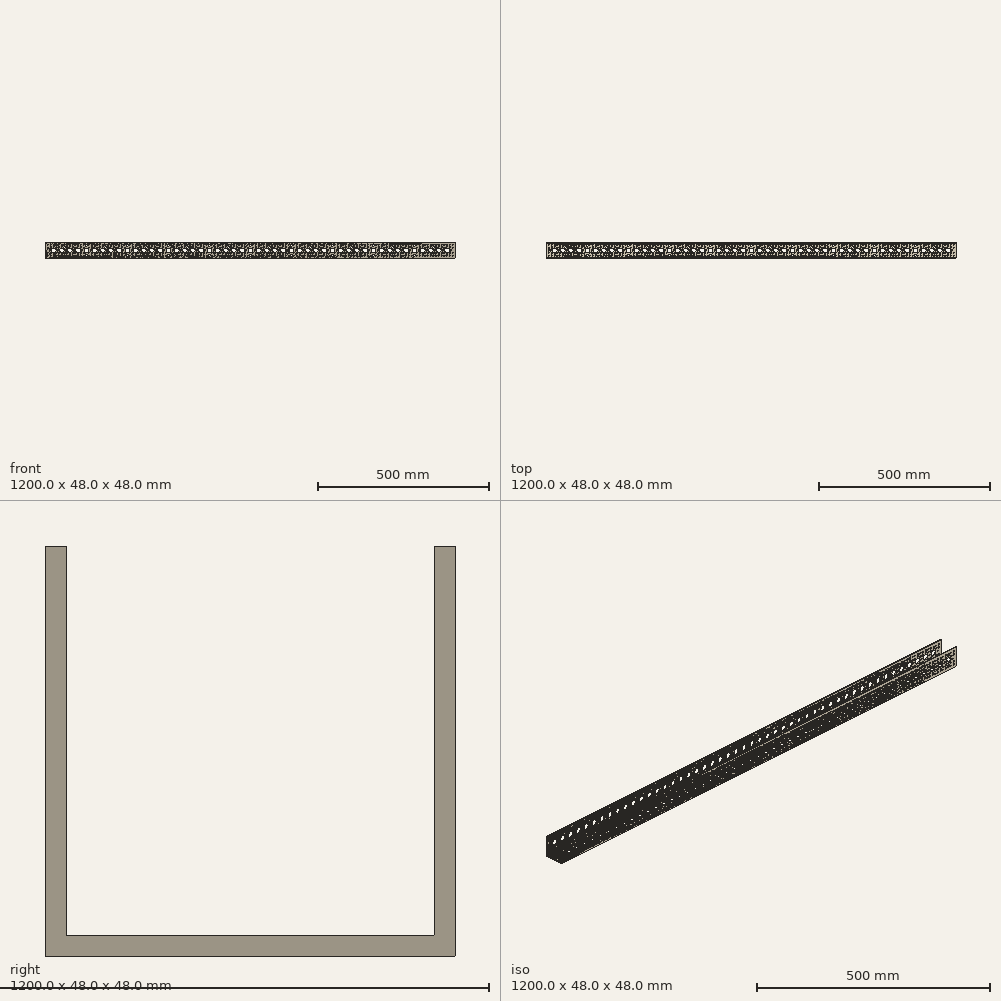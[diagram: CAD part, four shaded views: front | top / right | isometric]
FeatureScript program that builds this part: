
annotation { "Feature Type Name" : "Feature", "Feature Type Description" : "" }
export const myFeature = defineFeature(function(context is Context, id is Id, definition is map)
    precondition{}
    {
        {
            var Q0;
            Q0=qCreatedBy(makeId("Right.planeOp"),FACE);
            var sketch = newSketch(context, id + "F0", { "sketchPlane" : qUnion([Q0])});
            skLineSegment(sketch, "E0.bottom", {"start": v(24, 24) * mm, "end": v(21.5, 24) * mm});
            skLineSegment(sketch, "E0.top", {"start": v(24, -24) * mm, "end": v(-24, -24) * mm});
            skLineSegment(sketch, "E0.left", {"start": v(24, 24) * mm, "end": v(24, -24) * mm});
            skLineSegment(sketch, "E0.right", {"start": v(-24, 24) * mm, "end": v(-24, -24) * mm});
            skPoint(sketch, "E0.middle", {"position": v(0, 0) * mm});
            skLineSegment(sketch, "E1.top", {"start": v(-21.5, -21.5) * mm, "end": v(21.5, -21.5) * mm});
            skLineSegment(sketch, "E1.left", {"start": v(-21.5, 24) * mm, "end": v(-21.5, -21.5) * mm});
            skLineSegment(sketch, "E1.right", {"start": v(21.5, 24) * mm, "end": v(21.5, -21.5) * mm});
            skLineSegment(sketch, "E2.trimOffspring", {"start": v(-21.5, 24) * mm, "end": v(-24, 24) * mm});
            skSolve(sketch);
        }
        {
            var Q0;
            Q0=qSketchRegion(id+"F0",true);
            extrude(context, id + "F1", {"entities" : qUnion([Q0]), "depth" : 48 * mm, "offsetDistance" : 25 * mm});
        }
        {
            var Q0;
            Q0=qSketchRegion(id+"F0",true);
            extrude(context, id + "F2", {"entities" : qUnion([Q0]), "depth" : 72 * mm, "offsetDistance" : 25 * mm});
        }
        {
            var Q0;
            Q0=qSketchRegion(id+"F0",true);
            extrude(context, id + "F3", {"entities" : qUnion([Q0]), "depth" : 96 * mm, "offsetDistance" : 25 * mm});
        }
        {
            var Q0;
            Q0=qSketchRegion(id+"F0",true);
            extrude(context, id + "F4", {"entities" : qUnion([Q0]), "depth" : 120 * mm, "offsetDistance" : 25 * mm});
        }
        {
            var Q0;
            Q0=qSketchRegion(id+"F0",true);
            extrude(context, id + "F5", {"entities" : qUnion([Q0]), "depth" : 144 * mm, "offsetDistance" : 25 * mm});
        }
        {
            var Q0;
            Q0=qSketchRegion(id+"F0",true);
            extrude(context, id + "F6", {"entities" : qUnion([Q0]), "depth" : 192 * mm, "offsetDistance" : 25 * mm});
        }
        {
            var Q0;
            Q0=qSketchRegion(id+"F0",true);
            extrude(context, id + "F7", {"entities" : qUnion([Q0]), "depth" : 240 * mm, "offsetDistance" : 25 * mm});
        }
        {
            var Q0;
            Q0=qSketchRegion(id+"F0",true);
            extrude(context, id + "F8", {"entities" : qUnion([Q0]), "depth" : 288 * mm, "offsetDistance" : 25 * mm});
        }
        {
            var Q0;
            Q0=qSketchRegion(id+"F0",true);
            extrude(context, id + "F9", {"entities" : qUnion([Q0]), "depth" : 336 * mm, "offsetDistance" : 25 * mm});
        }
        {
            var Q0;
            Q0=qSketchRegion(id+"F0",true);
            extrude(context, id + "F10", {"entities" : qUnion([Q0]), "depth" : 384 * mm, "offsetDistance" : 25 * mm});
        }
        {
            var Q0;
            Q0=qSketchRegion(id+"F0",true);
            extrude(context, id + "F11", {"entities" : qUnion([Q0]), "depth" : 432 * mm, "offsetDistance" : 25 * mm});
        }
        {
            var Q0;
            Q0=qSketchRegion(id+"F0",true);
            extrude(context, id + "F12", {"entities" : qUnion([Q0]), "depth" : 528 * mm, "offsetDistance" : 25 * mm});
        }
        {
            var Q0;
            Q0=qSketchRegion(id+"F0",true);
            extrude(context, id + "F13", {"entities" : qUnion([Q0]), "depth" : 624 * mm, "offsetDistance" : 25 * mm});
        }
        {
            var Q0;
            Q0=qSketchRegion(id+"F0",true);
            extrude(context, id + "F14", {"entities" : qUnion([Q0]), "depth" : 720 * mm, "offsetDistance" : 25 * mm});
        }
        {
            var Q0;
            Q0=qSketchRegion(id+"F0",true);
            extrude(context, id + "F15", {"entities" : qUnion([Q0]), "depth" : 816 * mm, "offsetDistance" : 25 * mm});
        }
        {
            var Q0;
            Q0=qSketchRegion(id+"F0",true);
            extrude(context, id + "F16", {"entities" : qUnion([Q0]), "depth" : 912 * mm, "offsetDistance" : 25 * mm});
        }
        {
            var Q0;
            Q0=qSketchRegion(id+"F0",true);
            extrude(context, id + "F17", {"entities" : qUnion([Q0]), "depth" : 1008 * mm, "offsetDistance" : 25 * mm});
        }
        {
            var Q0;
            Q0=qSketchRegion(id+"F0",true);
            extrude(context, id + "F18", {"entities" : qUnion([Q0]), "depth" : 1104 * mm, "offsetDistance" : 25 * mm});
        }
        {
            var Q0;
            Q0=qSketchRegion(id+"F0",true);
            extrude(context, id + "F19", {"entities" : qUnion([Q0]), "depth" : 1200 * mm, "offsetDistance" : 25 * mm});
        }
        {
            var Q0;
            Q0=qCreatedBy(makeId("Front.planeOp"),FACE);
            var sketch = newSketch(context, id + "F20", { "sketchPlane" : qUnion([Q0])});
            skCircle(sketch, "E3", {"center": v(24, 0) * mm, "radius": 7 * mm});
            skLineSegment(sketch, "E4.0", {"start": v(48, 24) * mm, "end": v(0, 24) * mm, "construction": true});
            skLineSegment(sketch, "E5.0", {"start": v(48, -24) * mm, "end": v(0, -24) * mm, "construction": true});
            skLineSegment(sketch, "E6", {"start": v(24, 0) * mm, "end": v(24, 24) * mm, "construction": true});
            skLineSegment(sketch, "E7", {"start": v(24, 24) * mm, "end": v(24, -24) * mm, "construction": true});
            skArc(sketch, "E8", {"start": v(26, 16) * mm, "mid": v(24, 18) * mm, "end": v(22, 16) * mm});
            skArc(sketch, "E9", {"start": v(22, 12) * mm, "mid": v(24, 10) * mm, "end": v(26, 12) * mm});
            skLineSegment(sketch, "E10", {"start": v(22, 16) * mm, "end": v(22, 12) * mm});
            skLineSegment(sketch, "E11", {"start": v(26, 16) * mm, "end": v(26, 12) * mm});
            skArc(sketch, "E12", {"start": v(26, -12) * mm, "mid": v(24, -10) * mm, "end": v(22, -12) * mm});
            skArc(sketch, "E13", {"start": v(22, -16) * mm, "mid": v(24, -18) * mm, "end": v(26, -16) * mm});
            skLineSegment(sketch, "E14", {"start": v(22, -12) * mm, "end": v(22, -16) * mm});
            skLineSegment(sketch, "E15", {"start": v(26, -16) * mm, "end": v(26, -12) * mm});
            skLineSegment(sketch, "E16", {"start": v(0, -24) * mm, "end": v(24, 0) * mm, "construction": true});
            skLineSegment(sketch, "E17", {"start": v(0, 24) * mm, "end": v(24, 0) * mm, "construction": true});
            skArc(sketch, "E18", {"start": v(14.1, -7.07) * mm, "mid": v(14.1, -9.9) * mm, "end": v(16.93, -9.9) * mm});
            skArc(sketch, "E19", {"start": v(17.41, -9.41) * mm, "mid": v(17.41, -6.59) * mm, "end": v(14.59, -6.59) * mm});
            skArc(sketch, "E20", {"start": v(14.59, 6.59) * mm, "mid": v(17.41, 6.59) * mm, "end": v(17.41, 9.41) * mm});
            skArc(sketch, "E21", {"start": v(16.93, 9.9) * mm, "mid": v(14.1, 9.9) * mm, "end": v(14.1, 7.07) * mm});
            skLineSegment(sketch, "E22", {"start": v(15.51, 8.49) * mm, "end": v(16.93, 9.9) * mm, "construction": true});
            skLineSegment(sketch, "E23", {"start": v(15.51, 8.49) * mm, "end": v(14.1, 7.07) * mm, "construction": true});
            skLineSegment(sketch, "E24", {"start": v(17.41, 9.41) * mm, "end": v(14.59, 6.59) * mm, "construction": true});
            skLineSegment(sketch, "E25", {"start": v(16.93, 9.9) * mm, "end": v(17.41, 9.41) * mm});
            skLineSegment(sketch, "E26", {"start": v(14.1, 7.07) * mm, "end": v(14.59, 6.59) * mm});
            skLineSegment(sketch, "E27", {"start": v(14.1, -7.07) * mm, "end": v(16.93, -9.9) * mm, "construction": true});
            skLineSegment(sketch, "E28", {"start": v(14.59, -6.59) * mm, "end": v(17.41, -9.41) * mm, "construction": true});
            skLineSegment(sketch, "E29", {"start": v(14.1, -7.07) * mm, "end": v(14.59, -6.59) * mm});
            skLineSegment(sketch, "E30", {"start": v(16.93, -9.9) * mm, "end": v(17.41, -9.41) * mm});
            skCircle(sketch, "E31", {"center": v(8, 16) * mm, "radius": 2 * mm});
            skCircle(sketch, "E32", {"center": v(8, -16) * mm, "radius": 2 * mm});
            skCircle(sketch, "E33", {"center": v(12, 0) * mm, "radius": 2 * mm});
            skLineSegment(sketch, "E34", {"start": v(8, 16) * mm, "end": v(24, 16) * mm, "construction": true});
            skLineSegment(sketch, "E35", {"start": v(8, -16) * mm, "end": v(24, -16) * mm, "construction": true});
            skCircle(sketch, "E36", {"center": v(16, 16) * mm, "radius": 2 * mm});
            skCircle(sketch, "E37", {"center": v(16, -16) * mm, "radius": 2 * mm});
            skLineSegment(sketch, "E38", {"start": v(0, 0) * mm, "end": v(24, -24) * mm, "construction": true});
            skLineSegment(sketch, "E39", {"start": v(24, 24) * mm, "end": v(0, 0) * mm, "construction": true});
            skArc(sketch, "E40", {"start": v(6.59, 9.41) * mm, "mid": v(6.59, 6.59) * mm, "end": v(9.41, 6.59) * mm});
            skArc(sketch, "E41", {"start": v(9.9, 7.07) * mm, "mid": v(9.9, 9.9) * mm, "end": v(7.07, 9.9) * mm});
            skArc(sketch, "E42", {"start": v(7.07, -9.9) * mm, "mid": v(9.9, -9.9) * mm, "end": v(9.9, -7.07) * mm});
            skArc(sketch, "E43", {"start": v(9.41, -6.59) * mm, "mid": v(6.59, -6.59) * mm, "end": v(6.59, -9.41) * mm});
            skLineSegment(sketch, "E44", {"start": v(7.07, 9.9) * mm, "end": v(9.9, 7.07) * mm, "construction": true});
            skLineSegment(sketch, "E45", {"start": v(6.59, 9.41) * mm, "end": v(9.41, 6.59) * mm, "construction": true});
            skLineSegment(sketch, "E46", {"start": v(9.41, -6.59) * mm, "end": v(6.59, -9.41) * mm, "construction": true});
            skLineSegment(sketch, "E47", {"start": v(9.9, -7.07) * mm, "end": v(7.07, -9.9) * mm, "construction": true});
            skLineSegment(sketch, "E48", {"start": v(9.41, -6.59) * mm, "end": v(9.9, -7.07) * mm});
            skLineSegment(sketch, "E49", {"start": v(6.59, -9.41) * mm, "end": v(7.07, -9.9) * mm});
            skLineSegment(sketch, "E50", {"start": v(7.07, 9.9) * mm, "end": v(6.59, 9.41) * mm});
            skLineSegment(sketch, "E51", {"start": v(9.9, 7.07) * mm, "end": v(9.41, 6.59) * mm});
            skArc(sketch, "E52.1.0.0", {"start": v(50, 16) * mm, "mid": v(48, 18) * mm, "end": v(46, 16) * mm});
            skLineSegment(sketch, "E52.1.0.1", {"start": v(50, 16) * mm, "end": v(50, 12) * mm});
            skLineSegment(sketch, "E52.1.0.2", {"start": v(46, 16) * mm, "end": v(46, 12) * mm});
            skArc(sketch, "E52.1.0.3", {"start": v(46, 12) * mm, "mid": v(48, 10) * mm, "end": v(50, 12) * mm});
            skCircle(sketch, "E52.1.0.4", {"center": v(40, 16) * mm, "radius": 2 * mm});
            skCircle(sketch, "E52.1.0.5", {"center": v(32, 16) * mm, "radius": 2 * mm});
            skArc(sketch, "E52.1.0.6", {"start": v(33.9, 7.07) * mm, "mid": v(33.9, 9.9) * mm, "end": v(31.07, 9.9) * mm});
            skArc(sketch, "E52.1.0.7", {"start": v(30.59, 9.41) * mm, "mid": v(30.59, 6.59) * mm, "end": v(33.41, 6.59) * mm});
            skLineSegment(sketch, "E52.1.0.8", {"start": v(31.07, 9.9) * mm, "end": v(30.59, 9.41) * mm});
            skLineSegment(sketch, "E52.1.0.9", {"start": v(33.9, 7.07) * mm, "end": v(33.41, 6.59) * mm});
            skArc(sketch, "E52.1.0.10", {"start": v(40.93, 9.9) * mm, "mid": v(38.1, 9.9) * mm, "end": v(38.1, 7.07) * mm});
            skLineSegment(sketch, "E52.1.0.11", {"start": v(40.93, 9.9) * mm, "end": v(41.41, 9.41) * mm});
            skArc(sketch, "E52.1.0.12", {"start": v(38.59, 6.59) * mm, "mid": v(41.41, 6.59) * mm, "end": v(41.41, 9.41) * mm});
            skLineSegment(sketch, "E52.1.0.13", {"start": v(38.1, 7.07) * mm, "end": v(38.59, 6.59) * mm});
            skCircle(sketch, "E52.1.0.14", {"center": v(48, 0) * mm, "radius": 7 * mm});
            skArc(sketch, "E52.1.0.15", {"start": v(31.07, -9.9) * mm, "mid": v(33.9, -9.9) * mm, "end": v(33.9, -7.07) * mm});
            skArc(sketch, "E52.1.0.16", {"start": v(33.41, -6.59) * mm, "mid": v(30.59, -6.59) * mm, "end": v(30.59, -9.41) * mm});
            skLineSegment(sketch, "E52.1.0.17", {"start": v(33.41, -6.59) * mm, "end": v(33.9, -7.07) * mm});
            skLineSegment(sketch, "E52.1.0.18", {"start": v(30.59, -9.41) * mm, "end": v(31.07, -9.9) * mm});
            skArc(sketch, "E52.1.0.19", {"start": v(38.1, -7.07) * mm, "mid": v(38.1, -9.9) * mm, "end": v(40.93, -9.9) * mm});
            skLineSegment(sketch, "E52.1.0.20", {"start": v(40.93, -9.9) * mm, "end": v(41.41, -9.41) * mm});
            skArc(sketch, "E52.1.0.21", {"start": v(41.41, -9.41) * mm, "mid": v(41.41, -6.59) * mm, "end": v(38.59, -6.59) * mm});
            skCircle(sketch, "E52.1.0.22", {"center": v(40, -16) * mm, "radius": 2 * mm});
            skCircle(sketch, "E52.1.0.23", {"center": v(32, -16) * mm, "radius": 2 * mm});
            skLineSegment(sketch, "E52.1.0.24", {"start": v(38.1, -7.07) * mm, "end": v(38.59, -6.59) * mm});
            skCircle(sketch, "E52.1.0.25", {"center": v(36, 0) * mm, "radius": 2 * mm});
            skArc(sketch, "E52.1.0.26", {"start": v(50, -12) * mm, "mid": v(48, -10) * mm, "end": v(46, -12) * mm});
            skArc(sketch, "E52.1.0.27", {"start": v(46, -16) * mm, "mid": v(48, -18) * mm, "end": v(50, -16) * mm});
            skLineSegment(sketch, "E52.1.0.28", {"start": v(46, -12) * mm, "end": v(46, -16) * mm});
            skLineSegment(sketch, "E52.1.0.29", {"start": v(50, -16) * mm, "end": v(50, -12) * mm});
            skArc(sketch, "E52.2.0.0", {"start": v(74, 16) * mm, "mid": v(72, 18) * mm, "end": v(70, 16) * mm});
            skLineSegment(sketch, "E52.2.0.1", {"start": v(74, 16) * mm, "end": v(74, 12) * mm});
            skLineSegment(sketch, "E52.2.0.2", {"start": v(70, 16) * mm, "end": v(70, 12) * mm});
            skArc(sketch, "E52.2.0.3", {"start": v(70, 12) * mm, "mid": v(72, 10) * mm, "end": v(74, 12) * mm});
            skCircle(sketch, "E52.2.0.4", {"center": v(64, 16) * mm, "radius": 2 * mm});
            skCircle(sketch, "E52.2.0.5", {"center": v(56, 16) * mm, "radius": 2 * mm});
            skArc(sketch, "E52.2.0.6", {"start": v(57.9, 7.07) * mm, "mid": v(57.9, 9.9) * mm, "end": v(55.07, 9.9) * mm});
            skArc(sketch, "E52.2.0.7", {"start": v(54.59, 9.41) * mm, "mid": v(54.59, 6.59) * mm, "end": v(57.41, 6.59) * mm});
            skLineSegment(sketch, "E52.2.0.8", {"start": v(55.07, 9.9) * mm, "end": v(54.59, 9.41) * mm});
            skLineSegment(sketch, "E52.2.0.9", {"start": v(57.9, 7.07) * mm, "end": v(57.41, 6.59) * mm});
            skArc(sketch, "E52.2.0.10", {"start": v(64.93, 9.9) * mm, "mid": v(62.1, 9.9) * mm, "end": v(62.1, 7.07) * mm});
            skLineSegment(sketch, "E52.2.0.11", {"start": v(64.93, 9.9) * mm, "end": v(65.41, 9.41) * mm});
            skArc(sketch, "E52.2.0.12", {"start": v(62.59, 6.59) * mm, "mid": v(65.41, 6.59) * mm, "end": v(65.41, 9.41) * mm});
            skLineSegment(sketch, "E52.2.0.13", {"start": v(62.1, 7.07) * mm, "end": v(62.59, 6.59) * mm});
            skCircle(sketch, "E52.2.0.14", {"center": v(72, 0) * mm, "radius": 7 * mm});
            skArc(sketch, "E52.2.0.15", {"start": v(55.07, -9.9) * mm, "mid": v(57.9, -9.9) * mm, "end": v(57.9, -7.07) * mm});
            skArc(sketch, "E52.2.0.16", {"start": v(57.41, -6.59) * mm, "mid": v(54.59, -6.59) * mm, "end": v(54.59, -9.41) * mm});
            skLineSegment(sketch, "E52.2.0.17", {"start": v(57.41, -6.59) * mm, "end": v(57.9, -7.07) * mm});
            skLineSegment(sketch, "E52.2.0.18", {"start": v(54.59, -9.41) * mm, "end": v(55.07, -9.9) * mm});
            skArc(sketch, "E52.2.0.19", {"start": v(62.1, -7.07) * mm, "mid": v(62.1, -9.9) * mm, "end": v(64.93, -9.9) * mm});
            skLineSegment(sketch, "E52.2.0.20", {"start": v(64.93, -9.9) * mm, "end": v(65.41, -9.41) * mm});
            skArc(sketch, "E52.2.0.21", {"start": v(65.41, -9.41) * mm, "mid": v(65.41, -6.59) * mm, "end": v(62.59, -6.59) * mm});
            skCircle(sketch, "E52.2.0.22", {"center": v(64, -16) * mm, "radius": 2 * mm});
            skCircle(sketch, "E52.2.0.23", {"center": v(56, -16) * mm, "radius": 2 * mm});
            skLineSegment(sketch, "E52.2.0.24", {"start": v(62.1, -7.07) * mm, "end": v(62.59, -6.59) * mm});
            skCircle(sketch, "E52.2.0.25", {"center": v(60, 0) * mm, "radius": 2 * mm});
            skArc(sketch, "E52.2.0.26", {"start": v(74, -12) * mm, "mid": v(72, -10) * mm, "end": v(70, -12) * mm});
            skArc(sketch, "E52.2.0.27", {"start": v(70, -16) * mm, "mid": v(72, -18) * mm, "end": v(74, -16) * mm});
            skLineSegment(sketch, "E52.2.0.28", {"start": v(70, -12) * mm, "end": v(70, -16) * mm});
            skLineSegment(sketch, "E52.2.0.29", {"start": v(74, -16) * mm, "end": v(74, -12) * mm});
            skArc(sketch, "E52.3.0.0", {"start": v(98, 16) * mm, "mid": v(96, 18) * mm, "end": v(94, 16) * mm});
            skLineSegment(sketch, "E52.3.0.1", {"start": v(98, 16) * mm, "end": v(98, 12) * mm});
            skLineSegment(sketch, "E52.3.0.2", {"start": v(94, 16) * mm, "end": v(94, 12) * mm});
            skArc(sketch, "E52.3.0.3", {"start": v(94, 12) * mm, "mid": v(96, 10) * mm, "end": v(98, 12) * mm});
            skCircle(sketch, "E52.3.0.4", {"center": v(88, 16) * mm, "radius": 2 * mm});
            skCircle(sketch, "E52.3.0.5", {"center": v(80, 16) * mm, "radius": 2 * mm});
            skArc(sketch, "E52.3.0.6", {"start": v(81.9, 7.07) * mm, "mid": v(81.9, 9.9) * mm, "end": v(79.07, 9.9) * mm});
            skArc(sketch, "E52.3.0.7", {"start": v(78.59, 9.41) * mm, "mid": v(78.59, 6.59) * mm, "end": v(81.41, 6.59) * mm});
            skLineSegment(sketch, "E52.3.0.8", {"start": v(79.07, 9.9) * mm, "end": v(78.59, 9.41) * mm});
            skLineSegment(sketch, "E52.3.0.9", {"start": v(81.9, 7.07) * mm, "end": v(81.41, 6.59) * mm});
            skArc(sketch, "E52.3.0.10", {"start": v(88.93, 9.9) * mm, "mid": v(86.1, 9.9) * mm, "end": v(86.1, 7.07) * mm});
            skLineSegment(sketch, "E52.3.0.11", {"start": v(88.93, 9.9) * mm, "end": v(89.41, 9.41) * mm});
            skArc(sketch, "E52.3.0.12", {"start": v(86.59, 6.59) * mm, "mid": v(89.41, 6.59) * mm, "end": v(89.41, 9.41) * mm});
            skLineSegment(sketch, "E52.3.0.13", {"start": v(86.1, 7.07) * mm, "end": v(86.59, 6.59) * mm});
            skCircle(sketch, "E52.3.0.14", {"center": v(96, 0) * mm, "radius": 7 * mm});
            skArc(sketch, "E52.3.0.15", {"start": v(79.07, -9.9) * mm, "mid": v(81.9, -9.9) * mm, "end": v(81.9, -7.07) * mm});
            skArc(sketch, "E52.3.0.16", {"start": v(81.41, -6.59) * mm, "mid": v(78.59, -6.59) * mm, "end": v(78.59, -9.41) * mm});
            skLineSegment(sketch, "E52.3.0.17", {"start": v(81.41, -6.59) * mm, "end": v(81.9, -7.07) * mm});
            skLineSegment(sketch, "E52.3.0.18", {"start": v(78.59, -9.41) * mm, "end": v(79.07, -9.9) * mm});
            skArc(sketch, "E52.3.0.19", {"start": v(86.1, -7.07) * mm, "mid": v(86.1, -9.9) * mm, "end": v(88.93, -9.9) * mm});
            skLineSegment(sketch, "E52.3.0.20", {"start": v(88.93, -9.9) * mm, "end": v(89.41, -9.41) * mm});
            skArc(sketch, "E52.3.0.21", {"start": v(89.41, -9.41) * mm, "mid": v(89.41, -6.59) * mm, "end": v(86.59, -6.59) * mm});
            skCircle(sketch, "E52.3.0.22", {"center": v(88, -16) * mm, "radius": 2 * mm});
            skCircle(sketch, "E52.3.0.23", {"center": v(80, -16) * mm, "radius": 2 * mm});
            skLineSegment(sketch, "E52.3.0.24", {"start": v(86.1, -7.07) * mm, "end": v(86.59, -6.59) * mm});
            skCircle(sketch, "E52.3.0.25", {"center": v(84, 0) * mm, "radius": 2 * mm});
            skArc(sketch, "E52.3.0.26", {"start": v(98, -12) * mm, "mid": v(96, -10) * mm, "end": v(94, -12) * mm});
            skArc(sketch, "E52.3.0.27", {"start": v(94, -16) * mm, "mid": v(96, -18) * mm, "end": v(98, -16) * mm});
            skLineSegment(sketch, "E52.3.0.28", {"start": v(94, -12) * mm, "end": v(94, -16) * mm});
            skLineSegment(sketch, "E52.3.0.29", {"start": v(98, -16) * mm, "end": v(98, -12) * mm});
            skArc(sketch, "E52.4.0.0", {"start": v(122, 16) * mm, "mid": v(120, 18) * mm, "end": v(118, 16) * mm});
            skLineSegment(sketch, "E52.4.0.1", {"start": v(122, 16) * mm, "end": v(122, 12) * mm});
            skLineSegment(sketch, "E52.4.0.2", {"start": v(118, 16) * mm, "end": v(118, 12) * mm});
            skArc(sketch, "E52.4.0.3", {"start": v(118, 12) * mm, "mid": v(120, 10) * mm, "end": v(122, 12) * mm});
            skCircle(sketch, "E52.4.0.4", {"center": v(112, 16) * mm, "radius": 2 * mm});
            skCircle(sketch, "E52.4.0.5", {"center": v(104, 16) * mm, "radius": 2 * mm});
            skArc(sketch, "E52.4.0.6", {"start": v(105.9, 7.07) * mm, "mid": v(105.9, 9.9) * mm, "end": v(103.07, 9.9) * mm});
            skArc(sketch, "E52.4.0.7", {"start": v(102.59, 9.41) * mm, "mid": v(102.59, 6.59) * mm, "end": v(105.41, 6.59) * mm});
            skLineSegment(sketch, "E52.4.0.8", {"start": v(103.07, 9.9) * mm, "end": v(102.59, 9.41) * mm});
            skLineSegment(sketch, "E52.4.0.9", {"start": v(105.9, 7.07) * mm, "end": v(105.41, 6.59) * mm});
            skArc(sketch, "E52.4.0.10", {"start": v(112.93, 9.9) * mm, "mid": v(110.1, 9.9) * mm, "end": v(110.1, 7.07) * mm});
            skLineSegment(sketch, "E52.4.0.11", {"start": v(112.93, 9.9) * mm, "end": v(113.41, 9.41) * mm});
            skArc(sketch, "E52.4.0.12", {"start": v(110.59, 6.59) * mm, "mid": v(113.41, 6.59) * mm, "end": v(113.41, 9.41) * mm});
            skLineSegment(sketch, "E52.4.0.13", {"start": v(110.1, 7.07) * mm, "end": v(110.59, 6.59) * mm});
            skCircle(sketch, "E52.4.0.14", {"center": v(120, 0) * mm, "radius": 7 * mm});
            skArc(sketch, "E52.4.0.15", {"start": v(103.07, -9.9) * mm, "mid": v(105.9, -9.9) * mm, "end": v(105.9, -7.07) * mm});
            skArc(sketch, "E52.4.0.16", {"start": v(105.41, -6.59) * mm, "mid": v(102.59, -6.59) * mm, "end": v(102.59, -9.41) * mm});
            skLineSegment(sketch, "E52.4.0.17", {"start": v(105.41, -6.59) * mm, "end": v(105.9, -7.07) * mm});
            skLineSegment(sketch, "E52.4.0.18", {"start": v(102.59, -9.41) * mm, "end": v(103.07, -9.9) * mm});
            skArc(sketch, "E52.4.0.19", {"start": v(110.1, -7.07) * mm, "mid": v(110.1, -9.9) * mm, "end": v(112.93, -9.9) * mm});
            skLineSegment(sketch, "E52.4.0.20", {"start": v(112.93, -9.9) * mm, "end": v(113.41, -9.41) * mm});
            skArc(sketch, "E52.4.0.21", {"start": v(113.41, -9.41) * mm, "mid": v(113.41, -6.59) * mm, "end": v(110.59, -6.59) * mm});
            skCircle(sketch, "E52.4.0.22", {"center": v(112, -16) * mm, "radius": 2 * mm});
            skCircle(sketch, "E52.4.0.23", {"center": v(104, -16) * mm, "radius": 2 * mm});
            skLineSegment(sketch, "E52.4.0.24", {"start": v(110.1, -7.07) * mm, "end": v(110.59, -6.59) * mm});
            skCircle(sketch, "E52.4.0.25", {"center": v(108, 0) * mm, "radius": 2 * mm});
            skArc(sketch, "E52.4.0.26", {"start": v(122, -12) * mm, "mid": v(120, -10) * mm, "end": v(118, -12) * mm});
            skArc(sketch, "E52.4.0.27", {"start": v(118, -16) * mm, "mid": v(120, -18) * mm, "end": v(122, -16) * mm});
            skLineSegment(sketch, "E52.4.0.28", {"start": v(118, -12) * mm, "end": v(118, -16) * mm});
            skLineSegment(sketch, "E52.4.0.29", {"start": v(122, -16) * mm, "end": v(122, -12) * mm});
            skArc(sketch, "E52.5.0.0", {"start": v(146, 16) * mm, "mid": v(144, 18) * mm, "end": v(142, 16) * mm});
            skLineSegment(sketch, "E52.5.0.1", {"start": v(146, 16) * mm, "end": v(146, 12) * mm});
            skLineSegment(sketch, "E52.5.0.2", {"start": v(142, 16) * mm, "end": v(142, 12) * mm});
            skArc(sketch, "E52.5.0.3", {"start": v(142, 12) * mm, "mid": v(144, 10) * mm, "end": v(146, 12) * mm});
            skCircle(sketch, "E52.5.0.4", {"center": v(136, 16) * mm, "radius": 2 * mm});
            skCircle(sketch, "E52.5.0.5", {"center": v(128, 16) * mm, "radius": 2 * mm});
            skArc(sketch, "E52.5.0.6", {"start": v(129.9, 7.07) * mm, "mid": v(129.9, 9.9) * mm, "end": v(127.07, 9.9) * mm});
            skArc(sketch, "E52.5.0.7", {"start": v(126.59, 9.41) * mm, "mid": v(126.59, 6.59) * mm, "end": v(129.41, 6.59) * mm});
            skLineSegment(sketch, "E52.5.0.8", {"start": v(127.07, 9.9) * mm, "end": v(126.59, 9.41) * mm});
            skLineSegment(sketch, "E52.5.0.9", {"start": v(129.9, 7.07) * mm, "end": v(129.41, 6.59) * mm});
            skArc(sketch, "E52.5.0.10", {"start": v(136.93, 9.9) * mm, "mid": v(134.1, 9.9) * mm, "end": v(134.1, 7.07) * mm});
            skLineSegment(sketch, "E52.5.0.11", {"start": v(136.93, 9.9) * mm, "end": v(137.41, 9.41) * mm});
            skArc(sketch, "E52.5.0.12", {"start": v(134.59, 6.59) * mm, "mid": v(137.41, 6.59) * mm, "end": v(137.41, 9.41) * mm});
            skLineSegment(sketch, "E52.5.0.13", {"start": v(134.1, 7.07) * mm, "end": v(134.59, 6.59) * mm});
            skCircle(sketch, "E52.5.0.14", {"center": v(144, 0) * mm, "radius": 7 * mm});
            skArc(sketch, "E52.5.0.15", {"start": v(127.07, -9.9) * mm, "mid": v(129.9, -9.9) * mm, "end": v(129.9, -7.07) * mm});
            skArc(sketch, "E52.5.0.16", {"start": v(129.41, -6.59) * mm, "mid": v(126.59, -6.59) * mm, "end": v(126.59, -9.41) * mm});
            skLineSegment(sketch, "E52.5.0.17", {"start": v(129.41, -6.59) * mm, "end": v(129.9, -7.07) * mm});
            skLineSegment(sketch, "E52.5.0.18", {"start": v(126.59, -9.41) * mm, "end": v(127.07, -9.9) * mm});
            skArc(sketch, "E52.5.0.19", {"start": v(134.1, -7.07) * mm, "mid": v(134.1, -9.9) * mm, "end": v(136.93, -9.9) * mm});
            skLineSegment(sketch, "E52.5.0.20", {"start": v(136.93, -9.9) * mm, "end": v(137.41, -9.41) * mm});
            skArc(sketch, "E52.5.0.21", {"start": v(137.41, -9.41) * mm, "mid": v(137.41, -6.59) * mm, "end": v(134.59, -6.59) * mm});
            skCircle(sketch, "E52.5.0.22", {"center": v(136, -16) * mm, "radius": 2 * mm});
            skCircle(sketch, "E52.5.0.23", {"center": v(128, -16) * mm, "radius": 2 * mm});
            skLineSegment(sketch, "E52.5.0.24", {"start": v(134.1, -7.07) * mm, "end": v(134.59, -6.59) * mm});
            skCircle(sketch, "E52.5.0.25", {"center": v(132, 0) * mm, "radius": 2 * mm});
            skArc(sketch, "E52.5.0.26", {"start": v(146, -12) * mm, "mid": v(144, -10) * mm, "end": v(142, -12) * mm});
            skArc(sketch, "E52.5.0.27", {"start": v(142, -16) * mm, "mid": v(144, -18) * mm, "end": v(146, -16) * mm});
            skLineSegment(sketch, "E52.5.0.28", {"start": v(142, -12) * mm, "end": v(142, -16) * mm});
            skLineSegment(sketch, "E52.5.0.29", {"start": v(146, -16) * mm, "end": v(146, -12) * mm});
            skArc(sketch, "E52.6.0.0", {"start": v(170, 16) * mm, "mid": v(168, 18) * mm, "end": v(166, 16) * mm});
            skLineSegment(sketch, "E52.6.0.1", {"start": v(170, 16) * mm, "end": v(170, 12) * mm});
            skLineSegment(sketch, "E52.6.0.2", {"start": v(166, 16) * mm, "end": v(166, 12) * mm});
            skArc(sketch, "E52.6.0.3", {"start": v(166, 12) * mm, "mid": v(168, 10) * mm, "end": v(170, 12) * mm});
            skCircle(sketch, "E52.6.0.4", {"center": v(160, 16) * mm, "radius": 2 * mm});
            skCircle(sketch, "E52.6.0.5", {"center": v(152, 16) * mm, "radius": 2 * mm});
            skArc(sketch, "E52.6.0.6", {"start": v(153.9, 7.07) * mm, "mid": v(153.9, 9.9) * mm, "end": v(151.07, 9.9) * mm});
            skArc(sketch, "E52.6.0.7", {"start": v(150.59, 9.41) * mm, "mid": v(150.59, 6.59) * mm, "end": v(153.41, 6.59) * mm});
            skLineSegment(sketch, "E52.6.0.8", {"start": v(151.07, 9.9) * mm, "end": v(150.59, 9.41) * mm});
            skLineSegment(sketch, "E52.6.0.9", {"start": v(153.9, 7.07) * mm, "end": v(153.41, 6.59) * mm});
            skArc(sketch, "E52.6.0.10", {"start": v(160.93, 9.9) * mm, "mid": v(158.1, 9.9) * mm, "end": v(158.1, 7.07) * mm});
            skLineSegment(sketch, "E52.6.0.11", {"start": v(160.93, 9.9) * mm, "end": v(161.41, 9.41) * mm});
            skArc(sketch, "E52.6.0.12", {"start": v(158.59, 6.59) * mm, "mid": v(161.41, 6.59) * mm, "end": v(161.41, 9.41) * mm});
            skLineSegment(sketch, "E52.6.0.13", {"start": v(158.1, 7.07) * mm, "end": v(158.59, 6.59) * mm});
            skCircle(sketch, "E52.6.0.14", {"center": v(168, 0) * mm, "radius": 7 * mm});
            skArc(sketch, "E52.6.0.15", {"start": v(151.07, -9.9) * mm, "mid": v(153.9, -9.9) * mm, "end": v(153.9, -7.07) * mm});
            skArc(sketch, "E52.6.0.16", {"start": v(153.41, -6.59) * mm, "mid": v(150.59, -6.59) * mm, "end": v(150.59, -9.41) * mm});
            skLineSegment(sketch, "E52.6.0.17", {"start": v(153.41, -6.59) * mm, "end": v(153.9, -7.07) * mm});
            skLineSegment(sketch, "E52.6.0.18", {"start": v(150.59, -9.41) * mm, "end": v(151.07, -9.9) * mm});
            skArc(sketch, "E52.6.0.19", {"start": v(158.1, -7.07) * mm, "mid": v(158.1, -9.9) * mm, "end": v(160.93, -9.9) * mm});
            skLineSegment(sketch, "E52.6.0.20", {"start": v(160.93, -9.9) * mm, "end": v(161.41, -9.41) * mm});
            skArc(sketch, "E52.6.0.21", {"start": v(161.41, -9.41) * mm, "mid": v(161.41, -6.59) * mm, "end": v(158.59, -6.59) * mm});
            skCircle(sketch, "E52.6.0.22", {"center": v(160, -16) * mm, "radius": 2 * mm});
            skCircle(sketch, "E52.6.0.23", {"center": v(152, -16) * mm, "radius": 2 * mm});
            skLineSegment(sketch, "E52.6.0.24", {"start": v(158.1, -7.07) * mm, "end": v(158.59, -6.59) * mm});
            skCircle(sketch, "E52.6.0.25", {"center": v(156, 0) * mm, "radius": 2 * mm});
            skArc(sketch, "E52.6.0.26", {"start": v(170, -12) * mm, "mid": v(168, -10) * mm, "end": v(166, -12) * mm});
            skArc(sketch, "E52.6.0.27", {"start": v(166, -16) * mm, "mid": v(168, -18) * mm, "end": v(170, -16) * mm});
            skLineSegment(sketch, "E52.6.0.28", {"start": v(166, -12) * mm, "end": v(166, -16) * mm});
            skLineSegment(sketch, "E52.6.0.29", {"start": v(170, -16) * mm, "end": v(170, -12) * mm});
            skArc(sketch, "E52.7.0.0", {"start": v(194, 16) * mm, "mid": v(192, 18) * mm, "end": v(190, 16) * mm});
            skLineSegment(sketch, "E52.7.0.1", {"start": v(194, 16) * mm, "end": v(194, 12) * mm});
            skLineSegment(sketch, "E52.7.0.2", {"start": v(190, 16) * mm, "end": v(190, 12) * mm});
            skArc(sketch, "E52.7.0.3", {"start": v(190, 12) * mm, "mid": v(192, 10) * mm, "end": v(194, 12) * mm});
            skCircle(sketch, "E52.7.0.4", {"center": v(184, 16) * mm, "radius": 2 * mm});
            skCircle(sketch, "E52.7.0.5", {"center": v(176, 16) * mm, "radius": 2 * mm});
            skArc(sketch, "E52.7.0.6", {"start": v(177.9, 7.07) * mm, "mid": v(177.9, 9.9) * mm, "end": v(175.07, 9.9) * mm});
            skArc(sketch, "E52.7.0.7", {"start": v(174.59, 9.41) * mm, "mid": v(174.59, 6.59) * mm, "end": v(177.41, 6.59) * mm});
            skLineSegment(sketch, "E52.7.0.8", {"start": v(175.07, 9.9) * mm, "end": v(174.59, 9.41) * mm});
            skLineSegment(sketch, "E52.7.0.9", {"start": v(177.9, 7.07) * mm, "end": v(177.41, 6.59) * mm});
            skArc(sketch, "E52.7.0.10", {"start": v(184.93, 9.9) * mm, "mid": v(182.1, 9.9) * mm, "end": v(182.1, 7.07) * mm});
            skLineSegment(sketch, "E52.7.0.11", {"start": v(184.93, 9.9) * mm, "end": v(185.41, 9.41) * mm});
            skArc(sketch, "E52.7.0.12", {"start": v(182.59, 6.59) * mm, "mid": v(185.41, 6.59) * mm, "end": v(185.41, 9.41) * mm});
            skLineSegment(sketch, "E52.7.0.13", {"start": v(182.1, 7.07) * mm, "end": v(182.59, 6.59) * mm});
            skCircle(sketch, "E52.7.0.14", {"center": v(192, 0) * mm, "radius": 7 * mm});
            skArc(sketch, "E52.7.0.15", {"start": v(175.07, -9.9) * mm, "mid": v(177.9, -9.9) * mm, "end": v(177.9, -7.07) * mm});
            skArc(sketch, "E52.7.0.16", {"start": v(177.41, -6.59) * mm, "mid": v(174.59, -6.59) * mm, "end": v(174.59, -9.41) * mm});
            skLineSegment(sketch, "E52.7.0.17", {"start": v(177.41, -6.59) * mm, "end": v(177.9, -7.07) * mm});
            skLineSegment(sketch, "E52.7.0.18", {"start": v(174.59, -9.41) * mm, "end": v(175.07, -9.9) * mm});
            skArc(sketch, "E52.7.0.19", {"start": v(182.1, -7.07) * mm, "mid": v(182.1, -9.9) * mm, "end": v(184.93, -9.9) * mm});
            skLineSegment(sketch, "E52.7.0.20", {"start": v(184.93, -9.9) * mm, "end": v(185.41, -9.41) * mm});
            skArc(sketch, "E52.7.0.21", {"start": v(185.41, -9.41) * mm, "mid": v(185.41, -6.59) * mm, "end": v(182.59, -6.59) * mm});
            skCircle(sketch, "E52.7.0.22", {"center": v(184, -16) * mm, "radius": 2 * mm});
            skCircle(sketch, "E52.7.0.23", {"center": v(176, -16) * mm, "radius": 2 * mm});
            skLineSegment(sketch, "E52.7.0.24", {"start": v(182.1, -7.07) * mm, "end": v(182.59, -6.59) * mm});
            skCircle(sketch, "E52.7.0.25", {"center": v(180, 0) * mm, "radius": 2 * mm});
            skArc(sketch, "E52.7.0.26", {"start": v(194, -12) * mm, "mid": v(192, -10) * mm, "end": v(190, -12) * mm});
            skArc(sketch, "E52.7.0.27", {"start": v(190, -16) * mm, "mid": v(192, -18) * mm, "end": v(194, -16) * mm});
            skLineSegment(sketch, "E52.7.0.28", {"start": v(190, -12) * mm, "end": v(190, -16) * mm});
            skLineSegment(sketch, "E52.7.0.29", {"start": v(194, -16) * mm, "end": v(194, -12) * mm});
            skArc(sketch, "E52.8.0.0", {"start": v(218, 16) * mm, "mid": v(216, 18) * mm, "end": v(214, 16) * mm});
            skLineSegment(sketch, "E52.8.0.1", {"start": v(218, 16) * mm, "end": v(218, 12) * mm});
            skLineSegment(sketch, "E52.8.0.2", {"start": v(214, 16) * mm, "end": v(214, 12) * mm});
            skArc(sketch, "E52.8.0.3", {"start": v(214, 12) * mm, "mid": v(216, 10) * mm, "end": v(218, 12) * mm});
            skCircle(sketch, "E52.8.0.4", {"center": v(208, 16) * mm, "radius": 2 * mm});
            skCircle(sketch, "E52.8.0.5", {"center": v(200, 16) * mm, "radius": 2 * mm});
            skArc(sketch, "E52.8.0.6", {"start": v(201.9, 7.07) * mm, "mid": v(201.9, 9.9) * mm, "end": v(199.07, 9.9) * mm});
            skArc(sketch, "E52.8.0.7", {"start": v(198.59, 9.41) * mm, "mid": v(198.59, 6.59) * mm, "end": v(201.41, 6.59) * mm});
            skLineSegment(sketch, "E52.8.0.8", {"start": v(199.07, 9.9) * mm, "end": v(198.59, 9.41) * mm});
            skLineSegment(sketch, "E52.8.0.9", {"start": v(201.9, 7.07) * mm, "end": v(201.41, 6.59) * mm});
            skArc(sketch, "E52.8.0.10", {"start": v(208.93, 9.9) * mm, "mid": v(206.1, 9.9) * mm, "end": v(206.1, 7.07) * mm});
            skLineSegment(sketch, "E52.8.0.11", {"start": v(208.93, 9.9) * mm, "end": v(209.41, 9.41) * mm});
            skArc(sketch, "E52.8.0.12", {"start": v(206.59, 6.59) * mm, "mid": v(209.41, 6.59) * mm, "end": v(209.41, 9.41) * mm});
            skLineSegment(sketch, "E52.8.0.13", {"start": v(206.1, 7.07) * mm, "end": v(206.59, 6.59) * mm});
            skCircle(sketch, "E52.8.0.14", {"center": v(216, 0) * mm, "radius": 7 * mm});
            skArc(sketch, "E52.8.0.15", {"start": v(199.07, -9.9) * mm, "mid": v(201.9, -9.9) * mm, "end": v(201.9, -7.07) * mm});
            skArc(sketch, "E52.8.0.16", {"start": v(201.41, -6.59) * mm, "mid": v(198.59, -6.59) * mm, "end": v(198.59, -9.41) * mm});
            skLineSegment(sketch, "E52.8.0.17", {"start": v(201.41, -6.59) * mm, "end": v(201.9, -7.07) * mm});
            skLineSegment(sketch, "E52.8.0.18", {"start": v(198.59, -9.41) * mm, "end": v(199.07, -9.9) * mm});
            skArc(sketch, "E52.8.0.19", {"start": v(206.1, -7.07) * mm, "mid": v(206.1, -9.9) * mm, "end": v(208.93, -9.9) * mm});
            skLineSegment(sketch, "E52.8.0.20", {"start": v(208.93, -9.9) * mm, "end": v(209.41, -9.41) * mm});
            skArc(sketch, "E52.8.0.21", {"start": v(209.41, -9.41) * mm, "mid": v(209.41, -6.59) * mm, "end": v(206.59, -6.59) * mm});
            skCircle(sketch, "E52.8.0.22", {"center": v(208, -16) * mm, "radius": 2 * mm});
            skCircle(sketch, "E52.8.0.23", {"center": v(200, -16) * mm, "radius": 2 * mm});
            skLineSegment(sketch, "E52.8.0.24", {"start": v(206.1, -7.07) * mm, "end": v(206.59, -6.59) * mm});
            skCircle(sketch, "E52.8.0.25", {"center": v(204, 0) * mm, "radius": 2 * mm});
            skArc(sketch, "E52.8.0.26", {"start": v(218, -12) * mm, "mid": v(216, -10) * mm, "end": v(214, -12) * mm});
            skArc(sketch, "E52.8.0.27", {"start": v(214, -16) * mm, "mid": v(216, -18) * mm, "end": v(218, -16) * mm});
            skLineSegment(sketch, "E52.8.0.28", {"start": v(214, -12) * mm, "end": v(214, -16) * mm});
            skLineSegment(sketch, "E52.8.0.29", {"start": v(218, -16) * mm, "end": v(218, -12) * mm});
            skArc(sketch, "E52.9.0.0", {"start": v(242, 16) * mm, "mid": v(240, 18) * mm, "end": v(238, 16) * mm});
            skLineSegment(sketch, "E52.9.0.1", {"start": v(242, 16) * mm, "end": v(242, 12) * mm});
            skLineSegment(sketch, "E52.9.0.2", {"start": v(238, 16) * mm, "end": v(238, 12) * mm});
            skArc(sketch, "E52.9.0.3", {"start": v(238, 12) * mm, "mid": v(240, 10) * mm, "end": v(242, 12) * mm});
            skCircle(sketch, "E52.9.0.4", {"center": v(232, 16) * mm, "radius": 2 * mm});
            skCircle(sketch, "E52.9.0.5", {"center": v(224, 16) * mm, "radius": 2 * mm});
            skArc(sketch, "E52.9.0.6", {"start": v(225.9, 7.07) * mm, "mid": v(225.9, 9.9) * mm, "end": v(223.07, 9.9) * mm});
            skArc(sketch, "E52.9.0.7", {"start": v(222.59, 9.41) * mm, "mid": v(222.59, 6.59) * mm, "end": v(225.41, 6.59) * mm});
            skLineSegment(sketch, "E52.9.0.8", {"start": v(223.07, 9.9) * mm, "end": v(222.59, 9.41) * mm});
            skLineSegment(sketch, "E52.9.0.9", {"start": v(225.9, 7.07) * mm, "end": v(225.41, 6.59) * mm});
            skArc(sketch, "E52.9.0.10", {"start": v(232.93, 9.9) * mm, "mid": v(230.1, 9.9) * mm, "end": v(230.1, 7.07) * mm});
            skLineSegment(sketch, "E52.9.0.11", {"start": v(232.93, 9.9) * mm, "end": v(233.41, 9.41) * mm});
            skArc(sketch, "E52.9.0.12", {"start": v(230.59, 6.59) * mm, "mid": v(233.41, 6.59) * mm, "end": v(233.41, 9.41) * mm});
            skLineSegment(sketch, "E52.9.0.13", {"start": v(230.1, 7.07) * mm, "end": v(230.59, 6.59) * mm});
            skCircle(sketch, "E52.9.0.14", {"center": v(240, 0) * mm, "radius": 7 * mm});
            skArc(sketch, "E52.9.0.15", {"start": v(223.07, -9.9) * mm, "mid": v(225.9, -9.9) * mm, "end": v(225.9, -7.07) * mm});
            skArc(sketch, "E52.9.0.16", {"start": v(225.41, -6.59) * mm, "mid": v(222.59, -6.59) * mm, "end": v(222.59, -9.41) * mm});
            skLineSegment(sketch, "E52.9.0.17", {"start": v(225.41, -6.59) * mm, "end": v(225.9, -7.07) * mm});
            skLineSegment(sketch, "E52.9.0.18", {"start": v(222.59, -9.41) * mm, "end": v(223.07, -9.9) * mm});
            skArc(sketch, "E52.9.0.19", {"start": v(230.1, -7.07) * mm, "mid": v(230.1, -9.9) * mm, "end": v(232.93, -9.9) * mm});
            skLineSegment(sketch, "E52.9.0.20", {"start": v(232.93, -9.9) * mm, "end": v(233.41, -9.41) * mm});
            skArc(sketch, "E52.9.0.21", {"start": v(233.41, -9.41) * mm, "mid": v(233.41, -6.59) * mm, "end": v(230.59, -6.59) * mm});
            skCircle(sketch, "E52.9.0.22", {"center": v(232, -16) * mm, "radius": 2 * mm});
            skCircle(sketch, "E52.9.0.23", {"center": v(224, -16) * mm, "radius": 2 * mm});
            skLineSegment(sketch, "E52.9.0.24", {"start": v(230.1, -7.07) * mm, "end": v(230.59, -6.59) * mm});
            skCircle(sketch, "E52.9.0.25", {"center": v(228, 0) * mm, "radius": 2 * mm});
            skArc(sketch, "E52.9.0.26", {"start": v(242, -12) * mm, "mid": v(240, -10) * mm, "end": v(238, -12) * mm});
            skArc(sketch, "E52.9.0.27", {"start": v(238, -16) * mm, "mid": v(240, -18) * mm, "end": v(242, -16) * mm});
            skLineSegment(sketch, "E52.9.0.28", {"start": v(238, -12) * mm, "end": v(238, -16) * mm});
            skLineSegment(sketch, "E52.9.0.29", {"start": v(242, -16) * mm, "end": v(242, -12) * mm});
            skArc(sketch, "E52.10.0.0", {"start": v(266, 16) * mm, "mid": v(264, 18) * mm, "end": v(262, 16) * mm});
            skLineSegment(sketch, "E52.10.0.1", {"start": v(266, 16) * mm, "end": v(266, 12) * mm});
            skLineSegment(sketch, "E52.10.0.2", {"start": v(262, 16) * mm, "end": v(262, 12) * mm});
            skArc(sketch, "E52.10.0.3", {"start": v(262, 12) * mm, "mid": v(264, 10) * mm, "end": v(266, 12) * mm});
            skCircle(sketch, "E52.10.0.4", {"center": v(256, 16) * mm, "radius": 2 * mm});
            skCircle(sketch, "E52.10.0.5", {"center": v(248, 16) * mm, "radius": 2 * mm});
            skArc(sketch, "E52.10.0.6", {"start": v(249.9, 7.07) * mm, "mid": v(249.9, 9.9) * mm, "end": v(247.07, 9.9) * mm});
            skArc(sketch, "E52.10.0.7", {"start": v(246.59, 9.41) * mm, "mid": v(246.59, 6.59) * mm, "end": v(249.41, 6.59) * mm});
            skLineSegment(sketch, "E52.10.0.8", {"start": v(247.07, 9.9) * mm, "end": v(246.59, 9.41) * mm});
            skLineSegment(sketch, "E52.10.0.9", {"start": v(249.9, 7.07) * mm, "end": v(249.41, 6.59) * mm});
            skArc(sketch, "E52.10.0.10", {"start": v(256.93, 9.9) * mm, "mid": v(254.1, 9.9) * mm, "end": v(254.1, 7.07) * mm});
            skLineSegment(sketch, "E52.10.0.11", {"start": v(256.93, 9.9) * mm, "end": v(257.41, 9.41) * mm});
            skArc(sketch, "E52.10.0.12", {"start": v(254.59, 6.59) * mm, "mid": v(257.41, 6.59) * mm, "end": v(257.41, 9.41) * mm});
            skLineSegment(sketch, "E52.10.0.13", {"start": v(254.1, 7.07) * mm, "end": v(254.59, 6.59) * mm});
            skCircle(sketch, "E52.10.0.14", {"center": v(264, 0) * mm, "radius": 7 * mm});
            skArc(sketch, "E52.10.0.15", {"start": v(247.07, -9.9) * mm, "mid": v(249.9, -9.9) * mm, "end": v(249.9, -7.07) * mm});
            skArc(sketch, "E52.10.0.16", {"start": v(249.41, -6.59) * mm, "mid": v(246.59, -6.59) * mm, "end": v(246.59, -9.41) * mm});
            skLineSegment(sketch, "E52.10.0.17", {"start": v(249.41, -6.59) * mm, "end": v(249.9, -7.07) * mm});
            skLineSegment(sketch, "E52.10.0.18", {"start": v(246.59, -9.41) * mm, "end": v(247.07, -9.9) * mm});
            skArc(sketch, "E52.10.0.19", {"start": v(254.1, -7.07) * mm, "mid": v(254.1, -9.9) * mm, "end": v(256.93, -9.9) * mm});
            skLineSegment(sketch, "E52.10.0.20", {"start": v(256.93, -9.9) * mm, "end": v(257.41, -9.41) * mm});
            skArc(sketch, "E52.10.0.21", {"start": v(257.41, -9.41) * mm, "mid": v(257.41, -6.59) * mm, "end": v(254.59, -6.59) * mm});
            skCircle(sketch, "E52.10.0.22", {"center": v(256, -16) * mm, "radius": 2 * mm});
            skCircle(sketch, "E52.10.0.23", {"center": v(248, -16) * mm, "radius": 2 * mm});
            skLineSegment(sketch, "E52.10.0.24", {"start": v(254.1, -7.07) * mm, "end": v(254.59, -6.59) * mm});
            skCircle(sketch, "E52.10.0.25", {"center": v(252, 0) * mm, "radius": 2 * mm});
            skArc(sketch, "E52.10.0.26", {"start": v(266, -12) * mm, "mid": v(264, -10) * mm, "end": v(262, -12) * mm});
            skArc(sketch, "E52.10.0.27", {"start": v(262, -16) * mm, "mid": v(264, -18) * mm, "end": v(266, -16) * mm});
            skLineSegment(sketch, "E52.10.0.28", {"start": v(262, -12) * mm, "end": v(262, -16) * mm});
            skLineSegment(sketch, "E52.10.0.29", {"start": v(266, -16) * mm, "end": v(266, -12) * mm});
            skArc(sketch, "E52.11.0.0", {"start": v(290, 16) * mm, "mid": v(288, 18) * mm, "end": v(286, 16) * mm});
            skLineSegment(sketch, "E52.11.0.1", {"start": v(290, 16) * mm, "end": v(290, 12) * mm});
            skLineSegment(sketch, "E52.11.0.2", {"start": v(286, 16) * mm, "end": v(286, 12) * mm});
            skArc(sketch, "E52.11.0.3", {"start": v(286, 12) * mm, "mid": v(288, 10) * mm, "end": v(290, 12) * mm});
            skCircle(sketch, "E52.11.0.4", {"center": v(280, 16) * mm, "radius": 2 * mm});
            skCircle(sketch, "E52.11.0.5", {"center": v(272, 16) * mm, "radius": 2 * mm});
            skArc(sketch, "E52.11.0.6", {"start": v(273.9, 7.07) * mm, "mid": v(273.9, 9.9) * mm, "end": v(271.07, 9.9) * mm});
            skArc(sketch, "E52.11.0.7", {"start": v(270.59, 9.41) * mm, "mid": v(270.59, 6.59) * mm, "end": v(273.41, 6.59) * mm});
            skLineSegment(sketch, "E52.11.0.8", {"start": v(271.07, 9.9) * mm, "end": v(270.59, 9.41) * mm});
            skLineSegment(sketch, "E52.11.0.9", {"start": v(273.9, 7.07) * mm, "end": v(273.41, 6.59) * mm});
            skArc(sketch, "E52.11.0.10", {"start": v(280.93, 9.9) * mm, "mid": v(278.1, 9.9) * mm, "end": v(278.1, 7.07) * mm});
            skLineSegment(sketch, "E52.11.0.11", {"start": v(280.93, 9.9) * mm, "end": v(281.41, 9.41) * mm});
            skArc(sketch, "E52.11.0.12", {"start": v(278.59, 6.59) * mm, "mid": v(281.41, 6.59) * mm, "end": v(281.41, 9.41) * mm});
            skLineSegment(sketch, "E52.11.0.13", {"start": v(278.1, 7.07) * mm, "end": v(278.59, 6.59) * mm});
            skCircle(sketch, "E52.11.0.14", {"center": v(288, 0) * mm, "radius": 7 * mm});
            skArc(sketch, "E52.11.0.15", {"start": v(271.07, -9.9) * mm, "mid": v(273.9, -9.9) * mm, "end": v(273.9, -7.07) * mm});
            skArc(sketch, "E52.11.0.16", {"start": v(273.41, -6.59) * mm, "mid": v(270.59, -6.59) * mm, "end": v(270.59, -9.41) * mm});
            skLineSegment(sketch, "E52.11.0.17", {"start": v(273.41, -6.59) * mm, "end": v(273.9, -7.07) * mm});
            skLineSegment(sketch, "E52.11.0.18", {"start": v(270.59, -9.41) * mm, "end": v(271.07, -9.9) * mm});
            skArc(sketch, "E52.11.0.19", {"start": v(278.1, -7.07) * mm, "mid": v(278.1, -9.9) * mm, "end": v(280.93, -9.9) * mm});
            skLineSegment(sketch, "E52.11.0.20", {"start": v(280.93, -9.9) * mm, "end": v(281.41, -9.41) * mm});
            skArc(sketch, "E52.11.0.21", {"start": v(281.41, -9.41) * mm, "mid": v(281.41, -6.59) * mm, "end": v(278.59, -6.59) * mm});
            skCircle(sketch, "E52.11.0.22", {"center": v(280, -16) * mm, "radius": 2 * mm});
            skCircle(sketch, "E52.11.0.23", {"center": v(272, -16) * mm, "radius": 2 * mm});
            skLineSegment(sketch, "E52.11.0.24", {"start": v(278.1, -7.07) * mm, "end": v(278.59, -6.59) * mm});
            skCircle(sketch, "E52.11.0.25", {"center": v(276, 0) * mm, "radius": 2 * mm});
            skArc(sketch, "E52.11.0.26", {"start": v(290, -12) * mm, "mid": v(288, -10) * mm, "end": v(286, -12) * mm});
            skArc(sketch, "E52.11.0.27", {"start": v(286, -16) * mm, "mid": v(288, -18) * mm, "end": v(290, -16) * mm});
            skLineSegment(sketch, "E52.11.0.28", {"start": v(286, -12) * mm, "end": v(286, -16) * mm});
            skLineSegment(sketch, "E52.11.0.29", {"start": v(290, -16) * mm, "end": v(290, -12) * mm});
            skArc(sketch, "E52.12.0.0", {"start": v(314, 16) * mm, "mid": v(312, 18) * mm, "end": v(310, 16) * mm});
            skLineSegment(sketch, "E52.12.0.1", {"start": v(314, 16) * mm, "end": v(314, 12) * mm});
            skLineSegment(sketch, "E52.12.0.2", {"start": v(310, 16) * mm, "end": v(310, 12) * mm});
            skArc(sketch, "E52.12.0.3", {"start": v(310, 12) * mm, "mid": v(312, 10) * mm, "end": v(314, 12) * mm});
            skCircle(sketch, "E52.12.0.4", {"center": v(304, 16) * mm, "radius": 2 * mm});
            skCircle(sketch, "E52.12.0.5", {"center": v(296, 16) * mm, "radius": 2 * mm});
            skArc(sketch, "E52.12.0.6", {"start": v(297.9, 7.07) * mm, "mid": v(297.9, 9.9) * mm, "end": v(295.07, 9.9) * mm});
            skArc(sketch, "E52.12.0.7", {"start": v(294.59, 9.41) * mm, "mid": v(294.59, 6.59) * mm, "end": v(297.41, 6.59) * mm});
            skLineSegment(sketch, "E52.12.0.8", {"start": v(295.07, 9.9) * mm, "end": v(294.59, 9.41) * mm});
            skLineSegment(sketch, "E52.12.0.9", {"start": v(297.9, 7.07) * mm, "end": v(297.41, 6.59) * mm});
            skArc(sketch, "E52.12.0.10", {"start": v(304.93, 9.9) * mm, "mid": v(302.1, 9.9) * mm, "end": v(302.1, 7.07) * mm});
            skLineSegment(sketch, "E52.12.0.11", {"start": v(304.93, 9.9) * mm, "end": v(305.41, 9.41) * mm});
            skArc(sketch, "E52.12.0.12", {"start": v(302.59, 6.59) * mm, "mid": v(305.41, 6.59) * mm, "end": v(305.41, 9.41) * mm});
            skLineSegment(sketch, "E52.12.0.13", {"start": v(302.1, 7.07) * mm, "end": v(302.59, 6.59) * mm});
            skCircle(sketch, "E52.12.0.14", {"center": v(312, 0) * mm, "radius": 7 * mm});
            skArc(sketch, "E52.12.0.15", {"start": v(295.07, -9.9) * mm, "mid": v(297.9, -9.9) * mm, "end": v(297.9, -7.07) * mm});
            skArc(sketch, "E52.12.0.16", {"start": v(297.41, -6.59) * mm, "mid": v(294.59, -6.59) * mm, "end": v(294.59, -9.41) * mm});
            skLineSegment(sketch, "E52.12.0.17", {"start": v(297.41, -6.59) * mm, "end": v(297.9, -7.07) * mm});
            skLineSegment(sketch, "E52.12.0.18", {"start": v(294.59, -9.41) * mm, "end": v(295.07, -9.9) * mm});
            skArc(sketch, "E52.12.0.19", {"start": v(302.1, -7.07) * mm, "mid": v(302.1, -9.9) * mm, "end": v(304.93, -9.9) * mm});
            skLineSegment(sketch, "E52.12.0.20", {"start": v(304.93, -9.9) * mm, "end": v(305.41, -9.41) * mm});
            skArc(sketch, "E52.12.0.21", {"start": v(305.41, -9.41) * mm, "mid": v(305.41, -6.59) * mm, "end": v(302.59, -6.59) * mm});
            skCircle(sketch, "E52.12.0.22", {"center": v(304, -16) * mm, "radius": 2 * mm});
            skCircle(sketch, "E52.12.0.23", {"center": v(296, -16) * mm, "radius": 2 * mm});
            skLineSegment(sketch, "E52.12.0.24", {"start": v(302.1, -7.07) * mm, "end": v(302.59, -6.59) * mm});
            skCircle(sketch, "E52.12.0.25", {"center": v(300, 0) * mm, "radius": 2 * mm});
            skArc(sketch, "E52.12.0.26", {"start": v(314, -12) * mm, "mid": v(312, -10) * mm, "end": v(310, -12) * mm});
            skArc(sketch, "E52.12.0.27", {"start": v(310, -16) * mm, "mid": v(312, -18) * mm, "end": v(314, -16) * mm});
            skLineSegment(sketch, "E52.12.0.28", {"start": v(310, -12) * mm, "end": v(310, -16) * mm});
            skLineSegment(sketch, "E52.12.0.29", {"start": v(314, -16) * mm, "end": v(314, -12) * mm});
            skArc(sketch, "E52.13.0.0", {"start": v(338, 16) * mm, "mid": v(336, 18) * mm, "end": v(334, 16) * mm});
            skLineSegment(sketch, "E52.13.0.1", {"start": v(338, 16) * mm, "end": v(338, 12) * mm});
            skLineSegment(sketch, "E52.13.0.2", {"start": v(334, 16) * mm, "end": v(334, 12) * mm});
            skArc(sketch, "E52.13.0.3", {"start": v(334, 12) * mm, "mid": v(336, 10) * mm, "end": v(338, 12) * mm});
            skCircle(sketch, "E52.13.0.4", {"center": v(328, 16) * mm, "radius": 2 * mm});
            skCircle(sketch, "E52.13.0.5", {"center": v(320, 16) * mm, "radius": 2 * mm});
            skArc(sketch, "E52.13.0.6", {"start": v(321.9, 7.07) * mm, "mid": v(321.9, 9.9) * mm, "end": v(319.07, 9.9) * mm});
            skArc(sketch, "E52.13.0.7", {"start": v(318.59, 9.41) * mm, "mid": v(318.59, 6.59) * mm, "end": v(321.41, 6.59) * mm});
            skLineSegment(sketch, "E52.13.0.8", {"start": v(319.07, 9.9) * mm, "end": v(318.59, 9.41) * mm});
            skLineSegment(sketch, "E52.13.0.9", {"start": v(321.9, 7.07) * mm, "end": v(321.41, 6.59) * mm});
            skArc(sketch, "E52.13.0.10", {"start": v(328.93, 9.9) * mm, "mid": v(326.1, 9.9) * mm, "end": v(326.1, 7.07) * mm});
            skLineSegment(sketch, "E52.13.0.11", {"start": v(328.93, 9.9) * mm, "end": v(329.41, 9.41) * mm});
            skArc(sketch, "E52.13.0.12", {"start": v(326.59, 6.59) * mm, "mid": v(329.41, 6.59) * mm, "end": v(329.41, 9.41) * mm});
            skLineSegment(sketch, "E52.13.0.13", {"start": v(326.1, 7.07) * mm, "end": v(326.59, 6.59) * mm});
            skCircle(sketch, "E52.13.0.14", {"center": v(336, 0) * mm, "radius": 7 * mm});
            skArc(sketch, "E52.13.0.15", {"start": v(319.07, -9.9) * mm, "mid": v(321.9, -9.9) * mm, "end": v(321.9, -7.07) * mm});
            skArc(sketch, "E52.13.0.16", {"start": v(321.41, -6.59) * mm, "mid": v(318.59, -6.59) * mm, "end": v(318.59, -9.41) * mm});
            skLineSegment(sketch, "E52.13.0.17", {"start": v(321.41, -6.59) * mm, "end": v(321.9, -7.07) * mm});
            skLineSegment(sketch, "E52.13.0.18", {"start": v(318.59, -9.41) * mm, "end": v(319.07, -9.9) * mm});
            skArc(sketch, "E52.13.0.19", {"start": v(326.1, -7.07) * mm, "mid": v(326.1, -9.9) * mm, "end": v(328.93, -9.9) * mm});
            skLineSegment(sketch, "E52.13.0.20", {"start": v(328.93, -9.9) * mm, "end": v(329.41, -9.41) * mm});
            skArc(sketch, "E52.13.0.21", {"start": v(329.41, -9.41) * mm, "mid": v(329.41, -6.59) * mm, "end": v(326.59, -6.59) * mm});
            skCircle(sketch, "E52.13.0.22", {"center": v(328, -16) * mm, "radius": 2 * mm});
            skCircle(sketch, "E52.13.0.23", {"center": v(320, -16) * mm, "radius": 2 * mm});
            skLineSegment(sketch, "E52.13.0.24", {"start": v(326.1, -7.07) * mm, "end": v(326.59, -6.59) * mm});
            skCircle(sketch, "E52.13.0.25", {"center": v(324, 0) * mm, "radius": 2 * mm});
            skArc(sketch, "E52.13.0.26", {"start": v(338, -12) * mm, "mid": v(336, -10) * mm, "end": v(334, -12) * mm});
            skArc(sketch, "E52.13.0.27", {"start": v(334, -16) * mm, "mid": v(336, -18) * mm, "end": v(338, -16) * mm});
            skLineSegment(sketch, "E52.13.0.28", {"start": v(334, -12) * mm, "end": v(334, -16) * mm});
            skLineSegment(sketch, "E52.13.0.29", {"start": v(338, -16) * mm, "end": v(338, -12) * mm});
            skArc(sketch, "E52.14.0.0", {"start": v(362, 16) * mm, "mid": v(360, 18) * mm, "end": v(358, 16) * mm});
            skLineSegment(sketch, "E52.14.0.1", {"start": v(362, 16) * mm, "end": v(362, 12) * mm});
            skLineSegment(sketch, "E52.14.0.2", {"start": v(358, 16) * mm, "end": v(358, 12) * mm});
            skArc(sketch, "E52.14.0.3", {"start": v(358, 12) * mm, "mid": v(360, 10) * mm, "end": v(362, 12) * mm});
            skCircle(sketch, "E52.14.0.4", {"center": v(352, 16) * mm, "radius": 2 * mm});
            skCircle(sketch, "E52.14.0.5", {"center": v(344, 16) * mm, "radius": 2 * mm});
            skArc(sketch, "E52.14.0.6", {"start": v(345.9, 7.07) * mm, "mid": v(345.9, 9.9) * mm, "end": v(343.07, 9.9) * mm});
            skArc(sketch, "E52.14.0.7", {"start": v(342.59, 9.41) * mm, "mid": v(342.59, 6.59) * mm, "end": v(345.41, 6.59) * mm});
            skLineSegment(sketch, "E52.14.0.8", {"start": v(343.07, 9.9) * mm, "end": v(342.59, 9.41) * mm});
            skLineSegment(sketch, "E52.14.0.9", {"start": v(345.9, 7.07) * mm, "end": v(345.41, 6.59) * mm});
            skArc(sketch, "E52.14.0.10", {"start": v(352.93, 9.9) * mm, "mid": v(350.1, 9.9) * mm, "end": v(350.1, 7.07) * mm});
            skLineSegment(sketch, "E52.14.0.11", {"start": v(352.93, 9.9) * mm, "end": v(353.41, 9.41) * mm});
            skArc(sketch, "E52.14.0.12", {"start": v(350.59, 6.59) * mm, "mid": v(353.41, 6.59) * mm, "end": v(353.41, 9.41) * mm});
            skLineSegment(sketch, "E52.14.0.13", {"start": v(350.1, 7.07) * mm, "end": v(350.59, 6.59) * mm});
            skCircle(sketch, "E52.14.0.14", {"center": v(360, 0) * mm, "radius": 7 * mm});
            skArc(sketch, "E52.14.0.15", {"start": v(343.07, -9.9) * mm, "mid": v(345.9, -9.9) * mm, "end": v(345.9, -7.07) * mm});
            skArc(sketch, "E52.14.0.16", {"start": v(345.41, -6.59) * mm, "mid": v(342.59, -6.59) * mm, "end": v(342.59, -9.41) * mm});
            skLineSegment(sketch, "E52.14.0.17", {"start": v(345.41, -6.59) * mm, "end": v(345.9, -7.07) * mm});
            skLineSegment(sketch, "E52.14.0.18", {"start": v(342.59, -9.41) * mm, "end": v(343.07, -9.9) * mm});
            skArc(sketch, "E52.14.0.19", {"start": v(350.1, -7.07) * mm, "mid": v(350.1, -9.9) * mm, "end": v(352.93, -9.9) * mm});
            skLineSegment(sketch, "E52.14.0.20", {"start": v(352.93, -9.9) * mm, "end": v(353.41, -9.41) * mm});
            skArc(sketch, "E52.14.0.21", {"start": v(353.41, -9.41) * mm, "mid": v(353.41, -6.59) * mm, "end": v(350.59, -6.59) * mm});
            skCircle(sketch, "E52.14.0.22", {"center": v(352, -16) * mm, "radius": 2 * mm});
            skCircle(sketch, "E52.14.0.23", {"center": v(344, -16) * mm, "radius": 2 * mm});
            skLineSegment(sketch, "E52.14.0.24", {"start": v(350.1, -7.07) * mm, "end": v(350.59, -6.59) * mm});
            skCircle(sketch, "E52.14.0.25", {"center": v(348, 0) * mm, "radius": 2 * mm});
            skArc(sketch, "E52.14.0.26", {"start": v(362, -12) * mm, "mid": v(360, -10) * mm, "end": v(358, -12) * mm});
            skArc(sketch, "E52.14.0.27", {"start": v(358, -16) * mm, "mid": v(360, -18) * mm, "end": v(362, -16) * mm});
            skLineSegment(sketch, "E52.14.0.28", {"start": v(358, -12) * mm, "end": v(358, -16) * mm});
            skLineSegment(sketch, "E52.14.0.29", {"start": v(362, -16) * mm, "end": v(362, -12) * mm});
            skArc(sketch, "E52.15.0.0", {"start": v(386, 16) * mm, "mid": v(384, 18) * mm, "end": v(382, 16) * mm});
            skLineSegment(sketch, "E52.15.0.1", {"start": v(386, 16) * mm, "end": v(386, 12) * mm});
            skLineSegment(sketch, "E52.15.0.2", {"start": v(382, 16) * mm, "end": v(382, 12) * mm});
            skArc(sketch, "E52.15.0.3", {"start": v(382, 12) * mm, "mid": v(384, 10) * mm, "end": v(386, 12) * mm});
            skCircle(sketch, "E52.15.0.4", {"center": v(376, 16) * mm, "radius": 2 * mm});
            skCircle(sketch, "E52.15.0.5", {"center": v(368, 16) * mm, "radius": 2 * mm});
            skArc(sketch, "E52.15.0.6", {"start": v(369.9, 7.07) * mm, "mid": v(369.9, 9.9) * mm, "end": v(367.07, 9.9) * mm});
            skArc(sketch, "E52.15.0.7", {"start": v(366.59, 9.41) * mm, "mid": v(366.59, 6.59) * mm, "end": v(369.41, 6.59) * mm});
            skLineSegment(sketch, "E52.15.0.8", {"start": v(367.07, 9.9) * mm, "end": v(366.59, 9.41) * mm});
            skLineSegment(sketch, "E52.15.0.9", {"start": v(369.9, 7.07) * mm, "end": v(369.41, 6.59) * mm});
            skArc(sketch, "E52.15.0.10", {"start": v(376.93, 9.9) * mm, "mid": v(374.1, 9.9) * mm, "end": v(374.1, 7.07) * mm});
            skLineSegment(sketch, "E52.15.0.11", {"start": v(376.93, 9.9) * mm, "end": v(377.41, 9.41) * mm});
            skArc(sketch, "E52.15.0.12", {"start": v(374.59, 6.59) * mm, "mid": v(377.41, 6.59) * mm, "end": v(377.41, 9.41) * mm});
            skLineSegment(sketch, "E52.15.0.13", {"start": v(374.1, 7.07) * mm, "end": v(374.59, 6.59) * mm});
            skCircle(sketch, "E52.15.0.14", {"center": v(384, 0) * mm, "radius": 7 * mm});
            skArc(sketch, "E52.15.0.15", {"start": v(367.07, -9.9) * mm, "mid": v(369.9, -9.9) * mm, "end": v(369.9, -7.07) * mm});
            skArc(sketch, "E52.15.0.16", {"start": v(369.41, -6.59) * mm, "mid": v(366.59, -6.59) * mm, "end": v(366.59, -9.41) * mm});
            skLineSegment(sketch, "E52.15.0.17", {"start": v(369.41, -6.59) * mm, "end": v(369.9, -7.07) * mm});
            skLineSegment(sketch, "E52.15.0.18", {"start": v(366.59, -9.41) * mm, "end": v(367.07, -9.9) * mm});
            skArc(sketch, "E52.15.0.19", {"start": v(374.1, -7.07) * mm, "mid": v(374.1, -9.9) * mm, "end": v(376.93, -9.9) * mm});
            skLineSegment(sketch, "E52.15.0.20", {"start": v(376.93, -9.9) * mm, "end": v(377.41, -9.41) * mm});
            skArc(sketch, "E52.15.0.21", {"start": v(377.41, -9.41) * mm, "mid": v(377.41, -6.59) * mm, "end": v(374.59, -6.59) * mm});
            skCircle(sketch, "E52.15.0.22", {"center": v(376, -16) * mm, "radius": 2 * mm});
            skCircle(sketch, "E52.15.0.23", {"center": v(368, -16) * mm, "radius": 2 * mm});
            skLineSegment(sketch, "E52.15.0.24", {"start": v(374.1, -7.07) * mm, "end": v(374.59, -6.59) * mm});
            skCircle(sketch, "E52.15.0.25", {"center": v(372, 0) * mm, "radius": 2 * mm});
            skArc(sketch, "E52.15.0.26", {"start": v(386, -12) * mm, "mid": v(384, -10) * mm, "end": v(382, -12) * mm});
            skArc(sketch, "E52.15.0.27", {"start": v(382, -16) * mm, "mid": v(384, -18) * mm, "end": v(386, -16) * mm});
            skLineSegment(sketch, "E52.15.0.28", {"start": v(382, -12) * mm, "end": v(382, -16) * mm});
            skLineSegment(sketch, "E52.15.0.29", {"start": v(386, -16) * mm, "end": v(386, -12) * mm});
            skArc(sketch, "E52.16.0.0", {"start": v(410, 16) * mm, "mid": v(408, 18) * mm, "end": v(406, 16) * mm});
            skLineSegment(sketch, "E52.16.0.1", {"start": v(410, 16) * mm, "end": v(410, 12) * mm});
            skLineSegment(sketch, "E52.16.0.2", {"start": v(406, 16) * mm, "end": v(406, 12) * mm});
            skArc(sketch, "E52.16.0.3", {"start": v(406, 12) * mm, "mid": v(408, 10) * mm, "end": v(410, 12) * mm});
            skCircle(sketch, "E52.16.0.4", {"center": v(400, 16) * mm, "radius": 2 * mm});
            skCircle(sketch, "E52.16.0.5", {"center": v(392, 16) * mm, "radius": 2 * mm});
            skArc(sketch, "E52.16.0.6", {"start": v(393.9, 7.07) * mm, "mid": v(393.9, 9.9) * mm, "end": v(391.07, 9.9) * mm});
            skArc(sketch, "E52.16.0.7", {"start": v(390.59, 9.41) * mm, "mid": v(390.59, 6.59) * mm, "end": v(393.41, 6.59) * mm});
            skLineSegment(sketch, "E52.16.0.8", {"start": v(391.07, 9.9) * mm, "end": v(390.59, 9.41) * mm});
            skLineSegment(sketch, "E52.16.0.9", {"start": v(393.9, 7.07) * mm, "end": v(393.41, 6.59) * mm});
            skArc(sketch, "E52.16.0.10", {"start": v(400.93, 9.9) * mm, "mid": v(398.1, 9.9) * mm, "end": v(398.1, 7.07) * mm});
            skLineSegment(sketch, "E52.16.0.11", {"start": v(400.93, 9.9) * mm, "end": v(401.41, 9.41) * mm});
            skArc(sketch, "E52.16.0.12", {"start": v(398.59, 6.59) * mm, "mid": v(401.41, 6.59) * mm, "end": v(401.41, 9.41) * mm});
            skLineSegment(sketch, "E52.16.0.13", {"start": v(398.1, 7.07) * mm, "end": v(398.59, 6.59) * mm});
            skCircle(sketch, "E52.16.0.14", {"center": v(408, 0) * mm, "radius": 7 * mm});
            skArc(sketch, "E52.16.0.15", {"start": v(391.07, -9.9) * mm, "mid": v(393.9, -9.9) * mm, "end": v(393.9, -7.07) * mm});
            skArc(sketch, "E52.16.0.16", {"start": v(393.41, -6.59) * mm, "mid": v(390.59, -6.59) * mm, "end": v(390.59, -9.41) * mm});
            skLineSegment(sketch, "E52.16.0.17", {"start": v(393.41, -6.59) * mm, "end": v(393.9, -7.07) * mm});
            skLineSegment(sketch, "E52.16.0.18", {"start": v(390.59, -9.41) * mm, "end": v(391.07, -9.9) * mm});
            skArc(sketch, "E52.16.0.19", {"start": v(398.1, -7.07) * mm, "mid": v(398.1, -9.9) * mm, "end": v(400.93, -9.9) * mm});
            skLineSegment(sketch, "E52.16.0.20", {"start": v(400.93, -9.9) * mm, "end": v(401.41, -9.41) * mm});
            skArc(sketch, "E52.16.0.21", {"start": v(401.41, -9.41) * mm, "mid": v(401.41, -6.59) * mm, "end": v(398.59, -6.59) * mm});
            skCircle(sketch, "E52.16.0.22", {"center": v(400, -16) * mm, "radius": 2 * mm});
            skCircle(sketch, "E52.16.0.23", {"center": v(392, -16) * mm, "radius": 2 * mm});
            skLineSegment(sketch, "E52.16.0.24", {"start": v(398.1, -7.07) * mm, "end": v(398.59, -6.59) * mm});
            skCircle(sketch, "E52.16.0.25", {"center": v(396, 0) * mm, "radius": 2 * mm});
            skArc(sketch, "E52.16.0.26", {"start": v(410, -12) * mm, "mid": v(408, -10) * mm, "end": v(406, -12) * mm});
            skArc(sketch, "E52.16.0.27", {"start": v(406, -16) * mm, "mid": v(408, -18) * mm, "end": v(410, -16) * mm});
            skLineSegment(sketch, "E52.16.0.28", {"start": v(406, -12) * mm, "end": v(406, -16) * mm});
            skLineSegment(sketch, "E52.16.0.29", {"start": v(410, -16) * mm, "end": v(410, -12) * mm});
            skArc(sketch, "E52.17.0.0", {"start": v(434, 16) * mm, "mid": v(432, 18) * mm, "end": v(430, 16) * mm});
            skLineSegment(sketch, "E52.17.0.1", {"start": v(434, 16) * mm, "end": v(434, 12) * mm});
            skLineSegment(sketch, "E52.17.0.2", {"start": v(430, 16) * mm, "end": v(430, 12) * mm});
            skArc(sketch, "E52.17.0.3", {"start": v(430, 12) * mm, "mid": v(432, 10) * mm, "end": v(434, 12) * mm});
            skCircle(sketch, "E52.17.0.4", {"center": v(424, 16) * mm, "radius": 2 * mm});
            skCircle(sketch, "E52.17.0.5", {"center": v(416, 16) * mm, "radius": 2 * mm});
            skArc(sketch, "E52.17.0.6", {"start": v(417.9, 7.07) * mm, "mid": v(417.9, 9.9) * mm, "end": v(415.07, 9.9) * mm});
            skArc(sketch, "E52.17.0.7", {"start": v(414.59, 9.41) * mm, "mid": v(414.59, 6.59) * mm, "end": v(417.41, 6.59) * mm});
            skLineSegment(sketch, "E52.17.0.8", {"start": v(415.07, 9.9) * mm, "end": v(414.59, 9.41) * mm});
            skLineSegment(sketch, "E52.17.0.9", {"start": v(417.9, 7.07) * mm, "end": v(417.41, 6.59) * mm});
            skArc(sketch, "E52.17.0.10", {"start": v(424.93, 9.9) * mm, "mid": v(422.1, 9.9) * mm, "end": v(422.1, 7.07) * mm});
            skLineSegment(sketch, "E52.17.0.11", {"start": v(424.93, 9.9) * mm, "end": v(425.41, 9.41) * mm});
            skArc(sketch, "E52.17.0.12", {"start": v(422.59, 6.59) * mm, "mid": v(425.41, 6.59) * mm, "end": v(425.41, 9.41) * mm});
            skLineSegment(sketch, "E52.17.0.13", {"start": v(422.1, 7.07) * mm, "end": v(422.59, 6.59) * mm});
            skCircle(sketch, "E52.17.0.14", {"center": v(432, 0) * mm, "radius": 7 * mm});
            skArc(sketch, "E52.17.0.15", {"start": v(415.07, -9.9) * mm, "mid": v(417.9, -9.9) * mm, "end": v(417.9, -7.07) * mm});
            skArc(sketch, "E52.17.0.16", {"start": v(417.41, -6.59) * mm, "mid": v(414.59, -6.59) * mm, "end": v(414.59, -9.41) * mm});
            skLineSegment(sketch, "E52.17.0.17", {"start": v(417.41, -6.59) * mm, "end": v(417.9, -7.07) * mm});
            skLineSegment(sketch, "E52.17.0.18", {"start": v(414.59, -9.41) * mm, "end": v(415.07, -9.9) * mm});
            skArc(sketch, "E52.17.0.19", {"start": v(422.1, -7.07) * mm, "mid": v(422.1, -9.9) * mm, "end": v(424.93, -9.9) * mm});
            skLineSegment(sketch, "E52.17.0.20", {"start": v(424.93, -9.9) * mm, "end": v(425.41, -9.41) * mm});
            skArc(sketch, "E52.17.0.21", {"start": v(425.41, -9.41) * mm, "mid": v(425.41, -6.59) * mm, "end": v(422.59, -6.59) * mm});
            skCircle(sketch, "E52.17.0.22", {"center": v(424, -16) * mm, "radius": 2 * mm});
            skCircle(sketch, "E52.17.0.23", {"center": v(416, -16) * mm, "radius": 2 * mm});
            skLineSegment(sketch, "E52.17.0.24", {"start": v(422.1, -7.07) * mm, "end": v(422.59, -6.59) * mm});
            skCircle(sketch, "E52.17.0.25", {"center": v(420, 0) * mm, "radius": 2 * mm});
            skArc(sketch, "E52.17.0.26", {"start": v(434, -12) * mm, "mid": v(432, -10) * mm, "end": v(430, -12) * mm});
            skArc(sketch, "E52.17.0.27", {"start": v(430, -16) * mm, "mid": v(432, -18) * mm, "end": v(434, -16) * mm});
            skLineSegment(sketch, "E52.17.0.28", {"start": v(430, -12) * mm, "end": v(430, -16) * mm});
            skLineSegment(sketch, "E52.17.0.29", {"start": v(434, -16) * mm, "end": v(434, -12) * mm});
            skArc(sketch, "E52.18.0.0", {"start": v(458, 16) * mm, "mid": v(456, 18) * mm, "end": v(454, 16) * mm});
            skLineSegment(sketch, "E52.18.0.1", {"start": v(458, 16) * mm, "end": v(458, 12) * mm});
            skLineSegment(sketch, "E52.18.0.2", {"start": v(454, 16) * mm, "end": v(454, 12) * mm});
            skArc(sketch, "E52.18.0.3", {"start": v(454, 12) * mm, "mid": v(456, 10) * mm, "end": v(458, 12) * mm});
            skCircle(sketch, "E52.18.0.4", {"center": v(448, 16) * mm, "radius": 2 * mm});
            skCircle(sketch, "E52.18.0.5", {"center": v(440, 16) * mm, "radius": 2 * mm});
            skArc(sketch, "E52.18.0.6", {"start": v(441.9, 7.07) * mm, "mid": v(441.9, 9.9) * mm, "end": v(439.07, 9.9) * mm});
            skArc(sketch, "E52.18.0.7", {"start": v(438.59, 9.41) * mm, "mid": v(438.59, 6.59) * mm, "end": v(441.41, 6.59) * mm});
            skLineSegment(sketch, "E52.18.0.8", {"start": v(439.07, 9.9) * mm, "end": v(438.59, 9.41) * mm});
            skLineSegment(sketch, "E52.18.0.9", {"start": v(441.9, 7.07) * mm, "end": v(441.41, 6.59) * mm});
            skArc(sketch, "E52.18.0.10", {"start": v(448.93, 9.9) * mm, "mid": v(446.1, 9.9) * mm, "end": v(446.1, 7.07) * mm});
            skLineSegment(sketch, "E52.18.0.11", {"start": v(448.93, 9.9) * mm, "end": v(449.41, 9.41) * mm});
            skArc(sketch, "E52.18.0.12", {"start": v(446.59, 6.59) * mm, "mid": v(449.41, 6.59) * mm, "end": v(449.41, 9.41) * mm});
            skLineSegment(sketch, "E52.18.0.13", {"start": v(446.1, 7.07) * mm, "end": v(446.59, 6.59) * mm});
            skCircle(sketch, "E52.18.0.14", {"center": v(456, 0) * mm, "radius": 7 * mm});
            skArc(sketch, "E52.18.0.15", {"start": v(439.07, -9.9) * mm, "mid": v(441.9, -9.9) * mm, "end": v(441.9, -7.07) * mm});
            skArc(sketch, "E52.18.0.16", {"start": v(441.41, -6.59) * mm, "mid": v(438.59, -6.59) * mm, "end": v(438.59, -9.41) * mm});
            skLineSegment(sketch, "E52.18.0.17", {"start": v(441.41, -6.59) * mm, "end": v(441.9, -7.07) * mm});
            skLineSegment(sketch, "E52.18.0.18", {"start": v(438.59, -9.41) * mm, "end": v(439.07, -9.9) * mm});
            skArc(sketch, "E52.18.0.19", {"start": v(446.1, -7.07) * mm, "mid": v(446.1, -9.9) * mm, "end": v(448.93, -9.9) * mm});
            skLineSegment(sketch, "E52.18.0.20", {"start": v(448.93, -9.9) * mm, "end": v(449.41, -9.41) * mm});
            skArc(sketch, "E52.18.0.21", {"start": v(449.41, -9.41) * mm, "mid": v(449.41, -6.59) * mm, "end": v(446.59, -6.59) * mm});
            skCircle(sketch, "E52.18.0.22", {"center": v(448, -16) * mm, "radius": 2 * mm});
            skCircle(sketch, "E52.18.0.23", {"center": v(440, -16) * mm, "radius": 2 * mm});
            skLineSegment(sketch, "E52.18.0.24", {"start": v(446.1, -7.07) * mm, "end": v(446.59, -6.59) * mm});
            skCircle(sketch, "E52.18.0.25", {"center": v(444, 0) * mm, "radius": 2 * mm});
            skArc(sketch, "E52.18.0.26", {"start": v(458, -12) * mm, "mid": v(456, -10) * mm, "end": v(454, -12) * mm});
            skArc(sketch, "E52.18.0.27", {"start": v(454, -16) * mm, "mid": v(456, -18) * mm, "end": v(458, -16) * mm});
            skLineSegment(sketch, "E52.18.0.28", {"start": v(454, -12) * mm, "end": v(454, -16) * mm});
            skLineSegment(sketch, "E52.18.0.29", {"start": v(458, -16) * mm, "end": v(458, -12) * mm});
            skArc(sketch, "E52.19.0.0", {"start": v(482, 16) * mm, "mid": v(480, 18) * mm, "end": v(478, 16) * mm});
            skLineSegment(sketch, "E52.19.0.1", {"start": v(482, 16) * mm, "end": v(482, 12) * mm});
            skLineSegment(sketch, "E52.19.0.2", {"start": v(478, 16) * mm, "end": v(478, 12) * mm});
            skArc(sketch, "E52.19.0.3", {"start": v(478, 12) * mm, "mid": v(480, 10) * mm, "end": v(482, 12) * mm});
            skCircle(sketch, "E52.19.0.4", {"center": v(472, 16) * mm, "radius": 2 * mm});
            skCircle(sketch, "E52.19.0.5", {"center": v(464, 16) * mm, "radius": 2 * mm});
            skArc(sketch, "E52.19.0.6", {"start": v(465.9, 7.07) * mm, "mid": v(465.9, 9.9) * mm, "end": v(463.07, 9.9) * mm});
            skArc(sketch, "E52.19.0.7", {"start": v(462.59, 9.41) * mm, "mid": v(462.59, 6.59) * mm, "end": v(465.41, 6.59) * mm});
            skLineSegment(sketch, "E52.19.0.8", {"start": v(463.07, 9.9) * mm, "end": v(462.59, 9.41) * mm});
            skLineSegment(sketch, "E52.19.0.9", {"start": v(465.9, 7.07) * mm, "end": v(465.41, 6.59) * mm});
            skArc(sketch, "E52.19.0.10", {"start": v(472.93, 9.9) * mm, "mid": v(470.1, 9.9) * mm, "end": v(470.1, 7.07) * mm});
            skLineSegment(sketch, "E52.19.0.11", {"start": v(472.93, 9.9) * mm, "end": v(473.41, 9.41) * mm});
            skArc(sketch, "E52.19.0.12", {"start": v(470.59, 6.59) * mm, "mid": v(473.41, 6.59) * mm, "end": v(473.41, 9.41) * mm});
            skLineSegment(sketch, "E52.19.0.13", {"start": v(470.1, 7.07) * mm, "end": v(470.59, 6.59) * mm});
            skCircle(sketch, "E52.19.0.14", {"center": v(480, 0) * mm, "radius": 7 * mm});
            skArc(sketch, "E52.19.0.15", {"start": v(463.07, -9.9) * mm, "mid": v(465.9, -9.9) * mm, "end": v(465.9, -7.07) * mm});
            skArc(sketch, "E52.19.0.16", {"start": v(465.41, -6.59) * mm, "mid": v(462.59, -6.59) * mm, "end": v(462.59, -9.41) * mm});
            skLineSegment(sketch, "E52.19.0.17", {"start": v(465.41, -6.59) * mm, "end": v(465.9, -7.07) * mm});
            skLineSegment(sketch, "E52.19.0.18", {"start": v(462.59, -9.41) * mm, "end": v(463.07, -9.9) * mm});
            skArc(sketch, "E52.19.0.19", {"start": v(470.1, -7.07) * mm, "mid": v(470.1, -9.9) * mm, "end": v(472.93, -9.9) * mm});
            skLineSegment(sketch, "E52.19.0.20", {"start": v(472.93, -9.9) * mm, "end": v(473.41, -9.41) * mm});
            skArc(sketch, "E52.19.0.21", {"start": v(473.41, -9.41) * mm, "mid": v(473.41, -6.59) * mm, "end": v(470.59, -6.59) * mm});
            skCircle(sketch, "E52.19.0.22", {"center": v(472, -16) * mm, "radius": 2 * mm});
            skCircle(sketch, "E52.19.0.23", {"center": v(464, -16) * mm, "radius": 2 * mm});
            skLineSegment(sketch, "E52.19.0.24", {"start": v(470.1, -7.07) * mm, "end": v(470.59, -6.59) * mm});
            skCircle(sketch, "E52.19.0.25", {"center": v(468, 0) * mm, "radius": 2 * mm});
            skArc(sketch, "E52.19.0.26", {"start": v(482, -12) * mm, "mid": v(480, -10) * mm, "end": v(478, -12) * mm});
            skArc(sketch, "E52.19.0.27", {"start": v(478, -16) * mm, "mid": v(480, -18) * mm, "end": v(482, -16) * mm});
            skLineSegment(sketch, "E52.19.0.28", {"start": v(478, -12) * mm, "end": v(478, -16) * mm});
            skLineSegment(sketch, "E52.19.0.29", {"start": v(482, -16) * mm, "end": v(482, -12) * mm});
            skArc(sketch, "E52.20.0.0", {"start": v(506, 16) * mm, "mid": v(504, 18) * mm, "end": v(502, 16) * mm});
            skLineSegment(sketch, "E52.20.0.1", {"start": v(506, 16) * mm, "end": v(506, 12) * mm});
            skLineSegment(sketch, "E52.20.0.2", {"start": v(502, 16) * mm, "end": v(502, 12) * mm});
            skArc(sketch, "E52.20.0.3", {"start": v(502, 12) * mm, "mid": v(504, 10) * mm, "end": v(506, 12) * mm});
            skCircle(sketch, "E52.20.0.4", {"center": v(496, 16) * mm, "radius": 2 * mm});
            skCircle(sketch, "E52.20.0.5", {"center": v(488, 16) * mm, "radius": 2 * mm});
            skArc(sketch, "E52.20.0.6", {"start": v(489.9, 7.07) * mm, "mid": v(489.9, 9.9) * mm, "end": v(487.07, 9.9) * mm});
            skArc(sketch, "E52.20.0.7", {"start": v(486.59, 9.41) * mm, "mid": v(486.59, 6.59) * mm, "end": v(489.41, 6.59) * mm});
            skLineSegment(sketch, "E52.20.0.8", {"start": v(487.07, 9.9) * mm, "end": v(486.59, 9.41) * mm});
            skLineSegment(sketch, "E52.20.0.9", {"start": v(489.9, 7.07) * mm, "end": v(489.41, 6.59) * mm});
            skArc(sketch, "E52.20.0.10", {"start": v(496.93, 9.9) * mm, "mid": v(494.1, 9.9) * mm, "end": v(494.1, 7.07) * mm});
            skLineSegment(sketch, "E52.20.0.11", {"start": v(496.93, 9.9) * mm, "end": v(497.41, 9.41) * mm});
            skArc(sketch, "E52.20.0.12", {"start": v(494.59, 6.59) * mm, "mid": v(497.41, 6.59) * mm, "end": v(497.41, 9.41) * mm});
            skLineSegment(sketch, "E52.20.0.13", {"start": v(494.1, 7.07) * mm, "end": v(494.59, 6.59) * mm});
            skCircle(sketch, "E52.20.0.14", {"center": v(504, 0) * mm, "radius": 7 * mm});
            skArc(sketch, "E52.20.0.15", {"start": v(487.07, -9.9) * mm, "mid": v(489.9, -9.9) * mm, "end": v(489.9, -7.07) * mm});
            skArc(sketch, "E52.20.0.16", {"start": v(489.41, -6.59) * mm, "mid": v(486.59, -6.59) * mm, "end": v(486.59, -9.41) * mm});
            skLineSegment(sketch, "E52.20.0.17", {"start": v(489.41, -6.59) * mm, "end": v(489.9, -7.07) * mm});
            skLineSegment(sketch, "E52.20.0.18", {"start": v(486.59, -9.41) * mm, "end": v(487.07, -9.9) * mm});
            skArc(sketch, "E52.20.0.19", {"start": v(494.1, -7.07) * mm, "mid": v(494.1, -9.9) * mm, "end": v(496.93, -9.9) * mm});
            skLineSegment(sketch, "E52.20.0.20", {"start": v(496.93, -9.9) * mm, "end": v(497.41, -9.41) * mm});
            skArc(sketch, "E52.20.0.21", {"start": v(497.41, -9.41) * mm, "mid": v(497.41, -6.59) * mm, "end": v(494.59, -6.59) * mm});
            skCircle(sketch, "E52.20.0.22", {"center": v(496, -16) * mm, "radius": 2 * mm});
            skCircle(sketch, "E52.20.0.23", {"center": v(488, -16) * mm, "radius": 2 * mm});
            skLineSegment(sketch, "E52.20.0.24", {"start": v(494.1, -7.07) * mm, "end": v(494.59, -6.59) * mm});
            skCircle(sketch, "E52.20.0.25", {"center": v(492, 0) * mm, "radius": 2 * mm});
            skArc(sketch, "E52.20.0.26", {"start": v(506, -12) * mm, "mid": v(504, -10) * mm, "end": v(502, -12) * mm});
            skArc(sketch, "E52.20.0.27", {"start": v(502, -16) * mm, "mid": v(504, -18) * mm, "end": v(506, -16) * mm});
            skLineSegment(sketch, "E52.20.0.28", {"start": v(502, -12) * mm, "end": v(502, -16) * mm});
            skLineSegment(sketch, "E52.20.0.29", {"start": v(506, -16) * mm, "end": v(506, -12) * mm});
            skArc(sketch, "E52.21.0.0", {"start": v(530, 16) * mm, "mid": v(528, 18) * mm, "end": v(526, 16) * mm});
            skLineSegment(sketch, "E52.21.0.1", {"start": v(530, 16) * mm, "end": v(530, 12) * mm});
            skLineSegment(sketch, "E52.21.0.2", {"start": v(526, 16) * mm, "end": v(526, 12) * mm});
            skArc(sketch, "E52.21.0.3", {"start": v(526, 12) * mm, "mid": v(528, 10) * mm, "end": v(530, 12) * mm});
            skCircle(sketch, "E52.21.0.4", {"center": v(520, 16) * mm, "radius": 2 * mm});
            skCircle(sketch, "E52.21.0.5", {"center": v(512, 16) * mm, "radius": 2 * mm});
            skArc(sketch, "E52.21.0.6", {"start": v(513.9, 7.07) * mm, "mid": v(513.9, 9.9) * mm, "end": v(511.07, 9.9) * mm});
            skArc(sketch, "E52.21.0.7", {"start": v(510.59, 9.41) * mm, "mid": v(510.59, 6.59) * mm, "end": v(513.41, 6.59) * mm});
            skLineSegment(sketch, "E52.21.0.8", {"start": v(511.07, 9.9) * mm, "end": v(510.59, 9.41) * mm});
            skLineSegment(sketch, "E52.21.0.9", {"start": v(513.9, 7.07) * mm, "end": v(513.41, 6.59) * mm});
            skArc(sketch, "E52.21.0.10", {"start": v(520.93, 9.9) * mm, "mid": v(518.1, 9.9) * mm, "end": v(518.1, 7.07) * mm});
            skLineSegment(sketch, "E52.21.0.11", {"start": v(520.93, 9.9) * mm, "end": v(521.41, 9.41) * mm});
            skArc(sketch, "E52.21.0.12", {"start": v(518.59, 6.59) * mm, "mid": v(521.41, 6.59) * mm, "end": v(521.41, 9.41) * mm});
            skLineSegment(sketch, "E52.21.0.13", {"start": v(518.1, 7.07) * mm, "end": v(518.59, 6.59) * mm});
            skCircle(sketch, "E52.21.0.14", {"center": v(528, 0) * mm, "radius": 7 * mm});
            skArc(sketch, "E52.21.0.15", {"start": v(511.07, -9.9) * mm, "mid": v(513.9, -9.9) * mm, "end": v(513.9, -7.07) * mm});
            skArc(sketch, "E52.21.0.16", {"start": v(513.41, -6.59) * mm, "mid": v(510.59, -6.59) * mm, "end": v(510.59, -9.41) * mm});
            skLineSegment(sketch, "E52.21.0.17", {"start": v(513.41, -6.59) * mm, "end": v(513.9, -7.07) * mm});
            skLineSegment(sketch, "E52.21.0.18", {"start": v(510.59, -9.41) * mm, "end": v(511.07, -9.9) * mm});
            skArc(sketch, "E52.21.0.19", {"start": v(518.1, -7.07) * mm, "mid": v(518.1, -9.9) * mm, "end": v(520.93, -9.9) * mm});
            skLineSegment(sketch, "E52.21.0.20", {"start": v(520.93, -9.9) * mm, "end": v(521.41, -9.41) * mm});
            skArc(sketch, "E52.21.0.21", {"start": v(521.41, -9.41) * mm, "mid": v(521.41, -6.59) * mm, "end": v(518.59, -6.59) * mm});
            skCircle(sketch, "E52.21.0.22", {"center": v(520, -16) * mm, "radius": 2 * mm});
            skCircle(sketch, "E52.21.0.23", {"center": v(512, -16) * mm, "radius": 2 * mm});
            skLineSegment(sketch, "E52.21.0.24", {"start": v(518.1, -7.07) * mm, "end": v(518.59, -6.59) * mm});
            skCircle(sketch, "E52.21.0.25", {"center": v(516, 0) * mm, "radius": 2 * mm});
            skArc(sketch, "E52.21.0.26", {"start": v(530, -12) * mm, "mid": v(528, -10) * mm, "end": v(526, -12) * mm});
            skArc(sketch, "E52.21.0.27", {"start": v(526, -16) * mm, "mid": v(528, -18) * mm, "end": v(530, -16) * mm});
            skLineSegment(sketch, "E52.21.0.28", {"start": v(526, -12) * mm, "end": v(526, -16) * mm});
            skLineSegment(sketch, "E52.21.0.29", {"start": v(530, -16) * mm, "end": v(530, -12) * mm});
            skArc(sketch, "E52.22.0.0", {"start": v(554, 16) * mm, "mid": v(552, 18) * mm, "end": v(550, 16) * mm});
            skLineSegment(sketch, "E52.22.0.1", {"start": v(554, 16) * mm, "end": v(554, 12) * mm});
            skLineSegment(sketch, "E52.22.0.2", {"start": v(550, 16) * mm, "end": v(550, 12) * mm});
            skArc(sketch, "E52.22.0.3", {"start": v(550, 12) * mm, "mid": v(552, 10) * mm, "end": v(554, 12) * mm});
            skCircle(sketch, "E52.22.0.4", {"center": v(544, 16) * mm, "radius": 2 * mm});
            skCircle(sketch, "E52.22.0.5", {"center": v(536, 16) * mm, "radius": 2 * mm});
            skArc(sketch, "E52.22.0.6", {"start": v(537.9, 7.07) * mm, "mid": v(537.9, 9.9) * mm, "end": v(535.07, 9.9) * mm});
            skArc(sketch, "E52.22.0.7", {"start": v(534.59, 9.41) * mm, "mid": v(534.59, 6.59) * mm, "end": v(537.41, 6.59) * mm});
            skLineSegment(sketch, "E52.22.0.8", {"start": v(535.07, 9.9) * mm, "end": v(534.59, 9.41) * mm});
            skLineSegment(sketch, "E52.22.0.9", {"start": v(537.9, 7.07) * mm, "end": v(537.41, 6.59) * mm});
            skArc(sketch, "E52.22.0.10", {"start": v(544.93, 9.9) * mm, "mid": v(542.1, 9.9) * mm, "end": v(542.1, 7.07) * mm});
            skLineSegment(sketch, "E52.22.0.11", {"start": v(544.93, 9.9) * mm, "end": v(545.41, 9.41) * mm});
            skArc(sketch, "E52.22.0.12", {"start": v(542.59, 6.59) * mm, "mid": v(545.41, 6.59) * mm, "end": v(545.41, 9.41) * mm});
            skLineSegment(sketch, "E52.22.0.13", {"start": v(542.1, 7.07) * mm, "end": v(542.59, 6.59) * mm});
            skCircle(sketch, "E52.22.0.14", {"center": v(552, 0) * mm, "radius": 7 * mm});
            skArc(sketch, "E52.22.0.15", {"start": v(535.07, -9.9) * mm, "mid": v(537.9, -9.9) * mm, "end": v(537.9, -7.07) * mm});
            skArc(sketch, "E52.22.0.16", {"start": v(537.41, -6.59) * mm, "mid": v(534.59, -6.59) * mm, "end": v(534.59, -9.41) * mm});
            skLineSegment(sketch, "E52.22.0.17", {"start": v(537.41, -6.59) * mm, "end": v(537.9, -7.07) * mm});
            skLineSegment(sketch, "E52.22.0.18", {"start": v(534.59, -9.41) * mm, "end": v(535.07, -9.9) * mm});
            skArc(sketch, "E52.22.0.19", {"start": v(542.1, -7.07) * mm, "mid": v(542.1, -9.9) * mm, "end": v(544.93, -9.9) * mm});
            skLineSegment(sketch, "E52.22.0.20", {"start": v(544.93, -9.9) * mm, "end": v(545.41, -9.41) * mm});
            skArc(sketch, "E52.22.0.21", {"start": v(545.41, -9.41) * mm, "mid": v(545.41, -6.59) * mm, "end": v(542.59, -6.59) * mm});
            skCircle(sketch, "E52.22.0.22", {"center": v(544, -16) * mm, "radius": 2 * mm});
            skCircle(sketch, "E52.22.0.23", {"center": v(536, -16) * mm, "radius": 2 * mm});
            skLineSegment(sketch, "E52.22.0.24", {"start": v(542.1, -7.07) * mm, "end": v(542.59, -6.59) * mm});
            skCircle(sketch, "E52.22.0.25", {"center": v(540, 0) * mm, "radius": 2 * mm});
            skArc(sketch, "E52.22.0.26", {"start": v(554, -12) * mm, "mid": v(552, -10) * mm, "end": v(550, -12) * mm});
            skArc(sketch, "E52.22.0.27", {"start": v(550, -16) * mm, "mid": v(552, -18) * mm, "end": v(554, -16) * mm});
            skLineSegment(sketch, "E52.22.0.28", {"start": v(550, -12) * mm, "end": v(550, -16) * mm});
            skLineSegment(sketch, "E52.22.0.29", {"start": v(554, -16) * mm, "end": v(554, -12) * mm});
            skArc(sketch, "E52.23.0.0", {"start": v(578, 16) * mm, "mid": v(576, 18) * mm, "end": v(574, 16) * mm});
            skLineSegment(sketch, "E52.23.0.1", {"start": v(578, 16) * mm, "end": v(578, 12) * mm});
            skLineSegment(sketch, "E52.23.0.2", {"start": v(574, 16) * mm, "end": v(574, 12) * mm});
            skArc(sketch, "E52.23.0.3", {"start": v(574, 12) * mm, "mid": v(576, 10) * mm, "end": v(578, 12) * mm});
            skCircle(sketch, "E52.23.0.4", {"center": v(568, 16) * mm, "radius": 2 * mm});
            skCircle(sketch, "E52.23.0.5", {"center": v(560, 16) * mm, "radius": 2 * mm});
            skArc(sketch, "E52.23.0.6", {"start": v(561.9, 7.07) * mm, "mid": v(561.9, 9.9) * mm, "end": v(559.07, 9.9) * mm});
            skArc(sketch, "E52.23.0.7", {"start": v(558.59, 9.41) * mm, "mid": v(558.59, 6.59) * mm, "end": v(561.41, 6.59) * mm});
            skLineSegment(sketch, "E52.23.0.8", {"start": v(559.07, 9.9) * mm, "end": v(558.59, 9.41) * mm});
            skLineSegment(sketch, "E52.23.0.9", {"start": v(561.9, 7.07) * mm, "end": v(561.41, 6.59) * mm});
            skArc(sketch, "E52.23.0.10", {"start": v(568.93, 9.9) * mm, "mid": v(566.1, 9.9) * mm, "end": v(566.1, 7.07) * mm});
            skLineSegment(sketch, "E52.23.0.11", {"start": v(568.93, 9.9) * mm, "end": v(569.41, 9.41) * mm});
            skArc(sketch, "E52.23.0.12", {"start": v(566.59, 6.59) * mm, "mid": v(569.41, 6.59) * mm, "end": v(569.41, 9.41) * mm});
            skLineSegment(sketch, "E52.23.0.13", {"start": v(566.1, 7.07) * mm, "end": v(566.59, 6.59) * mm});
            skCircle(sketch, "E52.23.0.14", {"center": v(576, 0) * mm, "radius": 7 * mm});
            skArc(sketch, "E52.23.0.15", {"start": v(559.07, -9.9) * mm, "mid": v(561.9, -9.9) * mm, "end": v(561.9, -7.07) * mm});
            skArc(sketch, "E52.23.0.16", {"start": v(561.41, -6.59) * mm, "mid": v(558.59, -6.59) * mm, "end": v(558.59, -9.41) * mm});
            skLineSegment(sketch, "E52.23.0.17", {"start": v(561.41, -6.59) * mm, "end": v(561.9, -7.07) * mm});
            skLineSegment(sketch, "E52.23.0.18", {"start": v(558.59, -9.41) * mm, "end": v(559.07, -9.9) * mm});
            skArc(sketch, "E52.23.0.19", {"start": v(566.1, -7.07) * mm, "mid": v(566.1, -9.9) * mm, "end": v(568.93, -9.9) * mm});
            skLineSegment(sketch, "E52.23.0.20", {"start": v(568.93, -9.9) * mm, "end": v(569.41, -9.41) * mm});
            skArc(sketch, "E52.23.0.21", {"start": v(569.41, -9.41) * mm, "mid": v(569.41, -6.59) * mm, "end": v(566.59, -6.59) * mm});
            skCircle(sketch, "E52.23.0.22", {"center": v(568, -16) * mm, "radius": 2 * mm});
            skCircle(sketch, "E52.23.0.23", {"center": v(560, -16) * mm, "radius": 2 * mm});
            skLineSegment(sketch, "E52.23.0.24", {"start": v(566.1, -7.07) * mm, "end": v(566.59, -6.59) * mm});
            skCircle(sketch, "E52.23.0.25", {"center": v(564, 0) * mm, "radius": 2 * mm});
            skArc(sketch, "E52.23.0.26", {"start": v(578, -12) * mm, "mid": v(576, -10) * mm, "end": v(574, -12) * mm});
            skArc(sketch, "E52.23.0.27", {"start": v(574, -16) * mm, "mid": v(576, -18) * mm, "end": v(578, -16) * mm});
            skLineSegment(sketch, "E52.23.0.28", {"start": v(574, -12) * mm, "end": v(574, -16) * mm});
            skLineSegment(sketch, "E52.23.0.29", {"start": v(578, -16) * mm, "end": v(578, -12) * mm});
            skArc(sketch, "E52.24.0.0", {"start": v(602, 16) * mm, "mid": v(600, 18) * mm, "end": v(598, 16) * mm});
            skLineSegment(sketch, "E52.24.0.1", {"start": v(602, 16) * mm, "end": v(602, 12) * mm});
            skLineSegment(sketch, "E52.24.0.2", {"start": v(598, 16) * mm, "end": v(598, 12) * mm});
            skArc(sketch, "E52.24.0.3", {"start": v(598, 12) * mm, "mid": v(600, 10) * mm, "end": v(602, 12) * mm});
            skCircle(sketch, "E52.24.0.4", {"center": v(592, 16) * mm, "radius": 2 * mm});
            skCircle(sketch, "E52.24.0.5", {"center": v(584, 16) * mm, "radius": 2 * mm});
            skArc(sketch, "E52.24.0.6", {"start": v(585.9, 7.07) * mm, "mid": v(585.9, 9.9) * mm, "end": v(583.07, 9.9) * mm});
            skArc(sketch, "E52.24.0.7", {"start": v(582.59, 9.41) * mm, "mid": v(582.59, 6.59) * mm, "end": v(585.41, 6.59) * mm});
            skLineSegment(sketch, "E52.24.0.8", {"start": v(583.07, 9.9) * mm, "end": v(582.59, 9.41) * mm});
            skLineSegment(sketch, "E52.24.0.9", {"start": v(585.9, 7.07) * mm, "end": v(585.41, 6.59) * mm});
            skArc(sketch, "E52.24.0.10", {"start": v(592.93, 9.9) * mm, "mid": v(590.1, 9.9) * mm, "end": v(590.1, 7.07) * mm});
            skLineSegment(sketch, "E52.24.0.11", {"start": v(592.93, 9.9) * mm, "end": v(593.41, 9.41) * mm});
            skArc(sketch, "E52.24.0.12", {"start": v(590.59, 6.59) * mm, "mid": v(593.41, 6.59) * mm, "end": v(593.41, 9.41) * mm});
            skLineSegment(sketch, "E52.24.0.13", {"start": v(590.1, 7.07) * mm, "end": v(590.59, 6.59) * mm});
            skCircle(sketch, "E52.24.0.14", {"center": v(600, 0) * mm, "radius": 7 * mm});
            skArc(sketch, "E52.24.0.15", {"start": v(583.07, -9.9) * mm, "mid": v(585.9, -9.9) * mm, "end": v(585.9, -7.07) * mm});
            skArc(sketch, "E52.24.0.16", {"start": v(585.41, -6.59) * mm, "mid": v(582.59, -6.59) * mm, "end": v(582.59, -9.41) * mm});
            skLineSegment(sketch, "E52.24.0.17", {"start": v(585.41, -6.59) * mm, "end": v(585.9, -7.07) * mm});
            skLineSegment(sketch, "E52.24.0.18", {"start": v(582.59, -9.41) * mm, "end": v(583.07, -9.9) * mm});
            skArc(sketch, "E52.24.0.19", {"start": v(590.1, -7.07) * mm, "mid": v(590.1, -9.9) * mm, "end": v(592.93, -9.9) * mm});
            skLineSegment(sketch, "E52.24.0.20", {"start": v(592.93, -9.9) * mm, "end": v(593.41, -9.41) * mm});
            skArc(sketch, "E52.24.0.21", {"start": v(593.41, -9.41) * mm, "mid": v(593.41, -6.59) * mm, "end": v(590.59, -6.59) * mm});
            skCircle(sketch, "E52.24.0.22", {"center": v(592, -16) * mm, "radius": 2 * mm});
            skCircle(sketch, "E52.24.0.23", {"center": v(584, -16) * mm, "radius": 2 * mm});
            skLineSegment(sketch, "E52.24.0.24", {"start": v(590.1, -7.07) * mm, "end": v(590.59, -6.59) * mm});
            skCircle(sketch, "E52.24.0.25", {"center": v(588, 0) * mm, "radius": 2 * mm});
            skArc(sketch, "E52.24.0.26", {"start": v(602, -12) * mm, "mid": v(600, -10) * mm, "end": v(598, -12) * mm});
            skArc(sketch, "E52.24.0.27", {"start": v(598, -16) * mm, "mid": v(600, -18) * mm, "end": v(602, -16) * mm});
            skLineSegment(sketch, "E52.24.0.28", {"start": v(598, -12) * mm, "end": v(598, -16) * mm});
            skLineSegment(sketch, "E52.24.0.29", {"start": v(602, -16) * mm, "end": v(602, -12) * mm});
            skArc(sketch, "E52.25.0.0", {"start": v(626, 16) * mm, "mid": v(624, 18) * mm, "end": v(622, 16) * mm});
            skLineSegment(sketch, "E52.25.0.1", {"start": v(626, 16) * mm, "end": v(626, 12) * mm});
            skLineSegment(sketch, "E52.25.0.2", {"start": v(622, 16) * mm, "end": v(622, 12) * mm});
            skArc(sketch, "E52.25.0.3", {"start": v(622, 12) * mm, "mid": v(624, 10) * mm, "end": v(626, 12) * mm});
            skCircle(sketch, "E52.25.0.4", {"center": v(616, 16) * mm, "radius": 2 * mm});
            skCircle(sketch, "E52.25.0.5", {"center": v(608, 16) * mm, "radius": 2 * mm});
            skArc(sketch, "E52.25.0.6", {"start": v(609.9, 7.07) * mm, "mid": v(609.9, 9.9) * mm, "end": v(607.07, 9.9) * mm});
            skArc(sketch, "E52.25.0.7", {"start": v(606.59, 9.41) * mm, "mid": v(606.59, 6.59) * mm, "end": v(609.41, 6.59) * mm});
            skLineSegment(sketch, "E52.25.0.8", {"start": v(607.07, 9.9) * mm, "end": v(606.59, 9.41) * mm});
            skLineSegment(sketch, "E52.25.0.9", {"start": v(609.9, 7.07) * mm, "end": v(609.41, 6.59) * mm});
            skArc(sketch, "E52.25.0.10", {"start": v(616.93, 9.9) * mm, "mid": v(614.1, 9.9) * mm, "end": v(614.1, 7.07) * mm});
            skLineSegment(sketch, "E52.25.0.11", {"start": v(616.93, 9.9) * mm, "end": v(617.41, 9.41) * mm});
            skArc(sketch, "E52.25.0.12", {"start": v(614.59, 6.59) * mm, "mid": v(617.41, 6.59) * mm, "end": v(617.41, 9.41) * mm});
            skLineSegment(sketch, "E52.25.0.13", {"start": v(614.1, 7.07) * mm, "end": v(614.59, 6.59) * mm});
            skCircle(sketch, "E52.25.0.14", {"center": v(624, 0) * mm, "radius": 7 * mm});
            skArc(sketch, "E52.25.0.15", {"start": v(607.07, -9.9) * mm, "mid": v(609.9, -9.9) * mm, "end": v(609.9, -7.07) * mm});
            skArc(sketch, "E52.25.0.16", {"start": v(609.41, -6.59) * mm, "mid": v(606.59, -6.59) * mm, "end": v(606.59, -9.41) * mm});
            skLineSegment(sketch, "E52.25.0.17", {"start": v(609.41, -6.59) * mm, "end": v(609.9, -7.07) * mm});
            skLineSegment(sketch, "E52.25.0.18", {"start": v(606.59, -9.41) * mm, "end": v(607.07, -9.9) * mm});
            skArc(sketch, "E52.25.0.19", {"start": v(614.1, -7.07) * mm, "mid": v(614.1, -9.9) * mm, "end": v(616.93, -9.9) * mm});
            skLineSegment(sketch, "E52.25.0.20", {"start": v(616.93, -9.9) * mm, "end": v(617.41, -9.41) * mm});
            skArc(sketch, "E52.25.0.21", {"start": v(617.41, -9.41) * mm, "mid": v(617.41, -6.59) * mm, "end": v(614.59, -6.59) * mm});
            skCircle(sketch, "E52.25.0.22", {"center": v(616, -16) * mm, "radius": 2 * mm});
            skCircle(sketch, "E52.25.0.23", {"center": v(608, -16) * mm, "radius": 2 * mm});
            skLineSegment(sketch, "E52.25.0.24", {"start": v(614.1, -7.07) * mm, "end": v(614.59, -6.59) * mm});
            skCircle(sketch, "E52.25.0.25", {"center": v(612, 0) * mm, "radius": 2 * mm});
            skArc(sketch, "E52.25.0.26", {"start": v(626, -12) * mm, "mid": v(624, -10) * mm, "end": v(622, -12) * mm});
            skArc(sketch, "E52.25.0.27", {"start": v(622, -16) * mm, "mid": v(624, -18) * mm, "end": v(626, -16) * mm});
            skLineSegment(sketch, "E52.25.0.28", {"start": v(622, -12) * mm, "end": v(622, -16) * mm});
            skLineSegment(sketch, "E52.25.0.29", {"start": v(626, -16) * mm, "end": v(626, -12) * mm});
            skArc(sketch, "E52.26.0.0", {"start": v(650, 16) * mm, "mid": v(648, 18) * mm, "end": v(646, 16) * mm});
            skLineSegment(sketch, "E52.26.0.1", {"start": v(650, 16) * mm, "end": v(650, 12) * mm});
            skLineSegment(sketch, "E52.26.0.2", {"start": v(646, 16) * mm, "end": v(646, 12) * mm});
            skArc(sketch, "E52.26.0.3", {"start": v(646, 12) * mm, "mid": v(648, 10) * mm, "end": v(650, 12) * mm});
            skCircle(sketch, "E52.26.0.4", {"center": v(640, 16) * mm, "radius": 2 * mm});
            skCircle(sketch, "E52.26.0.5", {"center": v(632, 16) * mm, "radius": 2 * mm});
            skArc(sketch, "E52.26.0.6", {"start": v(633.9, 7.07) * mm, "mid": v(633.9, 9.9) * mm, "end": v(631.07, 9.9) * mm});
            skArc(sketch, "E52.26.0.7", {"start": v(630.59, 9.41) * mm, "mid": v(630.59, 6.59) * mm, "end": v(633.41, 6.59) * mm});
            skLineSegment(sketch, "E52.26.0.8", {"start": v(631.07, 9.9) * mm, "end": v(630.59, 9.41) * mm});
            skLineSegment(sketch, "E52.26.0.9", {"start": v(633.9, 7.07) * mm, "end": v(633.41, 6.59) * mm});
            skArc(sketch, "E52.26.0.10", {"start": v(640.93, 9.9) * mm, "mid": v(638.1, 9.9) * mm, "end": v(638.1, 7.07) * mm});
            skLineSegment(sketch, "E52.26.0.11", {"start": v(640.93, 9.9) * mm, "end": v(641.41, 9.41) * mm});
            skArc(sketch, "E52.26.0.12", {"start": v(638.59, 6.59) * mm, "mid": v(641.41, 6.59) * mm, "end": v(641.41, 9.41) * mm});
            skLineSegment(sketch, "E52.26.0.13", {"start": v(638.1, 7.07) * mm, "end": v(638.59, 6.59) * mm});
            skCircle(sketch, "E52.26.0.14", {"center": v(648, 0) * mm, "radius": 7 * mm});
            skArc(sketch, "E52.26.0.15", {"start": v(631.07, -9.9) * mm, "mid": v(633.9, -9.9) * mm, "end": v(633.9, -7.07) * mm});
            skArc(sketch, "E52.26.0.16", {"start": v(633.41, -6.59) * mm, "mid": v(630.59, -6.59) * mm, "end": v(630.59, -9.41) * mm});
            skLineSegment(sketch, "E52.26.0.17", {"start": v(633.41, -6.59) * mm, "end": v(633.9, -7.07) * mm});
            skLineSegment(sketch, "E52.26.0.18", {"start": v(630.59, -9.41) * mm, "end": v(631.07, -9.9) * mm});
            skArc(sketch, "E52.26.0.19", {"start": v(638.1, -7.07) * mm, "mid": v(638.1, -9.9) * mm, "end": v(640.93, -9.9) * mm});
            skLineSegment(sketch, "E52.26.0.20", {"start": v(640.93, -9.9) * mm, "end": v(641.41, -9.41) * mm});
            skArc(sketch, "E52.26.0.21", {"start": v(641.41, -9.41) * mm, "mid": v(641.41, -6.59) * mm, "end": v(638.59, -6.59) * mm});
            skCircle(sketch, "E52.26.0.22", {"center": v(640, -16) * mm, "radius": 2 * mm});
            skCircle(sketch, "E52.26.0.23", {"center": v(632, -16) * mm, "radius": 2 * mm});
            skLineSegment(sketch, "E52.26.0.24", {"start": v(638.1, -7.07) * mm, "end": v(638.59, -6.59) * mm});
            skCircle(sketch, "E52.26.0.25", {"center": v(636, 0) * mm, "radius": 2 * mm});
            skArc(sketch, "E52.26.0.26", {"start": v(650, -12) * mm, "mid": v(648, -10) * mm, "end": v(646, -12) * mm});
            skArc(sketch, "E52.26.0.27", {"start": v(646, -16) * mm, "mid": v(648, -18) * mm, "end": v(650, -16) * mm});
            skLineSegment(sketch, "E52.26.0.28", {"start": v(646, -12) * mm, "end": v(646, -16) * mm});
            skLineSegment(sketch, "E52.26.0.29", {"start": v(650, -16) * mm, "end": v(650, -12) * mm});
            skArc(sketch, "E52.27.0.0", {"start": v(674, 16) * mm, "mid": v(672, 18) * mm, "end": v(670, 16) * mm});
            skLineSegment(sketch, "E52.27.0.1", {"start": v(674, 16) * mm, "end": v(674, 12) * mm});
            skLineSegment(sketch, "E52.27.0.2", {"start": v(670, 16) * mm, "end": v(670, 12) * mm});
            skArc(sketch, "E52.27.0.3", {"start": v(670, 12) * mm, "mid": v(672, 10) * mm, "end": v(674, 12) * mm});
            skCircle(sketch, "E52.27.0.4", {"center": v(664, 16) * mm, "radius": 2 * mm});
            skCircle(sketch, "E52.27.0.5", {"center": v(656, 16) * mm, "radius": 2 * mm});
            skArc(sketch, "E52.27.0.6", {"start": v(657.9, 7.07) * mm, "mid": v(657.9, 9.9) * mm, "end": v(655.07, 9.9) * mm});
            skArc(sketch, "E52.27.0.7", {"start": v(654.59, 9.41) * mm, "mid": v(654.59, 6.59) * mm, "end": v(657.41, 6.59) * mm});
            skLineSegment(sketch, "E52.27.0.8", {"start": v(655.07, 9.9) * mm, "end": v(654.59, 9.41) * mm});
            skLineSegment(sketch, "E52.27.0.9", {"start": v(657.9, 7.07) * mm, "end": v(657.41, 6.59) * mm});
            skArc(sketch, "E52.27.0.10", {"start": v(664.93, 9.9) * mm, "mid": v(662.1, 9.9) * mm, "end": v(662.1, 7.07) * mm});
            skLineSegment(sketch, "E52.27.0.11", {"start": v(664.93, 9.9) * mm, "end": v(665.41, 9.41) * mm});
            skArc(sketch, "E52.27.0.12", {"start": v(662.59, 6.59) * mm, "mid": v(665.41, 6.59) * mm, "end": v(665.41, 9.41) * mm});
            skLineSegment(sketch, "E52.27.0.13", {"start": v(662.1, 7.07) * mm, "end": v(662.59, 6.59) * mm});
            skCircle(sketch, "E52.27.0.14", {"center": v(672, 0) * mm, "radius": 7 * mm});
            skArc(sketch, "E52.27.0.15", {"start": v(655.07, -9.9) * mm, "mid": v(657.9, -9.9) * mm, "end": v(657.9, -7.07) * mm});
            skArc(sketch, "E52.27.0.16", {"start": v(657.41, -6.59) * mm, "mid": v(654.59, -6.59) * mm, "end": v(654.59, -9.41) * mm});
            skLineSegment(sketch, "E52.27.0.17", {"start": v(657.41, -6.59) * mm, "end": v(657.9, -7.07) * mm});
            skLineSegment(sketch, "E52.27.0.18", {"start": v(654.59, -9.41) * mm, "end": v(655.07, -9.9) * mm});
            skArc(sketch, "E52.27.0.19", {"start": v(662.1, -7.07) * mm, "mid": v(662.1, -9.9) * mm, "end": v(664.93, -9.9) * mm});
            skLineSegment(sketch, "E52.27.0.20", {"start": v(664.93, -9.9) * mm, "end": v(665.41, -9.41) * mm});
            skArc(sketch, "E52.27.0.21", {"start": v(665.41, -9.41) * mm, "mid": v(665.41, -6.59) * mm, "end": v(662.59, -6.59) * mm});
            skCircle(sketch, "E52.27.0.22", {"center": v(664, -16) * mm, "radius": 2 * mm});
            skCircle(sketch, "E52.27.0.23", {"center": v(656, -16) * mm, "radius": 2 * mm});
            skLineSegment(sketch, "E52.27.0.24", {"start": v(662.1, -7.07) * mm, "end": v(662.59, -6.59) * mm});
            skCircle(sketch, "E52.27.0.25", {"center": v(660, 0) * mm, "radius": 2 * mm});
            skArc(sketch, "E52.27.0.26", {"start": v(674, -12) * mm, "mid": v(672, -10) * mm, "end": v(670, -12) * mm});
            skArc(sketch, "E52.27.0.27", {"start": v(670, -16) * mm, "mid": v(672, -18) * mm, "end": v(674, -16) * mm});
            skLineSegment(sketch, "E52.27.0.28", {"start": v(670, -12) * mm, "end": v(670, -16) * mm});
            skLineSegment(sketch, "E52.27.0.29", {"start": v(674, -16) * mm, "end": v(674, -12) * mm});
            skArc(sketch, "E52.28.0.0", {"start": v(698, 16) * mm, "mid": v(696, 18) * mm, "end": v(694, 16) * mm});
            skLineSegment(sketch, "E52.28.0.1", {"start": v(698, 16) * mm, "end": v(698, 12) * mm});
            skLineSegment(sketch, "E52.28.0.2", {"start": v(694, 16) * mm, "end": v(694, 12) * mm});
            skArc(sketch, "E52.28.0.3", {"start": v(694, 12) * mm, "mid": v(696, 10) * mm, "end": v(698, 12) * mm});
            skCircle(sketch, "E52.28.0.4", {"center": v(688, 16) * mm, "radius": 2 * mm});
            skCircle(sketch, "E52.28.0.5", {"center": v(680, 16) * mm, "radius": 2 * mm});
            skArc(sketch, "E52.28.0.6", {"start": v(681.9, 7.07) * mm, "mid": v(681.9, 9.9) * mm, "end": v(679.07, 9.9) * mm});
            skArc(sketch, "E52.28.0.7", {"start": v(678.59, 9.41) * mm, "mid": v(678.59, 6.59) * mm, "end": v(681.41, 6.59) * mm});
            skLineSegment(sketch, "E52.28.0.8", {"start": v(679.07, 9.9) * mm, "end": v(678.59, 9.41) * mm});
            skLineSegment(sketch, "E52.28.0.9", {"start": v(681.9, 7.07) * mm, "end": v(681.41, 6.59) * mm});
            skArc(sketch, "E52.28.0.10", {"start": v(688.93, 9.9) * mm, "mid": v(686.1, 9.9) * mm, "end": v(686.1, 7.07) * mm});
            skLineSegment(sketch, "E52.28.0.11", {"start": v(688.93, 9.9) * mm, "end": v(689.41, 9.41) * mm});
            skArc(sketch, "E52.28.0.12", {"start": v(686.59, 6.59) * mm, "mid": v(689.41, 6.59) * mm, "end": v(689.41, 9.41) * mm});
            skLineSegment(sketch, "E52.28.0.13", {"start": v(686.1, 7.07) * mm, "end": v(686.59, 6.59) * mm});
            skCircle(sketch, "E52.28.0.14", {"center": v(696, 0) * mm, "radius": 7 * mm});
            skArc(sketch, "E52.28.0.15", {"start": v(679.07, -9.9) * mm, "mid": v(681.9, -9.9) * mm, "end": v(681.9, -7.07) * mm});
            skArc(sketch, "E52.28.0.16", {"start": v(681.41, -6.59) * mm, "mid": v(678.59, -6.59) * mm, "end": v(678.59, -9.41) * mm});
            skLineSegment(sketch, "E52.28.0.17", {"start": v(681.41, -6.59) * mm, "end": v(681.9, -7.07) * mm});
            skLineSegment(sketch, "E52.28.0.18", {"start": v(678.59, -9.41) * mm, "end": v(679.07, -9.9) * mm});
            skArc(sketch, "E52.28.0.19", {"start": v(686.1, -7.07) * mm, "mid": v(686.1, -9.9) * mm, "end": v(688.93, -9.9) * mm});
            skLineSegment(sketch, "E52.28.0.20", {"start": v(688.93, -9.9) * mm, "end": v(689.41, -9.41) * mm});
            skArc(sketch, "E52.28.0.21", {"start": v(689.41, -9.41) * mm, "mid": v(689.41, -6.59) * mm, "end": v(686.59, -6.59) * mm});
            skCircle(sketch, "E52.28.0.22", {"center": v(688, -16) * mm, "radius": 2 * mm});
            skCircle(sketch, "E52.28.0.23", {"center": v(680, -16) * mm, "radius": 2 * mm});
            skLineSegment(sketch, "E52.28.0.24", {"start": v(686.1, -7.07) * mm, "end": v(686.59, -6.59) * mm});
            skCircle(sketch, "E52.28.0.25", {"center": v(684, 0) * mm, "radius": 2 * mm});
            skArc(sketch, "E52.28.0.26", {"start": v(698, -12) * mm, "mid": v(696, -10) * mm, "end": v(694, -12) * mm});
            skArc(sketch, "E52.28.0.27", {"start": v(694, -16) * mm, "mid": v(696, -18) * mm, "end": v(698, -16) * mm});
            skLineSegment(sketch, "E52.28.0.28", {"start": v(694, -12) * mm, "end": v(694, -16) * mm});
            skLineSegment(sketch, "E52.28.0.29", {"start": v(698, -16) * mm, "end": v(698, -12) * mm});
            skArc(sketch, "E52.29.0.0", {"start": v(722, 16) * mm, "mid": v(720, 18) * mm, "end": v(718, 16) * mm});
            skLineSegment(sketch, "E52.29.0.1", {"start": v(722, 16) * mm, "end": v(722, 12) * mm});
            skLineSegment(sketch, "E52.29.0.2", {"start": v(718, 16) * mm, "end": v(718, 12) * mm});
            skArc(sketch, "E52.29.0.3", {"start": v(718, 12) * mm, "mid": v(720, 10) * mm, "end": v(722, 12) * mm});
            skCircle(sketch, "E52.29.0.4", {"center": v(712, 16) * mm, "radius": 2 * mm});
            skCircle(sketch, "E52.29.0.5", {"center": v(704, 16) * mm, "radius": 2 * mm});
            skArc(sketch, "E52.29.0.6", {"start": v(705.9, 7.07) * mm, "mid": v(705.9, 9.9) * mm, "end": v(703.07, 9.9) * mm});
            skArc(sketch, "E52.29.0.7", {"start": v(702.59, 9.41) * mm, "mid": v(702.59, 6.59) * mm, "end": v(705.41, 6.59) * mm});
            skLineSegment(sketch, "E52.29.0.8", {"start": v(703.07, 9.9) * mm, "end": v(702.59, 9.41) * mm});
            skLineSegment(sketch, "E52.29.0.9", {"start": v(705.9, 7.07) * mm, "end": v(705.41, 6.59) * mm});
            skArc(sketch, "E52.29.0.10", {"start": v(712.93, 9.9) * mm, "mid": v(710.1, 9.9) * mm, "end": v(710.1, 7.07) * mm});
            skLineSegment(sketch, "E52.29.0.11", {"start": v(712.93, 9.9) * mm, "end": v(713.41, 9.41) * mm});
            skArc(sketch, "E52.29.0.12", {"start": v(710.59, 6.59) * mm, "mid": v(713.41, 6.59) * mm, "end": v(713.41, 9.41) * mm});
            skLineSegment(sketch, "E52.29.0.13", {"start": v(710.1, 7.07) * mm, "end": v(710.59, 6.59) * mm});
            skCircle(sketch, "E52.29.0.14", {"center": v(720, 0) * mm, "radius": 7 * mm});
            skArc(sketch, "E52.29.0.15", {"start": v(703.07, -9.9) * mm, "mid": v(705.9, -9.9) * mm, "end": v(705.9, -7.07) * mm});
            skArc(sketch, "E52.29.0.16", {"start": v(705.41, -6.59) * mm, "mid": v(702.59, -6.59) * mm, "end": v(702.59, -9.41) * mm});
            skLineSegment(sketch, "E52.29.0.17", {"start": v(705.41, -6.59) * mm, "end": v(705.9, -7.07) * mm});
            skLineSegment(sketch, "E52.29.0.18", {"start": v(702.59, -9.41) * mm, "end": v(703.07, -9.9) * mm});
            skArc(sketch, "E52.29.0.19", {"start": v(710.1, -7.07) * mm, "mid": v(710.1, -9.9) * mm, "end": v(712.93, -9.9) * mm});
            skLineSegment(sketch, "E52.29.0.20", {"start": v(712.93, -9.9) * mm, "end": v(713.41, -9.41) * mm});
            skArc(sketch, "E52.29.0.21", {"start": v(713.41, -9.41) * mm, "mid": v(713.41, -6.59) * mm, "end": v(710.59, -6.59) * mm});
            skCircle(sketch, "E52.29.0.22", {"center": v(712, -16) * mm, "radius": 2 * mm});
            skCircle(sketch, "E52.29.0.23", {"center": v(704, -16) * mm, "radius": 2 * mm});
            skLineSegment(sketch, "E52.29.0.24", {"start": v(710.1, -7.07) * mm, "end": v(710.59, -6.59) * mm});
            skCircle(sketch, "E52.29.0.25", {"center": v(708, 0) * mm, "radius": 2 * mm});
            skArc(sketch, "E52.29.0.26", {"start": v(722, -12) * mm, "mid": v(720, -10) * mm, "end": v(718, -12) * mm});
            skArc(sketch, "E52.29.0.27", {"start": v(718, -16) * mm, "mid": v(720, -18) * mm, "end": v(722, -16) * mm});
            skLineSegment(sketch, "E52.29.0.28", {"start": v(718, -12) * mm, "end": v(718, -16) * mm});
            skLineSegment(sketch, "E52.29.0.29", {"start": v(722, -16) * mm, "end": v(722, -12) * mm});
            skArc(sketch, "E52.30.0.0", {"start": v(746, 16) * mm, "mid": v(744, 18) * mm, "end": v(742, 16) * mm});
            skLineSegment(sketch, "E52.30.0.1", {"start": v(746, 16) * mm, "end": v(746, 12) * mm});
            skLineSegment(sketch, "E52.30.0.2", {"start": v(742, 16) * mm, "end": v(742, 12) * mm});
            skArc(sketch, "E52.30.0.3", {"start": v(742, 12) * mm, "mid": v(744, 10) * mm, "end": v(746, 12) * mm});
            skCircle(sketch, "E52.30.0.4", {"center": v(736, 16) * mm, "radius": 2 * mm});
            skCircle(sketch, "E52.30.0.5", {"center": v(728, 16) * mm, "radius": 2 * mm});
            skArc(sketch, "E52.30.0.6", {"start": v(729.9, 7.07) * mm, "mid": v(729.9, 9.9) * mm, "end": v(727.07, 9.9) * mm});
            skArc(sketch, "E52.30.0.7", {"start": v(726.59, 9.41) * mm, "mid": v(726.59, 6.59) * mm, "end": v(729.41, 6.59) * mm});
            skLineSegment(sketch, "E52.30.0.8", {"start": v(727.07, 9.9) * mm, "end": v(726.59, 9.41) * mm});
            skLineSegment(sketch, "E52.30.0.9", {"start": v(729.9, 7.07) * mm, "end": v(729.41, 6.59) * mm});
            skArc(sketch, "E52.30.0.10", {"start": v(736.93, 9.9) * mm, "mid": v(734.1, 9.9) * mm, "end": v(734.1, 7.07) * mm});
            skLineSegment(sketch, "E52.30.0.11", {"start": v(736.93, 9.9) * mm, "end": v(737.41, 9.41) * mm});
            skArc(sketch, "E52.30.0.12", {"start": v(734.59, 6.59) * mm, "mid": v(737.41, 6.59) * mm, "end": v(737.41, 9.41) * mm});
            skLineSegment(sketch, "E52.30.0.13", {"start": v(734.1, 7.07) * mm, "end": v(734.59, 6.59) * mm});
            skCircle(sketch, "E52.30.0.14", {"center": v(744, 0) * mm, "radius": 7 * mm});
            skArc(sketch, "E52.30.0.15", {"start": v(727.07, -9.9) * mm, "mid": v(729.9, -9.9) * mm, "end": v(729.9, -7.07) * mm});
            skArc(sketch, "E52.30.0.16", {"start": v(729.41, -6.59) * mm, "mid": v(726.59, -6.59) * mm, "end": v(726.59, -9.41) * mm});
            skLineSegment(sketch, "E52.30.0.17", {"start": v(729.41, -6.59) * mm, "end": v(729.9, -7.07) * mm});
            skLineSegment(sketch, "E52.30.0.18", {"start": v(726.59, -9.41) * mm, "end": v(727.07, -9.9) * mm});
            skArc(sketch, "E52.30.0.19", {"start": v(734.1, -7.07) * mm, "mid": v(734.1, -9.9) * mm, "end": v(736.93, -9.9) * mm});
            skLineSegment(sketch, "E52.30.0.20", {"start": v(736.93, -9.9) * mm, "end": v(737.41, -9.41) * mm});
            skArc(sketch, "E52.30.0.21", {"start": v(737.41, -9.41) * mm, "mid": v(737.41, -6.59) * mm, "end": v(734.59, -6.59) * mm});
            skCircle(sketch, "E52.30.0.22", {"center": v(736, -16) * mm, "radius": 2 * mm});
            skCircle(sketch, "E52.30.0.23", {"center": v(728, -16) * mm, "radius": 2 * mm});
            skLineSegment(sketch, "E52.30.0.24", {"start": v(734.1, -7.07) * mm, "end": v(734.59, -6.59) * mm});
            skCircle(sketch, "E52.30.0.25", {"center": v(732, 0) * mm, "radius": 2 * mm});
            skArc(sketch, "E52.30.0.26", {"start": v(746, -12) * mm, "mid": v(744, -10) * mm, "end": v(742, -12) * mm});
            skArc(sketch, "E52.30.0.27", {"start": v(742, -16) * mm, "mid": v(744, -18) * mm, "end": v(746, -16) * mm});
            skLineSegment(sketch, "E52.30.0.28", {"start": v(742, -12) * mm, "end": v(742, -16) * mm});
            skLineSegment(sketch, "E52.30.0.29", {"start": v(746, -16) * mm, "end": v(746, -12) * mm});
            skArc(sketch, "E52.31.0.0", {"start": v(770, 16) * mm, "mid": v(768, 18) * mm, "end": v(766, 16) * mm});
            skLineSegment(sketch, "E52.31.0.1", {"start": v(770, 16) * mm, "end": v(770, 12) * mm});
            skLineSegment(sketch, "E52.31.0.2", {"start": v(766, 16) * mm, "end": v(766, 12) * mm});
            skArc(sketch, "E52.31.0.3", {"start": v(766, 12) * mm, "mid": v(768, 10) * mm, "end": v(770, 12) * mm});
            skCircle(sketch, "E52.31.0.4", {"center": v(760, 16) * mm, "radius": 2 * mm});
            skCircle(sketch, "E52.31.0.5", {"center": v(752, 16) * mm, "radius": 2 * mm});
            skArc(sketch, "E52.31.0.6", {"start": v(753.9, 7.07) * mm, "mid": v(753.9, 9.9) * mm, "end": v(751.07, 9.9) * mm});
            skArc(sketch, "E52.31.0.7", {"start": v(750.59, 9.41) * mm, "mid": v(750.59, 6.59) * mm, "end": v(753.41, 6.59) * mm});
            skLineSegment(sketch, "E52.31.0.8", {"start": v(751.07, 9.9) * mm, "end": v(750.59, 9.41) * mm});
            skLineSegment(sketch, "E52.31.0.9", {"start": v(753.9, 7.07) * mm, "end": v(753.41, 6.59) * mm});
            skArc(sketch, "E52.31.0.10", {"start": v(760.93, 9.9) * mm, "mid": v(758.1, 9.9) * mm, "end": v(758.1, 7.07) * mm});
            skLineSegment(sketch, "E52.31.0.11", {"start": v(760.93, 9.9) * mm, "end": v(761.41, 9.41) * mm});
            skArc(sketch, "E52.31.0.12", {"start": v(758.59, 6.59) * mm, "mid": v(761.41, 6.59) * mm, "end": v(761.41, 9.41) * mm});
            skLineSegment(sketch, "E52.31.0.13", {"start": v(758.1, 7.07) * mm, "end": v(758.59, 6.59) * mm});
            skCircle(sketch, "E52.31.0.14", {"center": v(768, 0) * mm, "radius": 7 * mm});
            skArc(sketch, "E52.31.0.15", {"start": v(751.07, -9.9) * mm, "mid": v(753.9, -9.9) * mm, "end": v(753.9, -7.07) * mm});
            skArc(sketch, "E52.31.0.16", {"start": v(753.41, -6.59) * mm, "mid": v(750.59, -6.59) * mm, "end": v(750.59, -9.41) * mm});
            skLineSegment(sketch, "E52.31.0.17", {"start": v(753.41, -6.59) * mm, "end": v(753.9, -7.07) * mm});
            skLineSegment(sketch, "E52.31.0.18", {"start": v(750.59, -9.41) * mm, "end": v(751.07, -9.9) * mm});
            skArc(sketch, "E52.31.0.19", {"start": v(758.1, -7.07) * mm, "mid": v(758.1, -9.9) * mm, "end": v(760.93, -9.9) * mm});
            skLineSegment(sketch, "E52.31.0.20", {"start": v(760.93, -9.9) * mm, "end": v(761.41, -9.41) * mm});
            skArc(sketch, "E52.31.0.21", {"start": v(761.41, -9.41) * mm, "mid": v(761.41, -6.59) * mm, "end": v(758.59, -6.59) * mm});
            skCircle(sketch, "E52.31.0.22", {"center": v(760, -16) * mm, "radius": 2 * mm});
            skCircle(sketch, "E52.31.0.23", {"center": v(752, -16) * mm, "radius": 2 * mm});
            skLineSegment(sketch, "E52.31.0.24", {"start": v(758.1, -7.07) * mm, "end": v(758.59, -6.59) * mm});
            skCircle(sketch, "E52.31.0.25", {"center": v(756, 0) * mm, "radius": 2 * mm});
            skArc(sketch, "E52.31.0.26", {"start": v(770, -12) * mm, "mid": v(768, -10) * mm, "end": v(766, -12) * mm});
            skArc(sketch, "E52.31.0.27", {"start": v(766, -16) * mm, "mid": v(768, -18) * mm, "end": v(770, -16) * mm});
            skLineSegment(sketch, "E52.31.0.28", {"start": v(766, -12) * mm, "end": v(766, -16) * mm});
            skLineSegment(sketch, "E52.31.0.29", {"start": v(770, -16) * mm, "end": v(770, -12) * mm});
            skArc(sketch, "E52.32.0.0", {"start": v(794, 16) * mm, "mid": v(792, 18) * mm, "end": v(790, 16) * mm});
            skLineSegment(sketch, "E52.32.0.1", {"start": v(794, 16) * mm, "end": v(794, 12) * mm});
            skLineSegment(sketch, "E52.32.0.2", {"start": v(790, 16) * mm, "end": v(790, 12) * mm});
            skArc(sketch, "E52.32.0.3", {"start": v(790, 12) * mm, "mid": v(792, 10) * mm, "end": v(794, 12) * mm});
            skCircle(sketch, "E52.32.0.4", {"center": v(784, 16) * mm, "radius": 2 * mm});
            skCircle(sketch, "E52.32.0.5", {"center": v(776, 16) * mm, "radius": 2 * mm});
            skArc(sketch, "E52.32.0.6", {"start": v(777.9, 7.07) * mm, "mid": v(777.9, 9.9) * mm, "end": v(775.07, 9.9) * mm});
            skArc(sketch, "E52.32.0.7", {"start": v(774.59, 9.41) * mm, "mid": v(774.59, 6.59) * mm, "end": v(777.41, 6.59) * mm});
            skLineSegment(sketch, "E52.32.0.8", {"start": v(775.07, 9.9) * mm, "end": v(774.59, 9.41) * mm});
            skLineSegment(sketch, "E52.32.0.9", {"start": v(777.9, 7.07) * mm, "end": v(777.41, 6.59) * mm});
            skArc(sketch, "E52.32.0.10", {"start": v(784.93, 9.9) * mm, "mid": v(782.1, 9.9) * mm, "end": v(782.1, 7.07) * mm});
            skLineSegment(sketch, "E52.32.0.11", {"start": v(784.93, 9.9) * mm, "end": v(785.41, 9.41) * mm});
            skArc(sketch, "E52.32.0.12", {"start": v(782.59, 6.59) * mm, "mid": v(785.41, 6.59) * mm, "end": v(785.41, 9.41) * mm});
            skLineSegment(sketch, "E52.32.0.13", {"start": v(782.1, 7.07) * mm, "end": v(782.59, 6.59) * mm});
            skCircle(sketch, "E52.32.0.14", {"center": v(792, 0) * mm, "radius": 7 * mm});
            skArc(sketch, "E52.32.0.15", {"start": v(775.07, -9.9) * mm, "mid": v(777.9, -9.9) * mm, "end": v(777.9, -7.07) * mm});
            skArc(sketch, "E52.32.0.16", {"start": v(777.41, -6.59) * mm, "mid": v(774.59, -6.59) * mm, "end": v(774.59, -9.41) * mm});
            skLineSegment(sketch, "E52.32.0.17", {"start": v(777.41, -6.59) * mm, "end": v(777.9, -7.07) * mm});
            skLineSegment(sketch, "E52.32.0.18", {"start": v(774.59, -9.41) * mm, "end": v(775.07, -9.9) * mm});
            skArc(sketch, "E52.32.0.19", {"start": v(782.1, -7.07) * mm, "mid": v(782.1, -9.9) * mm, "end": v(784.93, -9.9) * mm});
            skLineSegment(sketch, "E52.32.0.20", {"start": v(784.93, -9.9) * mm, "end": v(785.41, -9.41) * mm});
            skArc(sketch, "E52.32.0.21", {"start": v(785.41, -9.41) * mm, "mid": v(785.41, -6.59) * mm, "end": v(782.59, -6.59) * mm});
            skCircle(sketch, "E52.32.0.22", {"center": v(784, -16) * mm, "radius": 2 * mm});
            skCircle(sketch, "E52.32.0.23", {"center": v(776, -16) * mm, "radius": 2 * mm});
            skLineSegment(sketch, "E52.32.0.24", {"start": v(782.1, -7.07) * mm, "end": v(782.59, -6.59) * mm});
            skCircle(sketch, "E52.32.0.25", {"center": v(780, 0) * mm, "radius": 2 * mm});
            skArc(sketch, "E52.32.0.26", {"start": v(794, -12) * mm, "mid": v(792, -10) * mm, "end": v(790, -12) * mm});
            skArc(sketch, "E52.32.0.27", {"start": v(790, -16) * mm, "mid": v(792, -18) * mm, "end": v(794, -16) * mm});
            skLineSegment(sketch, "E52.32.0.28", {"start": v(790, -12) * mm, "end": v(790, -16) * mm});
            skLineSegment(sketch, "E52.32.0.29", {"start": v(794, -16) * mm, "end": v(794, -12) * mm});
            skArc(sketch, "E52.33.0.0", {"start": v(818, 16) * mm, "mid": v(816, 18) * mm, "end": v(814, 16) * mm});
            skLineSegment(sketch, "E52.33.0.1", {"start": v(818, 16) * mm, "end": v(818, 12) * mm});
            skLineSegment(sketch, "E52.33.0.2", {"start": v(814, 16) * mm, "end": v(814, 12) * mm});
            skArc(sketch, "E52.33.0.3", {"start": v(814, 12) * mm, "mid": v(816, 10) * mm, "end": v(818, 12) * mm});
            skCircle(sketch, "E52.33.0.4", {"center": v(808, 16) * mm, "radius": 2 * mm});
            skCircle(sketch, "E52.33.0.5", {"center": v(800, 16) * mm, "radius": 2 * mm});
            skArc(sketch, "E52.33.0.6", {"start": v(801.9, 7.07) * mm, "mid": v(801.9, 9.9) * mm, "end": v(799.07, 9.9) * mm});
            skArc(sketch, "E52.33.0.7", {"start": v(798.59, 9.41) * mm, "mid": v(798.59, 6.59) * mm, "end": v(801.41, 6.59) * mm});
            skLineSegment(sketch, "E52.33.0.8", {"start": v(799.07, 9.9) * mm, "end": v(798.59, 9.41) * mm});
            skLineSegment(sketch, "E52.33.0.9", {"start": v(801.9, 7.07) * mm, "end": v(801.41, 6.59) * mm});
            skArc(sketch, "E52.33.0.10", {"start": v(808.93, 9.9) * mm, "mid": v(806.1, 9.9) * mm, "end": v(806.1, 7.07) * mm});
            skLineSegment(sketch, "E52.33.0.11", {"start": v(808.93, 9.9) * mm, "end": v(809.41, 9.41) * mm});
            skArc(sketch, "E52.33.0.12", {"start": v(806.59, 6.59) * mm, "mid": v(809.41, 6.59) * mm, "end": v(809.41, 9.41) * mm});
            skLineSegment(sketch, "E52.33.0.13", {"start": v(806.1, 7.07) * mm, "end": v(806.59, 6.59) * mm});
            skCircle(sketch, "E52.33.0.14", {"center": v(816, 0) * mm, "radius": 7 * mm});
            skArc(sketch, "E52.33.0.15", {"start": v(799.07, -9.9) * mm, "mid": v(801.9, -9.9) * mm, "end": v(801.9, -7.07) * mm});
            skArc(sketch, "E52.33.0.16", {"start": v(801.41, -6.59) * mm, "mid": v(798.59, -6.59) * mm, "end": v(798.59, -9.41) * mm});
            skLineSegment(sketch, "E52.33.0.17", {"start": v(801.41, -6.59) * mm, "end": v(801.9, -7.07) * mm});
            skLineSegment(sketch, "E52.33.0.18", {"start": v(798.59, -9.41) * mm, "end": v(799.07, -9.9) * mm});
            skArc(sketch, "E52.33.0.19", {"start": v(806.1, -7.07) * mm, "mid": v(806.1, -9.9) * mm, "end": v(808.93, -9.9) * mm});
            skLineSegment(sketch, "E52.33.0.20", {"start": v(808.93, -9.9) * mm, "end": v(809.41, -9.41) * mm});
            skArc(sketch, "E52.33.0.21", {"start": v(809.41, -9.41) * mm, "mid": v(809.41, -6.59) * mm, "end": v(806.59, -6.59) * mm});
            skCircle(sketch, "E52.33.0.22", {"center": v(808, -16) * mm, "radius": 2 * mm});
            skCircle(sketch, "E52.33.0.23", {"center": v(800, -16) * mm, "radius": 2 * mm});
            skLineSegment(sketch, "E52.33.0.24", {"start": v(806.1, -7.07) * mm, "end": v(806.59, -6.59) * mm});
            skCircle(sketch, "E52.33.0.25", {"center": v(804, 0) * mm, "radius": 2 * mm});
            skArc(sketch, "E52.33.0.26", {"start": v(818, -12) * mm, "mid": v(816, -10) * mm, "end": v(814, -12) * mm});
            skArc(sketch, "E52.33.0.27", {"start": v(814, -16) * mm, "mid": v(816, -18) * mm, "end": v(818, -16) * mm});
            skLineSegment(sketch, "E52.33.0.28", {"start": v(814, -12) * mm, "end": v(814, -16) * mm});
            skLineSegment(sketch, "E52.33.0.29", {"start": v(818, -16) * mm, "end": v(818, -12) * mm});
            skArc(sketch, "E52.34.0.0", {"start": v(842, 16) * mm, "mid": v(840, 18) * mm, "end": v(838, 16) * mm});
            skLineSegment(sketch, "E52.34.0.1", {"start": v(842, 16) * mm, "end": v(842, 12) * mm});
            skLineSegment(sketch, "E52.34.0.2", {"start": v(838, 16) * mm, "end": v(838, 12) * mm});
            skArc(sketch, "E52.34.0.3", {"start": v(838, 12) * mm, "mid": v(840, 10) * mm, "end": v(842, 12) * mm});
            skCircle(sketch, "E52.34.0.4", {"center": v(832, 16) * mm, "radius": 2 * mm});
            skCircle(sketch, "E52.34.0.5", {"center": v(824, 16) * mm, "radius": 2 * mm});
            skArc(sketch, "E52.34.0.6", {"start": v(825.9, 7.07) * mm, "mid": v(825.9, 9.9) * mm, "end": v(823.07, 9.9) * mm});
            skArc(sketch, "E52.34.0.7", {"start": v(822.59, 9.41) * mm, "mid": v(822.59, 6.59) * mm, "end": v(825.41, 6.59) * mm});
            skLineSegment(sketch, "E52.34.0.8", {"start": v(823.07, 9.9) * mm, "end": v(822.59, 9.41) * mm});
            skLineSegment(sketch, "E52.34.0.9", {"start": v(825.9, 7.07) * mm, "end": v(825.41, 6.59) * mm});
            skArc(sketch, "E52.34.0.10", {"start": v(832.93, 9.9) * mm, "mid": v(830.1, 9.9) * mm, "end": v(830.1, 7.07) * mm});
            skLineSegment(sketch, "E52.34.0.11", {"start": v(832.93, 9.9) * mm, "end": v(833.41, 9.41) * mm});
            skArc(sketch, "E52.34.0.12", {"start": v(830.59, 6.59) * mm, "mid": v(833.41, 6.59) * mm, "end": v(833.41, 9.41) * mm});
            skLineSegment(sketch, "E52.34.0.13", {"start": v(830.1, 7.07) * mm, "end": v(830.59, 6.59) * mm});
            skCircle(sketch, "E52.34.0.14", {"center": v(840, 0) * mm, "radius": 7 * mm});
            skArc(sketch, "E52.34.0.15", {"start": v(823.07, -9.9) * mm, "mid": v(825.9, -9.9) * mm, "end": v(825.9, -7.07) * mm});
            skArc(sketch, "E52.34.0.16", {"start": v(825.41, -6.59) * mm, "mid": v(822.59, -6.59) * mm, "end": v(822.59, -9.41) * mm});
            skLineSegment(sketch, "E52.34.0.17", {"start": v(825.41, -6.59) * mm, "end": v(825.9, -7.07) * mm});
            skLineSegment(sketch, "E52.34.0.18", {"start": v(822.59, -9.41) * mm, "end": v(823.07, -9.9) * mm});
            skArc(sketch, "E52.34.0.19", {"start": v(830.1, -7.07) * mm, "mid": v(830.1, -9.9) * mm, "end": v(832.93, -9.9) * mm});
            skLineSegment(sketch, "E52.34.0.20", {"start": v(832.93, -9.9) * mm, "end": v(833.41, -9.41) * mm});
            skArc(sketch, "E52.34.0.21", {"start": v(833.41, -9.41) * mm, "mid": v(833.41, -6.59) * mm, "end": v(830.59, -6.59) * mm});
            skCircle(sketch, "E52.34.0.22", {"center": v(832, -16) * mm, "radius": 2 * mm});
            skCircle(sketch, "E52.34.0.23", {"center": v(824, -16) * mm, "radius": 2 * mm});
            skLineSegment(sketch, "E52.34.0.24", {"start": v(830.1, -7.07) * mm, "end": v(830.59, -6.59) * mm});
            skCircle(sketch, "E52.34.0.25", {"center": v(828, 0) * mm, "radius": 2 * mm});
            skArc(sketch, "E52.34.0.26", {"start": v(842, -12) * mm, "mid": v(840, -10) * mm, "end": v(838, -12) * mm});
            skArc(sketch, "E52.34.0.27", {"start": v(838, -16) * mm, "mid": v(840, -18) * mm, "end": v(842, -16) * mm});
            skLineSegment(sketch, "E52.34.0.28", {"start": v(838, -12) * mm, "end": v(838, -16) * mm});
            skLineSegment(sketch, "E52.34.0.29", {"start": v(842, -16) * mm, "end": v(842, -12) * mm});
            skArc(sketch, "E52.35.0.0", {"start": v(866, 16) * mm, "mid": v(864, 18) * mm, "end": v(862, 16) * mm});
            skLineSegment(sketch, "E52.35.0.1", {"start": v(866, 16) * mm, "end": v(866, 12) * mm});
            skLineSegment(sketch, "E52.35.0.2", {"start": v(862, 16) * mm, "end": v(862, 12) * mm});
            skArc(sketch, "E52.35.0.3", {"start": v(862, 12) * mm, "mid": v(864, 10) * mm, "end": v(866, 12) * mm});
            skCircle(sketch, "E52.35.0.4", {"center": v(856, 16) * mm, "radius": 2 * mm});
            skCircle(sketch, "E52.35.0.5", {"center": v(848, 16) * mm, "radius": 2 * mm});
            skArc(sketch, "E52.35.0.6", {"start": v(849.9, 7.07) * mm, "mid": v(849.9, 9.9) * mm, "end": v(847.07, 9.9) * mm});
            skArc(sketch, "E52.35.0.7", {"start": v(846.59, 9.41) * mm, "mid": v(846.59, 6.59) * mm, "end": v(849.41, 6.59) * mm});
            skLineSegment(sketch, "E52.35.0.8", {"start": v(847.07, 9.9) * mm, "end": v(846.59, 9.41) * mm});
            skLineSegment(sketch, "E52.35.0.9", {"start": v(849.9, 7.07) * mm, "end": v(849.41, 6.59) * mm});
            skArc(sketch, "E52.35.0.10", {"start": v(856.93, 9.9) * mm, "mid": v(854.1, 9.9) * mm, "end": v(854.1, 7.07) * mm});
            skLineSegment(sketch, "E52.35.0.11", {"start": v(856.93, 9.9) * mm, "end": v(857.41, 9.41) * mm});
            skArc(sketch, "E52.35.0.12", {"start": v(854.59, 6.59) * mm, "mid": v(857.41, 6.59) * mm, "end": v(857.41, 9.41) * mm});
            skLineSegment(sketch, "E52.35.0.13", {"start": v(854.1, 7.07) * mm, "end": v(854.59, 6.59) * mm});
            skCircle(sketch, "E52.35.0.14", {"center": v(864, 0) * mm, "radius": 7 * mm});
            skArc(sketch, "E52.35.0.15", {"start": v(847.07, -9.9) * mm, "mid": v(849.9, -9.9) * mm, "end": v(849.9, -7.07) * mm});
            skArc(sketch, "E52.35.0.16", {"start": v(849.41, -6.59) * mm, "mid": v(846.59, -6.59) * mm, "end": v(846.59, -9.41) * mm});
            skLineSegment(sketch, "E52.35.0.17", {"start": v(849.41, -6.59) * mm, "end": v(849.9, -7.07) * mm});
            skLineSegment(sketch, "E52.35.0.18", {"start": v(846.59, -9.41) * mm, "end": v(847.07, -9.9) * mm});
            skArc(sketch, "E52.35.0.19", {"start": v(854.1, -7.07) * mm, "mid": v(854.1, -9.9) * mm, "end": v(856.93, -9.9) * mm});
            skLineSegment(sketch, "E52.35.0.20", {"start": v(856.93, -9.9) * mm, "end": v(857.41, -9.41) * mm});
            skArc(sketch, "E52.35.0.21", {"start": v(857.41, -9.41) * mm, "mid": v(857.41, -6.59) * mm, "end": v(854.59, -6.59) * mm});
            skCircle(sketch, "E52.35.0.22", {"center": v(856, -16) * mm, "radius": 2 * mm});
            skCircle(sketch, "E52.35.0.23", {"center": v(848, -16) * mm, "radius": 2 * mm});
            skLineSegment(sketch, "E52.35.0.24", {"start": v(854.1, -7.07) * mm, "end": v(854.59, -6.59) * mm});
            skCircle(sketch, "E52.35.0.25", {"center": v(852, 0) * mm, "radius": 2 * mm});
            skArc(sketch, "E52.35.0.26", {"start": v(866, -12) * mm, "mid": v(864, -10) * mm, "end": v(862, -12) * mm});
            skArc(sketch, "E52.35.0.27", {"start": v(862, -16) * mm, "mid": v(864, -18) * mm, "end": v(866, -16) * mm});
            skLineSegment(sketch, "E52.35.0.28", {"start": v(862, -12) * mm, "end": v(862, -16) * mm});
            skLineSegment(sketch, "E52.35.0.29", {"start": v(866, -16) * mm, "end": v(866, -12) * mm});
            skArc(sketch, "E52.36.0.0", {"start": v(890, 16) * mm, "mid": v(888, 18) * mm, "end": v(886, 16) * mm});
            skLineSegment(sketch, "E52.36.0.1", {"start": v(890, 16) * mm, "end": v(890, 12) * mm});
            skLineSegment(sketch, "E52.36.0.2", {"start": v(886, 16) * mm, "end": v(886, 12) * mm});
            skArc(sketch, "E52.36.0.3", {"start": v(886, 12) * mm, "mid": v(888, 10) * mm, "end": v(890, 12) * mm});
            skCircle(sketch, "E52.36.0.4", {"center": v(880, 16) * mm, "radius": 2 * mm});
            skCircle(sketch, "E52.36.0.5", {"center": v(872, 16) * mm, "radius": 2 * mm});
            skArc(sketch, "E52.36.0.6", {"start": v(873.9, 7.07) * mm, "mid": v(873.9, 9.9) * mm, "end": v(871.07, 9.9) * mm});
            skArc(sketch, "E52.36.0.7", {"start": v(870.59, 9.41) * mm, "mid": v(870.59, 6.59) * mm, "end": v(873.41, 6.59) * mm});
            skLineSegment(sketch, "E52.36.0.8", {"start": v(871.07, 9.9) * mm, "end": v(870.59, 9.41) * mm});
            skLineSegment(sketch, "E52.36.0.9", {"start": v(873.9, 7.07) * mm, "end": v(873.41, 6.59) * mm});
            skArc(sketch, "E52.36.0.10", {"start": v(880.93, 9.9) * mm, "mid": v(878.1, 9.9) * mm, "end": v(878.1, 7.07) * mm});
            skLineSegment(sketch, "E52.36.0.11", {"start": v(880.93, 9.9) * mm, "end": v(881.41, 9.41) * mm});
            skArc(sketch, "E52.36.0.12", {"start": v(878.59, 6.59) * mm, "mid": v(881.41, 6.59) * mm, "end": v(881.41, 9.41) * mm});
            skLineSegment(sketch, "E52.36.0.13", {"start": v(878.1, 7.07) * mm, "end": v(878.59, 6.59) * mm});
            skCircle(sketch, "E52.36.0.14", {"center": v(888, 0) * mm, "radius": 7 * mm});
            skArc(sketch, "E52.36.0.15", {"start": v(871.07, -9.9) * mm, "mid": v(873.9, -9.9) * mm, "end": v(873.9, -7.07) * mm});
            skArc(sketch, "E52.36.0.16", {"start": v(873.41, -6.59) * mm, "mid": v(870.59, -6.59) * mm, "end": v(870.59, -9.41) * mm});
            skLineSegment(sketch, "E52.36.0.17", {"start": v(873.41, -6.59) * mm, "end": v(873.9, -7.07) * mm});
            skLineSegment(sketch, "E52.36.0.18", {"start": v(870.59, -9.41) * mm, "end": v(871.07, -9.9) * mm});
            skArc(sketch, "E52.36.0.19", {"start": v(878.1, -7.07) * mm, "mid": v(878.1, -9.9) * mm, "end": v(880.93, -9.9) * mm});
            skLineSegment(sketch, "E52.36.0.20", {"start": v(880.93, -9.9) * mm, "end": v(881.41, -9.41) * mm});
            skArc(sketch, "E52.36.0.21", {"start": v(881.41, -9.41) * mm, "mid": v(881.41, -6.59) * mm, "end": v(878.59, -6.59) * mm});
            skCircle(sketch, "E52.36.0.22", {"center": v(880, -16) * mm, "radius": 2 * mm});
            skCircle(sketch, "E52.36.0.23", {"center": v(872, -16) * mm, "radius": 2 * mm});
            skLineSegment(sketch, "E52.36.0.24", {"start": v(878.1, -7.07) * mm, "end": v(878.59, -6.59) * mm});
            skCircle(sketch, "E52.36.0.25", {"center": v(876, 0) * mm, "radius": 2 * mm});
            skArc(sketch, "E52.36.0.26", {"start": v(890, -12) * mm, "mid": v(888, -10) * mm, "end": v(886, -12) * mm});
            skArc(sketch, "E52.36.0.27", {"start": v(886, -16) * mm, "mid": v(888, -18) * mm, "end": v(890, -16) * mm});
            skLineSegment(sketch, "E52.36.0.28", {"start": v(886, -12) * mm, "end": v(886, -16) * mm});
            skLineSegment(sketch, "E52.36.0.29", {"start": v(890, -16) * mm, "end": v(890, -12) * mm});
            skArc(sketch, "E52.37.0.0", {"start": v(914, 16) * mm, "mid": v(912, 18) * mm, "end": v(910, 16) * mm});
            skLineSegment(sketch, "E52.37.0.1", {"start": v(914, 16) * mm, "end": v(914, 12) * mm});
            skLineSegment(sketch, "E52.37.0.2", {"start": v(910, 16) * mm, "end": v(910, 12) * mm});
            skArc(sketch, "E52.37.0.3", {"start": v(910, 12) * mm, "mid": v(912, 10) * mm, "end": v(914, 12) * mm});
            skCircle(sketch, "E52.37.0.4", {"center": v(904, 16) * mm, "radius": 2 * mm});
            skCircle(sketch, "E52.37.0.5", {"center": v(896, 16) * mm, "radius": 2 * mm});
            skArc(sketch, "E52.37.0.6", {"start": v(897.9, 7.07) * mm, "mid": v(897.9, 9.9) * mm, "end": v(895.07, 9.9) * mm});
            skArc(sketch, "E52.37.0.7", {"start": v(894.59, 9.41) * mm, "mid": v(894.59, 6.59) * mm, "end": v(897.41, 6.59) * mm});
            skLineSegment(sketch, "E52.37.0.8", {"start": v(895.07, 9.9) * mm, "end": v(894.59, 9.41) * mm});
            skLineSegment(sketch, "E52.37.0.9", {"start": v(897.9, 7.07) * mm, "end": v(897.41, 6.59) * mm});
            skArc(sketch, "E52.37.0.10", {"start": v(904.93, 9.9) * mm, "mid": v(902.1, 9.9) * mm, "end": v(902.1, 7.07) * mm});
            skLineSegment(sketch, "E52.37.0.11", {"start": v(904.93, 9.9) * mm, "end": v(905.41, 9.41) * mm});
            skArc(sketch, "E52.37.0.12", {"start": v(902.59, 6.59) * mm, "mid": v(905.41, 6.59) * mm, "end": v(905.41, 9.41) * mm});
            skLineSegment(sketch, "E52.37.0.13", {"start": v(902.1, 7.07) * mm, "end": v(902.59, 6.59) * mm});
            skCircle(sketch, "E52.37.0.14", {"center": v(912, 0) * mm, "radius": 7 * mm});
            skArc(sketch, "E52.37.0.15", {"start": v(895.07, -9.9) * mm, "mid": v(897.9, -9.9) * mm, "end": v(897.9, -7.07) * mm});
            skArc(sketch, "E52.37.0.16", {"start": v(897.41, -6.59) * mm, "mid": v(894.59, -6.59) * mm, "end": v(894.59, -9.41) * mm});
            skLineSegment(sketch, "E52.37.0.17", {"start": v(897.41, -6.59) * mm, "end": v(897.9, -7.07) * mm});
            skLineSegment(sketch, "E52.37.0.18", {"start": v(894.59, -9.41) * mm, "end": v(895.07, -9.9) * mm});
            skArc(sketch, "E52.37.0.19", {"start": v(902.1, -7.07) * mm, "mid": v(902.1, -9.9) * mm, "end": v(904.93, -9.9) * mm});
            skLineSegment(sketch, "E52.37.0.20", {"start": v(904.93, -9.9) * mm, "end": v(905.41, -9.41) * mm});
            skArc(sketch, "E52.37.0.21", {"start": v(905.41, -9.41) * mm, "mid": v(905.41, -6.59) * mm, "end": v(902.59, -6.59) * mm});
            skCircle(sketch, "E52.37.0.22", {"center": v(904, -16) * mm, "radius": 2 * mm});
            skCircle(sketch, "E52.37.0.23", {"center": v(896, -16) * mm, "radius": 2 * mm});
            skLineSegment(sketch, "E52.37.0.24", {"start": v(902.1, -7.07) * mm, "end": v(902.59, -6.59) * mm});
            skCircle(sketch, "E52.37.0.25", {"center": v(900, 0) * mm, "radius": 2 * mm});
            skArc(sketch, "E52.37.0.26", {"start": v(914, -12) * mm, "mid": v(912, -10) * mm, "end": v(910, -12) * mm});
            skArc(sketch, "E52.37.0.27", {"start": v(910, -16) * mm, "mid": v(912, -18) * mm, "end": v(914, -16) * mm});
            skLineSegment(sketch, "E52.37.0.28", {"start": v(910, -12) * mm, "end": v(910, -16) * mm});
            skLineSegment(sketch, "E52.37.0.29", {"start": v(914, -16) * mm, "end": v(914, -12) * mm});
            skArc(sketch, "E52.38.0.0", {"start": v(938, 16) * mm, "mid": v(936, 18) * mm, "end": v(934, 16) * mm});
            skLineSegment(sketch, "E52.38.0.1", {"start": v(938, 16) * mm, "end": v(938, 12) * mm});
            skLineSegment(sketch, "E52.38.0.2", {"start": v(934, 16) * mm, "end": v(934, 12) * mm});
            skArc(sketch, "E52.38.0.3", {"start": v(934, 12) * mm, "mid": v(936, 10) * mm, "end": v(938, 12) * mm});
            skCircle(sketch, "E52.38.0.4", {"center": v(928, 16) * mm, "radius": 2 * mm});
            skCircle(sketch, "E52.38.0.5", {"center": v(920, 16) * mm, "radius": 2 * mm});
            skArc(sketch, "E52.38.0.6", {"start": v(921.9, 7.07) * mm, "mid": v(921.9, 9.9) * mm, "end": v(919.07, 9.9) * mm});
            skArc(sketch, "E52.38.0.7", {"start": v(918.59, 9.41) * mm, "mid": v(918.59, 6.59) * mm, "end": v(921.41, 6.59) * mm});
            skLineSegment(sketch, "E52.38.0.8", {"start": v(919.07, 9.9) * mm, "end": v(918.59, 9.41) * mm});
            skLineSegment(sketch, "E52.38.0.9", {"start": v(921.9, 7.07) * mm, "end": v(921.41, 6.59) * mm});
            skArc(sketch, "E52.38.0.10", {"start": v(928.93, 9.9) * mm, "mid": v(926.1, 9.9) * mm, "end": v(926.1, 7.07) * mm});
            skLineSegment(sketch, "E52.38.0.11", {"start": v(928.93, 9.9) * mm, "end": v(929.41, 9.41) * mm});
            skArc(sketch, "E52.38.0.12", {"start": v(926.59, 6.59) * mm, "mid": v(929.41, 6.59) * mm, "end": v(929.41, 9.41) * mm});
            skLineSegment(sketch, "E52.38.0.13", {"start": v(926.1, 7.07) * mm, "end": v(926.59, 6.59) * mm});
            skCircle(sketch, "E52.38.0.14", {"center": v(936, 0) * mm, "radius": 7 * mm});
            skArc(sketch, "E52.38.0.15", {"start": v(919.07, -9.9) * mm, "mid": v(921.9, -9.9) * mm, "end": v(921.9, -7.07) * mm});
            skArc(sketch, "E52.38.0.16", {"start": v(921.41, -6.59) * mm, "mid": v(918.59, -6.59) * mm, "end": v(918.59, -9.41) * mm});
            skLineSegment(sketch, "E52.38.0.17", {"start": v(921.41, -6.59) * mm, "end": v(921.9, -7.07) * mm});
            skLineSegment(sketch, "E52.38.0.18", {"start": v(918.59, -9.41) * mm, "end": v(919.07, -9.9) * mm});
            skArc(sketch, "E52.38.0.19", {"start": v(926.1, -7.07) * mm, "mid": v(926.1, -9.9) * mm, "end": v(928.93, -9.9) * mm});
            skLineSegment(sketch, "E52.38.0.20", {"start": v(928.93, -9.9) * mm, "end": v(929.41, -9.41) * mm});
            skArc(sketch, "E52.38.0.21", {"start": v(929.41, -9.41) * mm, "mid": v(929.41, -6.59) * mm, "end": v(926.59, -6.59) * mm});
            skCircle(sketch, "E52.38.0.22", {"center": v(928, -16) * mm, "radius": 2 * mm});
            skCircle(sketch, "E52.38.0.23", {"center": v(920, -16) * mm, "radius": 2 * mm});
            skLineSegment(sketch, "E52.38.0.24", {"start": v(926.1, -7.07) * mm, "end": v(926.59, -6.59) * mm});
            skCircle(sketch, "E52.38.0.25", {"center": v(924, 0) * mm, "radius": 2 * mm});
            skArc(sketch, "E52.38.0.26", {"start": v(938, -12) * mm, "mid": v(936, -10) * mm, "end": v(934, -12) * mm});
            skArc(sketch, "E52.38.0.27", {"start": v(934, -16) * mm, "mid": v(936, -18) * mm, "end": v(938, -16) * mm});
            skLineSegment(sketch, "E52.38.0.28", {"start": v(934, -12) * mm, "end": v(934, -16) * mm});
            skLineSegment(sketch, "E52.38.0.29", {"start": v(938, -16) * mm, "end": v(938, -12) * mm});
            skArc(sketch, "E52.39.0.0", {"start": v(962, 16) * mm, "mid": v(960, 18) * mm, "end": v(958, 16) * mm});
            skLineSegment(sketch, "E52.39.0.1", {"start": v(962, 16) * mm, "end": v(962, 12) * mm});
            skLineSegment(sketch, "E52.39.0.2", {"start": v(958, 16) * mm, "end": v(958, 12) * mm});
            skArc(sketch, "E52.39.0.3", {"start": v(958, 12) * mm, "mid": v(960, 10) * mm, "end": v(962, 12) * mm});
            skCircle(sketch, "E52.39.0.4", {"center": v(952, 16) * mm, "radius": 2 * mm});
            skCircle(sketch, "E52.39.0.5", {"center": v(944, 16) * mm, "radius": 2 * mm});
            skArc(sketch, "E52.39.0.6", {"start": v(945.9, 7.07) * mm, "mid": v(945.9, 9.9) * mm, "end": v(943.07, 9.9) * mm});
            skArc(sketch, "E52.39.0.7", {"start": v(942.59, 9.41) * mm, "mid": v(942.59, 6.59) * mm, "end": v(945.41, 6.59) * mm});
            skLineSegment(sketch, "E52.39.0.8", {"start": v(943.07, 9.9) * mm, "end": v(942.59, 9.41) * mm});
            skLineSegment(sketch, "E52.39.0.9", {"start": v(945.9, 7.07) * mm, "end": v(945.41, 6.59) * mm});
            skArc(sketch, "E52.39.0.10", {"start": v(952.93, 9.9) * mm, "mid": v(950.1, 9.9) * mm, "end": v(950.1, 7.07) * mm});
            skLineSegment(sketch, "E52.39.0.11", {"start": v(952.93, 9.9) * mm, "end": v(953.41, 9.41) * mm});
            skArc(sketch, "E52.39.0.12", {"start": v(950.59, 6.59) * mm, "mid": v(953.41, 6.59) * mm, "end": v(953.41, 9.41) * mm});
            skLineSegment(sketch, "E52.39.0.13", {"start": v(950.1, 7.07) * mm, "end": v(950.59, 6.59) * mm});
            skCircle(sketch, "E52.39.0.14", {"center": v(960, 0) * mm, "radius": 7 * mm});
            skArc(sketch, "E52.39.0.15", {"start": v(943.07, -9.9) * mm, "mid": v(945.9, -9.9) * mm, "end": v(945.9, -7.07) * mm});
            skArc(sketch, "E52.39.0.16", {"start": v(945.41, -6.59) * mm, "mid": v(942.59, -6.59) * mm, "end": v(942.59, -9.41) * mm});
            skLineSegment(sketch, "E52.39.0.17", {"start": v(945.41, -6.59) * mm, "end": v(945.9, -7.07) * mm});
            skLineSegment(sketch, "E52.39.0.18", {"start": v(942.59, -9.41) * mm, "end": v(943.07, -9.9) * mm});
            skArc(sketch, "E52.39.0.19", {"start": v(950.1, -7.07) * mm, "mid": v(950.1, -9.9) * mm, "end": v(952.93, -9.9) * mm});
            skLineSegment(sketch, "E52.39.0.20", {"start": v(952.93, -9.9) * mm, "end": v(953.41, -9.41) * mm});
            skArc(sketch, "E52.39.0.21", {"start": v(953.41, -9.41) * mm, "mid": v(953.41, -6.59) * mm, "end": v(950.59, -6.59) * mm});
            skCircle(sketch, "E52.39.0.22", {"center": v(952, -16) * mm, "radius": 2 * mm});
            skCircle(sketch, "E52.39.0.23", {"center": v(944, -16) * mm, "radius": 2 * mm});
            skLineSegment(sketch, "E52.39.0.24", {"start": v(950.1, -7.07) * mm, "end": v(950.59, -6.59) * mm});
            skCircle(sketch, "E52.39.0.25", {"center": v(948, 0) * mm, "radius": 2 * mm});
            skArc(sketch, "E52.39.0.26", {"start": v(962, -12) * mm, "mid": v(960, -10) * mm, "end": v(958, -12) * mm});
            skArc(sketch, "E52.39.0.27", {"start": v(958, -16) * mm, "mid": v(960, -18) * mm, "end": v(962, -16) * mm});
            skLineSegment(sketch, "E52.39.0.28", {"start": v(958, -12) * mm, "end": v(958, -16) * mm});
            skLineSegment(sketch, "E52.39.0.29", {"start": v(962, -16) * mm, "end": v(962, -12) * mm});
            skArc(sketch, "E52.40.0.0", {"start": v(986, 16) * mm, "mid": v(984, 18) * mm, "end": v(982, 16) * mm});
            skLineSegment(sketch, "E52.40.0.1", {"start": v(986, 16) * mm, "end": v(986, 12) * mm});
            skLineSegment(sketch, "E52.40.0.2", {"start": v(982, 16) * mm, "end": v(982, 12) * mm});
            skArc(sketch, "E52.40.0.3", {"start": v(982, 12) * mm, "mid": v(984, 10) * mm, "end": v(986, 12) * mm});
            skCircle(sketch, "E52.40.0.4", {"center": v(976, 16) * mm, "radius": 2 * mm});
            skCircle(sketch, "E52.40.0.5", {"center": v(968, 16) * mm, "radius": 2 * mm});
            skArc(sketch, "E52.40.0.6", {"start": v(969.9, 7.07) * mm, "mid": v(969.9, 9.9) * mm, "end": v(967.07, 9.9) * mm});
            skArc(sketch, "E52.40.0.7", {"start": v(966.59, 9.41) * mm, "mid": v(966.59, 6.59) * mm, "end": v(969.41, 6.59) * mm});
            skLineSegment(sketch, "E52.40.0.8", {"start": v(967.07, 9.9) * mm, "end": v(966.59, 9.41) * mm});
            skLineSegment(sketch, "E52.40.0.9", {"start": v(969.9, 7.07) * mm, "end": v(969.41, 6.59) * mm});
            skArc(sketch, "E52.40.0.10", {"start": v(976.93, 9.9) * mm, "mid": v(974.1, 9.9) * mm, "end": v(974.1, 7.07) * mm});
            skLineSegment(sketch, "E52.40.0.11", {"start": v(976.93, 9.9) * mm, "end": v(977.41, 9.41) * mm});
            skArc(sketch, "E52.40.0.12", {"start": v(974.59, 6.59) * mm, "mid": v(977.41, 6.59) * mm, "end": v(977.41, 9.41) * mm});
            skLineSegment(sketch, "E52.40.0.13", {"start": v(974.1, 7.07) * mm, "end": v(974.59, 6.59) * mm});
            skCircle(sketch, "E52.40.0.14", {"center": v(984, 0) * mm, "radius": 7 * mm});
            skArc(sketch, "E52.40.0.15", {"start": v(967.07, -9.9) * mm, "mid": v(969.9, -9.9) * mm, "end": v(969.9, -7.07) * mm});
            skArc(sketch, "E52.40.0.16", {"start": v(969.41, -6.59) * mm, "mid": v(966.59, -6.59) * mm, "end": v(966.59, -9.41) * mm});
            skLineSegment(sketch, "E52.40.0.17", {"start": v(969.41, -6.59) * mm, "end": v(969.9, -7.07) * mm});
            skLineSegment(sketch, "E52.40.0.18", {"start": v(966.59, -9.41) * mm, "end": v(967.07, -9.9) * mm});
            skArc(sketch, "E52.40.0.19", {"start": v(974.1, -7.07) * mm, "mid": v(974.1, -9.9) * mm, "end": v(976.93, -9.9) * mm});
            skLineSegment(sketch, "E52.40.0.20", {"start": v(976.93, -9.9) * mm, "end": v(977.41, -9.41) * mm});
            skArc(sketch, "E52.40.0.21", {"start": v(977.41, -9.41) * mm, "mid": v(977.41, -6.59) * mm, "end": v(974.59, -6.59) * mm});
            skCircle(sketch, "E52.40.0.22", {"center": v(976, -16) * mm, "radius": 2 * mm});
            skCircle(sketch, "E52.40.0.23", {"center": v(968, -16) * mm, "radius": 2 * mm});
            skLineSegment(sketch, "E52.40.0.24", {"start": v(974.1, -7.07) * mm, "end": v(974.59, -6.59) * mm});
            skCircle(sketch, "E52.40.0.25", {"center": v(972, 0) * mm, "radius": 2 * mm});
            skArc(sketch, "E52.40.0.26", {"start": v(986, -12) * mm, "mid": v(984, -10) * mm, "end": v(982, -12) * mm});
            skArc(sketch, "E52.40.0.27", {"start": v(982, -16) * mm, "mid": v(984, -18) * mm, "end": v(986, -16) * mm});
            skLineSegment(sketch, "E52.40.0.28", {"start": v(982, -12) * mm, "end": v(982, -16) * mm});
            skLineSegment(sketch, "E52.40.0.29", {"start": v(986, -16) * mm, "end": v(986, -12) * mm});
            skArc(sketch, "E52.41.0.0", {"start": v(1010, 16) * mm, "mid": v(1008, 18) * mm, "end": v(1006, 16) * mm});
            skLineSegment(sketch, "E52.41.0.1", {"start": v(1010, 16) * mm, "end": v(1010, 12) * mm});
            skLineSegment(sketch, "E52.41.0.2", {"start": v(1006, 16) * mm, "end": v(1006, 12) * mm});
            skArc(sketch, "E52.41.0.3", {"start": v(1006, 12) * mm, "mid": v(1008, 10) * mm, "end": v(1010, 12) * mm});
            skCircle(sketch, "E52.41.0.4", {"center": v(1000, 16) * mm, "radius": 2 * mm});
            skCircle(sketch, "E52.41.0.5", {"center": v(992, 16) * mm, "radius": 2 * mm});
            skArc(sketch, "E52.41.0.6", {"start": v(993.9, 7.07) * mm, "mid": v(993.9, 9.9) * mm, "end": v(991.07, 9.9) * mm});
            skArc(sketch, "E52.41.0.7", {"start": v(990.59, 9.41) * mm, "mid": v(990.59, 6.59) * mm, "end": v(993.41, 6.59) * mm});
            skLineSegment(sketch, "E52.41.0.8", {"start": v(991.07, 9.9) * mm, "end": v(990.59, 9.41) * mm});
            skLineSegment(sketch, "E52.41.0.9", {"start": v(993.9, 7.07) * mm, "end": v(993.41, 6.59) * mm});
            skArc(sketch, "E52.41.0.10", {"start": v(1000.93, 9.9) * mm, "mid": v(998.1, 9.9) * mm, "end": v(998.1, 7.07) * mm});
            skLineSegment(sketch, "E52.41.0.11", {"start": v(1000.93, 9.9) * mm, "end": v(1001.41, 9.41) * mm});
            skArc(sketch, "E52.41.0.12", {"start": v(998.59, 6.59) * mm, "mid": v(1001.41, 6.59) * mm, "end": v(1001.41, 9.41) * mm});
            skLineSegment(sketch, "E52.41.0.13", {"start": v(998.1, 7.07) * mm, "end": v(998.59, 6.59) * mm});
            skCircle(sketch, "E52.41.0.14", {"center": v(1008, 0) * mm, "radius": 7 * mm});
            skArc(sketch, "E52.41.0.15", {"start": v(991.07, -9.9) * mm, "mid": v(993.9, -9.9) * mm, "end": v(993.9, -7.07) * mm});
            skArc(sketch, "E52.41.0.16", {"start": v(993.41, -6.59) * mm, "mid": v(990.59, -6.59) * mm, "end": v(990.59, -9.41) * mm});
            skLineSegment(sketch, "E52.41.0.17", {"start": v(993.41, -6.59) * mm, "end": v(993.9, -7.07) * mm});
            skLineSegment(sketch, "E52.41.0.18", {"start": v(990.59, -9.41) * mm, "end": v(991.07, -9.9) * mm});
            skArc(sketch, "E52.41.0.19", {"start": v(998.1, -7.07) * mm, "mid": v(998.1, -9.9) * mm, "end": v(1000.93, -9.9) * mm});
            skLineSegment(sketch, "E52.41.0.20", {"start": v(1000.93, -9.9) * mm, "end": v(1001.41, -9.41) * mm});
            skArc(sketch, "E52.41.0.21", {"start": v(1001.41, -9.41) * mm, "mid": v(1001.41, -6.59) * mm, "end": v(998.59, -6.59) * mm});
            skCircle(sketch, "E52.41.0.22", {"center": v(1000, -16) * mm, "radius": 2 * mm});
            skCircle(sketch, "E52.41.0.23", {"center": v(992, -16) * mm, "radius": 2 * mm});
            skLineSegment(sketch, "E52.41.0.24", {"start": v(998.1, -7.07) * mm, "end": v(998.59, -6.59) * mm});
            skCircle(sketch, "E52.41.0.25", {"center": v(996, 0) * mm, "radius": 2 * mm});
            skArc(sketch, "E52.41.0.26", {"start": v(1010, -12) * mm, "mid": v(1008, -10) * mm, "end": v(1006, -12) * mm});
            skArc(sketch, "E52.41.0.27", {"start": v(1006, -16) * mm, "mid": v(1008, -18) * mm, "end": v(1010, -16) * mm});
            skLineSegment(sketch, "E52.41.0.28", {"start": v(1006, -12) * mm, "end": v(1006, -16) * mm});
            skLineSegment(sketch, "E52.41.0.29", {"start": v(1010, -16) * mm, "end": v(1010, -12) * mm});
            skArc(sketch, "E52.42.0.0", {"start": v(1034, 16) * mm, "mid": v(1032, 18) * mm, "end": v(1030, 16) * mm});
            skLineSegment(sketch, "E52.42.0.1", {"start": v(1034, 16) * mm, "end": v(1034, 12) * mm});
            skLineSegment(sketch, "E52.42.0.2", {"start": v(1030, 16) * mm, "end": v(1030, 12) * mm});
            skArc(sketch, "E52.42.0.3", {"start": v(1030, 12) * mm, "mid": v(1032, 10) * mm, "end": v(1034, 12) * mm});
            skCircle(sketch, "E52.42.0.4", {"center": v(1024, 16) * mm, "radius": 2 * mm});
            skCircle(sketch, "E52.42.0.5", {"center": v(1016, 16) * mm, "radius": 2 * mm});
            skArc(sketch, "E52.42.0.6", {"start": v(1017.9, 7.07) * mm, "mid": v(1017.9, 9.9) * mm, "end": v(1015.07, 9.9) * mm});
            skArc(sketch, "E52.42.0.7", {"start": v(1014.59, 9.41) * mm, "mid": v(1014.59, 6.59) * mm, "end": v(1017.41, 6.59) * mm});
            skLineSegment(sketch, "E52.42.0.8", {"start": v(1015.07, 9.9) * mm, "end": v(1014.59, 9.41) * mm});
            skLineSegment(sketch, "E52.42.0.9", {"start": v(1017.9, 7.07) * mm, "end": v(1017.41, 6.59) * mm});
            skArc(sketch, "E52.42.0.10", {"start": v(1024.93, 9.9) * mm, "mid": v(1022.1, 9.9) * mm, "end": v(1022.1, 7.07) * mm});
            skLineSegment(sketch, "E52.42.0.11", {"start": v(1024.93, 9.9) * mm, "end": v(1025.41, 9.41) * mm});
            skArc(sketch, "E52.42.0.12", {"start": v(1022.59, 6.59) * mm, "mid": v(1025.41, 6.59) * mm, "end": v(1025.41, 9.41) * mm});
            skLineSegment(sketch, "E52.42.0.13", {"start": v(1022.1, 7.07) * mm, "end": v(1022.59, 6.59) * mm});
            skCircle(sketch, "E52.42.0.14", {"center": v(1032, 0) * mm, "radius": 7 * mm});
            skArc(sketch, "E52.42.0.15", {"start": v(1015.07, -9.9) * mm, "mid": v(1017.9, -9.9) * mm, "end": v(1017.9, -7.07) * mm});
            skArc(sketch, "E52.42.0.16", {"start": v(1017.41, -6.59) * mm, "mid": v(1014.59, -6.59) * mm, "end": v(1014.59, -9.41) * mm});
            skLineSegment(sketch, "E52.42.0.17", {"start": v(1017.41, -6.59) * mm, "end": v(1017.9, -7.07) * mm});
            skLineSegment(sketch, "E52.42.0.18", {"start": v(1014.59, -9.41) * mm, "end": v(1015.07, -9.9) * mm});
            skArc(sketch, "E52.42.0.19", {"start": v(1022.1, -7.07) * mm, "mid": v(1022.1, -9.9) * mm, "end": v(1024.93, -9.9) * mm});
            skLineSegment(sketch, "E52.42.0.20", {"start": v(1024.93, -9.9) * mm, "end": v(1025.41, -9.41) * mm});
            skArc(sketch, "E52.42.0.21", {"start": v(1025.41, -9.41) * mm, "mid": v(1025.41, -6.59) * mm, "end": v(1022.59, -6.59) * mm});
            skCircle(sketch, "E52.42.0.22", {"center": v(1024, -16) * mm, "radius": 2 * mm});
            skCircle(sketch, "E52.42.0.23", {"center": v(1016, -16) * mm, "radius": 2 * mm});
            skLineSegment(sketch, "E52.42.0.24", {"start": v(1022.1, -7.07) * mm, "end": v(1022.59, -6.59) * mm});
            skCircle(sketch, "E52.42.0.25", {"center": v(1020, 0) * mm, "radius": 2 * mm});
            skArc(sketch, "E52.42.0.26", {"start": v(1034, -12) * mm, "mid": v(1032, -10) * mm, "end": v(1030, -12) * mm});
            skArc(sketch, "E52.42.0.27", {"start": v(1030, -16) * mm, "mid": v(1032, -18) * mm, "end": v(1034, -16) * mm});
            skLineSegment(sketch, "E52.42.0.28", {"start": v(1030, -12) * mm, "end": v(1030, -16) * mm});
            skLineSegment(sketch, "E52.42.0.29", {"start": v(1034, -16) * mm, "end": v(1034, -12) * mm});
            skArc(sketch, "E52.43.0.0", {"start": v(1058, 16) * mm, "mid": v(1056, 18) * mm, "end": v(1054, 16) * mm});
            skLineSegment(sketch, "E52.43.0.1", {"start": v(1058, 16) * mm, "end": v(1058, 12) * mm});
            skLineSegment(sketch, "E52.43.0.2", {"start": v(1054, 16) * mm, "end": v(1054, 12) * mm});
            skArc(sketch, "E52.43.0.3", {"start": v(1054, 12) * mm, "mid": v(1056, 10) * mm, "end": v(1058, 12) * mm});
            skCircle(sketch, "E52.43.0.4", {"center": v(1048, 16) * mm, "radius": 2 * mm});
            skCircle(sketch, "E52.43.0.5", {"center": v(1040, 16) * mm, "radius": 2 * mm});
            skArc(sketch, "E52.43.0.6", {"start": v(1041.9, 7.07) * mm, "mid": v(1041.9, 9.9) * mm, "end": v(1039.07, 9.9) * mm});
            skArc(sketch, "E52.43.0.7", {"start": v(1038.59, 9.41) * mm, "mid": v(1038.59, 6.59) * mm, "end": v(1041.41, 6.59) * mm});
            skLineSegment(sketch, "E52.43.0.8", {"start": v(1039.07, 9.9) * mm, "end": v(1038.59, 9.41) * mm});
            skLineSegment(sketch, "E52.43.0.9", {"start": v(1041.9, 7.07) * mm, "end": v(1041.41, 6.59) * mm});
            skArc(sketch, "E52.43.0.10", {"start": v(1048.93, 9.9) * mm, "mid": v(1046.1, 9.9) * mm, "end": v(1046.1, 7.07) * mm});
            skLineSegment(sketch, "E52.43.0.11", {"start": v(1048.93, 9.9) * mm, "end": v(1049.41, 9.41) * mm});
            skArc(sketch, "E52.43.0.12", {"start": v(1046.59, 6.59) * mm, "mid": v(1049.41, 6.59) * mm, "end": v(1049.41, 9.41) * mm});
            skLineSegment(sketch, "E52.43.0.13", {"start": v(1046.1, 7.07) * mm, "end": v(1046.59, 6.59) * mm});
            skCircle(sketch, "E52.43.0.14", {"center": v(1056, 0) * mm, "radius": 7 * mm});
            skArc(sketch, "E52.43.0.15", {"start": v(1039.07, -9.9) * mm, "mid": v(1041.9, -9.9) * mm, "end": v(1041.9, -7.07) * mm});
            skArc(sketch, "E52.43.0.16", {"start": v(1041.41, -6.59) * mm, "mid": v(1038.59, -6.59) * mm, "end": v(1038.59, -9.41) * mm});
            skLineSegment(sketch, "E52.43.0.17", {"start": v(1041.41, -6.59) * mm, "end": v(1041.9, -7.07) * mm});
            skLineSegment(sketch, "E52.43.0.18", {"start": v(1038.59, -9.41) * mm, "end": v(1039.07, -9.9) * mm});
            skArc(sketch, "E52.43.0.19", {"start": v(1046.1, -7.07) * mm, "mid": v(1046.1, -9.9) * mm, "end": v(1048.93, -9.9) * mm});
            skLineSegment(sketch, "E52.43.0.20", {"start": v(1048.93, -9.9) * mm, "end": v(1049.41, -9.41) * mm});
            skArc(sketch, "E52.43.0.21", {"start": v(1049.41, -9.41) * mm, "mid": v(1049.41, -6.59) * mm, "end": v(1046.59, -6.59) * mm});
            skCircle(sketch, "E52.43.0.22", {"center": v(1048, -16) * mm, "radius": 2 * mm});
            skCircle(sketch, "E52.43.0.23", {"center": v(1040, -16) * mm, "radius": 2 * mm});
            skLineSegment(sketch, "E52.43.0.24", {"start": v(1046.1, -7.07) * mm, "end": v(1046.59, -6.59) * mm});
            skCircle(sketch, "E52.43.0.25", {"center": v(1044, 0) * mm, "radius": 2 * mm});
            skArc(sketch, "E52.43.0.26", {"start": v(1058, -12) * mm, "mid": v(1056, -10) * mm, "end": v(1054, -12) * mm});
            skArc(sketch, "E52.43.0.27", {"start": v(1054, -16) * mm, "mid": v(1056, -18) * mm, "end": v(1058, -16) * mm});
            skLineSegment(sketch, "E52.43.0.28", {"start": v(1054, -12) * mm, "end": v(1054, -16) * mm});
            skLineSegment(sketch, "E52.43.0.29", {"start": v(1058, -16) * mm, "end": v(1058, -12) * mm});
            skArc(sketch, "E52.44.0.0", {"start": v(1082, 16) * mm, "mid": v(1080, 18) * mm, "end": v(1078, 16) * mm});
            skLineSegment(sketch, "E52.44.0.1", {"start": v(1082, 16) * mm, "end": v(1082, 12) * mm});
            skLineSegment(sketch, "E52.44.0.2", {"start": v(1078, 16) * mm, "end": v(1078, 12) * mm});
            skArc(sketch, "E52.44.0.3", {"start": v(1078, 12) * mm, "mid": v(1080, 10) * mm, "end": v(1082, 12) * mm});
            skCircle(sketch, "E52.44.0.4", {"center": v(1072, 16) * mm, "radius": 2 * mm});
            skCircle(sketch, "E52.44.0.5", {"center": v(1064, 16) * mm, "radius": 2 * mm});
            skArc(sketch, "E52.44.0.6", {"start": v(1065.9, 7.07) * mm, "mid": v(1065.9, 9.9) * mm, "end": v(1063.07, 9.9) * mm});
            skArc(sketch, "E52.44.0.7", {"start": v(1062.59, 9.41) * mm, "mid": v(1062.59, 6.59) * mm, "end": v(1065.41, 6.59) * mm});
            skLineSegment(sketch, "E52.44.0.8", {"start": v(1063.07, 9.9) * mm, "end": v(1062.59, 9.41) * mm});
            skLineSegment(sketch, "E52.44.0.9", {"start": v(1065.9, 7.07) * mm, "end": v(1065.41, 6.59) * mm});
            skArc(sketch, "E52.44.0.10", {"start": v(1072.93, 9.9) * mm, "mid": v(1070.1, 9.9) * mm, "end": v(1070.1, 7.07) * mm});
            skLineSegment(sketch, "E52.44.0.11", {"start": v(1072.93, 9.9) * mm, "end": v(1073.41, 9.41) * mm});
            skArc(sketch, "E52.44.0.12", {"start": v(1070.59, 6.59) * mm, "mid": v(1073.41, 6.59) * mm, "end": v(1073.41, 9.41) * mm});
            skLineSegment(sketch, "E52.44.0.13", {"start": v(1070.1, 7.07) * mm, "end": v(1070.59, 6.59) * mm});
            skCircle(sketch, "E52.44.0.14", {"center": v(1080, 0) * mm, "radius": 7 * mm});
            skArc(sketch, "E52.44.0.15", {"start": v(1063.07, -9.9) * mm, "mid": v(1065.9, -9.9) * mm, "end": v(1065.9, -7.07) * mm});
            skArc(sketch, "E52.44.0.16", {"start": v(1065.41, -6.59) * mm, "mid": v(1062.59, -6.59) * mm, "end": v(1062.59, -9.41) * mm});
            skLineSegment(sketch, "E52.44.0.17", {"start": v(1065.41, -6.59) * mm, "end": v(1065.9, -7.07) * mm});
            skLineSegment(sketch, "E52.44.0.18", {"start": v(1062.59, -9.41) * mm, "end": v(1063.07, -9.9) * mm});
            skArc(sketch, "E52.44.0.19", {"start": v(1070.1, -7.07) * mm, "mid": v(1070.1, -9.9) * mm, "end": v(1072.93, -9.9) * mm});
            skLineSegment(sketch, "E52.44.0.20", {"start": v(1072.93, -9.9) * mm, "end": v(1073.41, -9.41) * mm});
            skArc(sketch, "E52.44.0.21", {"start": v(1073.41, -9.41) * mm, "mid": v(1073.41, -6.59) * mm, "end": v(1070.59, -6.59) * mm});
            skCircle(sketch, "E52.44.0.22", {"center": v(1072, -16) * mm, "radius": 2 * mm});
            skCircle(sketch, "E52.44.0.23", {"center": v(1064, -16) * mm, "radius": 2 * mm});
            skLineSegment(sketch, "E52.44.0.24", {"start": v(1070.1, -7.07) * mm, "end": v(1070.59, -6.59) * mm});
            skCircle(sketch, "E52.44.0.25", {"center": v(1068, 0) * mm, "radius": 2 * mm});
            skArc(sketch, "E52.44.0.26", {"start": v(1082, -12) * mm, "mid": v(1080, -10) * mm, "end": v(1078, -12) * mm});
            skArc(sketch, "E52.44.0.27", {"start": v(1078, -16) * mm, "mid": v(1080, -18) * mm, "end": v(1082, -16) * mm});
            skLineSegment(sketch, "E52.44.0.28", {"start": v(1078, -12) * mm, "end": v(1078, -16) * mm});
            skLineSegment(sketch, "E52.44.0.29", {"start": v(1082, -16) * mm, "end": v(1082, -12) * mm});
            skArc(sketch, "E52.45.0.0", {"start": v(1106, 16) * mm, "mid": v(1104, 18) * mm, "end": v(1102, 16) * mm});
            skLineSegment(sketch, "E52.45.0.1", {"start": v(1106, 16) * mm, "end": v(1106, 12) * mm});
            skLineSegment(sketch, "E52.45.0.2", {"start": v(1102, 16) * mm, "end": v(1102, 12) * mm});
            skArc(sketch, "E52.45.0.3", {"start": v(1102, 12) * mm, "mid": v(1104, 10) * mm, "end": v(1106, 12) * mm});
            skCircle(sketch, "E52.45.0.4", {"center": v(1096, 16) * mm, "radius": 2 * mm});
            skCircle(sketch, "E52.45.0.5", {"center": v(1088, 16) * mm, "radius": 2 * mm});
            skArc(sketch, "E52.45.0.6", {"start": v(1089.9, 7.07) * mm, "mid": v(1089.9, 9.9) * mm, "end": v(1087.07, 9.9) * mm});
            skArc(sketch, "E52.45.0.7", {"start": v(1086.59, 9.41) * mm, "mid": v(1086.59, 6.59) * mm, "end": v(1089.41, 6.59) * mm});
            skLineSegment(sketch, "E52.45.0.8", {"start": v(1087.07, 9.9) * mm, "end": v(1086.59, 9.41) * mm});
            skLineSegment(sketch, "E52.45.0.9", {"start": v(1089.9, 7.07) * mm, "end": v(1089.41, 6.59) * mm});
            skArc(sketch, "E52.45.0.10", {"start": v(1096.93, 9.9) * mm, "mid": v(1094.1, 9.9) * mm, "end": v(1094.1, 7.07) * mm});
            skLineSegment(sketch, "E52.45.0.11", {"start": v(1096.93, 9.9) * mm, "end": v(1097.41, 9.41) * mm});
            skArc(sketch, "E52.45.0.12", {"start": v(1094.59, 6.59) * mm, "mid": v(1097.41, 6.59) * mm, "end": v(1097.41, 9.41) * mm});
            skLineSegment(sketch, "E52.45.0.13", {"start": v(1094.1, 7.07) * mm, "end": v(1094.59, 6.59) * mm});
            skCircle(sketch, "E52.45.0.14", {"center": v(1104, 0) * mm, "radius": 7 * mm});
            skArc(sketch, "E52.45.0.15", {"start": v(1087.07, -9.9) * mm, "mid": v(1089.9, -9.9) * mm, "end": v(1089.9, -7.07) * mm});
            skArc(sketch, "E52.45.0.16", {"start": v(1089.41, -6.59) * mm, "mid": v(1086.59, -6.59) * mm, "end": v(1086.59, -9.41) * mm});
            skLineSegment(sketch, "E52.45.0.17", {"start": v(1089.41, -6.59) * mm, "end": v(1089.9, -7.07) * mm});
            skLineSegment(sketch, "E52.45.0.18", {"start": v(1086.59, -9.41) * mm, "end": v(1087.07, -9.9) * mm});
            skArc(sketch, "E52.45.0.19", {"start": v(1094.1, -7.07) * mm, "mid": v(1094.1, -9.9) * mm, "end": v(1096.93, -9.9) * mm});
            skLineSegment(sketch, "E52.45.0.20", {"start": v(1096.93, -9.9) * mm, "end": v(1097.41, -9.41) * mm});
            skArc(sketch, "E52.45.0.21", {"start": v(1097.41, -9.41) * mm, "mid": v(1097.41, -6.59) * mm, "end": v(1094.59, -6.59) * mm});
            skCircle(sketch, "E52.45.0.22", {"center": v(1096, -16) * mm, "radius": 2 * mm});
            skCircle(sketch, "E52.45.0.23", {"center": v(1088, -16) * mm, "radius": 2 * mm});
            skLineSegment(sketch, "E52.45.0.24", {"start": v(1094.1, -7.07) * mm, "end": v(1094.59, -6.59) * mm});
            skCircle(sketch, "E52.45.0.25", {"center": v(1092, 0) * mm, "radius": 2 * mm});
            skArc(sketch, "E52.45.0.26", {"start": v(1106, -12) * mm, "mid": v(1104, -10) * mm, "end": v(1102, -12) * mm});
            skArc(sketch, "E52.45.0.27", {"start": v(1102, -16) * mm, "mid": v(1104, -18) * mm, "end": v(1106, -16) * mm});
            skLineSegment(sketch, "E52.45.0.28", {"start": v(1102, -12) * mm, "end": v(1102, -16) * mm});
            skLineSegment(sketch, "E52.45.0.29", {"start": v(1106, -16) * mm, "end": v(1106, -12) * mm});
            skArc(sketch, "E52.46.0.0", {"start": v(1130, 16) * mm, "mid": v(1128, 18) * mm, "end": v(1126, 16) * mm});
            skLineSegment(sketch, "E52.46.0.1", {"start": v(1130, 16) * mm, "end": v(1130, 12) * mm});
            skLineSegment(sketch, "E52.46.0.2", {"start": v(1126, 16) * mm, "end": v(1126, 12) * mm});
            skArc(sketch, "E52.46.0.3", {"start": v(1126, 12) * mm, "mid": v(1128, 10) * mm, "end": v(1130, 12) * mm});
            skCircle(sketch, "E52.46.0.4", {"center": v(1120, 16) * mm, "radius": 2 * mm});
            skCircle(sketch, "E52.46.0.5", {"center": v(1112, 16) * mm, "radius": 2 * mm});
            skArc(sketch, "E52.46.0.6", {"start": v(1113.9, 7.07) * mm, "mid": v(1113.9, 9.9) * mm, "end": v(1111.07, 9.9) * mm});
            skArc(sketch, "E52.46.0.7", {"start": v(1110.59, 9.41) * mm, "mid": v(1110.59, 6.59) * mm, "end": v(1113.41, 6.59) * mm});
            skLineSegment(sketch, "E52.46.0.8", {"start": v(1111.07, 9.9) * mm, "end": v(1110.59, 9.41) * mm});
            skLineSegment(sketch, "E52.46.0.9", {"start": v(1113.9, 7.07) * mm, "end": v(1113.41, 6.59) * mm});
            skArc(sketch, "E52.46.0.10", {"start": v(1120.93, 9.9) * mm, "mid": v(1118.1, 9.9) * mm, "end": v(1118.1, 7.07) * mm});
            skLineSegment(sketch, "E52.46.0.11", {"start": v(1120.93, 9.9) * mm, "end": v(1121.41, 9.41) * mm});
            skArc(sketch, "E52.46.0.12", {"start": v(1118.59, 6.59) * mm, "mid": v(1121.41, 6.59) * mm, "end": v(1121.41, 9.41) * mm});
            skLineSegment(sketch, "E52.46.0.13", {"start": v(1118.1, 7.07) * mm, "end": v(1118.59, 6.59) * mm});
            skCircle(sketch, "E52.46.0.14", {"center": v(1128, 0) * mm, "radius": 7 * mm});
            skArc(sketch, "E52.46.0.15", {"start": v(1111.07, -9.9) * mm, "mid": v(1113.9, -9.9) * mm, "end": v(1113.9, -7.07) * mm});
            skArc(sketch, "E52.46.0.16", {"start": v(1113.41, -6.59) * mm, "mid": v(1110.59, -6.59) * mm, "end": v(1110.59, -9.41) * mm});
            skLineSegment(sketch, "E52.46.0.17", {"start": v(1113.41, -6.59) * mm, "end": v(1113.9, -7.07) * mm});
            skLineSegment(sketch, "E52.46.0.18", {"start": v(1110.59, -9.41) * mm, "end": v(1111.07, -9.9) * mm});
            skArc(sketch, "E52.46.0.19", {"start": v(1118.1, -7.07) * mm, "mid": v(1118.1, -9.9) * mm, "end": v(1120.93, -9.9) * mm});
            skLineSegment(sketch, "E52.46.0.20", {"start": v(1120.93, -9.9) * mm, "end": v(1121.41, -9.41) * mm});
            skArc(sketch, "E52.46.0.21", {"start": v(1121.41, -9.41) * mm, "mid": v(1121.41, -6.59) * mm, "end": v(1118.59, -6.59) * mm});
            skCircle(sketch, "E52.46.0.22", {"center": v(1120, -16) * mm, "radius": 2 * mm});
            skCircle(sketch, "E52.46.0.23", {"center": v(1112, -16) * mm, "radius": 2 * mm});
            skLineSegment(sketch, "E52.46.0.24", {"start": v(1118.1, -7.07) * mm, "end": v(1118.59, -6.59) * mm});
            skCircle(sketch, "E52.46.0.25", {"center": v(1116, 0) * mm, "radius": 2 * mm});
            skArc(sketch, "E52.46.0.26", {"start": v(1130, -12) * mm, "mid": v(1128, -10) * mm, "end": v(1126, -12) * mm});
            skArc(sketch, "E52.46.0.27", {"start": v(1126, -16) * mm, "mid": v(1128, -18) * mm, "end": v(1130, -16) * mm});
            skLineSegment(sketch, "E52.46.0.28", {"start": v(1126, -12) * mm, "end": v(1126, -16) * mm});
            skLineSegment(sketch, "E52.46.0.29", {"start": v(1130, -16) * mm, "end": v(1130, -12) * mm});
            skArc(sketch, "E52.47.0.0", {"start": v(1154, 16) * mm, "mid": v(1152, 18) * mm, "end": v(1150, 16) * mm});
            skLineSegment(sketch, "E52.47.0.1", {"start": v(1154, 16) * mm, "end": v(1154, 12) * mm});
            skLineSegment(sketch, "E52.47.0.2", {"start": v(1150, 16) * mm, "end": v(1150, 12) * mm});
            skArc(sketch, "E52.47.0.3", {"start": v(1150, 12) * mm, "mid": v(1152, 10) * mm, "end": v(1154, 12) * mm});
            skCircle(sketch, "E52.47.0.4", {"center": v(1144, 16) * mm, "radius": 2 * mm});
            skCircle(sketch, "E52.47.0.5", {"center": v(1136, 16) * mm, "radius": 2 * mm});
            skArc(sketch, "E52.47.0.6", {"start": v(1137.9, 7.07) * mm, "mid": v(1137.9, 9.9) * mm, "end": v(1135.07, 9.9) * mm});
            skArc(sketch, "E52.47.0.7", {"start": v(1134.59, 9.41) * mm, "mid": v(1134.59, 6.59) * mm, "end": v(1137.41, 6.59) * mm});
            skLineSegment(sketch, "E52.47.0.8", {"start": v(1135.07, 9.9) * mm, "end": v(1134.59, 9.41) * mm});
            skLineSegment(sketch, "E52.47.0.9", {"start": v(1137.9, 7.07) * mm, "end": v(1137.41, 6.59) * mm});
            skArc(sketch, "E52.47.0.10", {"start": v(1144.93, 9.9) * mm, "mid": v(1142.1, 9.9) * mm, "end": v(1142.1, 7.07) * mm});
            skLineSegment(sketch, "E52.47.0.11", {"start": v(1144.93, 9.9) * mm, "end": v(1145.41, 9.41) * mm});
            skArc(sketch, "E52.47.0.12", {"start": v(1142.59, 6.59) * mm, "mid": v(1145.41, 6.59) * mm, "end": v(1145.41, 9.41) * mm});
            skLineSegment(sketch, "E52.47.0.13", {"start": v(1142.1, 7.07) * mm, "end": v(1142.59, 6.59) * mm});
            skCircle(sketch, "E52.47.0.14", {"center": v(1152, 0) * mm, "radius": 7 * mm});
            skArc(sketch, "E52.47.0.15", {"start": v(1135.07, -9.9) * mm, "mid": v(1137.9, -9.9) * mm, "end": v(1137.9, -7.07) * mm});
            skArc(sketch, "E52.47.0.16", {"start": v(1137.41, -6.59) * mm, "mid": v(1134.59, -6.59) * mm, "end": v(1134.59, -9.41) * mm});
            skLineSegment(sketch, "E52.47.0.17", {"start": v(1137.41, -6.59) * mm, "end": v(1137.9, -7.07) * mm});
            skLineSegment(sketch, "E52.47.0.18", {"start": v(1134.59, -9.41) * mm, "end": v(1135.07, -9.9) * mm});
            skArc(sketch, "E52.47.0.19", {"start": v(1142.1, -7.07) * mm, "mid": v(1142.1, -9.9) * mm, "end": v(1144.93, -9.9) * mm});
            skLineSegment(sketch, "E52.47.0.20", {"start": v(1144.93, -9.9) * mm, "end": v(1145.41, -9.41) * mm});
            skArc(sketch, "E52.47.0.21", {"start": v(1145.41, -9.41) * mm, "mid": v(1145.41, -6.59) * mm, "end": v(1142.59, -6.59) * mm});
            skCircle(sketch, "E52.47.0.22", {"center": v(1144, -16) * mm, "radius": 2 * mm});
            skCircle(sketch, "E52.47.0.23", {"center": v(1136, -16) * mm, "radius": 2 * mm});
            skLineSegment(sketch, "E52.47.0.24", {"start": v(1142.1, -7.07) * mm, "end": v(1142.59, -6.59) * mm});
            skCircle(sketch, "E52.47.0.25", {"center": v(1140, 0) * mm, "radius": 2 * mm});
            skArc(sketch, "E52.47.0.26", {"start": v(1154, -12) * mm, "mid": v(1152, -10) * mm, "end": v(1150, -12) * mm});
            skArc(sketch, "E52.47.0.27", {"start": v(1150, -16) * mm, "mid": v(1152, -18) * mm, "end": v(1154, -16) * mm});
            skLineSegment(sketch, "E52.47.0.28", {"start": v(1150, -12) * mm, "end": v(1150, -16) * mm});
            skLineSegment(sketch, "E52.47.0.29", {"start": v(1154, -16) * mm, "end": v(1154, -12) * mm});
            skArc(sketch, "E52.48.0.0", {"start": v(1178, 16) * mm, "mid": v(1176, 18) * mm, "end": v(1174, 16) * mm});
            skLineSegment(sketch, "E52.48.0.1", {"start": v(1178, 16) * mm, "end": v(1178, 12) * mm});
            skLineSegment(sketch, "E52.48.0.2", {"start": v(1174, 16) * mm, "end": v(1174, 12) * mm});
            skArc(sketch, "E52.48.0.3", {"start": v(1174, 12) * mm, "mid": v(1176, 10) * mm, "end": v(1178, 12) * mm});
            skCircle(sketch, "E52.48.0.4", {"center": v(1168, 16) * mm, "radius": 2 * mm});
            skCircle(sketch, "E52.48.0.5", {"center": v(1160, 16) * mm, "radius": 2 * mm});
            skArc(sketch, "E52.48.0.6", {"start": v(1161.9, 7.07) * mm, "mid": v(1161.9, 9.9) * mm, "end": v(1159.07, 9.9) * mm});
            skArc(sketch, "E52.48.0.7", {"start": v(1158.59, 9.41) * mm, "mid": v(1158.59, 6.59) * mm, "end": v(1161.41, 6.59) * mm});
            skLineSegment(sketch, "E52.48.0.8", {"start": v(1159.07, 9.9) * mm, "end": v(1158.59, 9.41) * mm});
            skLineSegment(sketch, "E52.48.0.9", {"start": v(1161.9, 7.07) * mm, "end": v(1161.41, 6.59) * mm});
            skArc(sketch, "E52.48.0.10", {"start": v(1168.93, 9.9) * mm, "mid": v(1166.1, 9.9) * mm, "end": v(1166.1, 7.07) * mm});
            skLineSegment(sketch, "E52.48.0.11", {"start": v(1168.93, 9.9) * mm, "end": v(1169.41, 9.41) * mm});
            skArc(sketch, "E52.48.0.12", {"start": v(1166.59, 6.59) * mm, "mid": v(1169.41, 6.59) * mm, "end": v(1169.41, 9.41) * mm});
            skLineSegment(sketch, "E52.48.0.13", {"start": v(1166.1, 7.07) * mm, "end": v(1166.59, 6.59) * mm});
            skCircle(sketch, "E52.48.0.14", {"center": v(1176, 0) * mm, "radius": 7 * mm});
            skArc(sketch, "E52.48.0.15", {"start": v(1159.07, -9.9) * mm, "mid": v(1161.9, -9.9) * mm, "end": v(1161.9, -7.07) * mm});
            skArc(sketch, "E52.48.0.16", {"start": v(1161.41, -6.59) * mm, "mid": v(1158.59, -6.59) * mm, "end": v(1158.59, -9.41) * mm});
            skLineSegment(sketch, "E52.48.0.17", {"start": v(1161.41, -6.59) * mm, "end": v(1161.9, -7.07) * mm});
            skLineSegment(sketch, "E52.48.0.18", {"start": v(1158.59, -9.41) * mm, "end": v(1159.07, -9.9) * mm});
            skArc(sketch, "E52.48.0.19", {"start": v(1166.1, -7.07) * mm, "mid": v(1166.1, -9.9) * mm, "end": v(1168.93, -9.9) * mm});
            skLineSegment(sketch, "E52.48.0.20", {"start": v(1168.93, -9.9) * mm, "end": v(1169.41, -9.41) * mm});
            skArc(sketch, "E52.48.0.21", {"start": v(1169.41, -9.41) * mm, "mid": v(1169.41, -6.59) * mm, "end": v(1166.59, -6.59) * mm});
            skCircle(sketch, "E52.48.0.22", {"center": v(1168, -16) * mm, "radius": 2 * mm});
            skCircle(sketch, "E52.48.0.23", {"center": v(1160, -16) * mm, "radius": 2 * mm});
            skLineSegment(sketch, "E52.48.0.24", {"start": v(1166.1, -7.07) * mm, "end": v(1166.59, -6.59) * mm});
            skCircle(sketch, "E52.48.0.25", {"center": v(1164, 0) * mm, "radius": 2 * mm});
            skArc(sketch, "E52.48.0.26", {"start": v(1178, -12) * mm, "mid": v(1176, -10) * mm, "end": v(1174, -12) * mm});
            skArc(sketch, "E52.48.0.27", {"start": v(1174, -16) * mm, "mid": v(1176, -18) * mm, "end": v(1178, -16) * mm});
            skLineSegment(sketch, "E52.48.0.28", {"start": v(1174, -12) * mm, "end": v(1174, -16) * mm});
            skLineSegment(sketch, "E52.48.0.29", {"start": v(1178, -16) * mm, "end": v(1178, -12) * mm});
            skArc(sketch, "E52.49.0.0", {"start": v(1202, 16) * mm, "mid": v(1200, 18) * mm, "end": v(1198, 16) * mm});
            skLineSegment(sketch, "E52.49.0.1", {"start": v(1202, 16) * mm, "end": v(1202, 12) * mm});
            skLineSegment(sketch, "E52.49.0.2", {"start": v(1198, 16) * mm, "end": v(1198, 12) * mm});
            skArc(sketch, "E52.49.0.3", {"start": v(1198, 12) * mm, "mid": v(1200, 10) * mm, "end": v(1202, 12) * mm});
            skCircle(sketch, "E52.49.0.4", {"center": v(1192, 16) * mm, "radius": 2 * mm});
            skCircle(sketch, "E52.49.0.5", {"center": v(1184, 16) * mm, "radius": 2 * mm});
            skArc(sketch, "E52.49.0.6", {"start": v(1185.9, 7.07) * mm, "mid": v(1185.9, 9.9) * mm, "end": v(1183.07, 9.9) * mm});
            skArc(sketch, "E52.49.0.7", {"start": v(1182.59, 9.41) * mm, "mid": v(1182.59, 6.59) * mm, "end": v(1185.41, 6.59) * mm});
            skLineSegment(sketch, "E52.49.0.8", {"start": v(1183.07, 9.9) * mm, "end": v(1182.59, 9.41) * mm});
            skLineSegment(sketch, "E52.49.0.9", {"start": v(1185.9, 7.07) * mm, "end": v(1185.41, 6.59) * mm});
            skArc(sketch, "E52.49.0.10", {"start": v(1192.93, 9.9) * mm, "mid": v(1190.1, 9.9) * mm, "end": v(1190.1, 7.07) * mm});
            skLineSegment(sketch, "E52.49.0.11", {"start": v(1192.93, 9.9) * mm, "end": v(1193.41, 9.41) * mm});
            skArc(sketch, "E52.49.0.12", {"start": v(1190.59, 6.59) * mm, "mid": v(1193.41, 6.59) * mm, "end": v(1193.41, 9.41) * mm});
            skLineSegment(sketch, "E52.49.0.13", {"start": v(1190.1, 7.07) * mm, "end": v(1190.59, 6.59) * mm});
            skCircle(sketch, "E52.49.0.14", {"center": v(1200, 0) * mm, "radius": 7 * mm});
            skArc(sketch, "E52.49.0.15", {"start": v(1183.07, -9.9) * mm, "mid": v(1185.9, -9.9) * mm, "end": v(1185.9, -7.07) * mm});
            skArc(sketch, "E52.49.0.16", {"start": v(1185.41, -6.59) * mm, "mid": v(1182.59, -6.59) * mm, "end": v(1182.59, -9.41) * mm});
            skLineSegment(sketch, "E52.49.0.17", {"start": v(1185.41, -6.59) * mm, "end": v(1185.9, -7.07) * mm});
            skLineSegment(sketch, "E52.49.0.18", {"start": v(1182.59, -9.41) * mm, "end": v(1183.07, -9.9) * mm});
            skArc(sketch, "E52.49.0.19", {"start": v(1190.1, -7.07) * mm, "mid": v(1190.1, -9.9) * mm, "end": v(1192.93, -9.9) * mm});
            skLineSegment(sketch, "E52.49.0.20", {"start": v(1192.93, -9.9) * mm, "end": v(1193.41, -9.41) * mm});
            skArc(sketch, "E52.49.0.21", {"start": v(1193.41, -9.41) * mm, "mid": v(1193.41, -6.59) * mm, "end": v(1190.59, -6.59) * mm});
            skCircle(sketch, "E52.49.0.22", {"center": v(1192, -16) * mm, "radius": 2 * mm});
            skCircle(sketch, "E52.49.0.23", {"center": v(1184, -16) * mm, "radius": 2 * mm});
            skLineSegment(sketch, "E52.49.0.24", {"start": v(1190.1, -7.07) * mm, "end": v(1190.59, -6.59) * mm});
            skCircle(sketch, "E52.49.0.25", {"center": v(1188, 0) * mm, "radius": 2 * mm});
            skArc(sketch, "E52.49.0.26", {"start": v(1202, -12) * mm, "mid": v(1200, -10) * mm, "end": v(1198, -12) * mm});
            skArc(sketch, "E52.49.0.27", {"start": v(1198, -16) * mm, "mid": v(1200, -18) * mm, "end": v(1202, -16) * mm});
            skLineSegment(sketch, "E52.49.0.28", {"start": v(1198, -12) * mm, "end": v(1198, -16) * mm});
            skLineSegment(sketch, "E52.49.0.29", {"start": v(1202, -16) * mm, "end": v(1202, -12) * mm});
            skLineSegment(sketch, "E52.direction1", {"start": v(8, -16) * mm, "end": v(32, -16) * mm, "construction": true});
            skSolve(sketch);
        }
        {
            var Q0;
            Q0=makeQuery(id+"F20.imprint","IMPRINT",FACE,{"disambiguationData":[TD([[makeQuery(id+"F20.imprint","IMPRINT",EDGE,{"derivedFrom":sQuery(id+"F20.wireOp",EDGE,"E52.1.0.4")}),1.0]])]});
            var Q1;
            Q1=makeQuery(id+"F20.imprint","IMPRINT",FACE,{"disambiguationData":[TD([[makeQuery(id+"F20.imprint","IMPRINT",EDGE,{"derivedFrom":sQuery(id+"F20.wireOp",EDGE,"E52.1.0.10")}),1.0]])]});
            var Q2;
            Q2=makeQuery(id+"F20.imprint","IMPRINT",FACE,{"disambiguationData":[TD([[makeQuery(id+"F20.imprint","IMPRINT",EDGE,{"derivedFrom":sQuery(id+"F20.wireOp",EDGE,"E52.1.0.25")}),1.0]])]});
            var Q3;
            Q3=makeQuery(id+"F20.imprint","IMPRINT",FACE,{"disambiguationData":[TD([[makeQuery(id+"F20.imprint","IMPRINT",EDGE,{"derivedFrom":sQuery(id+"F20.wireOp",EDGE,"E52.1.0.15")}),1.0]])]});
            var Q4;
            Q4=makeQuery(id+"F20.imprint","IMPRINT",FACE,{"disambiguationData":[TD([[makeQuery(id+"F20.imprint","IMPRINT",EDGE,{"derivedFrom":sQuery(id+"F20.wireOp",EDGE,"E52.1.0.23")}),1.0]])]});
            var Q5;
            Q5=makeQuery(id+"F20.imprint","IMPRINT",FACE,{"disambiguationData":[TD([[makeQuery(id+"F20.imprint","IMPRINT",EDGE,{"derivedFrom":sQuery(id+"F20.wireOp",EDGE,"E12")}),1.0]])]});
            var Q6;
            Q6=makeQuery(id+"F20.imprint","IMPRINT",FACE,{"disambiguationData":[TD([[makeQuery(id+"F20.imprint","IMPRINT",EDGE,{"derivedFrom":sQuery(id+"F20.wireOp",EDGE,"E3")}),1.0]])]});
            var Q7;
            Q7=makeQuery(id+"F20.imprint","IMPRINT",FACE,{"disambiguationData":[TD([[makeQuery(id+"F20.imprint","IMPRINT",EDGE,{"derivedFrom":sQuery(id+"F20.wireOp",EDGE,"E8")}),1.0]])]});
            var Q8;
            Q8=makeQuery(id+"F20.imprint","IMPRINT",FACE,{"disambiguationData":[TD([[makeQuery(id+"F20.imprint","IMPRINT",EDGE,{"derivedFrom":sQuery(id+"F20.wireOp",EDGE,"E36")}),1.0]])]});
            var Q9;
            Q9=makeQuery(id+"F20.imprint","IMPRINT",FACE,{"disambiguationData":[TD([[makeQuery(id+"F20.imprint","IMPRINT",EDGE,{"derivedFrom":sQuery(id+"F20.wireOp",EDGE,"E52.1.0.19")}),1.0]])]});
            var Q10;
            Q10=makeQuery(id+"F20.imprint","IMPRINT",FACE,{"disambiguationData":[TD([[makeQuery(id+"F20.imprint","IMPRINT",EDGE,{"derivedFrom":sQuery(id+"F20.wireOp",EDGE,"E52.1.0.6")}),1.0]])]});
            var Q11;
            Q11=makeQuery(id+"F20.imprint","IMPRINT",FACE,{"disambiguationData":[TD([[makeQuery(id+"F20.imprint","IMPRINT",EDGE,{"derivedFrom":sQuery(id+"F20.wireOp",EDGE,"E31")}),1.0]])]});
            var Q12;
            Q12=makeQuery(id+"F20.imprint","IMPRINT",FACE,{"disambiguationData":[TD([[makeQuery(id+"F20.imprint","IMPRINT",EDGE,{"derivedFrom":sQuery(id+"F20.wireOp",EDGE,"E40")}),1.0]])]});
            var Q13;
            Q13=makeQuery(id+"F20.imprint","IMPRINT",FACE,{"disambiguationData":[TD([[makeQuery(id+"F20.imprint","IMPRINT",EDGE,{"derivedFrom":sQuery(id+"F20.wireOp",EDGE,"E42")}),1.0]])]});
            var Q14;
            Q14=makeQuery(id+"F20.imprint","IMPRINT",FACE,{"disambiguationData":[TD([[makeQuery(id+"F20.imprint","IMPRINT",EDGE,{"derivedFrom":sQuery(id+"F20.wireOp",EDGE,"E32")}),1.0]])]});
            var Q15;
            Q15=makeQuery(id+"F20.imprint","IMPRINT",FACE,{"disambiguationData":[TD([[makeQuery(id+"F20.imprint","IMPRINT",EDGE,{"derivedFrom":sQuery(id+"F20.wireOp",EDGE,"E37")}),1.0]])]});
            var Q16;
            Q16=makeQuery(id+"F20.imprint","IMPRINT",FACE,{"disambiguationData":[TD([[makeQuery(id+"F20.imprint","IMPRINT",EDGE,{"derivedFrom":sQuery(id+"F20.wireOp",EDGE,"E18")}),1.0]])]});
            var Q17;
            Q17=makeQuery(id+"F20.imprint","IMPRINT",FACE,{"disambiguationData":[TD([[makeQuery(id+"F20.imprint","IMPRINT",EDGE,{"derivedFrom":sQuery(id+"F20.wireOp",EDGE,"E33")}),1.0]])]});
            var Q18;
            Q18=makeQuery(id+"F20.imprint","IMPRINT",FACE,{"disambiguationData":[TD([[makeQuery(id+"F20.imprint","IMPRINT",EDGE,{"derivedFrom":sQuery(id+"F20.wireOp",EDGE,"E20")}),1.0]])]});
            var Q19;
            Q19=makeQuery(id+"F20.imprint","IMPRINT",FACE,{"disambiguationData":[TD([[makeQuery(id+"F20.imprint","IMPRINT",EDGE,{"derivedFrom":sQuery(id+"F20.wireOp",EDGE,"E52.1.0.5")}),1.0]])]});
            var Q20;
            Q20=makeQuery(id+"F20.imprint","IMPRINT",FACE,{"disambiguationData":[TD([[makeQuery(id+"F20.imprint","IMPRINT",EDGE,{"derivedFrom":sQuery(id+"F20.wireOp",EDGE,"E52.1.0.22")}),1.0]])]});
            extrude(context, id + "F21", {"entities" : qUnion([Q0, Q1, Q2, Q3, Q4, Q5, Q6, Q7, Q8, Q9, Q10, Q11, Q12, Q13, Q14, Q15, Q16, Q17, Q18, Q19, Q20]), "operationType" : NewBodyOperationType.REMOVE, "oppositeDirection" : true, "depth" : 50 * mm, "offsetDistance" : 25 * mm, "symmetric" : true});
        }
        {
            var Q0;
            Q0=makeQuery(id+"F20.imprint","IMPRINT",FACE,{"disambiguationData":[TD([[makeQuery(id+"F20.imprint","IMPRINT",EDGE,{"derivedFrom":sQuery(id+"F20.wireOp",EDGE,"E52.1.0.0")}),1.0]])]});
            var Q1;
            Q1=makeQuery(id+"F20.imprint","IMPRINT",FACE,{"disambiguationData":[TD([[makeQuery(id+"F20.imprint","IMPRINT",EDGE,{"derivedFrom":sQuery(id+"F20.wireOp",EDGE,"E52.2.0.6")}),1.0]])]});
            var Q2;
            Q2=makeQuery(id+"F20.imprint","IMPRINT",FACE,{"disambiguationData":[TD([[makeQuery(id+"F20.imprint","IMPRINT",EDGE,{"derivedFrom":sQuery(id+"F20.wireOp",EDGE,"E52.2.0.5")}),1.0]])]});
            var Q3;
            Q3=makeQuery(id+"F20.imprint","IMPRINT",FACE,{"disambiguationData":[TD([[makeQuery(id+"F20.imprint","IMPRINT",EDGE,{"derivedFrom":sQuery(id+"F20.wireOp",EDGE,"E52.1.0.14")}),1.0]])]});
            var Q4;
            Q4=makeQuery(id+"F20.imprint","IMPRINT",FACE,{"disambiguationData":[TD([[makeQuery(id+"F20.imprint","IMPRINT",EDGE,{"derivedFrom":sQuery(id+"F20.wireOp",EDGE,"E52.1.0.26")}),1.0]])]});
            var Q5;
            Q5=makeQuery(id+"F20.imprint","IMPRINT",FACE,{"disambiguationData":[TD([[makeQuery(id+"F20.imprint","IMPRINT",EDGE,{"derivedFrom":sQuery(id+"F20.wireOp",EDGE,"E52.2.0.23")}),1.0]])]});
            var Q6;
            Q6=makeQuery(id+"F20.imprint","IMPRINT",FACE,{"disambiguationData":[TD([[makeQuery(id+"F20.imprint","IMPRINT",EDGE,{"derivedFrom":sQuery(id+"F20.wireOp",EDGE,"E52.2.0.22")}),1.0]])]});
            var Q7;
            Q7=makeQuery(id+"F20.imprint","IMPRINT",FACE,{"disambiguationData":[TD([[makeQuery(id+"F20.imprint","IMPRINT",EDGE,{"derivedFrom":sQuery(id+"F20.wireOp",EDGE,"E52.2.0.19")}),1.0]])]});
            var Q8;
            Q8=makeQuery(id+"F20.imprint","IMPRINT",FACE,{"disambiguationData":[TD([[makeQuery(id+"F20.imprint","IMPRINT",EDGE,{"derivedFrom":sQuery(id+"F20.wireOp",EDGE,"E52.2.0.15")}),1.0]])]});
            var Q9;
            Q9=makeQuery(id+"F20.imprint","IMPRINT",FACE,{"disambiguationData":[TD([[makeQuery(id+"F20.imprint","IMPRINT",EDGE,{"derivedFrom":sQuery(id+"F20.wireOp",EDGE,"E52.2.0.25")}),1.0]])]});
            var Q10;
            Q10=makeQuery(id+"F20.imprint","IMPRINT",FACE,{"disambiguationData":[TD([[makeQuery(id+"F20.imprint","IMPRINT",EDGE,{"derivedFrom":sQuery(id+"F20.wireOp",EDGE,"E52.2.0.10")}),1.0]])]});
            var Q11;
            Q11=makeQuery(id+"F20.imprint","IMPRINT",FACE,{"disambiguationData":[TD([[makeQuery(id+"F20.imprint","IMPRINT",EDGE,{"derivedFrom":sQuery(id+"F20.wireOp",EDGE,"E52.2.0.4")}),1.0]])]});
            extrude(context, id + "F22", {"entities" : qUnion([Q0, Q1, Q2, Q3, Q4, Q5, Q6, Q7, Q8, Q9, Q10, Q11]), "operationType" : NewBodyOperationType.REMOVE, "oppositeDirection" : true, "depth" : 50 * mm, "offsetDistance" : 25 * mm, "symmetric" : true});
        }
        {
            var Q0;
            Q0=makeQuery(id+"F20.imprint","IMPRINT",FACE,{"disambiguationData":[TD([[makeQuery(id+"F20.imprint","IMPRINT",EDGE,{"derivedFrom":sQuery(id+"F20.wireOp",EDGE,"E52.2.0.26")}),1.0]])]});
            var Q1;
            Q1=makeQuery(id+"F20.imprint","IMPRINT",FACE,{"disambiguationData":[TD([[makeQuery(id+"F20.imprint","IMPRINT",EDGE,{"derivedFrom":sQuery(id+"F20.wireOp",EDGE,"E52.3.0.23")}),1.0]])]});
            var Q2;
            Q2=makeQuery(id+"F20.imprint","IMPRINT",FACE,{"disambiguationData":[TD([[makeQuery(id+"F20.imprint","IMPRINT",EDGE,{"derivedFrom":sQuery(id+"F20.wireOp",EDGE,"E52.3.0.22")}),1.0]])]});
            var Q3;
            Q3=makeQuery(id+"F20.imprint","IMPRINT",FACE,{"disambiguationData":[TD([[makeQuery(id+"F20.imprint","IMPRINT",EDGE,{"derivedFrom":sQuery(id+"F20.wireOp",EDGE,"E52.3.0.19")}),1.0]])]});
            var Q4;
            Q4=makeQuery(id+"F20.imprint","IMPRINT",FACE,{"disambiguationData":[TD([[makeQuery(id+"F20.imprint","IMPRINT",EDGE,{"derivedFrom":sQuery(id+"F20.wireOp",EDGE,"E52.3.0.15")}),1.0]])]});
            var Q5;
            Q5=makeQuery(id+"F20.imprint","IMPRINT",FACE,{"disambiguationData":[TD([[makeQuery(id+"F20.imprint","IMPRINT",EDGE,{"derivedFrom":sQuery(id+"F20.wireOp",EDGE,"E52.2.0.14")}),1.0]])]});
            var Q6;
            Q6=makeQuery(id+"F20.imprint","IMPRINT",FACE,{"disambiguationData":[TD([[makeQuery(id+"F20.imprint","IMPRINT",EDGE,{"derivedFrom":sQuery(id+"F20.wireOp",EDGE,"E52.3.0.25")}),1.0]])]});
            var Q7;
            Q7=makeQuery(id+"F20.imprint","IMPRINT",FACE,{"disambiguationData":[TD([[makeQuery(id+"F20.imprint","IMPRINT",EDGE,{"derivedFrom":sQuery(id+"F20.wireOp",EDGE,"E52.2.0.0")}),1.0]])]});
            var Q8;
            Q8=makeQuery(id+"F20.imprint","IMPRINT",FACE,{"disambiguationData":[TD([[makeQuery(id+"F20.imprint","IMPRINT",EDGE,{"derivedFrom":sQuery(id+"F20.wireOp",EDGE,"E52.3.0.6")}),1.0]])]});
            var Q9;
            Q9=makeQuery(id+"F20.imprint","IMPRINT",FACE,{"disambiguationData":[TD([[makeQuery(id+"F20.imprint","IMPRINT",EDGE,{"derivedFrom":sQuery(id+"F20.wireOp",EDGE,"E52.3.0.5")}),1.0]])]});
            var Q10;
            Q10=makeQuery(id+"F20.imprint","IMPRINT",FACE,{"disambiguationData":[TD([[makeQuery(id+"F20.imprint","IMPRINT",EDGE,{"derivedFrom":sQuery(id+"F20.wireOp",EDGE,"E52.3.0.10")}),1.0]])]});
            var Q11;
            Q11=makeQuery(id+"F20.imprint","IMPRINT",FACE,{"disambiguationData":[TD([[makeQuery(id+"F20.imprint","IMPRINT",EDGE,{"derivedFrom":sQuery(id+"F20.wireOp",EDGE,"E52.3.0.4")}),1.0]])]});
            extrude(context, id + "F23", {"entities" : qUnion([Q0, Q1, Q2, Q3, Q4, Q5, Q6, Q7, Q8, Q9, Q10, Q11]), "operationType" : NewBodyOperationType.REMOVE, "oppositeDirection" : true, "depth" : 50 * mm, "offsetDistance" : 25 * mm, "symmetric" : true});
        }
        {
            var Q0;
            Q0=makeQuery(id+"F20.imprint","IMPRINT",FACE,{"disambiguationData":[TD([[makeQuery(id+"F20.imprint","IMPRINT",EDGE,{"derivedFrom":sQuery(id+"F20.wireOp",EDGE,"E52.3.0.26")}),1.0]])]});
            var Q1;
            Q1=makeQuery(id+"F20.imprint","IMPRINT",FACE,{"disambiguationData":[TD([[makeQuery(id+"F20.imprint","IMPRINT",EDGE,{"derivedFrom":sQuery(id+"F20.wireOp",EDGE,"E52.4.0.23")}),1.0]])]});
            var Q2;
            Q2=makeQuery(id+"F20.imprint","IMPRINT",FACE,{"disambiguationData":[TD([[makeQuery(id+"F20.imprint","IMPRINT",EDGE,{"derivedFrom":sQuery(id+"F20.wireOp",EDGE,"E52.4.0.22")}),1.0]])]});
            var Q3;
            Q3=makeQuery(id+"F20.imprint","IMPRINT",FACE,{"disambiguationData":[TD([[makeQuery(id+"F20.imprint","IMPRINT",EDGE,{"derivedFrom":sQuery(id+"F20.wireOp",EDGE,"E52.4.0.19")}),1.0]])]});
            var Q4;
            Q4=makeQuery(id+"F20.imprint","IMPRINT",FACE,{"disambiguationData":[TD([[makeQuery(id+"F20.imprint","IMPRINT",EDGE,{"derivedFrom":sQuery(id+"F20.wireOp",EDGE,"E52.4.0.15")}),1.0]])]});
            var Q5;
            Q5=makeQuery(id+"F20.imprint","IMPRINT",FACE,{"disambiguationData":[TD([[makeQuery(id+"F20.imprint","IMPRINT",EDGE,{"derivedFrom":sQuery(id+"F20.wireOp",EDGE,"E52.3.0.14")}),1.0]])]});
            var Q6;
            Q6=makeQuery(id+"F20.imprint","IMPRINT",FACE,{"disambiguationData":[TD([[makeQuery(id+"F20.imprint","IMPRINT",EDGE,{"derivedFrom":sQuery(id+"F20.wireOp",EDGE,"E52.3.0.0")}),1.0]])]});
            var Q7;
            Q7=makeQuery(id+"F20.imprint","IMPRINT",FACE,{"disambiguationData":[TD([[makeQuery(id+"F20.imprint","IMPRINT",EDGE,{"derivedFrom":sQuery(id+"F20.wireOp",EDGE,"E52.4.0.5")}),1.0]])]});
            var Q8;
            Q8=makeQuery(id+"F20.imprint","IMPRINT",FACE,{"disambiguationData":[TD([[makeQuery(id+"F20.imprint","IMPRINT",EDGE,{"derivedFrom":sQuery(id+"F20.wireOp",EDGE,"E52.4.0.6")}),1.0]])]});
            var Q9;
            Q9=makeQuery(id+"F20.imprint","IMPRINT",FACE,{"disambiguationData":[TD([[makeQuery(id+"F20.imprint","IMPRINT",EDGE,{"derivedFrom":sQuery(id+"F20.wireOp",EDGE,"E52.4.0.10")}),1.0]])]});
            var Q10;
            Q10=makeQuery(id+"F20.imprint","IMPRINT",FACE,{"disambiguationData":[TD([[makeQuery(id+"F20.imprint","IMPRINT",EDGE,{"derivedFrom":sQuery(id+"F20.wireOp",EDGE,"E52.4.0.4")}),1.0]])]});
            var Q11;
            Q11=makeQuery(id+"F20.imprint","IMPRINT",FACE,{"disambiguationData":[TD([[makeQuery(id+"F20.imprint","IMPRINT",EDGE,{"derivedFrom":sQuery(id+"F20.wireOp",EDGE,"E52.4.0.25")}),1.0]])]});
            extrude(context, id + "F24", {"entities" : qUnion([Q0, Q1, Q2, Q3, Q4, Q5, Q6, Q7, Q8, Q9, Q10, Q11]), "operationType" : NewBodyOperationType.REMOVE, "oppositeDirection" : true, "depth" : 50 * mm, "offsetDistance" : 25 * mm, "symmetric" : true});
        }
        {
            var Q0;
            Q0=makeQuery(id+"F20.imprint","IMPRINT",FACE,{"disambiguationData":[TD([[makeQuery(id+"F20.imprint","IMPRINT",EDGE,{"derivedFrom":sQuery(id+"F20.wireOp",EDGE,"E52.4.0.26")}),1.0]])]});
            var Q1;
            Q1=makeQuery(id+"F20.imprint","IMPRINT",FACE,{"disambiguationData":[TD([[makeQuery(id+"F20.imprint","IMPRINT",EDGE,{"derivedFrom":sQuery(id+"F20.wireOp",EDGE,"E52.5.0.23")}),1.0]])]});
            var Q2;
            Q2=makeQuery(id+"F20.imprint","IMPRINT",FACE,{"disambiguationData":[TD([[makeQuery(id+"F20.imprint","IMPRINT",EDGE,{"derivedFrom":sQuery(id+"F20.wireOp",EDGE,"E52.5.0.22")}),1.0]])]});
            var Q3;
            Q3=makeQuery(id+"F20.imprint","IMPRINT",FACE,{"disambiguationData":[TD([[makeQuery(id+"F20.imprint","IMPRINT",EDGE,{"derivedFrom":sQuery(id+"F20.wireOp",EDGE,"E52.5.0.19")}),1.0]])]});
            var Q4;
            Q4=makeQuery(id+"F20.imprint","IMPRINT",FACE,{"disambiguationData":[TD([[makeQuery(id+"F20.imprint","IMPRINT",EDGE,{"derivedFrom":sQuery(id+"F20.wireOp",EDGE,"E52.5.0.15")}),1.0]])]});
            var Q5;
            Q5=makeQuery(id+"F20.imprint","IMPRINT",FACE,{"disambiguationData":[TD([[makeQuery(id+"F20.imprint","IMPRINT",EDGE,{"derivedFrom":sQuery(id+"F20.wireOp",EDGE,"E52.4.0.14")}),1.0]])]});
            var Q6;
            Q6=makeQuery(id+"F20.imprint","IMPRINT",FACE,{"disambiguationData":[TD([[makeQuery(id+"F20.imprint","IMPRINT",EDGE,{"derivedFrom":sQuery(id+"F20.wireOp",EDGE,"E52.5.0.25")}),1.0]])]});
            var Q7;
            Q7=makeQuery(id+"F20.imprint","IMPRINT",FACE,{"disambiguationData":[TD([[makeQuery(id+"F20.imprint","IMPRINT",EDGE,{"derivedFrom":sQuery(id+"F20.wireOp",EDGE,"E52.5.0.6")}),1.0]])]});
            var Q8;
            Q8=makeQuery(id+"F20.imprint","IMPRINT",FACE,{"disambiguationData":[TD([[makeQuery(id+"F20.imprint","IMPRINT",EDGE,{"derivedFrom":sQuery(id+"F20.wireOp",EDGE,"E52.4.0.0")}),1.0]])]});
            var Q9;
            Q9=makeQuery(id+"F20.imprint","IMPRINT",FACE,{"disambiguationData":[TD([[makeQuery(id+"F20.imprint","IMPRINT",EDGE,{"derivedFrom":sQuery(id+"F20.wireOp",EDGE,"E52.5.0.5")}),1.0]])]});
            var Q10;
            Q10=makeQuery(id+"F20.imprint","IMPRINT",FACE,{"disambiguationData":[TD([[makeQuery(id+"F20.imprint","IMPRINT",EDGE,{"derivedFrom":sQuery(id+"F20.wireOp",EDGE,"E52.5.0.4")}),1.0]])]});
            var Q11;
            Q11=makeQuery(id+"F20.imprint","IMPRINT",FACE,{"disambiguationData":[TD([[makeQuery(id+"F20.imprint","IMPRINT",EDGE,{"derivedFrom":sQuery(id+"F20.wireOp",EDGE,"E52.5.0.10")}),1.0]])]});
            extrude(context, id + "F25", {"entities" : qUnion([Q0, Q1, Q2, Q3, Q4, Q5, Q6, Q7, Q8, Q9, Q10, Q11]), "operationType" : NewBodyOperationType.REMOVE, "oppositeDirection" : true, "depth" : 50 * mm, "offsetDistance" : 25 * mm, "symmetric" : true});
        }
        {
            var Q0;
            Q0=makeQuery(id+"F20.imprint","IMPRINT",FACE,{"disambiguationData":[TD([[makeQuery(id+"F20.imprint","IMPRINT",EDGE,{"derivedFrom":sQuery(id+"F20.wireOp",EDGE,"E52.7.0.22")}),1.0]])]});
            var Q1;
            Q1=makeQuery(id+"F20.imprint","IMPRINT",FACE,{"disambiguationData":[TD([[makeQuery(id+"F20.imprint","IMPRINT",EDGE,{"derivedFrom":sQuery(id+"F20.wireOp",EDGE,"E52.7.0.23")}),1.0]])]});
            var Q2;
            Q2=makeQuery(id+"F20.imprint","IMPRINT",FACE,{"disambiguationData":[TD([[makeQuery(id+"F20.imprint","IMPRINT",EDGE,{"derivedFrom":sQuery(id+"F20.wireOp",EDGE,"E52.6.0.26")}),1.0]])]});
            var Q3;
            Q3=makeQuery(id+"F20.imprint","IMPRINT",FACE,{"disambiguationData":[TD([[makeQuery(id+"F20.imprint","IMPRINT",EDGE,{"derivedFrom":sQuery(id+"F20.wireOp",EDGE,"E52.6.0.22")}),1.0]])]});
            var Q4;
            Q4=makeQuery(id+"F20.imprint","IMPRINT",FACE,{"disambiguationData":[TD([[makeQuery(id+"F20.imprint","IMPRINT",EDGE,{"derivedFrom":sQuery(id+"F20.wireOp",EDGE,"E52.6.0.23")}),1.0]])]});
            var Q5;
            Q5=makeQuery(id+"F20.imprint","IMPRINT",FACE,{"disambiguationData":[TD([[makeQuery(id+"F20.imprint","IMPRINT",EDGE,{"derivedFrom":sQuery(id+"F20.wireOp",EDGE,"E52.5.0.26")}),1.0]])]});
            var Q6;
            Q6=makeQuery(id+"F20.imprint","IMPRINT",FACE,{"disambiguationData":[TD([[makeQuery(id+"F20.imprint","IMPRINT",EDGE,{"derivedFrom":sQuery(id+"F20.wireOp",EDGE,"E52.6.0.15")}),1.0]])]});
            var Q7;
            Q7=makeQuery(id+"F20.imprint","IMPRINT",FACE,{"disambiguationData":[TD([[makeQuery(id+"F20.imprint","IMPRINT",EDGE,{"derivedFrom":sQuery(id+"F20.wireOp",EDGE,"E52.6.0.19")}),1.0]])]});
            var Q8;
            Q8=makeQuery(id+"F20.imprint","IMPRINT",FACE,{"disambiguationData":[TD([[makeQuery(id+"F20.imprint","IMPRINT",EDGE,{"derivedFrom":sQuery(id+"F20.wireOp",EDGE,"E52.7.0.15")}),1.0]])]});
            var Q9;
            Q9=makeQuery(id+"F20.imprint","IMPRINT",FACE,{"disambiguationData":[TD([[makeQuery(id+"F20.imprint","IMPRINT",EDGE,{"derivedFrom":sQuery(id+"F20.wireOp",EDGE,"E52.7.0.19")}),1.0]])]});
            var Q10;
            Q10=makeQuery(id+"F20.imprint","IMPRINT",FACE,{"disambiguationData":[TD([[makeQuery(id+"F20.imprint","IMPRINT",EDGE,{"derivedFrom":sQuery(id+"F20.wireOp",EDGE,"E52.7.0.25")}),1.0]])]});
            var Q11;
            Q11=makeQuery(id+"F20.imprint","IMPRINT",FACE,{"disambiguationData":[TD([[makeQuery(id+"F20.imprint","IMPRINT",EDGE,{"derivedFrom":sQuery(id+"F20.wireOp",EDGE,"E52.6.0.14")}),1.0]])]});
            var Q12;
            Q12=makeQuery(id+"F20.imprint","IMPRINT",FACE,{"disambiguationData":[TD([[makeQuery(id+"F20.imprint","IMPRINT",EDGE,{"derivedFrom":sQuery(id+"F20.wireOp",EDGE,"E52.6.0.25")}),1.0]])]});
            var Q13;
            Q13=makeQuery(id+"F20.imprint","IMPRINT",FACE,{"disambiguationData":[TD([[makeQuery(id+"F20.imprint","IMPRINT",EDGE,{"derivedFrom":sQuery(id+"F20.wireOp",EDGE,"E52.5.0.14")}),1.0]])]});
            var Q14;
            Q14=makeQuery(id+"F20.imprint","IMPRINT",FACE,{"disambiguationData":[TD([[makeQuery(id+"F20.imprint","IMPRINT",EDGE,{"derivedFrom":sQuery(id+"F20.wireOp",EDGE,"E52.5.0.0")}),1.0]])]});
            var Q15;
            Q15=makeQuery(id+"F20.imprint","IMPRINT",FACE,{"disambiguationData":[TD([[makeQuery(id+"F20.imprint","IMPRINT",EDGE,{"derivedFrom":sQuery(id+"F20.wireOp",EDGE,"E52.6.0.6")}),1.0]])]});
            var Q16;
            Q16=makeQuery(id+"F20.imprint","IMPRINT",FACE,{"disambiguationData":[TD([[makeQuery(id+"F20.imprint","IMPRINT",EDGE,{"derivedFrom":sQuery(id+"F20.wireOp",EDGE,"E52.6.0.5")}),1.0]])]});
            var Q17;
            Q17=makeQuery(id+"F20.imprint","IMPRINT",FACE,{"disambiguationData":[TD([[makeQuery(id+"F20.imprint","IMPRINT",EDGE,{"derivedFrom":sQuery(id+"F20.wireOp",EDGE,"E52.6.0.10")}),1.0]])]});
            var Q18;
            Q18=makeQuery(id+"F20.imprint","IMPRINT",FACE,{"disambiguationData":[TD([[makeQuery(id+"F20.imprint","IMPRINT",EDGE,{"derivedFrom":sQuery(id+"F20.wireOp",EDGE,"E52.6.0.4")}),1.0]])]});
            var Q19;
            Q19=makeQuery(id+"F20.imprint","IMPRINT",FACE,{"disambiguationData":[TD([[makeQuery(id+"F20.imprint","IMPRINT",EDGE,{"derivedFrom":sQuery(id+"F20.wireOp",EDGE,"E52.6.0.0")}),1.0]])]});
            var Q20;
            Q20=makeQuery(id+"F20.imprint","IMPRINT",FACE,{"disambiguationData":[TD([[makeQuery(id+"F20.imprint","IMPRINT",EDGE,{"derivedFrom":sQuery(id+"F20.wireOp",EDGE,"E52.7.0.5")}),1.0]])]});
            var Q21;
            Q21=makeQuery(id+"F20.imprint","IMPRINT",FACE,{"disambiguationData":[TD([[makeQuery(id+"F20.imprint","IMPRINT",EDGE,{"derivedFrom":sQuery(id+"F20.wireOp",EDGE,"E52.7.0.6")}),1.0]])]});
            var Q22;
            Q22=makeQuery(id+"F20.imprint","IMPRINT",FACE,{"disambiguationData":[TD([[makeQuery(id+"F20.imprint","IMPRINT",EDGE,{"derivedFrom":sQuery(id+"F20.wireOp",EDGE,"E52.7.0.10")}),1.0]])]});
            var Q23;
            Q23=makeQuery(id+"F20.imprint","IMPRINT",FACE,{"disambiguationData":[TD([[makeQuery(id+"F20.imprint","IMPRINT",EDGE,{"derivedFrom":sQuery(id+"F20.wireOp",EDGE,"E52.7.0.4")}),1.0]])]});
            extrude(context, id + "F26", {"entities" : qUnion([Q0, Q1, Q2, Q3, Q4, Q5, Q6, Q7, Q8, Q9, Q10, Q11, Q12, Q13, Q14, Q15, Q16, Q17, Q18, Q19, Q20, Q21, Q22, Q23]), "operationType" : NewBodyOperationType.REMOVE, "depth" : 50 * mm, "offsetDistance" : 25 * mm, "symmetric" : true});
        }
        {
            var Q0;
            Q0=makeQuery(id+"F20.imprint","IMPRINT",FACE,{"disambiguationData":[TD([[makeQuery(id+"F20.imprint","IMPRINT",EDGE,{"derivedFrom":sQuery(id+"F20.wireOp",EDGE,"E52.7.0.26")}),1.0]])]});
            var Q1;
            Q1=makeQuery(id+"F20.imprint","IMPRINT",FACE,{"disambiguationData":[TD([[makeQuery(id+"F20.imprint","IMPRINT",EDGE,{"derivedFrom":sQuery(id+"F20.wireOp",EDGE,"E52.8.0.23")}),1.0]])]});
            var Q2;
            Q2=makeQuery(id+"F20.imprint","IMPRINT",FACE,{"disambiguationData":[TD([[makeQuery(id+"F20.imprint","IMPRINT",EDGE,{"derivedFrom":sQuery(id+"F20.wireOp",EDGE,"E52.8.0.22")}),1.0]])]});
            var Q3;
            Q3=makeQuery(id+"F20.imprint","IMPRINT",FACE,{"disambiguationData":[TD([[makeQuery(id+"F20.imprint","IMPRINT",EDGE,{"derivedFrom":sQuery(id+"F20.wireOp",EDGE,"E52.8.0.26")}),1.0]])]});
            var Q4;
            Q4=makeQuery(id+"F20.imprint","IMPRINT",FACE,{"disambiguationData":[TD([[makeQuery(id+"F20.imprint","IMPRINT",EDGE,{"derivedFrom":sQuery(id+"F20.wireOp",EDGE,"E52.9.0.23")}),1.0]])]});
            var Q5;
            Q5=makeQuery(id+"F20.imprint","IMPRINT",FACE,{"disambiguationData":[TD([[makeQuery(id+"F20.imprint","IMPRINT",EDGE,{"derivedFrom":sQuery(id+"F20.wireOp",EDGE,"E52.9.0.22")}),1.0]])]});
            var Q6;
            Q6=makeQuery(id+"F20.imprint","IMPRINT",FACE,{"disambiguationData":[TD([[makeQuery(id+"F20.imprint","IMPRINT",EDGE,{"derivedFrom":sQuery(id+"F20.wireOp",EDGE,"E52.9.0.19")}),1.0]])]});
            var Q7;
            Q7=makeQuery(id+"F20.imprint","IMPRINT",FACE,{"disambiguationData":[TD([[makeQuery(id+"F20.imprint","IMPRINT",EDGE,{"derivedFrom":sQuery(id+"F20.wireOp",EDGE,"E52.9.0.15")}),1.0]])]});
            var Q8;
            Q8=makeQuery(id+"F20.imprint","IMPRINT",FACE,{"disambiguationData":[TD([[makeQuery(id+"F20.imprint","IMPRINT",EDGE,{"derivedFrom":sQuery(id+"F20.wireOp",EDGE,"E52.8.0.19")}),1.0]])]});
            var Q9;
            Q9=makeQuery(id+"F20.imprint","IMPRINT",FACE,{"disambiguationData":[TD([[makeQuery(id+"F20.imprint","IMPRINT",EDGE,{"derivedFrom":sQuery(id+"F20.wireOp",EDGE,"E52.8.0.15")}),1.0]])]});
            var Q10;
            Q10=makeQuery(id+"F20.imprint","IMPRINT",FACE,{"disambiguationData":[TD([[makeQuery(id+"F20.imprint","IMPRINT",EDGE,{"derivedFrom":sQuery(id+"F20.wireOp",EDGE,"E52.7.0.14")}),1.0]])]});
            var Q11;
            Q11=makeQuery(id+"F20.imprint","IMPRINT",FACE,{"disambiguationData":[TD([[makeQuery(id+"F20.imprint","IMPRINT",EDGE,{"derivedFrom":sQuery(id+"F20.wireOp",EDGE,"E52.8.0.25")}),1.0]])]});
            var Q12;
            Q12=makeQuery(id+"F20.imprint","IMPRINT",FACE,{"disambiguationData":[TD([[makeQuery(id+"F20.imprint","IMPRINT",EDGE,{"derivedFrom":sQuery(id+"F20.wireOp",EDGE,"E52.8.0.14")}),1.0]])]});
            var Q13;
            Q13=makeQuery(id+"F20.imprint","IMPRINT",FACE,{"disambiguationData":[TD([[makeQuery(id+"F20.imprint","IMPRINT",EDGE,{"derivedFrom":sQuery(id+"F20.wireOp",EDGE,"E52.9.0.25")}),1.0]])]});
            var Q14;
            Q14=makeQuery(id+"F20.imprint","IMPRINT",FACE,{"disambiguationData":[TD([[makeQuery(id+"F20.imprint","IMPRINT",EDGE,{"derivedFrom":sQuery(id+"F20.wireOp",EDGE,"E52.9.0.10")}),1.0]])]});
            var Q15;
            Q15=makeQuery(id+"F20.imprint","IMPRINT",FACE,{"disambiguationData":[TD([[makeQuery(id+"F20.imprint","IMPRINT",EDGE,{"derivedFrom":sQuery(id+"F20.wireOp",EDGE,"E52.9.0.4")}),1.0]])]});
            var Q16;
            Q16=makeQuery(id+"F20.imprint","IMPRINT",FACE,{"disambiguationData":[TD([[makeQuery(id+"F20.imprint","IMPRINT",EDGE,{"derivedFrom":sQuery(id+"F20.wireOp",EDGE,"E52.9.0.6")}),1.0]])]});
            var Q17;
            Q17=makeQuery(id+"F20.imprint","IMPRINT",FACE,{"disambiguationData":[TD([[makeQuery(id+"F20.imprint","IMPRINT",EDGE,{"derivedFrom":sQuery(id+"F20.wireOp",EDGE,"E52.9.0.5")}),1.0]])]});
            var Q18;
            Q18=makeQuery(id+"F20.imprint","IMPRINT",FACE,{"disambiguationData":[TD([[makeQuery(id+"F20.imprint","IMPRINT",EDGE,{"derivedFrom":sQuery(id+"F20.wireOp",EDGE,"E52.8.0.0")}),1.0]])]});
            var Q19;
            Q19=makeQuery(id+"F20.imprint","IMPRINT",FACE,{"disambiguationData":[TD([[makeQuery(id+"F20.imprint","IMPRINT",EDGE,{"derivedFrom":sQuery(id+"F20.wireOp",EDGE,"E52.8.0.10")}),1.0]])]});
            var Q20;
            Q20=makeQuery(id+"F20.imprint","IMPRINT",FACE,{"disambiguationData":[TD([[makeQuery(id+"F20.imprint","IMPRINT",EDGE,{"derivedFrom":sQuery(id+"F20.wireOp",EDGE,"E52.8.0.4")}),1.0]])]});
            var Q21;
            Q21=makeQuery(id+"F20.imprint","IMPRINT",FACE,{"disambiguationData":[TD([[makeQuery(id+"F20.imprint","IMPRINT",EDGE,{"derivedFrom":sQuery(id+"F20.wireOp",EDGE,"E52.8.0.6")}),1.0]])]});
            var Q22;
            Q22=makeQuery(id+"F20.imprint","IMPRINT",FACE,{"disambiguationData":[TD([[makeQuery(id+"F20.imprint","IMPRINT",EDGE,{"derivedFrom":sQuery(id+"F20.wireOp",EDGE,"E52.8.0.5")}),1.0]])]});
            var Q23;
            Q23=makeQuery(id+"F20.imprint","IMPRINT",FACE,{"disambiguationData":[TD([[makeQuery(id+"F20.imprint","IMPRINT",EDGE,{"derivedFrom":sQuery(id+"F20.wireOp",EDGE,"E52.7.0.0")}),1.0]])]});
            extrude(context, id + "F27", {"entities" : qUnion([Q0, Q1, Q2, Q3, Q4, Q5, Q6, Q7, Q8, Q9, Q10, Q11, Q12, Q13, Q14, Q15, Q16, Q17, Q18, Q19, Q20, Q21, Q22, Q23]), "operationType" : NewBodyOperationType.REMOVE, "oppositeDirection" : true, "depth" : 56 * mm, "offsetDistance" : 25 * mm, "symmetric" : true});
        }
        {
            var Q0;
            Q0=makeQuery(id+"F20.imprint","IMPRINT",FACE,{"disambiguationData":[TD([[makeQuery(id+"F20.imprint","IMPRINT",EDGE,{"derivedFrom":sQuery(id+"F20.wireOp",EDGE,"E52.9.0.26")}),1.0]])]});
            var Q1;
            Q1=makeQuery(id+"F20.imprint","IMPRINT",FACE,{"disambiguationData":[TD([[makeQuery(id+"F20.imprint","IMPRINT",EDGE,{"derivedFrom":sQuery(id+"F20.wireOp",EDGE,"E52.10.0.23")}),1.0]])]});
            var Q2;
            Q2=makeQuery(id+"F20.imprint","IMPRINT",FACE,{"disambiguationData":[TD([[makeQuery(id+"F20.imprint","IMPRINT",EDGE,{"derivedFrom":sQuery(id+"F20.wireOp",EDGE,"E52.10.0.22")}),1.0]])]});
            var Q3;
            Q3=makeQuery(id+"F20.imprint","IMPRINT",FACE,{"disambiguationData":[TD([[makeQuery(id+"F20.imprint","IMPRINT",EDGE,{"derivedFrom":sQuery(id+"F20.wireOp",EDGE,"E52.10.0.26")}),1.0]])]});
            var Q4;
            Q4=makeQuery(id+"F20.imprint","IMPRINT",FACE,{"disambiguationData":[TD([[makeQuery(id+"F20.imprint","IMPRINT",EDGE,{"derivedFrom":sQuery(id+"F20.wireOp",EDGE,"E52.11.0.23")}),1.0]])]});
            var Q5;
            Q5=makeQuery(id+"F20.imprint","IMPRINT",FACE,{"disambiguationData":[TD([[makeQuery(id+"F20.imprint","IMPRINT",EDGE,{"derivedFrom":sQuery(id+"F20.wireOp",EDGE,"E52.11.0.22")}),1.0]])]});
            var Q6;
            Q6=makeQuery(id+"F20.imprint","IMPRINT",FACE,{"disambiguationData":[TD([[makeQuery(id+"F20.imprint","IMPRINT",EDGE,{"derivedFrom":sQuery(id+"F20.wireOp",EDGE,"E52.11.0.19")}),1.0]])]});
            var Q7;
            Q7=makeQuery(id+"F20.imprint","IMPRINT",FACE,{"disambiguationData":[TD([[makeQuery(id+"F20.imprint","IMPRINT",EDGE,{"derivedFrom":sQuery(id+"F20.wireOp",EDGE,"E52.11.0.15")}),1.0]])]});
            var Q8;
            Q8=makeQuery(id+"F20.imprint","IMPRINT",FACE,{"disambiguationData":[TD([[makeQuery(id+"F20.imprint","IMPRINT",EDGE,{"derivedFrom":sQuery(id+"F20.wireOp",EDGE,"E52.11.0.25")}),1.0]])]});
            var Q9;
            Q9=makeQuery(id+"F20.imprint","IMPRINT",FACE,{"disambiguationData":[TD([[makeQuery(id+"F20.imprint","IMPRINT",EDGE,{"derivedFrom":sQuery(id+"F20.wireOp",EDGE,"E52.11.0.10")}),1.0]])]});
            var Q10;
            Q10=makeQuery(id+"F20.imprint","IMPRINT",FACE,{"disambiguationData":[TD([[makeQuery(id+"F20.imprint","IMPRINT",EDGE,{"derivedFrom":sQuery(id+"F20.wireOp",EDGE,"E52.11.0.4")}),1.0]])]});
            var Q11;
            Q11=makeQuery(id+"F20.imprint","IMPRINT",FACE,{"disambiguationData":[TD([[makeQuery(id+"F20.imprint","IMPRINT",EDGE,{"derivedFrom":sQuery(id+"F20.wireOp",EDGE,"E52.11.0.6")}),1.0]])]});
            var Q12;
            Q12=makeQuery(id+"F20.imprint","IMPRINT",FACE,{"disambiguationData":[TD([[makeQuery(id+"F20.imprint","IMPRINT",EDGE,{"derivedFrom":sQuery(id+"F20.wireOp",EDGE,"E52.11.0.5")}),1.0]])]});
            var Q13;
            Q13=makeQuery(id+"F20.imprint","IMPRINT",FACE,{"disambiguationData":[TD([[makeQuery(id+"F20.imprint","IMPRINT",EDGE,{"derivedFrom":sQuery(id+"F20.wireOp",EDGE,"E52.10.0.14")}),1.0]])]});
            var Q14;
            Q14=makeQuery(id+"F20.imprint","IMPRINT",FACE,{"disambiguationData":[TD([[makeQuery(id+"F20.imprint","IMPRINT",EDGE,{"derivedFrom":sQuery(id+"F20.wireOp",EDGE,"E52.10.0.0")}),1.0]])]});
            var Q15;
            Q15=makeQuery(id+"F20.imprint","IMPRINT",FACE,{"disambiguationData":[TD([[makeQuery(id+"F20.imprint","IMPRINT",EDGE,{"derivedFrom":sQuery(id+"F20.wireOp",EDGE,"E52.10.0.10")}),1.0]])]});
            var Q16;
            Q16=makeQuery(id+"F20.imprint","IMPRINT",FACE,{"disambiguationData":[TD([[makeQuery(id+"F20.imprint","IMPRINT",EDGE,{"derivedFrom":sQuery(id+"F20.wireOp",EDGE,"E52.10.0.4")}),1.0]])]});
            var Q17;
            Q17=makeQuery(id+"F20.imprint","IMPRINT",FACE,{"disambiguationData":[TD([[makeQuery(id+"F20.imprint","IMPRINT",EDGE,{"derivedFrom":sQuery(id+"F20.wireOp",EDGE,"E52.10.0.25")}),1.0]])]});
            var Q18;
            Q18=makeQuery(id+"F20.imprint","IMPRINT",FACE,{"disambiguationData":[TD([[makeQuery(id+"F20.imprint","IMPRINT",EDGE,{"derivedFrom":sQuery(id+"F20.wireOp",EDGE,"E52.10.0.19")}),1.0]])]});
            var Q19;
            Q19=makeQuery(id+"F20.imprint","IMPRINT",FACE,{"disambiguationData":[TD([[makeQuery(id+"F20.imprint","IMPRINT",EDGE,{"derivedFrom":sQuery(id+"F20.wireOp",EDGE,"E52.10.0.15")}),1.0]])]});
            var Q20;
            Q20=makeQuery(id+"F20.imprint","IMPRINT",FACE,{"disambiguationData":[TD([[makeQuery(id+"F20.imprint","IMPRINT",EDGE,{"derivedFrom":sQuery(id+"F20.wireOp",EDGE,"E52.10.0.6")}),1.0]])]});
            var Q21;
            Q21=makeQuery(id+"F20.imprint","IMPRINT",FACE,{"disambiguationData":[TD([[makeQuery(id+"F20.imprint","IMPRINT",EDGE,{"derivedFrom":sQuery(id+"F20.wireOp",EDGE,"E52.10.0.5")}),1.0]])]});
            var Q22;
            Q22=makeQuery(id+"F20.imprint","IMPRINT",FACE,{"disambiguationData":[TD([[makeQuery(id+"F20.imprint","IMPRINT",EDGE,{"derivedFrom":sQuery(id+"F20.wireOp",EDGE,"E52.9.0.14")}),1.0]])]});
            var Q23;
            Q23=makeQuery(id+"F20.imprint","IMPRINT",FACE,{"disambiguationData":[TD([[makeQuery(id+"F20.imprint","IMPRINT",EDGE,{"derivedFrom":sQuery(id+"F20.wireOp",EDGE,"E52.9.0.0")}),1.0]])]});
            extrude(context, id + "F28", {"entities" : qUnion([Q0, Q1, Q2, Q3, Q4, Q5, Q6, Q7, Q8, Q9, Q10, Q11, Q12, Q13, Q14, Q15, Q16, Q17, Q18, Q19, Q20, Q21, Q22, Q23]), "operationType" : NewBodyOperationType.REMOVE, "oppositeDirection" : true, "depth" : 50 * mm, "offsetDistance" : 25 * mm, "symmetric" : true});
        }
        {
            var Q0;
            Q0=makeQuery(id+"F20.imprint","IMPRINT",FACE,{"disambiguationData":[TD([[makeQuery(id+"F20.imprint","IMPRINT",EDGE,{"derivedFrom":sQuery(id+"F20.wireOp",EDGE,"E52.13.0.22")}),1.0]])]});
            var Q1;
            Q1=makeQuery(id+"F20.imprint","IMPRINT",FACE,{"disambiguationData":[TD([[makeQuery(id+"F20.imprint","IMPRINT",EDGE,{"derivedFrom":sQuery(id+"F20.wireOp",EDGE,"E52.13.0.23")}),1.0]])]});
            var Q2;
            Q2=makeQuery(id+"F20.imprint","IMPRINT",FACE,{"disambiguationData":[TD([[makeQuery(id+"F20.imprint","IMPRINT",EDGE,{"derivedFrom":sQuery(id+"F20.wireOp",EDGE,"E52.12.0.26")}),1.0]])]});
            var Q3;
            Q3=makeQuery(id+"F20.imprint","IMPRINT",FACE,{"disambiguationData":[TD([[makeQuery(id+"F20.imprint","IMPRINT",EDGE,{"derivedFrom":sQuery(id+"F20.wireOp",EDGE,"E52.12.0.22")}),1.0]])]});
            var Q4;
            Q4=makeQuery(id+"F20.imprint","IMPRINT",FACE,{"disambiguationData":[TD([[makeQuery(id+"F20.imprint","IMPRINT",EDGE,{"derivedFrom":sQuery(id+"F20.wireOp",EDGE,"E52.12.0.23")}),1.0]])]});
            var Q5;
            Q5=makeQuery(id+"F20.imprint","IMPRINT",FACE,{"disambiguationData":[TD([[makeQuery(id+"F20.imprint","IMPRINT",EDGE,{"derivedFrom":sQuery(id+"F20.wireOp",EDGE,"E52.11.0.26")}),1.0]])]});
            var Q6;
            Q6=makeQuery(id+"F20.imprint","IMPRINT",FACE,{"disambiguationData":[TD([[makeQuery(id+"F20.imprint","IMPRINT",EDGE,{"derivedFrom":sQuery(id+"F20.wireOp",EDGE,"E52.11.0.14")}),1.0]])]});
            var Q7;
            Q7=makeQuery(id+"F20.imprint","IMPRINT",FACE,{"disambiguationData":[TD([[makeQuery(id+"F20.imprint","IMPRINT",EDGE,{"derivedFrom":sQuery(id+"F20.wireOp",EDGE,"E52.12.0.15")}),1.0]])]});
            var Q8;
            Q8=makeQuery(id+"F20.imprint","IMPRINT",FACE,{"disambiguationData":[TD([[makeQuery(id+"F20.imprint","IMPRINT",EDGE,{"derivedFrom":sQuery(id+"F20.wireOp",EDGE,"E52.12.0.25")}),1.0]])]});
            var Q9;
            Q9=makeQuery(id+"F20.imprint","IMPRINT",FACE,{"disambiguationData":[TD([[makeQuery(id+"F20.imprint","IMPRINT",EDGE,{"derivedFrom":sQuery(id+"F20.wireOp",EDGE,"E52.12.0.19")}),1.0]])]});
            var Q10;
            Q10=makeQuery(id+"F20.imprint","IMPRINT",FACE,{"disambiguationData":[TD([[makeQuery(id+"F20.imprint","IMPRINT",EDGE,{"derivedFrom":sQuery(id+"F20.wireOp",EDGE,"E52.12.0.14")}),1.0]])]});
            var Q11;
            Q11=makeQuery(id+"F20.imprint","IMPRINT",FACE,{"disambiguationData":[TD([[makeQuery(id+"F20.imprint","IMPRINT",EDGE,{"derivedFrom":sQuery(id+"F20.wireOp",EDGE,"E52.13.0.15")}),1.0]])]});
            var Q12;
            Q12=makeQuery(id+"F20.imprint","IMPRINT",FACE,{"disambiguationData":[TD([[makeQuery(id+"F20.imprint","IMPRINT",EDGE,{"derivedFrom":sQuery(id+"F20.wireOp",EDGE,"E52.13.0.25")}),1.0]])]});
            var Q13;
            Q13=makeQuery(id+"F20.imprint","IMPRINT",FACE,{"disambiguationData":[TD([[makeQuery(id+"F20.imprint","IMPRINT",EDGE,{"derivedFrom":sQuery(id+"F20.wireOp",EDGE,"E52.13.0.19")}),1.0]])]});
            var Q14;
            Q14=makeQuery(id+"F20.imprint","IMPRINT",FACE,{"disambiguationData":[TD([[makeQuery(id+"F20.imprint","IMPRINT",EDGE,{"derivedFrom":sQuery(id+"F20.wireOp",EDGE,"E52.13.0.10")}),1.0]])]});
            var Q15;
            Q15=makeQuery(id+"F20.imprint","IMPRINT",FACE,{"disambiguationData":[TD([[makeQuery(id+"F20.imprint","IMPRINT",EDGE,{"derivedFrom":sQuery(id+"F20.wireOp",EDGE,"E52.13.0.4")}),1.0]])]});
            var Q16;
            Q16=makeQuery(id+"F20.imprint","IMPRINT",FACE,{"disambiguationData":[TD([[makeQuery(id+"F20.imprint","IMPRINT",EDGE,{"derivedFrom":sQuery(id+"F20.wireOp",EDGE,"E52.13.0.5")}),1.0]])]});
            var Q17;
            Q17=makeQuery(id+"F20.imprint","IMPRINT",FACE,{"disambiguationData":[TD([[makeQuery(id+"F20.imprint","IMPRINT",EDGE,{"derivedFrom":sQuery(id+"F20.wireOp",EDGE,"E52.13.0.6")}),1.0]])]});
            var Q18;
            Q18=makeQuery(id+"F20.imprint","IMPRINT",FACE,{"disambiguationData":[TD([[makeQuery(id+"F20.imprint","IMPRINT",EDGE,{"derivedFrom":sQuery(id+"F20.wireOp",EDGE,"E52.12.0.0")}),1.0]])]});
            var Q19;
            Q19=makeQuery(id+"F20.imprint","IMPRINT",FACE,{"disambiguationData":[TD([[makeQuery(id+"F20.imprint","IMPRINT",EDGE,{"derivedFrom":sQuery(id+"F20.wireOp",EDGE,"E52.12.0.4")}),1.0]])]});
            var Q20;
            Q20=makeQuery(id+"F20.imprint","IMPRINT",FACE,{"disambiguationData":[TD([[makeQuery(id+"F20.imprint","IMPRINT",EDGE,{"derivedFrom":sQuery(id+"F20.wireOp",EDGE,"E52.12.0.10")}),1.0]])]});
            var Q21;
            Q21=makeQuery(id+"F20.imprint","IMPRINT",FACE,{"disambiguationData":[TD([[makeQuery(id+"F20.imprint","IMPRINT",EDGE,{"derivedFrom":sQuery(id+"F20.wireOp",EDGE,"E52.12.0.6")}),1.0]])]});
            var Q22;
            Q22=makeQuery(id+"F20.imprint","IMPRINT",FACE,{"disambiguationData":[TD([[makeQuery(id+"F20.imprint","IMPRINT",EDGE,{"derivedFrom":sQuery(id+"F20.wireOp",EDGE,"E52.12.0.5")}),1.0]])]});
            var Q23;
            Q23=makeQuery(id+"F20.imprint","IMPRINT",FACE,{"disambiguationData":[TD([[makeQuery(id+"F20.imprint","IMPRINT",EDGE,{"derivedFrom":sQuery(id+"F20.wireOp",EDGE,"E52.11.0.0")}),1.0]])]});
            extrude(context, id + "F29", {"entities" : qUnion([Q0, Q1, Q2, Q3, Q4, Q5, Q6, Q7, Q8, Q9, Q10, Q11, Q12, Q13, Q14, Q15, Q16, Q17, Q18, Q19, Q20, Q21, Q22, Q23]), "operationType" : NewBodyOperationType.REMOVE, "oppositeDirection" : true, "depth" : 50 * mm, "offsetDistance" : 25 * mm, "symmetric" : true});
        }
        {
            var Q0;
            Q0=makeQuery(id+"F20.imprint","IMPRINT",FACE,{"disambiguationData":[TD([[makeQuery(id+"F20.imprint","IMPRINT",EDGE,{"derivedFrom":sQuery(id+"F20.wireOp",EDGE,"E52.15.0.22")}),1.0]])]});
            var Q1;
            Q1=makeQuery(id+"F20.imprint","IMPRINT",FACE,{"disambiguationData":[TD([[makeQuery(id+"F20.imprint","IMPRINT",EDGE,{"derivedFrom":sQuery(id+"F20.wireOp",EDGE,"E52.15.0.23")}),1.0]])]});
            var Q2;
            Q2=makeQuery(id+"F20.imprint","IMPRINT",FACE,{"disambiguationData":[TD([[makeQuery(id+"F20.imprint","IMPRINT",EDGE,{"derivedFrom":sQuery(id+"F20.wireOp",EDGE,"E52.14.0.26")}),1.0]])]});
            var Q3;
            Q3=makeQuery(id+"F20.imprint","IMPRINT",FACE,{"disambiguationData":[TD([[makeQuery(id+"F20.imprint","IMPRINT",EDGE,{"derivedFrom":sQuery(id+"F20.wireOp",EDGE,"E52.14.0.22")}),1.0]])]});
            var Q4;
            Q4=makeQuery(id+"F20.imprint","IMPRINT",FACE,{"disambiguationData":[TD([[makeQuery(id+"F20.imprint","IMPRINT",EDGE,{"derivedFrom":sQuery(id+"F20.wireOp",EDGE,"E52.14.0.23")}),1.0]])]});
            var Q5;
            Q5=makeQuery(id+"F20.imprint","IMPRINT",FACE,{"disambiguationData":[TD([[makeQuery(id+"F20.imprint","IMPRINT",EDGE,{"derivedFrom":sQuery(id+"F20.wireOp",EDGE,"E52.13.0.26")}),1.0]])]});
            var Q6;
            Q6=makeQuery(id+"F20.imprint","IMPRINT",FACE,{"disambiguationData":[TD([[makeQuery(id+"F20.imprint","IMPRINT",EDGE,{"derivedFrom":sQuery(id+"F20.wireOp",EDGE,"E52.13.0.14")}),1.0]])]});
            var Q7;
            Q7=makeQuery(id+"F20.imprint","IMPRINT",FACE,{"disambiguationData":[TD([[makeQuery(id+"F20.imprint","IMPRINT",EDGE,{"derivedFrom":sQuery(id+"F20.wireOp",EDGE,"E52.14.0.15")}),1.0]])]});
            var Q8;
            Q8=makeQuery(id+"F20.imprint","IMPRINT",FACE,{"disambiguationData":[TD([[makeQuery(id+"F20.imprint","IMPRINT",EDGE,{"derivedFrom":sQuery(id+"F20.wireOp",EDGE,"E52.14.0.25")}),1.0]])]});
            var Q9;
            Q9=makeQuery(id+"F20.imprint","IMPRINT",FACE,{"disambiguationData":[TD([[makeQuery(id+"F20.imprint","IMPRINT",EDGE,{"derivedFrom":sQuery(id+"F20.wireOp",EDGE,"E52.14.0.19")}),1.0]])]});
            var Q10;
            Q10=makeQuery(id+"F20.imprint","IMPRINT",FACE,{"disambiguationData":[TD([[makeQuery(id+"F20.imprint","IMPRINT",EDGE,{"derivedFrom":sQuery(id+"F20.wireOp",EDGE,"E52.14.0.14")}),1.0]])]});
            var Q11;
            Q11=makeQuery(id+"F20.imprint","IMPRINT",FACE,{"disambiguationData":[TD([[makeQuery(id+"F20.imprint","IMPRINT",EDGE,{"derivedFrom":sQuery(id+"F20.wireOp",EDGE,"E52.15.0.15")}),1.0]])]});
            var Q12;
            Q12=makeQuery(id+"F20.imprint","IMPRINT",FACE,{"disambiguationData":[TD([[makeQuery(id+"F20.imprint","IMPRINT",EDGE,{"derivedFrom":sQuery(id+"F20.wireOp",EDGE,"E52.15.0.25")}),1.0]])]});
            var Q13;
            Q13=makeQuery(id+"F20.imprint","IMPRINT",FACE,{"disambiguationData":[TD([[makeQuery(id+"F20.imprint","IMPRINT",EDGE,{"derivedFrom":sQuery(id+"F20.wireOp",EDGE,"E52.15.0.19")}),1.0]])]});
            var Q14;
            Q14=makeQuery(id+"F20.imprint","IMPRINT",FACE,{"disambiguationData":[TD([[makeQuery(id+"F20.imprint","IMPRINT",EDGE,{"derivedFrom":sQuery(id+"F20.wireOp",EDGE,"E52.15.0.10")}),1.0]])]});
            var Q15;
            Q15=makeQuery(id+"F20.imprint","IMPRINT",FACE,{"disambiguationData":[TD([[makeQuery(id+"F20.imprint","IMPRINT",EDGE,{"derivedFrom":sQuery(id+"F20.wireOp",EDGE,"E52.15.0.4")}),1.0]])]});
            var Q16;
            Q16=makeQuery(id+"F20.imprint","IMPRINT",FACE,{"disambiguationData":[TD([[makeQuery(id+"F20.imprint","IMPRINT",EDGE,{"derivedFrom":sQuery(id+"F20.wireOp",EDGE,"E52.15.0.5")}),1.0]])]});
            var Q17;
            Q17=makeQuery(id+"F20.imprint","IMPRINT",FACE,{"disambiguationData":[TD([[makeQuery(id+"F20.imprint","IMPRINT",EDGE,{"derivedFrom":sQuery(id+"F20.wireOp",EDGE,"E52.15.0.6")}),1.0]])]});
            var Q18;
            Q18=makeQuery(id+"F20.imprint","IMPRINT",FACE,{"disambiguationData":[TD([[makeQuery(id+"F20.imprint","IMPRINT",EDGE,{"derivedFrom":sQuery(id+"F20.wireOp",EDGE,"E52.14.0.0")}),1.0]])]});
            var Q19;
            Q19=makeQuery(id+"F20.imprint","IMPRINT",FACE,{"disambiguationData":[TD([[makeQuery(id+"F20.imprint","IMPRINT",EDGE,{"derivedFrom":sQuery(id+"F20.wireOp",EDGE,"E52.14.0.4")}),1.0]])]});
            var Q20;
            Q20=makeQuery(id+"F20.imprint","IMPRINT",FACE,{"disambiguationData":[TD([[makeQuery(id+"F20.imprint","IMPRINT",EDGE,{"derivedFrom":sQuery(id+"F20.wireOp",EDGE,"E52.14.0.10")}),1.0]])]});
            var Q21;
            Q21=makeQuery(id+"F20.imprint","IMPRINT",FACE,{"disambiguationData":[TD([[makeQuery(id+"F20.imprint","IMPRINT",EDGE,{"derivedFrom":sQuery(id+"F20.wireOp",EDGE,"E52.14.0.6")}),1.0]])]});
            var Q22;
            Q22=makeQuery(id+"F20.imprint","IMPRINT",FACE,{"disambiguationData":[TD([[makeQuery(id+"F20.imprint","IMPRINT",EDGE,{"derivedFrom":sQuery(id+"F20.wireOp",EDGE,"E52.14.0.5")}),1.0]])]});
            var Q23;
            Q23=makeQuery(id+"F20.imprint","IMPRINT",FACE,{"disambiguationData":[TD([[makeQuery(id+"F20.imprint","IMPRINT",EDGE,{"derivedFrom":sQuery(id+"F20.wireOp",EDGE,"E52.13.0.0")}),1.0]])]});
            extrude(context, id + "F30", {"entities" : qUnion([Q0, Q1, Q2, Q3, Q4, Q5, Q6, Q7, Q8, Q9, Q10, Q11, Q12, Q13, Q14, Q15, Q16, Q17, Q18, Q19, Q20, Q21, Q22, Q23]), "operationType" : NewBodyOperationType.REMOVE, "oppositeDirection" : true, "depth" : 50 * mm, "offsetDistance" : 25 * mm, "symmetric" : true});
        }
        {
            var Q0;
            Q0=makeQuery(id+"F20.imprint","IMPRINT",FACE,{"disambiguationData":[TD([[makeQuery(id+"F20.imprint","IMPRINT",EDGE,{"derivedFrom":sQuery(id+"F20.wireOp",EDGE,"E52.15.0.26")}),1.0]])]});
            var Q1;
            Q1=makeQuery(id+"F20.imprint","IMPRINT",FACE,{"disambiguationData":[TD([[makeQuery(id+"F20.imprint","IMPRINT",EDGE,{"derivedFrom":sQuery(id+"F20.wireOp",EDGE,"E52.16.0.23")}),1.0]])]});
            var Q2;
            Q2=makeQuery(id+"F20.imprint","IMPRINT",FACE,{"disambiguationData":[TD([[makeQuery(id+"F20.imprint","IMPRINT",EDGE,{"derivedFrom":sQuery(id+"F20.wireOp",EDGE,"E52.16.0.22")}),1.0]])]});
            var Q3;
            Q3=makeQuery(id+"F20.imprint","IMPRINT",FACE,{"disambiguationData":[TD([[makeQuery(id+"F20.imprint","IMPRINT",EDGE,{"derivedFrom":sQuery(id+"F20.wireOp",EDGE,"E52.16.0.26")}),1.0]])]});
            var Q4;
            Q4=makeQuery(id+"F20.imprint","IMPRINT",FACE,{"disambiguationData":[TD([[makeQuery(id+"F20.imprint","IMPRINT",EDGE,{"derivedFrom":sQuery(id+"F20.wireOp",EDGE,"E52.17.0.23")}),1.0]])]});
            var Q5;
            Q5=makeQuery(id+"F20.imprint","IMPRINT",FACE,{"disambiguationData":[TD([[makeQuery(id+"F20.imprint","IMPRINT",EDGE,{"derivedFrom":sQuery(id+"F20.wireOp",EDGE,"E52.17.0.22")}),1.0]])]});
            var Q6;
            Q6=makeQuery(id+"F20.imprint","IMPRINT",FACE,{"disambiguationData":[TD([[makeQuery(id+"F20.imprint","IMPRINT",EDGE,{"derivedFrom":sQuery(id+"F20.wireOp",EDGE,"E52.17.0.19")}),1.0]])]});
            var Q7;
            Q7=makeQuery(id+"F20.imprint","IMPRINT",FACE,{"disambiguationData":[TD([[makeQuery(id+"F20.imprint","IMPRINT",EDGE,{"derivedFrom":sQuery(id+"F20.wireOp",EDGE,"E52.17.0.15")}),1.0]])]});
            var Q8;
            Q8=makeQuery(id+"F20.imprint","IMPRINT",FACE,{"disambiguationData":[TD([[makeQuery(id+"F20.imprint","IMPRINT",EDGE,{"derivedFrom":sQuery(id+"F20.wireOp",EDGE,"E52.17.0.25")}),1.0]])]});
            var Q9;
            Q9=makeQuery(id+"F20.imprint","IMPRINT",FACE,{"disambiguationData":[TD([[makeQuery(id+"F20.imprint","IMPRINT",EDGE,{"derivedFrom":sQuery(id+"F20.wireOp",EDGE,"E52.16.0.14")}),1.0]])]});
            var Q10;
            Q10=makeQuery(id+"F20.imprint","IMPRINT",FACE,{"disambiguationData":[TD([[makeQuery(id+"F20.imprint","IMPRINT",EDGE,{"derivedFrom":sQuery(id+"F20.wireOp",EDGE,"E52.16.0.19")}),1.0]])]});
            var Q11;
            Q11=makeQuery(id+"F20.imprint","IMPRINT",FACE,{"disambiguationData":[TD([[makeQuery(id+"F20.imprint","IMPRINT",EDGE,{"derivedFrom":sQuery(id+"F20.wireOp",EDGE,"E52.16.0.25")}),1.0]])]});
            var Q12;
            Q12=makeQuery(id+"F20.imprint","IMPRINT",FACE,{"disambiguationData":[TD([[makeQuery(id+"F20.imprint","IMPRINT",EDGE,{"derivedFrom":sQuery(id+"F20.wireOp",EDGE,"E52.16.0.15")}),1.0]])]});
            var Q13;
            Q13=makeQuery(id+"F20.imprint","IMPRINT",FACE,{"disambiguationData":[TD([[makeQuery(id+"F20.imprint","IMPRINT",EDGE,{"derivedFrom":sQuery(id+"F20.wireOp",EDGE,"E52.15.0.14")}),1.0]])]});
            var Q14;
            Q14=makeQuery(id+"F20.imprint","IMPRINT",FACE,{"disambiguationData":[TD([[makeQuery(id+"F20.imprint","IMPRINT",EDGE,{"derivedFrom":sQuery(id+"F20.wireOp",EDGE,"E52.15.0.0")}),1.0]])]});
            var Q15;
            Q15=makeQuery(id+"F20.imprint","IMPRINT",FACE,{"disambiguationData":[TD([[makeQuery(id+"F20.imprint","IMPRINT",EDGE,{"derivedFrom":sQuery(id+"F20.wireOp",EDGE,"E52.16.0.5")}),1.0]])]});
            var Q16;
            Q16=makeQuery(id+"F20.imprint","IMPRINT",FACE,{"disambiguationData":[TD([[makeQuery(id+"F20.imprint","IMPRINT",EDGE,{"derivedFrom":sQuery(id+"F20.wireOp",EDGE,"E52.16.0.6")}),1.0]])]});
            var Q17;
            Q17=makeQuery(id+"F20.imprint","IMPRINT",FACE,{"disambiguationData":[TD([[makeQuery(id+"F20.imprint","IMPRINT",EDGE,{"derivedFrom":sQuery(id+"F20.wireOp",EDGE,"E52.16.0.10")}),1.0]])]});
            var Q18;
            Q18=makeQuery(id+"F20.imprint","IMPRINT",FACE,{"disambiguationData":[TD([[makeQuery(id+"F20.imprint","IMPRINT",EDGE,{"derivedFrom":sQuery(id+"F20.wireOp",EDGE,"E52.16.0.4")}),1.0]])]});
            var Q19;
            Q19=makeQuery(id+"F20.imprint","IMPRINT",FACE,{"disambiguationData":[TD([[makeQuery(id+"F20.imprint","IMPRINT",EDGE,{"derivedFrom":sQuery(id+"F20.wireOp",EDGE,"E52.16.0.0")}),1.0]])]});
            var Q20;
            Q20=makeQuery(id+"F20.imprint","IMPRINT",FACE,{"disambiguationData":[TD([[makeQuery(id+"F20.imprint","IMPRINT",EDGE,{"derivedFrom":sQuery(id+"F20.wireOp",EDGE,"E52.17.0.5")}),1.0]])]});
            var Q21;
            Q21=makeQuery(id+"F20.imprint","IMPRINT",FACE,{"disambiguationData":[TD([[makeQuery(id+"F20.imprint","IMPRINT",EDGE,{"derivedFrom":sQuery(id+"F20.wireOp",EDGE,"E52.17.0.6")}),1.0]])]});
            var Q22;
            Q22=makeQuery(id+"F20.imprint","IMPRINT",FACE,{"disambiguationData":[TD([[makeQuery(id+"F20.imprint","IMPRINT",EDGE,{"derivedFrom":sQuery(id+"F20.wireOp",EDGE,"E52.17.0.10")}),1.0]])]});
            var Q23;
            Q23=makeQuery(id+"F20.imprint","IMPRINT",FACE,{"disambiguationData":[TD([[makeQuery(id+"F20.imprint","IMPRINT",EDGE,{"derivedFrom":sQuery(id+"F20.wireOp",EDGE,"E52.17.0.4")}),1.0]])]});
            extrude(context, id + "F31", {"entities" : qUnion([Q0, Q1, Q2, Q3, Q4, Q5, Q6, Q7, Q8, Q9, Q10, Q11, Q12, Q13, Q14, Q15, Q16, Q17, Q18, Q19, Q20, Q21, Q22, Q23]), "operationType" : NewBodyOperationType.REMOVE, "oppositeDirection" : true, "depth" : 50 * mm, "offsetDistance" : 25 * mm, "symmetric" : true});
        }
        {
            var Q0;
            Q0=makeQuery(id+"F20.imprint","IMPRINT",FACE,{"disambiguationData":[TD([[makeQuery(id+"F20.imprint","IMPRINT",EDGE,{"derivedFrom":sQuery(id+"F20.wireOp",EDGE,"E52.18.0.19")}),1.0]])]});
            var Q1;
            Q1=makeQuery(id+"F20.imprint","IMPRINT",FACE,{"disambiguationData":[TD([[makeQuery(id+"F20.imprint","IMPRINT",EDGE,{"derivedFrom":sQuery(id+"F20.wireOp",EDGE,"E52.21.0.6")}),1.0]])]});
            var Q2;
            Q2=makeQuery(id+"F20.imprint","IMPRINT",FACE,{"disambiguationData":[TD([[makeQuery(id+"F20.imprint","IMPRINT",EDGE,{"derivedFrom":sQuery(id+"F20.wireOp",EDGE,"E52.19.0.26")}),1.0]])]});
            var Q3;
            Q3=makeQuery(id+"F20.imprint","IMPRINT",FACE,{"disambiguationData":[TD([[makeQuery(id+"F20.imprint","IMPRINT",EDGE,{"derivedFrom":sQuery(id+"F20.wireOp",EDGE,"E52.18.0.14")}),1.0]])]});
            var Q4;
            Q4=makeQuery(id+"F20.imprint","IMPRINT",FACE,{"disambiguationData":[TD([[makeQuery(id+"F20.imprint","IMPRINT",EDGE,{"derivedFrom":sQuery(id+"F20.wireOp",EDGE,"E52.21.0.4")}),1.0]])]});
            var Q5;
            Q5=makeQuery(id+"F20.imprint","IMPRINT",FACE,{"disambiguationData":[TD([[makeQuery(id+"F20.imprint","IMPRINT",EDGE,{"derivedFrom":sQuery(id+"F20.wireOp",EDGE,"E52.19.0.23")}),1.0]])]});
            var Q6;
            Q6=makeQuery(id+"F20.imprint","IMPRINT",FACE,{"disambiguationData":[TD([[makeQuery(id+"F20.imprint","IMPRINT",EDGE,{"derivedFrom":sQuery(id+"F20.wireOp",EDGE,"E52.18.0.15")}),1.0]])]});
            var Q7;
            Q7=makeQuery(id+"F20.imprint","IMPRINT",FACE,{"disambiguationData":[TD([[makeQuery(id+"F20.imprint","IMPRINT",EDGE,{"derivedFrom":sQuery(id+"F20.wireOp",EDGE,"E52.21.0.5")}),1.0]])]});
            var Q8;
            Q8=makeQuery(id+"F20.imprint","IMPRINT",FACE,{"disambiguationData":[TD([[makeQuery(id+"F20.imprint","IMPRINT",EDGE,{"derivedFrom":sQuery(id+"F20.wireOp",EDGE,"E52.19.0.25")}),1.0]])]});
            var Q9;
            Q9=makeQuery(id+"F20.imprint","IMPRINT",FACE,{"disambiguationData":[TD([[makeQuery(id+"F20.imprint","IMPRINT",EDGE,{"derivedFrom":sQuery(id+"F20.wireOp",EDGE,"E52.18.0.22")}),1.0]])]});
            var Q10;
            Q10=makeQuery(id+"F20.imprint","IMPRINT",FACE,{"disambiguationData":[TD([[makeQuery(id+"F20.imprint","IMPRINT",EDGE,{"derivedFrom":sQuery(id+"F20.wireOp",EDGE,"E52.21.0.10")}),1.0]])]});
            var Q11;
            Q11=makeQuery(id+"F20.imprint","IMPRINT",FACE,{"disambiguationData":[TD([[makeQuery(id+"F20.imprint","IMPRINT",EDGE,{"derivedFrom":sQuery(id+"F20.wireOp",EDGE,"E52.20.0.0")}),1.0]])]});
            var Q12;
            Q12=makeQuery(id+"F20.imprint","IMPRINT",FACE,{"disambiguationData":[TD([[makeQuery(id+"F20.imprint","IMPRINT",EDGE,{"derivedFrom":sQuery(id+"F20.wireOp",EDGE,"E52.18.0.23")}),1.0]])]});
            var Q13;
            Q13=makeQuery(id+"F20.imprint","IMPRINT",FACE,{"disambiguationData":[TD([[makeQuery(id+"F20.imprint","IMPRINT",EDGE,{"derivedFrom":sQuery(id+"F20.wireOp",EDGE,"E52.17.0.14")}),1.0]])]});
            var Q14;
            Q14=makeQuery(id+"F20.imprint","IMPRINT",FACE,{"disambiguationData":[TD([[makeQuery(id+"F20.imprint","IMPRINT",EDGE,{"derivedFrom":sQuery(id+"F20.wireOp",EDGE,"E52.20.0.4")}),1.0]])]});
            var Q15;
            Q15=makeQuery(id+"F20.imprint","IMPRINT",FACE,{"disambiguationData":[TD([[makeQuery(id+"F20.imprint","IMPRINT",EDGE,{"derivedFrom":sQuery(id+"F20.wireOp",EDGE,"E52.18.0.25")}),1.0]])]});
            var Q16;
            Q16=makeQuery(id+"F20.imprint","IMPRINT",FACE,{"disambiguationData":[TD([[makeQuery(id+"F20.imprint","IMPRINT",EDGE,{"derivedFrom":sQuery(id+"F20.wireOp",EDGE,"E52.21.0.15")}),1.0]])]});
            var Q17;
            Q17=makeQuery(id+"F20.imprint","IMPRINT",FACE,{"disambiguationData":[TD([[makeQuery(id+"F20.imprint","IMPRINT",EDGE,{"derivedFrom":sQuery(id+"F20.wireOp",EDGE,"E52.20.0.5")}),1.0]])]});
            var Q18;
            Q18=makeQuery(id+"F20.imprint","IMPRINT",FACE,{"disambiguationData":[TD([[makeQuery(id+"F20.imprint","IMPRINT",EDGE,{"derivedFrom":sQuery(id+"F20.wireOp",EDGE,"E52.18.0.26")}),1.0]])]});
            var Q19;
            Q19=makeQuery(id+"F20.imprint","IMPRINT",FACE,{"disambiguationData":[TD([[makeQuery(id+"F20.imprint","IMPRINT",EDGE,{"derivedFrom":sQuery(id+"F20.wireOp",EDGE,"E52.21.0.19")}),1.0]])]});
            var Q20;
            Q20=makeQuery(id+"F20.imprint","IMPRINT",FACE,{"disambiguationData":[TD([[makeQuery(id+"F20.imprint","IMPRINT",EDGE,{"derivedFrom":sQuery(id+"F20.wireOp",EDGE,"E52.20.0.6")}),1.0]])]});
            var Q21;
            Q21=makeQuery(id+"F20.imprint","IMPRINT",FACE,{"disambiguationData":[TD([[makeQuery(id+"F20.imprint","IMPRINT",EDGE,{"derivedFrom":sQuery(id+"F20.wireOp",EDGE,"E52.19.0.0")}),1.0]])]});
            var Q22;
            Q22=makeQuery(id+"F20.imprint","IMPRINT",FACE,{"disambiguationData":[TD([[makeQuery(id+"F20.imprint","IMPRINT",EDGE,{"derivedFrom":sQuery(id+"F20.wireOp",EDGE,"E52.21.0.22")}),1.0]])]});
            var Q23;
            Q23=makeQuery(id+"F20.imprint","IMPRINT",FACE,{"disambiguationData":[TD([[makeQuery(id+"F20.imprint","IMPRINT",EDGE,{"derivedFrom":sQuery(id+"F20.wireOp",EDGE,"E52.20.0.10")}),1.0]])]});
            var Q24;
            Q24=makeQuery(id+"F20.imprint","IMPRINT",FACE,{"disambiguationData":[TD([[makeQuery(id+"F20.imprint","IMPRINT",EDGE,{"derivedFrom":sQuery(id+"F20.wireOp",EDGE,"E52.19.0.4")}),1.0]])]});
            var Q25;
            Q25=makeQuery(id+"F20.imprint","IMPRINT",FACE,{"disambiguationData":[TD([[makeQuery(id+"F20.imprint","IMPRINT",EDGE,{"derivedFrom":sQuery(id+"F20.wireOp",EDGE,"E52.21.0.23")}),1.0]])]});
            var Q26;
            Q26=makeQuery(id+"F20.imprint","IMPRINT",FACE,{"disambiguationData":[TD([[makeQuery(id+"F20.imprint","IMPRINT",EDGE,{"derivedFrom":sQuery(id+"F20.wireOp",EDGE,"E52.20.0.14")}),1.0]])]});
            var Q27;
            Q27=makeQuery(id+"F20.imprint","IMPRINT",FACE,{"disambiguationData":[TD([[makeQuery(id+"F20.imprint","IMPRINT",EDGE,{"derivedFrom":sQuery(id+"F20.wireOp",EDGE,"E52.21.0.25")}),1.0]])]});
            var Q28;
            Q28=makeQuery(id+"F20.imprint","IMPRINT",FACE,{"disambiguationData":[TD([[makeQuery(id+"F20.imprint","IMPRINT",EDGE,{"derivedFrom":sQuery(id+"F20.wireOp",EDGE,"E52.20.0.15")}),1.0]])]});
            var Q29;
            Q29=makeQuery(id+"F20.imprint","IMPRINT",FACE,{"disambiguationData":[TD([[makeQuery(id+"F20.imprint","IMPRINT",EDGE,{"derivedFrom":sQuery(id+"F20.wireOp",EDGE,"E52.19.0.5")}),1.0]])]});
            var Q30;
            Q30=makeQuery(id+"F20.imprint","IMPRINT",FACE,{"disambiguationData":[TD([[makeQuery(id+"F20.imprint","IMPRINT",EDGE,{"derivedFrom":sQuery(id+"F20.wireOp",EDGE,"E52.20.0.19")}),1.0]])]});
            var Q31;
            Q31=makeQuery(id+"F20.imprint","IMPRINT",FACE,{"disambiguationData":[TD([[makeQuery(id+"F20.imprint","IMPRINT",EDGE,{"derivedFrom":sQuery(id+"F20.wireOp",EDGE,"E52.19.0.6")}),1.0]])]});
            var Q32;
            Q32=makeQuery(id+"F20.imprint","IMPRINT",FACE,{"disambiguationData":[TD([[makeQuery(id+"F20.imprint","IMPRINT",EDGE,{"derivedFrom":sQuery(id+"F20.wireOp",EDGE,"E52.17.0.26")}),1.0]])]});
            var Q33;
            Q33=makeQuery(id+"F20.imprint","IMPRINT",FACE,{"disambiguationData":[TD([[makeQuery(id+"F20.imprint","IMPRINT",EDGE,{"derivedFrom":sQuery(id+"F20.wireOp",EDGE,"E52.20.0.22")}),1.0]])]});
            var Q34;
            Q34=makeQuery(id+"F20.imprint","IMPRINT",FACE,{"disambiguationData":[TD([[makeQuery(id+"F20.imprint","IMPRINT",EDGE,{"derivedFrom":sQuery(id+"F20.wireOp",EDGE,"E52.19.0.10")}),1.0]])]});
            var Q35;
            Q35=makeQuery(id+"F20.imprint","IMPRINT",FACE,{"disambiguationData":[TD([[makeQuery(id+"F20.imprint","IMPRINT",EDGE,{"derivedFrom":sQuery(id+"F20.wireOp",EDGE,"E52.18.0.0")}),1.0]])]});
            var Q36;
            Q36=makeQuery(id+"F20.imprint","IMPRINT",FACE,{"disambiguationData":[TD([[makeQuery(id+"F20.imprint","IMPRINT",EDGE,{"derivedFrom":sQuery(id+"F20.wireOp",EDGE,"E52.20.0.23")}),1.0]])]});
            var Q37;
            Q37=makeQuery(id+"F20.imprint","IMPRINT",FACE,{"disambiguationData":[TD([[makeQuery(id+"F20.imprint","IMPRINT",EDGE,{"derivedFrom":sQuery(id+"F20.wireOp",EDGE,"E52.19.0.14")}),1.0]])]});
            var Q38;
            Q38=makeQuery(id+"F20.imprint","IMPRINT",FACE,{"disambiguationData":[TD([[makeQuery(id+"F20.imprint","IMPRINT",EDGE,{"derivedFrom":sQuery(id+"F20.wireOp",EDGE,"E52.18.0.4")}),1.0]])]});
            var Q39;
            Q39=makeQuery(id+"F20.imprint","IMPRINT",FACE,{"disambiguationData":[TD([[makeQuery(id+"F20.imprint","IMPRINT",EDGE,{"derivedFrom":sQuery(id+"F20.wireOp",EDGE,"E52.20.0.25")}),1.0]])]});
            var Q40;
            Q40=makeQuery(id+"F20.imprint","IMPRINT",FACE,{"disambiguationData":[TD([[makeQuery(id+"F20.imprint","IMPRINT",EDGE,{"derivedFrom":sQuery(id+"F20.wireOp",EDGE,"E52.19.0.15")}),1.0]])]});
            var Q41;
            Q41=makeQuery(id+"F20.imprint","IMPRINT",FACE,{"disambiguationData":[TD([[makeQuery(id+"F20.imprint","IMPRINT",EDGE,{"derivedFrom":sQuery(id+"F20.wireOp",EDGE,"E52.18.0.5")}),1.0]])]});
            var Q42;
            Q42=makeQuery(id+"F20.imprint","IMPRINT",FACE,{"disambiguationData":[TD([[makeQuery(id+"F20.imprint","IMPRINT",EDGE,{"derivedFrom":sQuery(id+"F20.wireOp",EDGE,"E52.20.0.26")}),1.0]])]});
            var Q43;
            Q43=makeQuery(id+"F20.imprint","IMPRINT",FACE,{"disambiguationData":[TD([[makeQuery(id+"F20.imprint","IMPRINT",EDGE,{"derivedFrom":sQuery(id+"F20.wireOp",EDGE,"E52.19.0.19")}),1.0]])]});
            var Q44;
            Q44=makeQuery(id+"F20.imprint","IMPRINT",FACE,{"disambiguationData":[TD([[makeQuery(id+"F20.imprint","IMPRINT",EDGE,{"derivedFrom":sQuery(id+"F20.wireOp",EDGE,"E52.18.0.6")}),1.0]])]});
            var Q45;
            Q45=makeQuery(id+"F20.imprint","IMPRINT",FACE,{"disambiguationData":[TD([[makeQuery(id+"F20.imprint","IMPRINT",EDGE,{"derivedFrom":sQuery(id+"F20.wireOp",EDGE,"E52.17.0.0")}),1.0]])]});
            var Q46;
            Q46=makeQuery(id+"F20.imprint","IMPRINT",FACE,{"disambiguationData":[TD([[makeQuery(id+"F20.imprint","IMPRINT",EDGE,{"derivedFrom":sQuery(id+"F20.wireOp",EDGE,"E52.19.0.22")}),1.0]])]});
            var Q47;
            Q47=makeQuery(id+"F20.imprint","IMPRINT",FACE,{"disambiguationData":[TD([[makeQuery(id+"F20.imprint","IMPRINT",EDGE,{"derivedFrom":sQuery(id+"F20.wireOp",EDGE,"E52.18.0.10")}),1.0]])]});
            extrude(context, id + "F32", {"entities" : qUnion([Q0, Q1, Q2, Q3, Q4, Q5, Q6, Q7, Q8, Q9, Q10, Q11, Q12, Q13, Q14, Q15, Q16, Q17, Q18, Q19, Q20, Q21, Q22, Q23, Q24, Q25, Q26, Q27, Q28, Q29, Q30, Q31, Q32, Q33, Q34, Q35, Q36, Q37, Q38, Q39, Q40, Q41, Q42, Q43, Q44, Q45, Q46, Q47]), "operationType" : NewBodyOperationType.REMOVE, "oppositeDirection" : true, "depth" : 56 * mm, "offsetDistance" : 25 * mm, "symmetric" : true});
        }
        {
            var Q0;
            Q0=makeQuery(id+"F20.imprint","IMPRINT",FACE,{"disambiguationData":[TD([[makeQuery(id+"F20.imprint","IMPRINT",EDGE,{"derivedFrom":sQuery(id+"F20.wireOp",EDGE,"E52.21.0.26")}),1.0]])]});
            var Q1;
            Q1=makeQuery(id+"F20.imprint","IMPRINT",FACE,{"disambiguationData":[TD([[makeQuery(id+"F20.imprint","IMPRINT",EDGE,{"derivedFrom":sQuery(id+"F20.wireOp",EDGE,"E52.21.0.14")}),1.0]])]});
            var Q2;
            Q2=makeQuery(id+"F20.imprint","IMPRINT",FACE,{"disambiguationData":[TD([[makeQuery(id+"F20.imprint","IMPRINT",EDGE,{"derivedFrom":sQuery(id+"F20.wireOp",EDGE,"E52.21.0.0")}),1.0]])]});
            var Q3;
            Q3=makeQuery(id+"F20.imprint","IMPRINT",FACE,{"disambiguationData":[TD([[makeQuery(id+"F20.imprint","IMPRINT",EDGE,{"derivedFrom":sQuery(id+"F20.wireOp",EDGE,"E52.22.0.5")}),1.0]])]});
            var Q4;
            Q4=makeQuery(id+"F20.imprint","IMPRINT",FACE,{"disambiguationData":[TD([[makeQuery(id+"F20.imprint","IMPRINT",EDGE,{"derivedFrom":sQuery(id+"F20.wireOp",EDGE,"E52.22.0.6")}),1.0]])]});
            var Q5;
            Q5=makeQuery(id+"F20.imprint","IMPRINT",FACE,{"disambiguationData":[TD([[makeQuery(id+"F20.imprint","IMPRINT",EDGE,{"derivedFrom":sQuery(id+"F20.wireOp",EDGE,"E52.22.0.15")}),1.0]])]});
            var Q6;
            Q6=makeQuery(id+"F20.imprint","IMPRINT",FACE,{"disambiguationData":[TD([[makeQuery(id+"F20.imprint","IMPRINT",EDGE,{"derivedFrom":sQuery(id+"F20.wireOp",EDGE,"E52.22.0.23")}),1.0]])]});
            var Q7;
            Q7=makeQuery(id+"F20.imprint","IMPRINT",FACE,{"disambiguationData":[TD([[makeQuery(id+"F20.imprint","IMPRINT",EDGE,{"derivedFrom":sQuery(id+"F20.wireOp",EDGE,"E52.22.0.22")}),1.0]])]});
            var Q8;
            Q8=makeQuery(id+"F20.imprint","IMPRINT",FACE,{"disambiguationData":[TD([[makeQuery(id+"F20.imprint","IMPRINT",EDGE,{"derivedFrom":sQuery(id+"F20.wireOp",EDGE,"E52.22.0.19")}),1.0]])]});
            var Q9;
            Q9=makeQuery(id+"F20.imprint","IMPRINT",FACE,{"disambiguationData":[TD([[makeQuery(id+"F20.imprint","IMPRINT",EDGE,{"derivedFrom":sQuery(id+"F20.wireOp",EDGE,"E52.22.0.25")}),1.0]])]});
            var Q10;
            Q10=makeQuery(id+"F20.imprint","IMPRINT",FACE,{"disambiguationData":[TD([[makeQuery(id+"F20.imprint","IMPRINT",EDGE,{"derivedFrom":sQuery(id+"F20.wireOp",EDGE,"E52.22.0.10")}),1.0]])]});
            var Q11;
            Q11=makeQuery(id+"F20.imprint","IMPRINT",FACE,{"disambiguationData":[TD([[makeQuery(id+"F20.imprint","IMPRINT",EDGE,{"derivedFrom":sQuery(id+"F20.wireOp",EDGE,"E52.22.0.4")}),1.0]])]});
            var Q12;
            Q12=makeQuery(id+"F20.imprint","IMPRINT",FACE,{"disambiguationData":[TD([[makeQuery(id+"F20.imprint","IMPRINT",EDGE,{"derivedFrom":sQuery(id+"F20.wireOp",EDGE,"E52.22.0.14")}),1.0]])]});
            var Q13;
            Q13=makeQuery(id+"F20.imprint","IMPRINT",FACE,{"disambiguationData":[TD([[makeQuery(id+"F20.imprint","IMPRINT",EDGE,{"derivedFrom":sQuery(id+"F20.wireOp",EDGE,"E52.22.0.0")}),1.0]])]});
            var Q14;
            Q14=makeQuery(id+"F20.imprint","IMPRINT",FACE,{"disambiguationData":[TD([[makeQuery(id+"F20.imprint","IMPRINT",EDGE,{"derivedFrom":sQuery(id+"F20.wireOp",EDGE,"E52.22.0.26")}),1.0]])]});
            var Q15;
            Q15=makeQuery(id+"F20.imprint","IMPRINT",FACE,{"disambiguationData":[TD([[makeQuery(id+"F20.imprint","IMPRINT",EDGE,{"derivedFrom":sQuery(id+"F20.wireOp",EDGE,"E52.23.0.23")}),1.0]])]});
            var Q16;
            Q16=makeQuery(id+"F20.imprint","IMPRINT",FACE,{"disambiguationData":[TD([[makeQuery(id+"F20.imprint","IMPRINT",EDGE,{"derivedFrom":sQuery(id+"F20.wireOp",EDGE,"E52.23.0.15")}),1.0]])]});
            var Q17;
            Q17=makeQuery(id+"F20.imprint","IMPRINT",FACE,{"disambiguationData":[TD([[makeQuery(id+"F20.imprint","IMPRINT",EDGE,{"derivedFrom":sQuery(id+"F20.wireOp",EDGE,"E52.23.0.6")}),1.0]])]});
            var Q18;
            Q18=makeQuery(id+"F20.imprint","IMPRINT",FACE,{"disambiguationData":[TD([[makeQuery(id+"F20.imprint","IMPRINT",EDGE,{"derivedFrom":sQuery(id+"F20.wireOp",EDGE,"E52.23.0.5")}),1.0]])]});
            var Q19;
            Q19=makeQuery(id+"F20.imprint","IMPRINT",FACE,{"disambiguationData":[TD([[makeQuery(id+"F20.imprint","IMPRINT",EDGE,{"derivedFrom":sQuery(id+"F20.wireOp",EDGE,"E52.23.0.25")}),1.0]])]});
            var Q20;
            Q20=makeQuery(id+"F20.imprint","IMPRINT",FACE,{"disambiguationData":[TD([[makeQuery(id+"F20.imprint","IMPRINT",EDGE,{"derivedFrom":sQuery(id+"F20.wireOp",EDGE,"E52.23.0.10")}),1.0]])]});
            var Q21;
            Q21=makeQuery(id+"F20.imprint","IMPRINT",FACE,{"disambiguationData":[TD([[makeQuery(id+"F20.imprint","IMPRINT",EDGE,{"derivedFrom":sQuery(id+"F20.wireOp",EDGE,"E52.23.0.4")}),1.0]])]});
            var Q22;
            Q22=makeQuery(id+"F20.imprint","IMPRINT",FACE,{"disambiguationData":[TD([[makeQuery(id+"F20.imprint","IMPRINT",EDGE,{"derivedFrom":sQuery(id+"F20.wireOp",EDGE,"E52.23.0.19")}),1.0]])]});
            var Q23;
            Q23=makeQuery(id+"F20.imprint","IMPRINT",FACE,{"disambiguationData":[TD([[makeQuery(id+"F20.imprint","IMPRINT",EDGE,{"derivedFrom":sQuery(id+"F20.wireOp",EDGE,"E52.23.0.22")}),1.0]])]});
            var Q24;
            Q24=makeQuery(id+"F20.imprint","IMPRINT",FACE,{"disambiguationData":[TD([[makeQuery(id+"F20.imprint","IMPRINT",EDGE,{"derivedFrom":sQuery(id+"F20.wireOp",EDGE,"E52.23.0.14")}),1.0]])]});
            var Q25;
            Q25=makeQuery(id+"F20.imprint","IMPRINT",FACE,{"disambiguationData":[TD([[makeQuery(id+"F20.imprint","IMPRINT",EDGE,{"derivedFrom":sQuery(id+"F20.wireOp",EDGE,"E52.23.0.0")}),1.0]])]});
            var Q26;
            Q26=makeQuery(id+"F20.imprint","IMPRINT",FACE,{"disambiguationData":[TD([[makeQuery(id+"F20.imprint","IMPRINT",EDGE,{"derivedFrom":sQuery(id+"F20.wireOp",EDGE,"E52.23.0.26")}),1.0]])]});
            var Q27;
            Q27=makeQuery(id+"F20.imprint","IMPRINT",FACE,{"disambiguationData":[TD([[makeQuery(id+"F20.imprint","IMPRINT",EDGE,{"derivedFrom":sQuery(id+"F20.wireOp",EDGE,"E52.24.0.23")}),1.0]])]});
            var Q28;
            Q28=makeQuery(id+"F20.imprint","IMPRINT",FACE,{"disambiguationData":[TD([[makeQuery(id+"F20.imprint","IMPRINT",EDGE,{"derivedFrom":sQuery(id+"F20.wireOp",EDGE,"E52.24.0.15")}),1.0]])]});
            var Q29;
            Q29=makeQuery(id+"F20.imprint","IMPRINT",FACE,{"disambiguationData":[TD([[makeQuery(id+"F20.imprint","IMPRINT",EDGE,{"derivedFrom":sQuery(id+"F20.wireOp",EDGE,"E52.24.0.6")}),1.0]])]});
            var Q30;
            Q30=makeQuery(id+"F20.imprint","IMPRINT",FACE,{"disambiguationData":[TD([[makeQuery(id+"F20.imprint","IMPRINT",EDGE,{"derivedFrom":sQuery(id+"F20.wireOp",EDGE,"E52.24.0.5")}),1.0]])]});
            var Q31;
            Q31=makeQuery(id+"F20.imprint","IMPRINT",FACE,{"disambiguationData":[TD([[makeQuery(id+"F20.imprint","IMPRINT",EDGE,{"derivedFrom":sQuery(id+"F20.wireOp",EDGE,"E52.24.0.25")}),1.0]])]});
            var Q32;
            Q32=makeQuery(id+"F20.imprint","IMPRINT",FACE,{"disambiguationData":[TD([[makeQuery(id+"F20.imprint","IMPRINT",EDGE,{"derivedFrom":sQuery(id+"F20.wireOp",EDGE,"E52.24.0.19")}),1.0]])]});
            var Q33;
            Q33=makeQuery(id+"F20.imprint","IMPRINT",FACE,{"disambiguationData":[TD([[makeQuery(id+"F20.imprint","IMPRINT",EDGE,{"derivedFrom":sQuery(id+"F20.wireOp",EDGE,"E52.24.0.22")}),1.0]])]});
            var Q34;
            Q34=makeQuery(id+"F20.imprint","IMPRINT",FACE,{"disambiguationData":[TD([[makeQuery(id+"F20.imprint","IMPRINT",EDGE,{"derivedFrom":sQuery(id+"F20.wireOp",EDGE,"E52.24.0.10")}),1.0]])]});
            var Q35;
            Q35=makeQuery(id+"F20.imprint","IMPRINT",FACE,{"disambiguationData":[TD([[makeQuery(id+"F20.imprint","IMPRINT",EDGE,{"derivedFrom":sQuery(id+"F20.wireOp",EDGE,"E52.24.0.4")}),1.0]])]});
            var Q36;
            Q36=makeQuery(id+"F20.imprint","IMPRINT",FACE,{"disambiguationData":[TD([[makeQuery(id+"F20.imprint","IMPRINT",EDGE,{"derivedFrom":sQuery(id+"F20.wireOp",EDGE,"E52.24.0.14")}),1.0]])]});
            var Q37;
            Q37=makeQuery(id+"F20.imprint","IMPRINT",FACE,{"disambiguationData":[TD([[makeQuery(id+"F20.imprint","IMPRINT",EDGE,{"derivedFrom":sQuery(id+"F20.wireOp",EDGE,"E52.24.0.0")}),1.0]])]});
            var Q38;
            Q38=makeQuery(id+"F20.imprint","IMPRINT",FACE,{"disambiguationData":[TD([[makeQuery(id+"F20.imprint","IMPRINT",EDGE,{"derivedFrom":sQuery(id+"F20.wireOp",EDGE,"E52.24.0.26")}),1.0]])]});
            var Q39;
            Q39=makeQuery(id+"F20.imprint","IMPRINT",FACE,{"disambiguationData":[TD([[makeQuery(id+"F20.imprint","IMPRINT",EDGE,{"derivedFrom":sQuery(id+"F20.wireOp",EDGE,"E52.25.0.23")}),1.0]])]});
            var Q40;
            Q40=makeQuery(id+"F20.imprint","IMPRINT",FACE,{"disambiguationData":[TD([[makeQuery(id+"F20.imprint","IMPRINT",EDGE,{"derivedFrom":sQuery(id+"F20.wireOp",EDGE,"E52.25.0.15")}),1.0]])]});
            var Q41;
            Q41=makeQuery(id+"F20.imprint","IMPRINT",FACE,{"disambiguationData":[TD([[makeQuery(id+"F20.imprint","IMPRINT",EDGE,{"derivedFrom":sQuery(id+"F20.wireOp",EDGE,"E52.25.0.6")}),1.0]])]});
            var Q42;
            Q42=makeQuery(id+"F20.imprint","IMPRINT",FACE,{"disambiguationData":[TD([[makeQuery(id+"F20.imprint","IMPRINT",EDGE,{"derivedFrom":sQuery(id+"F20.wireOp",EDGE,"E52.25.0.5")}),1.0]])]});
            var Q43;
            Q43=makeQuery(id+"F20.imprint","IMPRINT",FACE,{"disambiguationData":[TD([[makeQuery(id+"F20.imprint","IMPRINT",EDGE,{"derivedFrom":sQuery(id+"F20.wireOp",EDGE,"E52.25.0.25")}),1.0]])]});
            var Q44;
            Q44=makeQuery(id+"F20.imprint","IMPRINT",FACE,{"disambiguationData":[TD([[makeQuery(id+"F20.imprint","IMPRINT",EDGE,{"derivedFrom":sQuery(id+"F20.wireOp",EDGE,"E52.25.0.10")}),1.0]])]});
            var Q45;
            Q45=makeQuery(id+"F20.imprint","IMPRINT",FACE,{"disambiguationData":[TD([[makeQuery(id+"F20.imprint","IMPRINT",EDGE,{"derivedFrom":sQuery(id+"F20.wireOp",EDGE,"E52.25.0.4")}),1.0]])]});
            var Q46;
            Q46=makeQuery(id+"F20.imprint","IMPRINT",FACE,{"disambiguationData":[TD([[makeQuery(id+"F20.imprint","IMPRINT",EDGE,{"derivedFrom":sQuery(id+"F20.wireOp",EDGE,"E52.25.0.22")}),1.0]])]});
            var Q47;
            Q47=makeQuery(id+"F20.imprint","IMPRINT",FACE,{"disambiguationData":[TD([[makeQuery(id+"F20.imprint","IMPRINT",EDGE,{"derivedFrom":sQuery(id+"F20.wireOp",EDGE,"E52.25.0.19")}),1.0]])]});
            extrude(context, id + "F33", {"entities" : qUnion([Q0, Q1, Q2, Q3, Q4, Q5, Q6, Q7, Q8, Q9, Q10, Q11, Q12, Q13, Q14, Q15, Q16, Q17, Q18, Q19, Q20, Q21, Q22, Q23, Q24, Q25, Q26, Q27, Q28, Q29, Q30, Q31, Q32, Q33, Q34, Q35, Q36, Q37, Q38, Q39, Q40, Q41, Q42, Q43, Q44, Q45, Q46, Q47]), "operationType" : NewBodyOperationType.REMOVE, "depth" : 56 * mm, "offsetDistance" : 25 * mm, "symmetric" : true});
        }
        {
            var Q0;
            Q0=makeQuery(id+"F20.imprint","IMPRINT",FACE,{"disambiguationData":[TD([[makeQuery(id+"F20.imprint","IMPRINT",EDGE,{"derivedFrom":sQuery(id+"F20.wireOp",EDGE,"E52.29.0.4")}),1.0]])]});
            var Q1;
            Q1=makeQuery(id+"F20.imprint","IMPRINT",FACE,{"disambiguationData":[TD([[makeQuery(id+"F20.imprint","IMPRINT",EDGE,{"derivedFrom":sQuery(id+"F20.wireOp",EDGE,"E52.26.0.14")}),1.0]])]});
            var Q2;
            Q2=makeQuery(id+"F20.imprint","IMPRINT",FACE,{"disambiguationData":[TD([[makeQuery(id+"F20.imprint","IMPRINT",EDGE,{"derivedFrom":sQuery(id+"F20.wireOp",EDGE,"E52.29.0.5")}),1.0]])]});
            var Q3;
            Q3=makeQuery(id+"F20.imprint","IMPRINT",FACE,{"disambiguationData":[TD([[makeQuery(id+"F20.imprint","IMPRINT",EDGE,{"derivedFrom":sQuery(id+"F20.wireOp",EDGE,"E52.27.0.25")}),1.0]])]});
            var Q4;
            Q4=makeQuery(id+"F20.imprint","IMPRINT",FACE,{"disambiguationData":[TD([[makeQuery(id+"F20.imprint","IMPRINT",EDGE,{"derivedFrom":sQuery(id+"F20.wireOp",EDGE,"E52.26.0.23")}),1.0]])]});
            var Q5;
            Q5=makeQuery(id+"F20.imprint","IMPRINT",FACE,{"disambiguationData":[TD([[makeQuery(id+"F20.imprint","IMPRINT",EDGE,{"derivedFrom":sQuery(id+"F20.wireOp",EDGE,"E52.25.0.14")}),1.0]])]});
            var Q6;
            Q6=makeQuery(id+"F20.imprint","IMPRINT",FACE,{"disambiguationData":[TD([[makeQuery(id+"F20.imprint","IMPRINT",EDGE,{"derivedFrom":sQuery(id+"F20.wireOp",EDGE,"E52.28.0.5")}),1.0]])]});
            var Q7;
            Q7=makeQuery(id+"F20.imprint","IMPRINT",FACE,{"disambiguationData":[TD([[makeQuery(id+"F20.imprint","IMPRINT",EDGE,{"derivedFrom":sQuery(id+"F20.wireOp",EDGE,"E52.26.0.25")}),1.0]])]});
            var Q8;
            Q8=makeQuery(id+"F20.imprint","IMPRINT",FACE,{"disambiguationData":[TD([[makeQuery(id+"F20.imprint","IMPRINT",EDGE,{"derivedFrom":sQuery(id+"F20.wireOp",EDGE,"E52.29.0.23")}),1.0]])]});
            var Q9;
            Q9=makeQuery(id+"F20.imprint","IMPRINT",FACE,{"disambiguationData":[TD([[makeQuery(id+"F20.imprint","IMPRINT",EDGE,{"derivedFrom":sQuery(id+"F20.wireOp",EDGE,"E52.28.0.14")}),1.0]])]});
            var Q10;
            Q10=makeQuery(id+"F20.imprint","IMPRINT",FACE,{"disambiguationData":[TD([[makeQuery(id+"F20.imprint","IMPRINT",EDGE,{"derivedFrom":sQuery(id+"F20.wireOp",EDGE,"E52.27.0.4")}),1.0]])]});
            var Q11;
            Q11=makeQuery(id+"F20.imprint","IMPRINT",FACE,{"disambiguationData":[TD([[makeQuery(id+"F20.imprint","IMPRINT",EDGE,{"derivedFrom":sQuery(id+"F20.wireOp",EDGE,"E52.27.0.5")}),1.0]])]});
            var Q12;
            Q12=makeQuery(id+"F20.imprint","IMPRINT",FACE,{"disambiguationData":[TD([[makeQuery(id+"F20.imprint","IMPRINT",EDGE,{"derivedFrom":sQuery(id+"F20.wireOp",EDGE,"E52.29.0.25")}),1.0]])]});
            var Q13;
            Q13=makeQuery(id+"F20.imprint","IMPRINT",FACE,{"disambiguationData":[TD([[makeQuery(id+"F20.imprint","IMPRINT",EDGE,{"derivedFrom":sQuery(id+"F20.wireOp",EDGE,"E52.28.0.22")}),1.0]])]});
            var Q14;
            Q14=makeQuery(id+"F20.imprint","IMPRINT",FACE,{"disambiguationData":[TD([[makeQuery(id+"F20.imprint","IMPRINT",EDGE,{"derivedFrom":sQuery(id+"F20.wireOp",EDGE,"E52.28.0.23")}),1.0]])]});
            var Q15;
            Q15=makeQuery(id+"F20.imprint","IMPRINT",FACE,{"disambiguationData":[TD([[makeQuery(id+"F20.imprint","IMPRINT",EDGE,{"derivedFrom":sQuery(id+"F20.wireOp",EDGE,"E52.27.0.14")}),1.0]])]});
            var Q16;
            Q16=makeQuery(id+"F20.imprint","IMPRINT",FACE,{"disambiguationData":[TD([[makeQuery(id+"F20.imprint","IMPRINT",EDGE,{"derivedFrom":sQuery(id+"F20.wireOp",EDGE,"E52.26.0.4")}),1.0]])]});
            var Q17;
            Q17=makeQuery(id+"F20.imprint","IMPRINT",FACE,{"disambiguationData":[TD([[makeQuery(id+"F20.imprint","IMPRINT",EDGE,{"derivedFrom":sQuery(id+"F20.wireOp",EDGE,"E52.26.0.5")}),1.0]])]});
            var Q18;
            Q18=makeQuery(id+"F20.imprint","IMPRINT",FACE,{"disambiguationData":[TD([[makeQuery(id+"F20.imprint","IMPRINT",EDGE,{"derivedFrom":sQuery(id+"F20.wireOp",EDGE,"E52.28.0.25")}),1.0]])]});
            var Q19;
            Q19=makeQuery(id+"F20.imprint","IMPRINT",FACE,{"disambiguationData":[TD([[makeQuery(id+"F20.imprint","IMPRINT",EDGE,{"derivedFrom":sQuery(id+"F20.wireOp",EDGE,"E52.27.0.22")}),1.0]])]});
            var Q20;
            Q20=makeQuery(id+"F20.imprint","IMPRINT",FACE,{"disambiguationData":[TD([[makeQuery(id+"F20.imprint","IMPRINT",EDGE,{"derivedFrom":sQuery(id+"F20.wireOp",EDGE,"E52.29.0.6")}),1.0]])]});
            var Q21;
            Q21=makeQuery(id+"F20.imprint","IMPRINT",FACE,{"disambiguationData":[TD([[makeQuery(id+"F20.imprint","IMPRINT",EDGE,{"derivedFrom":sQuery(id+"F20.wireOp",EDGE,"E52.27.0.26")}),1.0]])]});
            var Q22;
            Q22=makeQuery(id+"F20.imprint","IMPRINT",FACE,{"disambiguationData":[TD([[makeQuery(id+"F20.imprint","IMPRINT",EDGE,{"derivedFrom":sQuery(id+"F20.wireOp",EDGE,"E52.26.0.19")}),1.0]])]});
            var Q23;
            Q23=makeQuery(id+"F20.imprint","IMPRINT",FACE,{"disambiguationData":[TD([[makeQuery(id+"F20.imprint","IMPRINT",EDGE,{"derivedFrom":sQuery(id+"F20.wireOp",EDGE,"E52.27.0.23")}),1.0]])]});
            var Q24;
            Q24=makeQuery(id+"F20.imprint","IMPRINT",FACE,{"disambiguationData":[TD([[makeQuery(id+"F20.imprint","IMPRINT",EDGE,{"derivedFrom":sQuery(id+"F20.wireOp",EDGE,"E52.26.0.15")}),1.0]])]});
            var Q25;
            Q25=makeQuery(id+"F20.imprint","IMPRINT",FACE,{"disambiguationData":[TD([[makeQuery(id+"F20.imprint","IMPRINT",EDGE,{"derivedFrom":sQuery(id+"F20.wireOp",EDGE,"E52.29.0.10")}),1.0]])]});
            var Q26;
            Q26=makeQuery(id+"F20.imprint","IMPRINT",FACE,{"disambiguationData":[TD([[makeQuery(id+"F20.imprint","IMPRINT",EDGE,{"derivedFrom":sQuery(id+"F20.wireOp",EDGE,"E52.28.0.0")}),1.0]])]});
            var Q27;
            Q27=makeQuery(id+"F20.imprint","IMPRINT",FACE,{"disambiguationData":[TD([[makeQuery(id+"F20.imprint","IMPRINT",EDGE,{"derivedFrom":sQuery(id+"F20.wireOp",EDGE,"E52.26.0.22")}),1.0]])]});
            var Q28;
            Q28=makeQuery(id+"F20.imprint","IMPRINT",FACE,{"disambiguationData":[TD([[makeQuery(id+"F20.imprint","IMPRINT",EDGE,{"derivedFrom":sQuery(id+"F20.wireOp",EDGE,"E52.28.0.4")}),1.0]])]});
            var Q29;
            Q29=makeQuery(id+"F20.imprint","IMPRINT",FACE,{"disambiguationData":[TD([[makeQuery(id+"F20.imprint","IMPRINT",EDGE,{"derivedFrom":sQuery(id+"F20.wireOp",EDGE,"E52.29.0.15")}),1.0]])]});
            var Q30;
            Q30=makeQuery(id+"F20.imprint","IMPRINT",FACE,{"disambiguationData":[TD([[makeQuery(id+"F20.imprint","IMPRINT",EDGE,{"derivedFrom":sQuery(id+"F20.wireOp",EDGE,"E52.29.0.19")}),1.0]])]});
            var Q31;
            Q31=makeQuery(id+"F20.imprint","IMPRINT",FACE,{"disambiguationData":[TD([[makeQuery(id+"F20.imprint","IMPRINT",EDGE,{"derivedFrom":sQuery(id+"F20.wireOp",EDGE,"E52.28.0.6")}),1.0]])]});
            var Q32;
            Q32=makeQuery(id+"F20.imprint","IMPRINT",FACE,{"disambiguationData":[TD([[makeQuery(id+"F20.imprint","IMPRINT",EDGE,{"derivedFrom":sQuery(id+"F20.wireOp",EDGE,"E52.26.0.26")}),1.0]])]});
            var Q33;
            Q33=makeQuery(id+"F20.imprint","IMPRINT",FACE,{"disambiguationData":[TD([[makeQuery(id+"F20.imprint","IMPRINT",EDGE,{"derivedFrom":sQuery(id+"F20.wireOp",EDGE,"E52.29.0.22")}),1.0]])]});
            var Q34;
            Q34=makeQuery(id+"F20.imprint","IMPRINT",FACE,{"disambiguationData":[TD([[makeQuery(id+"F20.imprint","IMPRINT",EDGE,{"derivedFrom":sQuery(id+"F20.wireOp",EDGE,"E52.28.0.10")}),1.0]])]});
            var Q35;
            Q35=makeQuery(id+"F20.imprint","IMPRINT",FACE,{"disambiguationData":[TD([[makeQuery(id+"F20.imprint","IMPRINT",EDGE,{"derivedFrom":sQuery(id+"F20.wireOp",EDGE,"E52.27.0.0")}),1.0]])]});
            var Q36;
            Q36=makeQuery(id+"F20.imprint","IMPRINT",FACE,{"disambiguationData":[TD([[makeQuery(id+"F20.imprint","IMPRINT",EDGE,{"derivedFrom":sQuery(id+"F20.wireOp",EDGE,"E52.28.0.15")}),1.0]])]});
            var Q37;
            Q37=makeQuery(id+"F20.imprint","IMPRINT",FACE,{"disambiguationData":[TD([[makeQuery(id+"F20.imprint","IMPRINT",EDGE,{"derivedFrom":sQuery(id+"F20.wireOp",EDGE,"E52.27.0.6")}),1.0]])]});
            var Q38;
            Q38=makeQuery(id+"F20.imprint","IMPRINT",FACE,{"disambiguationData":[TD([[makeQuery(id+"F20.imprint","IMPRINT",EDGE,{"derivedFrom":sQuery(id+"F20.wireOp",EDGE,"E52.28.0.19")}),1.0]])]});
            var Q39;
            Q39=makeQuery(id+"F20.imprint","IMPRINT",FACE,{"disambiguationData":[TD([[makeQuery(id+"F20.imprint","IMPRINT",EDGE,{"derivedFrom":sQuery(id+"F20.wireOp",EDGE,"E52.27.0.10")}),1.0]])]});
            var Q40;
            Q40=makeQuery(id+"F20.imprint","IMPRINT",FACE,{"disambiguationData":[TD([[makeQuery(id+"F20.imprint","IMPRINT",EDGE,{"derivedFrom":sQuery(id+"F20.wireOp",EDGE,"E52.26.0.0")}),1.0]])]});
            var Q41;
            Q41=makeQuery(id+"F20.imprint","IMPRINT",FACE,{"disambiguationData":[TD([[makeQuery(id+"F20.imprint","IMPRINT",EDGE,{"derivedFrom":sQuery(id+"F20.wireOp",EDGE,"E52.27.0.15")}),1.0]])]});
            var Q42;
            Q42=makeQuery(id+"F20.imprint","IMPRINT",FACE,{"disambiguationData":[TD([[makeQuery(id+"F20.imprint","IMPRINT",EDGE,{"derivedFrom":sQuery(id+"F20.wireOp",EDGE,"E52.27.0.19")}),1.0]])]});
            var Q43;
            Q43=makeQuery(id+"F20.imprint","IMPRINT",FACE,{"disambiguationData":[TD([[makeQuery(id+"F20.imprint","IMPRINT",EDGE,{"derivedFrom":sQuery(id+"F20.wireOp",EDGE,"E52.26.0.6")}),1.0]])]});
            var Q44;
            Q44=makeQuery(id+"F20.imprint","IMPRINT",FACE,{"disambiguationData":[TD([[makeQuery(id+"F20.imprint","IMPRINT",EDGE,{"derivedFrom":sQuery(id+"F20.wireOp",EDGE,"E52.28.0.26")}),1.0]])]});
            var Q45;
            Q45=makeQuery(id+"F20.imprint","IMPRINT",FACE,{"disambiguationData":[TD([[makeQuery(id+"F20.imprint","IMPRINT",EDGE,{"derivedFrom":sQuery(id+"F20.wireOp",EDGE,"E52.26.0.10")}),1.0]])]});
            var Q46;
            Q46=makeQuery(id+"F20.imprint","IMPRINT",FACE,{"disambiguationData":[TD([[makeQuery(id+"F20.imprint","IMPRINT",EDGE,{"derivedFrom":sQuery(id+"F20.wireOp",EDGE,"E52.25.0.26")}),1.0]])]});
            var Q47;
            Q47=makeQuery(id+"F20.imprint","IMPRINT",FACE,{"disambiguationData":[TD([[makeQuery(id+"F20.imprint","IMPRINT",EDGE,{"derivedFrom":sQuery(id+"F20.wireOp",EDGE,"E52.25.0.0")}),1.0]])]});
            extrude(context, id + "F34", {"entities" : qUnion([Q0, Q1, Q2, Q3, Q4, Q5, Q6, Q7, Q8, Q9, Q10, Q11, Q12, Q13, Q14, Q15, Q16, Q17, Q18, Q19, Q20, Q21, Q22, Q23, Q24, Q25, Q26, Q27, Q28, Q29, Q30, Q31, Q32, Q33, Q34, Q35, Q36, Q37, Q38, Q39, Q40, Q41, Q42, Q43, Q44, Q45, Q46, Q47]), "operationType" : NewBodyOperationType.REMOVE, "oppositeDirection" : true, "depth" : 56 * mm, "offsetDistance" : 25 * mm, "symmetric" : true});
        }
        {
            var Q0;
            Q0=makeQuery(id+"F20.imprint","IMPRINT",FACE,{"disambiguationData":[TD([[makeQuery(id+"F20.imprint","IMPRINT",EDGE,{"derivedFrom":sQuery(id+"F20.wireOp",EDGE,"E52.30.0.14")}),1.0]])]});
            var Q1;
            Q1=makeQuery(id+"F20.imprint","IMPRINT",FACE,{"disambiguationData":[TD([[makeQuery(id+"F20.imprint","IMPRINT",EDGE,{"derivedFrom":sQuery(id+"F20.wireOp",EDGE,"E52.29.0.14")}),1.0]])]});
            var Q2;
            Q2=makeQuery(id+"F20.imprint","IMPRINT",FACE,{"disambiguationData":[TD([[makeQuery(id+"F20.imprint","IMPRINT",EDGE,{"derivedFrom":sQuery(id+"F20.wireOp",EDGE,"E52.32.0.14")}),1.0]])]});
            var Q3;
            Q3=makeQuery(id+"F20.imprint","IMPRINT",FACE,{"disambiguationData":[TD([[makeQuery(id+"F20.imprint","IMPRINT",EDGE,{"derivedFrom":sQuery(id+"F20.wireOp",EDGE,"E52.31.0.14")}),1.0]])]});
            var Q4;
            Q4=makeQuery(id+"F20.imprint","IMPRINT",FACE,{"disambiguationData":[TD([[makeQuery(id+"F20.imprint","IMPRINT",EDGE,{"derivedFrom":sQuery(id+"F20.wireOp",EDGE,"E52.33.0.6")}),1.0]])]});
            var Q5;
            Q5=makeQuery(id+"F20.imprint","IMPRINT",FACE,{"disambiguationData":[TD([[makeQuery(id+"F20.imprint","IMPRINT",EDGE,{"derivedFrom":sQuery(id+"F20.wireOp",EDGE,"E52.31.0.26")}),1.0]])]});
            var Q6;
            Q6=makeQuery(id+"F20.imprint","IMPRINT",FACE,{"disambiguationData":[TD([[makeQuery(id+"F20.imprint","IMPRINT",EDGE,{"derivedFrom":sQuery(id+"F20.wireOp",EDGE,"E52.33.0.4")}),1.0]])]});
            var Q7;
            Q7=makeQuery(id+"F20.imprint","IMPRINT",FACE,{"disambiguationData":[TD([[makeQuery(id+"F20.imprint","IMPRINT",EDGE,{"derivedFrom":sQuery(id+"F20.wireOp",EDGE,"E52.31.0.23")}),1.0]])]});
            var Q8;
            Q8=makeQuery(id+"F20.imprint","IMPRINT",FACE,{"disambiguationData":[TD([[makeQuery(id+"F20.imprint","IMPRINT",EDGE,{"derivedFrom":sQuery(id+"F20.wireOp",EDGE,"E52.33.0.5")}),1.0]])]});
            var Q9;
            Q9=makeQuery(id+"F20.imprint","IMPRINT",FACE,{"disambiguationData":[TD([[makeQuery(id+"F20.imprint","IMPRINT",EDGE,{"derivedFrom":sQuery(id+"F20.wireOp",EDGE,"E52.31.0.25")}),1.0]])]});
            var Q10;
            Q10=makeQuery(id+"F20.imprint","IMPRINT",FACE,{"disambiguationData":[TD([[makeQuery(id+"F20.imprint","IMPRINT",EDGE,{"derivedFrom":sQuery(id+"F20.wireOp",EDGE,"E52.30.0.22")}),1.0]])]});
            var Q11;
            Q11=makeQuery(id+"F20.imprint","IMPRINT",FACE,{"disambiguationData":[TD([[makeQuery(id+"F20.imprint","IMPRINT",EDGE,{"derivedFrom":sQuery(id+"F20.wireOp",EDGE,"E52.32.0.4")}),1.0]])]});
            var Q12;
            Q12=makeQuery(id+"F20.imprint","IMPRINT",FACE,{"disambiguationData":[TD([[makeQuery(id+"F20.imprint","IMPRINT",EDGE,{"derivedFrom":sQuery(id+"F20.wireOp",EDGE,"E52.30.0.23")}),1.0]])]});
            var Q13;
            Q13=makeQuery(id+"F20.imprint","IMPRINT",FACE,{"disambiguationData":[TD([[makeQuery(id+"F20.imprint","IMPRINT",EDGE,{"derivedFrom":sQuery(id+"F20.wireOp",EDGE,"E52.33.0.15")}),1.0]])]});
            var Q14;
            Q14=makeQuery(id+"F20.imprint","IMPRINT",FACE,{"disambiguationData":[TD([[makeQuery(id+"F20.imprint","IMPRINT",EDGE,{"derivedFrom":sQuery(id+"F20.wireOp",EDGE,"E52.32.0.5")}),1.0]])]});
            var Q15;
            Q15=makeQuery(id+"F20.imprint","IMPRINT",FACE,{"disambiguationData":[TD([[makeQuery(id+"F20.imprint","IMPRINT",EDGE,{"derivedFrom":sQuery(id+"F20.wireOp",EDGE,"E52.30.0.25")}),1.0]])]});
            var Q16;
            Q16=makeQuery(id+"F20.imprint","IMPRINT",FACE,{"disambiguationData":[TD([[makeQuery(id+"F20.imprint","IMPRINT",EDGE,{"derivedFrom":sQuery(id+"F20.wireOp",EDGE,"E52.33.0.22")}),1.0]])]});
            var Q17;
            Q17=makeQuery(id+"F20.imprint","IMPRINT",FACE,{"disambiguationData":[TD([[makeQuery(id+"F20.imprint","IMPRINT",EDGE,{"derivedFrom":sQuery(id+"F20.wireOp",EDGE,"E52.32.0.10")}),1.0]])]});
            var Q18;
            Q18=makeQuery(id+"F20.imprint","IMPRINT",FACE,{"disambiguationData":[TD([[makeQuery(id+"F20.imprint","IMPRINT",EDGE,{"derivedFrom":sQuery(id+"F20.wireOp",EDGE,"E52.31.0.0")}),1.0]])]});
            var Q19;
            Q19=makeQuery(id+"F20.imprint","IMPRINT",FACE,{"disambiguationData":[TD([[makeQuery(id+"F20.imprint","IMPRINT",EDGE,{"derivedFrom":sQuery(id+"F20.wireOp",EDGE,"E52.33.0.23")}),1.0]])]});
            var Q20;
            Q20=makeQuery(id+"F20.imprint","IMPRINT",FACE,{"disambiguationData":[TD([[makeQuery(id+"F20.imprint","IMPRINT",EDGE,{"derivedFrom":sQuery(id+"F20.wireOp",EDGE,"E52.31.0.4")}),1.0]])]});
            var Q21;
            Q21=makeQuery(id+"F20.imprint","IMPRINT",FACE,{"disambiguationData":[TD([[makeQuery(id+"F20.imprint","IMPRINT",EDGE,{"derivedFrom":sQuery(id+"F20.wireOp",EDGE,"E52.31.0.5")}),1.0]])]});
            var Q22;
            Q22=makeQuery(id+"F20.imprint","IMPRINT",FACE,{"disambiguationData":[TD([[makeQuery(id+"F20.imprint","IMPRINT",EDGE,{"derivedFrom":sQuery(id+"F20.wireOp",EDGE,"E52.33.0.25")}),1.0]])]});
            var Q23;
            Q23=makeQuery(id+"F20.imprint","IMPRINT",FACE,{"disambiguationData":[TD([[makeQuery(id+"F20.imprint","IMPRINT",EDGE,{"derivedFrom":sQuery(id+"F20.wireOp",EDGE,"E52.32.0.19")}),1.0]])]});
            var Q24;
            Q24=makeQuery(id+"F20.imprint","IMPRINT",FACE,{"disambiguationData":[TD([[makeQuery(id+"F20.imprint","IMPRINT",EDGE,{"derivedFrom":sQuery(id+"F20.wireOp",EDGE,"E52.31.0.6")}),1.0]])]});
            var Q25;
            Q25=makeQuery(id+"F20.imprint","IMPRINT",FACE,{"disambiguationData":[TD([[makeQuery(id+"F20.imprint","IMPRINT",EDGE,{"derivedFrom":sQuery(id+"F20.wireOp",EDGE,"E52.32.0.22")}),1.0]])]});
            var Q26;
            Q26=makeQuery(id+"F20.imprint","IMPRINT",FACE,{"disambiguationData":[TD([[makeQuery(id+"F20.imprint","IMPRINT",EDGE,{"derivedFrom":sQuery(id+"F20.wireOp",EDGE,"E52.32.0.23")}),1.0]])]});
            var Q27;
            Q27=makeQuery(id+"F20.imprint","IMPRINT",FACE,{"disambiguationData":[TD([[makeQuery(id+"F20.imprint","IMPRINT",EDGE,{"derivedFrom":sQuery(id+"F20.wireOp",EDGE,"E52.30.0.4")}),1.0]])]});
            var Q28;
            Q28=makeQuery(id+"F20.imprint","IMPRINT",FACE,{"disambiguationData":[TD([[makeQuery(id+"F20.imprint","IMPRINT",EDGE,{"derivedFrom":sQuery(id+"F20.wireOp",EDGE,"E52.32.0.25")}),1.0]])]});
            var Q29;
            Q29=makeQuery(id+"F20.imprint","IMPRINT",FACE,{"disambiguationData":[TD([[makeQuery(id+"F20.imprint","IMPRINT",EDGE,{"derivedFrom":sQuery(id+"F20.wireOp",EDGE,"E52.31.0.15")}),1.0]])]});
            var Q30;
            Q30=makeQuery(id+"F20.imprint","IMPRINT",FACE,{"disambiguationData":[TD([[makeQuery(id+"F20.imprint","IMPRINT",EDGE,{"derivedFrom":sQuery(id+"F20.wireOp",EDGE,"E52.30.0.5")}),1.0]])]});
            var Q31;
            Q31=makeQuery(id+"F20.imprint","IMPRINT",FACE,{"disambiguationData":[TD([[makeQuery(id+"F20.imprint","IMPRINT",EDGE,{"derivedFrom":sQuery(id+"F20.wireOp",EDGE,"E52.31.0.22")}),1.0]])]});
            var Q32;
            Q32=makeQuery(id+"F20.imprint","IMPRINT",FACE,{"disambiguationData":[TD([[makeQuery(id+"F20.imprint","IMPRINT",EDGE,{"derivedFrom":sQuery(id+"F20.wireOp",EDGE,"E52.30.0.19")}),1.0]])]});
            var Q33;
            Q33=makeQuery(id+"F20.imprint","IMPRINT",FACE,{"disambiguationData":[TD([[makeQuery(id+"F20.imprint","IMPRINT",EDGE,{"derivedFrom":sQuery(id+"F20.wireOp",EDGE,"E52.30.0.15")}),1.0]])]});
            var Q34;
            Q34=makeQuery(id+"F20.imprint","IMPRINT",FACE,{"disambiguationData":[TD([[makeQuery(id+"F20.imprint","IMPRINT",EDGE,{"derivedFrom":sQuery(id+"F20.wireOp",EDGE,"E52.33.0.10")}),1.0]])]});
            var Q35;
            Q35=makeQuery(id+"F20.imprint","IMPRINT",FACE,{"disambiguationData":[TD([[makeQuery(id+"F20.imprint","IMPRINT",EDGE,{"derivedFrom":sQuery(id+"F20.wireOp",EDGE,"E52.32.0.0")}),1.0]])]});
            var Q36;
            Q36=makeQuery(id+"F20.imprint","IMPRINT",FACE,{"disambiguationData":[TD([[makeQuery(id+"F20.imprint","IMPRINT",EDGE,{"derivedFrom":sQuery(id+"F20.wireOp",EDGE,"E52.33.0.19")}),1.0]])]});
            var Q37;
            Q37=makeQuery(id+"F20.imprint","IMPRINT",FACE,{"disambiguationData":[TD([[makeQuery(id+"F20.imprint","IMPRINT",EDGE,{"derivedFrom":sQuery(id+"F20.wireOp",EDGE,"E52.32.0.6")}),1.0]])]});
            var Q38;
            Q38=makeQuery(id+"F20.imprint","IMPRINT",FACE,{"disambiguationData":[TD([[makeQuery(id+"F20.imprint","IMPRINT",EDGE,{"derivedFrom":sQuery(id+"F20.wireOp",EDGE,"E52.30.0.26")}),1.0]])]});
            var Q39;
            Q39=makeQuery(id+"F20.imprint","IMPRINT",FACE,{"disambiguationData":[TD([[makeQuery(id+"F20.imprint","IMPRINT",EDGE,{"derivedFrom":sQuery(id+"F20.wireOp",EDGE,"E52.32.0.15")}),1.0]])]});
            var Q40;
            Q40=makeQuery(id+"F20.imprint","IMPRINT",FACE,{"disambiguationData":[TD([[makeQuery(id+"F20.imprint","IMPRINT",EDGE,{"derivedFrom":sQuery(id+"F20.wireOp",EDGE,"E52.31.0.10")}),1.0]])]});
            var Q41;
            Q41=makeQuery(id+"F20.imprint","IMPRINT",FACE,{"disambiguationData":[TD([[makeQuery(id+"F20.imprint","IMPRINT",EDGE,{"derivedFrom":sQuery(id+"F20.wireOp",EDGE,"E52.30.0.0")}),1.0]])]});
            var Q42;
            Q42=makeQuery(id+"F20.imprint","IMPRINT",FACE,{"disambiguationData":[TD([[makeQuery(id+"F20.imprint","IMPRINT",EDGE,{"derivedFrom":sQuery(id+"F20.wireOp",EDGE,"E52.32.0.26")}),1.0]])]});
            var Q43;
            Q43=makeQuery(id+"F20.imprint","IMPRINT",FACE,{"disambiguationData":[TD([[makeQuery(id+"F20.imprint","IMPRINT",EDGE,{"derivedFrom":sQuery(id+"F20.wireOp",EDGE,"E52.31.0.19")}),1.0]])]});
            var Q44;
            Q44=makeQuery(id+"F20.imprint","IMPRINT",FACE,{"disambiguationData":[TD([[makeQuery(id+"F20.imprint","IMPRINT",EDGE,{"derivedFrom":sQuery(id+"F20.wireOp",EDGE,"E52.30.0.6")}),1.0]])]});
            var Q45;
            Q45=makeQuery(id+"F20.imprint","IMPRINT",FACE,{"disambiguationData":[TD([[makeQuery(id+"F20.imprint","IMPRINT",EDGE,{"derivedFrom":sQuery(id+"F20.wireOp",EDGE,"E52.30.0.10")}),1.0]])]});
            var Q46;
            Q46=makeQuery(id+"F20.imprint","IMPRINT",FACE,{"disambiguationData":[TD([[makeQuery(id+"F20.imprint","IMPRINT",EDGE,{"derivedFrom":sQuery(id+"F20.wireOp",EDGE,"E52.29.0.26")}),1.0]])]});
            var Q47;
            Q47=makeQuery(id+"F20.imprint","IMPRINT",FACE,{"disambiguationData":[TD([[makeQuery(id+"F20.imprint","IMPRINT",EDGE,{"derivedFrom":sQuery(id+"F20.wireOp",EDGE,"E52.29.0.0")}),1.0]])]});
            extrude(context, id + "F35", {"entities" : qUnion([Q0, Q1, Q2, Q3, Q4, Q5, Q6, Q7, Q8, Q9, Q10, Q11, Q12, Q13, Q14, Q15, Q16, Q17, Q18, Q19, Q20, Q21, Q22, Q23, Q24, Q25, Q26, Q27, Q28, Q29, Q30, Q31, Q32, Q33, Q34, Q35, Q36, Q37, Q38, Q39, Q40, Q41, Q42, Q43, Q44, Q45, Q46, Q47]), "operationType" : NewBodyOperationType.REMOVE, "oppositeDirection" : true, "depth" : 50 * mm, "offsetDistance" : 25 * mm, "symmetric" : true});
        }
        {
            var Q0;
            Q0=makeQuery(id+"F20.imprint","IMPRINT",FACE,{"disambiguationData":[TD([[makeQuery(id+"F20.imprint","IMPRINT",EDGE,{"derivedFrom":sQuery(id+"F20.wireOp",EDGE,"E52.34.0.14")}),1.0]])]});
            var Q1;
            Q1=makeQuery(id+"F20.imprint","IMPRINT",FACE,{"disambiguationData":[TD([[makeQuery(id+"F20.imprint","IMPRINT",EDGE,{"derivedFrom":sQuery(id+"F20.wireOp",EDGE,"E52.33.0.14")}),1.0]])]});
            var Q2;
            Q2=makeQuery(id+"F20.imprint","IMPRINT",FACE,{"disambiguationData":[TD([[makeQuery(id+"F20.imprint","IMPRINT",EDGE,{"derivedFrom":sQuery(id+"F20.wireOp",EDGE,"E52.36.0.14")}),1.0]])]});
            var Q3;
            Q3=makeQuery(id+"F20.imprint","IMPRINT",FACE,{"disambiguationData":[TD([[makeQuery(id+"F20.imprint","IMPRINT",EDGE,{"derivedFrom":sQuery(id+"F20.wireOp",EDGE,"E52.35.0.14")}),1.0]])]});
            var Q4;
            Q4=makeQuery(id+"F20.imprint","IMPRINT",FACE,{"disambiguationData":[TD([[makeQuery(id+"F20.imprint","IMPRINT",EDGE,{"derivedFrom":sQuery(id+"F20.wireOp",EDGE,"E52.37.0.4")}),1.0]])]});
            var Q5;
            Q5=makeQuery(id+"F20.imprint","IMPRINT",FACE,{"disambiguationData":[TD([[makeQuery(id+"F20.imprint","IMPRINT",EDGE,{"derivedFrom":sQuery(id+"F20.wireOp",EDGE,"E52.35.0.23")}),1.0]])]});
            var Q6;
            Q6=makeQuery(id+"F20.imprint","IMPRINT",FACE,{"disambiguationData":[TD([[makeQuery(id+"F20.imprint","IMPRINT",EDGE,{"derivedFrom":sQuery(id+"F20.wireOp",EDGE,"E52.37.0.5")}),1.0]])]});
            var Q7;
            Q7=makeQuery(id+"F20.imprint","IMPRINT",FACE,{"disambiguationData":[TD([[makeQuery(id+"F20.imprint","IMPRINT",EDGE,{"derivedFrom":sQuery(id+"F20.wireOp",EDGE,"E52.35.0.25")}),1.0]])]});
            var Q8;
            Q8=makeQuery(id+"F20.imprint","IMPRINT",FACE,{"disambiguationData":[TD([[makeQuery(id+"F20.imprint","IMPRINT",EDGE,{"derivedFrom":sQuery(id+"F20.wireOp",EDGE,"E52.37.0.10")}),1.0]])]});
            var Q9;
            Q9=makeQuery(id+"F20.imprint","IMPRINT",FACE,{"disambiguationData":[TD([[makeQuery(id+"F20.imprint","IMPRINT",EDGE,{"derivedFrom":sQuery(id+"F20.wireOp",EDGE,"E52.36.0.0")}),1.0]])]});
            var Q10;
            Q10=makeQuery(id+"F20.imprint","IMPRINT",FACE,{"disambiguationData":[TD([[makeQuery(id+"F20.imprint","IMPRINT",EDGE,{"derivedFrom":sQuery(id+"F20.wireOp",EDGE,"E52.34.0.22")}),1.0]])]});
            var Q11;
            Q11=makeQuery(id+"F20.imprint","IMPRINT",FACE,{"disambiguationData":[TD([[makeQuery(id+"F20.imprint","IMPRINT",EDGE,{"derivedFrom":sQuery(id+"F20.wireOp",EDGE,"E52.36.0.4")}),1.0]])]});
            var Q12;
            Q12=makeQuery(id+"F20.imprint","IMPRINT",FACE,{"disambiguationData":[TD([[makeQuery(id+"F20.imprint","IMPRINT",EDGE,{"derivedFrom":sQuery(id+"F20.wireOp",EDGE,"E52.34.0.23")}),1.0]])]});
            var Q13;
            Q13=makeQuery(id+"F20.imprint","IMPRINT",FACE,{"disambiguationData":[TD([[makeQuery(id+"F20.imprint","IMPRINT",EDGE,{"derivedFrom":sQuery(id+"F20.wireOp",EDGE,"E52.37.0.15")}),1.0]])]});
            var Q14;
            Q14=makeQuery(id+"F20.imprint","IMPRINT",FACE,{"disambiguationData":[TD([[makeQuery(id+"F20.imprint","IMPRINT",EDGE,{"derivedFrom":sQuery(id+"F20.wireOp",EDGE,"E52.36.0.5")}),1.0]])]});
            var Q15;
            Q15=makeQuery(id+"F20.imprint","IMPRINT",FACE,{"disambiguationData":[TD([[makeQuery(id+"F20.imprint","IMPRINT",EDGE,{"derivedFrom":sQuery(id+"F20.wireOp",EDGE,"E52.34.0.25")}),1.0]])]});
            var Q16;
            Q16=makeQuery(id+"F20.imprint","IMPRINT",FACE,{"disambiguationData":[TD([[makeQuery(id+"F20.imprint","IMPRINT",EDGE,{"derivedFrom":sQuery(id+"F20.wireOp",EDGE,"E52.36.0.6")}),1.0]])]});
            var Q17;
            Q17=makeQuery(id+"F20.imprint","IMPRINT",FACE,{"disambiguationData":[TD([[makeQuery(id+"F20.imprint","IMPRINT",EDGE,{"derivedFrom":sQuery(id+"F20.wireOp",EDGE,"E52.34.0.26")}),1.0]])]});
            var Q18;
            Q18=makeQuery(id+"F20.imprint","IMPRINT",FACE,{"disambiguationData":[TD([[makeQuery(id+"F20.imprint","IMPRINT",EDGE,{"derivedFrom":sQuery(id+"F20.wireOp",EDGE,"E52.37.0.22")}),1.0]])]});
            var Q19;
            Q19=makeQuery(id+"F20.imprint","IMPRINT",FACE,{"disambiguationData":[TD([[makeQuery(id+"F20.imprint","IMPRINT",EDGE,{"derivedFrom":sQuery(id+"F20.wireOp",EDGE,"E52.37.0.23")}),1.0]])]});
            var Q20;
            Q20=makeQuery(id+"F20.imprint","IMPRINT",FACE,{"disambiguationData":[TD([[makeQuery(id+"F20.imprint","IMPRINT",EDGE,{"derivedFrom":sQuery(id+"F20.wireOp",EDGE,"E52.35.0.4")}),1.0]])]});
            var Q21;
            Q21=makeQuery(id+"F20.imprint","IMPRINT",FACE,{"disambiguationData":[TD([[makeQuery(id+"F20.imprint","IMPRINT",EDGE,{"derivedFrom":sQuery(id+"F20.wireOp",EDGE,"E52.35.0.5")}),1.0]])]});
            var Q22;
            Q22=makeQuery(id+"F20.imprint","IMPRINT",FACE,{"disambiguationData":[TD([[makeQuery(id+"F20.imprint","IMPRINT",EDGE,{"derivedFrom":sQuery(id+"F20.wireOp",EDGE,"E52.37.0.25")}),1.0]])]});
            var Q23;
            Q23=makeQuery(id+"F20.imprint","IMPRINT",FACE,{"disambiguationData":[TD([[makeQuery(id+"F20.imprint","IMPRINT",EDGE,{"derivedFrom":sQuery(id+"F20.wireOp",EDGE,"E52.36.0.15")}),1.0]])]});
            var Q24;
            Q24=makeQuery(id+"F20.imprint","IMPRINT",FACE,{"disambiguationData":[TD([[makeQuery(id+"F20.imprint","IMPRINT",EDGE,{"derivedFrom":sQuery(id+"F20.wireOp",EDGE,"E52.34.0.0")}),1.0]])]});
            var Q25;
            Q25=makeQuery(id+"F20.imprint","IMPRINT",FACE,{"disambiguationData":[TD([[makeQuery(id+"F20.imprint","IMPRINT",EDGE,{"derivedFrom":sQuery(id+"F20.wireOp",EDGE,"E52.35.0.10")}),1.0]])]});
            var Q26;
            Q26=makeQuery(id+"F20.imprint","IMPRINT",FACE,{"disambiguationData":[TD([[makeQuery(id+"F20.imprint","IMPRINT",EDGE,{"derivedFrom":sQuery(id+"F20.wireOp",EDGE,"E52.36.0.22")}),1.0]])]});
            var Q27;
            Q27=makeQuery(id+"F20.imprint","IMPRINT",FACE,{"disambiguationData":[TD([[makeQuery(id+"F20.imprint","IMPRINT",EDGE,{"derivedFrom":sQuery(id+"F20.wireOp",EDGE,"E52.34.0.4")}),1.0]])]});
            var Q28;
            Q28=makeQuery(id+"F20.imprint","IMPRINT",FACE,{"disambiguationData":[TD([[makeQuery(id+"F20.imprint","IMPRINT",EDGE,{"derivedFrom":sQuery(id+"F20.wireOp",EDGE,"E52.36.0.23")}),1.0]])]});
            var Q29;
            Q29=makeQuery(id+"F20.imprint","IMPRINT",FACE,{"disambiguationData":[TD([[makeQuery(id+"F20.imprint","IMPRINT",EDGE,{"derivedFrom":sQuery(id+"F20.wireOp",EDGE,"E52.34.0.5")}),1.0]])]});
            var Q30;
            Q30=makeQuery(id+"F20.imprint","IMPRINT",FACE,{"disambiguationData":[TD([[makeQuery(id+"F20.imprint","IMPRINT",EDGE,{"derivedFrom":sQuery(id+"F20.wireOp",EDGE,"E52.36.0.25")}),1.0]])]});
            var Q31;
            Q31=makeQuery(id+"F20.imprint","IMPRINT",FACE,{"disambiguationData":[TD([[makeQuery(id+"F20.imprint","IMPRINT",EDGE,{"derivedFrom":sQuery(id+"F20.wireOp",EDGE,"E52.35.0.19")}),1.0]])]});
            var Q32;
            Q32=makeQuery(id+"F20.imprint","IMPRINT",FACE,{"disambiguationData":[TD([[makeQuery(id+"F20.imprint","IMPRINT",EDGE,{"derivedFrom":sQuery(id+"F20.wireOp",EDGE,"E52.36.0.26")}),1.0]])]});
            var Q33;
            Q33=makeQuery(id+"F20.imprint","IMPRINT",FACE,{"disambiguationData":[TD([[makeQuery(id+"F20.imprint","IMPRINT",EDGE,{"derivedFrom":sQuery(id+"F20.wireOp",EDGE,"E52.34.0.6")}),1.0]])]});
            var Q34;
            Q34=makeQuery(id+"F20.imprint","IMPRINT",FACE,{"disambiguationData":[TD([[makeQuery(id+"F20.imprint","IMPRINT",EDGE,{"derivedFrom":sQuery(id+"F20.wireOp",EDGE,"E52.35.0.22")}),1.0]])]});
            var Q35;
            Q35=makeQuery(id+"F20.imprint","IMPRINT",FACE,{"disambiguationData":[TD([[makeQuery(id+"F20.imprint","IMPRINT",EDGE,{"derivedFrom":sQuery(id+"F20.wireOp",EDGE,"E52.34.0.19")}),1.0]])]});
            var Q36;
            Q36=makeQuery(id+"F20.imprint","IMPRINT",FACE,{"disambiguationData":[TD([[makeQuery(id+"F20.imprint","IMPRINT",EDGE,{"derivedFrom":sQuery(id+"F20.wireOp",EDGE,"E52.37.0.6")}),1.0]])]});
            var Q37;
            Q37=makeQuery(id+"F20.imprint","IMPRINT",FACE,{"disambiguationData":[TD([[makeQuery(id+"F20.imprint","IMPRINT",EDGE,{"derivedFrom":sQuery(id+"F20.wireOp",EDGE,"E52.35.0.26")}),1.0]])]});
            var Q38;
            Q38=makeQuery(id+"F20.imprint","IMPRINT",FACE,{"disambiguationData":[TD([[makeQuery(id+"F20.imprint","IMPRINT",EDGE,{"derivedFrom":sQuery(id+"F20.wireOp",EDGE,"E52.34.0.15")}),1.0]])]});
            var Q39;
            Q39=makeQuery(id+"F20.imprint","IMPRINT",FACE,{"disambiguationData":[TD([[makeQuery(id+"F20.imprint","IMPRINT",EDGE,{"derivedFrom":sQuery(id+"F20.wireOp",EDGE,"E52.37.0.19")}),1.0]])]});
            var Q40;
            Q40=makeQuery(id+"F20.imprint","IMPRINT",FACE,{"disambiguationData":[TD([[makeQuery(id+"F20.imprint","IMPRINT",EDGE,{"derivedFrom":sQuery(id+"F20.wireOp",EDGE,"E52.36.0.10")}),1.0]])]});
            var Q41;
            Q41=makeQuery(id+"F20.imprint","IMPRINT",FACE,{"disambiguationData":[TD([[makeQuery(id+"F20.imprint","IMPRINT",EDGE,{"derivedFrom":sQuery(id+"F20.wireOp",EDGE,"E52.35.0.0")}),1.0]])]});
            var Q42;
            Q42=makeQuery(id+"F20.imprint","IMPRINT",FACE,{"disambiguationData":[TD([[makeQuery(id+"F20.imprint","IMPRINT",EDGE,{"derivedFrom":sQuery(id+"F20.wireOp",EDGE,"E52.35.0.6")}),1.0]])]});
            var Q43;
            Q43=makeQuery(id+"F20.imprint","IMPRINT",FACE,{"disambiguationData":[TD([[makeQuery(id+"F20.imprint","IMPRINT",EDGE,{"derivedFrom":sQuery(id+"F20.wireOp",EDGE,"E52.36.0.19")}),1.0]])]});
            var Q44;
            Q44=makeQuery(id+"F20.imprint","IMPRINT",FACE,{"disambiguationData":[TD([[makeQuery(id+"F20.imprint","IMPRINT",EDGE,{"derivedFrom":sQuery(id+"F20.wireOp",EDGE,"E52.35.0.15")}),1.0]])]});
            var Q45;
            Q45=makeQuery(id+"F20.imprint","IMPRINT",FACE,{"disambiguationData":[TD([[makeQuery(id+"F20.imprint","IMPRINT",EDGE,{"derivedFrom":sQuery(id+"F20.wireOp",EDGE,"E52.34.0.10")}),1.0]])]});
            var Q46;
            Q46=makeQuery(id+"F20.imprint","IMPRINT",FACE,{"disambiguationData":[TD([[makeQuery(id+"F20.imprint","IMPRINT",EDGE,{"derivedFrom":sQuery(id+"F20.wireOp",EDGE,"E52.33.0.26")}),1.0]])]});
            var Q47;
            Q47=makeQuery(id+"F20.imprint","IMPRINT",FACE,{"disambiguationData":[TD([[makeQuery(id+"F20.imprint","IMPRINT",EDGE,{"derivedFrom":sQuery(id+"F20.wireOp",EDGE,"E52.33.0.0")}),1.0]])]});
            extrude(context, id + "F36", {"entities" : qUnion([Q0, Q1, Q2, Q3, Q4, Q5, Q6, Q7, Q8, Q9, Q10, Q11, Q12, Q13, Q14, Q15, Q16, Q17, Q18, Q19, Q20, Q21, Q22, Q23, Q24, Q25, Q26, Q27, Q28, Q29, Q30, Q31, Q32, Q33, Q34, Q35, Q36, Q37, Q38, Q39, Q40, Q41, Q42, Q43, Q44, Q45, Q46, Q47]), "operationType" : NewBodyOperationType.REMOVE, "oppositeDirection" : true, "depth" : 50 * mm, "offsetDistance" : 25 * mm, "symmetric" : true});
        }
        {
            var Q0;
            Q0=makeQuery(id+"F20.imprint","IMPRINT",FACE,{"disambiguationData":[TD([[makeQuery(id+"F20.imprint","IMPRINT",EDGE,{"derivedFrom":sQuery(id+"F20.wireOp",EDGE,"E52.38.0.14")}),1.0]])]});
            var Q1;
            Q1=makeQuery(id+"F20.imprint","IMPRINT",FACE,{"disambiguationData":[TD([[makeQuery(id+"F20.imprint","IMPRINT",EDGE,{"derivedFrom":sQuery(id+"F20.wireOp",EDGE,"E52.37.0.14")}),1.0]])]});
            var Q2;
            Q2=makeQuery(id+"F20.imprint","IMPRINT",FACE,{"disambiguationData":[TD([[makeQuery(id+"F20.imprint","IMPRINT",EDGE,{"derivedFrom":sQuery(id+"F20.wireOp",EDGE,"E52.38.0.23")}),1.0]])]});
            var Q3;
            Q3=makeQuery(id+"F20.imprint","IMPRINT",FACE,{"disambiguationData":[TD([[makeQuery(id+"F20.imprint","IMPRINT",EDGE,{"derivedFrom":sQuery(id+"F20.wireOp",EDGE,"E52.40.0.14")}),1.0]])]});
            var Q4;
            Q4=makeQuery(id+"F20.imprint","IMPRINT",FACE,{"disambiguationData":[TD([[makeQuery(id+"F20.imprint","IMPRINT",EDGE,{"derivedFrom":sQuery(id+"F20.wireOp",EDGE,"E52.39.0.14")}),1.0]])]});
            var Q5;
            Q5=makeQuery(id+"F20.imprint","IMPRINT",FACE,{"disambiguationData":[TD([[makeQuery(id+"F20.imprint","IMPRINT",EDGE,{"derivedFrom":sQuery(id+"F20.wireOp",EDGE,"E52.39.0.26")}),1.0]])]});
            var Q6;
            Q6=makeQuery(id+"F20.imprint","IMPRINT",FACE,{"disambiguationData":[TD([[makeQuery(id+"F20.imprint","IMPRINT",EDGE,{"derivedFrom":sQuery(id+"F20.wireOp",EDGE,"E52.38.0.19")}),1.0]])]});
            var Q7;
            Q7=makeQuery(id+"F20.imprint","IMPRINT",FACE,{"disambiguationData":[TD([[makeQuery(id+"F20.imprint","IMPRINT",EDGE,{"derivedFrom":sQuery(id+"F20.wireOp",EDGE,"E52.41.0.4")}),1.0]])]});
            var Q8;
            Q8=makeQuery(id+"F20.imprint","IMPRINT",FACE,{"disambiguationData":[TD([[makeQuery(id+"F20.imprint","IMPRINT",EDGE,{"derivedFrom":sQuery(id+"F20.wireOp",EDGE,"E52.39.0.23")}),1.0]])]});
            var Q9;
            Q9=makeQuery(id+"F20.imprint","IMPRINT",FACE,{"disambiguationData":[TD([[makeQuery(id+"F20.imprint","IMPRINT",EDGE,{"derivedFrom":sQuery(id+"F20.wireOp",EDGE,"E52.41.0.5")}),1.0]])]});
            var Q10;
            Q10=makeQuery(id+"F20.imprint","IMPRINT",FACE,{"disambiguationData":[TD([[makeQuery(id+"F20.imprint","IMPRINT",EDGE,{"derivedFrom":sQuery(id+"F20.wireOp",EDGE,"E52.39.0.25")}),1.0]])]});
            var Q11;
            Q11=makeQuery(id+"F20.imprint","IMPRINT",FACE,{"disambiguationData":[TD([[makeQuery(id+"F20.imprint","IMPRINT",EDGE,{"derivedFrom":sQuery(id+"F20.wireOp",EDGE,"E52.38.0.15")}),1.0]])]});
            var Q12;
            Q12=makeQuery(id+"F20.imprint","IMPRINT",FACE,{"disambiguationData":[TD([[makeQuery(id+"F20.imprint","IMPRINT",EDGE,{"derivedFrom":sQuery(id+"F20.wireOp",EDGE,"E52.40.0.0")}),1.0]])]});
            var Q13;
            Q13=makeQuery(id+"F20.imprint","IMPRINT",FACE,{"disambiguationData":[TD([[makeQuery(id+"F20.imprint","IMPRINT",EDGE,{"derivedFrom":sQuery(id+"F20.wireOp",EDGE,"E52.38.0.22")}),1.0]])]});
            var Q14;
            Q14=makeQuery(id+"F20.imprint","IMPRINT",FACE,{"disambiguationData":[TD([[makeQuery(id+"F20.imprint","IMPRINT",EDGE,{"derivedFrom":sQuery(id+"F20.wireOp",EDGE,"E52.40.0.4")}),1.0]])]});
            var Q15;
            Q15=makeQuery(id+"F20.imprint","IMPRINT",FACE,{"disambiguationData":[TD([[makeQuery(id+"F20.imprint","IMPRINT",EDGE,{"derivedFrom":sQuery(id+"F20.wireOp",EDGE,"E52.41.0.15")}),1.0]])]});
            var Q16;
            Q16=makeQuery(id+"F20.imprint","IMPRINT",FACE,{"disambiguationData":[TD([[makeQuery(id+"F20.imprint","IMPRINT",EDGE,{"derivedFrom":sQuery(id+"F20.wireOp",EDGE,"E52.40.0.5")}),1.0]])]});
            var Q17;
            Q17=makeQuery(id+"F20.imprint","IMPRINT",FACE,{"disambiguationData":[TD([[makeQuery(id+"F20.imprint","IMPRINT",EDGE,{"derivedFrom":sQuery(id+"F20.wireOp",EDGE,"E52.38.0.25")}),1.0]])]});
            var Q18;
            Q18=makeQuery(id+"F20.imprint","IMPRINT",FACE,{"disambiguationData":[TD([[makeQuery(id+"F20.imprint","IMPRINT",EDGE,{"derivedFrom":sQuery(id+"F20.wireOp",EDGE,"E52.41.0.19")}),1.0]])]});
            var Q19;
            Q19=makeQuery(id+"F20.imprint","IMPRINT",FACE,{"disambiguationData":[TD([[makeQuery(id+"F20.imprint","IMPRINT",EDGE,{"derivedFrom":sQuery(id+"F20.wireOp",EDGE,"E52.40.0.6")}),1.0]])]});
            var Q20;
            Q20=makeQuery(id+"F20.imprint","IMPRINT",FACE,{"disambiguationData":[TD([[makeQuery(id+"F20.imprint","IMPRINT",EDGE,{"derivedFrom":sQuery(id+"F20.wireOp",EDGE,"E52.38.0.26")}),1.0]])]});
            var Q21;
            Q21=makeQuery(id+"F20.imprint","IMPRINT",FACE,{"disambiguationData":[TD([[makeQuery(id+"F20.imprint","IMPRINT",EDGE,{"derivedFrom":sQuery(id+"F20.wireOp",EDGE,"E52.41.0.22")}),1.0]])]});
            var Q22;
            Q22=makeQuery(id+"F20.imprint","IMPRINT",FACE,{"disambiguationData":[TD([[makeQuery(id+"F20.imprint","IMPRINT",EDGE,{"derivedFrom":sQuery(id+"F20.wireOp",EDGE,"E52.40.0.10")}),1.0]])]});
            var Q23;
            Q23=makeQuery(id+"F20.imprint","IMPRINT",FACE,{"disambiguationData":[TD([[makeQuery(id+"F20.imprint","IMPRINT",EDGE,{"derivedFrom":sQuery(id+"F20.wireOp",EDGE,"E52.39.0.0")}),1.0]])]});
            var Q24;
            Q24=makeQuery(id+"F20.imprint","IMPRINT",FACE,{"disambiguationData":[TD([[makeQuery(id+"F20.imprint","IMPRINT",EDGE,{"derivedFrom":sQuery(id+"F20.wireOp",EDGE,"E52.41.0.23")}),1.0]])]});
            var Q25;
            Q25=makeQuery(id+"F20.imprint","IMPRINT",FACE,{"disambiguationData":[TD([[makeQuery(id+"F20.imprint","IMPRINT",EDGE,{"derivedFrom":sQuery(id+"F20.wireOp",EDGE,"E52.39.0.4")}),1.0]])]});
            var Q26;
            Q26=makeQuery(id+"F20.imprint","IMPRINT",FACE,{"disambiguationData":[TD([[makeQuery(id+"F20.imprint","IMPRINT",EDGE,{"derivedFrom":sQuery(id+"F20.wireOp",EDGE,"E52.40.0.15")}),1.0]])]});
            var Q27;
            Q27=makeQuery(id+"F20.imprint","IMPRINT",FACE,{"disambiguationData":[TD([[makeQuery(id+"F20.imprint","IMPRINT",EDGE,{"derivedFrom":sQuery(id+"F20.wireOp",EDGE,"E52.39.0.5")}),1.0]])]});
            var Q28;
            Q28=makeQuery(id+"F20.imprint","IMPRINT",FACE,{"disambiguationData":[TD([[makeQuery(id+"F20.imprint","IMPRINT",EDGE,{"derivedFrom":sQuery(id+"F20.wireOp",EDGE,"E52.41.0.25")}),1.0]])]});
            var Q29;
            Q29=makeQuery(id+"F20.imprint","IMPRINT",FACE,{"disambiguationData":[TD([[makeQuery(id+"F20.imprint","IMPRINT",EDGE,{"derivedFrom":sQuery(id+"F20.wireOp",EDGE,"E52.40.0.19")}),1.0]])]});
            var Q30;
            Q30=makeQuery(id+"F20.imprint","IMPRINT",FACE,{"disambiguationData":[TD([[makeQuery(id+"F20.imprint","IMPRINT",EDGE,{"derivedFrom":sQuery(id+"F20.wireOp",EDGE,"E52.39.0.6")}),1.0]])]});
            var Q31;
            Q31=makeQuery(id+"F20.imprint","IMPRINT",FACE,{"disambiguationData":[TD([[makeQuery(id+"F20.imprint","IMPRINT",EDGE,{"derivedFrom":sQuery(id+"F20.wireOp",EDGE,"E52.40.0.22")}),1.0]])]});
            var Q32;
            Q32=makeQuery(id+"F20.imprint","IMPRINT",FACE,{"disambiguationData":[TD([[makeQuery(id+"F20.imprint","IMPRINT",EDGE,{"derivedFrom":sQuery(id+"F20.wireOp",EDGE,"E52.39.0.10")}),1.0]])]});
            var Q33;
            Q33=makeQuery(id+"F20.imprint","IMPRINT",FACE,{"disambiguationData":[TD([[makeQuery(id+"F20.imprint","IMPRINT",EDGE,{"derivedFrom":sQuery(id+"F20.wireOp",EDGE,"E52.38.0.0")}),1.0]])]});
            var Q34;
            Q34=makeQuery(id+"F20.imprint","IMPRINT",FACE,{"disambiguationData":[TD([[makeQuery(id+"F20.imprint","IMPRINT",EDGE,{"derivedFrom":sQuery(id+"F20.wireOp",EDGE,"E52.40.0.23")}),1.0]])]});
            var Q35;
            Q35=makeQuery(id+"F20.imprint","IMPRINT",FACE,{"disambiguationData":[TD([[makeQuery(id+"F20.imprint","IMPRINT",EDGE,{"derivedFrom":sQuery(id+"F20.wireOp",EDGE,"E52.38.0.4")}),1.0]])]});
            var Q36;
            Q36=makeQuery(id+"F20.imprint","IMPRINT",FACE,{"disambiguationData":[TD([[makeQuery(id+"F20.imprint","IMPRINT",EDGE,{"derivedFrom":sQuery(id+"F20.wireOp",EDGE,"E52.40.0.25")}),1.0]])]});
            var Q37;
            Q37=makeQuery(id+"F20.imprint","IMPRINT",FACE,{"disambiguationData":[TD([[makeQuery(id+"F20.imprint","IMPRINT",EDGE,{"derivedFrom":sQuery(id+"F20.wireOp",EDGE,"E52.39.0.15")}),1.0]])]});
            var Q38;
            Q38=makeQuery(id+"F20.imprint","IMPRINT",FACE,{"disambiguationData":[TD([[makeQuery(id+"F20.imprint","IMPRINT",EDGE,{"derivedFrom":sQuery(id+"F20.wireOp",EDGE,"E52.38.0.5")}),1.0]])]});
            var Q39;
            Q39=makeQuery(id+"F20.imprint","IMPRINT",FACE,{"disambiguationData":[TD([[makeQuery(id+"F20.imprint","IMPRINT",EDGE,{"derivedFrom":sQuery(id+"F20.wireOp",EDGE,"E52.40.0.26")}),1.0]])]});
            var Q40;
            Q40=makeQuery(id+"F20.imprint","IMPRINT",FACE,{"disambiguationData":[TD([[makeQuery(id+"F20.imprint","IMPRINT",EDGE,{"derivedFrom":sQuery(id+"F20.wireOp",EDGE,"E52.39.0.19")}),1.0]])]});
            var Q41;
            Q41=makeQuery(id+"F20.imprint","IMPRINT",FACE,{"disambiguationData":[TD([[makeQuery(id+"F20.imprint","IMPRINT",EDGE,{"derivedFrom":sQuery(id+"F20.wireOp",EDGE,"E52.38.0.6")}),1.0]])]});
            var Q42;
            Q42=makeQuery(id+"F20.imprint","IMPRINT",FACE,{"disambiguationData":[TD([[makeQuery(id+"F20.imprint","IMPRINT",EDGE,{"derivedFrom":sQuery(id+"F20.wireOp",EDGE,"E52.39.0.22")}),1.0]])]});
            var Q43;
            Q43=makeQuery(id+"F20.imprint","IMPRINT",FACE,{"disambiguationData":[TD([[makeQuery(id+"F20.imprint","IMPRINT",EDGE,{"derivedFrom":sQuery(id+"F20.wireOp",EDGE,"E52.38.0.10")}),1.0]])]});
            var Q44;
            Q44=makeQuery(id+"F20.imprint","IMPRINT",FACE,{"disambiguationData":[TD([[makeQuery(id+"F20.imprint","IMPRINT",EDGE,{"derivedFrom":sQuery(id+"F20.wireOp",EDGE,"E52.41.0.6")}),1.0]])]});
            var Q45;
            Q45=makeQuery(id+"F20.imprint","IMPRINT",FACE,{"disambiguationData":[TD([[makeQuery(id+"F20.imprint","IMPRINT",EDGE,{"derivedFrom":sQuery(id+"F20.wireOp",EDGE,"E52.41.0.10")}),1.0]])]});
            var Q46;
            Q46=makeQuery(id+"F20.imprint","IMPRINT",FACE,{"disambiguationData":[TD([[makeQuery(id+"F20.imprint","IMPRINT",EDGE,{"derivedFrom":sQuery(id+"F20.wireOp",EDGE,"E52.37.0.26")}),1.0]])]});
            var Q47;
            Q47=makeQuery(id+"F20.imprint","IMPRINT",FACE,{"disambiguationData":[TD([[makeQuery(id+"F20.imprint","IMPRINT",EDGE,{"derivedFrom":sQuery(id+"F20.wireOp",EDGE,"E52.37.0.0")}),1.0]])]});
            extrude(context, id + "F37", {"entities" : qUnion([Q0, Q1, Q2, Q3, Q4, Q5, Q6, Q7, Q8, Q9, Q10, Q11, Q12, Q13, Q14, Q15, Q16, Q17, Q18, Q19, Q20, Q21, Q22, Q23, Q24, Q25, Q26, Q27, Q28, Q29, Q30, Q31, Q32, Q33, Q34, Q35, Q36, Q37, Q38, Q39, Q40, Q41, Q42, Q43, Q44, Q45, Q46, Q47]), "operationType" : NewBodyOperationType.REMOVE, "depth" : 50 * mm, "offsetDistance" : 25 * mm, "symmetric" : true});
        }
        {
            var Q0;
            Q0=makeQuery(id+"F20.imprint","IMPRINT",FACE,{"disambiguationData":[TD([[makeQuery(id+"F20.imprint","IMPRINT",EDGE,{"derivedFrom":sQuery(id+"F20.wireOp",EDGE,"E52.42.0.14")}),1.0]])]});
            var Q1;
            Q1=makeQuery(id+"F20.imprint","IMPRINT",FACE,{"disambiguationData":[TD([[makeQuery(id+"F20.imprint","IMPRINT",EDGE,{"derivedFrom":sQuery(id+"F20.wireOp",EDGE,"E52.41.0.14")}),1.0]])]});
            var Q2;
            Q2=makeQuery(id+"F20.imprint","IMPRINT",FACE,{"disambiguationData":[TD([[makeQuery(id+"F20.imprint","IMPRINT",EDGE,{"derivedFrom":sQuery(id+"F20.wireOp",EDGE,"E52.44.0.10")}),1.0]])]});
            var Q3;
            Q3=makeQuery(id+"F20.imprint","IMPRINT",FACE,{"disambiguationData":[TD([[makeQuery(id+"F20.imprint","IMPRINT",EDGE,{"derivedFrom":sQuery(id+"F20.wireOp",EDGE,"E52.44.0.14")}),1.0]])]});
            var Q4;
            Q4=makeQuery(id+"F20.imprint","IMPRINT",FACE,{"disambiguationData":[TD([[makeQuery(id+"F20.imprint","IMPRINT",EDGE,{"derivedFrom":sQuery(id+"F20.wireOp",EDGE,"E52.44.0.23")}),1.0]])]});
            var Q5;
            Q5=makeQuery(id+"F20.imprint","IMPRINT",FACE,{"disambiguationData":[TD([[makeQuery(id+"F20.imprint","IMPRINT",EDGE,{"derivedFrom":sQuery(id+"F20.wireOp",EDGE,"E52.43.0.14")}),1.0]])]});
            var Q6;
            Q6=makeQuery(id+"F20.imprint","IMPRINT",FACE,{"disambiguationData":[TD([[makeQuery(id+"F20.imprint","IMPRINT",EDGE,{"derivedFrom":sQuery(id+"F20.wireOp",EDGE,"E52.45.0.6")}),1.0]])]});
            var Q7;
            Q7=makeQuery(id+"F20.imprint","IMPRINT",FACE,{"disambiguationData":[TD([[makeQuery(id+"F20.imprint","IMPRINT",EDGE,{"derivedFrom":sQuery(id+"F20.wireOp",EDGE,"E52.43.0.26")}),1.0]])]});
            var Q8;
            Q8=makeQuery(id+"F20.imprint","IMPRINT",FACE,{"disambiguationData":[TD([[makeQuery(id+"F20.imprint","IMPRINT",EDGE,{"derivedFrom":sQuery(id+"F20.wireOp",EDGE,"E52.45.0.4")}),1.0]])]});
            var Q9;
            Q9=makeQuery(id+"F20.imprint","IMPRINT",FACE,{"disambiguationData":[TD([[makeQuery(id+"F20.imprint","IMPRINT",EDGE,{"derivedFrom":sQuery(id+"F20.wireOp",EDGE,"E52.43.0.23")}),1.0]])]});
            var Q10;
            Q10=makeQuery(id+"F20.imprint","IMPRINT",FACE,{"disambiguationData":[TD([[makeQuery(id+"F20.imprint","IMPRINT",EDGE,{"derivedFrom":sQuery(id+"F20.wireOp",EDGE,"E52.42.0.15")}),1.0]])]});
            var Q11;
            Q11=makeQuery(id+"F20.imprint","IMPRINT",FACE,{"disambiguationData":[TD([[makeQuery(id+"F20.imprint","IMPRINT",EDGE,{"derivedFrom":sQuery(id+"F20.wireOp",EDGE,"E52.45.0.5")}),1.0]])]});
            var Q12;
            Q12=makeQuery(id+"F20.imprint","IMPRINT",FACE,{"disambiguationData":[TD([[makeQuery(id+"F20.imprint","IMPRINT",EDGE,{"derivedFrom":sQuery(id+"F20.wireOp",EDGE,"E52.43.0.25")}),1.0]])]});
            var Q13;
            Q13=makeQuery(id+"F20.imprint","IMPRINT",FACE,{"disambiguationData":[TD([[makeQuery(id+"F20.imprint","IMPRINT",EDGE,{"derivedFrom":sQuery(id+"F20.wireOp",EDGE,"E52.42.0.22")}),1.0]])]});
            var Q14;
            Q14=makeQuery(id+"F20.imprint","IMPRINT",FACE,{"disambiguationData":[TD([[makeQuery(id+"F20.imprint","IMPRINT",EDGE,{"derivedFrom":sQuery(id+"F20.wireOp",EDGE,"E52.45.0.10")}),1.0]])]});
            var Q15;
            Q15=makeQuery(id+"F20.imprint","IMPRINT",FACE,{"disambiguationData":[TD([[makeQuery(id+"F20.imprint","IMPRINT",EDGE,{"derivedFrom":sQuery(id+"F20.wireOp",EDGE,"E52.44.0.0")}),1.0]])]});
            var Q16;
            Q16=makeQuery(id+"F20.imprint","IMPRINT",FACE,{"disambiguationData":[TD([[makeQuery(id+"F20.imprint","IMPRINT",EDGE,{"derivedFrom":sQuery(id+"F20.wireOp",EDGE,"E52.42.0.23")}),1.0]])]});
            var Q17;
            Q17=makeQuery(id+"F20.imprint","IMPRINT",FACE,{"disambiguationData":[TD([[makeQuery(id+"F20.imprint","IMPRINT",EDGE,{"derivedFrom":sQuery(id+"F20.wireOp",EDGE,"E52.44.0.4")}),1.0]])]});
            var Q18;
            Q18=makeQuery(id+"F20.imprint","IMPRINT",FACE,{"disambiguationData":[TD([[makeQuery(id+"F20.imprint","IMPRINT",EDGE,{"derivedFrom":sQuery(id+"F20.wireOp",EDGE,"E52.42.0.25")}),1.0]])]});
            var Q19;
            Q19=makeQuery(id+"F20.imprint","IMPRINT",FACE,{"disambiguationData":[TD([[makeQuery(id+"F20.imprint","IMPRINT",EDGE,{"derivedFrom":sQuery(id+"F20.wireOp",EDGE,"E52.45.0.15")}),1.0]])]});
            var Q20;
            Q20=makeQuery(id+"F20.imprint","IMPRINT",FACE,{"disambiguationData":[TD([[makeQuery(id+"F20.imprint","IMPRINT",EDGE,{"derivedFrom":sQuery(id+"F20.wireOp",EDGE,"E52.44.0.5")}),1.0]])]});
            var Q21;
            Q21=makeQuery(id+"F20.imprint","IMPRINT",FACE,{"disambiguationData":[TD([[makeQuery(id+"F20.imprint","IMPRINT",EDGE,{"derivedFrom":sQuery(id+"F20.wireOp",EDGE,"E52.42.0.26")}),1.0]])]});
            var Q22;
            Q22=makeQuery(id+"F20.imprint","IMPRINT",FACE,{"disambiguationData":[TD([[makeQuery(id+"F20.imprint","IMPRINT",EDGE,{"derivedFrom":sQuery(id+"F20.wireOp",EDGE,"E52.45.0.19")}),1.0]])]});
            var Q23;
            Q23=makeQuery(id+"F20.imprint","IMPRINT",FACE,{"disambiguationData":[TD([[makeQuery(id+"F20.imprint","IMPRINT",EDGE,{"derivedFrom":sQuery(id+"F20.wireOp",EDGE,"E52.44.0.6")}),1.0]])]});
            var Q24;
            Q24=makeQuery(id+"F20.imprint","IMPRINT",FACE,{"disambiguationData":[TD([[makeQuery(id+"F20.imprint","IMPRINT",EDGE,{"derivedFrom":sQuery(id+"F20.wireOp",EDGE,"E52.43.0.0")}),1.0]])]});
            var Q25;
            Q25=makeQuery(id+"F20.imprint","IMPRINT",FACE,{"disambiguationData":[TD([[makeQuery(id+"F20.imprint","IMPRINT",EDGE,{"derivedFrom":sQuery(id+"F20.wireOp",EDGE,"E52.45.0.22")}),1.0]])]});
            var Q26;
            Q26=makeQuery(id+"F20.imprint","IMPRINT",FACE,{"disambiguationData":[TD([[makeQuery(id+"F20.imprint","IMPRINT",EDGE,{"derivedFrom":sQuery(id+"F20.wireOp",EDGE,"E52.43.0.4")}),1.0]])]});
            var Q27;
            Q27=makeQuery(id+"F20.imprint","IMPRINT",FACE,{"disambiguationData":[TD([[makeQuery(id+"F20.imprint","IMPRINT",EDGE,{"derivedFrom":sQuery(id+"F20.wireOp",EDGE,"E52.45.0.23")}),1.0]])]});
            var Q28;
            Q28=makeQuery(id+"F20.imprint","IMPRINT",FACE,{"disambiguationData":[TD([[makeQuery(id+"F20.imprint","IMPRINT",EDGE,{"derivedFrom":sQuery(id+"F20.wireOp",EDGE,"E52.45.0.25")}),1.0]])]});
            var Q29;
            Q29=makeQuery(id+"F20.imprint","IMPRINT",FACE,{"disambiguationData":[TD([[makeQuery(id+"F20.imprint","IMPRINT",EDGE,{"derivedFrom":sQuery(id+"F20.wireOp",EDGE,"E52.44.0.15")}),1.0]])]});
            var Q30;
            Q30=makeQuery(id+"F20.imprint","IMPRINT",FACE,{"disambiguationData":[TD([[makeQuery(id+"F20.imprint","IMPRINT",EDGE,{"derivedFrom":sQuery(id+"F20.wireOp",EDGE,"E52.43.0.5")}),1.0]])]});
            var Q31;
            Q31=makeQuery(id+"F20.imprint","IMPRINT",FACE,{"disambiguationData":[TD([[makeQuery(id+"F20.imprint","IMPRINT",EDGE,{"derivedFrom":sQuery(id+"F20.wireOp",EDGE,"E52.44.0.19")}),1.0]])]});
            var Q32;
            Q32=makeQuery(id+"F20.imprint","IMPRINT",FACE,{"disambiguationData":[TD([[makeQuery(id+"F20.imprint","IMPRINT",EDGE,{"derivedFrom":sQuery(id+"F20.wireOp",EDGE,"E52.43.0.6")}),1.0]])]});
            var Q33;
            Q33=makeQuery(id+"F20.imprint","IMPRINT",FACE,{"disambiguationData":[TD([[makeQuery(id+"F20.imprint","IMPRINT",EDGE,{"derivedFrom":sQuery(id+"F20.wireOp",EDGE,"E52.44.0.22")}),1.0]])]});
            var Q34;
            Q34=makeQuery(id+"F20.imprint","IMPRINT",FACE,{"disambiguationData":[TD([[makeQuery(id+"F20.imprint","IMPRINT",EDGE,{"derivedFrom":sQuery(id+"F20.wireOp",EDGE,"E52.43.0.10")}),1.0]])]});
            var Q35;
            Q35=makeQuery(id+"F20.imprint","IMPRINT",FACE,{"disambiguationData":[TD([[makeQuery(id+"F20.imprint","IMPRINT",EDGE,{"derivedFrom":sQuery(id+"F20.wireOp",EDGE,"E52.42.0.0")}),1.0]])]});
            var Q36;
            Q36=makeQuery(id+"F20.imprint","IMPRINT",FACE,{"disambiguationData":[TD([[makeQuery(id+"F20.imprint","IMPRINT",EDGE,{"derivedFrom":sQuery(id+"F20.wireOp",EDGE,"E52.42.0.4")}),1.0]])]});
            var Q37;
            Q37=makeQuery(id+"F20.imprint","IMPRINT",FACE,{"disambiguationData":[TD([[makeQuery(id+"F20.imprint","IMPRINT",EDGE,{"derivedFrom":sQuery(id+"F20.wireOp",EDGE,"E52.44.0.25")}),1.0]])]});
            var Q38;
            Q38=makeQuery(id+"F20.imprint","IMPRINT",FACE,{"disambiguationData":[TD([[makeQuery(id+"F20.imprint","IMPRINT",EDGE,{"derivedFrom":sQuery(id+"F20.wireOp",EDGE,"E52.43.0.15")}),1.0]])]});
            var Q39;
            Q39=makeQuery(id+"F20.imprint","IMPRINT",FACE,{"disambiguationData":[TD([[makeQuery(id+"F20.imprint","IMPRINT",EDGE,{"derivedFrom":sQuery(id+"F20.wireOp",EDGE,"E52.42.0.5")}),1.0]])]});
            var Q40;
            Q40=makeQuery(id+"F20.imprint","IMPRINT",FACE,{"disambiguationData":[TD([[makeQuery(id+"F20.imprint","IMPRINT",EDGE,{"derivedFrom":sQuery(id+"F20.wireOp",EDGE,"E52.44.0.26")}),1.0]])]});
            var Q41;
            Q41=makeQuery(id+"F20.imprint","IMPRINT",FACE,{"disambiguationData":[TD([[makeQuery(id+"F20.imprint","IMPRINT",EDGE,{"derivedFrom":sQuery(id+"F20.wireOp",EDGE,"E52.43.0.19")}),1.0]])]});
            var Q42;
            Q42=makeQuery(id+"F20.imprint","IMPRINT",FACE,{"disambiguationData":[TD([[makeQuery(id+"F20.imprint","IMPRINT",EDGE,{"derivedFrom":sQuery(id+"F20.wireOp",EDGE,"E52.42.0.6")}),1.0]])]});
            var Q43;
            Q43=makeQuery(id+"F20.imprint","IMPRINT",FACE,{"disambiguationData":[TD([[makeQuery(id+"F20.imprint","IMPRINT",EDGE,{"derivedFrom":sQuery(id+"F20.wireOp",EDGE,"E52.43.0.22")}),1.0]])]});
            var Q44;
            Q44=makeQuery(id+"F20.imprint","IMPRINT",FACE,{"disambiguationData":[TD([[makeQuery(id+"F20.imprint","IMPRINT",EDGE,{"derivedFrom":sQuery(id+"F20.wireOp",EDGE,"E52.42.0.10")}),1.0]])]});
            var Q45;
            Q45=makeQuery(id+"F20.imprint","IMPRINT",FACE,{"disambiguationData":[TD([[makeQuery(id+"F20.imprint","IMPRINT",EDGE,{"derivedFrom":sQuery(id+"F20.wireOp",EDGE,"E52.42.0.19")}),1.0]])]});
            var Q46;
            Q46=makeQuery(id+"F20.imprint","IMPRINT",FACE,{"disambiguationData":[TD([[makeQuery(id+"F20.imprint","IMPRINT",EDGE,{"derivedFrom":sQuery(id+"F20.wireOp",EDGE,"E52.41.0.26")}),1.0]])]});
            var Q47;
            Q47=makeQuery(id+"F20.imprint","IMPRINT",FACE,{"disambiguationData":[TD([[makeQuery(id+"F20.imprint","IMPRINT",EDGE,{"derivedFrom":sQuery(id+"F20.wireOp",EDGE,"E52.41.0.0")}),1.0]])]});
            extrude(context, id + "F38", {"entities" : qUnion([Q0, Q1, Q2, Q3, Q4, Q5, Q6, Q7, Q8, Q9, Q10, Q11, Q12, Q13, Q14, Q15, Q16, Q17, Q18, Q19, Q20, Q21, Q22, Q23, Q24, Q25, Q26, Q27, Q28, Q29, Q30, Q31, Q32, Q33, Q34, Q35, Q36, Q37, Q38, Q39, Q40, Q41, Q42, Q43, Q44, Q45, Q46, Q47]), "operationType" : NewBodyOperationType.REMOVE, "depth" : 50 * mm, "offsetDistance" : 25 * mm, "symmetric" : true});
        }
        {
            var Q0;
            Q0=makeQuery(id+"F20.imprint","IMPRINT",FACE,{"disambiguationData":[TD([[makeQuery(id+"F20.imprint","IMPRINT",EDGE,{"derivedFrom":sQuery(id+"F20.wireOp",EDGE,"E52.47.0.26")}),1.0]])]});
            var Q1;
            Q1=makeQuery(id+"F20.imprint","IMPRINT",FACE,{"disambiguationData":[TD([[makeQuery(id+"F20.imprint","IMPRINT",EDGE,{"derivedFrom":sQuery(id+"F20.wireOp",EDGE,"E52.46.0.19")}),1.0]])]});
            var Q2;
            Q2=makeQuery(id+"F20.imprint","IMPRINT",FACE,{"disambiguationData":[TD([[makeQuery(id+"F20.imprint","IMPRINT",EDGE,{"derivedFrom":sQuery(id+"F20.wireOp",EDGE,"E52.47.0.23")}),1.0]])]});
            var Q3;
            Q3=makeQuery(id+"F20.imprint","IMPRINT",FACE,{"disambiguationData":[TD([[makeQuery(id+"F20.imprint","IMPRINT",EDGE,{"derivedFrom":sQuery(id+"F20.wireOp",EDGE,"E52.46.0.14")}),1.0]])]});
            var Q4;
            Q4=makeQuery(id+"F20.imprint","IMPRINT",FACE,{"disambiguationData":[TD([[makeQuery(id+"F20.imprint","IMPRINT",EDGE,{"derivedFrom":sQuery(id+"F20.wireOp",EDGE,"E52.47.0.25")}),1.0]])]});
            var Q5;
            Q5=makeQuery(id+"F20.imprint","IMPRINT",FACE,{"disambiguationData":[TD([[makeQuery(id+"F20.imprint","IMPRINT",EDGE,{"derivedFrom":sQuery(id+"F20.wireOp",EDGE,"E52.49.0.5")}),1.0]])]});
            var Q6;
            Q6=makeQuery(id+"F20.imprint","IMPRINT",FACE,{"disambiguationData":[TD([[makeQuery(id+"F20.imprint","IMPRINT",EDGE,{"derivedFrom":sQuery(id+"F20.wireOp",EDGE,"E52.48.0.0")}),1.0]])]});
            var Q7;
            Q7=makeQuery(id+"F20.imprint","IMPRINT",FACE,{"disambiguationData":[TD([[makeQuery(id+"F20.imprint","IMPRINT",EDGE,{"derivedFrom":sQuery(id+"F20.wireOp",EDGE,"E52.46.0.22")}),1.0]])]});
            var Q8;
            Q8=makeQuery(id+"F20.imprint","IMPRINT",FACE,{"disambiguationData":[TD([[makeQuery(id+"F20.imprint","IMPRINT",EDGE,{"derivedFrom":sQuery(id+"F20.wireOp",EDGE,"E52.48.0.4")}),1.0]])]});
            var Q9;
            Q9=makeQuery(id+"F20.imprint","IMPRINT",FACE,{"disambiguationData":[TD([[makeQuery(id+"F20.imprint","IMPRINT",EDGE,{"derivedFrom":sQuery(id+"F20.wireOp",EDGE,"E52.45.0.14")}),1.0]])]});
            var Q10;
            Q10=makeQuery(id+"F20.imprint","IMPRINT",FACE,{"disambiguationData":[TD([[makeQuery(id+"F20.imprint","IMPRINT",EDGE,{"derivedFrom":sQuery(id+"F20.wireOp",EDGE,"E52.48.0.5")}),1.0]])]});
            var Q11;
            Q11=makeQuery(id+"F20.imprint","IMPRINT",FACE,{"disambiguationData":[TD([[makeQuery(id+"F20.imprint","IMPRINT",EDGE,{"derivedFrom":sQuery(id+"F20.wireOp",EDGE,"E52.46.0.25")}),1.0]])]});
            var Q12;
            Q12=makeQuery(id+"F20.imprint","IMPRINT",FACE,{"disambiguationData":[TD([[makeQuery(id+"F20.imprint","IMPRINT",EDGE,{"derivedFrom":sQuery(id+"F20.wireOp",EDGE,"E52.46.0.26")}),1.0]])]});
            var Q13;
            Q13=makeQuery(id+"F20.imprint","IMPRINT",FACE,{"disambiguationData":[TD([[makeQuery(id+"F20.imprint","IMPRINT",EDGE,{"derivedFrom":sQuery(id+"F20.wireOp",EDGE,"E52.47.0.0")}),1.0]])]});
            var Q14;
            Q14=makeQuery(id+"F20.imprint","IMPRINT",FACE,{"disambiguationData":[TD([[makeQuery(id+"F20.imprint","IMPRINT",EDGE,{"derivedFrom":sQuery(id+"F20.wireOp",EDGE,"E52.48.0.14")}),1.0]])]});
            var Q15;
            Q15=makeQuery(id+"F20.imprint","IMPRINT",FACE,{"disambiguationData":[TD([[makeQuery(id+"F20.imprint","IMPRINT",EDGE,{"derivedFrom":sQuery(id+"F20.wireOp",EDGE,"E52.47.0.4")}),1.0]])]});
            var Q16;
            Q16=makeQuery(id+"F20.imprint","IMPRINT",FACE,{"disambiguationData":[TD([[makeQuery(id+"F20.imprint","IMPRINT",EDGE,{"derivedFrom":sQuery(id+"F20.wireOp",EDGE,"E52.49.0.23")}),1.0]])]});
            var Q17;
            Q17=makeQuery(id+"F20.imprint","IMPRINT",FACE,{"disambiguationData":[TD([[makeQuery(id+"F20.imprint","IMPRINT",EDGE,{"derivedFrom":sQuery(id+"F20.wireOp",EDGE,"E52.49.0.25")}),1.0]])]});
            var Q18;
            Q18=makeQuery(id+"F20.imprint","IMPRINT",FACE,{"disambiguationData":[TD([[makeQuery(id+"F20.imprint","IMPRINT",EDGE,{"derivedFrom":sQuery(id+"F20.wireOp",EDGE,"E52.48.0.15")}),1.0]])]});
            var Q19;
            Q19=makeQuery(id+"F20.imprint","IMPRINT",FACE,{"disambiguationData":[TD([[makeQuery(id+"F20.imprint","IMPRINT",EDGE,{"derivedFrom":sQuery(id+"F20.wireOp",EDGE,"E52.47.0.5")}),1.0]])]});
            var Q20;
            Q20=makeQuery(id+"F20.imprint","IMPRINT",FACE,{"disambiguationData":[TD([[makeQuery(id+"F20.imprint","IMPRINT",EDGE,{"derivedFrom":sQuery(id+"F20.wireOp",EDGE,"E52.46.0.0")}),1.0]])]});
            var Q21;
            Q21=makeQuery(id+"F20.imprint","IMPRINT",FACE,{"disambiguationData":[TD([[makeQuery(id+"F20.imprint","IMPRINT",EDGE,{"derivedFrom":sQuery(id+"F20.wireOp",EDGE,"E52.46.0.4")}),1.0]])]});
            var Q22;
            Q22=makeQuery(id+"F20.imprint","IMPRINT",FACE,{"disambiguationData":[TD([[makeQuery(id+"F20.imprint","IMPRINT",EDGE,{"derivedFrom":sQuery(id+"F20.wireOp",EDGE,"E52.48.0.23")}),1.0]])]});
            var Q23;
            Q23=makeQuery(id+"F20.imprint","IMPRINT",FACE,{"disambiguationData":[TD([[makeQuery(id+"F20.imprint","IMPRINT",EDGE,{"derivedFrom":sQuery(id+"F20.wireOp",EDGE,"E52.47.0.14")}),1.0]])]});
            var Q24;
            Q24=makeQuery(id+"F20.imprint","IMPRINT",FACE,{"disambiguationData":[TD([[makeQuery(id+"F20.imprint","IMPRINT",EDGE,{"derivedFrom":sQuery(id+"F20.wireOp",EDGE,"E52.46.0.5")}),1.0]])]});
            var Q25;
            Q25=makeQuery(id+"F20.imprint","IMPRINT",FACE,{"disambiguationData":[TD([[makeQuery(id+"F20.imprint","IMPRINT",EDGE,{"derivedFrom":sQuery(id+"F20.wireOp",EDGE,"E52.48.0.25")}),1.0]])]});
            var Q26;
            Q26=makeQuery(id+"F20.imprint","IMPRINT",FACE,{"disambiguationData":[TD([[makeQuery(id+"F20.imprint","IMPRINT",EDGE,{"derivedFrom":sQuery(id+"F20.wireOp",EDGE,"E52.48.0.26")}),1.0]])]});
            var Q27;
            Q27=makeQuery(id+"F20.imprint","IMPRINT",FACE,{"disambiguationData":[TD([[makeQuery(id+"F20.imprint","IMPRINT",EDGE,{"derivedFrom":sQuery(id+"F20.wireOp",EDGE,"E52.47.0.22")}),1.0]])]});
            var Q28;
            Q28=makeQuery(id+"F20.imprint","IMPRINT",FACE,{"disambiguationData":[TD([[makeQuery(id+"F20.imprint","IMPRINT",EDGE,{"derivedFrom":sQuery(id+"F20.wireOp",EDGE,"E52.49.0.6")}),1.0]])]});
            var Q29;
            Q29=makeQuery(id+"F20.imprint","IMPRINT",FACE,{"disambiguationData":[TD([[makeQuery(id+"F20.imprint","IMPRINT",EDGE,{"derivedFrom":sQuery(id+"F20.wireOp",EDGE,"E52.49.0.4")}),1.0]])]});
            var Q30;
            Q30=makeQuery(id+"F20.imprint","IMPRINT",FACE,{"disambiguationData":[TD([[makeQuery(id+"F20.imprint","IMPRINT",EDGE,{"derivedFrom":sQuery(id+"F20.wireOp",EDGE,"E52.46.0.15")}),1.0]])]});
            var Q31;
            Q31=makeQuery(id+"F20.imprint","IMPRINT",FACE,{"disambiguationData":[TD([[makeQuery(id+"F20.imprint","IMPRINT",EDGE,{"derivedFrom":sQuery(id+"F20.wireOp",EDGE,"E52.49.0.10")}),1.0]])]});
            var Q32;
            Q32=makeQuery(id+"F20.imprint","IMPRINT",FACE,{"disambiguationData":[TD([[makeQuery(id+"F20.imprint","IMPRINT",EDGE,{"derivedFrom":sQuery(id+"F20.wireOp",EDGE,"E52.46.0.23")}),1.0]])]});
            var Q33;
            Q33=makeQuery(id+"F20.imprint","IMPRINT",FACE,{"disambiguationData":[TD([[makeQuery(id+"F20.imprint","IMPRINT",EDGE,{"derivedFrom":sQuery(id+"F20.wireOp",EDGE,"E52.49.0.15")}),1.0]])]});
            var Q34;
            Q34=makeQuery(id+"F20.imprint","IMPRINT",FACE,{"disambiguationData":[TD([[makeQuery(id+"F20.imprint","IMPRINT",EDGE,{"derivedFrom":sQuery(id+"F20.wireOp",EDGE,"E52.48.0.6")}),1.0]])]});
            var Q35;
            Q35=makeQuery(id+"F20.imprint","IMPRINT",FACE,{"disambiguationData":[TD([[makeQuery(id+"F20.imprint","IMPRINT",EDGE,{"derivedFrom":sQuery(id+"F20.wireOp",EDGE,"E52.49.0.19")}),1.0]])]});
            var Q36;
            Q36=makeQuery(id+"F20.imprint","IMPRINT",FACE,{"disambiguationData":[TD([[makeQuery(id+"F20.imprint","IMPRINT",EDGE,{"derivedFrom":sQuery(id+"F20.wireOp",EDGE,"E52.48.0.10")}),1.0]])]});
            var Q37;
            Q37=makeQuery(id+"F20.imprint","IMPRINT",FACE,{"disambiguationData":[TD([[makeQuery(id+"F20.imprint","IMPRINT",EDGE,{"derivedFrom":sQuery(id+"F20.wireOp",EDGE,"E52.49.0.22")}),1.0]])]});
            var Q38;
            Q38=makeQuery(id+"F20.imprint","IMPRINT",FACE,{"disambiguationData":[TD([[makeQuery(id+"F20.imprint","IMPRINT",EDGE,{"derivedFrom":sQuery(id+"F20.wireOp",EDGE,"E52.45.0.26")}),1.0]])]});
            var Q39;
            Q39=makeQuery(id+"F20.imprint","IMPRINT",FACE,{"disambiguationData":[TD([[makeQuery(id+"F20.imprint","IMPRINT",EDGE,{"derivedFrom":sQuery(id+"F20.wireOp",EDGE,"E52.48.0.19")}),1.0]])]});
            var Q40;
            Q40=makeQuery(id+"F20.imprint","IMPRINT",FACE,{"disambiguationData":[TD([[makeQuery(id+"F20.imprint","IMPRINT",EDGE,{"derivedFrom":sQuery(id+"F20.wireOp",EDGE,"E52.47.0.6")}),1.0]])]});
            var Q41;
            Q41=makeQuery(id+"F20.imprint","IMPRINT",FACE,{"disambiguationData":[TD([[makeQuery(id+"F20.imprint","IMPRINT",EDGE,{"derivedFrom":sQuery(id+"F20.wireOp",EDGE,"E52.48.0.22")}),1.0]])]});
            var Q42;
            Q42=makeQuery(id+"F20.imprint","IMPRINT",FACE,{"disambiguationData":[TD([[makeQuery(id+"F20.imprint","IMPRINT",EDGE,{"derivedFrom":sQuery(id+"F20.wireOp",EDGE,"E52.47.0.10")}),1.0]])]});
            var Q43;
            Q43=makeQuery(id+"F20.imprint","IMPRINT",FACE,{"disambiguationData":[TD([[makeQuery(id+"F20.imprint","IMPRINT",EDGE,{"derivedFrom":sQuery(id+"F20.wireOp",EDGE,"E52.47.0.15")}),1.0]])]});
            var Q44;
            Q44=makeQuery(id+"F20.imprint","IMPRINT",FACE,{"disambiguationData":[TD([[makeQuery(id+"F20.imprint","IMPRINT",EDGE,{"derivedFrom":sQuery(id+"F20.wireOp",EDGE,"E52.46.0.6")}),1.0]])]});
            var Q45;
            Q45=makeQuery(id+"F20.imprint","IMPRINT",FACE,{"disambiguationData":[TD([[makeQuery(id+"F20.imprint","IMPRINT",EDGE,{"derivedFrom":sQuery(id+"F20.wireOp",EDGE,"E52.47.0.19")}),1.0]])]});
            var Q46;
            Q46=makeQuery(id+"F20.imprint","IMPRINT",FACE,{"disambiguationData":[TD([[makeQuery(id+"F20.imprint","IMPRINT",EDGE,{"derivedFrom":sQuery(id+"F20.wireOp",EDGE,"E52.46.0.10")}),1.0]])]});
            var Q47;
            Q47=makeQuery(id+"F20.imprint","IMPRINT",FACE,{"disambiguationData":[TD([[makeQuery(id+"F20.imprint","IMPRINT",EDGE,{"derivedFrom":sQuery(id+"F20.wireOp",EDGE,"E52.45.0.0")}),1.0]])]});
            extrude(context, id + "F39", {"entities" : qUnion([Q0, Q1, Q2, Q3, Q4, Q5, Q6, Q7, Q8, Q9, Q10, Q11, Q12, Q13, Q14, Q15, Q16, Q17, Q18, Q19, Q20, Q21, Q22, Q23, Q24, Q25, Q26, Q27, Q28, Q29, Q30, Q31, Q32, Q33, Q34, Q35, Q36, Q37, Q38, Q39, Q40, Q41, Q42, Q43, Q44, Q45, Q46, Q47]), "operationType" : NewBodyOperationType.REMOVE, "depth" : 50 * mm, "offsetDistance" : 25 * mm, "symmetric" : true});
        }
        {
            var Q0;
            Q0=qCreatedBy(makeId("Top.planeOp"),FACE);
            var sketch = newSketch(context, id + "F40", { "sketchPlane" : qUnion([Q0])});
            skPoint(sketch, "E53.0", {"position": v(0, 24) * mm});
            skPoint(sketch, "E54.0", {"position": v(0, -24) * mm});
            skLineSegment(sketch, "E55", {"start": v(0, 24) * mm, "end": v(24, 0) * mm, "construction": true});
            skLineSegment(sketch, "E56", {"start": v(24, 0) * mm, "end": v(0, -24) * mm, "construction": true});
            skCircle(sketch, "E57", {"center": v(8, 16) * mm, "radius": 2 * mm});
            skArc(sketch, "E58", {"start": v(16.93, 9.9) * mm, "mid": v(14.1, 9.9) * mm, "end": v(14.1, 7.07) * mm});
            skArc(sketch, "E59", {"start": v(14.59, 6.59) * mm, "mid": v(17.41, 6.59) * mm, "end": v(17.41, 9.41) * mm});
            skCircle(sketch, "E60", {"center": v(8, -16) * mm, "radius": 2 * mm});
            skArc(sketch, "E61", {"start": v(17.41, -9.41) * mm, "mid": v(17.41, -6.59) * mm, "end": v(14.59, -6.59) * mm});
            skArc(sketch, "E62", {"start": v(14.1, -7.07) * mm, "mid": v(14.1, -9.9) * mm, "end": v(16.93, -9.9) * mm});
            skLineSegment(sketch, "E63", {"start": v(14.1, -7.07) * mm, "end": v(16.93, -9.9) * mm, "construction": true});
            skLineSegment(sketch, "E64", {"start": v(14.59, -6.59) * mm, "end": v(17.41, -9.41) * mm, "construction": true});
            skLineSegment(sketch, "E65", {"start": v(14.1, -7.07) * mm, "end": v(14.59, -6.59) * mm});
            skLineSegment(sketch, "E66", {"start": v(16.93, -9.9) * mm, "end": v(17.41, -9.41) * mm});
            skLineSegment(sketch, "E67", {"start": v(16.93, 9.9) * mm, "end": v(14.1, 7.07) * mm, "construction": true});
            skLineSegment(sketch, "E68", {"start": v(14.59, 6.59) * mm, "end": v(17.41, 9.41) * mm, "construction": true});
            skLineSegment(sketch, "E69", {"start": v(14.1, 7.07) * mm, "end": v(14.59, 6.59) * mm});
            skLineSegment(sketch, "E70", {"start": v(16.93, 9.9) * mm, "end": v(17.41, 9.41) * mm});
            skLineSegment(sketch, "E71", {"start": v(8, 16) * mm, "end": v(16, 16) * mm, "construction": true});
            skLineSegment(sketch, "E72", {"start": v(8, -16) * mm, "end": v(16, -16) * mm, "construction": true});
            skCircle(sketch, "E73", {"center": v(16, -16) * mm, "radius": 2 * mm});
            skCircle(sketch, "E74", {"center": v(12, 0) * mm, "radius": 2 * mm});
            skCircle(sketch, "E75", {"center": v(16, 16) * mm, "radius": 2 * mm});
            skLineSegment(sketch, "E76.bottom", {"start": v(0, 24) * mm, "end": v(24, 24) * mm, "construction": true});
            skLineSegment(sketch, "E76.top", {"start": v(0, 0) * mm, "end": v(24, 0) * mm, "construction": true});
            skLineSegment(sketch, "E76.left", {"start": v(0, 24) * mm, "end": v(0, 0) * mm, "construction": true});
            skLineSegment(sketch, "E76.right", {"start": v(24, 24) * mm, "end": v(24, 0) * mm, "construction": true});
            skLineSegment(sketch, "E77.bottom", {"start": v(24, 0) * mm, "end": v(0, 0) * mm, "construction": true});
            skLineSegment(sketch, "E77.top", {"start": v(24, -24) * mm, "end": v(0, -24) * mm, "construction": true});
            skLineSegment(sketch, "E77.left", {"start": v(24, 0) * mm, "end": v(24, -24) * mm, "construction": true});
            skLineSegment(sketch, "E77.right", {"start": v(0, 0) * mm, "end": v(0, -24) * mm, "construction": true});
            skLineSegment(sketch, "E78", {"start": v(24, 24) * mm, "end": v(0, 0) * mm, "construction": true});
            skLineSegment(sketch, "E79", {"start": v(24, -24) * mm, "end": v(0, 0) * mm, "construction": true});
            skArc(sketch, "E80", {"start": v(7.07, -9.9) * mm, "mid": v(9.9, -9.9) * mm, "end": v(9.9, -7.07) * mm});
            skArc(sketch, "E81", {"start": v(9.9, 7.07) * mm, "mid": v(9.9, 9.9) * mm, "end": v(7.07, 9.9) * mm});
            skArc(sketch, "E82", {"start": v(6.59, 9.41) * mm, "mid": v(6.59, 6.59) * mm, "end": v(9.41, 6.59) * mm});
            skLineSegment(sketch, "E83", {"start": v(7.07, 9.9) * mm, "end": v(9.9, 7.07) * mm, "construction": true});
            skLineSegment(sketch, "E84", {"start": v(6.59, 9.41) * mm, "end": v(9.41, 6.59) * mm, "construction": true});
            skLineSegment(sketch, "E85", {"start": v(7.07, -9.9) * mm, "end": v(9.9, -7.07) * mm, "construction": true});
            skLineSegment(sketch, "E86", {"start": v(9.41, -6.59) * mm, "end": v(6.59, -9.41) * mm, "construction": true});
            skLineSegment(sketch, "E87", {"start": v(9.41, -6.59) * mm, "end": v(9.9, -7.07) * mm});
            skLineSegment(sketch, "E88", {"start": v(6.59, -9.41) * mm, "end": v(7.07, -9.9) * mm});
            skLineSegment(sketch, "E89", {"start": v(6.59, 9.41) * mm, "end": v(7.07, 9.9) * mm});
            skLineSegment(sketch, "E90", {"start": v(9.41, 6.59) * mm, "end": v(9.9, 7.07) * mm});
            skArc(sketch, "E91.trimOffspring", {"start": v(9.41, -6.59) * mm, "mid": v(6.59, -6.59) * mm, "end": v(6.59, -9.41) * mm});
            skArc(sketch, "E92.1.0.0", {"start": v(30.59, 9.41) * mm, "mid": v(30.59, 6.59) * mm, "end": v(33.41, 6.59) * mm});
            skArc(sketch, "E92.1.0.1", {"start": v(33.41, -6.59) * mm, "mid": v(30.59, -6.59) * mm, "end": v(30.59, -9.41) * mm});
            skLineSegment(sketch, "E92.1.0.2", {"start": v(24, 24) * mm, "end": v(48, 24) * mm, "construction": true});
            skLineSegment(sketch, "E92.1.0.3", {"start": v(32, 16) * mm, "end": v(40, 16) * mm, "construction": true});
            skArc(sketch, "E92.1.0.4", {"start": v(31.07, -9.9) * mm, "mid": v(33.9, -9.9) * mm, "end": v(33.9, -7.07) * mm});
            skLineSegment(sketch, "E92.1.0.5", {"start": v(48, 0) * mm, "end": v(24, -24) * mm, "construction": true});
            skCircle(sketch, "E92.1.0.6", {"center": v(40, -16) * mm, "radius": 2 * mm});
            skLineSegment(sketch, "E92.1.0.7", {"start": v(48, -24) * mm, "end": v(24, -24) * mm, "construction": true});
            skCircle(sketch, "E92.1.0.8", {"center": v(32, 16) * mm, "radius": 2 * mm});
            skCircle(sketch, "E92.1.0.9", {"center": v(40, 16) * mm, "radius": 2 * mm});
            skLineSegment(sketch, "E92.1.0.10", {"start": v(48, -24) * mm, "end": v(24, 0) * mm, "construction": true});
            skLineSegment(sketch, "E92.1.0.11", {"start": v(24, 24) * mm, "end": v(48, 0) * mm, "construction": true});
            skLineSegment(sketch, "E92.1.0.12", {"start": v(48, 24) * mm, "end": v(24, 0) * mm, "construction": true});
            skArc(sketch, "E92.1.0.13", {"start": v(40.93, 9.9) * mm, "mid": v(38.1, 9.9) * mm, "end": v(38.1, 7.07) * mm});
            skArc(sketch, "E92.1.0.14", {"start": v(33.9, 7.07) * mm, "mid": v(33.9, 9.9) * mm, "end": v(31.07, 9.9) * mm});
            skArc(sketch, "E92.1.0.15", {"start": v(38.1, -7.07) * mm, "mid": v(38.1, -9.9) * mm, "end": v(40.93, -9.9) * mm});
            skArc(sketch, "E92.1.0.16", {"start": v(38.59, 6.59) * mm, "mid": v(41.41, 6.59) * mm, "end": v(41.41, 9.41) * mm});
            skLineSegment(sketch, "E92.1.0.17", {"start": v(32, -16) * mm, "end": v(40, -16) * mm, "construction": true});
            skLineSegment(sketch, "E92.1.0.18", {"start": v(24, 0) * mm, "end": v(48, 0) * mm, "construction": true});
            skArc(sketch, "E92.1.0.19", {"start": v(41.41, -9.41) * mm, "mid": v(41.41, -6.59) * mm, "end": v(38.59, -6.59) * mm});
            skCircle(sketch, "E92.1.0.20", {"center": v(32, -16) * mm, "radius": 2 * mm});
            skCircle(sketch, "E92.1.0.21", {"center": v(36, 0) * mm, "radius": 2 * mm});
            skPoint(sketch, "E92.1.0.22", {"position": v(32, -8) * mm});
            skLineSegment(sketch, "E92.1.0.23", {"start": v(48, 0) * mm, "end": v(24, 0) * mm, "construction": true});
            skLineSegment(sketch, "E92.1.0.24", {"start": v(38.59, 6.59) * mm, "end": v(41.41, 9.41) * mm, "construction": true});
            skLineSegment(sketch, "E92.1.0.25", {"start": v(38.1, -7.07) * mm, "end": v(40.93, -9.9) * mm, "construction": true});
            skLineSegment(sketch, "E92.1.0.26", {"start": v(30.59, 9.41) * mm, "end": v(33.41, 6.59) * mm, "construction": true});
            skLineSegment(sketch, "E92.1.0.27", {"start": v(31.07, 9.9) * mm, "end": v(33.9, 7.07) * mm, "construction": true});
            skLineSegment(sketch, "E92.1.0.28", {"start": v(40.93, 9.9) * mm, "end": v(38.1, 7.07) * mm, "construction": true});
            skLineSegment(sketch, "E92.1.0.29", {"start": v(38.59, -6.59) * mm, "end": v(41.41, -9.41) * mm, "construction": true});
            skLineSegment(sketch, "E92.1.0.30", {"start": v(31.07, -9.9) * mm, "end": v(33.9, -7.07) * mm, "construction": true});
            skLineSegment(sketch, "E92.1.0.31", {"start": v(33.41, -6.59) * mm, "end": v(30.59, -9.41) * mm, "construction": true});
            skLineSegment(sketch, "E92.1.0.32", {"start": v(38.1, -7.07) * mm, "end": v(38.59, -6.59) * mm});
            skLineSegment(sketch, "E92.1.0.33", {"start": v(30.59, 9.41) * mm, "end": v(31.07, 9.9) * mm});
            skLineSegment(sketch, "E92.1.0.34", {"start": v(30.59, -9.41) * mm, "end": v(31.07, -9.9) * mm});
            skLineSegment(sketch, "E92.1.0.35", {"start": v(40.93, -9.9) * mm, "end": v(41.41, -9.41) * mm});
            skLineSegment(sketch, "E92.1.0.36", {"start": v(33.41, 6.59) * mm, "end": v(33.9, 7.07) * mm});
            skLineSegment(sketch, "E92.1.0.37", {"start": v(40.93, 9.9) * mm, "end": v(41.41, 9.41) * mm});
            skLineSegment(sketch, "E92.1.0.38", {"start": v(38.1, 7.07) * mm, "end": v(38.59, 6.59) * mm});
            skLineSegment(sketch, "E92.1.0.39", {"start": v(33.41, -6.59) * mm, "end": v(33.9, -7.07) * mm});
            skArc(sketch, "E92.2.0.0", {"start": v(54.59, 9.41) * mm, "mid": v(54.59, 6.59) * mm, "end": v(57.41, 6.59) * mm});
            skArc(sketch, "E92.2.0.1", {"start": v(57.41, -6.59) * mm, "mid": v(54.59, -6.59) * mm, "end": v(54.59, -9.41) * mm});
            skLineSegment(sketch, "E92.2.0.2", {"start": v(48, 24) * mm, "end": v(72, 24) * mm, "construction": true});
            skLineSegment(sketch, "E92.2.0.3", {"start": v(56, 16) * mm, "end": v(64, 16) * mm, "construction": true});
            skArc(sketch, "E92.2.0.4", {"start": v(55.07, -9.9) * mm, "mid": v(57.9, -9.9) * mm, "end": v(57.9, -7.07) * mm});
            skLineSegment(sketch, "E92.2.0.5", {"start": v(72, 0) * mm, "end": v(48, -24) * mm, "construction": true});
            skCircle(sketch, "E92.2.0.6", {"center": v(64, -16) * mm, "radius": 2 * mm});
            skLineSegment(sketch, "E92.2.0.7", {"start": v(72, -24) * mm, "end": v(48, -24) * mm, "construction": true});
            skCircle(sketch, "E92.2.0.8", {"center": v(56, 16) * mm, "radius": 2 * mm});
            skCircle(sketch, "E92.2.0.9", {"center": v(64, 16) * mm, "radius": 2 * mm});
            skLineSegment(sketch, "E92.2.0.10", {"start": v(72, -24) * mm, "end": v(48, 0) * mm, "construction": true});
            skLineSegment(sketch, "E92.2.0.11", {"start": v(48, 24) * mm, "end": v(72, 0) * mm, "construction": true});
            skLineSegment(sketch, "E92.2.0.12", {"start": v(72, 24) * mm, "end": v(48, 0) * mm, "construction": true});
            skArc(sketch, "E92.2.0.13", {"start": v(64.93, 9.9) * mm, "mid": v(62.1, 9.9) * mm, "end": v(62.1, 7.07) * mm});
            skArc(sketch, "E92.2.0.14", {"start": v(57.9, 7.07) * mm, "mid": v(57.9, 9.9) * mm, "end": v(55.07, 9.9) * mm});
            skArc(sketch, "E92.2.0.15", {"start": v(62.1, -7.07) * mm, "mid": v(62.1, -9.9) * mm, "end": v(64.93, -9.9) * mm});
            skArc(sketch, "E92.2.0.16", {"start": v(62.59, 6.59) * mm, "mid": v(65.41, 6.59) * mm, "end": v(65.41, 9.41) * mm});
            skLineSegment(sketch, "E92.2.0.17", {"start": v(56, -16) * mm, "end": v(64, -16) * mm, "construction": true});
            skLineSegment(sketch, "E92.2.0.18", {"start": v(48, 0) * mm, "end": v(72, 0) * mm, "construction": true});
            skArc(sketch, "E92.2.0.19", {"start": v(65.41, -9.41) * mm, "mid": v(65.41, -6.59) * mm, "end": v(62.59, -6.59) * mm});
            skCircle(sketch, "E92.2.0.20", {"center": v(56, -16) * mm, "radius": 2 * mm});
            skCircle(sketch, "E92.2.0.21", {"center": v(60, 0) * mm, "radius": 2 * mm});
            skPoint(sketch, "E92.2.0.22", {"position": v(56, -8) * mm});
            skLineSegment(sketch, "E92.2.0.23", {"start": v(72, 0) * mm, "end": v(48, 0) * mm, "construction": true});
            skLineSegment(sketch, "E92.2.0.24", {"start": v(62.59, 6.59) * mm, "end": v(65.41, 9.41) * mm, "construction": true});
            skLineSegment(sketch, "E92.2.0.25", {"start": v(62.1, -7.07) * mm, "end": v(64.93, -9.9) * mm, "construction": true});
            skLineSegment(sketch, "E92.2.0.26", {"start": v(54.59, 9.41) * mm, "end": v(57.41, 6.59) * mm, "construction": true});
            skLineSegment(sketch, "E92.2.0.27", {"start": v(55.07, 9.9) * mm, "end": v(57.9, 7.07) * mm, "construction": true});
            skLineSegment(sketch, "E92.2.0.28", {"start": v(64.93, 9.9) * mm, "end": v(62.1, 7.07) * mm, "construction": true});
            skLineSegment(sketch, "E92.2.0.29", {"start": v(62.59, -6.59) * mm, "end": v(65.41, -9.41) * mm, "construction": true});
            skLineSegment(sketch, "E92.2.0.30", {"start": v(55.07, -9.9) * mm, "end": v(57.9, -7.07) * mm, "construction": true});
            skLineSegment(sketch, "E92.2.0.31", {"start": v(57.41, -6.59) * mm, "end": v(54.59, -9.41) * mm, "construction": true});
            skLineSegment(sketch, "E92.2.0.32", {"start": v(62.1, -7.07) * mm, "end": v(62.59, -6.59) * mm});
            skLineSegment(sketch, "E92.2.0.33", {"start": v(54.59, 9.41) * mm, "end": v(55.07, 9.9) * mm});
            skLineSegment(sketch, "E92.2.0.34", {"start": v(54.59, -9.41) * mm, "end": v(55.07, -9.9) * mm});
            skLineSegment(sketch, "E92.2.0.35", {"start": v(64.93, -9.9) * mm, "end": v(65.41, -9.41) * mm});
            skLineSegment(sketch, "E92.2.0.36", {"start": v(57.41, 6.59) * mm, "end": v(57.9, 7.07) * mm});
            skLineSegment(sketch, "E92.2.0.37", {"start": v(64.93, 9.9) * mm, "end": v(65.41, 9.41) * mm});
            skLineSegment(sketch, "E92.2.0.38", {"start": v(62.1, 7.07) * mm, "end": v(62.59, 6.59) * mm});
            skLineSegment(sketch, "E92.2.0.39", {"start": v(57.41, -6.59) * mm, "end": v(57.9, -7.07) * mm});
            skArc(sketch, "E92.3.0.0", {"start": v(78.59, 9.41) * mm, "mid": v(78.59, 6.59) * mm, "end": v(81.41, 6.59) * mm});
            skArc(sketch, "E92.3.0.1", {"start": v(81.41, -6.59) * mm, "mid": v(78.59, -6.59) * mm, "end": v(78.59, -9.41) * mm});
            skLineSegment(sketch, "E92.3.0.2", {"start": v(72, 24) * mm, "end": v(96, 24) * mm, "construction": true});
            skLineSegment(sketch, "E92.3.0.3", {"start": v(80, 16) * mm, "end": v(88, 16) * mm, "construction": true});
            skArc(sketch, "E92.3.0.4", {"start": v(79.07, -9.9) * mm, "mid": v(81.9, -9.9) * mm, "end": v(81.9, -7.07) * mm});
            skLineSegment(sketch, "E92.3.0.5", {"start": v(96, 0) * mm, "end": v(72, -24) * mm, "construction": true});
            skCircle(sketch, "E92.3.0.6", {"center": v(88, -16) * mm, "radius": 2 * mm});
            skLineSegment(sketch, "E92.3.0.7", {"start": v(96, -24) * mm, "end": v(72, -24) * mm, "construction": true});
            skCircle(sketch, "E92.3.0.8", {"center": v(80, 16) * mm, "radius": 2 * mm});
            skCircle(sketch, "E92.3.0.9", {"center": v(88, 16) * mm, "radius": 2 * mm});
            skLineSegment(sketch, "E92.3.0.10", {"start": v(96, -24) * mm, "end": v(72, 0) * mm, "construction": true});
            skLineSegment(sketch, "E92.3.0.11", {"start": v(72, 24) * mm, "end": v(96, 0) * mm, "construction": true});
            skLineSegment(sketch, "E92.3.0.12", {"start": v(96, 24) * mm, "end": v(72, 0) * mm, "construction": true});
            skArc(sketch, "E92.3.0.13", {"start": v(88.93, 9.9) * mm, "mid": v(86.1, 9.9) * mm, "end": v(86.1, 7.07) * mm});
            skArc(sketch, "E92.3.0.14", {"start": v(81.9, 7.07) * mm, "mid": v(81.9, 9.9) * mm, "end": v(79.07, 9.9) * mm});
            skArc(sketch, "E92.3.0.15", {"start": v(86.1, -7.07) * mm, "mid": v(86.1, -9.9) * mm, "end": v(88.93, -9.9) * mm});
            skArc(sketch, "E92.3.0.16", {"start": v(86.59, 6.59) * mm, "mid": v(89.41, 6.59) * mm, "end": v(89.41, 9.41) * mm});
            skLineSegment(sketch, "E92.3.0.17", {"start": v(80, -16) * mm, "end": v(88, -16) * mm, "construction": true});
            skLineSegment(sketch, "E92.3.0.18", {"start": v(72, 0) * mm, "end": v(96, 0) * mm, "construction": true});
            skArc(sketch, "E92.3.0.19", {"start": v(89.41, -9.41) * mm, "mid": v(89.41, -6.59) * mm, "end": v(86.59, -6.59) * mm});
            skCircle(sketch, "E92.3.0.20", {"center": v(80, -16) * mm, "radius": 2 * mm});
            skCircle(sketch, "E92.3.0.21", {"center": v(84, 0) * mm, "radius": 2 * mm});
            skPoint(sketch, "E92.3.0.22", {"position": v(80, -8) * mm});
            skLineSegment(sketch, "E92.3.0.23", {"start": v(96, 0) * mm, "end": v(72, 0) * mm, "construction": true});
            skLineSegment(sketch, "E92.3.0.24", {"start": v(86.59, 6.59) * mm, "end": v(89.41, 9.41) * mm, "construction": true});
            skLineSegment(sketch, "E92.3.0.25", {"start": v(86.1, -7.07) * mm, "end": v(88.93, -9.9) * mm, "construction": true});
            skLineSegment(sketch, "E92.3.0.26", {"start": v(78.59, 9.41) * mm, "end": v(81.41, 6.59) * mm, "construction": true});
            skLineSegment(sketch, "E92.3.0.27", {"start": v(79.07, 9.9) * mm, "end": v(81.9, 7.07) * mm, "construction": true});
            skLineSegment(sketch, "E92.3.0.28", {"start": v(88.93, 9.9) * mm, "end": v(86.1, 7.07) * mm, "construction": true});
            skLineSegment(sketch, "E92.3.0.29", {"start": v(86.59, -6.59) * mm, "end": v(89.41, -9.41) * mm, "construction": true});
            skLineSegment(sketch, "E92.3.0.30", {"start": v(79.07, -9.9) * mm, "end": v(81.9, -7.07) * mm, "construction": true});
            skLineSegment(sketch, "E92.3.0.31", {"start": v(81.41, -6.59) * mm, "end": v(78.59, -9.41) * mm, "construction": true});
            skLineSegment(sketch, "E92.3.0.32", {"start": v(86.1, -7.07) * mm, "end": v(86.59, -6.59) * mm});
            skLineSegment(sketch, "E92.3.0.33", {"start": v(78.59, 9.41) * mm, "end": v(79.07, 9.9) * mm});
            skLineSegment(sketch, "E92.3.0.34", {"start": v(78.59, -9.41) * mm, "end": v(79.07, -9.9) * mm});
            skLineSegment(sketch, "E92.3.0.35", {"start": v(88.93, -9.9) * mm, "end": v(89.41, -9.41) * mm});
            skLineSegment(sketch, "E92.3.0.36", {"start": v(81.41, 6.59) * mm, "end": v(81.9, 7.07) * mm});
            skLineSegment(sketch, "E92.3.0.37", {"start": v(88.93, 9.9) * mm, "end": v(89.41, 9.41) * mm});
            skLineSegment(sketch, "E92.3.0.38", {"start": v(86.1, 7.07) * mm, "end": v(86.59, 6.59) * mm});
            skLineSegment(sketch, "E92.3.0.39", {"start": v(81.41, -6.59) * mm, "end": v(81.9, -7.07) * mm});
            skArc(sketch, "E92.4.0.0", {"start": v(102.59, 9.41) * mm, "mid": v(102.59, 6.59) * mm, "end": v(105.41, 6.59) * mm});
            skArc(sketch, "E92.4.0.1", {"start": v(105.41, -6.59) * mm, "mid": v(102.59, -6.59) * mm, "end": v(102.59, -9.41) * mm});
            skLineSegment(sketch, "E92.4.0.2", {"start": v(96, 24) * mm, "end": v(120, 24) * mm, "construction": true});
            skLineSegment(sketch, "E92.4.0.3", {"start": v(104, 16) * mm, "end": v(112, 16) * mm, "construction": true});
            skArc(sketch, "E92.4.0.4", {"start": v(103.07, -9.9) * mm, "mid": v(105.9, -9.9) * mm, "end": v(105.9, -7.07) * mm});
            skLineSegment(sketch, "E92.4.0.5", {"start": v(120, 0) * mm, "end": v(96, -24) * mm, "construction": true});
            skCircle(sketch, "E92.4.0.6", {"center": v(112, -16) * mm, "radius": 2 * mm});
            skLineSegment(sketch, "E92.4.0.7", {"start": v(120, -24) * mm, "end": v(96, -24) * mm, "construction": true});
            skCircle(sketch, "E92.4.0.8", {"center": v(104, 16) * mm, "radius": 2 * mm});
            skCircle(sketch, "E92.4.0.9", {"center": v(112, 16) * mm, "radius": 2 * mm});
            skLineSegment(sketch, "E92.4.0.10", {"start": v(120, -24) * mm, "end": v(96, 0) * mm, "construction": true});
            skLineSegment(sketch, "E92.4.0.11", {"start": v(96, 24) * mm, "end": v(120, 0) * mm, "construction": true});
            skLineSegment(sketch, "E92.4.0.12", {"start": v(120, 24) * mm, "end": v(96, 0) * mm, "construction": true});
            skArc(sketch, "E92.4.0.13", {"start": v(112.93, 9.9) * mm, "mid": v(110.1, 9.9) * mm, "end": v(110.1, 7.07) * mm});
            skArc(sketch, "E92.4.0.14", {"start": v(105.9, 7.07) * mm, "mid": v(105.9, 9.9) * mm, "end": v(103.07, 9.9) * mm});
            skArc(sketch, "E92.4.0.15", {"start": v(110.1, -7.07) * mm, "mid": v(110.1, -9.9) * mm, "end": v(112.93, -9.9) * mm});
            skArc(sketch, "E92.4.0.16", {"start": v(110.59, 6.59) * mm, "mid": v(113.41, 6.59) * mm, "end": v(113.41, 9.41) * mm});
            skLineSegment(sketch, "E92.4.0.17", {"start": v(104, -16) * mm, "end": v(112, -16) * mm, "construction": true});
            skLineSegment(sketch, "E92.4.0.18", {"start": v(96, 0) * mm, "end": v(120, 0) * mm, "construction": true});
            skArc(sketch, "E92.4.0.19", {"start": v(113.41, -9.41) * mm, "mid": v(113.41, -6.59) * mm, "end": v(110.59, -6.59) * mm});
            skCircle(sketch, "E92.4.0.20", {"center": v(104, -16) * mm, "radius": 2 * mm});
            skCircle(sketch, "E92.4.0.21", {"center": v(108, 0) * mm, "radius": 2 * mm});
            skPoint(sketch, "E92.4.0.22", {"position": v(104, -8) * mm});
            skLineSegment(sketch, "E92.4.0.23", {"start": v(120, 0) * mm, "end": v(96, 0) * mm, "construction": true});
            skLineSegment(sketch, "E92.4.0.24", {"start": v(110.59, 6.59) * mm, "end": v(113.41, 9.41) * mm, "construction": true});
            skLineSegment(sketch, "E92.4.0.25", {"start": v(110.1, -7.07) * mm, "end": v(112.93, -9.9) * mm, "construction": true});
            skLineSegment(sketch, "E92.4.0.26", {"start": v(102.59, 9.41) * mm, "end": v(105.41, 6.59) * mm, "construction": true});
            skLineSegment(sketch, "E92.4.0.27", {"start": v(103.07, 9.9) * mm, "end": v(105.9, 7.07) * mm, "construction": true});
            skLineSegment(sketch, "E92.4.0.28", {"start": v(112.93, 9.9) * mm, "end": v(110.1, 7.07) * mm, "construction": true});
            skLineSegment(sketch, "E92.4.0.29", {"start": v(110.59, -6.59) * mm, "end": v(113.41, -9.41) * mm, "construction": true});
            skLineSegment(sketch, "E92.4.0.30", {"start": v(103.07, -9.9) * mm, "end": v(105.9, -7.07) * mm, "construction": true});
            skLineSegment(sketch, "E92.4.0.31", {"start": v(105.41, -6.59) * mm, "end": v(102.59, -9.41) * mm, "construction": true});
            skLineSegment(sketch, "E92.4.0.32", {"start": v(110.1, -7.07) * mm, "end": v(110.59, -6.59) * mm});
            skLineSegment(sketch, "E92.4.0.33", {"start": v(102.59, 9.41) * mm, "end": v(103.07, 9.9) * mm});
            skLineSegment(sketch, "E92.4.0.34", {"start": v(102.59, -9.41) * mm, "end": v(103.07, -9.9) * mm});
            skLineSegment(sketch, "E92.4.0.35", {"start": v(112.93, -9.9) * mm, "end": v(113.41, -9.41) * mm});
            skLineSegment(sketch, "E92.4.0.36", {"start": v(105.41, 6.59) * mm, "end": v(105.9, 7.07) * mm});
            skLineSegment(sketch, "E92.4.0.37", {"start": v(112.93, 9.9) * mm, "end": v(113.41, 9.41) * mm});
            skLineSegment(sketch, "E92.4.0.38", {"start": v(110.1, 7.07) * mm, "end": v(110.59, 6.59) * mm});
            skLineSegment(sketch, "E92.4.0.39", {"start": v(105.41, -6.59) * mm, "end": v(105.9, -7.07) * mm});
            skArc(sketch, "E92.5.0.0", {"start": v(126.59, 9.41) * mm, "mid": v(126.59, 6.59) * mm, "end": v(129.41, 6.59) * mm});
            skArc(sketch, "E92.5.0.1", {"start": v(129.41, -6.59) * mm, "mid": v(126.59, -6.59) * mm, "end": v(126.59, -9.41) * mm});
            skLineSegment(sketch, "E92.5.0.2", {"start": v(120, 24) * mm, "end": v(144, 24) * mm, "construction": true});
            skLineSegment(sketch, "E92.5.0.3", {"start": v(128, 16) * mm, "end": v(136, 16) * mm, "construction": true});
            skArc(sketch, "E92.5.0.4", {"start": v(127.07, -9.9) * mm, "mid": v(129.9, -9.9) * mm, "end": v(129.9, -7.07) * mm});
            skLineSegment(sketch, "E92.5.0.5", {"start": v(144, 0) * mm, "end": v(120, -24) * mm, "construction": true});
            skCircle(sketch, "E92.5.0.6", {"center": v(136, -16) * mm, "radius": 2 * mm});
            skLineSegment(sketch, "E92.5.0.7", {"start": v(144, -24) * mm, "end": v(120, -24) * mm, "construction": true});
            skCircle(sketch, "E92.5.0.8", {"center": v(128, 16) * mm, "radius": 2 * mm});
            skCircle(sketch, "E92.5.0.9", {"center": v(136, 16) * mm, "radius": 2 * mm});
            skLineSegment(sketch, "E92.5.0.10", {"start": v(144, -24) * mm, "end": v(120, 0) * mm, "construction": true});
            skLineSegment(sketch, "E92.5.0.11", {"start": v(120, 24) * mm, "end": v(144, 0) * mm, "construction": true});
            skLineSegment(sketch, "E92.5.0.12", {"start": v(144, 24) * mm, "end": v(120, 0) * mm, "construction": true});
            skArc(sketch, "E92.5.0.13", {"start": v(136.93, 9.9) * mm, "mid": v(134.1, 9.9) * mm, "end": v(134.1, 7.07) * mm});
            skArc(sketch, "E92.5.0.14", {"start": v(129.9, 7.07) * mm, "mid": v(129.9, 9.9) * mm, "end": v(127.07, 9.9) * mm});
            skArc(sketch, "E92.5.0.15", {"start": v(134.1, -7.07) * mm, "mid": v(134.1, -9.9) * mm, "end": v(136.93, -9.9) * mm});
            skArc(sketch, "E92.5.0.16", {"start": v(134.59, 6.59) * mm, "mid": v(137.41, 6.59) * mm, "end": v(137.41, 9.41) * mm});
            skLineSegment(sketch, "E92.5.0.17", {"start": v(128, -16) * mm, "end": v(136, -16) * mm, "construction": true});
            skLineSegment(sketch, "E92.5.0.18", {"start": v(120, 0) * mm, "end": v(144, 0) * mm, "construction": true});
            skArc(sketch, "E92.5.0.19", {"start": v(137.41, -9.41) * mm, "mid": v(137.41, -6.59) * mm, "end": v(134.59, -6.59) * mm});
            skCircle(sketch, "E92.5.0.20", {"center": v(128, -16) * mm, "radius": 2 * mm});
            skCircle(sketch, "E92.5.0.21", {"center": v(132, 0) * mm, "radius": 2 * mm});
            skPoint(sketch, "E92.5.0.22", {"position": v(128, -8) * mm});
            skLineSegment(sketch, "E92.5.0.23", {"start": v(144, 0) * mm, "end": v(120, 0) * mm, "construction": true});
            skLineSegment(sketch, "E92.5.0.24", {"start": v(134.59, 6.59) * mm, "end": v(137.41, 9.41) * mm, "construction": true});
            skLineSegment(sketch, "E92.5.0.25", {"start": v(134.1, -7.07) * mm, "end": v(136.93, -9.9) * mm, "construction": true});
            skLineSegment(sketch, "E92.5.0.26", {"start": v(126.59, 9.41) * mm, "end": v(129.41, 6.59) * mm, "construction": true});
            skLineSegment(sketch, "E92.5.0.27", {"start": v(127.07, 9.9) * mm, "end": v(129.9, 7.07) * mm, "construction": true});
            skLineSegment(sketch, "E92.5.0.28", {"start": v(136.93, 9.9) * mm, "end": v(134.1, 7.07) * mm, "construction": true});
            skLineSegment(sketch, "E92.5.0.29", {"start": v(134.59, -6.59) * mm, "end": v(137.41, -9.41) * mm, "construction": true});
            skLineSegment(sketch, "E92.5.0.30", {"start": v(127.07, -9.9) * mm, "end": v(129.9, -7.07) * mm, "construction": true});
            skLineSegment(sketch, "E92.5.0.31", {"start": v(129.41, -6.59) * mm, "end": v(126.59, -9.41) * mm, "construction": true});
            skLineSegment(sketch, "E92.5.0.32", {"start": v(134.1, -7.07) * mm, "end": v(134.59, -6.59) * mm});
            skLineSegment(sketch, "E92.5.0.33", {"start": v(126.59, 9.41) * mm, "end": v(127.07, 9.9) * mm});
            skLineSegment(sketch, "E92.5.0.34", {"start": v(126.59, -9.41) * mm, "end": v(127.07, -9.9) * mm});
            skLineSegment(sketch, "E92.5.0.35", {"start": v(136.93, -9.9) * mm, "end": v(137.41, -9.41) * mm});
            skLineSegment(sketch, "E92.5.0.36", {"start": v(129.41, 6.59) * mm, "end": v(129.9, 7.07) * mm});
            skLineSegment(sketch, "E92.5.0.37", {"start": v(136.93, 9.9) * mm, "end": v(137.41, 9.41) * mm});
            skLineSegment(sketch, "E92.5.0.38", {"start": v(134.1, 7.07) * mm, "end": v(134.59, 6.59) * mm});
            skLineSegment(sketch, "E92.5.0.39", {"start": v(129.41, -6.59) * mm, "end": v(129.9, -7.07) * mm});
            skArc(sketch, "E92.6.0.0", {"start": v(150.59, 9.41) * mm, "mid": v(150.59, 6.59) * mm, "end": v(153.41, 6.59) * mm});
            skArc(sketch, "E92.6.0.1", {"start": v(153.41, -6.59) * mm, "mid": v(150.59, -6.59) * mm, "end": v(150.59, -9.41) * mm});
            skLineSegment(sketch, "E92.6.0.2", {"start": v(144, 24) * mm, "end": v(168, 24) * mm, "construction": true});
            skLineSegment(sketch, "E92.6.0.3", {"start": v(152, 16) * mm, "end": v(160, 16) * mm, "construction": true});
            skArc(sketch, "E92.6.0.4", {"start": v(151.07, -9.9) * mm, "mid": v(153.9, -9.9) * mm, "end": v(153.9, -7.07) * mm});
            skLineSegment(sketch, "E92.6.0.5", {"start": v(168, 0) * mm, "end": v(144, -24) * mm, "construction": true});
            skCircle(sketch, "E92.6.0.6", {"center": v(160, -16) * mm, "radius": 2 * mm});
            skLineSegment(sketch, "E92.6.0.7", {"start": v(168, -24) * mm, "end": v(144, -24) * mm, "construction": true});
            skCircle(sketch, "E92.6.0.8", {"center": v(152, 16) * mm, "radius": 2 * mm});
            skCircle(sketch, "E92.6.0.9", {"center": v(160, 16) * mm, "radius": 2 * mm});
            skLineSegment(sketch, "E92.6.0.10", {"start": v(168, -24) * mm, "end": v(144, 0) * mm, "construction": true});
            skLineSegment(sketch, "E92.6.0.11", {"start": v(144, 24) * mm, "end": v(168, 0) * mm, "construction": true});
            skLineSegment(sketch, "E92.6.0.12", {"start": v(168, 24) * mm, "end": v(144, 0) * mm, "construction": true});
            skArc(sketch, "E92.6.0.13", {"start": v(160.93, 9.9) * mm, "mid": v(158.1, 9.9) * mm, "end": v(158.1, 7.07) * mm});
            skArc(sketch, "E92.6.0.14", {"start": v(153.9, 7.07) * mm, "mid": v(153.9, 9.9) * mm, "end": v(151.07, 9.9) * mm});
            skArc(sketch, "E92.6.0.15", {"start": v(158.1, -7.07) * mm, "mid": v(158.1, -9.9) * mm, "end": v(160.93, -9.9) * mm});
            skArc(sketch, "E92.6.0.16", {"start": v(158.59, 6.59) * mm, "mid": v(161.41, 6.59) * mm, "end": v(161.41, 9.41) * mm});
            skLineSegment(sketch, "E92.6.0.17", {"start": v(152, -16) * mm, "end": v(160, -16) * mm, "construction": true});
            skLineSegment(sketch, "E92.6.0.18", {"start": v(144, 0) * mm, "end": v(168, 0) * mm, "construction": true});
            skArc(sketch, "E92.6.0.19", {"start": v(161.41, -9.41) * mm, "mid": v(161.41, -6.59) * mm, "end": v(158.59, -6.59) * mm});
            skCircle(sketch, "E92.6.0.20", {"center": v(152, -16) * mm, "radius": 2 * mm});
            skCircle(sketch, "E92.6.0.21", {"center": v(156, 0) * mm, "radius": 2 * mm});
            skPoint(sketch, "E92.6.0.22", {"position": v(152, -8) * mm});
            skLineSegment(sketch, "E92.6.0.23", {"start": v(168, 0) * mm, "end": v(144, 0) * mm, "construction": true});
            skLineSegment(sketch, "E92.6.0.24", {"start": v(158.59, 6.59) * mm, "end": v(161.41, 9.41) * mm, "construction": true});
            skLineSegment(sketch, "E92.6.0.25", {"start": v(158.1, -7.07) * mm, "end": v(160.93, -9.9) * mm, "construction": true});
            skLineSegment(sketch, "E92.6.0.26", {"start": v(150.59, 9.41) * mm, "end": v(153.41, 6.59) * mm, "construction": true});
            skLineSegment(sketch, "E92.6.0.27", {"start": v(151.07, 9.9) * mm, "end": v(153.9, 7.07) * mm, "construction": true});
            skLineSegment(sketch, "E92.6.0.28", {"start": v(160.93, 9.9) * mm, "end": v(158.1, 7.07) * mm, "construction": true});
            skLineSegment(sketch, "E92.6.0.29", {"start": v(158.59, -6.59) * mm, "end": v(161.41, -9.41) * mm, "construction": true});
            skLineSegment(sketch, "E92.6.0.30", {"start": v(151.07, -9.9) * mm, "end": v(153.9, -7.07) * mm, "construction": true});
            skLineSegment(sketch, "E92.6.0.31", {"start": v(153.41, -6.59) * mm, "end": v(150.59, -9.41) * mm, "construction": true});
            skLineSegment(sketch, "E92.6.0.32", {"start": v(158.1, -7.07) * mm, "end": v(158.59, -6.59) * mm});
            skLineSegment(sketch, "E92.6.0.33", {"start": v(150.59, 9.41) * mm, "end": v(151.07, 9.9) * mm});
            skLineSegment(sketch, "E92.6.0.34", {"start": v(150.59, -9.41) * mm, "end": v(151.07, -9.9) * mm});
            skLineSegment(sketch, "E92.6.0.35", {"start": v(160.93, -9.9) * mm, "end": v(161.41, -9.41) * mm});
            skLineSegment(sketch, "E92.6.0.36", {"start": v(153.41, 6.59) * mm, "end": v(153.9, 7.07) * mm});
            skLineSegment(sketch, "E92.6.0.37", {"start": v(160.93, 9.9) * mm, "end": v(161.41, 9.41) * mm});
            skLineSegment(sketch, "E92.6.0.38", {"start": v(158.1, 7.07) * mm, "end": v(158.59, 6.59) * mm});
            skLineSegment(sketch, "E92.6.0.39", {"start": v(153.41, -6.59) * mm, "end": v(153.9, -7.07) * mm});
            skArc(sketch, "E92.7.0.0", {"start": v(174.59, 9.41) * mm, "mid": v(174.59, 6.59) * mm, "end": v(177.41, 6.59) * mm});
            skArc(sketch, "E92.7.0.1", {"start": v(177.41, -6.59) * mm, "mid": v(174.59, -6.59) * mm, "end": v(174.59, -9.41) * mm});
            skLineSegment(sketch, "E92.7.0.2", {"start": v(168, 24) * mm, "end": v(192, 24) * mm, "construction": true});
            skLineSegment(sketch, "E92.7.0.3", {"start": v(176, 16) * mm, "end": v(184, 16) * mm, "construction": true});
            skArc(sketch, "E92.7.0.4", {"start": v(175.07, -9.9) * mm, "mid": v(177.9, -9.9) * mm, "end": v(177.9, -7.07) * mm});
            skLineSegment(sketch, "E92.7.0.5", {"start": v(192, 0) * mm, "end": v(168, -24) * mm, "construction": true});
            skCircle(sketch, "E92.7.0.6", {"center": v(184, -16) * mm, "radius": 2 * mm});
            skLineSegment(sketch, "E92.7.0.7", {"start": v(192, -24) * mm, "end": v(168, -24) * mm, "construction": true});
            skCircle(sketch, "E92.7.0.8", {"center": v(176, 16) * mm, "radius": 2 * mm});
            skCircle(sketch, "E92.7.0.9", {"center": v(184, 16) * mm, "radius": 2 * mm});
            skLineSegment(sketch, "E92.7.0.10", {"start": v(192, -24) * mm, "end": v(168, 0) * mm, "construction": true});
            skLineSegment(sketch, "E92.7.0.11", {"start": v(168, 24) * mm, "end": v(192, 0) * mm, "construction": true});
            skLineSegment(sketch, "E92.7.0.12", {"start": v(192, 24) * mm, "end": v(168, 0) * mm, "construction": true});
            skArc(sketch, "E92.7.0.13", {"start": v(184.93, 9.9) * mm, "mid": v(182.1, 9.9) * mm, "end": v(182.1, 7.07) * mm});
            skArc(sketch, "E92.7.0.14", {"start": v(177.9, 7.07) * mm, "mid": v(177.9, 9.9) * mm, "end": v(175.07, 9.9) * mm});
            skArc(sketch, "E92.7.0.15", {"start": v(182.1, -7.07) * mm, "mid": v(182.1, -9.9) * mm, "end": v(184.93, -9.9) * mm});
            skArc(sketch, "E92.7.0.16", {"start": v(182.59, 6.59) * mm, "mid": v(185.41, 6.59) * mm, "end": v(185.41, 9.41) * mm});
            skLineSegment(sketch, "E92.7.0.17", {"start": v(176, -16) * mm, "end": v(184, -16) * mm, "construction": true});
            skLineSegment(sketch, "E92.7.0.18", {"start": v(168, 0) * mm, "end": v(192, 0) * mm, "construction": true});
            skArc(sketch, "E92.7.0.19", {"start": v(185.41, -9.41) * mm, "mid": v(185.41, -6.59) * mm, "end": v(182.59, -6.59) * mm});
            skCircle(sketch, "E92.7.0.20", {"center": v(176, -16) * mm, "radius": 2 * mm});
            skCircle(sketch, "E92.7.0.21", {"center": v(180, 0) * mm, "radius": 2 * mm});
            skPoint(sketch, "E92.7.0.22", {"position": v(176, -8) * mm});
            skLineSegment(sketch, "E92.7.0.23", {"start": v(192, 0) * mm, "end": v(168, 0) * mm, "construction": true});
            skLineSegment(sketch, "E92.7.0.24", {"start": v(182.59, 6.59) * mm, "end": v(185.41, 9.41) * mm, "construction": true});
            skLineSegment(sketch, "E92.7.0.25", {"start": v(182.1, -7.07) * mm, "end": v(184.93, -9.9) * mm, "construction": true});
            skLineSegment(sketch, "E92.7.0.26", {"start": v(174.59, 9.41) * mm, "end": v(177.41, 6.59) * mm, "construction": true});
            skLineSegment(sketch, "E92.7.0.27", {"start": v(175.07, 9.9) * mm, "end": v(177.9, 7.07) * mm, "construction": true});
            skLineSegment(sketch, "E92.7.0.28", {"start": v(184.93, 9.9) * mm, "end": v(182.1, 7.07) * mm, "construction": true});
            skLineSegment(sketch, "E92.7.0.29", {"start": v(182.59, -6.59) * mm, "end": v(185.41, -9.41) * mm, "construction": true});
            skLineSegment(sketch, "E92.7.0.30", {"start": v(175.07, -9.9) * mm, "end": v(177.9, -7.07) * mm, "construction": true});
            skLineSegment(sketch, "E92.7.0.31", {"start": v(177.41, -6.59) * mm, "end": v(174.59, -9.41) * mm, "construction": true});
            skLineSegment(sketch, "E92.7.0.32", {"start": v(182.1, -7.07) * mm, "end": v(182.59, -6.59) * mm});
            skLineSegment(sketch, "E92.7.0.33", {"start": v(174.59, 9.41) * mm, "end": v(175.07, 9.9) * mm});
            skLineSegment(sketch, "E92.7.0.34", {"start": v(174.59, -9.41) * mm, "end": v(175.07, -9.9) * mm});
            skLineSegment(sketch, "E92.7.0.35", {"start": v(184.93, -9.9) * mm, "end": v(185.41, -9.41) * mm});
            skLineSegment(sketch, "E92.7.0.36", {"start": v(177.41, 6.59) * mm, "end": v(177.9, 7.07) * mm});
            skLineSegment(sketch, "E92.7.0.37", {"start": v(184.93, 9.9) * mm, "end": v(185.41, 9.41) * mm});
            skLineSegment(sketch, "E92.7.0.38", {"start": v(182.1, 7.07) * mm, "end": v(182.59, 6.59) * mm});
            skLineSegment(sketch, "E92.7.0.39", {"start": v(177.41, -6.59) * mm, "end": v(177.9, -7.07) * mm});
            skArc(sketch, "E92.8.0.0", {"start": v(198.59, 9.41) * mm, "mid": v(198.59, 6.59) * mm, "end": v(201.41, 6.59) * mm});
            skArc(sketch, "E92.8.0.1", {"start": v(201.41, -6.59) * mm, "mid": v(198.59, -6.59) * mm, "end": v(198.59, -9.41) * mm});
            skLineSegment(sketch, "E92.8.0.2", {"start": v(192, 24) * mm, "end": v(216, 24) * mm, "construction": true});
            skLineSegment(sketch, "E92.8.0.3", {"start": v(200, 16) * mm, "end": v(208, 16) * mm, "construction": true});
            skArc(sketch, "E92.8.0.4", {"start": v(199.07, -9.9) * mm, "mid": v(201.9, -9.9) * mm, "end": v(201.9, -7.07) * mm});
            skLineSegment(sketch, "E92.8.0.5", {"start": v(216, 0) * mm, "end": v(192, -24) * mm, "construction": true});
            skCircle(sketch, "E92.8.0.6", {"center": v(208, -16) * mm, "radius": 2 * mm});
            skLineSegment(sketch, "E92.8.0.7", {"start": v(216, -24) * mm, "end": v(192, -24) * mm, "construction": true});
            skCircle(sketch, "E92.8.0.8", {"center": v(200, 16) * mm, "radius": 2 * mm});
            skCircle(sketch, "E92.8.0.9", {"center": v(208, 16) * mm, "radius": 2 * mm});
            skLineSegment(sketch, "E92.8.0.10", {"start": v(216, -24) * mm, "end": v(192, 0) * mm, "construction": true});
            skLineSegment(sketch, "E92.8.0.11", {"start": v(192, 24) * mm, "end": v(216, 0) * mm, "construction": true});
            skLineSegment(sketch, "E92.8.0.12", {"start": v(216, 24) * mm, "end": v(192, 0) * mm, "construction": true});
            skArc(sketch, "E92.8.0.13", {"start": v(208.93, 9.9) * mm, "mid": v(206.1, 9.9) * mm, "end": v(206.1, 7.07) * mm});
            skArc(sketch, "E92.8.0.14", {"start": v(201.9, 7.07) * mm, "mid": v(201.9, 9.9) * mm, "end": v(199.07, 9.9) * mm});
            skArc(sketch, "E92.8.0.15", {"start": v(206.1, -7.07) * mm, "mid": v(206.1, -9.9) * mm, "end": v(208.93, -9.9) * mm});
            skArc(sketch, "E92.8.0.16", {"start": v(206.59, 6.59) * mm, "mid": v(209.41, 6.59) * mm, "end": v(209.41, 9.41) * mm});
            skLineSegment(sketch, "E92.8.0.17", {"start": v(200, -16) * mm, "end": v(208, -16) * mm, "construction": true});
            skLineSegment(sketch, "E92.8.0.18", {"start": v(192, 0) * mm, "end": v(216, 0) * mm, "construction": true});
            skArc(sketch, "E92.8.0.19", {"start": v(209.41, -9.41) * mm, "mid": v(209.41, -6.59) * mm, "end": v(206.59, -6.59) * mm});
            skCircle(sketch, "E92.8.0.20", {"center": v(200, -16) * mm, "radius": 2 * mm});
            skCircle(sketch, "E92.8.0.21", {"center": v(204, 0) * mm, "radius": 2 * mm});
            skPoint(sketch, "E92.8.0.22", {"position": v(200, -8) * mm});
            skLineSegment(sketch, "E92.8.0.23", {"start": v(216, 0) * mm, "end": v(192, 0) * mm, "construction": true});
            skLineSegment(sketch, "E92.8.0.24", {"start": v(206.59, 6.59) * mm, "end": v(209.41, 9.41) * mm, "construction": true});
            skLineSegment(sketch, "E92.8.0.25", {"start": v(206.1, -7.07) * mm, "end": v(208.93, -9.9) * mm, "construction": true});
            skLineSegment(sketch, "E92.8.0.26", {"start": v(198.59, 9.41) * mm, "end": v(201.41, 6.59) * mm, "construction": true});
            skLineSegment(sketch, "E92.8.0.27", {"start": v(199.07, 9.9) * mm, "end": v(201.9, 7.07) * mm, "construction": true});
            skLineSegment(sketch, "E92.8.0.28", {"start": v(208.93, 9.9) * mm, "end": v(206.1, 7.07) * mm, "construction": true});
            skLineSegment(sketch, "E92.8.0.29", {"start": v(206.59, -6.59) * mm, "end": v(209.41, -9.41) * mm, "construction": true});
            skLineSegment(sketch, "E92.8.0.30", {"start": v(199.07, -9.9) * mm, "end": v(201.9, -7.07) * mm, "construction": true});
            skLineSegment(sketch, "E92.8.0.31", {"start": v(201.41, -6.59) * mm, "end": v(198.59, -9.41) * mm, "construction": true});
            skLineSegment(sketch, "E92.8.0.32", {"start": v(206.1, -7.07) * mm, "end": v(206.59, -6.59) * mm});
            skLineSegment(sketch, "E92.8.0.33", {"start": v(198.59, 9.41) * mm, "end": v(199.07, 9.9) * mm});
            skLineSegment(sketch, "E92.8.0.34", {"start": v(198.59, -9.41) * mm, "end": v(199.07, -9.9) * mm});
            skLineSegment(sketch, "E92.8.0.35", {"start": v(208.93, -9.9) * mm, "end": v(209.41, -9.41) * mm});
            skLineSegment(sketch, "E92.8.0.36", {"start": v(201.41, 6.59) * mm, "end": v(201.9, 7.07) * mm});
            skLineSegment(sketch, "E92.8.0.37", {"start": v(208.93, 9.9) * mm, "end": v(209.41, 9.41) * mm});
            skLineSegment(sketch, "E92.8.0.38", {"start": v(206.1, 7.07) * mm, "end": v(206.59, 6.59) * mm});
            skLineSegment(sketch, "E92.8.0.39", {"start": v(201.41, -6.59) * mm, "end": v(201.9, -7.07) * mm});
            skArc(sketch, "E92.9.0.0", {"start": v(222.59, 9.41) * mm, "mid": v(222.59, 6.59) * mm, "end": v(225.41, 6.59) * mm});
            skArc(sketch, "E92.9.0.1", {"start": v(225.41, -6.59) * mm, "mid": v(222.59, -6.59) * mm, "end": v(222.59, -9.41) * mm});
            skLineSegment(sketch, "E92.9.0.2", {"start": v(216, 24) * mm, "end": v(240, 24) * mm, "construction": true});
            skLineSegment(sketch, "E92.9.0.3", {"start": v(224, 16) * mm, "end": v(232, 16) * mm, "construction": true});
            skArc(sketch, "E92.9.0.4", {"start": v(223.07, -9.9) * mm, "mid": v(225.9, -9.9) * mm, "end": v(225.9, -7.07) * mm});
            skLineSegment(sketch, "E92.9.0.5", {"start": v(240, 0) * mm, "end": v(216, -24) * mm, "construction": true});
            skCircle(sketch, "E92.9.0.6", {"center": v(232, -16) * mm, "radius": 2 * mm});
            skLineSegment(sketch, "E92.9.0.7", {"start": v(240, -24) * mm, "end": v(216, -24) * mm, "construction": true});
            skCircle(sketch, "E92.9.0.8", {"center": v(224, 16) * mm, "radius": 2 * mm});
            skCircle(sketch, "E92.9.0.9", {"center": v(232, 16) * mm, "radius": 2 * mm});
            skLineSegment(sketch, "E92.9.0.10", {"start": v(240, -24) * mm, "end": v(216, 0) * mm, "construction": true});
            skLineSegment(sketch, "E92.9.0.11", {"start": v(216, 24) * mm, "end": v(240, 0) * mm, "construction": true});
            skLineSegment(sketch, "E92.9.0.12", {"start": v(240, 24) * mm, "end": v(216, 0) * mm, "construction": true});
            skArc(sketch, "E92.9.0.13", {"start": v(232.93, 9.9) * mm, "mid": v(230.1, 9.9) * mm, "end": v(230.1, 7.07) * mm});
            skArc(sketch, "E92.9.0.14", {"start": v(225.9, 7.07) * mm, "mid": v(225.9, 9.9) * mm, "end": v(223.07, 9.9) * mm});
            skArc(sketch, "E92.9.0.15", {"start": v(230.1, -7.07) * mm, "mid": v(230.1, -9.9) * mm, "end": v(232.93, -9.9) * mm});
            skArc(sketch, "E92.9.0.16", {"start": v(230.59, 6.59) * mm, "mid": v(233.41, 6.59) * mm, "end": v(233.41, 9.41) * mm});
            skLineSegment(sketch, "E92.9.0.17", {"start": v(224, -16) * mm, "end": v(232, -16) * mm, "construction": true});
            skLineSegment(sketch, "E92.9.0.18", {"start": v(216, 0) * mm, "end": v(240, 0) * mm, "construction": true});
            skArc(sketch, "E92.9.0.19", {"start": v(233.41, -9.41) * mm, "mid": v(233.41, -6.59) * mm, "end": v(230.59, -6.59) * mm});
            skCircle(sketch, "E92.9.0.20", {"center": v(224, -16) * mm, "radius": 2 * mm});
            skCircle(sketch, "E92.9.0.21", {"center": v(228, 0) * mm, "radius": 2 * mm});
            skPoint(sketch, "E92.9.0.22", {"position": v(224, -8) * mm});
            skLineSegment(sketch, "E92.9.0.23", {"start": v(240, 0) * mm, "end": v(216, 0) * mm, "construction": true});
            skLineSegment(sketch, "E92.9.0.24", {"start": v(230.59, 6.59) * mm, "end": v(233.41, 9.41) * mm, "construction": true});
            skLineSegment(sketch, "E92.9.0.25", {"start": v(230.1, -7.07) * mm, "end": v(232.93, -9.9) * mm, "construction": true});
            skLineSegment(sketch, "E92.9.0.26", {"start": v(222.59, 9.41) * mm, "end": v(225.41, 6.59) * mm, "construction": true});
            skLineSegment(sketch, "E92.9.0.27", {"start": v(223.07, 9.9) * mm, "end": v(225.9, 7.07) * mm, "construction": true});
            skLineSegment(sketch, "E92.9.0.28", {"start": v(232.93, 9.9) * mm, "end": v(230.1, 7.07) * mm, "construction": true});
            skLineSegment(sketch, "E92.9.0.29", {"start": v(230.59, -6.59) * mm, "end": v(233.41, -9.41) * mm, "construction": true});
            skLineSegment(sketch, "E92.9.0.30", {"start": v(223.07, -9.9) * mm, "end": v(225.9, -7.07) * mm, "construction": true});
            skLineSegment(sketch, "E92.9.0.31", {"start": v(225.41, -6.59) * mm, "end": v(222.59, -9.41) * mm, "construction": true});
            skLineSegment(sketch, "E92.9.0.32", {"start": v(230.1, -7.07) * mm, "end": v(230.59, -6.59) * mm});
            skLineSegment(sketch, "E92.9.0.33", {"start": v(222.59, 9.41) * mm, "end": v(223.07, 9.9) * mm});
            skLineSegment(sketch, "E92.9.0.34", {"start": v(222.59, -9.41) * mm, "end": v(223.07, -9.9) * mm});
            skLineSegment(sketch, "E92.9.0.35", {"start": v(232.93, -9.9) * mm, "end": v(233.41, -9.41) * mm});
            skLineSegment(sketch, "E92.9.0.36", {"start": v(225.41, 6.59) * mm, "end": v(225.9, 7.07) * mm});
            skLineSegment(sketch, "E92.9.0.37", {"start": v(232.93, 9.9) * mm, "end": v(233.41, 9.41) * mm});
            skLineSegment(sketch, "E92.9.0.38", {"start": v(230.1, 7.07) * mm, "end": v(230.59, 6.59) * mm});
            skLineSegment(sketch, "E92.9.0.39", {"start": v(225.41, -6.59) * mm, "end": v(225.9, -7.07) * mm});
            skArc(sketch, "E92.10.0.0", {"start": v(246.59, 9.41) * mm, "mid": v(246.59, 6.59) * mm, "end": v(249.41, 6.59) * mm});
            skArc(sketch, "E92.10.0.1", {"start": v(249.41, -6.59) * mm, "mid": v(246.59, -6.59) * mm, "end": v(246.59, -9.41) * mm});
            skLineSegment(sketch, "E92.10.0.2", {"start": v(240, 24) * mm, "end": v(264, 24) * mm, "construction": true});
            skLineSegment(sketch, "E92.10.0.3", {"start": v(248, 16) * mm, "end": v(256, 16) * mm, "construction": true});
            skArc(sketch, "E92.10.0.4", {"start": v(247.07, -9.9) * mm, "mid": v(249.9, -9.9) * mm, "end": v(249.9, -7.07) * mm});
            skLineSegment(sketch, "E92.10.0.5", {"start": v(264, 0) * mm, "end": v(240, -24) * mm, "construction": true});
            skCircle(sketch, "E92.10.0.6", {"center": v(256, -16) * mm, "radius": 2 * mm});
            skLineSegment(sketch, "E92.10.0.7", {"start": v(264, -24) * mm, "end": v(240, -24) * mm, "construction": true});
            skCircle(sketch, "E92.10.0.8", {"center": v(248, 16) * mm, "radius": 2 * mm});
            skCircle(sketch, "E92.10.0.9", {"center": v(256, 16) * mm, "radius": 2 * mm});
            skLineSegment(sketch, "E92.10.0.10", {"start": v(264, -24) * mm, "end": v(240, 0) * mm, "construction": true});
            skLineSegment(sketch, "E92.10.0.11", {"start": v(240, 24) * mm, "end": v(264, 0) * mm, "construction": true});
            skLineSegment(sketch, "E92.10.0.12", {"start": v(264, 24) * mm, "end": v(240, 0) * mm, "construction": true});
            skArc(sketch, "E92.10.0.13", {"start": v(256.93, 9.9) * mm, "mid": v(254.1, 9.9) * mm, "end": v(254.1, 7.07) * mm});
            skArc(sketch, "E92.10.0.14", {"start": v(249.9, 7.07) * mm, "mid": v(249.9, 9.9) * mm, "end": v(247.07, 9.9) * mm});
            skArc(sketch, "E92.10.0.15", {"start": v(254.1, -7.07) * mm, "mid": v(254.1, -9.9) * mm, "end": v(256.93, -9.9) * mm});
            skArc(sketch, "E92.10.0.16", {"start": v(254.59, 6.59) * mm, "mid": v(257.41, 6.59) * mm, "end": v(257.41, 9.41) * mm});
            skLineSegment(sketch, "E92.10.0.17", {"start": v(248, -16) * mm, "end": v(256, -16) * mm, "construction": true});
            skLineSegment(sketch, "E92.10.0.18", {"start": v(240, 0) * mm, "end": v(264, 0) * mm, "construction": true});
            skArc(sketch, "E92.10.0.19", {"start": v(257.41, -9.41) * mm, "mid": v(257.41, -6.59) * mm, "end": v(254.59, -6.59) * mm});
            skCircle(sketch, "E92.10.0.20", {"center": v(248, -16) * mm, "radius": 2 * mm});
            skCircle(sketch, "E92.10.0.21", {"center": v(252, 0) * mm, "radius": 2 * mm});
            skPoint(sketch, "E92.10.0.22", {"position": v(248, -8) * mm});
            skLineSegment(sketch, "E92.10.0.23", {"start": v(264, 0) * mm, "end": v(240, 0) * mm, "construction": true});
            skLineSegment(sketch, "E92.10.0.24", {"start": v(254.59, 6.59) * mm, "end": v(257.41, 9.41) * mm, "construction": true});
            skLineSegment(sketch, "E92.10.0.25", {"start": v(254.1, -7.07) * mm, "end": v(256.93, -9.9) * mm, "construction": true});
            skLineSegment(sketch, "E92.10.0.26", {"start": v(246.59, 9.41) * mm, "end": v(249.41, 6.59) * mm, "construction": true});
            skLineSegment(sketch, "E92.10.0.27", {"start": v(247.07, 9.9) * mm, "end": v(249.9, 7.07) * mm, "construction": true});
            skLineSegment(sketch, "E92.10.0.28", {"start": v(256.93, 9.9) * mm, "end": v(254.1, 7.07) * mm, "construction": true});
            skLineSegment(sketch, "E92.10.0.29", {"start": v(254.59, -6.59) * mm, "end": v(257.41, -9.41) * mm, "construction": true});
            skLineSegment(sketch, "E92.10.0.30", {"start": v(247.07, -9.9) * mm, "end": v(249.9, -7.07) * mm, "construction": true});
            skLineSegment(sketch, "E92.10.0.31", {"start": v(249.41, -6.59) * mm, "end": v(246.59, -9.41) * mm, "construction": true});
            skLineSegment(sketch, "E92.10.0.32", {"start": v(254.1, -7.07) * mm, "end": v(254.59, -6.59) * mm});
            skLineSegment(sketch, "E92.10.0.33", {"start": v(246.59, 9.41) * mm, "end": v(247.07, 9.9) * mm});
            skLineSegment(sketch, "E92.10.0.34", {"start": v(246.59, -9.41) * mm, "end": v(247.07, -9.9) * mm});
            skLineSegment(sketch, "E92.10.0.35", {"start": v(256.93, -9.9) * mm, "end": v(257.41, -9.41) * mm});
            skLineSegment(sketch, "E92.10.0.36", {"start": v(249.41, 6.59) * mm, "end": v(249.9, 7.07) * mm});
            skLineSegment(sketch, "E92.10.0.37", {"start": v(256.93, 9.9) * mm, "end": v(257.41, 9.41) * mm});
            skLineSegment(sketch, "E92.10.0.38", {"start": v(254.1, 7.07) * mm, "end": v(254.59, 6.59) * mm});
            skLineSegment(sketch, "E92.10.0.39", {"start": v(249.41, -6.59) * mm, "end": v(249.9, -7.07) * mm});
            skArc(sketch, "E92.11.0.0", {"start": v(270.59, 9.41) * mm, "mid": v(270.59, 6.59) * mm, "end": v(273.41, 6.59) * mm});
            skArc(sketch, "E92.11.0.1", {"start": v(273.41, -6.59) * mm, "mid": v(270.59, -6.59) * mm, "end": v(270.59, -9.41) * mm});
            skLineSegment(sketch, "E92.11.0.2", {"start": v(264, 24) * mm, "end": v(288, 24) * mm, "construction": true});
            skLineSegment(sketch, "E92.11.0.3", {"start": v(272, 16) * mm, "end": v(280, 16) * mm, "construction": true});
            skArc(sketch, "E92.11.0.4", {"start": v(271.07, -9.9) * mm, "mid": v(273.9, -9.9) * mm, "end": v(273.9, -7.07) * mm});
            skLineSegment(sketch, "E92.11.0.5", {"start": v(288, 0) * mm, "end": v(264, -24) * mm, "construction": true});
            skCircle(sketch, "E92.11.0.6", {"center": v(280, -16) * mm, "radius": 2 * mm});
            skLineSegment(sketch, "E92.11.0.7", {"start": v(288, -24) * mm, "end": v(264, -24) * mm, "construction": true});
            skCircle(sketch, "E92.11.0.8", {"center": v(272, 16) * mm, "radius": 2 * mm});
            skCircle(sketch, "E92.11.0.9", {"center": v(280, 16) * mm, "radius": 2 * mm});
            skLineSegment(sketch, "E92.11.0.10", {"start": v(288, -24) * mm, "end": v(264, 0) * mm, "construction": true});
            skLineSegment(sketch, "E92.11.0.11", {"start": v(264, 24) * mm, "end": v(288, 0) * mm, "construction": true});
            skLineSegment(sketch, "E92.11.0.12", {"start": v(288, 24) * mm, "end": v(264, 0) * mm, "construction": true});
            skArc(sketch, "E92.11.0.13", {"start": v(280.93, 9.9) * mm, "mid": v(278.1, 9.9) * mm, "end": v(278.1, 7.07) * mm});
            skArc(sketch, "E92.11.0.14", {"start": v(273.9, 7.07) * mm, "mid": v(273.9, 9.9) * mm, "end": v(271.07, 9.9) * mm});
            skArc(sketch, "E92.11.0.15", {"start": v(278.1, -7.07) * mm, "mid": v(278.1, -9.9) * mm, "end": v(280.93, -9.9) * mm});
            skArc(sketch, "E92.11.0.16", {"start": v(278.59, 6.59) * mm, "mid": v(281.41, 6.59) * mm, "end": v(281.41, 9.41) * mm});
            skLineSegment(sketch, "E92.11.0.17", {"start": v(272, -16) * mm, "end": v(280, -16) * mm, "construction": true});
            skLineSegment(sketch, "E92.11.0.18", {"start": v(264, 0) * mm, "end": v(288, 0) * mm, "construction": true});
            skArc(sketch, "E92.11.0.19", {"start": v(281.41, -9.41) * mm, "mid": v(281.41, -6.59) * mm, "end": v(278.59, -6.59) * mm});
            skCircle(sketch, "E92.11.0.20", {"center": v(272, -16) * mm, "radius": 2 * mm});
            skCircle(sketch, "E92.11.0.21", {"center": v(276, 0) * mm, "radius": 2 * mm});
            skPoint(sketch, "E92.11.0.22", {"position": v(272, -8) * mm});
            skLineSegment(sketch, "E92.11.0.23", {"start": v(288, 0) * mm, "end": v(264, 0) * mm, "construction": true});
            skLineSegment(sketch, "E92.11.0.24", {"start": v(278.59, 6.59) * mm, "end": v(281.41, 9.41) * mm, "construction": true});
            skLineSegment(sketch, "E92.11.0.25", {"start": v(278.1, -7.07) * mm, "end": v(280.93, -9.9) * mm, "construction": true});
            skLineSegment(sketch, "E92.11.0.26", {"start": v(270.59, 9.41) * mm, "end": v(273.41, 6.59) * mm, "construction": true});
            skLineSegment(sketch, "E92.11.0.27", {"start": v(271.07, 9.9) * mm, "end": v(273.9, 7.07) * mm, "construction": true});
            skLineSegment(sketch, "E92.11.0.28", {"start": v(280.93, 9.9) * mm, "end": v(278.1, 7.07) * mm, "construction": true});
            skLineSegment(sketch, "E92.11.0.29", {"start": v(278.59, -6.59) * mm, "end": v(281.41, -9.41) * mm, "construction": true});
            skLineSegment(sketch, "E92.11.0.30", {"start": v(271.07, -9.9) * mm, "end": v(273.9, -7.07) * mm, "construction": true});
            skLineSegment(sketch, "E92.11.0.31", {"start": v(273.41, -6.59) * mm, "end": v(270.59, -9.41) * mm, "construction": true});
            skLineSegment(sketch, "E92.11.0.32", {"start": v(278.1, -7.07) * mm, "end": v(278.59, -6.59) * mm});
            skLineSegment(sketch, "E92.11.0.33", {"start": v(270.59, 9.41) * mm, "end": v(271.07, 9.9) * mm});
            skLineSegment(sketch, "E92.11.0.34", {"start": v(270.59, -9.41) * mm, "end": v(271.07, -9.9) * mm});
            skLineSegment(sketch, "E92.11.0.35", {"start": v(280.93, -9.9) * mm, "end": v(281.41, -9.41) * mm});
            skLineSegment(sketch, "E92.11.0.36", {"start": v(273.41, 6.59) * mm, "end": v(273.9, 7.07) * mm});
            skLineSegment(sketch, "E92.11.0.37", {"start": v(280.93, 9.9) * mm, "end": v(281.41, 9.41) * mm});
            skLineSegment(sketch, "E92.11.0.38", {"start": v(278.1, 7.07) * mm, "end": v(278.59, 6.59) * mm});
            skLineSegment(sketch, "E92.11.0.39", {"start": v(273.41, -6.59) * mm, "end": v(273.9, -7.07) * mm});
            skArc(sketch, "E92.12.0.0", {"start": v(294.59, 9.41) * mm, "mid": v(294.59, 6.59) * mm, "end": v(297.41, 6.59) * mm});
            skArc(sketch, "E92.12.0.1", {"start": v(297.41, -6.59) * mm, "mid": v(294.59, -6.59) * mm, "end": v(294.59, -9.41) * mm});
            skLineSegment(sketch, "E92.12.0.2", {"start": v(288, 24) * mm, "end": v(312, 24) * mm, "construction": true});
            skLineSegment(sketch, "E92.12.0.3", {"start": v(296, 16) * mm, "end": v(304, 16) * mm, "construction": true});
            skArc(sketch, "E92.12.0.4", {"start": v(295.07, -9.9) * mm, "mid": v(297.9, -9.9) * mm, "end": v(297.9, -7.07) * mm});
            skLineSegment(sketch, "E92.12.0.5", {"start": v(312, 0) * mm, "end": v(288, -24) * mm, "construction": true});
            skCircle(sketch, "E92.12.0.6", {"center": v(304, -16) * mm, "radius": 2 * mm});
            skLineSegment(sketch, "E92.12.0.7", {"start": v(312, -24) * mm, "end": v(288, -24) * mm, "construction": true});
            skCircle(sketch, "E92.12.0.8", {"center": v(296, 16) * mm, "radius": 2 * mm});
            skCircle(sketch, "E92.12.0.9", {"center": v(304, 16) * mm, "radius": 2 * mm});
            skLineSegment(sketch, "E92.12.0.10", {"start": v(312, -24) * mm, "end": v(288, 0) * mm, "construction": true});
            skLineSegment(sketch, "E92.12.0.11", {"start": v(288, 24) * mm, "end": v(312, 0) * mm, "construction": true});
            skLineSegment(sketch, "E92.12.0.12", {"start": v(312, 24) * mm, "end": v(288, 0) * mm, "construction": true});
            skArc(sketch, "E92.12.0.13", {"start": v(304.93, 9.9) * mm, "mid": v(302.1, 9.9) * mm, "end": v(302.1, 7.07) * mm});
            skArc(sketch, "E92.12.0.14", {"start": v(297.9, 7.07) * mm, "mid": v(297.9, 9.9) * mm, "end": v(295.07, 9.9) * mm});
            skArc(sketch, "E92.12.0.15", {"start": v(302.1, -7.07) * mm, "mid": v(302.1, -9.9) * mm, "end": v(304.93, -9.9) * mm});
            skArc(sketch, "E92.12.0.16", {"start": v(302.59, 6.59) * mm, "mid": v(305.41, 6.59) * mm, "end": v(305.41, 9.41) * mm});
            skLineSegment(sketch, "E92.12.0.17", {"start": v(296, -16) * mm, "end": v(304, -16) * mm, "construction": true});
            skLineSegment(sketch, "E92.12.0.18", {"start": v(288, 0) * mm, "end": v(312, 0) * mm, "construction": true});
            skArc(sketch, "E92.12.0.19", {"start": v(305.41, -9.41) * mm, "mid": v(305.41, -6.59) * mm, "end": v(302.59, -6.59) * mm});
            skCircle(sketch, "E92.12.0.20", {"center": v(296, -16) * mm, "radius": 2 * mm});
            skCircle(sketch, "E92.12.0.21", {"center": v(300, 0) * mm, "radius": 2 * mm});
            skPoint(sketch, "E92.12.0.22", {"position": v(296, -8) * mm});
            skLineSegment(sketch, "E92.12.0.23", {"start": v(312, 0) * mm, "end": v(288, 0) * mm, "construction": true});
            skLineSegment(sketch, "E92.12.0.24", {"start": v(302.59, 6.59) * mm, "end": v(305.41, 9.41) * mm, "construction": true});
            skLineSegment(sketch, "E92.12.0.25", {"start": v(302.1, -7.07) * mm, "end": v(304.93, -9.9) * mm, "construction": true});
            skLineSegment(sketch, "E92.12.0.26", {"start": v(294.59, 9.41) * mm, "end": v(297.41, 6.59) * mm, "construction": true});
            skLineSegment(sketch, "E92.12.0.27", {"start": v(295.07, 9.9) * mm, "end": v(297.9, 7.07) * mm, "construction": true});
            skLineSegment(sketch, "E92.12.0.28", {"start": v(304.93, 9.9) * mm, "end": v(302.1, 7.07) * mm, "construction": true});
            skLineSegment(sketch, "E92.12.0.29", {"start": v(302.59, -6.59) * mm, "end": v(305.41, -9.41) * mm, "construction": true});
            skLineSegment(sketch, "E92.12.0.30", {"start": v(295.07, -9.9) * mm, "end": v(297.9, -7.07) * mm, "construction": true});
            skLineSegment(sketch, "E92.12.0.31", {"start": v(297.41, -6.59) * mm, "end": v(294.59, -9.41) * mm, "construction": true});
            skLineSegment(sketch, "E92.12.0.32", {"start": v(302.1, -7.07) * mm, "end": v(302.59, -6.59) * mm});
            skLineSegment(sketch, "E92.12.0.33", {"start": v(294.59, 9.41) * mm, "end": v(295.07, 9.9) * mm});
            skLineSegment(sketch, "E92.12.0.34", {"start": v(294.59, -9.41) * mm, "end": v(295.07, -9.9) * mm});
            skLineSegment(sketch, "E92.12.0.35", {"start": v(304.93, -9.9) * mm, "end": v(305.41, -9.41) * mm});
            skLineSegment(sketch, "E92.12.0.36", {"start": v(297.41, 6.59) * mm, "end": v(297.9, 7.07) * mm});
            skLineSegment(sketch, "E92.12.0.37", {"start": v(304.93, 9.9) * mm, "end": v(305.41, 9.41) * mm});
            skLineSegment(sketch, "E92.12.0.38", {"start": v(302.1, 7.07) * mm, "end": v(302.59, 6.59) * mm});
            skLineSegment(sketch, "E92.12.0.39", {"start": v(297.41, -6.59) * mm, "end": v(297.9, -7.07) * mm});
            skArc(sketch, "E92.13.0.0", {"start": v(318.59, 9.41) * mm, "mid": v(318.59, 6.59) * mm, "end": v(321.41, 6.59) * mm});
            skArc(sketch, "E92.13.0.1", {"start": v(321.41, -6.59) * mm, "mid": v(318.59, -6.59) * mm, "end": v(318.59, -9.41) * mm});
            skLineSegment(sketch, "E92.13.0.2", {"start": v(312, 24) * mm, "end": v(336, 24) * mm, "construction": true});
            skLineSegment(sketch, "E92.13.0.3", {"start": v(320, 16) * mm, "end": v(328, 16) * mm, "construction": true});
            skArc(sketch, "E92.13.0.4", {"start": v(319.07, -9.9) * mm, "mid": v(321.9, -9.9) * mm, "end": v(321.9, -7.07) * mm});
            skLineSegment(sketch, "E92.13.0.5", {"start": v(336, 0) * mm, "end": v(312, -24) * mm, "construction": true});
            skCircle(sketch, "E92.13.0.6", {"center": v(328, -16) * mm, "radius": 2 * mm});
            skLineSegment(sketch, "E92.13.0.7", {"start": v(336, -24) * mm, "end": v(312, -24) * mm, "construction": true});
            skCircle(sketch, "E92.13.0.8", {"center": v(320, 16) * mm, "radius": 2 * mm});
            skCircle(sketch, "E92.13.0.9", {"center": v(328, 16) * mm, "radius": 2 * mm});
            skLineSegment(sketch, "E92.13.0.10", {"start": v(336, -24) * mm, "end": v(312, 0) * mm, "construction": true});
            skLineSegment(sketch, "E92.13.0.11", {"start": v(312, 24) * mm, "end": v(336, 0) * mm, "construction": true});
            skLineSegment(sketch, "E92.13.0.12", {"start": v(336, 24) * mm, "end": v(312, 0) * mm, "construction": true});
            skArc(sketch, "E92.13.0.13", {"start": v(328.93, 9.9) * mm, "mid": v(326.1, 9.9) * mm, "end": v(326.1, 7.07) * mm});
            skArc(sketch, "E92.13.0.14", {"start": v(321.9, 7.07) * mm, "mid": v(321.9, 9.9) * mm, "end": v(319.07, 9.9) * mm});
            skArc(sketch, "E92.13.0.15", {"start": v(326.1, -7.07) * mm, "mid": v(326.1, -9.9) * mm, "end": v(328.93, -9.9) * mm});
            skArc(sketch, "E92.13.0.16", {"start": v(326.59, 6.59) * mm, "mid": v(329.41, 6.59) * mm, "end": v(329.41, 9.41) * mm});
            skLineSegment(sketch, "E92.13.0.17", {"start": v(320, -16) * mm, "end": v(328, -16) * mm, "construction": true});
            skLineSegment(sketch, "E92.13.0.18", {"start": v(312, 0) * mm, "end": v(336, 0) * mm, "construction": true});
            skArc(sketch, "E92.13.0.19", {"start": v(329.41, -9.41) * mm, "mid": v(329.41, -6.59) * mm, "end": v(326.59, -6.59) * mm});
            skCircle(sketch, "E92.13.0.20", {"center": v(320, -16) * mm, "radius": 2 * mm});
            skCircle(sketch, "E92.13.0.21", {"center": v(324, 0) * mm, "radius": 2 * mm});
            skPoint(sketch, "E92.13.0.22", {"position": v(320, -8) * mm});
            skLineSegment(sketch, "E92.13.0.23", {"start": v(336, 0) * mm, "end": v(312, 0) * mm, "construction": true});
            skLineSegment(sketch, "E92.13.0.24", {"start": v(326.59, 6.59) * mm, "end": v(329.41, 9.41) * mm, "construction": true});
            skLineSegment(sketch, "E92.13.0.25", {"start": v(326.1, -7.07) * mm, "end": v(328.93, -9.9) * mm, "construction": true});
            skLineSegment(sketch, "E92.13.0.26", {"start": v(318.59, 9.41) * mm, "end": v(321.41, 6.59) * mm, "construction": true});
            skLineSegment(sketch, "E92.13.0.27", {"start": v(319.07, 9.9) * mm, "end": v(321.9, 7.07) * mm, "construction": true});
            skLineSegment(sketch, "E92.13.0.28", {"start": v(328.93, 9.9) * mm, "end": v(326.1, 7.07) * mm, "construction": true});
            skLineSegment(sketch, "E92.13.0.29", {"start": v(326.59, -6.59) * mm, "end": v(329.41, -9.41) * mm, "construction": true});
            skLineSegment(sketch, "E92.13.0.30", {"start": v(319.07, -9.9) * mm, "end": v(321.9, -7.07) * mm, "construction": true});
            skLineSegment(sketch, "E92.13.0.31", {"start": v(321.41, -6.59) * mm, "end": v(318.59, -9.41) * mm, "construction": true});
            skLineSegment(sketch, "E92.13.0.32", {"start": v(326.1, -7.07) * mm, "end": v(326.59, -6.59) * mm});
            skLineSegment(sketch, "E92.13.0.33", {"start": v(318.59, 9.41) * mm, "end": v(319.07, 9.9) * mm});
            skLineSegment(sketch, "E92.13.0.34", {"start": v(318.59, -9.41) * mm, "end": v(319.07, -9.9) * mm});
            skLineSegment(sketch, "E92.13.0.35", {"start": v(328.93, -9.9) * mm, "end": v(329.41, -9.41) * mm});
            skLineSegment(sketch, "E92.13.0.36", {"start": v(321.41, 6.59) * mm, "end": v(321.9, 7.07) * mm});
            skLineSegment(sketch, "E92.13.0.37", {"start": v(328.93, 9.9) * mm, "end": v(329.41, 9.41) * mm});
            skLineSegment(sketch, "E92.13.0.38", {"start": v(326.1, 7.07) * mm, "end": v(326.59, 6.59) * mm});
            skLineSegment(sketch, "E92.13.0.39", {"start": v(321.41, -6.59) * mm, "end": v(321.9, -7.07) * mm});
            skArc(sketch, "E92.14.0.0", {"start": v(342.59, 9.41) * mm, "mid": v(342.59, 6.59) * mm, "end": v(345.41, 6.59) * mm});
            skArc(sketch, "E92.14.0.1", {"start": v(345.41, -6.59) * mm, "mid": v(342.59, -6.59) * mm, "end": v(342.59, -9.41) * mm});
            skLineSegment(sketch, "E92.14.0.2", {"start": v(336, 24) * mm, "end": v(360, 24) * mm, "construction": true});
            skLineSegment(sketch, "E92.14.0.3", {"start": v(344, 16) * mm, "end": v(352, 16) * mm, "construction": true});
            skArc(sketch, "E92.14.0.4", {"start": v(343.07, -9.9) * mm, "mid": v(345.9, -9.9) * mm, "end": v(345.9, -7.07) * mm});
            skLineSegment(sketch, "E92.14.0.5", {"start": v(360, 0) * mm, "end": v(336, -24) * mm, "construction": true});
            skCircle(sketch, "E92.14.0.6", {"center": v(352, -16) * mm, "radius": 2 * mm});
            skLineSegment(sketch, "E92.14.0.7", {"start": v(360, -24) * mm, "end": v(336, -24) * mm, "construction": true});
            skCircle(sketch, "E92.14.0.8", {"center": v(344, 16) * mm, "radius": 2 * mm});
            skCircle(sketch, "E92.14.0.9", {"center": v(352, 16) * mm, "radius": 2 * mm});
            skLineSegment(sketch, "E92.14.0.10", {"start": v(360, -24) * mm, "end": v(336, 0) * mm, "construction": true});
            skLineSegment(sketch, "E92.14.0.11", {"start": v(336, 24) * mm, "end": v(360, 0) * mm, "construction": true});
            skLineSegment(sketch, "E92.14.0.12", {"start": v(360, 24) * mm, "end": v(336, 0) * mm, "construction": true});
            skArc(sketch, "E92.14.0.13", {"start": v(352.93, 9.9) * mm, "mid": v(350.1, 9.9) * mm, "end": v(350.1, 7.07) * mm});
            skArc(sketch, "E92.14.0.14", {"start": v(345.9, 7.07) * mm, "mid": v(345.9, 9.9) * mm, "end": v(343.07, 9.9) * mm});
            skArc(sketch, "E92.14.0.15", {"start": v(350.1, -7.07) * mm, "mid": v(350.1, -9.9) * mm, "end": v(352.93, -9.9) * mm});
            skArc(sketch, "E92.14.0.16", {"start": v(350.59, 6.59) * mm, "mid": v(353.41, 6.59) * mm, "end": v(353.41, 9.41) * mm});
            skLineSegment(sketch, "E92.14.0.17", {"start": v(344, -16) * mm, "end": v(352, -16) * mm, "construction": true});
            skLineSegment(sketch, "E92.14.0.18", {"start": v(336, 0) * mm, "end": v(360, 0) * mm, "construction": true});
            skArc(sketch, "E92.14.0.19", {"start": v(353.41, -9.41) * mm, "mid": v(353.41, -6.59) * mm, "end": v(350.59, -6.59) * mm});
            skCircle(sketch, "E92.14.0.20", {"center": v(344, -16) * mm, "radius": 2 * mm});
            skCircle(sketch, "E92.14.0.21", {"center": v(348, 0) * mm, "radius": 2 * mm});
            skPoint(sketch, "E92.14.0.22", {"position": v(344, -8) * mm});
            skLineSegment(sketch, "E92.14.0.23", {"start": v(360, 0) * mm, "end": v(336, 0) * mm, "construction": true});
            skLineSegment(sketch, "E92.14.0.24", {"start": v(350.59, 6.59) * mm, "end": v(353.41, 9.41) * mm, "construction": true});
            skLineSegment(sketch, "E92.14.0.25", {"start": v(350.1, -7.07) * mm, "end": v(352.93, -9.9) * mm, "construction": true});
            skLineSegment(sketch, "E92.14.0.26", {"start": v(342.59, 9.41) * mm, "end": v(345.41, 6.59) * mm, "construction": true});
            skLineSegment(sketch, "E92.14.0.27", {"start": v(343.07, 9.9) * mm, "end": v(345.9, 7.07) * mm, "construction": true});
            skLineSegment(sketch, "E92.14.0.28", {"start": v(352.93, 9.9) * mm, "end": v(350.1, 7.07) * mm, "construction": true});
            skLineSegment(sketch, "E92.14.0.29", {"start": v(350.59, -6.59) * mm, "end": v(353.41, -9.41) * mm, "construction": true});
            skLineSegment(sketch, "E92.14.0.30", {"start": v(343.07, -9.9) * mm, "end": v(345.9, -7.07) * mm, "construction": true});
            skLineSegment(sketch, "E92.14.0.31", {"start": v(345.41, -6.59) * mm, "end": v(342.59, -9.41) * mm, "construction": true});
            skLineSegment(sketch, "E92.14.0.32", {"start": v(350.1, -7.07) * mm, "end": v(350.59, -6.59) * mm});
            skLineSegment(sketch, "E92.14.0.33", {"start": v(342.59, 9.41) * mm, "end": v(343.07, 9.9) * mm});
            skLineSegment(sketch, "E92.14.0.34", {"start": v(342.59, -9.41) * mm, "end": v(343.07, -9.9) * mm});
            skLineSegment(sketch, "E92.14.0.35", {"start": v(352.93, -9.9) * mm, "end": v(353.41, -9.41) * mm});
            skLineSegment(sketch, "E92.14.0.36", {"start": v(345.41, 6.59) * mm, "end": v(345.9, 7.07) * mm});
            skLineSegment(sketch, "E92.14.0.37", {"start": v(352.93, 9.9) * mm, "end": v(353.41, 9.41) * mm});
            skLineSegment(sketch, "E92.14.0.38", {"start": v(350.1, 7.07) * mm, "end": v(350.59, 6.59) * mm});
            skLineSegment(sketch, "E92.14.0.39", {"start": v(345.41, -6.59) * mm, "end": v(345.9, -7.07) * mm});
            skArc(sketch, "E92.15.0.0", {"start": v(366.59, 9.41) * mm, "mid": v(366.59, 6.59) * mm, "end": v(369.41, 6.59) * mm});
            skArc(sketch, "E92.15.0.1", {"start": v(369.41, -6.59) * mm, "mid": v(366.59, -6.59) * mm, "end": v(366.59, -9.41) * mm});
            skLineSegment(sketch, "E92.15.0.2", {"start": v(360, 24) * mm, "end": v(384, 24) * mm, "construction": true});
            skLineSegment(sketch, "E92.15.0.3", {"start": v(368, 16) * mm, "end": v(376, 16) * mm, "construction": true});
            skArc(sketch, "E92.15.0.4", {"start": v(367.07, -9.9) * mm, "mid": v(369.9, -9.9) * mm, "end": v(369.9, -7.07) * mm});
            skLineSegment(sketch, "E92.15.0.5", {"start": v(384, 0) * mm, "end": v(360, -24) * mm, "construction": true});
            skCircle(sketch, "E92.15.0.6", {"center": v(376, -16) * mm, "radius": 2 * mm});
            skLineSegment(sketch, "E92.15.0.7", {"start": v(384, -24) * mm, "end": v(360, -24) * mm, "construction": true});
            skCircle(sketch, "E92.15.0.8", {"center": v(368, 16) * mm, "radius": 2 * mm});
            skCircle(sketch, "E92.15.0.9", {"center": v(376, 16) * mm, "radius": 2 * mm});
            skLineSegment(sketch, "E92.15.0.10", {"start": v(384, -24) * mm, "end": v(360, 0) * mm, "construction": true});
            skLineSegment(sketch, "E92.15.0.11", {"start": v(360, 24) * mm, "end": v(384, 0) * mm, "construction": true});
            skLineSegment(sketch, "E92.15.0.12", {"start": v(384, 24) * mm, "end": v(360, 0) * mm, "construction": true});
            skArc(sketch, "E92.15.0.13", {"start": v(376.93, 9.9) * mm, "mid": v(374.1, 9.9) * mm, "end": v(374.1, 7.07) * mm});
            skArc(sketch, "E92.15.0.14", {"start": v(369.9, 7.07) * mm, "mid": v(369.9, 9.9) * mm, "end": v(367.07, 9.9) * mm});
            skArc(sketch, "E92.15.0.15", {"start": v(374.1, -7.07) * mm, "mid": v(374.1, -9.9) * mm, "end": v(376.93, -9.9) * mm});
            skArc(sketch, "E92.15.0.16", {"start": v(374.59, 6.59) * mm, "mid": v(377.41, 6.59) * mm, "end": v(377.41, 9.41) * mm});
            skLineSegment(sketch, "E92.15.0.17", {"start": v(368, -16) * mm, "end": v(376, -16) * mm, "construction": true});
            skLineSegment(sketch, "E92.15.0.18", {"start": v(360, 0) * mm, "end": v(384, 0) * mm, "construction": true});
            skArc(sketch, "E92.15.0.19", {"start": v(377.41, -9.41) * mm, "mid": v(377.41, -6.59) * mm, "end": v(374.59, -6.59) * mm});
            skCircle(sketch, "E92.15.0.20", {"center": v(368, -16) * mm, "radius": 2 * mm});
            skCircle(sketch, "E92.15.0.21", {"center": v(372, 0) * mm, "radius": 2 * mm});
            skPoint(sketch, "E92.15.0.22", {"position": v(368, -8) * mm});
            skLineSegment(sketch, "E92.15.0.23", {"start": v(384, 0) * mm, "end": v(360, 0) * mm, "construction": true});
            skLineSegment(sketch, "E92.15.0.24", {"start": v(374.59, 6.59) * mm, "end": v(377.41, 9.41) * mm, "construction": true});
            skLineSegment(sketch, "E92.15.0.25", {"start": v(374.1, -7.07) * mm, "end": v(376.93, -9.9) * mm, "construction": true});
            skLineSegment(sketch, "E92.15.0.26", {"start": v(366.59, 9.41) * mm, "end": v(369.41, 6.59) * mm, "construction": true});
            skLineSegment(sketch, "E92.15.0.27", {"start": v(367.07, 9.9) * mm, "end": v(369.9, 7.07) * mm, "construction": true});
            skLineSegment(sketch, "E92.15.0.28", {"start": v(376.93, 9.9) * mm, "end": v(374.1, 7.07) * mm, "construction": true});
            skLineSegment(sketch, "E92.15.0.29", {"start": v(374.59, -6.59) * mm, "end": v(377.41, -9.41) * mm, "construction": true});
            skLineSegment(sketch, "E92.15.0.30", {"start": v(367.07, -9.9) * mm, "end": v(369.9, -7.07) * mm, "construction": true});
            skLineSegment(sketch, "E92.15.0.31", {"start": v(369.41, -6.59) * mm, "end": v(366.59, -9.41) * mm, "construction": true});
            skLineSegment(sketch, "E92.15.0.32", {"start": v(374.1, -7.07) * mm, "end": v(374.59, -6.59) * mm});
            skLineSegment(sketch, "E92.15.0.33", {"start": v(366.59, 9.41) * mm, "end": v(367.07, 9.9) * mm});
            skLineSegment(sketch, "E92.15.0.34", {"start": v(366.59, -9.41) * mm, "end": v(367.07, -9.9) * mm});
            skLineSegment(sketch, "E92.15.0.35", {"start": v(376.93, -9.9) * mm, "end": v(377.41, -9.41) * mm});
            skLineSegment(sketch, "E92.15.0.36", {"start": v(369.41, 6.59) * mm, "end": v(369.9, 7.07) * mm});
            skLineSegment(sketch, "E92.15.0.37", {"start": v(376.93, 9.9) * mm, "end": v(377.41, 9.41) * mm});
            skLineSegment(sketch, "E92.15.0.38", {"start": v(374.1, 7.07) * mm, "end": v(374.59, 6.59) * mm});
            skLineSegment(sketch, "E92.15.0.39", {"start": v(369.41, -6.59) * mm, "end": v(369.9, -7.07) * mm});
            skArc(sketch, "E92.16.0.0", {"start": v(390.59, 9.41) * mm, "mid": v(390.59, 6.59) * mm, "end": v(393.41, 6.59) * mm});
            skArc(sketch, "E92.16.0.1", {"start": v(393.41, -6.59) * mm, "mid": v(390.59, -6.59) * mm, "end": v(390.59, -9.41) * mm});
            skLineSegment(sketch, "E92.16.0.2", {"start": v(384, 24) * mm, "end": v(408, 24) * mm, "construction": true});
            skLineSegment(sketch, "E92.16.0.3", {"start": v(392, 16) * mm, "end": v(400, 16) * mm, "construction": true});
            skArc(sketch, "E92.16.0.4", {"start": v(391.07, -9.9) * mm, "mid": v(393.9, -9.9) * mm, "end": v(393.9, -7.07) * mm});
            skLineSegment(sketch, "E92.16.0.5", {"start": v(408, 0) * mm, "end": v(384, -24) * mm, "construction": true});
            skCircle(sketch, "E92.16.0.6", {"center": v(400, -16) * mm, "radius": 2 * mm});
            skLineSegment(sketch, "E92.16.0.7", {"start": v(408, -24) * mm, "end": v(384, -24) * mm, "construction": true});
            skCircle(sketch, "E92.16.0.8", {"center": v(392, 16) * mm, "radius": 2 * mm});
            skCircle(sketch, "E92.16.0.9", {"center": v(400, 16) * mm, "radius": 2 * mm});
            skLineSegment(sketch, "E92.16.0.10", {"start": v(408, -24) * mm, "end": v(384, 0) * mm, "construction": true});
            skLineSegment(sketch, "E92.16.0.11", {"start": v(384, 24) * mm, "end": v(408, 0) * mm, "construction": true});
            skLineSegment(sketch, "E92.16.0.12", {"start": v(408, 24) * mm, "end": v(384, 0) * mm, "construction": true});
            skArc(sketch, "E92.16.0.13", {"start": v(400.93, 9.9) * mm, "mid": v(398.1, 9.9) * mm, "end": v(398.1, 7.07) * mm});
            skArc(sketch, "E92.16.0.14", {"start": v(393.9, 7.07) * mm, "mid": v(393.9, 9.9) * mm, "end": v(391.07, 9.9) * mm});
            skArc(sketch, "E92.16.0.15", {"start": v(398.1, -7.07) * mm, "mid": v(398.1, -9.9) * mm, "end": v(400.93, -9.9) * mm});
            skArc(sketch, "E92.16.0.16", {"start": v(398.59, 6.59) * mm, "mid": v(401.41, 6.59) * mm, "end": v(401.41, 9.41) * mm});
            skLineSegment(sketch, "E92.16.0.17", {"start": v(392, -16) * mm, "end": v(400, -16) * mm, "construction": true});
            skLineSegment(sketch, "E92.16.0.18", {"start": v(384, 0) * mm, "end": v(408, 0) * mm, "construction": true});
            skArc(sketch, "E92.16.0.19", {"start": v(401.41, -9.41) * mm, "mid": v(401.41, -6.59) * mm, "end": v(398.59, -6.59) * mm});
            skCircle(sketch, "E92.16.0.20", {"center": v(392, -16) * mm, "radius": 2 * mm});
            skCircle(sketch, "E92.16.0.21", {"center": v(396, 0) * mm, "radius": 2 * mm});
            skPoint(sketch, "E92.16.0.22", {"position": v(392, -8) * mm});
            skLineSegment(sketch, "E92.16.0.23", {"start": v(408, 0) * mm, "end": v(384, 0) * mm, "construction": true});
            skLineSegment(sketch, "E92.16.0.24", {"start": v(398.59, 6.59) * mm, "end": v(401.41, 9.41) * mm, "construction": true});
            skLineSegment(sketch, "E92.16.0.25", {"start": v(398.1, -7.07) * mm, "end": v(400.93, -9.9) * mm, "construction": true});
            skLineSegment(sketch, "E92.16.0.26", {"start": v(390.59, 9.41) * mm, "end": v(393.41, 6.59) * mm, "construction": true});
            skLineSegment(sketch, "E92.16.0.27", {"start": v(391.07, 9.9) * mm, "end": v(393.9, 7.07) * mm, "construction": true});
            skLineSegment(sketch, "E92.16.0.28", {"start": v(400.93, 9.9) * mm, "end": v(398.1, 7.07) * mm, "construction": true});
            skLineSegment(sketch, "E92.16.0.29", {"start": v(398.59, -6.59) * mm, "end": v(401.41, -9.41) * mm, "construction": true});
            skLineSegment(sketch, "E92.16.0.30", {"start": v(391.07, -9.9) * mm, "end": v(393.9, -7.07) * mm, "construction": true});
            skLineSegment(sketch, "E92.16.0.31", {"start": v(393.41, -6.59) * mm, "end": v(390.59, -9.41) * mm, "construction": true});
            skLineSegment(sketch, "E92.16.0.32", {"start": v(398.1, -7.07) * mm, "end": v(398.59, -6.59) * mm});
            skLineSegment(sketch, "E92.16.0.33", {"start": v(390.59, 9.41) * mm, "end": v(391.07, 9.9) * mm});
            skLineSegment(sketch, "E92.16.0.34", {"start": v(390.59, -9.41) * mm, "end": v(391.07, -9.9) * mm});
            skLineSegment(sketch, "E92.16.0.35", {"start": v(400.93, -9.9) * mm, "end": v(401.41, -9.41) * mm});
            skLineSegment(sketch, "E92.16.0.36", {"start": v(393.41, 6.59) * mm, "end": v(393.9, 7.07) * mm});
            skLineSegment(sketch, "E92.16.0.37", {"start": v(400.93, 9.9) * mm, "end": v(401.41, 9.41) * mm});
            skLineSegment(sketch, "E92.16.0.38", {"start": v(398.1, 7.07) * mm, "end": v(398.59, 6.59) * mm});
            skLineSegment(sketch, "E92.16.0.39", {"start": v(393.41, -6.59) * mm, "end": v(393.9, -7.07) * mm});
            skArc(sketch, "E92.17.0.0", {"start": v(414.59, 9.41) * mm, "mid": v(414.59, 6.59) * mm, "end": v(417.41, 6.59) * mm});
            skArc(sketch, "E92.17.0.1", {"start": v(417.41, -6.59) * mm, "mid": v(414.59, -6.59) * mm, "end": v(414.59, -9.41) * mm});
            skLineSegment(sketch, "E92.17.0.2", {"start": v(408, 24) * mm, "end": v(432, 24) * mm, "construction": true});
            skLineSegment(sketch, "E92.17.0.3", {"start": v(416, 16) * mm, "end": v(424, 16) * mm, "construction": true});
            skArc(sketch, "E92.17.0.4", {"start": v(415.07, -9.9) * mm, "mid": v(417.9, -9.9) * mm, "end": v(417.9, -7.07) * mm});
            skLineSegment(sketch, "E92.17.0.5", {"start": v(432, 0) * mm, "end": v(408, -24) * mm, "construction": true});
            skCircle(sketch, "E92.17.0.6", {"center": v(424, -16) * mm, "radius": 2 * mm});
            skLineSegment(sketch, "E92.17.0.7", {"start": v(432, -24) * mm, "end": v(408, -24) * mm, "construction": true});
            skCircle(sketch, "E92.17.0.8", {"center": v(416, 16) * mm, "radius": 2 * mm});
            skCircle(sketch, "E92.17.0.9", {"center": v(424, 16) * mm, "radius": 2 * mm});
            skLineSegment(sketch, "E92.17.0.10", {"start": v(432, -24) * mm, "end": v(408, 0) * mm, "construction": true});
            skLineSegment(sketch, "E92.17.0.11", {"start": v(408, 24) * mm, "end": v(432, 0) * mm, "construction": true});
            skLineSegment(sketch, "E92.17.0.12", {"start": v(432, 24) * mm, "end": v(408, 0) * mm, "construction": true});
            skArc(sketch, "E92.17.0.13", {"start": v(424.93, 9.9) * mm, "mid": v(422.1, 9.9) * mm, "end": v(422.1, 7.07) * mm});
            skArc(sketch, "E92.17.0.14", {"start": v(417.9, 7.07) * mm, "mid": v(417.9, 9.9) * mm, "end": v(415.07, 9.9) * mm});
            skArc(sketch, "E92.17.0.15", {"start": v(422.1, -7.07) * mm, "mid": v(422.1, -9.9) * mm, "end": v(424.93, -9.9) * mm});
            skArc(sketch, "E92.17.0.16", {"start": v(422.59, 6.59) * mm, "mid": v(425.41, 6.59) * mm, "end": v(425.41, 9.41) * mm});
            skLineSegment(sketch, "E92.17.0.17", {"start": v(416, -16) * mm, "end": v(424, -16) * mm, "construction": true});
            skLineSegment(sketch, "E92.17.0.18", {"start": v(408, 0) * mm, "end": v(432, 0) * mm, "construction": true});
            skArc(sketch, "E92.17.0.19", {"start": v(425.41, -9.41) * mm, "mid": v(425.41, -6.59) * mm, "end": v(422.59, -6.59) * mm});
            skCircle(sketch, "E92.17.0.20", {"center": v(416, -16) * mm, "radius": 2 * mm});
            skCircle(sketch, "E92.17.0.21", {"center": v(420, 0) * mm, "radius": 2 * mm});
            skPoint(sketch, "E92.17.0.22", {"position": v(416, -8) * mm});
            skLineSegment(sketch, "E92.17.0.23", {"start": v(432, 0) * mm, "end": v(408, 0) * mm, "construction": true});
            skLineSegment(sketch, "E92.17.0.24", {"start": v(422.59, 6.59) * mm, "end": v(425.41, 9.41) * mm, "construction": true});
            skLineSegment(sketch, "E92.17.0.25", {"start": v(422.1, -7.07) * mm, "end": v(424.93, -9.9) * mm, "construction": true});
            skLineSegment(sketch, "E92.17.0.26", {"start": v(414.59, 9.41) * mm, "end": v(417.41, 6.59) * mm, "construction": true});
            skLineSegment(sketch, "E92.17.0.27", {"start": v(415.07, 9.9) * mm, "end": v(417.9, 7.07) * mm, "construction": true});
            skLineSegment(sketch, "E92.17.0.28", {"start": v(424.93, 9.9) * mm, "end": v(422.1, 7.07) * mm, "construction": true});
            skLineSegment(sketch, "E92.17.0.29", {"start": v(422.59, -6.59) * mm, "end": v(425.41, -9.41) * mm, "construction": true});
            skLineSegment(sketch, "E92.17.0.30", {"start": v(415.07, -9.9) * mm, "end": v(417.9, -7.07) * mm, "construction": true});
            skLineSegment(sketch, "E92.17.0.31", {"start": v(417.41, -6.59) * mm, "end": v(414.59, -9.41) * mm, "construction": true});
            skLineSegment(sketch, "E92.17.0.32", {"start": v(422.1, -7.07) * mm, "end": v(422.59, -6.59) * mm});
            skLineSegment(sketch, "E92.17.0.33", {"start": v(414.59, 9.41) * mm, "end": v(415.07, 9.9) * mm});
            skLineSegment(sketch, "E92.17.0.34", {"start": v(414.59, -9.41) * mm, "end": v(415.07, -9.9) * mm});
            skLineSegment(sketch, "E92.17.0.35", {"start": v(424.93, -9.9) * mm, "end": v(425.41, -9.41) * mm});
            skLineSegment(sketch, "E92.17.0.36", {"start": v(417.41, 6.59) * mm, "end": v(417.9, 7.07) * mm});
            skLineSegment(sketch, "E92.17.0.37", {"start": v(424.93, 9.9) * mm, "end": v(425.41, 9.41) * mm});
            skLineSegment(sketch, "E92.17.0.38", {"start": v(422.1, 7.07) * mm, "end": v(422.59, 6.59) * mm});
            skLineSegment(sketch, "E92.17.0.39", {"start": v(417.41, -6.59) * mm, "end": v(417.9, -7.07) * mm});
            skArc(sketch, "E92.18.0.0", {"start": v(438.59, 9.41) * mm, "mid": v(438.59, 6.59) * mm, "end": v(441.41, 6.59) * mm});
            skArc(sketch, "E92.18.0.1", {"start": v(441.41, -6.59) * mm, "mid": v(438.59, -6.59) * mm, "end": v(438.59, -9.41) * mm});
            skLineSegment(sketch, "E92.18.0.2", {"start": v(432, 24) * mm, "end": v(456, 24) * mm, "construction": true});
            skLineSegment(sketch, "E92.18.0.3", {"start": v(440, 16) * mm, "end": v(448, 16) * mm, "construction": true});
            skArc(sketch, "E92.18.0.4", {"start": v(439.07, -9.9) * mm, "mid": v(441.9, -9.9) * mm, "end": v(441.9, -7.07) * mm});
            skLineSegment(sketch, "E92.18.0.5", {"start": v(456, 0) * mm, "end": v(432, -24) * mm, "construction": true});
            skCircle(sketch, "E92.18.0.6", {"center": v(448, -16) * mm, "radius": 2 * mm});
            skLineSegment(sketch, "E92.18.0.7", {"start": v(456, -24) * mm, "end": v(432, -24) * mm, "construction": true});
            skCircle(sketch, "E92.18.0.8", {"center": v(440, 16) * mm, "radius": 2 * mm});
            skCircle(sketch, "E92.18.0.9", {"center": v(448, 16) * mm, "radius": 2 * mm});
            skLineSegment(sketch, "E92.18.0.10", {"start": v(456, -24) * mm, "end": v(432, 0) * mm, "construction": true});
            skLineSegment(sketch, "E92.18.0.11", {"start": v(432, 24) * mm, "end": v(456, 0) * mm, "construction": true});
            skLineSegment(sketch, "E92.18.0.12", {"start": v(456, 24) * mm, "end": v(432, 0) * mm, "construction": true});
            skArc(sketch, "E92.18.0.13", {"start": v(448.93, 9.9) * mm, "mid": v(446.1, 9.9) * mm, "end": v(446.1, 7.07) * mm});
            skArc(sketch, "E92.18.0.14", {"start": v(441.9, 7.07) * mm, "mid": v(441.9, 9.9) * mm, "end": v(439.07, 9.9) * mm});
            skArc(sketch, "E92.18.0.15", {"start": v(446.1, -7.07) * mm, "mid": v(446.1, -9.9) * mm, "end": v(448.93, -9.9) * mm});
            skArc(sketch, "E92.18.0.16", {"start": v(446.59, 6.59) * mm, "mid": v(449.41, 6.59) * mm, "end": v(449.41, 9.41) * mm});
            skLineSegment(sketch, "E92.18.0.17", {"start": v(440, -16) * mm, "end": v(448, -16) * mm, "construction": true});
            skLineSegment(sketch, "E92.18.0.18", {"start": v(432, 0) * mm, "end": v(456, 0) * mm, "construction": true});
            skArc(sketch, "E92.18.0.19", {"start": v(449.41, -9.41) * mm, "mid": v(449.41, -6.59) * mm, "end": v(446.59, -6.59) * mm});
            skCircle(sketch, "E92.18.0.20", {"center": v(440, -16) * mm, "radius": 2 * mm});
            skCircle(sketch, "E92.18.0.21", {"center": v(444, 0) * mm, "radius": 2 * mm});
            skPoint(sketch, "E92.18.0.22", {"position": v(440, -8) * mm});
            skLineSegment(sketch, "E92.18.0.23", {"start": v(456, 0) * mm, "end": v(432, 0) * mm, "construction": true});
            skLineSegment(sketch, "E92.18.0.24", {"start": v(446.59, 6.59) * mm, "end": v(449.41, 9.41) * mm, "construction": true});
            skLineSegment(sketch, "E92.18.0.25", {"start": v(446.1, -7.07) * mm, "end": v(448.93, -9.9) * mm, "construction": true});
            skLineSegment(sketch, "E92.18.0.26", {"start": v(438.59, 9.41) * mm, "end": v(441.41, 6.59) * mm, "construction": true});
            skLineSegment(sketch, "E92.18.0.27", {"start": v(439.07, 9.9) * mm, "end": v(441.9, 7.07) * mm, "construction": true});
            skLineSegment(sketch, "E92.18.0.28", {"start": v(448.93, 9.9) * mm, "end": v(446.1, 7.07) * mm, "construction": true});
            skLineSegment(sketch, "E92.18.0.29", {"start": v(446.59, -6.59) * mm, "end": v(449.41, -9.41) * mm, "construction": true});
            skLineSegment(sketch, "E92.18.0.30", {"start": v(439.07, -9.9) * mm, "end": v(441.9, -7.07) * mm, "construction": true});
            skLineSegment(sketch, "E92.18.0.31", {"start": v(441.41, -6.59) * mm, "end": v(438.59, -9.41) * mm, "construction": true});
            skLineSegment(sketch, "E92.18.0.32", {"start": v(446.1, -7.07) * mm, "end": v(446.59, -6.59) * mm});
            skLineSegment(sketch, "E92.18.0.33", {"start": v(438.59, 9.41) * mm, "end": v(439.07, 9.9) * mm});
            skLineSegment(sketch, "E92.18.0.34", {"start": v(438.59, -9.41) * mm, "end": v(439.07, -9.9) * mm});
            skLineSegment(sketch, "E92.18.0.35", {"start": v(448.93, -9.9) * mm, "end": v(449.41, -9.41) * mm});
            skLineSegment(sketch, "E92.18.0.36", {"start": v(441.41, 6.59) * mm, "end": v(441.9, 7.07) * mm});
            skLineSegment(sketch, "E92.18.0.37", {"start": v(448.93, 9.9) * mm, "end": v(449.41, 9.41) * mm});
            skLineSegment(sketch, "E92.18.0.38", {"start": v(446.1, 7.07) * mm, "end": v(446.59, 6.59) * mm});
            skLineSegment(sketch, "E92.18.0.39", {"start": v(441.41, -6.59) * mm, "end": v(441.9, -7.07) * mm});
            skArc(sketch, "E92.19.0.0", {"start": v(462.59, 9.41) * mm, "mid": v(462.59, 6.59) * mm, "end": v(465.41, 6.59) * mm});
            skArc(sketch, "E92.19.0.1", {"start": v(465.41, -6.59) * mm, "mid": v(462.59, -6.59) * mm, "end": v(462.59, -9.41) * mm});
            skLineSegment(sketch, "E92.19.0.2", {"start": v(456, 24) * mm, "end": v(480, 24) * mm, "construction": true});
            skLineSegment(sketch, "E92.19.0.3", {"start": v(464, 16) * mm, "end": v(472, 16) * mm, "construction": true});
            skArc(sketch, "E92.19.0.4", {"start": v(463.07, -9.9) * mm, "mid": v(465.9, -9.9) * mm, "end": v(465.9, -7.07) * mm});
            skLineSegment(sketch, "E92.19.0.5", {"start": v(480, 0) * mm, "end": v(456, -24) * mm, "construction": true});
            skCircle(sketch, "E92.19.0.6", {"center": v(472, -16) * mm, "radius": 2 * mm});
            skLineSegment(sketch, "E92.19.0.7", {"start": v(480, -24) * mm, "end": v(456, -24) * mm, "construction": true});
            skCircle(sketch, "E92.19.0.8", {"center": v(464, 16) * mm, "radius": 2 * mm});
            skCircle(sketch, "E92.19.0.9", {"center": v(472, 16) * mm, "radius": 2 * mm});
            skLineSegment(sketch, "E92.19.0.10", {"start": v(480, -24) * mm, "end": v(456, 0) * mm, "construction": true});
            skLineSegment(sketch, "E92.19.0.11", {"start": v(456, 24) * mm, "end": v(480, 0) * mm, "construction": true});
            skLineSegment(sketch, "E92.19.0.12", {"start": v(480, 24) * mm, "end": v(456, 0) * mm, "construction": true});
            skArc(sketch, "E92.19.0.13", {"start": v(472.93, 9.9) * mm, "mid": v(470.1, 9.9) * mm, "end": v(470.1, 7.07) * mm});
            skArc(sketch, "E92.19.0.14", {"start": v(465.9, 7.07) * mm, "mid": v(465.9, 9.9) * mm, "end": v(463.07, 9.9) * mm});
            skArc(sketch, "E92.19.0.15", {"start": v(470.1, -7.07) * mm, "mid": v(470.1, -9.9) * mm, "end": v(472.93, -9.9) * mm});
            skArc(sketch, "E92.19.0.16", {"start": v(470.59, 6.59) * mm, "mid": v(473.41, 6.59) * mm, "end": v(473.41, 9.41) * mm});
            skLineSegment(sketch, "E92.19.0.17", {"start": v(464, -16) * mm, "end": v(472, -16) * mm, "construction": true});
            skLineSegment(sketch, "E92.19.0.18", {"start": v(456, 0) * mm, "end": v(480, 0) * mm, "construction": true});
            skArc(sketch, "E92.19.0.19", {"start": v(473.41, -9.41) * mm, "mid": v(473.41, -6.59) * mm, "end": v(470.59, -6.59) * mm});
            skCircle(sketch, "E92.19.0.20", {"center": v(464, -16) * mm, "radius": 2 * mm});
            skCircle(sketch, "E92.19.0.21", {"center": v(468, 0) * mm, "radius": 2 * mm});
            skPoint(sketch, "E92.19.0.22", {"position": v(464, -8) * mm});
            skLineSegment(sketch, "E92.19.0.23", {"start": v(480, 0) * mm, "end": v(456, 0) * mm, "construction": true});
            skLineSegment(sketch, "E92.19.0.24", {"start": v(470.59, 6.59) * mm, "end": v(473.41, 9.41) * mm, "construction": true});
            skLineSegment(sketch, "E92.19.0.25", {"start": v(470.1, -7.07) * mm, "end": v(472.93, -9.9) * mm, "construction": true});
            skLineSegment(sketch, "E92.19.0.26", {"start": v(462.59, 9.41) * mm, "end": v(465.41, 6.59) * mm, "construction": true});
            skLineSegment(sketch, "E92.19.0.27", {"start": v(463.07, 9.9) * mm, "end": v(465.9, 7.07) * mm, "construction": true});
            skLineSegment(sketch, "E92.19.0.28", {"start": v(472.93, 9.9) * mm, "end": v(470.1, 7.07) * mm, "construction": true});
            skLineSegment(sketch, "E92.19.0.29", {"start": v(470.59, -6.59) * mm, "end": v(473.41, -9.41) * mm, "construction": true});
            skLineSegment(sketch, "E92.19.0.30", {"start": v(463.07, -9.9) * mm, "end": v(465.9, -7.07) * mm, "construction": true});
            skLineSegment(sketch, "E92.19.0.31", {"start": v(465.41, -6.59) * mm, "end": v(462.59, -9.41) * mm, "construction": true});
            skLineSegment(sketch, "E92.19.0.32", {"start": v(470.1, -7.07) * mm, "end": v(470.59, -6.59) * mm});
            skLineSegment(sketch, "E92.19.0.33", {"start": v(462.59, 9.41) * mm, "end": v(463.07, 9.9) * mm});
            skLineSegment(sketch, "E92.19.0.34", {"start": v(462.59, -9.41) * mm, "end": v(463.07, -9.9) * mm});
            skLineSegment(sketch, "E92.19.0.35", {"start": v(472.93, -9.9) * mm, "end": v(473.41, -9.41) * mm});
            skLineSegment(sketch, "E92.19.0.36", {"start": v(465.41, 6.59) * mm, "end": v(465.9, 7.07) * mm});
            skLineSegment(sketch, "E92.19.0.37", {"start": v(472.93, 9.9) * mm, "end": v(473.41, 9.41) * mm});
            skLineSegment(sketch, "E92.19.0.38", {"start": v(470.1, 7.07) * mm, "end": v(470.59, 6.59) * mm});
            skLineSegment(sketch, "E92.19.0.39", {"start": v(465.41, -6.59) * mm, "end": v(465.9, -7.07) * mm});
            skArc(sketch, "E92.20.0.0", {"start": v(486.59, 9.41) * mm, "mid": v(486.59, 6.59) * mm, "end": v(489.41, 6.59) * mm});
            skArc(sketch, "E92.20.0.1", {"start": v(489.41, -6.59) * mm, "mid": v(486.59, -6.59) * mm, "end": v(486.59, -9.41) * mm});
            skLineSegment(sketch, "E92.20.0.2", {"start": v(480, 24) * mm, "end": v(504, 24) * mm, "construction": true});
            skLineSegment(sketch, "E92.20.0.3", {"start": v(488, 16) * mm, "end": v(496, 16) * mm, "construction": true});
            skArc(sketch, "E92.20.0.4", {"start": v(487.07, -9.9) * mm, "mid": v(489.9, -9.9) * mm, "end": v(489.9, -7.07) * mm});
            skLineSegment(sketch, "E92.20.0.5", {"start": v(504, 0) * mm, "end": v(480, -24) * mm, "construction": true});
            skCircle(sketch, "E92.20.0.6", {"center": v(496, -16) * mm, "radius": 2 * mm});
            skLineSegment(sketch, "E92.20.0.7", {"start": v(504, -24) * mm, "end": v(480, -24) * mm, "construction": true});
            skCircle(sketch, "E92.20.0.8", {"center": v(488, 16) * mm, "radius": 2 * mm});
            skCircle(sketch, "E92.20.0.9", {"center": v(496, 16) * mm, "radius": 2 * mm});
            skLineSegment(sketch, "E92.20.0.10", {"start": v(504, -24) * mm, "end": v(480, 0) * mm, "construction": true});
            skLineSegment(sketch, "E92.20.0.11", {"start": v(480, 24) * mm, "end": v(504, 0) * mm, "construction": true});
            skLineSegment(sketch, "E92.20.0.12", {"start": v(504, 24) * mm, "end": v(480, 0) * mm, "construction": true});
            skArc(sketch, "E92.20.0.13", {"start": v(496.93, 9.9) * mm, "mid": v(494.1, 9.9) * mm, "end": v(494.1, 7.07) * mm});
            skArc(sketch, "E92.20.0.14", {"start": v(489.9, 7.07) * mm, "mid": v(489.9, 9.9) * mm, "end": v(487.07, 9.9) * mm});
            skArc(sketch, "E92.20.0.15", {"start": v(494.1, -7.07) * mm, "mid": v(494.1, -9.9) * mm, "end": v(496.93, -9.9) * mm});
            skArc(sketch, "E92.20.0.16", {"start": v(494.59, 6.59) * mm, "mid": v(497.41, 6.59) * mm, "end": v(497.41, 9.41) * mm});
            skLineSegment(sketch, "E92.20.0.17", {"start": v(488, -16) * mm, "end": v(496, -16) * mm, "construction": true});
            skLineSegment(sketch, "E92.20.0.18", {"start": v(480, 0) * mm, "end": v(504, 0) * mm, "construction": true});
            skArc(sketch, "E92.20.0.19", {"start": v(497.41, -9.41) * mm, "mid": v(497.41, -6.59) * mm, "end": v(494.59, -6.59) * mm});
            skCircle(sketch, "E92.20.0.20", {"center": v(488, -16) * mm, "radius": 2 * mm});
            skCircle(sketch, "E92.20.0.21", {"center": v(492, 0) * mm, "radius": 2 * mm});
            skPoint(sketch, "E92.20.0.22", {"position": v(488, -8) * mm});
            skLineSegment(sketch, "E92.20.0.23", {"start": v(504, 0) * mm, "end": v(480, 0) * mm, "construction": true});
            skLineSegment(sketch, "E92.20.0.24", {"start": v(494.59, 6.59) * mm, "end": v(497.41, 9.41) * mm, "construction": true});
            skLineSegment(sketch, "E92.20.0.25", {"start": v(494.1, -7.07) * mm, "end": v(496.93, -9.9) * mm, "construction": true});
            skLineSegment(sketch, "E92.20.0.26", {"start": v(486.59, 9.41) * mm, "end": v(489.41, 6.59) * mm, "construction": true});
            skLineSegment(sketch, "E92.20.0.27", {"start": v(487.07, 9.9) * mm, "end": v(489.9, 7.07) * mm, "construction": true});
            skLineSegment(sketch, "E92.20.0.28", {"start": v(496.93, 9.9) * mm, "end": v(494.1, 7.07) * mm, "construction": true});
            skLineSegment(sketch, "E92.20.0.29", {"start": v(494.59, -6.59) * mm, "end": v(497.41, -9.41) * mm, "construction": true});
            skLineSegment(sketch, "E92.20.0.30", {"start": v(487.07, -9.9) * mm, "end": v(489.9, -7.07) * mm, "construction": true});
            skLineSegment(sketch, "E92.20.0.31", {"start": v(489.41, -6.59) * mm, "end": v(486.59, -9.41) * mm, "construction": true});
            skLineSegment(sketch, "E92.20.0.32", {"start": v(494.1, -7.07) * mm, "end": v(494.59, -6.59) * mm});
            skLineSegment(sketch, "E92.20.0.33", {"start": v(486.59, 9.41) * mm, "end": v(487.07, 9.9) * mm});
            skLineSegment(sketch, "E92.20.0.34", {"start": v(486.59, -9.41) * mm, "end": v(487.07, -9.9) * mm});
            skLineSegment(sketch, "E92.20.0.35", {"start": v(496.93, -9.9) * mm, "end": v(497.41, -9.41) * mm});
            skLineSegment(sketch, "E92.20.0.36", {"start": v(489.41, 6.59) * mm, "end": v(489.9, 7.07) * mm});
            skLineSegment(sketch, "E92.20.0.37", {"start": v(496.93, 9.9) * mm, "end": v(497.41, 9.41) * mm});
            skLineSegment(sketch, "E92.20.0.38", {"start": v(494.1, 7.07) * mm, "end": v(494.59, 6.59) * mm});
            skLineSegment(sketch, "E92.20.0.39", {"start": v(489.41, -6.59) * mm, "end": v(489.9, -7.07) * mm});
            skArc(sketch, "E92.21.0.0", {"start": v(510.59, 9.41) * mm, "mid": v(510.59, 6.59) * mm, "end": v(513.41, 6.59) * mm});
            skArc(sketch, "E92.21.0.1", {"start": v(513.41, -6.59) * mm, "mid": v(510.59, -6.59) * mm, "end": v(510.59, -9.41) * mm});
            skLineSegment(sketch, "E92.21.0.2", {"start": v(504, 24) * mm, "end": v(528, 24) * mm, "construction": true});
            skLineSegment(sketch, "E92.21.0.3", {"start": v(512, 16) * mm, "end": v(520, 16) * mm, "construction": true});
            skArc(sketch, "E92.21.0.4", {"start": v(511.07, -9.9) * mm, "mid": v(513.9, -9.9) * mm, "end": v(513.9, -7.07) * mm});
            skLineSegment(sketch, "E92.21.0.5", {"start": v(528, 0) * mm, "end": v(504, -24) * mm, "construction": true});
            skCircle(sketch, "E92.21.0.6", {"center": v(520, -16) * mm, "radius": 2 * mm});
            skLineSegment(sketch, "E92.21.0.7", {"start": v(528, -24) * mm, "end": v(504, -24) * mm, "construction": true});
            skCircle(sketch, "E92.21.0.8", {"center": v(512, 16) * mm, "radius": 2 * mm});
            skCircle(sketch, "E92.21.0.9", {"center": v(520, 16) * mm, "radius": 2 * mm});
            skLineSegment(sketch, "E92.21.0.10", {"start": v(528, -24) * mm, "end": v(504, 0) * mm, "construction": true});
            skLineSegment(sketch, "E92.21.0.11", {"start": v(504, 24) * mm, "end": v(528, 0) * mm, "construction": true});
            skLineSegment(sketch, "E92.21.0.12", {"start": v(528, 24) * mm, "end": v(504, 0) * mm, "construction": true});
            skArc(sketch, "E92.21.0.13", {"start": v(520.93, 9.9) * mm, "mid": v(518.1, 9.9) * mm, "end": v(518.1, 7.07) * mm});
            skArc(sketch, "E92.21.0.14", {"start": v(513.9, 7.07) * mm, "mid": v(513.9, 9.9) * mm, "end": v(511.07, 9.9) * mm});
            skArc(sketch, "E92.21.0.15", {"start": v(518.1, -7.07) * mm, "mid": v(518.1, -9.9) * mm, "end": v(520.93, -9.9) * mm});
            skArc(sketch, "E92.21.0.16", {"start": v(518.59, 6.59) * mm, "mid": v(521.41, 6.59) * mm, "end": v(521.41, 9.41) * mm});
            skLineSegment(sketch, "E92.21.0.17", {"start": v(512, -16) * mm, "end": v(520, -16) * mm, "construction": true});
            skLineSegment(sketch, "E92.21.0.18", {"start": v(504, 0) * mm, "end": v(528, 0) * mm, "construction": true});
            skArc(sketch, "E92.21.0.19", {"start": v(521.41, -9.41) * mm, "mid": v(521.41, -6.59) * mm, "end": v(518.59, -6.59) * mm});
            skCircle(sketch, "E92.21.0.20", {"center": v(512, -16) * mm, "radius": 2 * mm});
            skCircle(sketch, "E92.21.0.21", {"center": v(516, 0) * mm, "radius": 2 * mm});
            skPoint(sketch, "E92.21.0.22", {"position": v(512, -8) * mm});
            skLineSegment(sketch, "E92.21.0.23", {"start": v(528, 0) * mm, "end": v(504, 0) * mm, "construction": true});
            skLineSegment(sketch, "E92.21.0.24", {"start": v(518.59, 6.59) * mm, "end": v(521.41, 9.41) * mm, "construction": true});
            skLineSegment(sketch, "E92.21.0.25", {"start": v(518.1, -7.07) * mm, "end": v(520.93, -9.9) * mm, "construction": true});
            skLineSegment(sketch, "E92.21.0.26", {"start": v(510.59, 9.41) * mm, "end": v(513.41, 6.59) * mm, "construction": true});
            skLineSegment(sketch, "E92.21.0.27", {"start": v(511.07, 9.9) * mm, "end": v(513.9, 7.07) * mm, "construction": true});
            skLineSegment(sketch, "E92.21.0.28", {"start": v(520.93, 9.9) * mm, "end": v(518.1, 7.07) * mm, "construction": true});
            skLineSegment(sketch, "E92.21.0.29", {"start": v(518.59, -6.59) * mm, "end": v(521.41, -9.41) * mm, "construction": true});
            skLineSegment(sketch, "E92.21.0.30", {"start": v(511.07, -9.9) * mm, "end": v(513.9, -7.07) * mm, "construction": true});
            skLineSegment(sketch, "E92.21.0.31", {"start": v(513.41, -6.59) * mm, "end": v(510.59, -9.41) * mm, "construction": true});
            skLineSegment(sketch, "E92.21.0.32", {"start": v(518.1, -7.07) * mm, "end": v(518.59, -6.59) * mm});
            skLineSegment(sketch, "E92.21.0.33", {"start": v(510.59, 9.41) * mm, "end": v(511.07, 9.9) * mm});
            skLineSegment(sketch, "E92.21.0.34", {"start": v(510.59, -9.41) * mm, "end": v(511.07, -9.9) * mm});
            skLineSegment(sketch, "E92.21.0.35", {"start": v(520.93, -9.9) * mm, "end": v(521.41, -9.41) * mm});
            skLineSegment(sketch, "E92.21.0.36", {"start": v(513.41, 6.59) * mm, "end": v(513.9, 7.07) * mm});
            skLineSegment(sketch, "E92.21.0.37", {"start": v(520.93, 9.9) * mm, "end": v(521.41, 9.41) * mm});
            skLineSegment(sketch, "E92.21.0.38", {"start": v(518.1, 7.07) * mm, "end": v(518.59, 6.59) * mm});
            skLineSegment(sketch, "E92.21.0.39", {"start": v(513.41, -6.59) * mm, "end": v(513.9, -7.07) * mm});
            skArc(sketch, "E92.22.0.0", {"start": v(534.59, 9.41) * mm, "mid": v(534.59, 6.59) * mm, "end": v(537.41, 6.59) * mm});
            skArc(sketch, "E92.22.0.1", {"start": v(537.41, -6.59) * mm, "mid": v(534.59, -6.59) * mm, "end": v(534.59, -9.41) * mm});
            skLineSegment(sketch, "E92.22.0.2", {"start": v(528, 24) * mm, "end": v(552, 24) * mm, "construction": true});
            skLineSegment(sketch, "E92.22.0.3", {"start": v(536, 16) * mm, "end": v(544, 16) * mm, "construction": true});
            skArc(sketch, "E92.22.0.4", {"start": v(535.07, -9.9) * mm, "mid": v(537.9, -9.9) * mm, "end": v(537.9, -7.07) * mm});
            skLineSegment(sketch, "E92.22.0.5", {"start": v(552, 0) * mm, "end": v(528, -24) * mm, "construction": true});
            skCircle(sketch, "E92.22.0.6", {"center": v(544, -16) * mm, "radius": 2 * mm});
            skLineSegment(sketch, "E92.22.0.7", {"start": v(552, -24) * mm, "end": v(528, -24) * mm, "construction": true});
            skCircle(sketch, "E92.22.0.8", {"center": v(536, 16) * mm, "radius": 2 * mm});
            skCircle(sketch, "E92.22.0.9", {"center": v(544, 16) * mm, "radius": 2 * mm});
            skLineSegment(sketch, "E92.22.0.10", {"start": v(552, -24) * mm, "end": v(528, 0) * mm, "construction": true});
            skLineSegment(sketch, "E92.22.0.11", {"start": v(528, 24) * mm, "end": v(552, 0) * mm, "construction": true});
            skLineSegment(sketch, "E92.22.0.12", {"start": v(552, 24) * mm, "end": v(528, 0) * mm, "construction": true});
            skArc(sketch, "E92.22.0.13", {"start": v(544.93, 9.9) * mm, "mid": v(542.1, 9.9) * mm, "end": v(542.1, 7.07) * mm});
            skArc(sketch, "E92.22.0.14", {"start": v(537.9, 7.07) * mm, "mid": v(537.9, 9.9) * mm, "end": v(535.07, 9.9) * mm});
            skArc(sketch, "E92.22.0.15", {"start": v(542.1, -7.07) * mm, "mid": v(542.1, -9.9) * mm, "end": v(544.93, -9.9) * mm});
            skArc(sketch, "E92.22.0.16", {"start": v(542.59, 6.59) * mm, "mid": v(545.41, 6.59) * mm, "end": v(545.41, 9.41) * mm});
            skLineSegment(sketch, "E92.22.0.17", {"start": v(536, -16) * mm, "end": v(544, -16) * mm, "construction": true});
            skLineSegment(sketch, "E92.22.0.18", {"start": v(528, 0) * mm, "end": v(552, 0) * mm, "construction": true});
            skArc(sketch, "E92.22.0.19", {"start": v(545.41, -9.41) * mm, "mid": v(545.41, -6.59) * mm, "end": v(542.59, -6.59) * mm});
            skCircle(sketch, "E92.22.0.20", {"center": v(536, -16) * mm, "radius": 2 * mm});
            skCircle(sketch, "E92.22.0.21", {"center": v(540, 0) * mm, "radius": 2 * mm});
            skPoint(sketch, "E92.22.0.22", {"position": v(536, -8) * mm});
            skLineSegment(sketch, "E92.22.0.23", {"start": v(552, 0) * mm, "end": v(528, 0) * mm, "construction": true});
            skLineSegment(sketch, "E92.22.0.24", {"start": v(542.59, 6.59) * mm, "end": v(545.41, 9.41) * mm, "construction": true});
            skLineSegment(sketch, "E92.22.0.25", {"start": v(542.1, -7.07) * mm, "end": v(544.93, -9.9) * mm, "construction": true});
            skLineSegment(sketch, "E92.22.0.26", {"start": v(534.59, 9.41) * mm, "end": v(537.41, 6.59) * mm, "construction": true});
            skLineSegment(sketch, "E92.22.0.27", {"start": v(535.07, 9.9) * mm, "end": v(537.9, 7.07) * mm, "construction": true});
            skLineSegment(sketch, "E92.22.0.28", {"start": v(544.93, 9.9) * mm, "end": v(542.1, 7.07) * mm, "construction": true});
            skLineSegment(sketch, "E92.22.0.29", {"start": v(542.59, -6.59) * mm, "end": v(545.41, -9.41) * mm, "construction": true});
            skLineSegment(sketch, "E92.22.0.30", {"start": v(535.07, -9.9) * mm, "end": v(537.9, -7.07) * mm, "construction": true});
            skLineSegment(sketch, "E92.22.0.31", {"start": v(537.41, -6.59) * mm, "end": v(534.59, -9.41) * mm, "construction": true});
            skLineSegment(sketch, "E92.22.0.32", {"start": v(542.1, -7.07) * mm, "end": v(542.59, -6.59) * mm});
            skLineSegment(sketch, "E92.22.0.33", {"start": v(534.59, 9.41) * mm, "end": v(535.07, 9.9) * mm});
            skLineSegment(sketch, "E92.22.0.34", {"start": v(534.59, -9.41) * mm, "end": v(535.07, -9.9) * mm});
            skLineSegment(sketch, "E92.22.0.35", {"start": v(544.93, -9.9) * mm, "end": v(545.41, -9.41) * mm});
            skLineSegment(sketch, "E92.22.0.36", {"start": v(537.41, 6.59) * mm, "end": v(537.9, 7.07) * mm});
            skLineSegment(sketch, "E92.22.0.37", {"start": v(544.93, 9.9) * mm, "end": v(545.41, 9.41) * mm});
            skLineSegment(sketch, "E92.22.0.38", {"start": v(542.1, 7.07) * mm, "end": v(542.59, 6.59) * mm});
            skLineSegment(sketch, "E92.22.0.39", {"start": v(537.41, -6.59) * mm, "end": v(537.9, -7.07) * mm});
            skArc(sketch, "E92.23.0.0", {"start": v(558.59, 9.41) * mm, "mid": v(558.59, 6.59) * mm, "end": v(561.41, 6.59) * mm});
            skArc(sketch, "E92.23.0.1", {"start": v(561.41, -6.59) * mm, "mid": v(558.59, -6.59) * mm, "end": v(558.59, -9.41) * mm});
            skLineSegment(sketch, "E92.23.0.2", {"start": v(552, 24) * mm, "end": v(576, 24) * mm, "construction": true});
            skLineSegment(sketch, "E92.23.0.3", {"start": v(560, 16) * mm, "end": v(568, 16) * mm, "construction": true});
            skArc(sketch, "E92.23.0.4", {"start": v(559.07, -9.9) * mm, "mid": v(561.9, -9.9) * mm, "end": v(561.9, -7.07) * mm});
            skLineSegment(sketch, "E92.23.0.5", {"start": v(576, 0) * mm, "end": v(552, -24) * mm, "construction": true});
            skCircle(sketch, "E92.23.0.6", {"center": v(568, -16) * mm, "radius": 2 * mm});
            skLineSegment(sketch, "E92.23.0.7", {"start": v(576, -24) * mm, "end": v(552, -24) * mm, "construction": true});
            skCircle(sketch, "E92.23.0.8", {"center": v(560, 16) * mm, "radius": 2 * mm});
            skCircle(sketch, "E92.23.0.9", {"center": v(568, 16) * mm, "radius": 2 * mm});
            skLineSegment(sketch, "E92.23.0.10", {"start": v(576, -24) * mm, "end": v(552, 0) * mm, "construction": true});
            skLineSegment(sketch, "E92.23.0.11", {"start": v(552, 24) * mm, "end": v(576, 0) * mm, "construction": true});
            skLineSegment(sketch, "E92.23.0.12", {"start": v(576, 24) * mm, "end": v(552, 0) * mm, "construction": true});
            skArc(sketch, "E92.23.0.13", {"start": v(568.93, 9.9) * mm, "mid": v(566.1, 9.9) * mm, "end": v(566.1, 7.07) * mm});
            skArc(sketch, "E92.23.0.14", {"start": v(561.9, 7.07) * mm, "mid": v(561.9, 9.9) * mm, "end": v(559.07, 9.9) * mm});
            skArc(sketch, "E92.23.0.15", {"start": v(566.1, -7.07) * mm, "mid": v(566.1, -9.9) * mm, "end": v(568.93, -9.9) * mm});
            skArc(sketch, "E92.23.0.16", {"start": v(566.59, 6.59) * mm, "mid": v(569.41, 6.59) * mm, "end": v(569.41, 9.41) * mm});
            skLineSegment(sketch, "E92.23.0.17", {"start": v(560, -16) * mm, "end": v(568, -16) * mm, "construction": true});
            skLineSegment(sketch, "E92.23.0.18", {"start": v(552, 0) * mm, "end": v(576, 0) * mm, "construction": true});
            skArc(sketch, "E92.23.0.19", {"start": v(569.41, -9.41) * mm, "mid": v(569.41, -6.59) * mm, "end": v(566.59, -6.59) * mm});
            skCircle(sketch, "E92.23.0.20", {"center": v(560, -16) * mm, "radius": 2 * mm});
            skCircle(sketch, "E92.23.0.21", {"center": v(564, 0) * mm, "radius": 2 * mm});
            skPoint(sketch, "E92.23.0.22", {"position": v(560, -8) * mm});
            skLineSegment(sketch, "E92.23.0.23", {"start": v(576, 0) * mm, "end": v(552, 0) * mm, "construction": true});
            skLineSegment(sketch, "E92.23.0.24", {"start": v(566.59, 6.59) * mm, "end": v(569.41, 9.41) * mm, "construction": true});
            skLineSegment(sketch, "E92.23.0.25", {"start": v(566.1, -7.07) * mm, "end": v(568.93, -9.9) * mm, "construction": true});
            skLineSegment(sketch, "E92.23.0.26", {"start": v(558.59, 9.41) * mm, "end": v(561.41, 6.59) * mm, "construction": true});
            skLineSegment(sketch, "E92.23.0.27", {"start": v(559.07, 9.9) * mm, "end": v(561.9, 7.07) * mm, "construction": true});
            skLineSegment(sketch, "E92.23.0.28", {"start": v(568.93, 9.9) * mm, "end": v(566.1, 7.07) * mm, "construction": true});
            skLineSegment(sketch, "E92.23.0.29", {"start": v(566.59, -6.59) * mm, "end": v(569.41, -9.41) * mm, "construction": true});
            skLineSegment(sketch, "E92.23.0.30", {"start": v(559.07, -9.9) * mm, "end": v(561.9, -7.07) * mm, "construction": true});
            skLineSegment(sketch, "E92.23.0.31", {"start": v(561.41, -6.59) * mm, "end": v(558.59, -9.41) * mm, "construction": true});
            skLineSegment(sketch, "E92.23.0.32", {"start": v(566.1, -7.07) * mm, "end": v(566.59, -6.59) * mm});
            skLineSegment(sketch, "E92.23.0.33", {"start": v(558.59, 9.41) * mm, "end": v(559.07, 9.9) * mm});
            skLineSegment(sketch, "E92.23.0.34", {"start": v(558.59, -9.41) * mm, "end": v(559.07, -9.9) * mm});
            skLineSegment(sketch, "E92.23.0.35", {"start": v(568.93, -9.9) * mm, "end": v(569.41, -9.41) * mm});
            skLineSegment(sketch, "E92.23.0.36", {"start": v(561.41, 6.59) * mm, "end": v(561.9, 7.07) * mm});
            skLineSegment(sketch, "E92.23.0.37", {"start": v(568.93, 9.9) * mm, "end": v(569.41, 9.41) * mm});
            skLineSegment(sketch, "E92.23.0.38", {"start": v(566.1, 7.07) * mm, "end": v(566.59, 6.59) * mm});
            skLineSegment(sketch, "E92.23.0.39", {"start": v(561.41, -6.59) * mm, "end": v(561.9, -7.07) * mm});
            skArc(sketch, "E92.24.0.0", {"start": v(582.59, 9.41) * mm, "mid": v(582.59, 6.59) * mm, "end": v(585.41, 6.59) * mm});
            skArc(sketch, "E92.24.0.1", {"start": v(585.41, -6.59) * mm, "mid": v(582.59, -6.59) * mm, "end": v(582.59, -9.41) * mm});
            skLineSegment(sketch, "E92.24.0.2", {"start": v(576, 24) * mm, "end": v(600, 24) * mm, "construction": true});
            skLineSegment(sketch, "E92.24.0.3", {"start": v(584, 16) * mm, "end": v(592, 16) * mm, "construction": true});
            skArc(sketch, "E92.24.0.4", {"start": v(583.07, -9.9) * mm, "mid": v(585.9, -9.9) * mm, "end": v(585.9, -7.07) * mm});
            skLineSegment(sketch, "E92.24.0.5", {"start": v(600, 0) * mm, "end": v(576, -24) * mm, "construction": true});
            skCircle(sketch, "E92.24.0.6", {"center": v(592, -16) * mm, "radius": 2 * mm});
            skLineSegment(sketch, "E92.24.0.7", {"start": v(600, -24) * mm, "end": v(576, -24) * mm, "construction": true});
            skCircle(sketch, "E92.24.0.8", {"center": v(584, 16) * mm, "radius": 2 * mm});
            skCircle(sketch, "E92.24.0.9", {"center": v(592, 16) * mm, "radius": 2 * mm});
            skLineSegment(sketch, "E92.24.0.10", {"start": v(600, -24) * mm, "end": v(576, 0) * mm, "construction": true});
            skLineSegment(sketch, "E92.24.0.11", {"start": v(576, 24) * mm, "end": v(600, 0) * mm, "construction": true});
            skLineSegment(sketch, "E92.24.0.12", {"start": v(600, 24) * mm, "end": v(576, 0) * mm, "construction": true});
            skArc(sketch, "E92.24.0.13", {"start": v(592.93, 9.9) * mm, "mid": v(590.1, 9.9) * mm, "end": v(590.1, 7.07) * mm});
            skArc(sketch, "E92.24.0.14", {"start": v(585.9, 7.07) * mm, "mid": v(585.9, 9.9) * mm, "end": v(583.07, 9.9) * mm});
            skArc(sketch, "E92.24.0.15", {"start": v(590.1, -7.07) * mm, "mid": v(590.1, -9.9) * mm, "end": v(592.93, -9.9) * mm});
            skArc(sketch, "E92.24.0.16", {"start": v(590.59, 6.59) * mm, "mid": v(593.41, 6.59) * mm, "end": v(593.41, 9.41) * mm});
            skLineSegment(sketch, "E92.24.0.17", {"start": v(584, -16) * mm, "end": v(592, -16) * mm, "construction": true});
            skLineSegment(sketch, "E92.24.0.18", {"start": v(576, 0) * mm, "end": v(600, 0) * mm, "construction": true});
            skArc(sketch, "E92.24.0.19", {"start": v(593.41, -9.41) * mm, "mid": v(593.41, -6.59) * mm, "end": v(590.59, -6.59) * mm});
            skCircle(sketch, "E92.24.0.20", {"center": v(584, -16) * mm, "radius": 2 * mm});
            skCircle(sketch, "E92.24.0.21", {"center": v(588, 0) * mm, "radius": 2 * mm});
            skPoint(sketch, "E92.24.0.22", {"position": v(584, -8) * mm});
            skLineSegment(sketch, "E92.24.0.23", {"start": v(600, 0) * mm, "end": v(576, 0) * mm, "construction": true});
            skLineSegment(sketch, "E92.24.0.24", {"start": v(590.59, 6.59) * mm, "end": v(593.41, 9.41) * mm, "construction": true});
            skLineSegment(sketch, "E92.24.0.25", {"start": v(590.1, -7.07) * mm, "end": v(592.93, -9.9) * mm, "construction": true});
            skLineSegment(sketch, "E92.24.0.26", {"start": v(582.59, 9.41) * mm, "end": v(585.41, 6.59) * mm, "construction": true});
            skLineSegment(sketch, "E92.24.0.27", {"start": v(583.07, 9.9) * mm, "end": v(585.9, 7.07) * mm, "construction": true});
            skLineSegment(sketch, "E92.24.0.28", {"start": v(592.93, 9.9) * mm, "end": v(590.1, 7.07) * mm, "construction": true});
            skLineSegment(sketch, "E92.24.0.29", {"start": v(590.59, -6.59) * mm, "end": v(593.41, -9.41) * mm, "construction": true});
            skLineSegment(sketch, "E92.24.0.30", {"start": v(583.07, -9.9) * mm, "end": v(585.9, -7.07) * mm, "construction": true});
            skLineSegment(sketch, "E92.24.0.31", {"start": v(585.41, -6.59) * mm, "end": v(582.59, -9.41) * mm, "construction": true});
            skLineSegment(sketch, "E92.24.0.32", {"start": v(590.1, -7.07) * mm, "end": v(590.59, -6.59) * mm});
            skLineSegment(sketch, "E92.24.0.33", {"start": v(582.59, 9.41) * mm, "end": v(583.07, 9.9) * mm});
            skLineSegment(sketch, "E92.24.0.34", {"start": v(582.59, -9.41) * mm, "end": v(583.07, -9.9) * mm});
            skLineSegment(sketch, "E92.24.0.35", {"start": v(592.93, -9.9) * mm, "end": v(593.41, -9.41) * mm});
            skLineSegment(sketch, "E92.24.0.36", {"start": v(585.41, 6.59) * mm, "end": v(585.9, 7.07) * mm});
            skLineSegment(sketch, "E92.24.0.37", {"start": v(592.93, 9.9) * mm, "end": v(593.41, 9.41) * mm});
            skLineSegment(sketch, "E92.24.0.38", {"start": v(590.1, 7.07) * mm, "end": v(590.59, 6.59) * mm});
            skLineSegment(sketch, "E92.24.0.39", {"start": v(585.41, -6.59) * mm, "end": v(585.9, -7.07) * mm});
            skArc(sketch, "E92.25.0.0", {"start": v(606.59, 9.41) * mm, "mid": v(606.59, 6.59) * mm, "end": v(609.41, 6.59) * mm});
            skArc(sketch, "E92.25.0.1", {"start": v(609.41, -6.59) * mm, "mid": v(606.59, -6.59) * mm, "end": v(606.59, -9.41) * mm});
            skLineSegment(sketch, "E92.25.0.2", {"start": v(600, 24) * mm, "end": v(624, 24) * mm, "construction": true});
            skLineSegment(sketch, "E92.25.0.3", {"start": v(608, 16) * mm, "end": v(616, 16) * mm, "construction": true});
            skArc(sketch, "E92.25.0.4", {"start": v(607.07, -9.9) * mm, "mid": v(609.9, -9.9) * mm, "end": v(609.9, -7.07) * mm});
            skLineSegment(sketch, "E92.25.0.5", {"start": v(624, 0) * mm, "end": v(600, -24) * mm, "construction": true});
            skCircle(sketch, "E92.25.0.6", {"center": v(616, -16) * mm, "radius": 2 * mm});
            skLineSegment(sketch, "E92.25.0.7", {"start": v(624, -24) * mm, "end": v(600, -24) * mm, "construction": true});
            skCircle(sketch, "E92.25.0.8", {"center": v(608, 16) * mm, "radius": 2 * mm});
            skCircle(sketch, "E92.25.0.9", {"center": v(616, 16) * mm, "radius": 2 * mm});
            skLineSegment(sketch, "E92.25.0.10", {"start": v(624, -24) * mm, "end": v(600, 0) * mm, "construction": true});
            skLineSegment(sketch, "E92.25.0.11", {"start": v(600, 24) * mm, "end": v(624, 0) * mm, "construction": true});
            skLineSegment(sketch, "E92.25.0.12", {"start": v(624, 24) * mm, "end": v(600, 0) * mm, "construction": true});
            skArc(sketch, "E92.25.0.13", {"start": v(616.93, 9.9) * mm, "mid": v(614.1, 9.9) * mm, "end": v(614.1, 7.07) * mm});
            skArc(sketch, "E92.25.0.14", {"start": v(609.9, 7.07) * mm, "mid": v(609.9, 9.9) * mm, "end": v(607.07, 9.9) * mm});
            skArc(sketch, "E92.25.0.15", {"start": v(614.1, -7.07) * mm, "mid": v(614.1, -9.9) * mm, "end": v(616.93, -9.9) * mm});
            skArc(sketch, "E92.25.0.16", {"start": v(614.59, 6.59) * mm, "mid": v(617.41, 6.59) * mm, "end": v(617.41, 9.41) * mm});
            skLineSegment(sketch, "E92.25.0.17", {"start": v(608, -16) * mm, "end": v(616, -16) * mm, "construction": true});
            skLineSegment(sketch, "E92.25.0.18", {"start": v(600, 0) * mm, "end": v(624, 0) * mm, "construction": true});
            skArc(sketch, "E92.25.0.19", {"start": v(617.41, -9.41) * mm, "mid": v(617.41, -6.59) * mm, "end": v(614.59, -6.59) * mm});
            skCircle(sketch, "E92.25.0.20", {"center": v(608, -16) * mm, "radius": 2 * mm});
            skCircle(sketch, "E92.25.0.21", {"center": v(612, 0) * mm, "radius": 2 * mm});
            skPoint(sketch, "E92.25.0.22", {"position": v(608, -8) * mm});
            skLineSegment(sketch, "E92.25.0.23", {"start": v(624, 0) * mm, "end": v(600, 0) * mm, "construction": true});
            skLineSegment(sketch, "E92.25.0.24", {"start": v(614.59, 6.59) * mm, "end": v(617.41, 9.41) * mm, "construction": true});
            skLineSegment(sketch, "E92.25.0.25", {"start": v(614.1, -7.07) * mm, "end": v(616.93, -9.9) * mm, "construction": true});
            skLineSegment(sketch, "E92.25.0.26", {"start": v(606.59, 9.41) * mm, "end": v(609.41, 6.59) * mm, "construction": true});
            skLineSegment(sketch, "E92.25.0.27", {"start": v(607.07, 9.9) * mm, "end": v(609.9, 7.07) * mm, "construction": true});
            skLineSegment(sketch, "E92.25.0.28", {"start": v(616.93, 9.9) * mm, "end": v(614.1, 7.07) * mm, "construction": true});
            skLineSegment(sketch, "E92.25.0.29", {"start": v(614.59, -6.59) * mm, "end": v(617.41, -9.41) * mm, "construction": true});
            skLineSegment(sketch, "E92.25.0.30", {"start": v(607.07, -9.9) * mm, "end": v(609.9, -7.07) * mm, "construction": true});
            skLineSegment(sketch, "E92.25.0.31", {"start": v(609.41, -6.59) * mm, "end": v(606.59, -9.41) * mm, "construction": true});
            skLineSegment(sketch, "E92.25.0.32", {"start": v(614.1, -7.07) * mm, "end": v(614.59, -6.59) * mm});
            skLineSegment(sketch, "E92.25.0.33", {"start": v(606.59, 9.41) * mm, "end": v(607.07, 9.9) * mm});
            skLineSegment(sketch, "E92.25.0.34", {"start": v(606.59, -9.41) * mm, "end": v(607.07, -9.9) * mm});
            skLineSegment(sketch, "E92.25.0.35", {"start": v(616.93, -9.9) * mm, "end": v(617.41, -9.41) * mm});
            skLineSegment(sketch, "E92.25.0.36", {"start": v(609.41, 6.59) * mm, "end": v(609.9, 7.07) * mm});
            skLineSegment(sketch, "E92.25.0.37", {"start": v(616.93, 9.9) * mm, "end": v(617.41, 9.41) * mm});
            skLineSegment(sketch, "E92.25.0.38", {"start": v(614.1, 7.07) * mm, "end": v(614.59, 6.59) * mm});
            skLineSegment(sketch, "E92.25.0.39", {"start": v(609.41, -6.59) * mm, "end": v(609.9, -7.07) * mm});
            skArc(sketch, "E92.26.0.0", {"start": v(630.59, 9.41) * mm, "mid": v(630.59, 6.59) * mm, "end": v(633.41, 6.59) * mm});
            skArc(sketch, "E92.26.0.1", {"start": v(633.41, -6.59) * mm, "mid": v(630.59, -6.59) * mm, "end": v(630.59, -9.41) * mm});
            skLineSegment(sketch, "E92.26.0.2", {"start": v(624, 24) * mm, "end": v(648, 24) * mm, "construction": true});
            skLineSegment(sketch, "E92.26.0.3", {"start": v(632, 16) * mm, "end": v(640, 16) * mm, "construction": true});
            skArc(sketch, "E92.26.0.4", {"start": v(631.07, -9.9) * mm, "mid": v(633.9, -9.9) * mm, "end": v(633.9, -7.07) * mm});
            skLineSegment(sketch, "E92.26.0.5", {"start": v(648, 0) * mm, "end": v(624, -24) * mm, "construction": true});
            skCircle(sketch, "E92.26.0.6", {"center": v(640, -16) * mm, "radius": 2 * mm});
            skLineSegment(sketch, "E92.26.0.7", {"start": v(648, -24) * mm, "end": v(624, -24) * mm, "construction": true});
            skCircle(sketch, "E92.26.0.8", {"center": v(632, 16) * mm, "radius": 2 * mm});
            skCircle(sketch, "E92.26.0.9", {"center": v(640, 16) * mm, "radius": 2 * mm});
            skLineSegment(sketch, "E92.26.0.10", {"start": v(648, -24) * mm, "end": v(624, 0) * mm, "construction": true});
            skLineSegment(sketch, "E92.26.0.11", {"start": v(624, 24) * mm, "end": v(648, 0) * mm, "construction": true});
            skLineSegment(sketch, "E92.26.0.12", {"start": v(648, 24) * mm, "end": v(624, 0) * mm, "construction": true});
            skArc(sketch, "E92.26.0.13", {"start": v(640.93, 9.9) * mm, "mid": v(638.1, 9.9) * mm, "end": v(638.1, 7.07) * mm});
            skArc(sketch, "E92.26.0.14", {"start": v(633.9, 7.07) * mm, "mid": v(633.9, 9.9) * mm, "end": v(631.07, 9.9) * mm});
            skArc(sketch, "E92.26.0.15", {"start": v(638.1, -7.07) * mm, "mid": v(638.1, -9.9) * mm, "end": v(640.93, -9.9) * mm});
            skArc(sketch, "E92.26.0.16", {"start": v(638.59, 6.59) * mm, "mid": v(641.41, 6.59) * mm, "end": v(641.41, 9.41) * mm});
            skLineSegment(sketch, "E92.26.0.17", {"start": v(632, -16) * mm, "end": v(640, -16) * mm, "construction": true});
            skLineSegment(sketch, "E92.26.0.18", {"start": v(624, 0) * mm, "end": v(648, 0) * mm, "construction": true});
            skArc(sketch, "E92.26.0.19", {"start": v(641.41, -9.41) * mm, "mid": v(641.41, -6.59) * mm, "end": v(638.59, -6.59) * mm});
            skCircle(sketch, "E92.26.0.20", {"center": v(632, -16) * mm, "radius": 2 * mm});
            skCircle(sketch, "E92.26.0.21", {"center": v(636, 0) * mm, "radius": 2 * mm});
            skPoint(sketch, "E92.26.0.22", {"position": v(632, -8) * mm});
            skLineSegment(sketch, "E92.26.0.23", {"start": v(648, 0) * mm, "end": v(624, 0) * mm, "construction": true});
            skLineSegment(sketch, "E92.26.0.24", {"start": v(638.59, 6.59) * mm, "end": v(641.41, 9.41) * mm, "construction": true});
            skLineSegment(sketch, "E92.26.0.25", {"start": v(638.1, -7.07) * mm, "end": v(640.93, -9.9) * mm, "construction": true});
            skLineSegment(sketch, "E92.26.0.26", {"start": v(630.59, 9.41) * mm, "end": v(633.41, 6.59) * mm, "construction": true});
            skLineSegment(sketch, "E92.26.0.27", {"start": v(631.07, 9.9) * mm, "end": v(633.9, 7.07) * mm, "construction": true});
            skLineSegment(sketch, "E92.26.0.28", {"start": v(640.93, 9.9) * mm, "end": v(638.1, 7.07) * mm, "construction": true});
            skLineSegment(sketch, "E92.26.0.29", {"start": v(638.59, -6.59) * mm, "end": v(641.41, -9.41) * mm, "construction": true});
            skLineSegment(sketch, "E92.26.0.30", {"start": v(631.07, -9.9) * mm, "end": v(633.9, -7.07) * mm, "construction": true});
            skLineSegment(sketch, "E92.26.0.31", {"start": v(633.41, -6.59) * mm, "end": v(630.59, -9.41) * mm, "construction": true});
            skLineSegment(sketch, "E92.26.0.32", {"start": v(638.1, -7.07) * mm, "end": v(638.59, -6.59) * mm});
            skLineSegment(sketch, "E92.26.0.33", {"start": v(630.59, 9.41) * mm, "end": v(631.07, 9.9) * mm});
            skLineSegment(sketch, "E92.26.0.34", {"start": v(630.59, -9.41) * mm, "end": v(631.07, -9.9) * mm});
            skLineSegment(sketch, "E92.26.0.35", {"start": v(640.93, -9.9) * mm, "end": v(641.41, -9.41) * mm});
            skLineSegment(sketch, "E92.26.0.36", {"start": v(633.41, 6.59) * mm, "end": v(633.9, 7.07) * mm});
            skLineSegment(sketch, "E92.26.0.37", {"start": v(640.93, 9.9) * mm, "end": v(641.41, 9.41) * mm});
            skLineSegment(sketch, "E92.26.0.38", {"start": v(638.1, 7.07) * mm, "end": v(638.59, 6.59) * mm});
            skLineSegment(sketch, "E92.26.0.39", {"start": v(633.41, -6.59) * mm, "end": v(633.9, -7.07) * mm});
            skArc(sketch, "E92.27.0.0", {"start": v(654.59, 9.41) * mm, "mid": v(654.59, 6.59) * mm, "end": v(657.41, 6.59) * mm});
            skArc(sketch, "E92.27.0.1", {"start": v(657.41, -6.59) * mm, "mid": v(654.59, -6.59) * mm, "end": v(654.59, -9.41) * mm});
            skLineSegment(sketch, "E92.27.0.2", {"start": v(648, 24) * mm, "end": v(672, 24) * mm, "construction": true});
            skLineSegment(sketch, "E92.27.0.3", {"start": v(656, 16) * mm, "end": v(664, 16) * mm, "construction": true});
            skArc(sketch, "E92.27.0.4", {"start": v(655.07, -9.9) * mm, "mid": v(657.9, -9.9) * mm, "end": v(657.9, -7.07) * mm});
            skLineSegment(sketch, "E92.27.0.5", {"start": v(672, 0) * mm, "end": v(648, -24) * mm, "construction": true});
            skCircle(sketch, "E92.27.0.6", {"center": v(664, -16) * mm, "radius": 2 * mm});
            skLineSegment(sketch, "E92.27.0.7", {"start": v(672, -24) * mm, "end": v(648, -24) * mm, "construction": true});
            skCircle(sketch, "E92.27.0.8", {"center": v(656, 16) * mm, "radius": 2 * mm});
            skCircle(sketch, "E92.27.0.9", {"center": v(664, 16) * mm, "radius": 2 * mm});
            skLineSegment(sketch, "E92.27.0.10", {"start": v(672, -24) * mm, "end": v(648, 0) * mm, "construction": true});
            skLineSegment(sketch, "E92.27.0.11", {"start": v(648, 24) * mm, "end": v(672, 0) * mm, "construction": true});
            skLineSegment(sketch, "E92.27.0.12", {"start": v(672, 24) * mm, "end": v(648, 0) * mm, "construction": true});
            skArc(sketch, "E92.27.0.13", {"start": v(664.93, 9.9) * mm, "mid": v(662.1, 9.9) * mm, "end": v(662.1, 7.07) * mm});
            skArc(sketch, "E92.27.0.14", {"start": v(657.9, 7.07) * mm, "mid": v(657.9, 9.9) * mm, "end": v(655.07, 9.9) * mm});
            skArc(sketch, "E92.27.0.15", {"start": v(662.1, -7.07) * mm, "mid": v(662.1, -9.9) * mm, "end": v(664.93, -9.9) * mm});
            skArc(sketch, "E92.27.0.16", {"start": v(662.59, 6.59) * mm, "mid": v(665.41, 6.59) * mm, "end": v(665.41, 9.41) * mm});
            skLineSegment(sketch, "E92.27.0.17", {"start": v(656, -16) * mm, "end": v(664, -16) * mm, "construction": true});
            skLineSegment(sketch, "E92.27.0.18", {"start": v(648, 0) * mm, "end": v(672, 0) * mm, "construction": true});
            skArc(sketch, "E92.27.0.19", {"start": v(665.41, -9.41) * mm, "mid": v(665.41, -6.59) * mm, "end": v(662.59, -6.59) * mm});
            skCircle(sketch, "E92.27.0.20", {"center": v(656, -16) * mm, "radius": 2 * mm});
            skCircle(sketch, "E92.27.0.21", {"center": v(660, 0) * mm, "radius": 2 * mm});
            skPoint(sketch, "E92.27.0.22", {"position": v(656, -8) * mm});
            skLineSegment(sketch, "E92.27.0.23", {"start": v(672, 0) * mm, "end": v(648, 0) * mm, "construction": true});
            skLineSegment(sketch, "E92.27.0.24", {"start": v(662.59, 6.59) * mm, "end": v(665.41, 9.41) * mm, "construction": true});
            skLineSegment(sketch, "E92.27.0.25", {"start": v(662.1, -7.07) * mm, "end": v(664.93, -9.9) * mm, "construction": true});
            skLineSegment(sketch, "E92.27.0.26", {"start": v(654.59, 9.41) * mm, "end": v(657.41, 6.59) * mm, "construction": true});
            skLineSegment(sketch, "E92.27.0.27", {"start": v(655.07, 9.9) * mm, "end": v(657.9, 7.07) * mm, "construction": true});
            skLineSegment(sketch, "E92.27.0.28", {"start": v(664.93, 9.9) * mm, "end": v(662.1, 7.07) * mm, "construction": true});
            skLineSegment(sketch, "E92.27.0.29", {"start": v(662.59, -6.59) * mm, "end": v(665.41, -9.41) * mm, "construction": true});
            skLineSegment(sketch, "E92.27.0.30", {"start": v(655.07, -9.9) * mm, "end": v(657.9, -7.07) * mm, "construction": true});
            skLineSegment(sketch, "E92.27.0.31", {"start": v(657.41, -6.59) * mm, "end": v(654.59, -9.41) * mm, "construction": true});
            skLineSegment(sketch, "E92.27.0.32", {"start": v(662.1, -7.07) * mm, "end": v(662.59, -6.59) * mm});
            skLineSegment(sketch, "E92.27.0.33", {"start": v(654.59, 9.41) * mm, "end": v(655.07, 9.9) * mm});
            skLineSegment(sketch, "E92.27.0.34", {"start": v(654.59, -9.41) * mm, "end": v(655.07, -9.9) * mm});
            skLineSegment(sketch, "E92.27.0.35", {"start": v(664.93, -9.9) * mm, "end": v(665.41, -9.41) * mm});
            skLineSegment(sketch, "E92.27.0.36", {"start": v(657.41, 6.59) * mm, "end": v(657.9, 7.07) * mm});
            skLineSegment(sketch, "E92.27.0.37", {"start": v(664.93, 9.9) * mm, "end": v(665.41, 9.41) * mm});
            skLineSegment(sketch, "E92.27.0.38", {"start": v(662.1, 7.07) * mm, "end": v(662.59, 6.59) * mm});
            skLineSegment(sketch, "E92.27.0.39", {"start": v(657.41, -6.59) * mm, "end": v(657.9, -7.07) * mm});
            skArc(sketch, "E92.28.0.0", {"start": v(678.59, 9.41) * mm, "mid": v(678.59, 6.59) * mm, "end": v(681.41, 6.59) * mm});
            skArc(sketch, "E92.28.0.1", {"start": v(681.41, -6.59) * mm, "mid": v(678.59, -6.59) * mm, "end": v(678.59, -9.41) * mm});
            skLineSegment(sketch, "E92.28.0.2", {"start": v(672, 24) * mm, "end": v(696, 24) * mm, "construction": true});
            skLineSegment(sketch, "E92.28.0.3", {"start": v(680, 16) * mm, "end": v(688, 16) * mm, "construction": true});
            skArc(sketch, "E92.28.0.4", {"start": v(679.07, -9.9) * mm, "mid": v(681.9, -9.9) * mm, "end": v(681.9, -7.07) * mm});
            skLineSegment(sketch, "E92.28.0.5", {"start": v(696, 0) * mm, "end": v(672, -24) * mm, "construction": true});
            skCircle(sketch, "E92.28.0.6", {"center": v(688, -16) * mm, "radius": 2 * mm});
            skLineSegment(sketch, "E92.28.0.7", {"start": v(696, -24) * mm, "end": v(672, -24) * mm, "construction": true});
            skCircle(sketch, "E92.28.0.8", {"center": v(680, 16) * mm, "radius": 2 * mm});
            skCircle(sketch, "E92.28.0.9", {"center": v(688, 16) * mm, "radius": 2 * mm});
            skLineSegment(sketch, "E92.28.0.10", {"start": v(696, -24) * mm, "end": v(672, 0) * mm, "construction": true});
            skLineSegment(sketch, "E92.28.0.11", {"start": v(672, 24) * mm, "end": v(696, 0) * mm, "construction": true});
            skLineSegment(sketch, "E92.28.0.12", {"start": v(696, 24) * mm, "end": v(672, 0) * mm, "construction": true});
            skArc(sketch, "E92.28.0.13", {"start": v(688.93, 9.9) * mm, "mid": v(686.1, 9.9) * mm, "end": v(686.1, 7.07) * mm});
            skArc(sketch, "E92.28.0.14", {"start": v(681.9, 7.07) * mm, "mid": v(681.9, 9.9) * mm, "end": v(679.07, 9.9) * mm});
            skArc(sketch, "E92.28.0.15", {"start": v(686.1, -7.07) * mm, "mid": v(686.1, -9.9) * mm, "end": v(688.93, -9.9) * mm});
            skArc(sketch, "E92.28.0.16", {"start": v(686.59, 6.59) * mm, "mid": v(689.41, 6.59) * mm, "end": v(689.41, 9.41) * mm});
            skLineSegment(sketch, "E92.28.0.17", {"start": v(680, -16) * mm, "end": v(688, -16) * mm, "construction": true});
            skLineSegment(sketch, "E92.28.0.18", {"start": v(672, 0) * mm, "end": v(696, 0) * mm, "construction": true});
            skArc(sketch, "E92.28.0.19", {"start": v(689.41, -9.41) * mm, "mid": v(689.41, -6.59) * mm, "end": v(686.59, -6.59) * mm});
            skCircle(sketch, "E92.28.0.20", {"center": v(680, -16) * mm, "radius": 2 * mm});
            skCircle(sketch, "E92.28.0.21", {"center": v(684, 0) * mm, "radius": 2 * mm});
            skPoint(sketch, "E92.28.0.22", {"position": v(680, -8) * mm});
            skLineSegment(sketch, "E92.28.0.23", {"start": v(696, 0) * mm, "end": v(672, 0) * mm, "construction": true});
            skLineSegment(sketch, "E92.28.0.24", {"start": v(686.59, 6.59) * mm, "end": v(689.41, 9.41) * mm, "construction": true});
            skLineSegment(sketch, "E92.28.0.25", {"start": v(686.1, -7.07) * mm, "end": v(688.93, -9.9) * mm, "construction": true});
            skLineSegment(sketch, "E92.28.0.26", {"start": v(678.59, 9.41) * mm, "end": v(681.41, 6.59) * mm, "construction": true});
            skLineSegment(sketch, "E92.28.0.27", {"start": v(679.07, 9.9) * mm, "end": v(681.9, 7.07) * mm, "construction": true});
            skLineSegment(sketch, "E92.28.0.28", {"start": v(688.93, 9.9) * mm, "end": v(686.1, 7.07) * mm, "construction": true});
            skLineSegment(sketch, "E92.28.0.29", {"start": v(686.59, -6.59) * mm, "end": v(689.41, -9.41) * mm, "construction": true});
            skLineSegment(sketch, "E92.28.0.30", {"start": v(679.07, -9.9) * mm, "end": v(681.9, -7.07) * mm, "construction": true});
            skLineSegment(sketch, "E92.28.0.31", {"start": v(681.41, -6.59) * mm, "end": v(678.59, -9.41) * mm, "construction": true});
            skLineSegment(sketch, "E92.28.0.32", {"start": v(686.1, -7.07) * mm, "end": v(686.59, -6.59) * mm});
            skLineSegment(sketch, "E92.28.0.33", {"start": v(678.59, 9.41) * mm, "end": v(679.07, 9.9) * mm});
            skLineSegment(sketch, "E92.28.0.34", {"start": v(678.59, -9.41) * mm, "end": v(679.07, -9.9) * mm});
            skLineSegment(sketch, "E92.28.0.35", {"start": v(688.93, -9.9) * mm, "end": v(689.41, -9.41) * mm});
            skLineSegment(sketch, "E92.28.0.36", {"start": v(681.41, 6.59) * mm, "end": v(681.9, 7.07) * mm});
            skLineSegment(sketch, "E92.28.0.37", {"start": v(688.93, 9.9) * mm, "end": v(689.41, 9.41) * mm});
            skLineSegment(sketch, "E92.28.0.38", {"start": v(686.1, 7.07) * mm, "end": v(686.59, 6.59) * mm});
            skLineSegment(sketch, "E92.28.0.39", {"start": v(681.41, -6.59) * mm, "end": v(681.9, -7.07) * mm});
            skArc(sketch, "E92.29.0.0", {"start": v(702.59, 9.41) * mm, "mid": v(702.59, 6.59) * mm, "end": v(705.41, 6.59) * mm});
            skArc(sketch, "E92.29.0.1", {"start": v(705.41, -6.59) * mm, "mid": v(702.59, -6.59) * mm, "end": v(702.59, -9.41) * mm});
            skLineSegment(sketch, "E92.29.0.2", {"start": v(696, 24) * mm, "end": v(720, 24) * mm, "construction": true});
            skLineSegment(sketch, "E92.29.0.3", {"start": v(704, 16) * mm, "end": v(712, 16) * mm, "construction": true});
            skArc(sketch, "E92.29.0.4", {"start": v(703.07, -9.9) * mm, "mid": v(705.9, -9.9) * mm, "end": v(705.9, -7.07) * mm});
            skLineSegment(sketch, "E92.29.0.5", {"start": v(720, 0) * mm, "end": v(696, -24) * mm, "construction": true});
            skCircle(sketch, "E92.29.0.6", {"center": v(712, -16) * mm, "radius": 2 * mm});
            skLineSegment(sketch, "E92.29.0.7", {"start": v(720, -24) * mm, "end": v(696, -24) * mm, "construction": true});
            skCircle(sketch, "E92.29.0.8", {"center": v(704, 16) * mm, "radius": 2 * mm});
            skCircle(sketch, "E92.29.0.9", {"center": v(712, 16) * mm, "radius": 2 * mm});
            skLineSegment(sketch, "E92.29.0.10", {"start": v(720, -24) * mm, "end": v(696, 0) * mm, "construction": true});
            skLineSegment(sketch, "E92.29.0.11", {"start": v(696, 24) * mm, "end": v(720, 0) * mm, "construction": true});
            skLineSegment(sketch, "E92.29.0.12", {"start": v(720, 24) * mm, "end": v(696, 0) * mm, "construction": true});
            skArc(sketch, "E92.29.0.13", {"start": v(712.93, 9.9) * mm, "mid": v(710.1, 9.9) * mm, "end": v(710.1, 7.07) * mm});
            skArc(sketch, "E92.29.0.14", {"start": v(705.9, 7.07) * mm, "mid": v(705.9, 9.9) * mm, "end": v(703.07, 9.9) * mm});
            skArc(sketch, "E92.29.0.15", {"start": v(710.1, -7.07) * mm, "mid": v(710.1, -9.9) * mm, "end": v(712.93, -9.9) * mm});
            skArc(sketch, "E92.29.0.16", {"start": v(710.59, 6.59) * mm, "mid": v(713.41, 6.59) * mm, "end": v(713.41, 9.41) * mm});
            skLineSegment(sketch, "E92.29.0.17", {"start": v(704, -16) * mm, "end": v(712, -16) * mm, "construction": true});
            skLineSegment(sketch, "E92.29.0.18", {"start": v(696, 0) * mm, "end": v(720, 0) * mm, "construction": true});
            skArc(sketch, "E92.29.0.19", {"start": v(713.41, -9.41) * mm, "mid": v(713.41, -6.59) * mm, "end": v(710.59, -6.59) * mm});
            skCircle(sketch, "E92.29.0.20", {"center": v(704, -16) * mm, "radius": 2 * mm});
            skCircle(sketch, "E92.29.0.21", {"center": v(708, 0) * mm, "radius": 2 * mm});
            skPoint(sketch, "E92.29.0.22", {"position": v(704, -8) * mm});
            skLineSegment(sketch, "E92.29.0.23", {"start": v(720, 0) * mm, "end": v(696, 0) * mm, "construction": true});
            skLineSegment(sketch, "E92.29.0.24", {"start": v(710.59, 6.59) * mm, "end": v(713.41, 9.41) * mm, "construction": true});
            skLineSegment(sketch, "E92.29.0.25", {"start": v(710.1, -7.07) * mm, "end": v(712.93, -9.9) * mm, "construction": true});
            skLineSegment(sketch, "E92.29.0.26", {"start": v(702.59, 9.41) * mm, "end": v(705.41, 6.59) * mm, "construction": true});
            skLineSegment(sketch, "E92.29.0.27", {"start": v(703.07, 9.9) * mm, "end": v(705.9, 7.07) * mm, "construction": true});
            skLineSegment(sketch, "E92.29.0.28", {"start": v(712.93, 9.9) * mm, "end": v(710.1, 7.07) * mm, "construction": true});
            skLineSegment(sketch, "E92.29.0.29", {"start": v(710.59, -6.59) * mm, "end": v(713.41, -9.41) * mm, "construction": true});
            skLineSegment(sketch, "E92.29.0.30", {"start": v(703.07, -9.9) * mm, "end": v(705.9, -7.07) * mm, "construction": true});
            skLineSegment(sketch, "E92.29.0.31", {"start": v(705.41, -6.59) * mm, "end": v(702.59, -9.41) * mm, "construction": true});
            skLineSegment(sketch, "E92.29.0.32", {"start": v(710.1, -7.07) * mm, "end": v(710.59, -6.59) * mm});
            skLineSegment(sketch, "E92.29.0.33", {"start": v(702.59, 9.41) * mm, "end": v(703.07, 9.9) * mm});
            skLineSegment(sketch, "E92.29.0.34", {"start": v(702.59, -9.41) * mm, "end": v(703.07, -9.9) * mm});
            skLineSegment(sketch, "E92.29.0.35", {"start": v(712.93, -9.9) * mm, "end": v(713.41, -9.41) * mm});
            skLineSegment(sketch, "E92.29.0.36", {"start": v(705.41, 6.59) * mm, "end": v(705.9, 7.07) * mm});
            skLineSegment(sketch, "E92.29.0.37", {"start": v(712.93, 9.9) * mm, "end": v(713.41, 9.41) * mm});
            skLineSegment(sketch, "E92.29.0.38", {"start": v(710.1, 7.07) * mm, "end": v(710.59, 6.59) * mm});
            skLineSegment(sketch, "E92.29.0.39", {"start": v(705.41, -6.59) * mm, "end": v(705.9, -7.07) * mm});
            skArc(sketch, "E92.30.0.0", {"start": v(726.59, 9.41) * mm, "mid": v(726.59, 6.59) * mm, "end": v(729.41, 6.59) * mm});
            skArc(sketch, "E92.30.0.1", {"start": v(729.41, -6.59) * mm, "mid": v(726.59, -6.59) * mm, "end": v(726.59, -9.41) * mm});
            skLineSegment(sketch, "E92.30.0.2", {"start": v(720, 24) * mm, "end": v(744, 24) * mm, "construction": true});
            skLineSegment(sketch, "E92.30.0.3", {"start": v(728, 16) * mm, "end": v(736, 16) * mm, "construction": true});
            skArc(sketch, "E92.30.0.4", {"start": v(727.07, -9.9) * mm, "mid": v(729.9, -9.9) * mm, "end": v(729.9, -7.07) * mm});
            skLineSegment(sketch, "E92.30.0.5", {"start": v(744, 0) * mm, "end": v(720, -24) * mm, "construction": true});
            skCircle(sketch, "E92.30.0.6", {"center": v(736, -16) * mm, "radius": 2 * mm});
            skLineSegment(sketch, "E92.30.0.7", {"start": v(744, -24) * mm, "end": v(720, -24) * mm, "construction": true});
            skCircle(sketch, "E92.30.0.8", {"center": v(728, 16) * mm, "radius": 2 * mm});
            skCircle(sketch, "E92.30.0.9", {"center": v(736, 16) * mm, "radius": 2 * mm});
            skLineSegment(sketch, "E92.30.0.10", {"start": v(744, -24) * mm, "end": v(720, 0) * mm, "construction": true});
            skLineSegment(sketch, "E92.30.0.11", {"start": v(720, 24) * mm, "end": v(744, 0) * mm, "construction": true});
            skLineSegment(sketch, "E92.30.0.12", {"start": v(744, 24) * mm, "end": v(720, 0) * mm, "construction": true});
            skArc(sketch, "E92.30.0.13", {"start": v(736.93, 9.9) * mm, "mid": v(734.1, 9.9) * mm, "end": v(734.1, 7.07) * mm});
            skArc(sketch, "E92.30.0.14", {"start": v(729.9, 7.07) * mm, "mid": v(729.9, 9.9) * mm, "end": v(727.07, 9.9) * mm});
            skArc(sketch, "E92.30.0.15", {"start": v(734.1, -7.07) * mm, "mid": v(734.1, -9.9) * mm, "end": v(736.93, -9.9) * mm});
            skArc(sketch, "E92.30.0.16", {"start": v(734.59, 6.59) * mm, "mid": v(737.41, 6.59) * mm, "end": v(737.41, 9.41) * mm});
            skLineSegment(sketch, "E92.30.0.17", {"start": v(728, -16) * mm, "end": v(736, -16) * mm, "construction": true});
            skLineSegment(sketch, "E92.30.0.18", {"start": v(720, 0) * mm, "end": v(744, 0) * mm, "construction": true});
            skArc(sketch, "E92.30.0.19", {"start": v(737.41, -9.41) * mm, "mid": v(737.41, -6.59) * mm, "end": v(734.59, -6.59) * mm});
            skCircle(sketch, "E92.30.0.20", {"center": v(728, -16) * mm, "radius": 2 * mm});
            skCircle(sketch, "E92.30.0.21", {"center": v(732, 0) * mm, "radius": 2 * mm});
            skPoint(sketch, "E92.30.0.22", {"position": v(728, -8) * mm});
            skLineSegment(sketch, "E92.30.0.23", {"start": v(744, 0) * mm, "end": v(720, 0) * mm, "construction": true});
            skLineSegment(sketch, "E92.30.0.24", {"start": v(734.59, 6.59) * mm, "end": v(737.41, 9.41) * mm, "construction": true});
            skLineSegment(sketch, "E92.30.0.25", {"start": v(734.1, -7.07) * mm, "end": v(736.93, -9.9) * mm, "construction": true});
            skLineSegment(sketch, "E92.30.0.26", {"start": v(726.59, 9.41) * mm, "end": v(729.41, 6.59) * mm, "construction": true});
            skLineSegment(sketch, "E92.30.0.27", {"start": v(727.07, 9.9) * mm, "end": v(729.9, 7.07) * mm, "construction": true});
            skLineSegment(sketch, "E92.30.0.28", {"start": v(736.93, 9.9) * mm, "end": v(734.1, 7.07) * mm, "construction": true});
            skLineSegment(sketch, "E92.30.0.29", {"start": v(734.59, -6.59) * mm, "end": v(737.41, -9.41) * mm, "construction": true});
            skLineSegment(sketch, "E92.30.0.30", {"start": v(727.07, -9.9) * mm, "end": v(729.9, -7.07) * mm, "construction": true});
            skLineSegment(sketch, "E92.30.0.31", {"start": v(729.41, -6.59) * mm, "end": v(726.59, -9.41) * mm, "construction": true});
            skLineSegment(sketch, "E92.30.0.32", {"start": v(734.1, -7.07) * mm, "end": v(734.59, -6.59) * mm});
            skLineSegment(sketch, "E92.30.0.33", {"start": v(726.59, 9.41) * mm, "end": v(727.07, 9.9) * mm});
            skLineSegment(sketch, "E92.30.0.34", {"start": v(726.59, -9.41) * mm, "end": v(727.07, -9.9) * mm});
            skLineSegment(sketch, "E92.30.0.35", {"start": v(736.93, -9.9) * mm, "end": v(737.41, -9.41) * mm});
            skLineSegment(sketch, "E92.30.0.36", {"start": v(729.41, 6.59) * mm, "end": v(729.9, 7.07) * mm});
            skLineSegment(sketch, "E92.30.0.37", {"start": v(736.93, 9.9) * mm, "end": v(737.41, 9.41) * mm});
            skLineSegment(sketch, "E92.30.0.38", {"start": v(734.1, 7.07) * mm, "end": v(734.59, 6.59) * mm});
            skLineSegment(sketch, "E92.30.0.39", {"start": v(729.41, -6.59) * mm, "end": v(729.9, -7.07) * mm});
            skArc(sketch, "E92.31.0.0", {"start": v(750.59, 9.41) * mm, "mid": v(750.59, 6.59) * mm, "end": v(753.41, 6.59) * mm});
            skArc(sketch, "E92.31.0.1", {"start": v(753.41, -6.59) * mm, "mid": v(750.59, -6.59) * mm, "end": v(750.59, -9.41) * mm});
            skLineSegment(sketch, "E92.31.0.2", {"start": v(744, 24) * mm, "end": v(768, 24) * mm, "construction": true});
            skLineSegment(sketch, "E92.31.0.3", {"start": v(752, 16) * mm, "end": v(760, 16) * mm, "construction": true});
            skArc(sketch, "E92.31.0.4", {"start": v(751.07, -9.9) * mm, "mid": v(753.9, -9.9) * mm, "end": v(753.9, -7.07) * mm});
            skLineSegment(sketch, "E92.31.0.5", {"start": v(768, 0) * mm, "end": v(744, -24) * mm, "construction": true});
            skCircle(sketch, "E92.31.0.6", {"center": v(760, -16) * mm, "radius": 2 * mm});
            skLineSegment(sketch, "E92.31.0.7", {"start": v(768, -24) * mm, "end": v(744, -24) * mm, "construction": true});
            skCircle(sketch, "E92.31.0.8", {"center": v(752, 16) * mm, "radius": 2 * mm});
            skCircle(sketch, "E92.31.0.9", {"center": v(760, 16) * mm, "radius": 2 * mm});
            skLineSegment(sketch, "E92.31.0.10", {"start": v(768, -24) * mm, "end": v(744, 0) * mm, "construction": true});
            skLineSegment(sketch, "E92.31.0.11", {"start": v(744, 24) * mm, "end": v(768, 0) * mm, "construction": true});
            skLineSegment(sketch, "E92.31.0.12", {"start": v(768, 24) * mm, "end": v(744, 0) * mm, "construction": true});
            skArc(sketch, "E92.31.0.13", {"start": v(760.93, 9.9) * mm, "mid": v(758.1, 9.9) * mm, "end": v(758.1, 7.07) * mm});
            skArc(sketch, "E92.31.0.14", {"start": v(753.9, 7.07) * mm, "mid": v(753.9, 9.9) * mm, "end": v(751.07, 9.9) * mm});
            skArc(sketch, "E92.31.0.15", {"start": v(758.1, -7.07) * mm, "mid": v(758.1, -9.9) * mm, "end": v(760.93, -9.9) * mm});
            skArc(sketch, "E92.31.0.16", {"start": v(758.59, 6.59) * mm, "mid": v(761.41, 6.59) * mm, "end": v(761.41, 9.41) * mm});
            skLineSegment(sketch, "E92.31.0.17", {"start": v(752, -16) * mm, "end": v(760, -16) * mm, "construction": true});
            skLineSegment(sketch, "E92.31.0.18", {"start": v(744, 0) * mm, "end": v(768, 0) * mm, "construction": true});
            skArc(sketch, "E92.31.0.19", {"start": v(761.41, -9.41) * mm, "mid": v(761.41, -6.59) * mm, "end": v(758.59, -6.59) * mm});
            skCircle(sketch, "E92.31.0.20", {"center": v(752, -16) * mm, "radius": 2 * mm});
            skCircle(sketch, "E92.31.0.21", {"center": v(756, 0) * mm, "radius": 2 * mm});
            skPoint(sketch, "E92.31.0.22", {"position": v(752, -8) * mm});
            skLineSegment(sketch, "E92.31.0.23", {"start": v(768, 0) * mm, "end": v(744, 0) * mm, "construction": true});
            skLineSegment(sketch, "E92.31.0.24", {"start": v(758.59, 6.59) * mm, "end": v(761.41, 9.41) * mm, "construction": true});
            skLineSegment(sketch, "E92.31.0.25", {"start": v(758.1, -7.07) * mm, "end": v(760.93, -9.9) * mm, "construction": true});
            skLineSegment(sketch, "E92.31.0.26", {"start": v(750.59, 9.41) * mm, "end": v(753.41, 6.59) * mm, "construction": true});
            skLineSegment(sketch, "E92.31.0.27", {"start": v(751.07, 9.9) * mm, "end": v(753.9, 7.07) * mm, "construction": true});
            skLineSegment(sketch, "E92.31.0.28", {"start": v(760.93, 9.9) * mm, "end": v(758.1, 7.07) * mm, "construction": true});
            skLineSegment(sketch, "E92.31.0.29", {"start": v(758.59, -6.59) * mm, "end": v(761.41, -9.41) * mm, "construction": true});
            skLineSegment(sketch, "E92.31.0.30", {"start": v(751.07, -9.9) * mm, "end": v(753.9, -7.07) * mm, "construction": true});
            skLineSegment(sketch, "E92.31.0.31", {"start": v(753.41, -6.59) * mm, "end": v(750.59, -9.41) * mm, "construction": true});
            skLineSegment(sketch, "E92.31.0.32", {"start": v(758.1, -7.07) * mm, "end": v(758.59, -6.59) * mm});
            skLineSegment(sketch, "E92.31.0.33", {"start": v(750.59, 9.41) * mm, "end": v(751.07, 9.9) * mm});
            skLineSegment(sketch, "E92.31.0.34", {"start": v(750.59, -9.41) * mm, "end": v(751.07, -9.9) * mm});
            skLineSegment(sketch, "E92.31.0.35", {"start": v(760.93, -9.9) * mm, "end": v(761.41, -9.41) * mm});
            skLineSegment(sketch, "E92.31.0.36", {"start": v(753.41, 6.59) * mm, "end": v(753.9, 7.07) * mm});
            skLineSegment(sketch, "E92.31.0.37", {"start": v(760.93, 9.9) * mm, "end": v(761.41, 9.41) * mm});
            skLineSegment(sketch, "E92.31.0.38", {"start": v(758.1, 7.07) * mm, "end": v(758.59, 6.59) * mm});
            skLineSegment(sketch, "E92.31.0.39", {"start": v(753.41, -6.59) * mm, "end": v(753.9, -7.07) * mm});
            skArc(sketch, "E92.32.0.0", {"start": v(774.59, 9.41) * mm, "mid": v(774.59, 6.59) * mm, "end": v(777.41, 6.59) * mm});
            skArc(sketch, "E92.32.0.1", {"start": v(777.41, -6.59) * mm, "mid": v(774.59, -6.59) * mm, "end": v(774.59, -9.41) * mm});
            skLineSegment(sketch, "E92.32.0.2", {"start": v(768, 24) * mm, "end": v(792, 24) * mm, "construction": true});
            skLineSegment(sketch, "E92.32.0.3", {"start": v(776, 16) * mm, "end": v(784, 16) * mm, "construction": true});
            skArc(sketch, "E92.32.0.4", {"start": v(775.07, -9.9) * mm, "mid": v(777.9, -9.9) * mm, "end": v(777.9, -7.07) * mm});
            skLineSegment(sketch, "E92.32.0.5", {"start": v(792, 0) * mm, "end": v(768, -24) * mm, "construction": true});
            skCircle(sketch, "E92.32.0.6", {"center": v(784, -16) * mm, "radius": 2 * mm});
            skLineSegment(sketch, "E92.32.0.7", {"start": v(792, -24) * mm, "end": v(768, -24) * mm, "construction": true});
            skCircle(sketch, "E92.32.0.8", {"center": v(776, 16) * mm, "radius": 2 * mm});
            skCircle(sketch, "E92.32.0.9", {"center": v(784, 16) * mm, "radius": 2 * mm});
            skLineSegment(sketch, "E92.32.0.10", {"start": v(792, -24) * mm, "end": v(768, 0) * mm, "construction": true});
            skLineSegment(sketch, "E92.32.0.11", {"start": v(768, 24) * mm, "end": v(792, 0) * mm, "construction": true});
            skLineSegment(sketch, "E92.32.0.12", {"start": v(792, 24) * mm, "end": v(768, 0) * mm, "construction": true});
            skArc(sketch, "E92.32.0.13", {"start": v(784.93, 9.9) * mm, "mid": v(782.1, 9.9) * mm, "end": v(782.1, 7.07) * mm});
            skArc(sketch, "E92.32.0.14", {"start": v(777.9, 7.07) * mm, "mid": v(777.9, 9.9) * mm, "end": v(775.07, 9.9) * mm});
            skArc(sketch, "E92.32.0.15", {"start": v(782.1, -7.07) * mm, "mid": v(782.1, -9.9) * mm, "end": v(784.93, -9.9) * mm});
            skArc(sketch, "E92.32.0.16", {"start": v(782.59, 6.59) * mm, "mid": v(785.41, 6.59) * mm, "end": v(785.41, 9.41) * mm});
            skLineSegment(sketch, "E92.32.0.17", {"start": v(776, -16) * mm, "end": v(784, -16) * mm, "construction": true});
            skLineSegment(sketch, "E92.32.0.18", {"start": v(768, 0) * mm, "end": v(792, 0) * mm, "construction": true});
            skArc(sketch, "E92.32.0.19", {"start": v(785.41, -9.41) * mm, "mid": v(785.41, -6.59) * mm, "end": v(782.59, -6.59) * mm});
            skCircle(sketch, "E92.32.0.20", {"center": v(776, -16) * mm, "radius": 2 * mm});
            skCircle(sketch, "E92.32.0.21", {"center": v(780, 0) * mm, "radius": 2 * mm});
            skPoint(sketch, "E92.32.0.22", {"position": v(776, -8) * mm});
            skLineSegment(sketch, "E92.32.0.23", {"start": v(792, 0) * mm, "end": v(768, 0) * mm, "construction": true});
            skLineSegment(sketch, "E92.32.0.24", {"start": v(782.59, 6.59) * mm, "end": v(785.41, 9.41) * mm, "construction": true});
            skLineSegment(sketch, "E92.32.0.25", {"start": v(782.1, -7.07) * mm, "end": v(784.93, -9.9) * mm, "construction": true});
            skLineSegment(sketch, "E92.32.0.26", {"start": v(774.59, 9.41) * mm, "end": v(777.41, 6.59) * mm, "construction": true});
            skLineSegment(sketch, "E92.32.0.27", {"start": v(775.07, 9.9) * mm, "end": v(777.9, 7.07) * mm, "construction": true});
            skLineSegment(sketch, "E92.32.0.28", {"start": v(784.93, 9.9) * mm, "end": v(782.1, 7.07) * mm, "construction": true});
            skLineSegment(sketch, "E92.32.0.29", {"start": v(782.59, -6.59) * mm, "end": v(785.41, -9.41) * mm, "construction": true});
            skLineSegment(sketch, "E92.32.0.30", {"start": v(775.07, -9.9) * mm, "end": v(777.9, -7.07) * mm, "construction": true});
            skLineSegment(sketch, "E92.32.0.31", {"start": v(777.41, -6.59) * mm, "end": v(774.59, -9.41) * mm, "construction": true});
            skLineSegment(sketch, "E92.32.0.32", {"start": v(782.1, -7.07) * mm, "end": v(782.59, -6.59) * mm});
            skLineSegment(sketch, "E92.32.0.33", {"start": v(774.59, 9.41) * mm, "end": v(775.07, 9.9) * mm});
            skLineSegment(sketch, "E92.32.0.34", {"start": v(774.59, -9.41) * mm, "end": v(775.07, -9.9) * mm});
            skLineSegment(sketch, "E92.32.0.35", {"start": v(784.93, -9.9) * mm, "end": v(785.41, -9.41) * mm});
            skLineSegment(sketch, "E92.32.0.36", {"start": v(777.41, 6.59) * mm, "end": v(777.9, 7.07) * mm});
            skLineSegment(sketch, "E92.32.0.37", {"start": v(784.93, 9.9) * mm, "end": v(785.41, 9.41) * mm});
            skLineSegment(sketch, "E92.32.0.38", {"start": v(782.1, 7.07) * mm, "end": v(782.59, 6.59) * mm});
            skLineSegment(sketch, "E92.32.0.39", {"start": v(777.41, -6.59) * mm, "end": v(777.9, -7.07) * mm});
            skArc(sketch, "E92.33.0.0", {"start": v(798.59, 9.41) * mm, "mid": v(798.59, 6.59) * mm, "end": v(801.41, 6.59) * mm});
            skArc(sketch, "E92.33.0.1", {"start": v(801.41, -6.59) * mm, "mid": v(798.59, -6.59) * mm, "end": v(798.59, -9.41) * mm});
            skLineSegment(sketch, "E92.33.0.2", {"start": v(792, 24) * mm, "end": v(816, 24) * mm, "construction": true});
            skLineSegment(sketch, "E92.33.0.3", {"start": v(800, 16) * mm, "end": v(808, 16) * mm, "construction": true});
            skArc(sketch, "E92.33.0.4", {"start": v(799.07, -9.9) * mm, "mid": v(801.9, -9.9) * mm, "end": v(801.9, -7.07) * mm});
            skLineSegment(sketch, "E92.33.0.5", {"start": v(816, 0) * mm, "end": v(792, -24) * mm, "construction": true});
            skCircle(sketch, "E92.33.0.6", {"center": v(808, -16) * mm, "radius": 2 * mm});
            skLineSegment(sketch, "E92.33.0.7", {"start": v(816, -24) * mm, "end": v(792, -24) * mm, "construction": true});
            skCircle(sketch, "E92.33.0.8", {"center": v(800, 16) * mm, "radius": 2 * mm});
            skCircle(sketch, "E92.33.0.9", {"center": v(808, 16) * mm, "radius": 2 * mm});
            skLineSegment(sketch, "E92.33.0.10", {"start": v(816, -24) * mm, "end": v(792, 0) * mm, "construction": true});
            skLineSegment(sketch, "E92.33.0.11", {"start": v(792, 24) * mm, "end": v(816, 0) * mm, "construction": true});
            skLineSegment(sketch, "E92.33.0.12", {"start": v(816, 24) * mm, "end": v(792, 0) * mm, "construction": true});
            skArc(sketch, "E92.33.0.13", {"start": v(808.93, 9.9) * mm, "mid": v(806.1, 9.9) * mm, "end": v(806.1, 7.07) * mm});
            skArc(sketch, "E92.33.0.14", {"start": v(801.9, 7.07) * mm, "mid": v(801.9, 9.9) * mm, "end": v(799.07, 9.9) * mm});
            skArc(sketch, "E92.33.0.15", {"start": v(806.1, -7.07) * mm, "mid": v(806.1, -9.9) * mm, "end": v(808.93, -9.9) * mm});
            skArc(sketch, "E92.33.0.16", {"start": v(806.59, 6.59) * mm, "mid": v(809.41, 6.59) * mm, "end": v(809.41, 9.41) * mm});
            skLineSegment(sketch, "E92.33.0.17", {"start": v(800, -16) * mm, "end": v(808, -16) * mm, "construction": true});
            skLineSegment(sketch, "E92.33.0.18", {"start": v(792, 0) * mm, "end": v(816, 0) * mm, "construction": true});
            skArc(sketch, "E92.33.0.19", {"start": v(809.41, -9.41) * mm, "mid": v(809.41, -6.59) * mm, "end": v(806.59, -6.59) * mm});
            skCircle(sketch, "E92.33.0.20", {"center": v(800, -16) * mm, "radius": 2 * mm});
            skCircle(sketch, "E92.33.0.21", {"center": v(804, 0) * mm, "radius": 2 * mm});
            skPoint(sketch, "E92.33.0.22", {"position": v(800, -8) * mm});
            skLineSegment(sketch, "E92.33.0.23", {"start": v(816, 0) * mm, "end": v(792, 0) * mm, "construction": true});
            skLineSegment(sketch, "E92.33.0.24", {"start": v(806.59, 6.59) * mm, "end": v(809.41, 9.41) * mm, "construction": true});
            skLineSegment(sketch, "E92.33.0.25", {"start": v(806.1, -7.07) * mm, "end": v(808.93, -9.9) * mm, "construction": true});
            skLineSegment(sketch, "E92.33.0.26", {"start": v(798.59, 9.41) * mm, "end": v(801.41, 6.59) * mm, "construction": true});
            skLineSegment(sketch, "E92.33.0.27", {"start": v(799.07, 9.9) * mm, "end": v(801.9, 7.07) * mm, "construction": true});
            skLineSegment(sketch, "E92.33.0.28", {"start": v(808.93, 9.9) * mm, "end": v(806.1, 7.07) * mm, "construction": true});
            skLineSegment(sketch, "E92.33.0.29", {"start": v(806.59, -6.59) * mm, "end": v(809.41, -9.41) * mm, "construction": true});
            skLineSegment(sketch, "E92.33.0.30", {"start": v(799.07, -9.9) * mm, "end": v(801.9, -7.07) * mm, "construction": true});
            skLineSegment(sketch, "E92.33.0.31", {"start": v(801.41, -6.59) * mm, "end": v(798.59, -9.41) * mm, "construction": true});
            skLineSegment(sketch, "E92.33.0.32", {"start": v(806.1, -7.07) * mm, "end": v(806.59, -6.59) * mm});
            skLineSegment(sketch, "E92.33.0.33", {"start": v(798.59, 9.41) * mm, "end": v(799.07, 9.9) * mm});
            skLineSegment(sketch, "E92.33.0.34", {"start": v(798.59, -9.41) * mm, "end": v(799.07, -9.9) * mm});
            skLineSegment(sketch, "E92.33.0.35", {"start": v(808.93, -9.9) * mm, "end": v(809.41, -9.41) * mm});
            skLineSegment(sketch, "E92.33.0.36", {"start": v(801.41, 6.59) * mm, "end": v(801.9, 7.07) * mm});
            skLineSegment(sketch, "E92.33.0.37", {"start": v(808.93, 9.9) * mm, "end": v(809.41, 9.41) * mm});
            skLineSegment(sketch, "E92.33.0.38", {"start": v(806.1, 7.07) * mm, "end": v(806.59, 6.59) * mm});
            skLineSegment(sketch, "E92.33.0.39", {"start": v(801.41, -6.59) * mm, "end": v(801.9, -7.07) * mm});
            skArc(sketch, "E92.34.0.0", {"start": v(822.59, 9.41) * mm, "mid": v(822.59, 6.59) * mm, "end": v(825.41, 6.59) * mm});
            skArc(sketch, "E92.34.0.1", {"start": v(825.41, -6.59) * mm, "mid": v(822.59, -6.59) * mm, "end": v(822.59, -9.41) * mm});
            skLineSegment(sketch, "E92.34.0.2", {"start": v(816, 24) * mm, "end": v(840, 24) * mm, "construction": true});
            skLineSegment(sketch, "E92.34.0.3", {"start": v(824, 16) * mm, "end": v(832, 16) * mm, "construction": true});
            skArc(sketch, "E92.34.0.4", {"start": v(823.07, -9.9) * mm, "mid": v(825.9, -9.9) * mm, "end": v(825.9, -7.07) * mm});
            skLineSegment(sketch, "E92.34.0.5", {"start": v(840, 0) * mm, "end": v(816, -24) * mm, "construction": true});
            skCircle(sketch, "E92.34.0.6", {"center": v(832, -16) * mm, "radius": 2 * mm});
            skLineSegment(sketch, "E92.34.0.7", {"start": v(840, -24) * mm, "end": v(816, -24) * mm, "construction": true});
            skCircle(sketch, "E92.34.0.8", {"center": v(824, 16) * mm, "radius": 2 * mm});
            skCircle(sketch, "E92.34.0.9", {"center": v(832, 16) * mm, "radius": 2 * mm});
            skLineSegment(sketch, "E92.34.0.10", {"start": v(840, -24) * mm, "end": v(816, 0) * mm, "construction": true});
            skLineSegment(sketch, "E92.34.0.11", {"start": v(816, 24) * mm, "end": v(840, 0) * mm, "construction": true});
            skLineSegment(sketch, "E92.34.0.12", {"start": v(840, 24) * mm, "end": v(816, 0) * mm, "construction": true});
            skArc(sketch, "E92.34.0.13", {"start": v(832.93, 9.9) * mm, "mid": v(830.1, 9.9) * mm, "end": v(830.1, 7.07) * mm});
            skArc(sketch, "E92.34.0.14", {"start": v(825.9, 7.07) * mm, "mid": v(825.9, 9.9) * mm, "end": v(823.07, 9.9) * mm});
            skArc(sketch, "E92.34.0.15", {"start": v(830.1, -7.07) * mm, "mid": v(830.1, -9.9) * mm, "end": v(832.93, -9.9) * mm});
            skArc(sketch, "E92.34.0.16", {"start": v(830.59, 6.59) * mm, "mid": v(833.41, 6.59) * mm, "end": v(833.41, 9.41) * mm});
            skLineSegment(sketch, "E92.34.0.17", {"start": v(824, -16) * mm, "end": v(832, -16) * mm, "construction": true});
            skLineSegment(sketch, "E92.34.0.18", {"start": v(816, 0) * mm, "end": v(840, 0) * mm, "construction": true});
            skArc(sketch, "E92.34.0.19", {"start": v(833.41, -9.41) * mm, "mid": v(833.41, -6.59) * mm, "end": v(830.59, -6.59) * mm});
            skCircle(sketch, "E92.34.0.20", {"center": v(824, -16) * mm, "radius": 2 * mm});
            skCircle(sketch, "E92.34.0.21", {"center": v(828, 0) * mm, "radius": 2 * mm});
            skPoint(sketch, "E92.34.0.22", {"position": v(824, -8) * mm});
            skLineSegment(sketch, "E92.34.0.23", {"start": v(840, 0) * mm, "end": v(816, 0) * mm, "construction": true});
            skLineSegment(sketch, "E92.34.0.24", {"start": v(830.59, 6.59) * mm, "end": v(833.41, 9.41) * mm, "construction": true});
            skLineSegment(sketch, "E92.34.0.25", {"start": v(830.1, -7.07) * mm, "end": v(832.93, -9.9) * mm, "construction": true});
            skLineSegment(sketch, "E92.34.0.26", {"start": v(822.59, 9.41) * mm, "end": v(825.41, 6.59) * mm, "construction": true});
            skLineSegment(sketch, "E92.34.0.27", {"start": v(823.07, 9.9) * mm, "end": v(825.9, 7.07) * mm, "construction": true});
            skLineSegment(sketch, "E92.34.0.28", {"start": v(832.93, 9.9) * mm, "end": v(830.1, 7.07) * mm, "construction": true});
            skLineSegment(sketch, "E92.34.0.29", {"start": v(830.59, -6.59) * mm, "end": v(833.41, -9.41) * mm, "construction": true});
            skLineSegment(sketch, "E92.34.0.30", {"start": v(823.07, -9.9) * mm, "end": v(825.9, -7.07) * mm, "construction": true});
            skLineSegment(sketch, "E92.34.0.31", {"start": v(825.41, -6.59) * mm, "end": v(822.59, -9.41) * mm, "construction": true});
            skLineSegment(sketch, "E92.34.0.32", {"start": v(830.1, -7.07) * mm, "end": v(830.59, -6.59) * mm});
            skLineSegment(sketch, "E92.34.0.33", {"start": v(822.59, 9.41) * mm, "end": v(823.07, 9.9) * mm});
            skLineSegment(sketch, "E92.34.0.34", {"start": v(822.59, -9.41) * mm, "end": v(823.07, -9.9) * mm});
            skLineSegment(sketch, "E92.34.0.35", {"start": v(832.93, -9.9) * mm, "end": v(833.41, -9.41) * mm});
            skLineSegment(sketch, "E92.34.0.36", {"start": v(825.41, 6.59) * mm, "end": v(825.9, 7.07) * mm});
            skLineSegment(sketch, "E92.34.0.37", {"start": v(832.93, 9.9) * mm, "end": v(833.41, 9.41) * mm});
            skLineSegment(sketch, "E92.34.0.38", {"start": v(830.1, 7.07) * mm, "end": v(830.59, 6.59) * mm});
            skLineSegment(sketch, "E92.34.0.39", {"start": v(825.41, -6.59) * mm, "end": v(825.9, -7.07) * mm});
            skArc(sketch, "E92.35.0.0", {"start": v(846.59, 9.41) * mm, "mid": v(846.59, 6.59) * mm, "end": v(849.41, 6.59) * mm});
            skArc(sketch, "E92.35.0.1", {"start": v(849.41, -6.59) * mm, "mid": v(846.59, -6.59) * mm, "end": v(846.59, -9.41) * mm});
            skLineSegment(sketch, "E92.35.0.2", {"start": v(840, 24) * mm, "end": v(864, 24) * mm, "construction": true});
            skLineSegment(sketch, "E92.35.0.3", {"start": v(848, 16) * mm, "end": v(856, 16) * mm, "construction": true});
            skArc(sketch, "E92.35.0.4", {"start": v(847.07, -9.9) * mm, "mid": v(849.9, -9.9) * mm, "end": v(849.9, -7.07) * mm});
            skLineSegment(sketch, "E92.35.0.5", {"start": v(864, 0) * mm, "end": v(840, -24) * mm, "construction": true});
            skCircle(sketch, "E92.35.0.6", {"center": v(856, -16) * mm, "radius": 2 * mm});
            skLineSegment(sketch, "E92.35.0.7", {"start": v(864, -24) * mm, "end": v(840, -24) * mm, "construction": true});
            skCircle(sketch, "E92.35.0.8", {"center": v(848, 16) * mm, "radius": 2 * mm});
            skCircle(sketch, "E92.35.0.9", {"center": v(856, 16) * mm, "radius": 2 * mm});
            skLineSegment(sketch, "E92.35.0.10", {"start": v(864, -24) * mm, "end": v(840, 0) * mm, "construction": true});
            skLineSegment(sketch, "E92.35.0.11", {"start": v(840, 24) * mm, "end": v(864, 0) * mm, "construction": true});
            skLineSegment(sketch, "E92.35.0.12", {"start": v(864, 24) * mm, "end": v(840, 0) * mm, "construction": true});
            skArc(sketch, "E92.35.0.13", {"start": v(856.93, 9.9) * mm, "mid": v(854.1, 9.9) * mm, "end": v(854.1, 7.07) * mm});
            skArc(sketch, "E92.35.0.14", {"start": v(849.9, 7.07) * mm, "mid": v(849.9, 9.9) * mm, "end": v(847.07, 9.9) * mm});
            skArc(sketch, "E92.35.0.15", {"start": v(854.1, -7.07) * mm, "mid": v(854.1, -9.9) * mm, "end": v(856.93, -9.9) * mm});
            skArc(sketch, "E92.35.0.16", {"start": v(854.59, 6.59) * mm, "mid": v(857.41, 6.59) * mm, "end": v(857.41, 9.41) * mm});
            skLineSegment(sketch, "E92.35.0.17", {"start": v(848, -16) * mm, "end": v(856, -16) * mm, "construction": true});
            skLineSegment(sketch, "E92.35.0.18", {"start": v(840, 0) * mm, "end": v(864, 0) * mm, "construction": true});
            skArc(sketch, "E92.35.0.19", {"start": v(857.41, -9.41) * mm, "mid": v(857.41, -6.59) * mm, "end": v(854.59, -6.59) * mm});
            skCircle(sketch, "E92.35.0.20", {"center": v(848, -16) * mm, "radius": 2 * mm});
            skCircle(sketch, "E92.35.0.21", {"center": v(852, 0) * mm, "radius": 2 * mm});
            skPoint(sketch, "E92.35.0.22", {"position": v(848, -8) * mm});
            skLineSegment(sketch, "E92.35.0.23", {"start": v(864, 0) * mm, "end": v(840, 0) * mm, "construction": true});
            skLineSegment(sketch, "E92.35.0.24", {"start": v(854.59, 6.59) * mm, "end": v(857.41, 9.41) * mm, "construction": true});
            skLineSegment(sketch, "E92.35.0.25", {"start": v(854.1, -7.07) * mm, "end": v(856.93, -9.9) * mm, "construction": true});
            skLineSegment(sketch, "E92.35.0.26", {"start": v(846.59, 9.41) * mm, "end": v(849.41, 6.59) * mm, "construction": true});
            skLineSegment(sketch, "E92.35.0.27", {"start": v(847.07, 9.9) * mm, "end": v(849.9, 7.07) * mm, "construction": true});
            skLineSegment(sketch, "E92.35.0.28", {"start": v(856.93, 9.9) * mm, "end": v(854.1, 7.07) * mm, "construction": true});
            skLineSegment(sketch, "E92.35.0.29", {"start": v(854.59, -6.59) * mm, "end": v(857.41, -9.41) * mm, "construction": true});
            skLineSegment(sketch, "E92.35.0.30", {"start": v(847.07, -9.9) * mm, "end": v(849.9, -7.07) * mm, "construction": true});
            skLineSegment(sketch, "E92.35.0.31", {"start": v(849.41, -6.59) * mm, "end": v(846.59, -9.41) * mm, "construction": true});
            skLineSegment(sketch, "E92.35.0.32", {"start": v(854.1, -7.07) * mm, "end": v(854.59, -6.59) * mm});
            skLineSegment(sketch, "E92.35.0.33", {"start": v(846.59, 9.41) * mm, "end": v(847.07, 9.9) * mm});
            skLineSegment(sketch, "E92.35.0.34", {"start": v(846.59, -9.41) * mm, "end": v(847.07, -9.9) * mm});
            skLineSegment(sketch, "E92.35.0.35", {"start": v(856.93, -9.9) * mm, "end": v(857.41, -9.41) * mm});
            skLineSegment(sketch, "E92.35.0.36", {"start": v(849.41, 6.59) * mm, "end": v(849.9, 7.07) * mm});
            skLineSegment(sketch, "E92.35.0.37", {"start": v(856.93, 9.9) * mm, "end": v(857.41, 9.41) * mm});
            skLineSegment(sketch, "E92.35.0.38", {"start": v(854.1, 7.07) * mm, "end": v(854.59, 6.59) * mm});
            skLineSegment(sketch, "E92.35.0.39", {"start": v(849.41, -6.59) * mm, "end": v(849.9, -7.07) * mm});
            skArc(sketch, "E92.36.0.0", {"start": v(870.59, 9.41) * mm, "mid": v(870.59, 6.59) * mm, "end": v(873.41, 6.59) * mm});
            skArc(sketch, "E92.36.0.1", {"start": v(873.41, -6.59) * mm, "mid": v(870.59, -6.59) * mm, "end": v(870.59, -9.41) * mm});
            skLineSegment(sketch, "E92.36.0.2", {"start": v(864, 24) * mm, "end": v(888, 24) * mm, "construction": true});
            skLineSegment(sketch, "E92.36.0.3", {"start": v(872, 16) * mm, "end": v(880, 16) * mm, "construction": true});
            skArc(sketch, "E92.36.0.4", {"start": v(871.07, -9.9) * mm, "mid": v(873.9, -9.9) * mm, "end": v(873.9, -7.07) * mm});
            skLineSegment(sketch, "E92.36.0.5", {"start": v(888, 0) * mm, "end": v(864, -24) * mm, "construction": true});
            skCircle(sketch, "E92.36.0.6", {"center": v(880, -16) * mm, "radius": 2 * mm});
            skLineSegment(sketch, "E92.36.0.7", {"start": v(888, -24) * mm, "end": v(864, -24) * mm, "construction": true});
            skCircle(sketch, "E92.36.0.8", {"center": v(872, 16) * mm, "radius": 2 * mm});
            skCircle(sketch, "E92.36.0.9", {"center": v(880, 16) * mm, "radius": 2 * mm});
            skLineSegment(sketch, "E92.36.0.10", {"start": v(888, -24) * mm, "end": v(864, 0) * mm, "construction": true});
            skLineSegment(sketch, "E92.36.0.11", {"start": v(864, 24) * mm, "end": v(888, 0) * mm, "construction": true});
            skLineSegment(sketch, "E92.36.0.12", {"start": v(888, 24) * mm, "end": v(864, 0) * mm, "construction": true});
            skArc(sketch, "E92.36.0.13", {"start": v(880.93, 9.9) * mm, "mid": v(878.1, 9.9) * mm, "end": v(878.1, 7.07) * mm});
            skArc(sketch, "E92.36.0.14", {"start": v(873.9, 7.07) * mm, "mid": v(873.9, 9.9) * mm, "end": v(871.07, 9.9) * mm});
            skArc(sketch, "E92.36.0.15", {"start": v(878.1, -7.07) * mm, "mid": v(878.1, -9.9) * mm, "end": v(880.93, -9.9) * mm});
            skArc(sketch, "E92.36.0.16", {"start": v(878.59, 6.59) * mm, "mid": v(881.41, 6.59) * mm, "end": v(881.41, 9.41) * mm});
            skLineSegment(sketch, "E92.36.0.17", {"start": v(872, -16) * mm, "end": v(880, -16) * mm, "construction": true});
            skLineSegment(sketch, "E92.36.0.18", {"start": v(864, 0) * mm, "end": v(888, 0) * mm, "construction": true});
            skArc(sketch, "E92.36.0.19", {"start": v(881.41, -9.41) * mm, "mid": v(881.41, -6.59) * mm, "end": v(878.59, -6.59) * mm});
            skCircle(sketch, "E92.36.0.20", {"center": v(872, -16) * mm, "radius": 2 * mm});
            skCircle(sketch, "E92.36.0.21", {"center": v(876, 0) * mm, "radius": 2 * mm});
            skPoint(sketch, "E92.36.0.22", {"position": v(872, -8) * mm});
            skLineSegment(sketch, "E92.36.0.23", {"start": v(888, 0) * mm, "end": v(864, 0) * mm, "construction": true});
            skLineSegment(sketch, "E92.36.0.24", {"start": v(878.59, 6.59) * mm, "end": v(881.41, 9.41) * mm, "construction": true});
            skLineSegment(sketch, "E92.36.0.25", {"start": v(878.1, -7.07) * mm, "end": v(880.93, -9.9) * mm, "construction": true});
            skLineSegment(sketch, "E92.36.0.26", {"start": v(870.59, 9.41) * mm, "end": v(873.41, 6.59) * mm, "construction": true});
            skLineSegment(sketch, "E92.36.0.27", {"start": v(871.07, 9.9) * mm, "end": v(873.9, 7.07) * mm, "construction": true});
            skLineSegment(sketch, "E92.36.0.28", {"start": v(880.93, 9.9) * mm, "end": v(878.1, 7.07) * mm, "construction": true});
            skLineSegment(sketch, "E92.36.0.29", {"start": v(878.59, -6.59) * mm, "end": v(881.41, -9.41) * mm, "construction": true});
            skLineSegment(sketch, "E92.36.0.30", {"start": v(871.07, -9.9) * mm, "end": v(873.9, -7.07) * mm, "construction": true});
            skLineSegment(sketch, "E92.36.0.31", {"start": v(873.41, -6.59) * mm, "end": v(870.59, -9.41) * mm, "construction": true});
            skLineSegment(sketch, "E92.36.0.32", {"start": v(878.1, -7.07) * mm, "end": v(878.59, -6.59) * mm});
            skLineSegment(sketch, "E92.36.0.33", {"start": v(870.59, 9.41) * mm, "end": v(871.07, 9.9) * mm});
            skLineSegment(sketch, "E92.36.0.34", {"start": v(870.59, -9.41) * mm, "end": v(871.07, -9.9) * mm});
            skLineSegment(sketch, "E92.36.0.35", {"start": v(880.93, -9.9) * mm, "end": v(881.41, -9.41) * mm});
            skLineSegment(sketch, "E92.36.0.36", {"start": v(873.41, 6.59) * mm, "end": v(873.9, 7.07) * mm});
            skLineSegment(sketch, "E92.36.0.37", {"start": v(880.93, 9.9) * mm, "end": v(881.41, 9.41) * mm});
            skLineSegment(sketch, "E92.36.0.38", {"start": v(878.1, 7.07) * mm, "end": v(878.59, 6.59) * mm});
            skLineSegment(sketch, "E92.36.0.39", {"start": v(873.41, -6.59) * mm, "end": v(873.9, -7.07) * mm});
            skArc(sketch, "E92.37.0.0", {"start": v(894.59, 9.41) * mm, "mid": v(894.59, 6.59) * mm, "end": v(897.41, 6.59) * mm});
            skArc(sketch, "E92.37.0.1", {"start": v(897.41, -6.59) * mm, "mid": v(894.59, -6.59) * mm, "end": v(894.59, -9.41) * mm});
            skLineSegment(sketch, "E92.37.0.2", {"start": v(888, 24) * mm, "end": v(912, 24) * mm, "construction": true});
            skLineSegment(sketch, "E92.37.0.3", {"start": v(896, 16) * mm, "end": v(904, 16) * mm, "construction": true});
            skArc(sketch, "E92.37.0.4", {"start": v(895.07, -9.9) * mm, "mid": v(897.9, -9.9) * mm, "end": v(897.9, -7.07) * mm});
            skLineSegment(sketch, "E92.37.0.5", {"start": v(912, 0) * mm, "end": v(888, -24) * mm, "construction": true});
            skCircle(sketch, "E92.37.0.6", {"center": v(904, -16) * mm, "radius": 2 * mm});
            skLineSegment(sketch, "E92.37.0.7", {"start": v(912, -24) * mm, "end": v(888, -24) * mm, "construction": true});
            skCircle(sketch, "E92.37.0.8", {"center": v(896, 16) * mm, "radius": 2 * mm});
            skCircle(sketch, "E92.37.0.9", {"center": v(904, 16) * mm, "radius": 2 * mm});
            skLineSegment(sketch, "E92.37.0.10", {"start": v(912, -24) * mm, "end": v(888, 0) * mm, "construction": true});
            skLineSegment(sketch, "E92.37.0.11", {"start": v(888, 24) * mm, "end": v(912, 0) * mm, "construction": true});
            skLineSegment(sketch, "E92.37.0.12", {"start": v(912, 24) * mm, "end": v(888, 0) * mm, "construction": true});
            skArc(sketch, "E92.37.0.13", {"start": v(904.93, 9.9) * mm, "mid": v(902.1, 9.9) * mm, "end": v(902.1, 7.07) * mm});
            skArc(sketch, "E92.37.0.14", {"start": v(897.9, 7.07) * mm, "mid": v(897.9, 9.9) * mm, "end": v(895.07, 9.9) * mm});
            skArc(sketch, "E92.37.0.15", {"start": v(902.1, -7.07) * mm, "mid": v(902.1, -9.9) * mm, "end": v(904.93, -9.9) * mm});
            skArc(sketch, "E92.37.0.16", {"start": v(902.59, 6.59) * mm, "mid": v(905.41, 6.59) * mm, "end": v(905.41, 9.41) * mm});
            skLineSegment(sketch, "E92.37.0.17", {"start": v(896, -16) * mm, "end": v(904, -16) * mm, "construction": true});
            skLineSegment(sketch, "E92.37.0.18", {"start": v(888, 0) * mm, "end": v(912, 0) * mm, "construction": true});
            skArc(sketch, "E92.37.0.19", {"start": v(905.41, -9.41) * mm, "mid": v(905.41, -6.59) * mm, "end": v(902.59, -6.59) * mm});
            skCircle(sketch, "E92.37.0.20", {"center": v(896, -16) * mm, "radius": 2 * mm});
            skCircle(sketch, "E92.37.0.21", {"center": v(900, 0) * mm, "radius": 2 * mm});
            skPoint(sketch, "E92.37.0.22", {"position": v(896, -8) * mm});
            skLineSegment(sketch, "E92.37.0.23", {"start": v(912, 0) * mm, "end": v(888, 0) * mm, "construction": true});
            skLineSegment(sketch, "E92.37.0.24", {"start": v(902.59, 6.59) * mm, "end": v(905.41, 9.41) * mm, "construction": true});
            skLineSegment(sketch, "E92.37.0.25", {"start": v(902.1, -7.07) * mm, "end": v(904.93, -9.9) * mm, "construction": true});
            skLineSegment(sketch, "E92.37.0.26", {"start": v(894.59, 9.41) * mm, "end": v(897.41, 6.59) * mm, "construction": true});
            skLineSegment(sketch, "E92.37.0.27", {"start": v(895.07, 9.9) * mm, "end": v(897.9, 7.07) * mm, "construction": true});
            skLineSegment(sketch, "E92.37.0.28", {"start": v(904.93, 9.9) * mm, "end": v(902.1, 7.07) * mm, "construction": true});
            skLineSegment(sketch, "E92.37.0.29", {"start": v(902.59, -6.59) * mm, "end": v(905.41, -9.41) * mm, "construction": true});
            skLineSegment(sketch, "E92.37.0.30", {"start": v(895.07, -9.9) * mm, "end": v(897.9, -7.07) * mm, "construction": true});
            skLineSegment(sketch, "E92.37.0.31", {"start": v(897.41, -6.59) * mm, "end": v(894.59, -9.41) * mm, "construction": true});
            skLineSegment(sketch, "E92.37.0.32", {"start": v(902.1, -7.07) * mm, "end": v(902.59, -6.59) * mm});
            skLineSegment(sketch, "E92.37.0.33", {"start": v(894.59, 9.41) * mm, "end": v(895.07, 9.9) * mm});
            skLineSegment(sketch, "E92.37.0.34", {"start": v(894.59, -9.41) * mm, "end": v(895.07, -9.9) * mm});
            skLineSegment(sketch, "E92.37.0.35", {"start": v(904.93, -9.9) * mm, "end": v(905.41, -9.41) * mm});
            skLineSegment(sketch, "E92.37.0.36", {"start": v(897.41, 6.59) * mm, "end": v(897.9, 7.07) * mm});
            skLineSegment(sketch, "E92.37.0.37", {"start": v(904.93, 9.9) * mm, "end": v(905.41, 9.41) * mm});
            skLineSegment(sketch, "E92.37.0.38", {"start": v(902.1, 7.07) * mm, "end": v(902.59, 6.59) * mm});
            skLineSegment(sketch, "E92.37.0.39", {"start": v(897.41, -6.59) * mm, "end": v(897.9, -7.07) * mm});
            skArc(sketch, "E92.38.0.0", {"start": v(918.59, 9.41) * mm, "mid": v(918.59, 6.59) * mm, "end": v(921.41, 6.59) * mm});
            skArc(sketch, "E92.38.0.1", {"start": v(921.41, -6.59) * mm, "mid": v(918.59, -6.59) * mm, "end": v(918.59, -9.41) * mm});
            skLineSegment(sketch, "E92.38.0.2", {"start": v(912, 24) * mm, "end": v(936, 24) * mm, "construction": true});
            skLineSegment(sketch, "E92.38.0.3", {"start": v(920, 16) * mm, "end": v(928, 16) * mm, "construction": true});
            skArc(sketch, "E92.38.0.4", {"start": v(919.07, -9.9) * mm, "mid": v(921.9, -9.9) * mm, "end": v(921.9, -7.07) * mm});
            skLineSegment(sketch, "E92.38.0.5", {"start": v(936, 0) * mm, "end": v(912, -24) * mm, "construction": true});
            skCircle(sketch, "E92.38.0.6", {"center": v(928, -16) * mm, "radius": 2 * mm});
            skLineSegment(sketch, "E92.38.0.7", {"start": v(936, -24) * mm, "end": v(912, -24) * mm, "construction": true});
            skCircle(sketch, "E92.38.0.8", {"center": v(920, 16) * mm, "radius": 2 * mm});
            skCircle(sketch, "E92.38.0.9", {"center": v(928, 16) * mm, "radius": 2 * mm});
            skLineSegment(sketch, "E92.38.0.10", {"start": v(936, -24) * mm, "end": v(912, 0) * mm, "construction": true});
            skLineSegment(sketch, "E92.38.0.11", {"start": v(912, 24) * mm, "end": v(936, 0) * mm, "construction": true});
            skLineSegment(sketch, "E92.38.0.12", {"start": v(936, 24) * mm, "end": v(912, 0) * mm, "construction": true});
            skArc(sketch, "E92.38.0.13", {"start": v(928.93, 9.9) * mm, "mid": v(926.1, 9.9) * mm, "end": v(926.1, 7.07) * mm});
            skArc(sketch, "E92.38.0.14", {"start": v(921.9, 7.07) * mm, "mid": v(921.9, 9.9) * mm, "end": v(919.07, 9.9) * mm});
            skArc(sketch, "E92.38.0.15", {"start": v(926.1, -7.07) * mm, "mid": v(926.1, -9.9) * mm, "end": v(928.93, -9.9) * mm});
            skArc(sketch, "E92.38.0.16", {"start": v(926.59, 6.59) * mm, "mid": v(929.41, 6.59) * mm, "end": v(929.41, 9.41) * mm});
            skLineSegment(sketch, "E92.38.0.17", {"start": v(920, -16) * mm, "end": v(928, -16) * mm, "construction": true});
            skLineSegment(sketch, "E92.38.0.18", {"start": v(912, 0) * mm, "end": v(936, 0) * mm, "construction": true});
            skArc(sketch, "E92.38.0.19", {"start": v(929.41, -9.41) * mm, "mid": v(929.41, -6.59) * mm, "end": v(926.59, -6.59) * mm});
            skCircle(sketch, "E92.38.0.20", {"center": v(920, -16) * mm, "radius": 2 * mm});
            skCircle(sketch, "E92.38.0.21", {"center": v(924, 0) * mm, "radius": 2 * mm});
            skPoint(sketch, "E92.38.0.22", {"position": v(920, -8) * mm});
            skLineSegment(sketch, "E92.38.0.23", {"start": v(936, 0) * mm, "end": v(912, 0) * mm, "construction": true});
            skLineSegment(sketch, "E92.38.0.24", {"start": v(926.59, 6.59) * mm, "end": v(929.41, 9.41) * mm, "construction": true});
            skLineSegment(sketch, "E92.38.0.25", {"start": v(926.1, -7.07) * mm, "end": v(928.93, -9.9) * mm, "construction": true});
            skLineSegment(sketch, "E92.38.0.26", {"start": v(918.59, 9.41) * mm, "end": v(921.41, 6.59) * mm, "construction": true});
            skLineSegment(sketch, "E92.38.0.27", {"start": v(919.07, 9.9) * mm, "end": v(921.9, 7.07) * mm, "construction": true});
            skLineSegment(sketch, "E92.38.0.28", {"start": v(928.93, 9.9) * mm, "end": v(926.1, 7.07) * mm, "construction": true});
            skLineSegment(sketch, "E92.38.0.29", {"start": v(926.59, -6.59) * mm, "end": v(929.41, -9.41) * mm, "construction": true});
            skLineSegment(sketch, "E92.38.0.30", {"start": v(919.07, -9.9) * mm, "end": v(921.9, -7.07) * mm, "construction": true});
            skLineSegment(sketch, "E92.38.0.31", {"start": v(921.41, -6.59) * mm, "end": v(918.59, -9.41) * mm, "construction": true});
            skLineSegment(sketch, "E92.38.0.32", {"start": v(926.1, -7.07) * mm, "end": v(926.59, -6.59) * mm});
            skLineSegment(sketch, "E92.38.0.33", {"start": v(918.59, 9.41) * mm, "end": v(919.07, 9.9) * mm});
            skLineSegment(sketch, "E92.38.0.34", {"start": v(918.59, -9.41) * mm, "end": v(919.07, -9.9) * mm});
            skLineSegment(sketch, "E92.38.0.35", {"start": v(928.93, -9.9) * mm, "end": v(929.41, -9.41) * mm});
            skLineSegment(sketch, "E92.38.0.36", {"start": v(921.41, 6.59) * mm, "end": v(921.9, 7.07) * mm});
            skLineSegment(sketch, "E92.38.0.37", {"start": v(928.93, 9.9) * mm, "end": v(929.41, 9.41) * mm});
            skLineSegment(sketch, "E92.38.0.38", {"start": v(926.1, 7.07) * mm, "end": v(926.59, 6.59) * mm});
            skLineSegment(sketch, "E92.38.0.39", {"start": v(921.41, -6.59) * mm, "end": v(921.9, -7.07) * mm});
            skArc(sketch, "E92.39.0.0", {"start": v(942.59, 9.41) * mm, "mid": v(942.59, 6.59) * mm, "end": v(945.41, 6.59) * mm});
            skArc(sketch, "E92.39.0.1", {"start": v(945.41, -6.59) * mm, "mid": v(942.59, -6.59) * mm, "end": v(942.59, -9.41) * mm});
            skLineSegment(sketch, "E92.39.0.2", {"start": v(936, 24) * mm, "end": v(960, 24) * mm, "construction": true});
            skLineSegment(sketch, "E92.39.0.3", {"start": v(944, 16) * mm, "end": v(952, 16) * mm, "construction": true});
            skArc(sketch, "E92.39.0.4", {"start": v(943.07, -9.9) * mm, "mid": v(945.9, -9.9) * mm, "end": v(945.9, -7.07) * mm});
            skLineSegment(sketch, "E92.39.0.5", {"start": v(960, 0) * mm, "end": v(936, -24) * mm, "construction": true});
            skCircle(sketch, "E92.39.0.6", {"center": v(952, -16) * mm, "radius": 2 * mm});
            skLineSegment(sketch, "E92.39.0.7", {"start": v(960, -24) * mm, "end": v(936, -24) * mm, "construction": true});
            skCircle(sketch, "E92.39.0.8", {"center": v(944, 16) * mm, "radius": 2 * mm});
            skCircle(sketch, "E92.39.0.9", {"center": v(952, 16) * mm, "radius": 2 * mm});
            skLineSegment(sketch, "E92.39.0.10", {"start": v(960, -24) * mm, "end": v(936, 0) * mm, "construction": true});
            skLineSegment(sketch, "E92.39.0.11", {"start": v(936, 24) * mm, "end": v(960, 0) * mm, "construction": true});
            skLineSegment(sketch, "E92.39.0.12", {"start": v(960, 24) * mm, "end": v(936, 0) * mm, "construction": true});
            skArc(sketch, "E92.39.0.13", {"start": v(952.93, 9.9) * mm, "mid": v(950.1, 9.9) * mm, "end": v(950.1, 7.07) * mm});
            skArc(sketch, "E92.39.0.14", {"start": v(945.9, 7.07) * mm, "mid": v(945.9, 9.9) * mm, "end": v(943.07, 9.9) * mm});
            skArc(sketch, "E92.39.0.15", {"start": v(950.1, -7.07) * mm, "mid": v(950.1, -9.9) * mm, "end": v(952.93, -9.9) * mm});
            skArc(sketch, "E92.39.0.16", {"start": v(950.59, 6.59) * mm, "mid": v(953.41, 6.59) * mm, "end": v(953.41, 9.41) * mm});
            skLineSegment(sketch, "E92.39.0.17", {"start": v(944, -16) * mm, "end": v(952, -16) * mm, "construction": true});
            skLineSegment(sketch, "E92.39.0.18", {"start": v(936, 0) * mm, "end": v(960, 0) * mm, "construction": true});
            skArc(sketch, "E92.39.0.19", {"start": v(953.41, -9.41) * mm, "mid": v(953.41, -6.59) * mm, "end": v(950.59, -6.59) * mm});
            skCircle(sketch, "E92.39.0.20", {"center": v(944, -16) * mm, "radius": 2 * mm});
            skCircle(sketch, "E92.39.0.21", {"center": v(948, 0) * mm, "radius": 2 * mm});
            skPoint(sketch, "E92.39.0.22", {"position": v(944, -8) * mm});
            skLineSegment(sketch, "E92.39.0.23", {"start": v(960, 0) * mm, "end": v(936, 0) * mm, "construction": true});
            skLineSegment(sketch, "E92.39.0.24", {"start": v(950.59, 6.59) * mm, "end": v(953.41, 9.41) * mm, "construction": true});
            skLineSegment(sketch, "E92.39.0.25", {"start": v(950.1, -7.07) * mm, "end": v(952.93, -9.9) * mm, "construction": true});
            skLineSegment(sketch, "E92.39.0.26", {"start": v(942.59, 9.41) * mm, "end": v(945.41, 6.59) * mm, "construction": true});
            skLineSegment(sketch, "E92.39.0.27", {"start": v(943.07, 9.9) * mm, "end": v(945.9, 7.07) * mm, "construction": true});
            skLineSegment(sketch, "E92.39.0.28", {"start": v(952.93, 9.9) * mm, "end": v(950.1, 7.07) * mm, "construction": true});
            skLineSegment(sketch, "E92.39.0.29", {"start": v(950.59, -6.59) * mm, "end": v(953.41, -9.41) * mm, "construction": true});
            skLineSegment(sketch, "E92.39.0.30", {"start": v(943.07, -9.9) * mm, "end": v(945.9, -7.07) * mm, "construction": true});
            skLineSegment(sketch, "E92.39.0.31", {"start": v(945.41, -6.59) * mm, "end": v(942.59, -9.41) * mm, "construction": true});
            skLineSegment(sketch, "E92.39.0.32", {"start": v(950.1, -7.07) * mm, "end": v(950.59, -6.59) * mm});
            skLineSegment(sketch, "E92.39.0.33", {"start": v(942.59, 9.41) * mm, "end": v(943.07, 9.9) * mm});
            skLineSegment(sketch, "E92.39.0.34", {"start": v(942.59, -9.41) * mm, "end": v(943.07, -9.9) * mm});
            skLineSegment(sketch, "E92.39.0.35", {"start": v(952.93, -9.9) * mm, "end": v(953.41, -9.41) * mm});
            skLineSegment(sketch, "E92.39.0.36", {"start": v(945.41, 6.59) * mm, "end": v(945.9, 7.07) * mm});
            skLineSegment(sketch, "E92.39.0.37", {"start": v(952.93, 9.9) * mm, "end": v(953.41, 9.41) * mm});
            skLineSegment(sketch, "E92.39.0.38", {"start": v(950.1, 7.07) * mm, "end": v(950.59, 6.59) * mm});
            skLineSegment(sketch, "E92.39.0.39", {"start": v(945.41, -6.59) * mm, "end": v(945.9, -7.07) * mm});
            skArc(sketch, "E92.40.0.0", {"start": v(966.59, 9.41) * mm, "mid": v(966.59, 6.59) * mm, "end": v(969.41, 6.59) * mm});
            skArc(sketch, "E92.40.0.1", {"start": v(969.41, -6.59) * mm, "mid": v(966.59, -6.59) * mm, "end": v(966.59, -9.41) * mm});
            skLineSegment(sketch, "E92.40.0.2", {"start": v(960, 24) * mm, "end": v(984, 24) * mm, "construction": true});
            skLineSegment(sketch, "E92.40.0.3", {"start": v(968, 16) * mm, "end": v(976, 16) * mm, "construction": true});
            skArc(sketch, "E92.40.0.4", {"start": v(967.07, -9.9) * mm, "mid": v(969.9, -9.9) * mm, "end": v(969.9, -7.07) * mm});
            skLineSegment(sketch, "E92.40.0.5", {"start": v(984, 0) * mm, "end": v(960, -24) * mm, "construction": true});
            skCircle(sketch, "E92.40.0.6", {"center": v(976, -16) * mm, "radius": 2 * mm});
            skLineSegment(sketch, "E92.40.0.7", {"start": v(984, -24) * mm, "end": v(960, -24) * mm, "construction": true});
            skCircle(sketch, "E92.40.0.8", {"center": v(968, 16) * mm, "radius": 2 * mm});
            skCircle(sketch, "E92.40.0.9", {"center": v(976, 16) * mm, "radius": 2 * mm});
            skLineSegment(sketch, "E92.40.0.10", {"start": v(984, -24) * mm, "end": v(960, 0) * mm, "construction": true});
            skLineSegment(sketch, "E92.40.0.11", {"start": v(960, 24) * mm, "end": v(984, 0) * mm, "construction": true});
            skLineSegment(sketch, "E92.40.0.12", {"start": v(984, 24) * mm, "end": v(960, 0) * mm, "construction": true});
            skArc(sketch, "E92.40.0.13", {"start": v(976.93, 9.9) * mm, "mid": v(974.1, 9.9) * mm, "end": v(974.1, 7.07) * mm});
            skArc(sketch, "E92.40.0.14", {"start": v(969.9, 7.07) * mm, "mid": v(969.9, 9.9) * mm, "end": v(967.07, 9.9) * mm});
            skArc(sketch, "E92.40.0.15", {"start": v(974.1, -7.07) * mm, "mid": v(974.1, -9.9) * mm, "end": v(976.93, -9.9) * mm});
            skArc(sketch, "E92.40.0.16", {"start": v(974.59, 6.59) * mm, "mid": v(977.41, 6.59) * mm, "end": v(977.41, 9.41) * mm});
            skLineSegment(sketch, "E92.40.0.17", {"start": v(968, -16) * mm, "end": v(976, -16) * mm, "construction": true});
            skLineSegment(sketch, "E92.40.0.18", {"start": v(960, 0) * mm, "end": v(984, 0) * mm, "construction": true});
            skArc(sketch, "E92.40.0.19", {"start": v(977.41, -9.41) * mm, "mid": v(977.41, -6.59) * mm, "end": v(974.59, -6.59) * mm});
            skCircle(sketch, "E92.40.0.20", {"center": v(968, -16) * mm, "radius": 2 * mm});
            skCircle(sketch, "E92.40.0.21", {"center": v(972, 0) * mm, "radius": 2 * mm});
            skPoint(sketch, "E92.40.0.22", {"position": v(968, -8) * mm});
            skLineSegment(sketch, "E92.40.0.23", {"start": v(984, 0) * mm, "end": v(960, 0) * mm, "construction": true});
            skLineSegment(sketch, "E92.40.0.24", {"start": v(974.59, 6.59) * mm, "end": v(977.41, 9.41) * mm, "construction": true});
            skLineSegment(sketch, "E92.40.0.25", {"start": v(974.1, -7.07) * mm, "end": v(976.93, -9.9) * mm, "construction": true});
            skLineSegment(sketch, "E92.40.0.26", {"start": v(966.59, 9.41) * mm, "end": v(969.41, 6.59) * mm, "construction": true});
            skLineSegment(sketch, "E92.40.0.27", {"start": v(967.07, 9.9) * mm, "end": v(969.9, 7.07) * mm, "construction": true});
            skLineSegment(sketch, "E92.40.0.28", {"start": v(976.93, 9.9) * mm, "end": v(974.1, 7.07) * mm, "construction": true});
            skLineSegment(sketch, "E92.40.0.29", {"start": v(974.59, -6.59) * mm, "end": v(977.41, -9.41) * mm, "construction": true});
            skLineSegment(sketch, "E92.40.0.30", {"start": v(967.07, -9.9) * mm, "end": v(969.9, -7.07) * mm, "construction": true});
            skLineSegment(sketch, "E92.40.0.31", {"start": v(969.41, -6.59) * mm, "end": v(966.59, -9.41) * mm, "construction": true});
            skLineSegment(sketch, "E92.40.0.32", {"start": v(974.1, -7.07) * mm, "end": v(974.59, -6.59) * mm});
            skLineSegment(sketch, "E92.40.0.33", {"start": v(966.59, 9.41) * mm, "end": v(967.07, 9.9) * mm});
            skLineSegment(sketch, "E92.40.0.34", {"start": v(966.59, -9.41) * mm, "end": v(967.07, -9.9) * mm});
            skLineSegment(sketch, "E92.40.0.35", {"start": v(976.93, -9.9) * mm, "end": v(977.41, -9.41) * mm});
            skLineSegment(sketch, "E92.40.0.36", {"start": v(969.41, 6.59) * mm, "end": v(969.9, 7.07) * mm});
            skLineSegment(sketch, "E92.40.0.37", {"start": v(976.93, 9.9) * mm, "end": v(977.41, 9.41) * mm});
            skLineSegment(sketch, "E92.40.0.38", {"start": v(974.1, 7.07) * mm, "end": v(974.59, 6.59) * mm});
            skLineSegment(sketch, "E92.40.0.39", {"start": v(969.41, -6.59) * mm, "end": v(969.9, -7.07) * mm});
            skArc(sketch, "E92.41.0.0", {"start": v(990.59, 9.41) * mm, "mid": v(990.59, 6.59) * mm, "end": v(993.41, 6.59) * mm});
            skArc(sketch, "E92.41.0.1", {"start": v(993.41, -6.59) * mm, "mid": v(990.59, -6.59) * mm, "end": v(990.59, -9.41) * mm});
            skLineSegment(sketch, "E92.41.0.2", {"start": v(984, 24) * mm, "end": v(1008, 24) * mm, "construction": true});
            skLineSegment(sketch, "E92.41.0.3", {"start": v(992, 16) * mm, "end": v(1000, 16) * mm, "construction": true});
            skArc(sketch, "E92.41.0.4", {"start": v(991.07, -9.9) * mm, "mid": v(993.9, -9.9) * mm, "end": v(993.9, -7.07) * mm});
            skLineSegment(sketch, "E92.41.0.5", {"start": v(1008, 0) * mm, "end": v(984, -24) * mm, "construction": true});
            skCircle(sketch, "E92.41.0.6", {"center": v(1000, -16) * mm, "radius": 2 * mm});
            skLineSegment(sketch, "E92.41.0.7", {"start": v(1008, -24) * mm, "end": v(984, -24) * mm, "construction": true});
            skCircle(sketch, "E92.41.0.8", {"center": v(992, 16) * mm, "radius": 2 * mm});
            skCircle(sketch, "E92.41.0.9", {"center": v(1000, 16) * mm, "radius": 2 * mm});
            skLineSegment(sketch, "E92.41.0.10", {"start": v(1008, -24) * mm, "end": v(984, 0) * mm, "construction": true});
            skLineSegment(sketch, "E92.41.0.11", {"start": v(984, 24) * mm, "end": v(1008, 0) * mm, "construction": true});
            skLineSegment(sketch, "E92.41.0.12", {"start": v(1008, 24) * mm, "end": v(984, 0) * mm, "construction": true});
            skArc(sketch, "E92.41.0.13", {"start": v(1000.93, 9.9) * mm, "mid": v(998.1, 9.9) * mm, "end": v(998.1, 7.07) * mm});
            skArc(sketch, "E92.41.0.14", {"start": v(993.9, 7.07) * mm, "mid": v(993.9, 9.9) * mm, "end": v(991.07, 9.9) * mm});
            skArc(sketch, "E92.41.0.15", {"start": v(998.1, -7.07) * mm, "mid": v(998.1, -9.9) * mm, "end": v(1000.93, -9.9) * mm});
            skArc(sketch, "E92.41.0.16", {"start": v(998.59, 6.59) * mm, "mid": v(1001.41, 6.59) * mm, "end": v(1001.41, 9.41) * mm});
            skLineSegment(sketch, "E92.41.0.17", {"start": v(992, -16) * mm, "end": v(1000, -16) * mm, "construction": true});
            skLineSegment(sketch, "E92.41.0.18", {"start": v(984, 0) * mm, "end": v(1008, 0) * mm, "construction": true});
            skArc(sketch, "E92.41.0.19", {"start": v(1001.41, -9.41) * mm, "mid": v(1001.41, -6.59) * mm, "end": v(998.59, -6.59) * mm});
            skCircle(sketch, "E92.41.0.20", {"center": v(992, -16) * mm, "radius": 2 * mm});
            skCircle(sketch, "E92.41.0.21", {"center": v(996, 0) * mm, "radius": 2 * mm});
            skPoint(sketch, "E92.41.0.22", {"position": v(992, -8) * mm});
            skLineSegment(sketch, "E92.41.0.23", {"start": v(1008, 0) * mm, "end": v(984, 0) * mm, "construction": true});
            skLineSegment(sketch, "E92.41.0.24", {"start": v(998.59, 6.59) * mm, "end": v(1001.41, 9.41) * mm, "construction": true});
            skLineSegment(sketch, "E92.41.0.25", {"start": v(998.1, -7.07) * mm, "end": v(1000.93, -9.9) * mm, "construction": true});
            skLineSegment(sketch, "E92.41.0.26", {"start": v(990.59, 9.41) * mm, "end": v(993.41, 6.59) * mm, "construction": true});
            skLineSegment(sketch, "E92.41.0.27", {"start": v(991.07, 9.9) * mm, "end": v(993.9, 7.07) * mm, "construction": true});
            skLineSegment(sketch, "E92.41.0.28", {"start": v(1000.93, 9.9) * mm, "end": v(998.1, 7.07) * mm, "construction": true});
            skLineSegment(sketch, "E92.41.0.29", {"start": v(998.59, -6.59) * mm, "end": v(1001.41, -9.41) * mm, "construction": true});
            skLineSegment(sketch, "E92.41.0.30", {"start": v(991.07, -9.9) * mm, "end": v(993.9, -7.07) * mm, "construction": true});
            skLineSegment(sketch, "E92.41.0.31", {"start": v(993.41, -6.59) * mm, "end": v(990.59, -9.41) * mm, "construction": true});
            skLineSegment(sketch, "E92.41.0.32", {"start": v(998.1, -7.07) * mm, "end": v(998.59, -6.59) * mm});
            skLineSegment(sketch, "E92.41.0.33", {"start": v(990.59, 9.41) * mm, "end": v(991.07, 9.9) * mm});
            skLineSegment(sketch, "E92.41.0.34", {"start": v(990.59, -9.41) * mm, "end": v(991.07, -9.9) * mm});
            skLineSegment(sketch, "E92.41.0.35", {"start": v(1000.93, -9.9) * mm, "end": v(1001.41, -9.41) * mm});
            skLineSegment(sketch, "E92.41.0.36", {"start": v(993.41, 6.59) * mm, "end": v(993.9, 7.07) * mm});
            skLineSegment(sketch, "E92.41.0.37", {"start": v(1000.93, 9.9) * mm, "end": v(1001.41, 9.41) * mm});
            skLineSegment(sketch, "E92.41.0.38", {"start": v(998.1, 7.07) * mm, "end": v(998.59, 6.59) * mm});
            skLineSegment(sketch, "E92.41.0.39", {"start": v(993.41, -6.59) * mm, "end": v(993.9, -7.07) * mm});
            skArc(sketch, "E92.42.0.0", {"start": v(1014.59, 9.41) * mm, "mid": v(1014.59, 6.59) * mm, "end": v(1017.41, 6.59) * mm});
            skArc(sketch, "E92.42.0.1", {"start": v(1017.41, -6.59) * mm, "mid": v(1014.59, -6.59) * mm, "end": v(1014.59, -9.41) * mm});
            skLineSegment(sketch, "E92.42.0.2", {"start": v(1008, 24) * mm, "end": v(1032, 24) * mm, "construction": true});
            skLineSegment(sketch, "E92.42.0.3", {"start": v(1016, 16) * mm, "end": v(1024, 16) * mm, "construction": true});
            skArc(sketch, "E92.42.0.4", {"start": v(1015.07, -9.9) * mm, "mid": v(1017.9, -9.9) * mm, "end": v(1017.9, -7.07) * mm});
            skLineSegment(sketch, "E92.42.0.5", {"start": v(1032, 0) * mm, "end": v(1008, -24) * mm, "construction": true});
            skCircle(sketch, "E92.42.0.6", {"center": v(1024, -16) * mm, "radius": 2 * mm});
            skLineSegment(sketch, "E92.42.0.7", {"start": v(1032, -24) * mm, "end": v(1008, -24) * mm, "construction": true});
            skCircle(sketch, "E92.42.0.8", {"center": v(1016, 16) * mm, "radius": 2 * mm});
            skCircle(sketch, "E92.42.0.9", {"center": v(1024, 16) * mm, "radius": 2 * mm});
            skLineSegment(sketch, "E92.42.0.10", {"start": v(1032, -24) * mm, "end": v(1008, 0) * mm, "construction": true});
            skLineSegment(sketch, "E92.42.0.11", {"start": v(1008, 24) * mm, "end": v(1032, 0) * mm, "construction": true});
            skLineSegment(sketch, "E92.42.0.12", {"start": v(1032, 24) * mm, "end": v(1008, 0) * mm, "construction": true});
            skArc(sketch, "E92.42.0.13", {"start": v(1024.93, 9.9) * mm, "mid": v(1022.1, 9.9) * mm, "end": v(1022.1, 7.07) * mm});
            skArc(sketch, "E92.42.0.14", {"start": v(1017.9, 7.07) * mm, "mid": v(1017.9, 9.9) * mm, "end": v(1015.07, 9.9) * mm});
            skArc(sketch, "E92.42.0.15", {"start": v(1022.1, -7.07) * mm, "mid": v(1022.1, -9.9) * mm, "end": v(1024.93, -9.9) * mm});
            skArc(sketch, "E92.42.0.16", {"start": v(1022.59, 6.59) * mm, "mid": v(1025.41, 6.59) * mm, "end": v(1025.41, 9.41) * mm});
            skLineSegment(sketch, "E92.42.0.17", {"start": v(1016, -16) * mm, "end": v(1024, -16) * mm, "construction": true});
            skLineSegment(sketch, "E92.42.0.18", {"start": v(1008, 0) * mm, "end": v(1032, 0) * mm, "construction": true});
            skArc(sketch, "E92.42.0.19", {"start": v(1025.41, -9.41) * mm, "mid": v(1025.41, -6.59) * mm, "end": v(1022.59, -6.59) * mm});
            skCircle(sketch, "E92.42.0.20", {"center": v(1016, -16) * mm, "radius": 2 * mm});
            skCircle(sketch, "E92.42.0.21", {"center": v(1020, 0) * mm, "radius": 2 * mm});
            skPoint(sketch, "E92.42.0.22", {"position": v(1016, -8) * mm});
            skLineSegment(sketch, "E92.42.0.23", {"start": v(1032, 0) * mm, "end": v(1008, 0) * mm, "construction": true});
            skLineSegment(sketch, "E92.42.0.24", {"start": v(1022.59, 6.59) * mm, "end": v(1025.41, 9.41) * mm, "construction": true});
            skLineSegment(sketch, "E92.42.0.25", {"start": v(1022.1, -7.07) * mm, "end": v(1024.93, -9.9) * mm, "construction": true});
            skLineSegment(sketch, "E92.42.0.26", {"start": v(1014.59, 9.41) * mm, "end": v(1017.41, 6.59) * mm, "construction": true});
            skLineSegment(sketch, "E92.42.0.27", {"start": v(1015.07, 9.9) * mm, "end": v(1017.9, 7.07) * mm, "construction": true});
            skLineSegment(sketch, "E92.42.0.28", {"start": v(1024.93, 9.9) * mm, "end": v(1022.1, 7.07) * mm, "construction": true});
            skLineSegment(sketch, "E92.42.0.29", {"start": v(1022.59, -6.59) * mm, "end": v(1025.41, -9.41) * mm, "construction": true});
            skLineSegment(sketch, "E92.42.0.30", {"start": v(1015.07, -9.9) * mm, "end": v(1017.9, -7.07) * mm, "construction": true});
            skLineSegment(sketch, "E92.42.0.31", {"start": v(1017.41, -6.59) * mm, "end": v(1014.59, -9.41) * mm, "construction": true});
            skLineSegment(sketch, "E92.42.0.32", {"start": v(1022.1, -7.07) * mm, "end": v(1022.59, -6.59) * mm});
            skLineSegment(sketch, "E92.42.0.33", {"start": v(1014.59, 9.41) * mm, "end": v(1015.07, 9.9) * mm});
            skLineSegment(sketch, "E92.42.0.34", {"start": v(1014.59, -9.41) * mm, "end": v(1015.07, -9.9) * mm});
            skLineSegment(sketch, "E92.42.0.35", {"start": v(1024.93, -9.9) * mm, "end": v(1025.41, -9.41) * mm});
            skLineSegment(sketch, "E92.42.0.36", {"start": v(1017.41, 6.59) * mm, "end": v(1017.9, 7.07) * mm});
            skLineSegment(sketch, "E92.42.0.37", {"start": v(1024.93, 9.9) * mm, "end": v(1025.41, 9.41) * mm});
            skLineSegment(sketch, "E92.42.0.38", {"start": v(1022.1, 7.07) * mm, "end": v(1022.59, 6.59) * mm});
            skLineSegment(sketch, "E92.42.0.39", {"start": v(1017.41, -6.59) * mm, "end": v(1017.9, -7.07) * mm});
            skArc(sketch, "E92.43.0.0", {"start": v(1038.59, 9.41) * mm, "mid": v(1038.59, 6.59) * mm, "end": v(1041.41, 6.59) * mm});
            skArc(sketch, "E92.43.0.1", {"start": v(1041.41, -6.59) * mm, "mid": v(1038.59, -6.59) * mm, "end": v(1038.59, -9.41) * mm});
            skLineSegment(sketch, "E92.43.0.2", {"start": v(1032, 24) * mm, "end": v(1056, 24) * mm, "construction": true});
            skLineSegment(sketch, "E92.43.0.3", {"start": v(1040, 16) * mm, "end": v(1048, 16) * mm, "construction": true});
            skArc(sketch, "E92.43.0.4", {"start": v(1039.07, -9.9) * mm, "mid": v(1041.9, -9.9) * mm, "end": v(1041.9, -7.07) * mm});
            skLineSegment(sketch, "E92.43.0.5", {"start": v(1056, 0) * mm, "end": v(1032, -24) * mm, "construction": true});
            skCircle(sketch, "E92.43.0.6", {"center": v(1048, -16) * mm, "radius": 2 * mm});
            skLineSegment(sketch, "E92.43.0.7", {"start": v(1056, -24) * mm, "end": v(1032, -24) * mm, "construction": true});
            skCircle(sketch, "E92.43.0.8", {"center": v(1040, 16) * mm, "radius": 2 * mm});
            skCircle(sketch, "E92.43.0.9", {"center": v(1048, 16) * mm, "radius": 2 * mm});
            skLineSegment(sketch, "E92.43.0.10", {"start": v(1056, -24) * mm, "end": v(1032, 0) * mm, "construction": true});
            skLineSegment(sketch, "E92.43.0.11", {"start": v(1032, 24) * mm, "end": v(1056, 0) * mm, "construction": true});
            skLineSegment(sketch, "E92.43.0.12", {"start": v(1056, 24) * mm, "end": v(1032, 0) * mm, "construction": true});
            skArc(sketch, "E92.43.0.13", {"start": v(1048.93, 9.9) * mm, "mid": v(1046.1, 9.9) * mm, "end": v(1046.1, 7.07) * mm});
            skArc(sketch, "E92.43.0.14", {"start": v(1041.9, 7.07) * mm, "mid": v(1041.9, 9.9) * mm, "end": v(1039.07, 9.9) * mm});
            skArc(sketch, "E92.43.0.15", {"start": v(1046.1, -7.07) * mm, "mid": v(1046.1, -9.9) * mm, "end": v(1048.93, -9.9) * mm});
            skArc(sketch, "E92.43.0.16", {"start": v(1046.59, 6.59) * mm, "mid": v(1049.41, 6.59) * mm, "end": v(1049.41, 9.41) * mm});
            skLineSegment(sketch, "E92.43.0.17", {"start": v(1040, -16) * mm, "end": v(1048, -16) * mm, "construction": true});
            skLineSegment(sketch, "E92.43.0.18", {"start": v(1032, 0) * mm, "end": v(1056, 0) * mm, "construction": true});
            skArc(sketch, "E92.43.0.19", {"start": v(1049.41, -9.41) * mm, "mid": v(1049.41, -6.59) * mm, "end": v(1046.59, -6.59) * mm});
            skCircle(sketch, "E92.43.0.20", {"center": v(1040, -16) * mm, "radius": 2 * mm});
            skCircle(sketch, "E92.43.0.21", {"center": v(1044, 0) * mm, "radius": 2 * mm});
            skPoint(sketch, "E92.43.0.22", {"position": v(1040, -8) * mm});
            skLineSegment(sketch, "E92.43.0.23", {"start": v(1056, 0) * mm, "end": v(1032, 0) * mm, "construction": true});
            skLineSegment(sketch, "E92.43.0.24", {"start": v(1046.59, 6.59) * mm, "end": v(1049.41, 9.41) * mm, "construction": true});
            skLineSegment(sketch, "E92.43.0.25", {"start": v(1046.1, -7.07) * mm, "end": v(1048.93, -9.9) * mm, "construction": true});
            skLineSegment(sketch, "E92.43.0.26", {"start": v(1038.59, 9.41) * mm, "end": v(1041.41, 6.59) * mm, "construction": true});
            skLineSegment(sketch, "E92.43.0.27", {"start": v(1039.07, 9.9) * mm, "end": v(1041.9, 7.07) * mm, "construction": true});
            skLineSegment(sketch, "E92.43.0.28", {"start": v(1048.93, 9.9) * mm, "end": v(1046.1, 7.07) * mm, "construction": true});
            skLineSegment(sketch, "E92.43.0.29", {"start": v(1046.59, -6.59) * mm, "end": v(1049.41, -9.41) * mm, "construction": true});
            skLineSegment(sketch, "E92.43.0.30", {"start": v(1039.07, -9.9) * mm, "end": v(1041.9, -7.07) * mm, "construction": true});
            skLineSegment(sketch, "E92.43.0.31", {"start": v(1041.41, -6.59) * mm, "end": v(1038.59, -9.41) * mm, "construction": true});
            skLineSegment(sketch, "E92.43.0.32", {"start": v(1046.1, -7.07) * mm, "end": v(1046.59, -6.59) * mm});
            skLineSegment(sketch, "E92.43.0.33", {"start": v(1038.59, 9.41) * mm, "end": v(1039.07, 9.9) * mm});
            skLineSegment(sketch, "E92.43.0.34", {"start": v(1038.59, -9.41) * mm, "end": v(1039.07, -9.9) * mm});
            skLineSegment(sketch, "E92.43.0.35", {"start": v(1048.93, -9.9) * mm, "end": v(1049.41, -9.41) * mm});
            skLineSegment(sketch, "E92.43.0.36", {"start": v(1041.41, 6.59) * mm, "end": v(1041.9, 7.07) * mm});
            skLineSegment(sketch, "E92.43.0.37", {"start": v(1048.93, 9.9) * mm, "end": v(1049.41, 9.41) * mm});
            skLineSegment(sketch, "E92.43.0.38", {"start": v(1046.1, 7.07) * mm, "end": v(1046.59, 6.59) * mm});
            skLineSegment(sketch, "E92.43.0.39", {"start": v(1041.41, -6.59) * mm, "end": v(1041.9, -7.07) * mm});
            skArc(sketch, "E92.44.0.0", {"start": v(1062.59, 9.41) * mm, "mid": v(1062.59, 6.59) * mm, "end": v(1065.41, 6.59) * mm});
            skArc(sketch, "E92.44.0.1", {"start": v(1065.41, -6.59) * mm, "mid": v(1062.59, -6.59) * mm, "end": v(1062.59, -9.41) * mm});
            skLineSegment(sketch, "E92.44.0.2", {"start": v(1056, 24) * mm, "end": v(1080, 24) * mm, "construction": true});
            skLineSegment(sketch, "E92.44.0.3", {"start": v(1064, 16) * mm, "end": v(1072, 16) * mm, "construction": true});
            skArc(sketch, "E92.44.0.4", {"start": v(1063.07, -9.9) * mm, "mid": v(1065.9, -9.9) * mm, "end": v(1065.9, -7.07) * mm});
            skLineSegment(sketch, "E92.44.0.5", {"start": v(1080, 0) * mm, "end": v(1056, -24) * mm, "construction": true});
            skCircle(sketch, "E92.44.0.6", {"center": v(1072, -16) * mm, "radius": 2 * mm});
            skLineSegment(sketch, "E92.44.0.7", {"start": v(1080, -24) * mm, "end": v(1056, -24) * mm, "construction": true});
            skCircle(sketch, "E92.44.0.8", {"center": v(1064, 16) * mm, "radius": 2 * mm});
            skCircle(sketch, "E92.44.0.9", {"center": v(1072, 16) * mm, "radius": 2 * mm});
            skLineSegment(sketch, "E92.44.0.10", {"start": v(1080, -24) * mm, "end": v(1056, 0) * mm, "construction": true});
            skLineSegment(sketch, "E92.44.0.11", {"start": v(1056, 24) * mm, "end": v(1080, 0) * mm, "construction": true});
            skLineSegment(sketch, "E92.44.0.12", {"start": v(1080, 24) * mm, "end": v(1056, 0) * mm, "construction": true});
            skArc(sketch, "E92.44.0.13", {"start": v(1072.93, 9.9) * mm, "mid": v(1070.1, 9.9) * mm, "end": v(1070.1, 7.07) * mm});
            skArc(sketch, "E92.44.0.14", {"start": v(1065.9, 7.07) * mm, "mid": v(1065.9, 9.9) * mm, "end": v(1063.07, 9.9) * mm});
            skArc(sketch, "E92.44.0.15", {"start": v(1070.1, -7.07) * mm, "mid": v(1070.1, -9.9) * mm, "end": v(1072.93, -9.9) * mm});
            skArc(sketch, "E92.44.0.16", {"start": v(1070.59, 6.59) * mm, "mid": v(1073.41, 6.59) * mm, "end": v(1073.41, 9.41) * mm});
            skLineSegment(sketch, "E92.44.0.17", {"start": v(1064, -16) * mm, "end": v(1072, -16) * mm, "construction": true});
            skLineSegment(sketch, "E92.44.0.18", {"start": v(1056, 0) * mm, "end": v(1080, 0) * mm, "construction": true});
            skArc(sketch, "E92.44.0.19", {"start": v(1073.41, -9.41) * mm, "mid": v(1073.41, -6.59) * mm, "end": v(1070.59, -6.59) * mm});
            skCircle(sketch, "E92.44.0.20", {"center": v(1064, -16) * mm, "radius": 2 * mm});
            skCircle(sketch, "E92.44.0.21", {"center": v(1068, 0) * mm, "radius": 2 * mm});
            skPoint(sketch, "E92.44.0.22", {"position": v(1064, -8) * mm});
            skLineSegment(sketch, "E92.44.0.23", {"start": v(1080, 0) * mm, "end": v(1056, 0) * mm, "construction": true});
            skLineSegment(sketch, "E92.44.0.24", {"start": v(1070.59, 6.59) * mm, "end": v(1073.41, 9.41) * mm, "construction": true});
            skLineSegment(sketch, "E92.44.0.25", {"start": v(1070.1, -7.07) * mm, "end": v(1072.93, -9.9) * mm, "construction": true});
            skLineSegment(sketch, "E92.44.0.26", {"start": v(1062.59, 9.41) * mm, "end": v(1065.41, 6.59) * mm, "construction": true});
            skLineSegment(sketch, "E92.44.0.27", {"start": v(1063.07, 9.9) * mm, "end": v(1065.9, 7.07) * mm, "construction": true});
            skLineSegment(sketch, "E92.44.0.28", {"start": v(1072.93, 9.9) * mm, "end": v(1070.1, 7.07) * mm, "construction": true});
            skLineSegment(sketch, "E92.44.0.29", {"start": v(1070.59, -6.59) * mm, "end": v(1073.41, -9.41) * mm, "construction": true});
            skLineSegment(sketch, "E92.44.0.30", {"start": v(1063.07, -9.9) * mm, "end": v(1065.9, -7.07) * mm, "construction": true});
            skLineSegment(sketch, "E92.44.0.31", {"start": v(1065.41, -6.59) * mm, "end": v(1062.59, -9.41) * mm, "construction": true});
            skLineSegment(sketch, "E92.44.0.32", {"start": v(1070.1, -7.07) * mm, "end": v(1070.59, -6.59) * mm});
            skLineSegment(sketch, "E92.44.0.33", {"start": v(1062.59, 9.41) * mm, "end": v(1063.07, 9.9) * mm});
            skLineSegment(sketch, "E92.44.0.34", {"start": v(1062.59, -9.41) * mm, "end": v(1063.07, -9.9) * mm});
            skLineSegment(sketch, "E92.44.0.35", {"start": v(1072.93, -9.9) * mm, "end": v(1073.41, -9.41) * mm});
            skLineSegment(sketch, "E92.44.0.36", {"start": v(1065.41, 6.59) * mm, "end": v(1065.9, 7.07) * mm});
            skLineSegment(sketch, "E92.44.0.37", {"start": v(1072.93, 9.9) * mm, "end": v(1073.41, 9.41) * mm});
            skLineSegment(sketch, "E92.44.0.38", {"start": v(1070.1, 7.07) * mm, "end": v(1070.59, 6.59) * mm});
            skLineSegment(sketch, "E92.44.0.39", {"start": v(1065.41, -6.59) * mm, "end": v(1065.9, -7.07) * mm});
            skArc(sketch, "E92.45.0.0", {"start": v(1086.59, 9.41) * mm, "mid": v(1086.59, 6.59) * mm, "end": v(1089.41, 6.59) * mm});
            skArc(sketch, "E92.45.0.1", {"start": v(1089.41, -6.59) * mm, "mid": v(1086.59, -6.59) * mm, "end": v(1086.59, -9.41) * mm});
            skLineSegment(sketch, "E92.45.0.2", {"start": v(1080, 24) * mm, "end": v(1104, 24) * mm, "construction": true});
            skLineSegment(sketch, "E92.45.0.3", {"start": v(1088, 16) * mm, "end": v(1096, 16) * mm, "construction": true});
            skArc(sketch, "E92.45.0.4", {"start": v(1087.07, -9.9) * mm, "mid": v(1089.9, -9.9) * mm, "end": v(1089.9, -7.07) * mm});
            skLineSegment(sketch, "E92.45.0.5", {"start": v(1104, 0) * mm, "end": v(1080, -24) * mm, "construction": true});
            skCircle(sketch, "E92.45.0.6", {"center": v(1096, -16) * mm, "radius": 2 * mm});
            skLineSegment(sketch, "E92.45.0.7", {"start": v(1104, -24) * mm, "end": v(1080, -24) * mm, "construction": true});
            skCircle(sketch, "E92.45.0.8", {"center": v(1088, 16) * mm, "radius": 2 * mm});
            skCircle(sketch, "E92.45.0.9", {"center": v(1096, 16) * mm, "radius": 2 * mm});
            skLineSegment(sketch, "E92.45.0.10", {"start": v(1104, -24) * mm, "end": v(1080, 0) * mm, "construction": true});
            skLineSegment(sketch, "E92.45.0.11", {"start": v(1080, 24) * mm, "end": v(1104, 0) * mm, "construction": true});
            skLineSegment(sketch, "E92.45.0.12", {"start": v(1104, 24) * mm, "end": v(1080, 0) * mm, "construction": true});
            skArc(sketch, "E92.45.0.13", {"start": v(1096.93, 9.9) * mm, "mid": v(1094.1, 9.9) * mm, "end": v(1094.1, 7.07) * mm});
            skArc(sketch, "E92.45.0.14", {"start": v(1089.9, 7.07) * mm, "mid": v(1089.9, 9.9) * mm, "end": v(1087.07, 9.9) * mm});
            skArc(sketch, "E92.45.0.15", {"start": v(1094.1, -7.07) * mm, "mid": v(1094.1, -9.9) * mm, "end": v(1096.93, -9.9) * mm});
            skArc(sketch, "E92.45.0.16", {"start": v(1094.59, 6.59) * mm, "mid": v(1097.41, 6.59) * mm, "end": v(1097.41, 9.41) * mm});
            skLineSegment(sketch, "E92.45.0.17", {"start": v(1088, -16) * mm, "end": v(1096, -16) * mm, "construction": true});
            skLineSegment(sketch, "E92.45.0.18", {"start": v(1080, 0) * mm, "end": v(1104, 0) * mm, "construction": true});
            skArc(sketch, "E92.45.0.19", {"start": v(1097.41, -9.41) * mm, "mid": v(1097.41, -6.59) * mm, "end": v(1094.59, -6.59) * mm});
            skCircle(sketch, "E92.45.0.20", {"center": v(1088, -16) * mm, "radius": 2 * mm});
            skCircle(sketch, "E92.45.0.21", {"center": v(1092, 0) * mm, "radius": 2 * mm});
            skPoint(sketch, "E92.45.0.22", {"position": v(1088, -8) * mm});
            skLineSegment(sketch, "E92.45.0.23", {"start": v(1104, 0) * mm, "end": v(1080, 0) * mm, "construction": true});
            skLineSegment(sketch, "E92.45.0.24", {"start": v(1094.59, 6.59) * mm, "end": v(1097.41, 9.41) * mm, "construction": true});
            skLineSegment(sketch, "E92.45.0.25", {"start": v(1094.1, -7.07) * mm, "end": v(1096.93, -9.9) * mm, "construction": true});
            skLineSegment(sketch, "E92.45.0.26", {"start": v(1086.59, 9.41) * mm, "end": v(1089.41, 6.59) * mm, "construction": true});
            skLineSegment(sketch, "E92.45.0.27", {"start": v(1087.07, 9.9) * mm, "end": v(1089.9, 7.07) * mm, "construction": true});
            skLineSegment(sketch, "E92.45.0.28", {"start": v(1096.93, 9.9) * mm, "end": v(1094.1, 7.07) * mm, "construction": true});
            skLineSegment(sketch, "E92.45.0.29", {"start": v(1094.59, -6.59) * mm, "end": v(1097.41, -9.41) * mm, "construction": true});
            skLineSegment(sketch, "E92.45.0.30", {"start": v(1087.07, -9.9) * mm, "end": v(1089.9, -7.07) * mm, "construction": true});
            skLineSegment(sketch, "E92.45.0.31", {"start": v(1089.41, -6.59) * mm, "end": v(1086.59, -9.41) * mm, "construction": true});
            skLineSegment(sketch, "E92.45.0.32", {"start": v(1094.1, -7.07) * mm, "end": v(1094.59, -6.59) * mm});
            skLineSegment(sketch, "E92.45.0.33", {"start": v(1086.59, 9.41) * mm, "end": v(1087.07, 9.9) * mm});
            skLineSegment(sketch, "E92.45.0.34", {"start": v(1086.59, -9.41) * mm, "end": v(1087.07, -9.9) * mm});
            skLineSegment(sketch, "E92.45.0.35", {"start": v(1096.93, -9.9) * mm, "end": v(1097.41, -9.41) * mm});
            skLineSegment(sketch, "E92.45.0.36", {"start": v(1089.41, 6.59) * mm, "end": v(1089.9, 7.07) * mm});
            skLineSegment(sketch, "E92.45.0.37", {"start": v(1096.93, 9.9) * mm, "end": v(1097.41, 9.41) * mm});
            skLineSegment(sketch, "E92.45.0.38", {"start": v(1094.1, 7.07) * mm, "end": v(1094.59, 6.59) * mm});
            skLineSegment(sketch, "E92.45.0.39", {"start": v(1089.41, -6.59) * mm, "end": v(1089.9, -7.07) * mm});
            skArc(sketch, "E92.46.0.0", {"start": v(1110.59, 9.41) * mm, "mid": v(1110.59, 6.59) * mm, "end": v(1113.41, 6.59) * mm});
            skArc(sketch, "E92.46.0.1", {"start": v(1113.41, -6.59) * mm, "mid": v(1110.59, -6.59) * mm, "end": v(1110.59, -9.41) * mm});
            skLineSegment(sketch, "E92.46.0.2", {"start": v(1104, 24) * mm, "end": v(1128, 24) * mm, "construction": true});
            skLineSegment(sketch, "E92.46.0.3", {"start": v(1112, 16) * mm, "end": v(1120, 16) * mm, "construction": true});
            skArc(sketch, "E92.46.0.4", {"start": v(1111.07, -9.9) * mm, "mid": v(1113.9, -9.9) * mm, "end": v(1113.9, -7.07) * mm});
            skLineSegment(sketch, "E92.46.0.5", {"start": v(1128, 0) * mm, "end": v(1104, -24) * mm, "construction": true});
            skCircle(sketch, "E92.46.0.6", {"center": v(1120, -16) * mm, "radius": 2 * mm});
            skLineSegment(sketch, "E92.46.0.7", {"start": v(1128, -24) * mm, "end": v(1104, -24) * mm, "construction": true});
            skCircle(sketch, "E92.46.0.8", {"center": v(1112, 16) * mm, "radius": 2 * mm});
            skCircle(sketch, "E92.46.0.9", {"center": v(1120, 16) * mm, "radius": 2 * mm});
            skLineSegment(sketch, "E92.46.0.10", {"start": v(1128, -24) * mm, "end": v(1104, 0) * mm, "construction": true});
            skLineSegment(sketch, "E92.46.0.11", {"start": v(1104, 24) * mm, "end": v(1128, 0) * mm, "construction": true});
            skLineSegment(sketch, "E92.46.0.12", {"start": v(1128, 24) * mm, "end": v(1104, 0) * mm, "construction": true});
            skArc(sketch, "E92.46.0.13", {"start": v(1120.93, 9.9) * mm, "mid": v(1118.1, 9.9) * mm, "end": v(1118.1, 7.07) * mm});
            skArc(sketch, "E92.46.0.14", {"start": v(1113.9, 7.07) * mm, "mid": v(1113.9, 9.9) * mm, "end": v(1111.07, 9.9) * mm});
            skArc(sketch, "E92.46.0.15", {"start": v(1118.1, -7.07) * mm, "mid": v(1118.1, -9.9) * mm, "end": v(1120.93, -9.9) * mm});
            skArc(sketch, "E92.46.0.16", {"start": v(1118.59, 6.59) * mm, "mid": v(1121.41, 6.59) * mm, "end": v(1121.41, 9.41) * mm});
            skLineSegment(sketch, "E92.46.0.17", {"start": v(1112, -16) * mm, "end": v(1120, -16) * mm, "construction": true});
            skLineSegment(sketch, "E92.46.0.18", {"start": v(1104, 0) * mm, "end": v(1128, 0) * mm, "construction": true});
            skArc(sketch, "E92.46.0.19", {"start": v(1121.41, -9.41) * mm, "mid": v(1121.41, -6.59) * mm, "end": v(1118.59, -6.59) * mm});
            skCircle(sketch, "E92.46.0.20", {"center": v(1112, -16) * mm, "radius": 2 * mm});
            skCircle(sketch, "E92.46.0.21", {"center": v(1116, 0) * mm, "radius": 2 * mm});
            skPoint(sketch, "E92.46.0.22", {"position": v(1112, -8) * mm});
            skLineSegment(sketch, "E92.46.0.23", {"start": v(1128, 0) * mm, "end": v(1104, 0) * mm, "construction": true});
            skLineSegment(sketch, "E92.46.0.24", {"start": v(1118.59, 6.59) * mm, "end": v(1121.41, 9.41) * mm, "construction": true});
            skLineSegment(sketch, "E92.46.0.25", {"start": v(1118.1, -7.07) * mm, "end": v(1120.93, -9.9) * mm, "construction": true});
            skLineSegment(sketch, "E92.46.0.26", {"start": v(1110.59, 9.41) * mm, "end": v(1113.41, 6.59) * mm, "construction": true});
            skLineSegment(sketch, "E92.46.0.27", {"start": v(1111.07, 9.9) * mm, "end": v(1113.9, 7.07) * mm, "construction": true});
            skLineSegment(sketch, "E92.46.0.28", {"start": v(1120.93, 9.9) * mm, "end": v(1118.1, 7.07) * mm, "construction": true});
            skLineSegment(sketch, "E92.46.0.29", {"start": v(1118.59, -6.59) * mm, "end": v(1121.41, -9.41) * mm, "construction": true});
            skLineSegment(sketch, "E92.46.0.30", {"start": v(1111.07, -9.9) * mm, "end": v(1113.9, -7.07) * mm, "construction": true});
            skLineSegment(sketch, "E92.46.0.31", {"start": v(1113.41, -6.59) * mm, "end": v(1110.59, -9.41) * mm, "construction": true});
            skLineSegment(sketch, "E92.46.0.32", {"start": v(1118.1, -7.07) * mm, "end": v(1118.59, -6.59) * mm});
            skLineSegment(sketch, "E92.46.0.33", {"start": v(1110.59, 9.41) * mm, "end": v(1111.07, 9.9) * mm});
            skLineSegment(sketch, "E92.46.0.34", {"start": v(1110.59, -9.41) * mm, "end": v(1111.07, -9.9) * mm});
            skLineSegment(sketch, "E92.46.0.35", {"start": v(1120.93, -9.9) * mm, "end": v(1121.41, -9.41) * mm});
            skLineSegment(sketch, "E92.46.0.36", {"start": v(1113.41, 6.59) * mm, "end": v(1113.9, 7.07) * mm});
            skLineSegment(sketch, "E92.46.0.37", {"start": v(1120.93, 9.9) * mm, "end": v(1121.41, 9.41) * mm});
            skLineSegment(sketch, "E92.46.0.38", {"start": v(1118.1, 7.07) * mm, "end": v(1118.59, 6.59) * mm});
            skLineSegment(sketch, "E92.46.0.39", {"start": v(1113.41, -6.59) * mm, "end": v(1113.9, -7.07) * mm});
            skArc(sketch, "E92.47.0.0", {"start": v(1134.59, 9.41) * mm, "mid": v(1134.59, 6.59) * mm, "end": v(1137.41, 6.59) * mm});
            skArc(sketch, "E92.47.0.1", {"start": v(1137.41, -6.59) * mm, "mid": v(1134.59, -6.59) * mm, "end": v(1134.59, -9.41) * mm});
            skLineSegment(sketch, "E92.47.0.2", {"start": v(1128, 24) * mm, "end": v(1152, 24) * mm, "construction": true});
            skLineSegment(sketch, "E92.47.0.3", {"start": v(1136, 16) * mm, "end": v(1144, 16) * mm, "construction": true});
            skArc(sketch, "E92.47.0.4", {"start": v(1135.07, -9.9) * mm, "mid": v(1137.9, -9.9) * mm, "end": v(1137.9, -7.07) * mm});
            skLineSegment(sketch, "E92.47.0.5", {"start": v(1152, 0) * mm, "end": v(1128, -24) * mm, "construction": true});
            skCircle(sketch, "E92.47.0.6", {"center": v(1144, -16) * mm, "radius": 2 * mm});
            skLineSegment(sketch, "E92.47.0.7", {"start": v(1152, -24) * mm, "end": v(1128, -24) * mm, "construction": true});
            skCircle(sketch, "E92.47.0.8", {"center": v(1136, 16) * mm, "radius": 2 * mm});
            skCircle(sketch, "E92.47.0.9", {"center": v(1144, 16) * mm, "radius": 2 * mm});
            skLineSegment(sketch, "E92.47.0.10", {"start": v(1152, -24) * mm, "end": v(1128, 0) * mm, "construction": true});
            skLineSegment(sketch, "E92.47.0.11", {"start": v(1128, 24) * mm, "end": v(1152, 0) * mm, "construction": true});
            skLineSegment(sketch, "E92.47.0.12", {"start": v(1152, 24) * mm, "end": v(1128, 0) * mm, "construction": true});
            skArc(sketch, "E92.47.0.13", {"start": v(1144.93, 9.9) * mm, "mid": v(1142.1, 9.9) * mm, "end": v(1142.1, 7.07) * mm});
            skArc(sketch, "E92.47.0.14", {"start": v(1137.9, 7.07) * mm, "mid": v(1137.9, 9.9) * mm, "end": v(1135.07, 9.9) * mm});
            skArc(sketch, "E92.47.0.15", {"start": v(1142.1, -7.07) * mm, "mid": v(1142.1, -9.9) * mm, "end": v(1144.93, -9.9) * mm});
            skArc(sketch, "E92.47.0.16", {"start": v(1142.59, 6.59) * mm, "mid": v(1145.41, 6.59) * mm, "end": v(1145.41, 9.41) * mm});
            skLineSegment(sketch, "E92.47.0.17", {"start": v(1136, -16) * mm, "end": v(1144, -16) * mm, "construction": true});
            skLineSegment(sketch, "E92.47.0.18", {"start": v(1128, 0) * mm, "end": v(1152, 0) * mm, "construction": true});
            skArc(sketch, "E92.47.0.19", {"start": v(1145.41, -9.41) * mm, "mid": v(1145.41, -6.59) * mm, "end": v(1142.59, -6.59) * mm});
            skCircle(sketch, "E92.47.0.20", {"center": v(1136, -16) * mm, "radius": 2 * mm});
            skCircle(sketch, "E92.47.0.21", {"center": v(1140, 0) * mm, "radius": 2 * mm});
            skPoint(sketch, "E92.47.0.22", {"position": v(1136, -8) * mm});
            skLineSegment(sketch, "E92.47.0.23", {"start": v(1152, 0) * mm, "end": v(1128, 0) * mm, "construction": true});
            skLineSegment(sketch, "E92.47.0.24", {"start": v(1142.59, 6.59) * mm, "end": v(1145.41, 9.41) * mm, "construction": true});
            skLineSegment(sketch, "E92.47.0.25", {"start": v(1142.1, -7.07) * mm, "end": v(1144.93, -9.9) * mm, "construction": true});
            skLineSegment(sketch, "E92.47.0.26", {"start": v(1134.59, 9.41) * mm, "end": v(1137.41, 6.59) * mm, "construction": true});
            skLineSegment(sketch, "E92.47.0.27", {"start": v(1135.07, 9.9) * mm, "end": v(1137.9, 7.07) * mm, "construction": true});
            skLineSegment(sketch, "E92.47.0.28", {"start": v(1144.93, 9.9) * mm, "end": v(1142.1, 7.07) * mm, "construction": true});
            skLineSegment(sketch, "E92.47.0.29", {"start": v(1142.59, -6.59) * mm, "end": v(1145.41, -9.41) * mm, "construction": true});
            skLineSegment(sketch, "E92.47.0.30", {"start": v(1135.07, -9.9) * mm, "end": v(1137.9, -7.07) * mm, "construction": true});
            skLineSegment(sketch, "E92.47.0.31", {"start": v(1137.41, -6.59) * mm, "end": v(1134.59, -9.41) * mm, "construction": true});
            skLineSegment(sketch, "E92.47.0.32", {"start": v(1142.1, -7.07) * mm, "end": v(1142.59, -6.59) * mm});
            skLineSegment(sketch, "E92.47.0.33", {"start": v(1134.59, 9.41) * mm, "end": v(1135.07, 9.9) * mm});
            skLineSegment(sketch, "E92.47.0.34", {"start": v(1134.59, -9.41) * mm, "end": v(1135.07, -9.9) * mm});
            skLineSegment(sketch, "E92.47.0.35", {"start": v(1144.93, -9.9) * mm, "end": v(1145.41, -9.41) * mm});
            skLineSegment(sketch, "E92.47.0.36", {"start": v(1137.41, 6.59) * mm, "end": v(1137.9, 7.07) * mm});
            skLineSegment(sketch, "E92.47.0.37", {"start": v(1144.93, 9.9) * mm, "end": v(1145.41, 9.41) * mm});
            skLineSegment(sketch, "E92.47.0.38", {"start": v(1142.1, 7.07) * mm, "end": v(1142.59, 6.59) * mm});
            skLineSegment(sketch, "E92.47.0.39", {"start": v(1137.41, -6.59) * mm, "end": v(1137.9, -7.07) * mm});
            skArc(sketch, "E92.48.0.0", {"start": v(1158.59, 9.41) * mm, "mid": v(1158.59, 6.59) * mm, "end": v(1161.41, 6.59) * mm});
            skArc(sketch, "E92.48.0.1", {"start": v(1161.41, -6.59) * mm, "mid": v(1158.59, -6.59) * mm, "end": v(1158.59, -9.41) * mm});
            skLineSegment(sketch, "E92.48.0.2", {"start": v(1152, 24) * mm, "end": v(1176, 24) * mm, "construction": true});
            skLineSegment(sketch, "E92.48.0.3", {"start": v(1160, 16) * mm, "end": v(1168, 16) * mm, "construction": true});
            skArc(sketch, "E92.48.0.4", {"start": v(1159.07, -9.9) * mm, "mid": v(1161.9, -9.9) * mm, "end": v(1161.9, -7.07) * mm});
            skLineSegment(sketch, "E92.48.0.5", {"start": v(1176, 0) * mm, "end": v(1152, -24) * mm, "construction": true});
            skCircle(sketch, "E92.48.0.6", {"center": v(1168, -16) * mm, "radius": 2 * mm});
            skLineSegment(sketch, "E92.48.0.7", {"start": v(1176, -24) * mm, "end": v(1152, -24) * mm, "construction": true});
            skCircle(sketch, "E92.48.0.8", {"center": v(1160, 16) * mm, "radius": 2 * mm});
            skCircle(sketch, "E92.48.0.9", {"center": v(1168, 16) * mm, "radius": 2 * mm});
            skLineSegment(sketch, "E92.48.0.10", {"start": v(1176, -24) * mm, "end": v(1152, 0) * mm, "construction": true});
            skLineSegment(sketch, "E92.48.0.11", {"start": v(1152, 24) * mm, "end": v(1176, 0) * mm, "construction": true});
            skLineSegment(sketch, "E92.48.0.12", {"start": v(1176, 24) * mm, "end": v(1152, 0) * mm, "construction": true});
            skArc(sketch, "E92.48.0.13", {"start": v(1168.93, 9.9) * mm, "mid": v(1166.1, 9.9) * mm, "end": v(1166.1, 7.07) * mm});
            skArc(sketch, "E92.48.0.14", {"start": v(1161.9, 7.07) * mm, "mid": v(1161.9, 9.9) * mm, "end": v(1159.07, 9.9) * mm});
            skArc(sketch, "E92.48.0.15", {"start": v(1166.1, -7.07) * mm, "mid": v(1166.1, -9.9) * mm, "end": v(1168.93, -9.9) * mm});
            skArc(sketch, "E92.48.0.16", {"start": v(1166.59, 6.59) * mm, "mid": v(1169.41, 6.59) * mm, "end": v(1169.41, 9.41) * mm});
            skLineSegment(sketch, "E92.48.0.17", {"start": v(1160, -16) * mm, "end": v(1168, -16) * mm, "construction": true});
            skLineSegment(sketch, "E92.48.0.18", {"start": v(1152, 0) * mm, "end": v(1176, 0) * mm, "construction": true});
            skArc(sketch, "E92.48.0.19", {"start": v(1169.41, -9.41) * mm, "mid": v(1169.41, -6.59) * mm, "end": v(1166.59, -6.59) * mm});
            skCircle(sketch, "E92.48.0.20", {"center": v(1160, -16) * mm, "radius": 2 * mm});
            skCircle(sketch, "E92.48.0.21", {"center": v(1164, 0) * mm, "radius": 2 * mm});
            skPoint(sketch, "E92.48.0.22", {"position": v(1160, -8) * mm});
            skLineSegment(sketch, "E92.48.0.23", {"start": v(1176, 0) * mm, "end": v(1152, 0) * mm, "construction": true});
            skLineSegment(sketch, "E92.48.0.24", {"start": v(1166.59, 6.59) * mm, "end": v(1169.41, 9.41) * mm, "construction": true});
            skLineSegment(sketch, "E92.48.0.25", {"start": v(1166.1, -7.07) * mm, "end": v(1168.93, -9.9) * mm, "construction": true});
            skLineSegment(sketch, "E92.48.0.26", {"start": v(1158.59, 9.41) * mm, "end": v(1161.41, 6.59) * mm, "construction": true});
            skLineSegment(sketch, "E92.48.0.27", {"start": v(1159.07, 9.9) * mm, "end": v(1161.9, 7.07) * mm, "construction": true});
            skLineSegment(sketch, "E92.48.0.28", {"start": v(1168.93, 9.9) * mm, "end": v(1166.1, 7.07) * mm, "construction": true});
            skLineSegment(sketch, "E92.48.0.29", {"start": v(1166.59, -6.59) * mm, "end": v(1169.41, -9.41) * mm, "construction": true});
            skLineSegment(sketch, "E92.48.0.30", {"start": v(1159.07, -9.9) * mm, "end": v(1161.9, -7.07) * mm, "construction": true});
            skLineSegment(sketch, "E92.48.0.31", {"start": v(1161.41, -6.59) * mm, "end": v(1158.59, -9.41) * mm, "construction": true});
            skLineSegment(sketch, "E92.48.0.32", {"start": v(1166.1, -7.07) * mm, "end": v(1166.59, -6.59) * mm});
            skLineSegment(sketch, "E92.48.0.33", {"start": v(1158.59, 9.41) * mm, "end": v(1159.07, 9.9) * mm});
            skLineSegment(sketch, "E92.48.0.34", {"start": v(1158.59, -9.41) * mm, "end": v(1159.07, -9.9) * mm});
            skLineSegment(sketch, "E92.48.0.35", {"start": v(1168.93, -9.9) * mm, "end": v(1169.41, -9.41) * mm});
            skLineSegment(sketch, "E92.48.0.36", {"start": v(1161.41, 6.59) * mm, "end": v(1161.9, 7.07) * mm});
            skLineSegment(sketch, "E92.48.0.37", {"start": v(1168.93, 9.9) * mm, "end": v(1169.41, 9.41) * mm});
            skLineSegment(sketch, "E92.48.0.38", {"start": v(1166.1, 7.07) * mm, "end": v(1166.59, 6.59) * mm});
            skLineSegment(sketch, "E92.48.0.39", {"start": v(1161.41, -6.59) * mm, "end": v(1161.9, -7.07) * mm});
            skArc(sketch, "E92.49.0.0", {"start": v(1182.59, 9.41) * mm, "mid": v(1182.59, 6.59) * mm, "end": v(1185.41, 6.59) * mm});
            skArc(sketch, "E92.49.0.1", {"start": v(1185.41, -6.59) * mm, "mid": v(1182.59, -6.59) * mm, "end": v(1182.59, -9.41) * mm});
            skLineSegment(sketch, "E92.49.0.2", {"start": v(1176, 24) * mm, "end": v(1200, 24) * mm, "construction": true});
            skLineSegment(sketch, "E92.49.0.3", {"start": v(1184, 16) * mm, "end": v(1192, 16) * mm, "construction": true});
            skArc(sketch, "E92.49.0.4", {"start": v(1183.07, -9.9) * mm, "mid": v(1185.9, -9.9) * mm, "end": v(1185.9, -7.07) * mm});
            skLineSegment(sketch, "E92.49.0.5", {"start": v(1200, 0) * mm, "end": v(1176, -24) * mm, "construction": true});
            skCircle(sketch, "E92.49.0.6", {"center": v(1192, -16) * mm, "radius": 2 * mm});
            skLineSegment(sketch, "E92.49.0.7", {"start": v(1200, -24) * mm, "end": v(1176, -24) * mm, "construction": true});
            skCircle(sketch, "E92.49.0.8", {"center": v(1184, 16) * mm, "radius": 2 * mm});
            skCircle(sketch, "E92.49.0.9", {"center": v(1192, 16) * mm, "radius": 2 * mm});
            skLineSegment(sketch, "E92.49.0.10", {"start": v(1200, -24) * mm, "end": v(1176, 0) * mm, "construction": true});
            skLineSegment(sketch, "E92.49.0.11", {"start": v(1176, 24) * mm, "end": v(1200, 0) * mm, "construction": true});
            skLineSegment(sketch, "E92.49.0.12", {"start": v(1200, 24) * mm, "end": v(1176, 0) * mm, "construction": true});
            skArc(sketch, "E92.49.0.13", {"start": v(1192.93, 9.9) * mm, "mid": v(1190.1, 9.9) * mm, "end": v(1190.1, 7.07) * mm});
            skArc(sketch, "E92.49.0.14", {"start": v(1185.9, 7.07) * mm, "mid": v(1185.9, 9.9) * mm, "end": v(1183.07, 9.9) * mm});
            skArc(sketch, "E92.49.0.15", {"start": v(1190.1, -7.07) * mm, "mid": v(1190.1, -9.9) * mm, "end": v(1192.93, -9.9) * mm});
            skArc(sketch, "E92.49.0.16", {"start": v(1190.59, 6.59) * mm, "mid": v(1193.41, 6.59) * mm, "end": v(1193.41, 9.41) * mm});
            skLineSegment(sketch, "E92.49.0.17", {"start": v(1184, -16) * mm, "end": v(1192, -16) * mm, "construction": true});
            skLineSegment(sketch, "E92.49.0.18", {"start": v(1176, 0) * mm, "end": v(1200, 0) * mm, "construction": true});
            skArc(sketch, "E92.49.0.19", {"start": v(1193.41, -9.41) * mm, "mid": v(1193.41, -6.59) * mm, "end": v(1190.59, -6.59) * mm});
            skCircle(sketch, "E92.49.0.20", {"center": v(1184, -16) * mm, "radius": 2 * mm});
            skCircle(sketch, "E92.49.0.21", {"center": v(1188, 0) * mm, "radius": 2 * mm});
            skPoint(sketch, "E92.49.0.22", {"position": v(1184, -8) * mm});
            skLineSegment(sketch, "E92.49.0.23", {"start": v(1200, 0) * mm, "end": v(1176, 0) * mm, "construction": true});
            skLineSegment(sketch, "E92.49.0.24", {"start": v(1190.59, 6.59) * mm, "end": v(1193.41, 9.41) * mm, "construction": true});
            skLineSegment(sketch, "E92.49.0.25", {"start": v(1190.1, -7.07) * mm, "end": v(1192.93, -9.9) * mm, "construction": true});
            skLineSegment(sketch, "E92.49.0.26", {"start": v(1182.59, 9.41) * mm, "end": v(1185.41, 6.59) * mm, "construction": true});
            skLineSegment(sketch, "E92.49.0.27", {"start": v(1183.07, 9.9) * mm, "end": v(1185.9, 7.07) * mm, "construction": true});
            skLineSegment(sketch, "E92.49.0.28", {"start": v(1192.93, 9.9) * mm, "end": v(1190.1, 7.07) * mm, "construction": true});
            skLineSegment(sketch, "E92.49.0.29", {"start": v(1190.59, -6.59) * mm, "end": v(1193.41, -9.41) * mm, "construction": true});
            skLineSegment(sketch, "E92.49.0.30", {"start": v(1183.07, -9.9) * mm, "end": v(1185.9, -7.07) * mm, "construction": true});
            skLineSegment(sketch, "E92.49.0.31", {"start": v(1185.41, -6.59) * mm, "end": v(1182.59, -9.41) * mm, "construction": true});
            skLineSegment(sketch, "E92.49.0.32", {"start": v(1190.1, -7.07) * mm, "end": v(1190.59, -6.59) * mm});
            skLineSegment(sketch, "E92.49.0.33", {"start": v(1182.59, 9.41) * mm, "end": v(1183.07, 9.9) * mm});
            skLineSegment(sketch, "E92.49.0.34", {"start": v(1182.59, -9.41) * mm, "end": v(1183.07, -9.9) * mm});
            skLineSegment(sketch, "E92.49.0.35", {"start": v(1192.93, -9.9) * mm, "end": v(1193.41, -9.41) * mm});
            skLineSegment(sketch, "E92.49.0.36", {"start": v(1185.41, 6.59) * mm, "end": v(1185.9, 7.07) * mm});
            skLineSegment(sketch, "E92.49.0.37", {"start": v(1192.93, 9.9) * mm, "end": v(1193.41, 9.41) * mm});
            skLineSegment(sketch, "E92.49.0.38", {"start": v(1190.1, 7.07) * mm, "end": v(1190.59, 6.59) * mm});
            skLineSegment(sketch, "E92.49.0.39", {"start": v(1185.41, -6.59) * mm, "end": v(1185.9, -7.07) * mm});
            skLineSegment(sketch, "E92.direction1", {"start": v(0, -24) * mm, "end": v(24, -24) * mm, "construction": true});
            skSolve(sketch);
        }
        {
            var Q0;
            Q0=qSketchRegion(id+"F40",true);
            extrude(context, id + "F41", {"entities" : qUnion([Q0]), "operationType" : NewBodyOperationType.REMOVE, "oppositeDirection" : true, "depth" : 25 * mm, "offsetDistance" : 25 * mm});
        }
        {
            var Q0;
            Q0=qCreatedBy(makeId("Top.planeOp"),FACE);
            var sketch = newSketch(context, id + "F42", { "sketchPlane" : qUnion([Q0])});
            skCircle(sketch, "E93.0", {"center": v(16, 16) * mm, "radius": 2 * mm, "construction": true});
            skCircle(sketch, "E94.0", {"center": v(32, -16) * mm, "radius": 2 * mm, "construction": true});
            skLineSegment(sketch, "E95.bottom", {"start": v(16, 16) * mm, "end": v(32, 16) * mm, "construction": true});
            skLineSegment(sketch, "E95.top", {"start": v(16, -16) * mm, "end": v(32, -16) * mm, "construction": true});
            skLineSegment(sketch, "E95.left", {"start": v(16, 16) * mm, "end": v(16, -16) * mm, "construction": true});
            skLineSegment(sketch, "E95.right", {"start": v(32, 16) * mm, "end": v(32, -16) * mm, "construction": true});
            skLineSegment(sketch, "E96", {"start": v(24, 16) * mm, "end": v(24, -16) * mm, "construction": true});
            skCircle(sketch, "E97", {"center": v(24, 0) * mm, "radius": 7 * mm});
            skArc(sketch, "E98", {"start": v(26, 16) * mm, "mid": v(24, 18) * mm, "end": v(22, 16) * mm});
            skArc(sketch, "E99", {"start": v(22, -16) * mm, "mid": v(24, -18) * mm, "end": v(26, -16) * mm});
            skArc(sketch, "E100", {"start": v(22, 12) * mm, "mid": v(24, 10) * mm, "end": v(26, 12) * mm});
            skArc(sketch, "E101", {"start": v(26, -12) * mm, "mid": v(24, -10) * mm, "end": v(22, -12) * mm});
            skLineSegment(sketch, "E102", {"start": v(22, 16) * mm, "end": v(22, 12) * mm});
            skLineSegment(sketch, "E103", {"start": v(26, 16) * mm, "end": v(26, 12) * mm});
            skLineSegment(sketch, "E104", {"start": v(26, -16) * mm, "end": v(26, -12) * mm});
            skLineSegment(sketch, "E105", {"start": v(22, -16) * mm, "end": v(22, -12) * mm});
            skArc(sketch, "E106.1.0.0", {"start": v(50, -12) * mm, "mid": v(48, -10) * mm, "end": v(46, -12) * mm});
            skArc(sketch, "E106.1.0.1", {"start": v(46, 12) * mm, "mid": v(48, 10) * mm, "end": v(50, 12) * mm});
            skLineSegment(sketch, "E106.1.0.2", {"start": v(46, 16) * mm, "end": v(46, 12) * mm});
            skLineSegment(sketch, "E106.1.0.3", {"start": v(50, -16) * mm, "end": v(50, -12) * mm});
            skLineSegment(sketch, "E106.1.0.4", {"start": v(46, -16) * mm, "end": v(46, -12) * mm});
            skArc(sketch, "E106.1.0.5", {"start": v(46, -16) * mm, "mid": v(48, -18) * mm, "end": v(50, -16) * mm});
            skLineSegment(sketch, "E106.1.0.6", {"start": v(50, 16) * mm, "end": v(50, 12) * mm});
            skArc(sketch, "E106.1.0.7", {"start": v(50, 16) * mm, "mid": v(48, 18) * mm, "end": v(46, 16) * mm});
            skCircle(sketch, "E106.1.0.8", {"center": v(48, 0) * mm, "radius": 7 * mm});
            skArc(sketch, "E106.2.0.0", {"start": v(74, -12) * mm, "mid": v(72, -10) * mm, "end": v(70, -12) * mm});
            skArc(sketch, "E106.2.0.1", {"start": v(70, 12) * mm, "mid": v(72, 10) * mm, "end": v(74, 12) * mm});
            skLineSegment(sketch, "E106.2.0.2", {"start": v(70, 16) * mm, "end": v(70, 12) * mm});
            skLineSegment(sketch, "E106.2.0.3", {"start": v(74, -16) * mm, "end": v(74, -12) * mm});
            skLineSegment(sketch, "E106.2.0.4", {"start": v(70, -16) * mm, "end": v(70, -12) * mm});
            skArc(sketch, "E106.2.0.5", {"start": v(70, -16) * mm, "mid": v(72, -18) * mm, "end": v(74, -16) * mm});
            skLineSegment(sketch, "E106.2.0.6", {"start": v(74, 16) * mm, "end": v(74, 12) * mm});
            skArc(sketch, "E106.2.0.7", {"start": v(74, 16) * mm, "mid": v(72, 18) * mm, "end": v(70, 16) * mm});
            skCircle(sketch, "E106.2.0.8", {"center": v(72, 0) * mm, "radius": 7 * mm});
            skArc(sketch, "E106.3.0.0", {"start": v(98, -12) * mm, "mid": v(96, -10) * mm, "end": v(94, -12) * mm});
            skArc(sketch, "E106.3.0.1", {"start": v(94, 12) * mm, "mid": v(96, 10) * mm, "end": v(98, 12) * mm});
            skLineSegment(sketch, "E106.3.0.2", {"start": v(94, 16) * mm, "end": v(94, 12) * mm});
            skLineSegment(sketch, "E106.3.0.3", {"start": v(98, -16) * mm, "end": v(98, -12) * mm});
            skLineSegment(sketch, "E106.3.0.4", {"start": v(94, -16) * mm, "end": v(94, -12) * mm});
            skArc(sketch, "E106.3.0.5", {"start": v(94, -16) * mm, "mid": v(96, -18) * mm, "end": v(98, -16) * mm});
            skLineSegment(sketch, "E106.3.0.6", {"start": v(98, 16) * mm, "end": v(98, 12) * mm});
            skArc(sketch, "E106.3.0.7", {"start": v(98, 16) * mm, "mid": v(96, 18) * mm, "end": v(94, 16) * mm});
            skCircle(sketch, "E106.3.0.8", {"center": v(96, 0) * mm, "radius": 7 * mm});
            skArc(sketch, "E106.4.0.0", {"start": v(122, -12) * mm, "mid": v(120, -10) * mm, "end": v(118, -12) * mm});
            skArc(sketch, "E106.4.0.1", {"start": v(118, 12) * mm, "mid": v(120, 10) * mm, "end": v(122, 12) * mm});
            skLineSegment(sketch, "E106.4.0.2", {"start": v(118, 16) * mm, "end": v(118, 12) * mm});
            skLineSegment(sketch, "E106.4.0.3", {"start": v(122, -16) * mm, "end": v(122, -12) * mm});
            skLineSegment(sketch, "E106.4.0.4", {"start": v(118, -16) * mm, "end": v(118, -12) * mm});
            skArc(sketch, "E106.4.0.5", {"start": v(118, -16) * mm, "mid": v(120, -18) * mm, "end": v(122, -16) * mm});
            skLineSegment(sketch, "E106.4.0.6", {"start": v(122, 16) * mm, "end": v(122, 12) * mm});
            skArc(sketch, "E106.4.0.7", {"start": v(122, 16) * mm, "mid": v(120, 18) * mm, "end": v(118, 16) * mm});
            skCircle(sketch, "E106.4.0.8", {"center": v(120, 0) * mm, "radius": 7 * mm});
            skArc(sketch, "E106.5.0.0", {"start": v(146, -12) * mm, "mid": v(144, -10) * mm, "end": v(142, -12) * mm});
            skArc(sketch, "E106.5.0.1", {"start": v(142, 12) * mm, "mid": v(144, 10) * mm, "end": v(146, 12) * mm});
            skLineSegment(sketch, "E106.5.0.2", {"start": v(142, 16) * mm, "end": v(142, 12) * mm});
            skLineSegment(sketch, "E106.5.0.3", {"start": v(146, -16) * mm, "end": v(146, -12) * mm});
            skLineSegment(sketch, "E106.5.0.4", {"start": v(142, -16) * mm, "end": v(142, -12) * mm});
            skArc(sketch, "E106.5.0.5", {"start": v(142, -16) * mm, "mid": v(144, -18) * mm, "end": v(146, -16) * mm});
            skLineSegment(sketch, "E106.5.0.6", {"start": v(146, 16) * mm, "end": v(146, 12) * mm});
            skArc(sketch, "E106.5.0.7", {"start": v(146, 16) * mm, "mid": v(144, 18) * mm, "end": v(142, 16) * mm});
            skCircle(sketch, "E106.5.0.8", {"center": v(144, 0) * mm, "radius": 7 * mm});
            skArc(sketch, "E106.6.0.0", {"start": v(170, -12) * mm, "mid": v(168, -10) * mm, "end": v(166, -12) * mm});
            skArc(sketch, "E106.6.0.1", {"start": v(166, 12) * mm, "mid": v(168, 10) * mm, "end": v(170, 12) * mm});
            skLineSegment(sketch, "E106.6.0.2", {"start": v(166, 16) * mm, "end": v(166, 12) * mm});
            skLineSegment(sketch, "E106.6.0.3", {"start": v(170, -16) * mm, "end": v(170, -12) * mm});
            skLineSegment(sketch, "E106.6.0.4", {"start": v(166, -16) * mm, "end": v(166, -12) * mm});
            skArc(sketch, "E106.6.0.5", {"start": v(166, -16) * mm, "mid": v(168, -18) * mm, "end": v(170, -16) * mm});
            skLineSegment(sketch, "E106.6.0.6", {"start": v(170, 16) * mm, "end": v(170, 12) * mm});
            skArc(sketch, "E106.6.0.7", {"start": v(170, 16) * mm, "mid": v(168, 18) * mm, "end": v(166, 16) * mm});
            skCircle(sketch, "E106.6.0.8", {"center": v(168, 0) * mm, "radius": 7 * mm});
            skArc(sketch, "E106.7.0.0", {"start": v(194, -12) * mm, "mid": v(192, -10) * mm, "end": v(190, -12) * mm});
            skArc(sketch, "E106.7.0.1", {"start": v(190, 12) * mm, "mid": v(192, 10) * mm, "end": v(194, 12) * mm});
            skLineSegment(sketch, "E106.7.0.2", {"start": v(190, 16) * mm, "end": v(190, 12) * mm});
            skLineSegment(sketch, "E106.7.0.3", {"start": v(194, -16) * mm, "end": v(194, -12) * mm});
            skLineSegment(sketch, "E106.7.0.4", {"start": v(190, -16) * mm, "end": v(190, -12) * mm});
            skArc(sketch, "E106.7.0.5", {"start": v(190, -16) * mm, "mid": v(192, -18) * mm, "end": v(194, -16) * mm});
            skLineSegment(sketch, "E106.7.0.6", {"start": v(194, 16) * mm, "end": v(194, 12) * mm});
            skArc(sketch, "E106.7.0.7", {"start": v(194, 16) * mm, "mid": v(192, 18) * mm, "end": v(190, 16) * mm});
            skCircle(sketch, "E106.7.0.8", {"center": v(192, 0) * mm, "radius": 7 * mm});
            skArc(sketch, "E106.8.0.0", {"start": v(218, -12) * mm, "mid": v(216, -10) * mm, "end": v(214, -12) * mm});
            skArc(sketch, "E106.8.0.1", {"start": v(214, 12) * mm, "mid": v(216, 10) * mm, "end": v(218, 12) * mm});
            skLineSegment(sketch, "E106.8.0.2", {"start": v(214, 16) * mm, "end": v(214, 12) * mm});
            skLineSegment(sketch, "E106.8.0.3", {"start": v(218, -16) * mm, "end": v(218, -12) * mm});
            skLineSegment(sketch, "E106.8.0.4", {"start": v(214, -16) * mm, "end": v(214, -12) * mm});
            skArc(sketch, "E106.8.0.5", {"start": v(214, -16) * mm, "mid": v(216, -18) * mm, "end": v(218, -16) * mm});
            skLineSegment(sketch, "E106.8.0.6", {"start": v(218, 16) * mm, "end": v(218, 12) * mm});
            skArc(sketch, "E106.8.0.7", {"start": v(218, 16) * mm, "mid": v(216, 18) * mm, "end": v(214, 16) * mm});
            skCircle(sketch, "E106.8.0.8", {"center": v(216, 0) * mm, "radius": 7 * mm});
            skArc(sketch, "E106.9.0.0", {"start": v(242, -12) * mm, "mid": v(240, -10) * mm, "end": v(238, -12) * mm});
            skArc(sketch, "E106.9.0.1", {"start": v(238, 12) * mm, "mid": v(240, 10) * mm, "end": v(242, 12) * mm});
            skLineSegment(sketch, "E106.9.0.2", {"start": v(238, 16) * mm, "end": v(238, 12) * mm});
            skLineSegment(sketch, "E106.9.0.3", {"start": v(242, -16) * mm, "end": v(242, -12) * mm});
            skLineSegment(sketch, "E106.9.0.4", {"start": v(238, -16) * mm, "end": v(238, -12) * mm});
            skArc(sketch, "E106.9.0.5", {"start": v(238, -16) * mm, "mid": v(240, -18) * mm, "end": v(242, -16) * mm});
            skLineSegment(sketch, "E106.9.0.6", {"start": v(242, 16) * mm, "end": v(242, 12) * mm});
            skArc(sketch, "E106.9.0.7", {"start": v(242, 16) * mm, "mid": v(240, 18) * mm, "end": v(238, 16) * mm});
            skCircle(sketch, "E106.9.0.8", {"center": v(240, 0) * mm, "radius": 7 * mm});
            skArc(sketch, "E106.10.0.0", {"start": v(266, -12) * mm, "mid": v(264, -10) * mm, "end": v(262, -12) * mm});
            skArc(sketch, "E106.10.0.1", {"start": v(262, 12) * mm, "mid": v(264, 10) * mm, "end": v(266, 12) * mm});
            skLineSegment(sketch, "E106.10.0.2", {"start": v(262, 16) * mm, "end": v(262, 12) * mm});
            skLineSegment(sketch, "E106.10.0.3", {"start": v(266, -16) * mm, "end": v(266, -12) * mm});
            skLineSegment(sketch, "E106.10.0.4", {"start": v(262, -16) * mm, "end": v(262, -12) * mm});
            skArc(sketch, "E106.10.0.5", {"start": v(262, -16) * mm, "mid": v(264, -18) * mm, "end": v(266, -16) * mm});
            skLineSegment(sketch, "E106.10.0.6", {"start": v(266, 16) * mm, "end": v(266, 12) * mm});
            skArc(sketch, "E106.10.0.7", {"start": v(266, 16) * mm, "mid": v(264, 18) * mm, "end": v(262, 16) * mm});
            skCircle(sketch, "E106.10.0.8", {"center": v(264, 0) * mm, "radius": 7 * mm});
            skArc(sketch, "E106.11.0.0", {"start": v(290, -12) * mm, "mid": v(288, -10) * mm, "end": v(286, -12) * mm});
            skArc(sketch, "E106.11.0.1", {"start": v(286, 12) * mm, "mid": v(288, 10) * mm, "end": v(290, 12) * mm});
            skLineSegment(sketch, "E106.11.0.2", {"start": v(286, 16) * mm, "end": v(286, 12) * mm});
            skLineSegment(sketch, "E106.11.0.3", {"start": v(290, -16) * mm, "end": v(290, -12) * mm});
            skLineSegment(sketch, "E106.11.0.4", {"start": v(286, -16) * mm, "end": v(286, -12) * mm});
            skArc(sketch, "E106.11.0.5", {"start": v(286, -16) * mm, "mid": v(288, -18) * mm, "end": v(290, -16) * mm});
            skLineSegment(sketch, "E106.11.0.6", {"start": v(290, 16) * mm, "end": v(290, 12) * mm});
            skArc(sketch, "E106.11.0.7", {"start": v(290, 16) * mm, "mid": v(288, 18) * mm, "end": v(286, 16) * mm});
            skCircle(sketch, "E106.11.0.8", {"center": v(288, 0) * mm, "radius": 7 * mm});
            skArc(sketch, "E106.12.0.0", {"start": v(314, -12) * mm, "mid": v(312, -10) * mm, "end": v(310, -12) * mm});
            skArc(sketch, "E106.12.0.1", {"start": v(310, 12) * mm, "mid": v(312, 10) * mm, "end": v(314, 12) * mm});
            skLineSegment(sketch, "E106.12.0.2", {"start": v(310, 16) * mm, "end": v(310, 12) * mm});
            skLineSegment(sketch, "E106.12.0.3", {"start": v(314, -16) * mm, "end": v(314, -12) * mm});
            skLineSegment(sketch, "E106.12.0.4", {"start": v(310, -16) * mm, "end": v(310, -12) * mm});
            skArc(sketch, "E106.12.0.5", {"start": v(310, -16) * mm, "mid": v(312, -18) * mm, "end": v(314, -16) * mm});
            skLineSegment(sketch, "E106.12.0.6", {"start": v(314, 16) * mm, "end": v(314, 12) * mm});
            skArc(sketch, "E106.12.0.7", {"start": v(314, 16) * mm, "mid": v(312, 18) * mm, "end": v(310, 16) * mm});
            skCircle(sketch, "E106.12.0.8", {"center": v(312, 0) * mm, "radius": 7 * mm});
            skArc(sketch, "E106.13.0.0", {"start": v(338, -12) * mm, "mid": v(336, -10) * mm, "end": v(334, -12) * mm});
            skArc(sketch, "E106.13.0.1", {"start": v(334, 12) * mm, "mid": v(336, 10) * mm, "end": v(338, 12) * mm});
            skLineSegment(sketch, "E106.13.0.2", {"start": v(334, 16) * mm, "end": v(334, 12) * mm});
            skLineSegment(sketch, "E106.13.0.3", {"start": v(338, -16) * mm, "end": v(338, -12) * mm});
            skLineSegment(sketch, "E106.13.0.4", {"start": v(334, -16) * mm, "end": v(334, -12) * mm});
            skArc(sketch, "E106.13.0.5", {"start": v(334, -16) * mm, "mid": v(336, -18) * mm, "end": v(338, -16) * mm});
            skLineSegment(sketch, "E106.13.0.6", {"start": v(338, 16) * mm, "end": v(338, 12) * mm});
            skArc(sketch, "E106.13.0.7", {"start": v(338, 16) * mm, "mid": v(336, 18) * mm, "end": v(334, 16) * mm});
            skCircle(sketch, "E106.13.0.8", {"center": v(336, 0) * mm, "radius": 7 * mm});
            skArc(sketch, "E106.14.0.0", {"start": v(362, -12) * mm, "mid": v(360, -10) * mm, "end": v(358, -12) * mm});
            skArc(sketch, "E106.14.0.1", {"start": v(358, 12) * mm, "mid": v(360, 10) * mm, "end": v(362, 12) * mm});
            skLineSegment(sketch, "E106.14.0.2", {"start": v(358, 16) * mm, "end": v(358, 12) * mm});
            skLineSegment(sketch, "E106.14.0.3", {"start": v(362, -16) * mm, "end": v(362, -12) * mm});
            skLineSegment(sketch, "E106.14.0.4", {"start": v(358, -16) * mm, "end": v(358, -12) * mm});
            skArc(sketch, "E106.14.0.5", {"start": v(358, -16) * mm, "mid": v(360, -18) * mm, "end": v(362, -16) * mm});
            skLineSegment(sketch, "E106.14.0.6", {"start": v(362, 16) * mm, "end": v(362, 12) * mm});
            skArc(sketch, "E106.14.0.7", {"start": v(362, 16) * mm, "mid": v(360, 18) * mm, "end": v(358, 16) * mm});
            skCircle(sketch, "E106.14.0.8", {"center": v(360, 0) * mm, "radius": 7 * mm});
            skArc(sketch, "E106.15.0.0", {"start": v(386, -12) * mm, "mid": v(384, -10) * mm, "end": v(382, -12) * mm});
            skArc(sketch, "E106.15.0.1", {"start": v(382, 12) * mm, "mid": v(384, 10) * mm, "end": v(386, 12) * mm});
            skLineSegment(sketch, "E106.15.0.2", {"start": v(382, 16) * mm, "end": v(382, 12) * mm});
            skLineSegment(sketch, "E106.15.0.3", {"start": v(386, -16) * mm, "end": v(386, -12) * mm});
            skLineSegment(sketch, "E106.15.0.4", {"start": v(382, -16) * mm, "end": v(382, -12) * mm});
            skArc(sketch, "E106.15.0.5", {"start": v(382, -16) * mm, "mid": v(384, -18) * mm, "end": v(386, -16) * mm});
            skLineSegment(sketch, "E106.15.0.6", {"start": v(386, 16) * mm, "end": v(386, 12) * mm});
            skArc(sketch, "E106.15.0.7", {"start": v(386, 16) * mm, "mid": v(384, 18) * mm, "end": v(382, 16) * mm});
            skCircle(sketch, "E106.15.0.8", {"center": v(384, 0) * mm, "radius": 7 * mm});
            skArc(sketch, "E106.16.0.0", {"start": v(410, -12) * mm, "mid": v(408, -10) * mm, "end": v(406, -12) * mm});
            skArc(sketch, "E106.16.0.1", {"start": v(406, 12) * mm, "mid": v(408, 10) * mm, "end": v(410, 12) * mm});
            skLineSegment(sketch, "E106.16.0.2", {"start": v(406, 16) * mm, "end": v(406, 12) * mm});
            skLineSegment(sketch, "E106.16.0.3", {"start": v(410, -16) * mm, "end": v(410, -12) * mm});
            skLineSegment(sketch, "E106.16.0.4", {"start": v(406, -16) * mm, "end": v(406, -12) * mm});
            skArc(sketch, "E106.16.0.5", {"start": v(406, -16) * mm, "mid": v(408, -18) * mm, "end": v(410, -16) * mm});
            skLineSegment(sketch, "E106.16.0.6", {"start": v(410, 16) * mm, "end": v(410, 12) * mm});
            skArc(sketch, "E106.16.0.7", {"start": v(410, 16) * mm, "mid": v(408, 18) * mm, "end": v(406, 16) * mm});
            skCircle(sketch, "E106.16.0.8", {"center": v(408, 0) * mm, "radius": 7 * mm});
            skArc(sketch, "E106.17.0.0", {"start": v(434, -12) * mm, "mid": v(432, -10) * mm, "end": v(430, -12) * mm});
            skArc(sketch, "E106.17.0.1", {"start": v(430, 12) * mm, "mid": v(432, 10) * mm, "end": v(434, 12) * mm});
            skLineSegment(sketch, "E106.17.0.2", {"start": v(430, 16) * mm, "end": v(430, 12) * mm});
            skLineSegment(sketch, "E106.17.0.3", {"start": v(434, -16) * mm, "end": v(434, -12) * mm});
            skLineSegment(sketch, "E106.17.0.4", {"start": v(430, -16) * mm, "end": v(430, -12) * mm});
            skArc(sketch, "E106.17.0.5", {"start": v(430, -16) * mm, "mid": v(432, -18) * mm, "end": v(434, -16) * mm});
            skLineSegment(sketch, "E106.17.0.6", {"start": v(434, 16) * mm, "end": v(434, 12) * mm});
            skArc(sketch, "E106.17.0.7", {"start": v(434, 16) * mm, "mid": v(432, 18) * mm, "end": v(430, 16) * mm});
            skCircle(sketch, "E106.17.0.8", {"center": v(432, 0) * mm, "radius": 7 * mm});
            skArc(sketch, "E106.18.0.0", {"start": v(458, -12) * mm, "mid": v(456, -10) * mm, "end": v(454, -12) * mm});
            skArc(sketch, "E106.18.0.1", {"start": v(454, 12) * mm, "mid": v(456, 10) * mm, "end": v(458, 12) * mm});
            skLineSegment(sketch, "E106.18.0.2", {"start": v(454, 16) * mm, "end": v(454, 12) * mm});
            skLineSegment(sketch, "E106.18.0.3", {"start": v(458, -16) * mm, "end": v(458, -12) * mm});
            skLineSegment(sketch, "E106.18.0.4", {"start": v(454, -16) * mm, "end": v(454, -12) * mm});
            skArc(sketch, "E106.18.0.5", {"start": v(454, -16) * mm, "mid": v(456, -18) * mm, "end": v(458, -16) * mm});
            skLineSegment(sketch, "E106.18.0.6", {"start": v(458, 16) * mm, "end": v(458, 12) * mm});
            skArc(sketch, "E106.18.0.7", {"start": v(458, 16) * mm, "mid": v(456, 18) * mm, "end": v(454, 16) * mm});
            skCircle(sketch, "E106.18.0.8", {"center": v(456, 0) * mm, "radius": 7 * mm});
            skArc(sketch, "E106.19.0.0", {"start": v(482, -12) * mm, "mid": v(480, -10) * mm, "end": v(478, -12) * mm});
            skArc(sketch, "E106.19.0.1", {"start": v(478, 12) * mm, "mid": v(480, 10) * mm, "end": v(482, 12) * mm});
            skLineSegment(sketch, "E106.19.0.2", {"start": v(478, 16) * mm, "end": v(478, 12) * mm});
            skLineSegment(sketch, "E106.19.0.3", {"start": v(482, -16) * mm, "end": v(482, -12) * mm});
            skLineSegment(sketch, "E106.19.0.4", {"start": v(478, -16) * mm, "end": v(478, -12) * mm});
            skArc(sketch, "E106.19.0.5", {"start": v(478, -16) * mm, "mid": v(480, -18) * mm, "end": v(482, -16) * mm});
            skLineSegment(sketch, "E106.19.0.6", {"start": v(482, 16) * mm, "end": v(482, 12) * mm});
            skArc(sketch, "E106.19.0.7", {"start": v(482, 16) * mm, "mid": v(480, 18) * mm, "end": v(478, 16) * mm});
            skCircle(sketch, "E106.19.0.8", {"center": v(480, 0) * mm, "radius": 7 * mm});
            skArc(sketch, "E106.20.0.0", {"start": v(506, -12) * mm, "mid": v(504, -10) * mm, "end": v(502, -12) * mm});
            skArc(sketch, "E106.20.0.1", {"start": v(502, 12) * mm, "mid": v(504, 10) * mm, "end": v(506, 12) * mm});
            skLineSegment(sketch, "E106.20.0.2", {"start": v(502, 16) * mm, "end": v(502, 12) * mm});
            skLineSegment(sketch, "E106.20.0.3", {"start": v(506, -16) * mm, "end": v(506, -12) * mm});
            skLineSegment(sketch, "E106.20.0.4", {"start": v(502, -16) * mm, "end": v(502, -12) * mm});
            skArc(sketch, "E106.20.0.5", {"start": v(502, -16) * mm, "mid": v(504, -18) * mm, "end": v(506, -16) * mm});
            skLineSegment(sketch, "E106.20.0.6", {"start": v(506, 16) * mm, "end": v(506, 12) * mm});
            skArc(sketch, "E106.20.0.7", {"start": v(506, 16) * mm, "mid": v(504, 18) * mm, "end": v(502, 16) * mm});
            skCircle(sketch, "E106.20.0.8", {"center": v(504, 0) * mm, "radius": 7 * mm});
            skArc(sketch, "E106.21.0.0", {"start": v(530, -12) * mm, "mid": v(528, -10) * mm, "end": v(526, -12) * mm});
            skArc(sketch, "E106.21.0.1", {"start": v(526, 12) * mm, "mid": v(528, 10) * mm, "end": v(530, 12) * mm});
            skLineSegment(sketch, "E106.21.0.2", {"start": v(526, 16) * mm, "end": v(526, 12) * mm});
            skLineSegment(sketch, "E106.21.0.3", {"start": v(530, -16) * mm, "end": v(530, -12) * mm});
            skLineSegment(sketch, "E106.21.0.4", {"start": v(526, -16) * mm, "end": v(526, -12) * mm});
            skArc(sketch, "E106.21.0.5", {"start": v(526, -16) * mm, "mid": v(528, -18) * mm, "end": v(530, -16) * mm});
            skLineSegment(sketch, "E106.21.0.6", {"start": v(530, 16) * mm, "end": v(530, 12) * mm});
            skArc(sketch, "E106.21.0.7", {"start": v(530, 16) * mm, "mid": v(528, 18) * mm, "end": v(526, 16) * mm});
            skCircle(sketch, "E106.21.0.8", {"center": v(528, 0) * mm, "radius": 7 * mm});
            skArc(sketch, "E106.22.0.0", {"start": v(554, -12) * mm, "mid": v(552, -10) * mm, "end": v(550, -12) * mm});
            skArc(sketch, "E106.22.0.1", {"start": v(550, 12) * mm, "mid": v(552, 10) * mm, "end": v(554, 12) * mm});
            skLineSegment(sketch, "E106.22.0.2", {"start": v(550, 16) * mm, "end": v(550, 12) * mm});
            skLineSegment(sketch, "E106.22.0.3", {"start": v(554, -16) * mm, "end": v(554, -12) * mm});
            skLineSegment(sketch, "E106.22.0.4", {"start": v(550, -16) * mm, "end": v(550, -12) * mm});
            skArc(sketch, "E106.22.0.5", {"start": v(550, -16) * mm, "mid": v(552, -18) * mm, "end": v(554, -16) * mm});
            skLineSegment(sketch, "E106.22.0.6", {"start": v(554, 16) * mm, "end": v(554, 12) * mm});
            skArc(sketch, "E106.22.0.7", {"start": v(554, 16) * mm, "mid": v(552, 18) * mm, "end": v(550, 16) * mm});
            skCircle(sketch, "E106.22.0.8", {"center": v(552, 0) * mm, "radius": 7 * mm});
            skArc(sketch, "E106.23.0.0", {"start": v(578, -12) * mm, "mid": v(576, -10) * mm, "end": v(574, -12) * mm});
            skArc(sketch, "E106.23.0.1", {"start": v(574, 12) * mm, "mid": v(576, 10) * mm, "end": v(578, 12) * mm});
            skLineSegment(sketch, "E106.23.0.2", {"start": v(574, 16) * mm, "end": v(574, 12) * mm});
            skLineSegment(sketch, "E106.23.0.3", {"start": v(578, -16) * mm, "end": v(578, -12) * mm});
            skLineSegment(sketch, "E106.23.0.4", {"start": v(574, -16) * mm, "end": v(574, -12) * mm});
            skArc(sketch, "E106.23.0.5", {"start": v(574, -16) * mm, "mid": v(576, -18) * mm, "end": v(578, -16) * mm});
            skLineSegment(sketch, "E106.23.0.6", {"start": v(578, 16) * mm, "end": v(578, 12) * mm});
            skArc(sketch, "E106.23.0.7", {"start": v(578, 16) * mm, "mid": v(576, 18) * mm, "end": v(574, 16) * mm});
            skCircle(sketch, "E106.23.0.8", {"center": v(576, 0) * mm, "radius": 7 * mm});
            skArc(sketch, "E106.24.0.0", {"start": v(602, -12) * mm, "mid": v(600, -10) * mm, "end": v(598, -12) * mm});
            skArc(sketch, "E106.24.0.1", {"start": v(598, 12) * mm, "mid": v(600, 10) * mm, "end": v(602, 12) * mm});
            skLineSegment(sketch, "E106.24.0.2", {"start": v(598, 16) * mm, "end": v(598, 12) * mm});
            skLineSegment(sketch, "E106.24.0.3", {"start": v(602, -16) * mm, "end": v(602, -12) * mm});
            skLineSegment(sketch, "E106.24.0.4", {"start": v(598, -16) * mm, "end": v(598, -12) * mm});
            skArc(sketch, "E106.24.0.5", {"start": v(598, -16) * mm, "mid": v(600, -18) * mm, "end": v(602, -16) * mm});
            skLineSegment(sketch, "E106.24.0.6", {"start": v(602, 16) * mm, "end": v(602, 12) * mm});
            skArc(sketch, "E106.24.0.7", {"start": v(602, 16) * mm, "mid": v(600, 18) * mm, "end": v(598, 16) * mm});
            skCircle(sketch, "E106.24.0.8", {"center": v(600, 0) * mm, "radius": 7 * mm});
            skArc(sketch, "E106.25.0.0", {"start": v(626, -12) * mm, "mid": v(624, -10) * mm, "end": v(622, -12) * mm});
            skArc(sketch, "E106.25.0.1", {"start": v(622, 12) * mm, "mid": v(624, 10) * mm, "end": v(626, 12) * mm});
            skLineSegment(sketch, "E106.25.0.2", {"start": v(622, 16) * mm, "end": v(622, 12) * mm});
            skLineSegment(sketch, "E106.25.0.3", {"start": v(626, -16) * mm, "end": v(626, -12) * mm});
            skLineSegment(sketch, "E106.25.0.4", {"start": v(622, -16) * mm, "end": v(622, -12) * mm});
            skArc(sketch, "E106.25.0.5", {"start": v(622, -16) * mm, "mid": v(624, -18) * mm, "end": v(626, -16) * mm});
            skLineSegment(sketch, "E106.25.0.6", {"start": v(626, 16) * mm, "end": v(626, 12) * mm});
            skArc(sketch, "E106.25.0.7", {"start": v(626, 16) * mm, "mid": v(624, 18) * mm, "end": v(622, 16) * mm});
            skCircle(sketch, "E106.25.0.8", {"center": v(624, 0) * mm, "radius": 7 * mm});
            skArc(sketch, "E106.26.0.0", {"start": v(650, -12) * mm, "mid": v(648, -10) * mm, "end": v(646, -12) * mm});
            skArc(sketch, "E106.26.0.1", {"start": v(646, 12) * mm, "mid": v(648, 10) * mm, "end": v(650, 12) * mm});
            skLineSegment(sketch, "E106.26.0.2", {"start": v(646, 16) * mm, "end": v(646, 12) * mm});
            skLineSegment(sketch, "E106.26.0.3", {"start": v(650, -16) * mm, "end": v(650, -12) * mm});
            skLineSegment(sketch, "E106.26.0.4", {"start": v(646, -16) * mm, "end": v(646, -12) * mm});
            skArc(sketch, "E106.26.0.5", {"start": v(646, -16) * mm, "mid": v(648, -18) * mm, "end": v(650, -16) * mm});
            skLineSegment(sketch, "E106.26.0.6", {"start": v(650, 16) * mm, "end": v(650, 12) * mm});
            skArc(sketch, "E106.26.0.7", {"start": v(650, 16) * mm, "mid": v(648, 18) * mm, "end": v(646, 16) * mm});
            skCircle(sketch, "E106.26.0.8", {"center": v(648, 0) * mm, "radius": 7 * mm});
            skArc(sketch, "E106.27.0.0", {"start": v(674, -12) * mm, "mid": v(672, -10) * mm, "end": v(670, -12) * mm});
            skArc(sketch, "E106.27.0.1", {"start": v(670, 12) * mm, "mid": v(672, 10) * mm, "end": v(674, 12) * mm});
            skLineSegment(sketch, "E106.27.0.2", {"start": v(670, 16) * mm, "end": v(670, 12) * mm});
            skLineSegment(sketch, "E106.27.0.3", {"start": v(674, -16) * mm, "end": v(674, -12) * mm});
            skLineSegment(sketch, "E106.27.0.4", {"start": v(670, -16) * mm, "end": v(670, -12) * mm});
            skArc(sketch, "E106.27.0.5", {"start": v(670, -16) * mm, "mid": v(672, -18) * mm, "end": v(674, -16) * mm});
            skLineSegment(sketch, "E106.27.0.6", {"start": v(674, 16) * mm, "end": v(674, 12) * mm});
            skArc(sketch, "E106.27.0.7", {"start": v(674, 16) * mm, "mid": v(672, 18) * mm, "end": v(670, 16) * mm});
            skCircle(sketch, "E106.27.0.8", {"center": v(672, 0) * mm, "radius": 7 * mm});
            skArc(sketch, "E106.28.0.0", {"start": v(698, -12) * mm, "mid": v(696, -10) * mm, "end": v(694, -12) * mm});
            skArc(sketch, "E106.28.0.1", {"start": v(694, 12) * mm, "mid": v(696, 10) * mm, "end": v(698, 12) * mm});
            skLineSegment(sketch, "E106.28.0.2", {"start": v(694, 16) * mm, "end": v(694, 12) * mm});
            skLineSegment(sketch, "E106.28.0.3", {"start": v(698, -16) * mm, "end": v(698, -12) * mm});
            skLineSegment(sketch, "E106.28.0.4", {"start": v(694, -16) * mm, "end": v(694, -12) * mm});
            skArc(sketch, "E106.28.0.5", {"start": v(694, -16) * mm, "mid": v(696, -18) * mm, "end": v(698, -16) * mm});
            skLineSegment(sketch, "E106.28.0.6", {"start": v(698, 16) * mm, "end": v(698, 12) * mm});
            skArc(sketch, "E106.28.0.7", {"start": v(698, 16) * mm, "mid": v(696, 18) * mm, "end": v(694, 16) * mm});
            skCircle(sketch, "E106.28.0.8", {"center": v(696, 0) * mm, "radius": 7 * mm});
            skArc(sketch, "E106.29.0.0", {"start": v(722, -12) * mm, "mid": v(720, -10) * mm, "end": v(718, -12) * mm});
            skArc(sketch, "E106.29.0.1", {"start": v(718, 12) * mm, "mid": v(720, 10) * mm, "end": v(722, 12) * mm});
            skLineSegment(sketch, "E106.29.0.2", {"start": v(718, 16) * mm, "end": v(718, 12) * mm});
            skLineSegment(sketch, "E106.29.0.3", {"start": v(722, -16) * mm, "end": v(722, -12) * mm});
            skLineSegment(sketch, "E106.29.0.4", {"start": v(718, -16) * mm, "end": v(718, -12) * mm});
            skArc(sketch, "E106.29.0.5", {"start": v(718, -16) * mm, "mid": v(720, -18) * mm, "end": v(722, -16) * mm});
            skLineSegment(sketch, "E106.29.0.6", {"start": v(722, 16) * mm, "end": v(722, 12) * mm});
            skArc(sketch, "E106.29.0.7", {"start": v(722, 16) * mm, "mid": v(720, 18) * mm, "end": v(718, 16) * mm});
            skCircle(sketch, "E106.29.0.8", {"center": v(720, 0) * mm, "radius": 7 * mm});
            skArc(sketch, "E106.30.0.0", {"start": v(746, -12) * mm, "mid": v(744, -10) * mm, "end": v(742, -12) * mm});
            skArc(sketch, "E106.30.0.1", {"start": v(742, 12) * mm, "mid": v(744, 10) * mm, "end": v(746, 12) * mm});
            skLineSegment(sketch, "E106.30.0.2", {"start": v(742, 16) * mm, "end": v(742, 12) * mm});
            skLineSegment(sketch, "E106.30.0.3", {"start": v(746, -16) * mm, "end": v(746, -12) * mm});
            skLineSegment(sketch, "E106.30.0.4", {"start": v(742, -16) * mm, "end": v(742, -12) * mm});
            skArc(sketch, "E106.30.0.5", {"start": v(742, -16) * mm, "mid": v(744, -18) * mm, "end": v(746, -16) * mm});
            skLineSegment(sketch, "E106.30.0.6", {"start": v(746, 16) * mm, "end": v(746, 12) * mm});
            skArc(sketch, "E106.30.0.7", {"start": v(746, 16) * mm, "mid": v(744, 18) * mm, "end": v(742, 16) * mm});
            skCircle(sketch, "E106.30.0.8", {"center": v(744, 0) * mm, "radius": 7 * mm});
            skArc(sketch, "E106.31.0.0", {"start": v(770, -12) * mm, "mid": v(768, -10) * mm, "end": v(766, -12) * mm});
            skArc(sketch, "E106.31.0.1", {"start": v(766, 12) * mm, "mid": v(768, 10) * mm, "end": v(770, 12) * mm});
            skLineSegment(sketch, "E106.31.0.2", {"start": v(766, 16) * mm, "end": v(766, 12) * mm});
            skLineSegment(sketch, "E106.31.0.3", {"start": v(770, -16) * mm, "end": v(770, -12) * mm});
            skLineSegment(sketch, "E106.31.0.4", {"start": v(766, -16) * mm, "end": v(766, -12) * mm});
            skArc(sketch, "E106.31.0.5", {"start": v(766, -16) * mm, "mid": v(768, -18) * mm, "end": v(770, -16) * mm});
            skLineSegment(sketch, "E106.31.0.6", {"start": v(770, 16) * mm, "end": v(770, 12) * mm});
            skArc(sketch, "E106.31.0.7", {"start": v(770, 16) * mm, "mid": v(768, 18) * mm, "end": v(766, 16) * mm});
            skCircle(sketch, "E106.31.0.8", {"center": v(768, 0) * mm, "radius": 7 * mm});
            skArc(sketch, "E106.32.0.0", {"start": v(794, -12) * mm, "mid": v(792, -10) * mm, "end": v(790, -12) * mm});
            skArc(sketch, "E106.32.0.1", {"start": v(790, 12) * mm, "mid": v(792, 10) * mm, "end": v(794, 12) * mm});
            skLineSegment(sketch, "E106.32.0.2", {"start": v(790, 16) * mm, "end": v(790, 12) * mm});
            skLineSegment(sketch, "E106.32.0.3", {"start": v(794, -16) * mm, "end": v(794, -12) * mm});
            skLineSegment(sketch, "E106.32.0.4", {"start": v(790, -16) * mm, "end": v(790, -12) * mm});
            skArc(sketch, "E106.32.0.5", {"start": v(790, -16) * mm, "mid": v(792, -18) * mm, "end": v(794, -16) * mm});
            skLineSegment(sketch, "E106.32.0.6", {"start": v(794, 16) * mm, "end": v(794, 12) * mm});
            skArc(sketch, "E106.32.0.7", {"start": v(794, 16) * mm, "mid": v(792, 18) * mm, "end": v(790, 16) * mm});
            skCircle(sketch, "E106.32.0.8", {"center": v(792, 0) * mm, "radius": 7 * mm});
            skArc(sketch, "E106.33.0.0", {"start": v(818, -12) * mm, "mid": v(816, -10) * mm, "end": v(814, -12) * mm});
            skArc(sketch, "E106.33.0.1", {"start": v(814, 12) * mm, "mid": v(816, 10) * mm, "end": v(818, 12) * mm});
            skLineSegment(sketch, "E106.33.0.2", {"start": v(814, 16) * mm, "end": v(814, 12) * mm});
            skLineSegment(sketch, "E106.33.0.3", {"start": v(818, -16) * mm, "end": v(818, -12) * mm});
            skLineSegment(sketch, "E106.33.0.4", {"start": v(814, -16) * mm, "end": v(814, -12) * mm});
            skArc(sketch, "E106.33.0.5", {"start": v(814, -16) * mm, "mid": v(816, -18) * mm, "end": v(818, -16) * mm});
            skLineSegment(sketch, "E106.33.0.6", {"start": v(818, 16) * mm, "end": v(818, 12) * mm});
            skArc(sketch, "E106.33.0.7", {"start": v(818, 16) * mm, "mid": v(816, 18) * mm, "end": v(814, 16) * mm});
            skCircle(sketch, "E106.33.0.8", {"center": v(816, 0) * mm, "radius": 7 * mm});
            skArc(sketch, "E106.34.0.0", {"start": v(842, -12) * mm, "mid": v(840, -10) * mm, "end": v(838, -12) * mm});
            skArc(sketch, "E106.34.0.1", {"start": v(838, 12) * mm, "mid": v(840, 10) * mm, "end": v(842, 12) * mm});
            skLineSegment(sketch, "E106.34.0.2", {"start": v(838, 16) * mm, "end": v(838, 12) * mm});
            skLineSegment(sketch, "E106.34.0.3", {"start": v(842, -16) * mm, "end": v(842, -12) * mm});
            skLineSegment(sketch, "E106.34.0.4", {"start": v(838, -16) * mm, "end": v(838, -12) * mm});
            skArc(sketch, "E106.34.0.5", {"start": v(838, -16) * mm, "mid": v(840, -18) * mm, "end": v(842, -16) * mm});
            skLineSegment(sketch, "E106.34.0.6", {"start": v(842, 16) * mm, "end": v(842, 12) * mm});
            skArc(sketch, "E106.34.0.7", {"start": v(842, 16) * mm, "mid": v(840, 18) * mm, "end": v(838, 16) * mm});
            skCircle(sketch, "E106.34.0.8", {"center": v(840, 0) * mm, "radius": 7 * mm});
            skArc(sketch, "E106.35.0.0", {"start": v(866, -12) * mm, "mid": v(864, -10) * mm, "end": v(862, -12) * mm});
            skArc(sketch, "E106.35.0.1", {"start": v(862, 12) * mm, "mid": v(864, 10) * mm, "end": v(866, 12) * mm});
            skLineSegment(sketch, "E106.35.0.2", {"start": v(862, 16) * mm, "end": v(862, 12) * mm});
            skLineSegment(sketch, "E106.35.0.3", {"start": v(866, -16) * mm, "end": v(866, -12) * mm});
            skLineSegment(sketch, "E106.35.0.4", {"start": v(862, -16) * mm, "end": v(862, -12) * mm});
            skArc(sketch, "E106.35.0.5", {"start": v(862, -16) * mm, "mid": v(864, -18) * mm, "end": v(866, -16) * mm});
            skLineSegment(sketch, "E106.35.0.6", {"start": v(866, 16) * mm, "end": v(866, 12) * mm});
            skArc(sketch, "E106.35.0.7", {"start": v(866, 16) * mm, "mid": v(864, 18) * mm, "end": v(862, 16) * mm});
            skCircle(sketch, "E106.35.0.8", {"center": v(864, 0) * mm, "radius": 7 * mm});
            skArc(sketch, "E106.36.0.0", {"start": v(890, -12) * mm, "mid": v(888, -10) * mm, "end": v(886, -12) * mm});
            skArc(sketch, "E106.36.0.1", {"start": v(886, 12) * mm, "mid": v(888, 10) * mm, "end": v(890, 12) * mm});
            skLineSegment(sketch, "E106.36.0.2", {"start": v(886, 16) * mm, "end": v(886, 12) * mm});
            skLineSegment(sketch, "E106.36.0.3", {"start": v(890, -16) * mm, "end": v(890, -12) * mm});
            skLineSegment(sketch, "E106.36.0.4", {"start": v(886, -16) * mm, "end": v(886, -12) * mm});
            skArc(sketch, "E106.36.0.5", {"start": v(886, -16) * mm, "mid": v(888, -18) * mm, "end": v(890, -16) * mm});
            skLineSegment(sketch, "E106.36.0.6", {"start": v(890, 16) * mm, "end": v(890, 12) * mm});
            skArc(sketch, "E106.36.0.7", {"start": v(890, 16) * mm, "mid": v(888, 18) * mm, "end": v(886, 16) * mm});
            skCircle(sketch, "E106.36.0.8", {"center": v(888, 0) * mm, "radius": 7 * mm});
            skArc(sketch, "E106.37.0.0", {"start": v(914, -12) * mm, "mid": v(912, -10) * mm, "end": v(910, -12) * mm});
            skArc(sketch, "E106.37.0.1", {"start": v(910, 12) * mm, "mid": v(912, 10) * mm, "end": v(914, 12) * mm});
            skLineSegment(sketch, "E106.37.0.2", {"start": v(910, 16) * mm, "end": v(910, 12) * mm});
            skLineSegment(sketch, "E106.37.0.3", {"start": v(914, -16) * mm, "end": v(914, -12) * mm});
            skLineSegment(sketch, "E106.37.0.4", {"start": v(910, -16) * mm, "end": v(910, -12) * mm});
            skArc(sketch, "E106.37.0.5", {"start": v(910, -16) * mm, "mid": v(912, -18) * mm, "end": v(914, -16) * mm});
            skLineSegment(sketch, "E106.37.0.6", {"start": v(914, 16) * mm, "end": v(914, 12) * mm});
            skArc(sketch, "E106.37.0.7", {"start": v(914, 16) * mm, "mid": v(912, 18) * mm, "end": v(910, 16) * mm});
            skCircle(sketch, "E106.37.0.8", {"center": v(912, 0) * mm, "radius": 7 * mm});
            skArc(sketch, "E106.38.0.0", {"start": v(938, -12) * mm, "mid": v(936, -10) * mm, "end": v(934, -12) * mm});
            skArc(sketch, "E106.38.0.1", {"start": v(934, 12) * mm, "mid": v(936, 10) * mm, "end": v(938, 12) * mm});
            skLineSegment(sketch, "E106.38.0.2", {"start": v(934, 16) * mm, "end": v(934, 12) * mm});
            skLineSegment(sketch, "E106.38.0.3", {"start": v(938, -16) * mm, "end": v(938, -12) * mm});
            skLineSegment(sketch, "E106.38.0.4", {"start": v(934, -16) * mm, "end": v(934, -12) * mm});
            skArc(sketch, "E106.38.0.5", {"start": v(934, -16) * mm, "mid": v(936, -18) * mm, "end": v(938, -16) * mm});
            skLineSegment(sketch, "E106.38.0.6", {"start": v(938, 16) * mm, "end": v(938, 12) * mm});
            skArc(sketch, "E106.38.0.7", {"start": v(938, 16) * mm, "mid": v(936, 18) * mm, "end": v(934, 16) * mm});
            skCircle(sketch, "E106.38.0.8", {"center": v(936, 0) * mm, "radius": 7 * mm});
            skArc(sketch, "E106.39.0.0", {"start": v(962, -12) * mm, "mid": v(960, -10) * mm, "end": v(958, -12) * mm});
            skArc(sketch, "E106.39.0.1", {"start": v(958, 12) * mm, "mid": v(960, 10) * mm, "end": v(962, 12) * mm});
            skLineSegment(sketch, "E106.39.0.2", {"start": v(958, 16) * mm, "end": v(958, 12) * mm});
            skLineSegment(sketch, "E106.39.0.3", {"start": v(962, -16) * mm, "end": v(962, -12) * mm});
            skLineSegment(sketch, "E106.39.0.4", {"start": v(958, -16) * mm, "end": v(958, -12) * mm});
            skArc(sketch, "E106.39.0.5", {"start": v(958, -16) * mm, "mid": v(960, -18) * mm, "end": v(962, -16) * mm});
            skLineSegment(sketch, "E106.39.0.6", {"start": v(962, 16) * mm, "end": v(962, 12) * mm});
            skArc(sketch, "E106.39.0.7", {"start": v(962, 16) * mm, "mid": v(960, 18) * mm, "end": v(958, 16) * mm});
            skCircle(sketch, "E106.39.0.8", {"center": v(960, 0) * mm, "radius": 7 * mm});
            skArc(sketch, "E106.40.0.0", {"start": v(986, -12) * mm, "mid": v(984, -10) * mm, "end": v(982, -12) * mm});
            skArc(sketch, "E106.40.0.1", {"start": v(982, 12) * mm, "mid": v(984, 10) * mm, "end": v(986, 12) * mm});
            skLineSegment(sketch, "E106.40.0.2", {"start": v(982, 16) * mm, "end": v(982, 12) * mm});
            skLineSegment(sketch, "E106.40.0.3", {"start": v(986, -16) * mm, "end": v(986, -12) * mm});
            skLineSegment(sketch, "E106.40.0.4", {"start": v(982, -16) * mm, "end": v(982, -12) * mm});
            skArc(sketch, "E106.40.0.5", {"start": v(982, -16) * mm, "mid": v(984, -18) * mm, "end": v(986, -16) * mm});
            skLineSegment(sketch, "E106.40.0.6", {"start": v(986, 16) * mm, "end": v(986, 12) * mm});
            skArc(sketch, "E106.40.0.7", {"start": v(986, 16) * mm, "mid": v(984, 18) * mm, "end": v(982, 16) * mm});
            skCircle(sketch, "E106.40.0.8", {"center": v(984, 0) * mm, "radius": 7 * mm});
            skArc(sketch, "E106.41.0.0", {"start": v(1010, -12) * mm, "mid": v(1008, -10) * mm, "end": v(1006, -12) * mm});
            skArc(sketch, "E106.41.0.1", {"start": v(1006, 12) * mm, "mid": v(1008, 10) * mm, "end": v(1010, 12) * mm});
            skLineSegment(sketch, "E106.41.0.2", {"start": v(1006, 16) * mm, "end": v(1006, 12) * mm});
            skLineSegment(sketch, "E106.41.0.3", {"start": v(1010, -16) * mm, "end": v(1010, -12) * mm});
            skLineSegment(sketch, "E106.41.0.4", {"start": v(1006, -16) * mm, "end": v(1006, -12) * mm});
            skArc(sketch, "E106.41.0.5", {"start": v(1006, -16) * mm, "mid": v(1008, -18) * mm, "end": v(1010, -16) * mm});
            skLineSegment(sketch, "E106.41.0.6", {"start": v(1010, 16) * mm, "end": v(1010, 12) * mm});
            skArc(sketch, "E106.41.0.7", {"start": v(1010, 16) * mm, "mid": v(1008, 18) * mm, "end": v(1006, 16) * mm});
            skCircle(sketch, "E106.41.0.8", {"center": v(1008, 0) * mm, "radius": 7 * mm});
            skArc(sketch, "E106.42.0.0", {"start": v(1034, -12) * mm, "mid": v(1032, -10) * mm, "end": v(1030, -12) * mm});
            skArc(sketch, "E106.42.0.1", {"start": v(1030, 12) * mm, "mid": v(1032, 10) * mm, "end": v(1034, 12) * mm});
            skLineSegment(sketch, "E106.42.0.2", {"start": v(1030, 16) * mm, "end": v(1030, 12) * mm});
            skLineSegment(sketch, "E106.42.0.3", {"start": v(1034, -16) * mm, "end": v(1034, -12) * mm});
            skLineSegment(sketch, "E106.42.0.4", {"start": v(1030, -16) * mm, "end": v(1030, -12) * mm});
            skArc(sketch, "E106.42.0.5", {"start": v(1030, -16) * mm, "mid": v(1032, -18) * mm, "end": v(1034, -16) * mm});
            skLineSegment(sketch, "E106.42.0.6", {"start": v(1034, 16) * mm, "end": v(1034, 12) * mm});
            skArc(sketch, "E106.42.0.7", {"start": v(1034, 16) * mm, "mid": v(1032, 18) * mm, "end": v(1030, 16) * mm});
            skCircle(sketch, "E106.42.0.8", {"center": v(1032, 0) * mm, "radius": 7 * mm});
            skArc(sketch, "E106.43.0.0", {"start": v(1058, -12) * mm, "mid": v(1056, -10) * mm, "end": v(1054, -12) * mm});
            skArc(sketch, "E106.43.0.1", {"start": v(1054, 12) * mm, "mid": v(1056, 10) * mm, "end": v(1058, 12) * mm});
            skLineSegment(sketch, "E106.43.0.2", {"start": v(1054, 16) * mm, "end": v(1054, 12) * mm});
            skLineSegment(sketch, "E106.43.0.3", {"start": v(1058, -16) * mm, "end": v(1058, -12) * mm});
            skLineSegment(sketch, "E106.43.0.4", {"start": v(1054, -16) * mm, "end": v(1054, -12) * mm});
            skArc(sketch, "E106.43.0.5", {"start": v(1054, -16) * mm, "mid": v(1056, -18) * mm, "end": v(1058, -16) * mm});
            skLineSegment(sketch, "E106.43.0.6", {"start": v(1058, 16) * mm, "end": v(1058, 12) * mm});
            skArc(sketch, "E106.43.0.7", {"start": v(1058, 16) * mm, "mid": v(1056, 18) * mm, "end": v(1054, 16) * mm});
            skCircle(sketch, "E106.43.0.8", {"center": v(1056, 0) * mm, "radius": 7 * mm});
            skArc(sketch, "E106.44.0.0", {"start": v(1082, -12) * mm, "mid": v(1080, -10) * mm, "end": v(1078, -12) * mm});
            skArc(sketch, "E106.44.0.1", {"start": v(1078, 12) * mm, "mid": v(1080, 10) * mm, "end": v(1082, 12) * mm});
            skLineSegment(sketch, "E106.44.0.2", {"start": v(1078, 16) * mm, "end": v(1078, 12) * mm});
            skLineSegment(sketch, "E106.44.0.3", {"start": v(1082, -16) * mm, "end": v(1082, -12) * mm});
            skLineSegment(sketch, "E106.44.0.4", {"start": v(1078, -16) * mm, "end": v(1078, -12) * mm});
            skArc(sketch, "E106.44.0.5", {"start": v(1078, -16) * mm, "mid": v(1080, -18) * mm, "end": v(1082, -16) * mm});
            skLineSegment(sketch, "E106.44.0.6", {"start": v(1082, 16) * mm, "end": v(1082, 12) * mm});
            skArc(sketch, "E106.44.0.7", {"start": v(1082, 16) * mm, "mid": v(1080, 18) * mm, "end": v(1078, 16) * mm});
            skCircle(sketch, "E106.44.0.8", {"center": v(1080, 0) * mm, "radius": 7 * mm});
            skArc(sketch, "E106.45.0.0", {"start": v(1106, -12) * mm, "mid": v(1104, -10) * mm, "end": v(1102, -12) * mm});
            skArc(sketch, "E106.45.0.1", {"start": v(1102, 12) * mm, "mid": v(1104, 10) * mm, "end": v(1106, 12) * mm});
            skLineSegment(sketch, "E106.45.0.2", {"start": v(1102, 16) * mm, "end": v(1102, 12) * mm});
            skLineSegment(sketch, "E106.45.0.3", {"start": v(1106, -16) * mm, "end": v(1106, -12) * mm});
            skLineSegment(sketch, "E106.45.0.4", {"start": v(1102, -16) * mm, "end": v(1102, -12) * mm});
            skArc(sketch, "E106.45.0.5", {"start": v(1102, -16) * mm, "mid": v(1104, -18) * mm, "end": v(1106, -16) * mm});
            skLineSegment(sketch, "E106.45.0.6", {"start": v(1106, 16) * mm, "end": v(1106, 12) * mm});
            skArc(sketch, "E106.45.0.7", {"start": v(1106, 16) * mm, "mid": v(1104, 18) * mm, "end": v(1102, 16) * mm});
            skCircle(sketch, "E106.45.0.8", {"center": v(1104, 0) * mm, "radius": 7 * mm});
            skArc(sketch, "E106.46.0.0", {"start": v(1130, -12) * mm, "mid": v(1128, -10) * mm, "end": v(1126, -12) * mm});
            skArc(sketch, "E106.46.0.1", {"start": v(1126, 12) * mm, "mid": v(1128, 10) * mm, "end": v(1130, 12) * mm});
            skLineSegment(sketch, "E106.46.0.2", {"start": v(1126, 16) * mm, "end": v(1126, 12) * mm});
            skLineSegment(sketch, "E106.46.0.3", {"start": v(1130, -16) * mm, "end": v(1130, -12) * mm});
            skLineSegment(sketch, "E106.46.0.4", {"start": v(1126, -16) * mm, "end": v(1126, -12) * mm});
            skArc(sketch, "E106.46.0.5", {"start": v(1126, -16) * mm, "mid": v(1128, -18) * mm, "end": v(1130, -16) * mm});
            skLineSegment(sketch, "E106.46.0.6", {"start": v(1130, 16) * mm, "end": v(1130, 12) * mm});
            skArc(sketch, "E106.46.0.7", {"start": v(1130, 16) * mm, "mid": v(1128, 18) * mm, "end": v(1126, 16) * mm});
            skCircle(sketch, "E106.46.0.8", {"center": v(1128, 0) * mm, "radius": 7 * mm});
            skArc(sketch, "E106.47.0.0", {"start": v(1154, -12) * mm, "mid": v(1152, -10) * mm, "end": v(1150, -12) * mm});
            skArc(sketch, "E106.47.0.1", {"start": v(1150, 12) * mm, "mid": v(1152, 10) * mm, "end": v(1154, 12) * mm});
            skLineSegment(sketch, "E106.47.0.2", {"start": v(1150, 16) * mm, "end": v(1150, 12) * mm});
            skLineSegment(sketch, "E106.47.0.3", {"start": v(1154, -16) * mm, "end": v(1154, -12) * mm});
            skLineSegment(sketch, "E106.47.0.4", {"start": v(1150, -16) * mm, "end": v(1150, -12) * mm});
            skArc(sketch, "E106.47.0.5", {"start": v(1150, -16) * mm, "mid": v(1152, -18) * mm, "end": v(1154, -16) * mm});
            skLineSegment(sketch, "E106.47.0.6", {"start": v(1154, 16) * mm, "end": v(1154, 12) * mm});
            skArc(sketch, "E106.47.0.7", {"start": v(1154, 16) * mm, "mid": v(1152, 18) * mm, "end": v(1150, 16) * mm});
            skCircle(sketch, "E106.47.0.8", {"center": v(1152, 0) * mm, "radius": 7 * mm});
            skArc(sketch, "E106.48.0.0", {"start": v(1178, -12) * mm, "mid": v(1176, -10) * mm, "end": v(1174, -12) * mm});
            skArc(sketch, "E106.48.0.1", {"start": v(1174, 12) * mm, "mid": v(1176, 10) * mm, "end": v(1178, 12) * mm});
            skLineSegment(sketch, "E106.48.0.2", {"start": v(1174, 16) * mm, "end": v(1174, 12) * mm});
            skLineSegment(sketch, "E106.48.0.3", {"start": v(1178, -16) * mm, "end": v(1178, -12) * mm});
            skLineSegment(sketch, "E106.48.0.4", {"start": v(1174, -16) * mm, "end": v(1174, -12) * mm});
            skArc(sketch, "E106.48.0.5", {"start": v(1174, -16) * mm, "mid": v(1176, -18) * mm, "end": v(1178, -16) * mm});
            skLineSegment(sketch, "E106.48.0.6", {"start": v(1178, 16) * mm, "end": v(1178, 12) * mm});
            skArc(sketch, "E106.48.0.7", {"start": v(1178, 16) * mm, "mid": v(1176, 18) * mm, "end": v(1174, 16) * mm});
            skCircle(sketch, "E106.48.0.8", {"center": v(1176, 0) * mm, "radius": 7 * mm});
            skLineSegment(sketch, "E106.direction1", {"start": v(22, -16) * mm, "end": v(46, -16) * mm, "construction": true});
            skSolve(sketch);
        }
        {
            var Q0;
            Q0=makeQuery(id+"F42.imprint","IMPRINT",FACE,{"disambiguationData":[TD([[makeQuery(id+"F42.imprint","IMPRINT",EDGE,{"derivedFrom":sQuery(id+"F42.wireOp",EDGE,"E97")}),1.0]])]});
            var Q1;
            Q1=makeQuery(id+"F42.imprint","IMPRINT",FACE,{"disambiguationData":[TD([[makeQuery(id+"F42.imprint","IMPRINT",EDGE,{"derivedFrom":sQuery(id+"F42.wireOp",EDGE,"E98")}),1.0]])]});
            var Q2;
            Q2=makeQuery(id+"F42.imprint","IMPRINT",FACE,{"disambiguationData":[TD([[makeQuery(id+"F42.imprint","IMPRINT",EDGE,{"derivedFrom":sQuery(id+"F42.wireOp",EDGE,"E99")}),1.0]])]});
            extrude(context, id + "F43", {"entities" : qUnion([Q0, Q1, Q2]), "operationType" : NewBodyOperationType.REMOVE, "oppositeDirection" : true, "depth" : 25 * mm, "offsetDistance" : 25 * mm});
        }
        {
            var Q0;
            Q0=makeQuery(id+"F42.imprint","IMPRINT",FACE,{"disambiguationData":[TD([[makeQuery(id+"F42.imprint","IMPRINT",EDGE,{"derivedFrom":sQuery(id+"F42.wireOp",EDGE,"E106.1.0.8")}),1.0]])]});
            var Q1;
            Q1=makeQuery(id+"F42.imprint","IMPRINT",FACE,{"disambiguationData":[TD([[makeQuery(id+"F42.imprint","IMPRINT",EDGE,{"derivedFrom":sQuery(id+"F42.wireOp",EDGE,"E106.1.0.1")}),1.0]])]});
            var Q2;
            Q2=makeQuery(id+"F42.imprint","IMPRINT",FACE,{"disambiguationData":[TD([[makeQuery(id+"F42.imprint","IMPRINT",EDGE,{"derivedFrom":sQuery(id+"F42.wireOp",EDGE,"E106.1.0.0")}),1.0]])]});
            extrude(context, id + "F44", {"entities" : qUnion([Q0, Q1, Q2]), "operationType" : NewBodyOperationType.REMOVE, "oppositeDirection" : true, "depth" : 25 * mm, "offsetDistance" : 25 * mm});
        }
        {
            var Q0;
            Q0=makeQuery(id+"F42.imprint","IMPRINT",FACE,{"disambiguationData":[TD([[makeQuery(id+"F42.imprint","IMPRINT",EDGE,{"derivedFrom":sQuery(id+"F42.wireOp",EDGE,"E106.2.0.1")}),1.0]])]});
            var Q1;
            Q1=makeQuery(id+"F42.imprint","IMPRINT",FACE,{"disambiguationData":[TD([[makeQuery(id+"F42.imprint","IMPRINT",EDGE,{"derivedFrom":sQuery(id+"F42.wireOp",EDGE,"E106.2.0.8")}),1.0]])]});
            var Q2;
            Q2=makeQuery(id+"F42.imprint","IMPRINT",FACE,{"disambiguationData":[TD([[makeQuery(id+"F42.imprint","IMPRINT",EDGE,{"derivedFrom":sQuery(id+"F42.wireOp",EDGE,"E106.2.0.0")}),1.0]])]});
            extrude(context, id + "F45", {"entities" : qUnion([Q0, Q1, Q2]), "operationType" : NewBodyOperationType.REMOVE, "oppositeDirection" : true, "depth" : 25 * mm, "offsetDistance" : 25 * mm});
        }
        {
            var Q0;
            Q0=makeQuery(id+"F42.imprint","IMPRINT",FACE,{"disambiguationData":[TD([[makeQuery(id+"F42.imprint","IMPRINT",EDGE,{"derivedFrom":sQuery(id+"F42.wireOp",EDGE,"E106.3.0.8")}),1.0]])]});
            var Q1;
            Q1=makeQuery(id+"F42.imprint","IMPRINT",FACE,{"disambiguationData":[TD([[makeQuery(id+"F42.imprint","IMPRINT",EDGE,{"derivedFrom":sQuery(id+"F42.wireOp",EDGE,"E106.3.0.1")}),1.0]])]});
            var Q2;
            Q2=makeQuery(id+"F42.imprint","IMPRINT",FACE,{"disambiguationData":[TD([[makeQuery(id+"F42.imprint","IMPRINT",EDGE,{"derivedFrom":sQuery(id+"F42.wireOp",EDGE,"E106.3.0.0")}),1.0]])]});
            extrude(context, id + "F46", {"entities" : qUnion([Q0, Q1, Q2]), "operationType" : NewBodyOperationType.REMOVE, "oppositeDirection" : true, "depth" : 25 * mm, "offsetDistance" : 25 * mm});
        }
        {
            var Q0;
            Q0=makeQuery(id+"F42.imprint","IMPRINT",FACE,{"disambiguationData":[TD([[makeQuery(id+"F42.imprint","IMPRINT",EDGE,{"derivedFrom":sQuery(id+"F42.wireOp",EDGE,"E106.4.0.8")}),1.0]])]});
            var Q1;
            Q1=makeQuery(id+"F42.imprint","IMPRINT",FACE,{"disambiguationData":[TD([[makeQuery(id+"F42.imprint","IMPRINT",EDGE,{"derivedFrom":sQuery(id+"F42.wireOp",EDGE,"E106.4.0.1")}),1.0]])]});
            var Q2;
            Q2=makeQuery(id+"F42.imprint","IMPRINT",FACE,{"disambiguationData":[TD([[makeQuery(id+"F42.imprint","IMPRINT",EDGE,{"derivedFrom":sQuery(id+"F42.wireOp",EDGE,"E106.4.0.0")}),1.0]])]});
            extrude(context, id + "F47", {"entities" : qUnion([Q0, Q1, Q2]), "operationType" : NewBodyOperationType.REMOVE, "oppositeDirection" : true, "depth" : 25 * mm, "offsetDistance" : 25 * mm});
        }
        {
            var Q0;
            Q0=makeQuery(id+"F42.imprint","IMPRINT",FACE,{"disambiguationData":[TD([[makeQuery(id+"F42.imprint","IMPRINT",EDGE,{"derivedFrom":sQuery(id+"F42.wireOp",EDGE,"E106.5.0.8")}),1.0]])]});
            var Q1;
            Q1=makeQuery(id+"F42.imprint","IMPRINT",FACE,{"disambiguationData":[TD([[makeQuery(id+"F42.imprint","IMPRINT",EDGE,{"derivedFrom":sQuery(id+"F42.wireOp",EDGE,"E106.5.0.1")}),1.0]])]});
            var Q2;
            Q2=makeQuery(id+"F42.imprint","IMPRINT",FACE,{"disambiguationData":[TD([[makeQuery(id+"F42.imprint","IMPRINT",EDGE,{"derivedFrom":sQuery(id+"F42.wireOp",EDGE,"E106.6.0.1")}),1.0]])]});
            var Q3;
            Q3=makeQuery(id+"F42.imprint","IMPRINT",FACE,{"disambiguationData":[TD([[makeQuery(id+"F42.imprint","IMPRINT",EDGE,{"derivedFrom":sQuery(id+"F42.wireOp",EDGE,"E106.6.0.0")}),1.0]])]});
            var Q4;
            Q4=makeQuery(id+"F42.imprint","IMPRINT",FACE,{"disambiguationData":[TD([[makeQuery(id+"F42.imprint","IMPRINT",EDGE,{"derivedFrom":sQuery(id+"F42.wireOp",EDGE,"E106.5.0.0")}),1.0]])]});
            var Q5;
            Q5=makeQuery(id+"F42.imprint","IMPRINT",FACE,{"disambiguationData":[TD([[makeQuery(id+"F42.imprint","IMPRINT",EDGE,{"derivedFrom":sQuery(id+"F42.wireOp",EDGE,"E106.6.0.8")}),1.0]])]});
            extrude(context, id + "F48", {"entities" : qUnion([Q0, Q1, Q2, Q3, Q4, Q5]), "operationType" : NewBodyOperationType.REMOVE, "oppositeDirection" : true, "depth" : 25 * mm, "offsetDistance" : 25 * mm});
        }
        {
            var Q0;
            Q0=makeQuery(id+"F42.imprint","IMPRINT",FACE,{"disambiguationData":[TD([[makeQuery(id+"F42.imprint","IMPRINT",EDGE,{"derivedFrom":sQuery(id+"F42.wireOp",EDGE,"E106.7.0.8")}),1.0]])]});
            var Q1;
            Q1=makeQuery(id+"F42.imprint","IMPRINT",FACE,{"disambiguationData":[TD([[makeQuery(id+"F42.imprint","IMPRINT",EDGE,{"derivedFrom":sQuery(id+"F42.wireOp",EDGE,"E106.7.0.1")}),1.0]])]});
            var Q2;
            Q2=makeQuery(id+"F42.imprint","IMPRINT",FACE,{"disambiguationData":[TD([[makeQuery(id+"F42.imprint","IMPRINT",EDGE,{"derivedFrom":sQuery(id+"F42.wireOp",EDGE,"E106.8.0.1")}),1.0]])]});
            var Q3;
            Q3=makeQuery(id+"F42.imprint","IMPRINT",FACE,{"disambiguationData":[TD([[makeQuery(id+"F42.imprint","IMPRINT",EDGE,{"derivedFrom":sQuery(id+"F42.wireOp",EDGE,"E106.8.0.8")}),1.0]])]});
            var Q4;
            Q4=makeQuery(id+"F42.imprint","IMPRINT",FACE,{"disambiguationData":[TD([[makeQuery(id+"F42.imprint","IMPRINT",EDGE,{"derivedFrom":sQuery(id+"F42.wireOp",EDGE,"E106.8.0.0")}),1.0]])]});
            var Q5;
            Q5=makeQuery(id+"F42.imprint","IMPRINT",FACE,{"disambiguationData":[TD([[makeQuery(id+"F42.imprint","IMPRINT",EDGE,{"derivedFrom":sQuery(id+"F42.wireOp",EDGE,"E106.7.0.0")}),1.0]])]});
            extrude(context, id + "F49", {"entities" : qUnion([Q0, Q1, Q2, Q3, Q4, Q5]), "operationType" : NewBodyOperationType.REMOVE, "oppositeDirection" : true, "depth" : 25 * mm, "offsetDistance" : 25 * mm});
        }
        {
            var Q0;
            Q0=makeQuery(id+"F42.imprint","IMPRINT",FACE,{"disambiguationData":[TD([[makeQuery(id+"F42.imprint","IMPRINT",EDGE,{"derivedFrom":sQuery(id+"F42.wireOp",EDGE,"E106.9.0.1")}),1.0]])]});
            var Q1;
            Q1=makeQuery(id+"F42.imprint","IMPRINT",FACE,{"disambiguationData":[TD([[makeQuery(id+"F42.imprint","IMPRINT",EDGE,{"derivedFrom":sQuery(id+"F42.wireOp",EDGE,"E106.9.0.8")}),1.0]])]});
            var Q2;
            Q2=makeQuery(id+"F42.imprint","IMPRINT",FACE,{"disambiguationData":[TD([[makeQuery(id+"F42.imprint","IMPRINT",EDGE,{"derivedFrom":sQuery(id+"F42.wireOp",EDGE,"E106.9.0.0")}),1.0]])]});
            var Q3;
            Q3=makeQuery(id+"F42.imprint","IMPRINT",FACE,{"disambiguationData":[TD([[makeQuery(id+"F42.imprint","IMPRINT",EDGE,{"derivedFrom":sQuery(id+"F42.wireOp",EDGE,"E106.10.0.0")}),1.0]])]});
            var Q4;
            Q4=makeQuery(id+"F42.imprint","IMPRINT",FACE,{"disambiguationData":[TD([[makeQuery(id+"F42.imprint","IMPRINT",EDGE,{"derivedFrom":sQuery(id+"F42.wireOp",EDGE,"E106.10.0.8")}),1.0]])]});
            var Q5;
            Q5=makeQuery(id+"F42.imprint","IMPRINT",FACE,{"disambiguationData":[TD([[makeQuery(id+"F42.imprint","IMPRINT",EDGE,{"derivedFrom":sQuery(id+"F42.wireOp",EDGE,"E106.10.0.1")}),1.0]])]});
            extrude(context, id + "F50", {"entities" : qUnion([Q0, Q1, Q2, Q3, Q4, Q5]), "operationType" : NewBodyOperationType.REMOVE, "oppositeDirection" : true, "depth" : 25 * mm, "offsetDistance" : 25 * mm});
        }
        {
            var Q0;
            Q0=makeQuery(id+"F42.imprint","IMPRINT",FACE,{"disambiguationData":[TD([[makeQuery(id+"F42.imprint","IMPRINT",EDGE,{"derivedFrom":sQuery(id+"F42.wireOp",EDGE,"E106.11.0.8")}),1.0]])]});
            var Q1;
            Q1=makeQuery(id+"F42.imprint","IMPRINT",FACE,{"disambiguationData":[TD([[makeQuery(id+"F42.imprint","IMPRINT",EDGE,{"derivedFrom":sQuery(id+"F42.wireOp",EDGE,"E106.11.0.1")}),1.0]])]});
            var Q2;
            Q2=makeQuery(id+"F42.imprint","IMPRINT",FACE,{"disambiguationData":[TD([[makeQuery(id+"F42.imprint","IMPRINT",EDGE,{"derivedFrom":sQuery(id+"F42.wireOp",EDGE,"E106.12.0.1")}),1.0]])]});
            var Q3;
            Q3=makeQuery(id+"F42.imprint","IMPRINT",FACE,{"disambiguationData":[TD([[makeQuery(id+"F42.imprint","IMPRINT",EDGE,{"derivedFrom":sQuery(id+"F42.wireOp",EDGE,"E106.12.0.8")}),1.0]])]});
            var Q4;
            Q4=makeQuery(id+"F42.imprint","IMPRINT",FACE,{"disambiguationData":[TD([[makeQuery(id+"F42.imprint","IMPRINT",EDGE,{"derivedFrom":sQuery(id+"F42.wireOp",EDGE,"E106.12.0.0")}),1.0]])]});
            var Q5;
            Q5=makeQuery(id+"F42.imprint","IMPRINT",FACE,{"disambiguationData":[TD([[makeQuery(id+"F42.imprint","IMPRINT",EDGE,{"derivedFrom":sQuery(id+"F42.wireOp",EDGE,"E106.11.0.0")}),1.0]])]});
            extrude(context, id + "F51", {"entities" : qUnion([Q0, Q1, Q2, Q3, Q4, Q5]), "operationType" : NewBodyOperationType.REMOVE, "oppositeDirection" : true, "depth" : 25 * mm, "offsetDistance" : 25 * mm});
        }
        {
            var Q0;
            Q0=makeQuery(id+"F42.imprint","IMPRINT",FACE,{"disambiguationData":[TD([[makeQuery(id+"F42.imprint","IMPRINT",EDGE,{"derivedFrom":sQuery(id+"F42.wireOp",EDGE,"E106.13.0.8")}),1.0]])]});
            var Q1;
            Q1=makeQuery(id+"F42.imprint","IMPRINT",FACE,{"disambiguationData":[TD([[makeQuery(id+"F42.imprint","IMPRINT",EDGE,{"derivedFrom":sQuery(id+"F42.wireOp",EDGE,"E106.13.0.1")}),1.0]])]});
            var Q2;
            Q2=makeQuery(id+"F42.imprint","IMPRINT",FACE,{"disambiguationData":[TD([[makeQuery(id+"F42.imprint","IMPRINT",EDGE,{"derivedFrom":sQuery(id+"F42.wireOp",EDGE,"E106.13.0.0")}),1.0]])]});
            var Q3;
            Q3=makeQuery(id+"F42.imprint","IMPRINT",FACE,{"disambiguationData":[TD([[makeQuery(id+"F42.imprint","IMPRINT",EDGE,{"derivedFrom":sQuery(id+"F42.wireOp",EDGE,"E106.14.0.0")}),1.0]])]});
            var Q4;
            Q4=makeQuery(id+"F42.imprint","IMPRINT",FACE,{"disambiguationData":[TD([[makeQuery(id+"F42.imprint","IMPRINT",EDGE,{"derivedFrom":sQuery(id+"F42.wireOp",EDGE,"E106.14.0.8")}),1.0]])]});
            var Q5;
            Q5=makeQuery(id+"F42.imprint","IMPRINT",FACE,{"disambiguationData":[TD([[makeQuery(id+"F42.imprint","IMPRINT",EDGE,{"derivedFrom":sQuery(id+"F42.wireOp",EDGE,"E106.14.0.1")}),1.0]])]});
            extrude(context, id + "F52", {"entities" : qUnion([Q0, Q1, Q2, Q3, Q4, Q5]), "operationType" : NewBodyOperationType.REMOVE, "oppositeDirection" : true, "depth" : 25 * mm, "offsetDistance" : 25 * mm});
        }
        {
            var Q0;
            Q0=makeQuery(id+"F42.imprint","IMPRINT",FACE,{"disambiguationData":[TD([[makeQuery(id+"F42.imprint","IMPRINT",EDGE,{"derivedFrom":sQuery(id+"F42.wireOp",EDGE,"E106.15.0.1")}),1.0]])]});
            var Q1;
            Q1=makeQuery(id+"F42.imprint","IMPRINT",FACE,{"disambiguationData":[TD([[makeQuery(id+"F42.imprint","IMPRINT",EDGE,{"derivedFrom":sQuery(id+"F42.wireOp",EDGE,"E106.16.0.1")}),1.0]])]});
            var Q2;
            Q2=makeQuery(id+"F42.imprint","IMPRINT",FACE,{"disambiguationData":[TD([[makeQuery(id+"F42.imprint","IMPRINT",EDGE,{"derivedFrom":sQuery(id+"F42.wireOp",EDGE,"E106.16.0.8")}),1.0]])]});
            var Q3;
            Q3=makeQuery(id+"F42.imprint","IMPRINT",FACE,{"disambiguationData":[TD([[makeQuery(id+"F42.imprint","IMPRINT",EDGE,{"derivedFrom":sQuery(id+"F42.wireOp",EDGE,"E106.15.0.8")}),1.0]])]});
            var Q4;
            Q4=makeQuery(id+"F42.imprint","IMPRINT",FACE,{"disambiguationData":[TD([[makeQuery(id+"F42.imprint","IMPRINT",EDGE,{"derivedFrom":sQuery(id+"F42.wireOp",EDGE,"E106.15.0.0")}),1.0]])]});
            var Q5;
            Q5=makeQuery(id+"F42.imprint","IMPRINT",FACE,{"disambiguationData":[TD([[makeQuery(id+"F42.imprint","IMPRINT",EDGE,{"derivedFrom":sQuery(id+"F42.wireOp",EDGE,"E106.16.0.0")}),1.0]])]});
            extrude(context, id + "F53", {"entities" : qUnion([Q0, Q1, Q2, Q3, Q4, Q5]), "operationType" : NewBodyOperationType.REMOVE, "oppositeDirection" : true, "depth" : 25 * mm, "offsetDistance" : 25 * mm});
        }
        {
            var Q0;
            Q0=makeQuery(id+"F42.imprint","IMPRINT",FACE,{"disambiguationData":[TD([[makeQuery(id+"F42.imprint","IMPRINT",EDGE,{"derivedFrom":sQuery(id+"F42.wireOp",EDGE,"E106.20.0.8")}),1.0]])]});
            var Q1;
            Q1=makeQuery(id+"F42.imprint","IMPRINT",FACE,{"disambiguationData":[TD([[makeQuery(id+"F42.imprint","IMPRINT",EDGE,{"derivedFrom":sQuery(id+"F42.wireOp",EDGE,"E106.20.0.1")}),1.0]])]});
            var Q2;
            Q2=makeQuery(id+"F42.imprint","IMPRINT",FACE,{"disambiguationData":[TD([[makeQuery(id+"F42.imprint","IMPRINT",EDGE,{"derivedFrom":sQuery(id+"F42.wireOp",EDGE,"E106.17.0.0")}),1.0]])]});
            var Q3;
            Q3=makeQuery(id+"F42.imprint","IMPRINT",FACE,{"disambiguationData":[TD([[makeQuery(id+"F42.imprint","IMPRINT",EDGE,{"derivedFrom":sQuery(id+"F42.wireOp",EDGE,"E106.20.0.0")}),1.0]])]});
            var Q4;
            Q4=makeQuery(id+"F42.imprint","IMPRINT",FACE,{"disambiguationData":[TD([[makeQuery(id+"F42.imprint","IMPRINT",EDGE,{"derivedFrom":sQuery(id+"F42.wireOp",EDGE,"E106.19.0.8")}),1.0]])]});
            var Q5;
            Q5=makeQuery(id+"F42.imprint","IMPRINT",FACE,{"disambiguationData":[TD([[makeQuery(id+"F42.imprint","IMPRINT",EDGE,{"derivedFrom":sQuery(id+"F42.wireOp",EDGE,"E106.17.0.8")}),1.0]])]});
            var Q6;
            Q6=makeQuery(id+"F42.imprint","IMPRINT",FACE,{"disambiguationData":[TD([[makeQuery(id+"F42.imprint","IMPRINT",EDGE,{"derivedFrom":sQuery(id+"F42.wireOp",EDGE,"E106.17.0.1")}),1.0]])]});
            var Q7;
            Q7=makeQuery(id+"F42.imprint","IMPRINT",FACE,{"disambiguationData":[TD([[makeQuery(id+"F42.imprint","IMPRINT",EDGE,{"derivedFrom":sQuery(id+"F42.wireOp",EDGE,"E106.18.0.0")}),1.0]])]});
            var Q8;
            Q8=makeQuery(id+"F42.imprint","IMPRINT",FACE,{"disambiguationData":[TD([[makeQuery(id+"F42.imprint","IMPRINT",EDGE,{"derivedFrom":sQuery(id+"F42.wireOp",EDGE,"E106.18.0.8")}),1.0]])]});
            var Q9;
            Q9=makeQuery(id+"F42.imprint","IMPRINT",FACE,{"disambiguationData":[TD([[makeQuery(id+"F42.imprint","IMPRINT",EDGE,{"derivedFrom":sQuery(id+"F42.wireOp",EDGE,"E106.18.0.1")}),1.0]])]});
            var Q10;
            Q10=makeQuery(id+"F42.imprint","IMPRINT",FACE,{"disambiguationData":[TD([[makeQuery(id+"F42.imprint","IMPRINT",EDGE,{"derivedFrom":sQuery(id+"F42.wireOp",EDGE,"E106.19.0.1")}),1.0]])]});
            var Q11;
            Q11=makeQuery(id+"F42.imprint","IMPRINT",FACE,{"disambiguationData":[TD([[makeQuery(id+"F42.imprint","IMPRINT",EDGE,{"derivedFrom":sQuery(id+"F42.wireOp",EDGE,"E106.19.0.0")}),1.0]])]});
            extrude(context, id + "F54", {"entities" : qUnion([Q0, Q1, Q2, Q3, Q4, Q5, Q6, Q7, Q8, Q9, Q10, Q11]), "operationType" : NewBodyOperationType.REMOVE, "oppositeDirection" : true, "depth" : 25 * mm, "offsetDistance" : 25 * mm});
        }
        {
            var Q0;
            Q0=makeQuery(id+"F42.imprint","IMPRINT",FACE,{"disambiguationData":[TD([[makeQuery(id+"F42.imprint","IMPRINT",EDGE,{"derivedFrom":sQuery(id+"F42.wireOp",EDGE,"E106.21.0.8")}),1.0]])]});
            var Q1;
            Q1=makeQuery(id+"F42.imprint","IMPRINT",FACE,{"disambiguationData":[TD([[makeQuery(id+"F42.imprint","IMPRINT",EDGE,{"derivedFrom":sQuery(id+"F42.wireOp",EDGE,"E106.22.0.1")}),1.0]])]});
            var Q2;
            Q2=makeQuery(id+"F42.imprint","IMPRINT",FACE,{"disambiguationData":[TD([[makeQuery(id+"F42.imprint","IMPRINT",EDGE,{"derivedFrom":sQuery(id+"F42.wireOp",EDGE,"E106.22.0.0")}),1.0]])]});
            var Q3;
            Q3=makeQuery(id+"F42.imprint","IMPRINT",FACE,{"disambiguationData":[TD([[makeQuery(id+"F42.imprint","IMPRINT",EDGE,{"derivedFrom":sQuery(id+"F42.wireOp",EDGE,"E106.23.0.0")}),1.0]])]});
            var Q4;
            Q4=makeQuery(id+"F42.imprint","IMPRINT",FACE,{"disambiguationData":[TD([[makeQuery(id+"F42.imprint","IMPRINT",EDGE,{"derivedFrom":sQuery(id+"F42.wireOp",EDGE,"E106.22.0.8")}),1.0]])]});
            var Q5;
            Q5=makeQuery(id+"F42.imprint","IMPRINT",FACE,{"disambiguationData":[TD([[makeQuery(id+"F42.imprint","IMPRINT",EDGE,{"derivedFrom":sQuery(id+"F42.wireOp",EDGE,"E106.23.0.1")}),1.0]])]});
            var Q6;
            Q6=makeQuery(id+"F42.imprint","IMPRINT",FACE,{"disambiguationData":[TD([[makeQuery(id+"F42.imprint","IMPRINT",EDGE,{"derivedFrom":sQuery(id+"F42.wireOp",EDGE,"E106.24.0.0")}),1.0]])]});
            var Q7;
            Q7=makeQuery(id+"F42.imprint","IMPRINT",FACE,{"disambiguationData":[TD([[makeQuery(id+"F42.imprint","IMPRINT",EDGE,{"derivedFrom":sQuery(id+"F42.wireOp",EDGE,"E106.23.0.8")}),1.0]])]});
            var Q8;
            Q8=makeQuery(id+"F42.imprint","IMPRINT",FACE,{"disambiguationData":[TD([[makeQuery(id+"F42.imprint","IMPRINT",EDGE,{"derivedFrom":sQuery(id+"F42.wireOp",EDGE,"E106.24.0.8")}),1.0]])]});
            var Q9;
            Q9=makeQuery(id+"F42.imprint","IMPRINT",FACE,{"disambiguationData":[TD([[makeQuery(id+"F42.imprint","IMPRINT",EDGE,{"derivedFrom":sQuery(id+"F42.wireOp",EDGE,"E106.24.0.1")}),1.0]])]});
            var Q10;
            Q10=makeQuery(id+"F42.imprint","IMPRINT",FACE,{"disambiguationData":[TD([[makeQuery(id+"F42.imprint","IMPRINT",EDGE,{"derivedFrom":sQuery(id+"F42.wireOp",EDGE,"E106.21.0.1")}),1.0]])]});
            var Q11;
            Q11=makeQuery(id+"F42.imprint","IMPRINT",FACE,{"disambiguationData":[TD([[makeQuery(id+"F42.imprint","IMPRINT",EDGE,{"derivedFrom":sQuery(id+"F42.wireOp",EDGE,"E106.21.0.0")}),1.0]])]});
            extrude(context, id + "F55", {"entities" : qUnion([Q0, Q1, Q2, Q3, Q4, Q5, Q6, Q7, Q8, Q9, Q10, Q11]), "operationType" : NewBodyOperationType.REMOVE, "oppositeDirection" : true, "depth" : 25 * mm, "offsetDistance" : 25 * mm});
        }
        {
            var Q0;
            Q0=makeQuery(id+"F42.imprint","IMPRINT",FACE,{"disambiguationData":[TD([[makeQuery(id+"F42.imprint","IMPRINT",EDGE,{"derivedFrom":sQuery(id+"F42.wireOp",EDGE,"E106.26.0.0")}),1.0]])]});
            var Q1;
            Q1=makeQuery(id+"F42.imprint","IMPRINT",FACE,{"disambiguationData":[TD([[makeQuery(id+"F42.imprint","IMPRINT",EDGE,{"derivedFrom":sQuery(id+"F42.wireOp",EDGE,"E106.25.0.8")}),1.0]])]});
            var Q2;
            Q2=makeQuery(id+"F42.imprint","IMPRINT",FACE,{"disambiguationData":[TD([[makeQuery(id+"F42.imprint","IMPRINT",EDGE,{"derivedFrom":sQuery(id+"F42.wireOp",EDGE,"E106.27.0.0")}),1.0]])]});
            var Q3;
            Q3=makeQuery(id+"F42.imprint","IMPRINT",FACE,{"disambiguationData":[TD([[makeQuery(id+"F42.imprint","IMPRINT",EDGE,{"derivedFrom":sQuery(id+"F42.wireOp",EDGE,"E106.26.0.8")}),1.0]])]});
            var Q4;
            Q4=makeQuery(id+"F42.imprint","IMPRINT",FACE,{"disambiguationData":[TD([[makeQuery(id+"F42.imprint","IMPRINT",EDGE,{"derivedFrom":sQuery(id+"F42.wireOp",EDGE,"E106.27.0.8")}),1.0]])]});
            var Q5;
            Q5=makeQuery(id+"F42.imprint","IMPRINT",FACE,{"disambiguationData":[TD([[makeQuery(id+"F42.imprint","IMPRINT",EDGE,{"derivedFrom":sQuery(id+"F42.wireOp",EDGE,"E106.27.0.1")}),1.0]])]});
            var Q6;
            Q6=makeQuery(id+"F42.imprint","IMPRINT",FACE,{"disambiguationData":[TD([[makeQuery(id+"F42.imprint","IMPRINT",EDGE,{"derivedFrom":sQuery(id+"F42.wireOp",EDGE,"E106.26.0.1")}),1.0]])]});
            var Q7;
            Q7=makeQuery(id+"F42.imprint","IMPRINT",FACE,{"disambiguationData":[TD([[makeQuery(id+"F42.imprint","IMPRINT",EDGE,{"derivedFrom":sQuery(id+"F42.wireOp",EDGE,"E106.28.0.1")}),1.0]])]});
            var Q8;
            Q8=makeQuery(id+"F42.imprint","IMPRINT",FACE,{"disambiguationData":[TD([[makeQuery(id+"F42.imprint","IMPRINT",EDGE,{"derivedFrom":sQuery(id+"F42.wireOp",EDGE,"E106.28.0.0")}),1.0]])]});
            var Q9;
            Q9=makeQuery(id+"F42.imprint","IMPRINT",FACE,{"disambiguationData":[TD([[makeQuery(id+"F42.imprint","IMPRINT",EDGE,{"derivedFrom":sQuery(id+"F42.wireOp",EDGE,"E106.28.0.8")}),1.0]])]});
            var Q10;
            Q10=makeQuery(id+"F42.imprint","IMPRINT",FACE,{"disambiguationData":[TD([[makeQuery(id+"F42.imprint","IMPRINT",EDGE,{"derivedFrom":sQuery(id+"F42.wireOp",EDGE,"E106.25.0.1")}),1.0]])]});
            var Q11;
            Q11=makeQuery(id+"F42.imprint","IMPRINT",FACE,{"disambiguationData":[TD([[makeQuery(id+"F42.imprint","IMPRINT",EDGE,{"derivedFrom":sQuery(id+"F42.wireOp",EDGE,"E106.25.0.0")}),1.0]])]});
            extrude(context, id + "F56", {"entities" : qUnion([Q0, Q1, Q2, Q3, Q4, Q5, Q6, Q7, Q8, Q9, Q10, Q11]), "operationType" : NewBodyOperationType.REMOVE, "oppositeDirection" : true, "depth" : 25 * mm, "offsetDistance" : 25 * mm});
        }
        {
            var Q0;
            Q0=makeQuery(id+"F42.imprint","IMPRINT",FACE,{"disambiguationData":[TD([[makeQuery(id+"F42.imprint","IMPRINT",EDGE,{"derivedFrom":sQuery(id+"F42.wireOp",EDGE,"E106.31.0.1")}),1.0]])]});
            var Q1;
            Q1=makeQuery(id+"F42.imprint","IMPRINT",FACE,{"disambiguationData":[TD([[makeQuery(id+"F42.imprint","IMPRINT",EDGE,{"derivedFrom":sQuery(id+"F42.wireOp",EDGE,"E106.31.0.0")}),1.0]])]});
            var Q2;
            Q2=makeQuery(id+"F42.imprint","IMPRINT",FACE,{"disambiguationData":[TD([[makeQuery(id+"F42.imprint","IMPRINT",EDGE,{"derivedFrom":sQuery(id+"F42.wireOp",EDGE,"E106.32.0.1")}),1.0]])]});
            var Q3;
            Q3=makeQuery(id+"F42.imprint","IMPRINT",FACE,{"disambiguationData":[TD([[makeQuery(id+"F42.imprint","IMPRINT",EDGE,{"derivedFrom":sQuery(id+"F42.wireOp",EDGE,"E106.32.0.0")}),1.0]])]});
            var Q4;
            Q4=makeQuery(id+"F42.imprint","IMPRINT",FACE,{"disambiguationData":[TD([[makeQuery(id+"F42.imprint","IMPRINT",EDGE,{"derivedFrom":sQuery(id+"F42.wireOp",EDGE,"E106.32.0.8")}),1.0]])]});
            var Q5;
            Q5=makeQuery(id+"F42.imprint","IMPRINT",FACE,{"disambiguationData":[TD([[makeQuery(id+"F42.imprint","IMPRINT",EDGE,{"derivedFrom":sQuery(id+"F42.wireOp",EDGE,"E106.31.0.8")}),1.0]])]});
            var Q6;
            Q6=makeQuery(id+"F42.imprint","IMPRINT",FACE,{"disambiguationData":[TD([[makeQuery(id+"F42.imprint","IMPRINT",EDGE,{"derivedFrom":sQuery(id+"F42.wireOp",EDGE,"E106.30.0.8")}),1.0]])]});
            var Q7;
            Q7=makeQuery(id+"F42.imprint","IMPRINT",FACE,{"disambiguationData":[TD([[makeQuery(id+"F42.imprint","IMPRINT",EDGE,{"derivedFrom":sQuery(id+"F42.wireOp",EDGE,"E106.30.0.1")}),1.0]])]});
            var Q8;
            Q8=makeQuery(id+"F42.imprint","IMPRINT",FACE,{"disambiguationData":[TD([[makeQuery(id+"F42.imprint","IMPRINT",EDGE,{"derivedFrom":sQuery(id+"F42.wireOp",EDGE,"E106.30.0.0")}),1.0]])]});
            var Q9;
            Q9=makeQuery(id+"F42.imprint","IMPRINT",FACE,{"disambiguationData":[TD([[makeQuery(id+"F42.imprint","IMPRINT",EDGE,{"derivedFrom":sQuery(id+"F42.wireOp",EDGE,"E106.29.0.8")}),1.0]])]});
            var Q10;
            Q10=makeQuery(id+"F42.imprint","IMPRINT",FACE,{"disambiguationData":[TD([[makeQuery(id+"F42.imprint","IMPRINT",EDGE,{"derivedFrom":sQuery(id+"F42.wireOp",EDGE,"E106.29.0.1")}),1.0]])]});
            var Q11;
            Q11=makeQuery(id+"F42.imprint","IMPRINT",FACE,{"disambiguationData":[TD([[makeQuery(id+"F42.imprint","IMPRINT",EDGE,{"derivedFrom":sQuery(id+"F42.wireOp",EDGE,"E106.29.0.0")}),1.0]])]});
            extrude(context, id + "F57", {"entities" : qUnion([Q0, Q1, Q2, Q3, Q4, Q5, Q6, Q7, Q8, Q9, Q10, Q11]), "operationType" : NewBodyOperationType.REMOVE, "oppositeDirection" : true, "depth" : 25 * mm, "offsetDistance" : 25 * mm});
        }
        {
            var Q0;
            Q0=makeQuery(id+"F42.imprint","IMPRINT",FACE,{"disambiguationData":[TD([[makeQuery(id+"F42.imprint","IMPRINT",EDGE,{"derivedFrom":sQuery(id+"F42.wireOp",EDGE,"E106.36.0.8")}),1.0]])]});
            var Q1;
            Q1=makeQuery(id+"F42.imprint","IMPRINT",FACE,{"disambiguationData":[TD([[makeQuery(id+"F42.imprint","IMPRINT",EDGE,{"derivedFrom":sQuery(id+"F42.wireOp",EDGE,"E106.36.0.1")}),1.0]])]});
            var Q2;
            Q2=makeQuery(id+"F42.imprint","IMPRINT",FACE,{"disambiguationData":[TD([[makeQuery(id+"F42.imprint","IMPRINT",EDGE,{"derivedFrom":sQuery(id+"F42.wireOp",EDGE,"E106.36.0.0")}),1.0]])]});
            var Q3;
            Q3=makeQuery(id+"F42.imprint","IMPRINT",FACE,{"disambiguationData":[TD([[makeQuery(id+"F42.imprint","IMPRINT",EDGE,{"derivedFrom":sQuery(id+"F42.wireOp",EDGE,"E106.35.0.8")}),1.0]])]});
            var Q4;
            Q4=makeQuery(id+"F42.imprint","IMPRINT",FACE,{"disambiguationData":[TD([[makeQuery(id+"F42.imprint","IMPRINT",EDGE,{"derivedFrom":sQuery(id+"F42.wireOp",EDGE,"E106.33.0.8")}),1.0]])]});
            var Q5;
            Q5=makeQuery(id+"F42.imprint","IMPRINT",FACE,{"disambiguationData":[TD([[makeQuery(id+"F42.imprint","IMPRINT",EDGE,{"derivedFrom":sQuery(id+"F42.wireOp",EDGE,"E106.34.0.0")}),1.0]])]});
            var Q6;
            Q6=makeQuery(id+"F42.imprint","IMPRINT",FACE,{"disambiguationData":[TD([[makeQuery(id+"F42.imprint","IMPRINT",EDGE,{"derivedFrom":sQuery(id+"F42.wireOp",EDGE,"E106.34.0.8")}),1.0]])]});
            var Q7;
            Q7=makeQuery(id+"F42.imprint","IMPRINT",FACE,{"disambiguationData":[TD([[makeQuery(id+"F42.imprint","IMPRINT",EDGE,{"derivedFrom":sQuery(id+"F42.wireOp",EDGE,"E106.34.0.1")}),1.0]])]});
            var Q8;
            Q8=makeQuery(id+"F42.imprint","IMPRINT",FACE,{"disambiguationData":[TD([[makeQuery(id+"F42.imprint","IMPRINT",EDGE,{"derivedFrom":sQuery(id+"F42.wireOp",EDGE,"E106.35.0.1")}),1.0]])]});
            var Q9;
            Q9=makeQuery(id+"F42.imprint","IMPRINT",FACE,{"disambiguationData":[TD([[makeQuery(id+"F42.imprint","IMPRINT",EDGE,{"derivedFrom":sQuery(id+"F42.wireOp",EDGE,"E106.35.0.0")}),1.0]])]});
            var Q10;
            Q10=makeQuery(id+"F42.imprint","IMPRINT",FACE,{"disambiguationData":[TD([[makeQuery(id+"F42.imprint","IMPRINT",EDGE,{"derivedFrom":sQuery(id+"F42.wireOp",EDGE,"E106.33.0.0")}),1.0]])]});
            var Q11;
            Q11=makeQuery(id+"F42.imprint","IMPRINT",FACE,{"disambiguationData":[TD([[makeQuery(id+"F42.imprint","IMPRINT",EDGE,{"derivedFrom":sQuery(id+"F42.wireOp",EDGE,"E106.33.0.1")}),1.0]])]});
            extrude(context, id + "F58", {"entities" : qUnion([Q0, Q1, Q2, Q3, Q4, Q5, Q6, Q7, Q8, Q9, Q10, Q11]), "operationType" : NewBodyOperationType.REMOVE, "oppositeDirection" : true, "depth" : 25 * mm, "offsetDistance" : 25 * mm});
        }
        {
            var Q0;
            Q0=makeQuery(id+"F42.imprint","IMPRINT",FACE,{"disambiguationData":[TD([[makeQuery(id+"F42.imprint","IMPRINT",EDGE,{"derivedFrom":sQuery(id+"F42.wireOp",EDGE,"E106.37.0.8")}),1.0]])]});
            var Q1;
            Q1=makeQuery(id+"F42.imprint","IMPRINT",FACE,{"disambiguationData":[TD([[makeQuery(id+"F42.imprint","IMPRINT",EDGE,{"derivedFrom":sQuery(id+"F42.wireOp",EDGE,"E106.38.0.1")}),1.0]])]});
            var Q2;
            Q2=makeQuery(id+"F42.imprint","IMPRINT",FACE,{"disambiguationData":[TD([[makeQuery(id+"F42.imprint","IMPRINT",EDGE,{"derivedFrom":sQuery(id+"F42.wireOp",EDGE,"E106.38.0.0")}),1.0]])]});
            var Q3;
            Q3=makeQuery(id+"F42.imprint","IMPRINT",FACE,{"disambiguationData":[TD([[makeQuery(id+"F42.imprint","IMPRINT",EDGE,{"derivedFrom":sQuery(id+"F42.wireOp",EDGE,"E106.39.0.0")}),1.0]])]});
            var Q4;
            Q4=makeQuery(id+"F42.imprint","IMPRINT",FACE,{"disambiguationData":[TD([[makeQuery(id+"F42.imprint","IMPRINT",EDGE,{"derivedFrom":sQuery(id+"F42.wireOp",EDGE,"E106.38.0.8")}),1.0]])]});
            var Q5;
            Q5=makeQuery(id+"F42.imprint","IMPRINT",FACE,{"disambiguationData":[TD([[makeQuery(id+"F42.imprint","IMPRINT",EDGE,{"derivedFrom":sQuery(id+"F42.wireOp",EDGE,"E106.39.0.1")}),1.0]])]});
            var Q6;
            Q6=makeQuery(id+"F42.imprint","IMPRINT",FACE,{"disambiguationData":[TD([[makeQuery(id+"F42.imprint","IMPRINT",EDGE,{"derivedFrom":sQuery(id+"F42.wireOp",EDGE,"E106.40.0.0")}),1.0]])]});
            var Q7;
            Q7=makeQuery(id+"F42.imprint","IMPRINT",FACE,{"disambiguationData":[TD([[makeQuery(id+"F42.imprint","IMPRINT",EDGE,{"derivedFrom":sQuery(id+"F42.wireOp",EDGE,"E106.39.0.8")}),1.0]])]});
            var Q8;
            Q8=makeQuery(id+"F42.imprint","IMPRINT",FACE,{"disambiguationData":[TD([[makeQuery(id+"F42.imprint","IMPRINT",EDGE,{"derivedFrom":sQuery(id+"F42.wireOp",EDGE,"E106.40.0.8")}),1.0]])]});
            var Q9;
            Q9=makeQuery(id+"F42.imprint","IMPRINT",FACE,{"disambiguationData":[TD([[makeQuery(id+"F42.imprint","IMPRINT",EDGE,{"derivedFrom":sQuery(id+"F42.wireOp",EDGE,"E106.40.0.1")}),1.0]])]});
            var Q10;
            Q10=makeQuery(id+"F42.imprint","IMPRINT",FACE,{"disambiguationData":[TD([[makeQuery(id+"F42.imprint","IMPRINT",EDGE,{"derivedFrom":sQuery(id+"F42.wireOp",EDGE,"E106.37.0.1")}),1.0]])]});
            var Q11;
            Q11=makeQuery(id+"F42.imprint","IMPRINT",FACE,{"disambiguationData":[TD([[makeQuery(id+"F42.imprint","IMPRINT",EDGE,{"derivedFrom":sQuery(id+"F42.wireOp",EDGE,"E106.37.0.0")}),1.0]])]});
            extrude(context, id + "F59", {"entities" : qUnion([Q0, Q1, Q2, Q3, Q4, Q5, Q6, Q7, Q8, Q9, Q10, Q11]), "operationType" : NewBodyOperationType.REMOVE, "oppositeDirection" : true, "depth" : 25 * mm, "offsetDistance" : 25 * mm});
        }
        {
            var Q0;
            Q0=makeQuery(id+"F42.imprint","IMPRINT",FACE,{"disambiguationData":[TD([[makeQuery(id+"F42.imprint","IMPRINT",EDGE,{"derivedFrom":sQuery(id+"F42.wireOp",EDGE,"E106.41.0.8")}),1.0]])]});
            var Q1;
            Q1=makeQuery(id+"F42.imprint","IMPRINT",FACE,{"disambiguationData":[TD([[makeQuery(id+"F42.imprint","IMPRINT",EDGE,{"derivedFrom":sQuery(id+"F42.wireOp",EDGE,"E106.42.0.8")}),1.0]])]});
            var Q2;
            Q2=makeQuery(id+"F42.imprint","IMPRINT",FACE,{"disambiguationData":[TD([[makeQuery(id+"F42.imprint","IMPRINT",EDGE,{"derivedFrom":sQuery(id+"F42.wireOp",EDGE,"E106.43.0.8")}),1.0]])]});
            var Q3;
            Q3=makeQuery(id+"F42.imprint","IMPRINT",FACE,{"disambiguationData":[TD([[makeQuery(id+"F42.imprint","IMPRINT",EDGE,{"derivedFrom":sQuery(id+"F42.wireOp",EDGE,"E106.44.0.8")}),1.0]])]});
            var Q4;
            Q4=makeQuery(id+"F42.imprint","IMPRINT",FACE,{"disambiguationData":[TD([[makeQuery(id+"F42.imprint","IMPRINT",EDGE,{"derivedFrom":sQuery(id+"F42.wireOp",EDGE,"E106.42.0.0")}),1.0]])]});
            var Q5;
            Q5=makeQuery(id+"F42.imprint","IMPRINT",FACE,{"disambiguationData":[TD([[makeQuery(id+"F42.imprint","IMPRINT",EDGE,{"derivedFrom":sQuery(id+"F42.wireOp",EDGE,"E106.43.0.0")}),1.0]])]});
            var Q6;
            Q6=makeQuery(id+"F42.imprint","IMPRINT",FACE,{"disambiguationData":[TD([[makeQuery(id+"F42.imprint","IMPRINT",EDGE,{"derivedFrom":sQuery(id+"F42.wireOp",EDGE,"E106.44.0.0")}),1.0]])]});
            var Q7;
            Q7=makeQuery(id+"F42.imprint","IMPRINT",FACE,{"disambiguationData":[TD([[makeQuery(id+"F42.imprint","IMPRINT",EDGE,{"derivedFrom":sQuery(id+"F42.wireOp",EDGE,"E106.43.0.1")}),1.0]])]});
            var Q8;
            Q8=makeQuery(id+"F42.imprint","IMPRINT",FACE,{"disambiguationData":[TD([[makeQuery(id+"F42.imprint","IMPRINT",EDGE,{"derivedFrom":sQuery(id+"F42.wireOp",EDGE,"E106.42.0.1")}),1.0]])]});
            var Q9;
            Q9=makeQuery(id+"F42.imprint","IMPRINT",FACE,{"disambiguationData":[TD([[makeQuery(id+"F42.imprint","IMPRINT",EDGE,{"derivedFrom":sQuery(id+"F42.wireOp",EDGE,"E106.44.0.1")}),1.0]])]});
            var Q10;
            Q10=makeQuery(id+"F42.imprint","IMPRINT",FACE,{"disambiguationData":[TD([[makeQuery(id+"F42.imprint","IMPRINT",EDGE,{"derivedFrom":sQuery(id+"F42.wireOp",EDGE,"E106.41.0.1")}),1.0]])]});
            var Q11;
            Q11=makeQuery(id+"F42.imprint","IMPRINT",FACE,{"disambiguationData":[TD([[makeQuery(id+"F42.imprint","IMPRINT",EDGE,{"derivedFrom":sQuery(id+"F42.wireOp",EDGE,"E106.41.0.0")}),1.0]])]});
            extrude(context, id + "F60", {"entities" : qUnion([Q0, Q1, Q2, Q3, Q4, Q5, Q6, Q7, Q8, Q9, Q10, Q11]), "operationType" : NewBodyOperationType.REMOVE, "oppositeDirection" : true, "depth" : 25 * mm, "offsetDistance" : 25 * mm});
        }
        {
            var Q0;
            Q0=makeQuery(id+"F42.imprint","IMPRINT",FACE,{"disambiguationData":[TD([[makeQuery(id+"F42.imprint","IMPRINT",EDGE,{"derivedFrom":sQuery(id+"F42.wireOp",EDGE,"E106.47.0.0")}),1.0]])]});
            var Q1;
            Q1=makeQuery(id+"F42.imprint","IMPRINT",FACE,{"disambiguationData":[TD([[makeQuery(id+"F42.imprint","IMPRINT",EDGE,{"derivedFrom":sQuery(id+"F42.wireOp",EDGE,"E106.48.0.0")}),1.0]])]});
            var Q2;
            Q2=makeQuery(id+"F42.imprint","IMPRINT",FACE,{"disambiguationData":[TD([[makeQuery(id+"F42.imprint","IMPRINT",EDGE,{"derivedFrom":sQuery(id+"F42.wireOp",EDGE,"E106.48.0.8")}),1.0]])]});
            var Q3;
            Q3=makeQuery(id+"F42.imprint","IMPRINT",FACE,{"disambiguationData":[TD([[makeQuery(id+"F42.imprint","IMPRINT",EDGE,{"derivedFrom":sQuery(id+"F42.wireOp",EDGE,"E106.47.0.8")}),1.0]])]});
            var Q4;
            Q4=makeQuery(id+"F42.imprint","IMPRINT",FACE,{"disambiguationData":[TD([[makeQuery(id+"F42.imprint","IMPRINT",EDGE,{"derivedFrom":sQuery(id+"F42.wireOp",EDGE,"E106.46.0.8")}),1.0]])]});
            var Q5;
            Q5=makeQuery(id+"F42.imprint","IMPRINT",FACE,{"disambiguationData":[TD([[makeQuery(id+"F42.imprint","IMPRINT",EDGE,{"derivedFrom":sQuery(id+"F42.wireOp",EDGE,"E106.46.0.0")}),1.0]])]});
            var Q6;
            Q6=makeQuery(id+"F42.imprint","IMPRINT",FACE,{"disambiguationData":[TD([[makeQuery(id+"F42.imprint","IMPRINT",EDGE,{"derivedFrom":sQuery(id+"F42.wireOp",EDGE,"E106.45.0.8")}),1.0]])]});
            var Q7;
            Q7=makeQuery(id+"F42.imprint","IMPRINT",FACE,{"disambiguationData":[TD([[makeQuery(id+"F42.imprint","IMPRINT",EDGE,{"derivedFrom":sQuery(id+"F42.wireOp",EDGE,"E106.47.0.1")}),1.0]])]});
            var Q8;
            Q8=makeQuery(id+"F42.imprint","IMPRINT",FACE,{"disambiguationData":[TD([[makeQuery(id+"F42.imprint","IMPRINT",EDGE,{"derivedFrom":sQuery(id+"F42.wireOp",EDGE,"E106.48.0.1")}),1.0]])]});
            var Q9;
            Q9=makeQuery(id+"F42.imprint","IMPRINT",FACE,{"disambiguationData":[TD([[makeQuery(id+"F42.imprint","IMPRINT",EDGE,{"derivedFrom":sQuery(id+"F42.wireOp",EDGE,"E106.46.0.1")}),1.0]])]});
            var Q10;
            Q10=makeQuery(id+"F42.imprint","IMPRINT",FACE,{"disambiguationData":[TD([[makeQuery(id+"F42.imprint","IMPRINT",EDGE,{"derivedFrom":sQuery(id+"F42.wireOp",EDGE,"E106.45.0.0")}),1.0]])]});
            var Q11;
            Q11=makeQuery(id+"F42.imprint","IMPRINT",FACE,{"disambiguationData":[TD([[makeQuery(id+"F42.imprint","IMPRINT",EDGE,{"derivedFrom":sQuery(id+"F42.wireOp",EDGE,"E106.45.0.1")}),1.0]])]});
            extrude(context, id + "F61", {"entities" : qUnion([Q0, Q1, Q2, Q3, Q4, Q5, Q6, Q7, Q8, Q9, Q10, Q11]), "operationType" : NewBodyOperationType.REMOVE, "oppositeDirection" : true, "depth" : 25 * mm, "offsetDistance" : 25 * mm});
        }
    });
